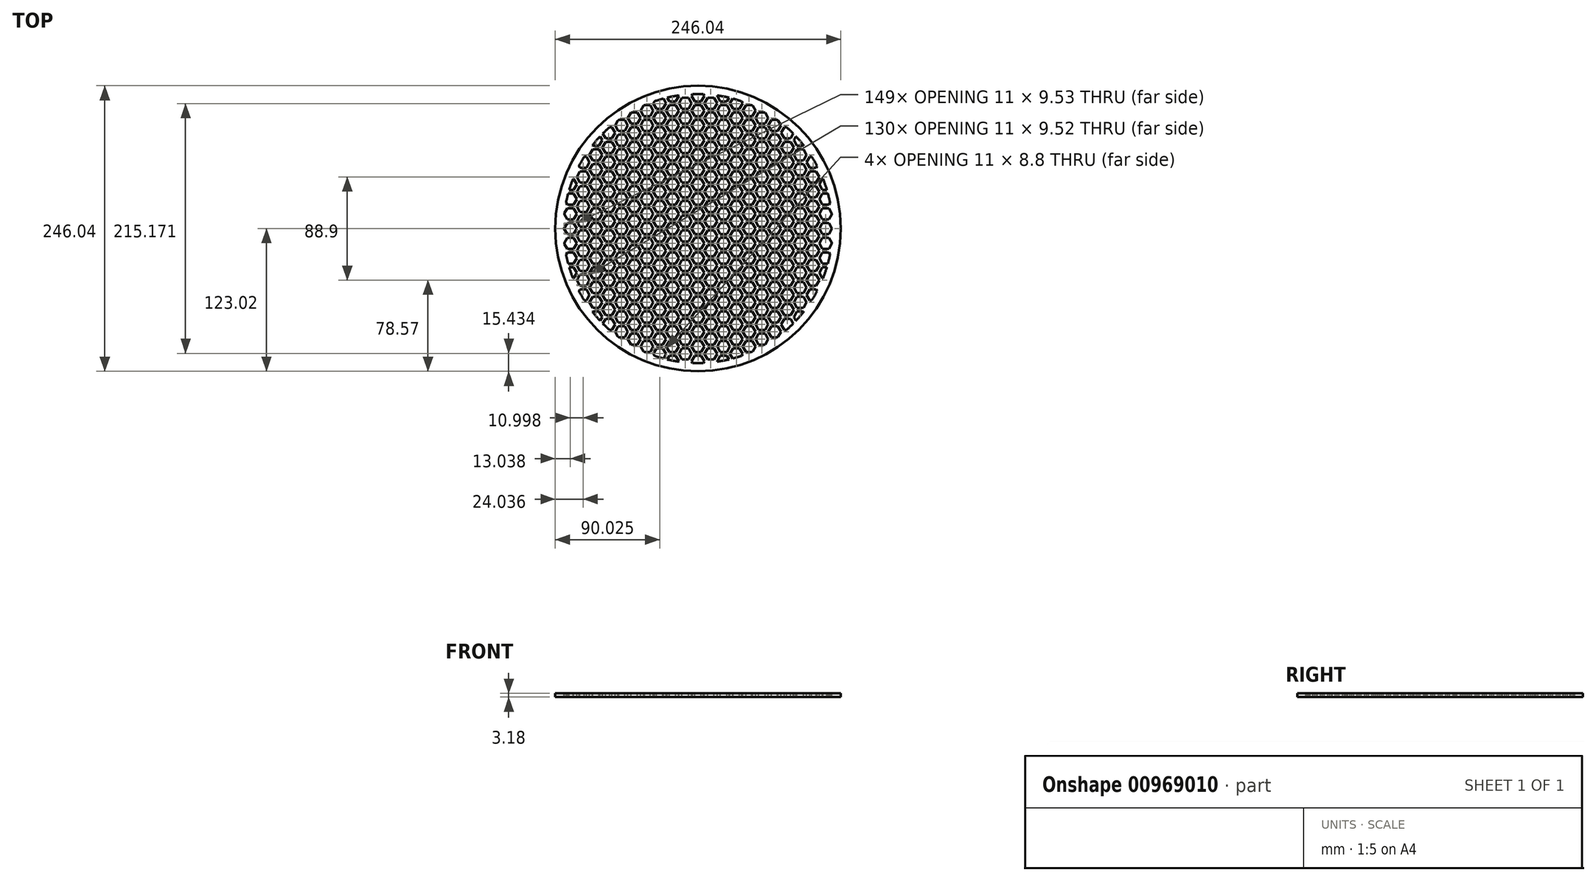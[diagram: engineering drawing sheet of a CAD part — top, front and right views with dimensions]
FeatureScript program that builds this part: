
annotation { "Feature Type Name" : "Feature", "Feature Type Description" : "" }
export const myFeature = defineFeature(function(context is Context, id is Id, definition is map)
    precondition{}
    {
        {
            var Q0;
            Q0=qCreatedBy(makeId("Top.planeOp"),FACE);
            var sketch = newSketch(context, id + "F0", { "sketchPlane" : qUnion([Q0])});
            skCircle(sketch, "E0", {"center": v(0, 0) * mm, "radius": 123.02 * mm});
            skSolve(sketch);
        }
        {
            var Q0;
            Q0=qSketchRegion(id+"F0",true);
            extrude(context, id + "F1", {"entities" : qUnion([Q0]), "depth" : 3.17 * mm, "offsetDistance" : 25.4 * mm});
        }
        {
            var Q0;
            Q0=makeQuery(id+"F1.opExtrude","CAP_FACE",FACE,{"disambiguationData":[OSD([sQuery(id+"F0.wireOp",EDGE,"E0")])],"isStart":false});
            var sketch = newSketch(context, id + "F2", { "sketchPlane" : qUnion([Q0])});
            skCircle(sketch, "E1.cCircle", {"center": v(-120.98, -120.65) * mm, "radius": 4.76 * mm, "construction": true});
            skLineSegment(sketch, "E1.0", {"start": v(-123.73, -115.89) * mm, "end": v(-118.23, -115.89) * mm});
            skLineSegment(sketch, "E1.1", {"start": v(-118.23, -115.89) * mm, "end": v(-115.48, -120.65) * mm});
            skLineSegment(sketch, "E1.2", {"start": v(-115.48, -120.65) * mm, "end": v(-118.23, -125.41) * mm});
            skLineSegment(sketch, "E1.3", {"start": v(-118.23, -125.41) * mm, "end": v(-123.73, -125.41) * mm});
            skLineSegment(sketch, "E1.4", {"start": v(-123.73, -125.41) * mm, "end": v(-126.48, -120.65) * mm});
            skLineSegment(sketch, "E1.5", {"start": v(-126.48, -120.65) * mm, "end": v(-123.73, -115.89) * mm});
            skPoint(sketch, "E1.0.midPoint", {"position": v(-120.98, -115.89) * mm});
            skCircle(sketch, "E2.cCircle", {"center": v(-109.98, -114.3) * mm, "radius": 4.76 * mm, "construction": true});
            skLineSegment(sketch, "E2.0", {"start": v(-112.73, -109.54) * mm, "end": v(-107.23, -109.54) * mm});
            skLineSegment(sketch, "E2.1", {"start": v(-107.23, -109.54) * mm, "end": v(-104.48, -114.3) * mm});
            skLineSegment(sketch, "E2.2", {"start": v(-104.48, -114.3) * mm, "end": v(-107.23, -119.06) * mm});
            skLineSegment(sketch, "E2.3", {"start": v(-107.23, -119.06) * mm, "end": v(-112.73, -119.06) * mm});
            skLineSegment(sketch, "E2.4", {"start": v(-112.73, -119.06) * mm, "end": v(-115.48, -114.3) * mm});
            skLineSegment(sketch, "E2.5", {"start": v(-115.48, -114.3) * mm, "end": v(-112.73, -109.54) * mm});
            skPoint(sketch, "E2.0.midPoint", {"position": v(-109.98, -109.54) * mm});
            skLineSegment(sketch, "E3.0.1.0", {"start": v(-123.73, -103.19) * mm, "end": v(-118.23, -103.19) * mm});
            skLineSegment(sketch, "E3.0.1.1", {"start": v(-118.23, -103.19) * mm, "end": v(-115.48, -107.95) * mm});
            skLineSegment(sketch, "E3.0.1.2", {"start": v(-115.48, -107.95) * mm, "end": v(-118.23, -112.71) * mm});
            skCircle(sketch, "E3.0.1.3", {"center": v(-120.98, -107.95) * mm, "radius": 4.76 * mm, "construction": true});
            skLineSegment(sketch, "E3.0.1.4", {"start": v(-118.23, -112.71) * mm, "end": v(-123.73, -112.71) * mm});
            skLineSegment(sketch, "E3.0.1.5", {"start": v(-123.73, -112.71) * mm, "end": v(-126.48, -107.95) * mm});
            skLineSegment(sketch, "E3.0.1.6", {"start": v(-126.48, -107.95) * mm, "end": v(-123.73, -103.19) * mm});
            skLineSegment(sketch, "E3.0.2.0", {"start": v(-123.73, -90.49) * mm, "end": v(-118.23, -90.49) * mm});
            skLineSegment(sketch, "E3.0.2.1", {"start": v(-118.23, -90.49) * mm, "end": v(-115.48, -95.25) * mm});
            skLineSegment(sketch, "E3.0.2.2", {"start": v(-115.48, -95.25) * mm, "end": v(-118.23, -100.01) * mm});
            skCircle(sketch, "E3.0.2.3", {"center": v(-120.98, -95.25) * mm, "radius": 4.76 * mm, "construction": true});
            skLineSegment(sketch, "E3.0.2.4", {"start": v(-118.23, -100.01) * mm, "end": v(-123.73, -100.01) * mm});
            skLineSegment(sketch, "E3.0.2.5", {"start": v(-123.73, -100.01) * mm, "end": v(-126.48, -95.25) * mm});
            skLineSegment(sketch, "E3.0.2.6", {"start": v(-126.48, -95.25) * mm, "end": v(-123.73, -90.49) * mm});
            skLineSegment(sketch, "E3.1.0.0", {"start": v(-101.73, -115.89) * mm, "end": v(-96.23, -115.89) * mm});
            skLineSegment(sketch, "E3.1.0.1", {"start": v(-96.23, -115.89) * mm, "end": v(-93.48, -120.65) * mm});
            skLineSegment(sketch, "E3.1.0.2", {"start": v(-93.48, -120.65) * mm, "end": v(-96.23, -125.41) * mm});
            skCircle(sketch, "E3.1.0.3", {"center": v(-98.98, -120.65) * mm, "radius": 4.76 * mm, "construction": true});
            skLineSegment(sketch, "E3.1.0.4", {"start": v(-96.23, -125.41) * mm, "end": v(-101.73, -125.41) * mm});
            skLineSegment(sketch, "E3.1.0.5", {"start": v(-101.73, -125.41) * mm, "end": v(-104.48, -120.65) * mm});
            skLineSegment(sketch, "E3.1.0.6", {"start": v(-104.48, -120.65) * mm, "end": v(-101.73, -115.89) * mm});
            skLineSegment(sketch, "E3.1.1.0", {"start": v(-101.73, -103.19) * mm, "end": v(-96.23, -103.19) * mm});
            skLineSegment(sketch, "E3.1.1.1", {"start": v(-96.23, -103.19) * mm, "end": v(-93.48, -107.95) * mm});
            skLineSegment(sketch, "E3.1.1.2", {"start": v(-93.48, -107.95) * mm, "end": v(-96.23, -112.71) * mm});
            skCircle(sketch, "E3.1.1.3", {"center": v(-98.98, -107.95) * mm, "radius": 4.76 * mm, "construction": true});
            skLineSegment(sketch, "E3.1.1.4", {"start": v(-96.23, -112.71) * mm, "end": v(-101.73, -112.71) * mm});
            skLineSegment(sketch, "E3.1.1.5", {"start": v(-101.73, -112.71) * mm, "end": v(-104.48, -107.95) * mm});
            skLineSegment(sketch, "E3.1.1.6", {"start": v(-104.48, -107.95) * mm, "end": v(-101.73, -103.19) * mm});
            skLineSegment(sketch, "E3.1.2.0", {"start": v(-101.73, -90.49) * mm, "end": v(-96.23, -90.49) * mm});
            skLineSegment(sketch, "E3.1.2.1", {"start": v(-96.23, -90.49) * mm, "end": v(-93.48, -95.25) * mm});
            skLineSegment(sketch, "E3.1.2.2", {"start": v(-93.48, -95.25) * mm, "end": v(-96.23, -100.01) * mm});
            skCircle(sketch, "E3.1.2.3", {"center": v(-98.98, -95.25) * mm, "radius": 4.76 * mm, "construction": true});
            skLineSegment(sketch, "E3.1.2.4", {"start": v(-96.23, -100.01) * mm, "end": v(-101.73, -100.01) * mm});
            skLineSegment(sketch, "E3.1.2.5", {"start": v(-101.73, -100.01) * mm, "end": v(-104.48, -95.25) * mm});
            skLineSegment(sketch, "E3.1.2.6", {"start": v(-104.48, -95.25) * mm, "end": v(-101.73, -90.49) * mm});
            skLineSegment(sketch, "E3.2.0.0", {"start": v(-79.74, -115.89) * mm, "end": v(-74.24, -115.89) * mm});
            skLineSegment(sketch, "E3.2.0.1", {"start": v(-74.24, -115.89) * mm, "end": v(-71.49, -120.65) * mm});
            skLineSegment(sketch, "E3.2.0.2", {"start": v(-71.49, -120.65) * mm, "end": v(-74.24, -125.41) * mm});
            skCircle(sketch, "E3.2.0.3", {"center": v(-76.99, -120.65) * mm, "radius": 4.76 * mm, "construction": true});
            skLineSegment(sketch, "E3.2.0.4", {"start": v(-74.24, -125.41) * mm, "end": v(-79.74, -125.41) * mm});
            skLineSegment(sketch, "E3.2.0.5", {"start": v(-79.74, -125.41) * mm, "end": v(-82.49, -120.65) * mm});
            skLineSegment(sketch, "E3.2.0.6", {"start": v(-82.49, -120.65) * mm, "end": v(-79.74, -115.89) * mm});
            skLineSegment(sketch, "E3.2.1.0", {"start": v(-79.74, -103.19) * mm, "end": v(-74.24, -103.19) * mm});
            skLineSegment(sketch, "E3.2.1.1", {"start": v(-74.24, -103.19) * mm, "end": v(-71.49, -107.95) * mm});
            skLineSegment(sketch, "E3.2.1.2", {"start": v(-71.49, -107.95) * mm, "end": v(-74.24, -112.71) * mm});
            skCircle(sketch, "E3.2.1.3", {"center": v(-76.99, -107.95) * mm, "radius": 4.76 * mm, "construction": true});
            skLineSegment(sketch, "E3.2.1.4", {"start": v(-74.24, -112.71) * mm, "end": v(-79.74, -112.71) * mm});
            skLineSegment(sketch, "E3.2.1.5", {"start": v(-79.74, -112.71) * mm, "end": v(-82.49, -107.95) * mm});
            skLineSegment(sketch, "E3.2.1.6", {"start": v(-82.49, -107.95) * mm, "end": v(-79.74, -103.19) * mm});
            skLineSegment(sketch, "E3.2.2.0", {"start": v(-79.74, -90.49) * mm, "end": v(-74.24, -90.49) * mm});
            skLineSegment(sketch, "E3.2.2.1", {"start": v(-74.24, -90.49) * mm, "end": v(-71.49, -95.25) * mm});
            skLineSegment(sketch, "E3.2.2.2", {"start": v(-71.49, -95.25) * mm, "end": v(-74.24, -100.01) * mm});
            skCircle(sketch, "E3.2.2.3", {"center": v(-76.99, -95.25) * mm, "radius": 4.76 * mm, "construction": true});
            skLineSegment(sketch, "E3.2.2.4", {"start": v(-74.24, -100.01) * mm, "end": v(-79.74, -100.01) * mm});
            skLineSegment(sketch, "E3.2.2.5", {"start": v(-79.74, -100.01) * mm, "end": v(-82.49, -95.25) * mm});
            skLineSegment(sketch, "E3.2.2.6", {"start": v(-82.49, -95.25) * mm, "end": v(-79.74, -90.49) * mm});
            skLineSegment(sketch, "E3.direction1", {"start": v(-123.73, -125.41) * mm, "end": v(-101.73, -125.41) * mm, "construction": true});
            skLineSegment(sketch, "E3.direction2", {"start": v(-123.73, -125.41) * mm, "end": v(-123.73, -112.71) * mm, "construction": true});
            skLineSegment(sketch, "E4.0.0.3", {"start": v(-123.73, -77.79) * mm, "end": v(-118.23, -77.79) * mm});
            skLineSegment(sketch, "E4.3.0.3", {"start": v(-118.23, -77.79) * mm, "end": v(-115.48, -82.55) * mm});
            skLineSegment(sketch, "E4.6.0.3", {"start": v(-115.48, -82.55) * mm, "end": v(-118.23, -87.31) * mm});
            skCircle(sketch, "E4.9.0.3", {"center": v(-120.98, -82.55) * mm, "radius": 4.76 * mm, "construction": true});
            skLineSegment(sketch, "E4.11.0.3", {"start": v(-118.23, -87.31) * mm, "end": v(-123.73, -87.31) * mm});
            skLineSegment(sketch, "E4.14.0.3", {"start": v(-123.73, -87.31) * mm, "end": v(-126.48, -82.55) * mm});
            skLineSegment(sketch, "E4.17.0.3", {"start": v(-126.48, -82.55) * mm, "end": v(-123.73, -77.79) * mm});
            skLineSegment(sketch, "E4.0.1.3", {"start": v(-101.73, -77.79) * mm, "end": v(-96.23, -77.79) * mm});
            skLineSegment(sketch, "E4.3.1.3", {"start": v(-96.23, -77.79) * mm, "end": v(-93.48, -82.55) * mm});
            skLineSegment(sketch, "E4.6.1.3", {"start": v(-93.48, -82.55) * mm, "end": v(-96.23, -87.31) * mm});
            skCircle(sketch, "E4.9.1.3", {"center": v(-98.98, -82.55) * mm, "radius": 4.76 * mm, "construction": true});
            skLineSegment(sketch, "E4.11.1.3", {"start": v(-96.23, -87.31) * mm, "end": v(-101.73, -87.31) * mm});
            skLineSegment(sketch, "E4.14.1.3", {"start": v(-101.73, -87.31) * mm, "end": v(-104.48, -82.55) * mm});
            skLineSegment(sketch, "E4.17.1.3", {"start": v(-104.48, -82.55) * mm, "end": v(-101.73, -77.79) * mm});
            skLineSegment(sketch, "E4.0.2.3", {"start": v(-79.74, -77.79) * mm, "end": v(-74.24, -77.79) * mm});
            skLineSegment(sketch, "E4.3.2.3", {"start": v(-74.24, -77.79) * mm, "end": v(-71.49, -82.55) * mm});
            skLineSegment(sketch, "E4.6.2.3", {"start": v(-71.49, -82.55) * mm, "end": v(-74.24, -87.31) * mm});
            skCircle(sketch, "E4.9.2.3", {"center": v(-76.99, -82.55) * mm, "radius": 4.76 * mm, "construction": true});
            skLineSegment(sketch, "E4.11.2.3", {"start": v(-74.24, -87.31) * mm, "end": v(-79.74, -87.31) * mm});
            skLineSegment(sketch, "E4.14.2.3", {"start": v(-79.74, -87.31) * mm, "end": v(-82.49, -82.55) * mm});
            skLineSegment(sketch, "E4.17.2.3", {"start": v(-82.49, -82.55) * mm, "end": v(-79.74, -77.79) * mm});
            skCircle(sketch, "E5.0.1.0", {"center": v(-109.98, -101.6) * mm, "radius": 4.76 * mm, "construction": true});
            skLineSegment(sketch, "E5.0.1.1", {"start": v(-115.48, -101.6) * mm, "end": v(-112.73, -96.84) * mm});
            skLineSegment(sketch, "E5.0.1.2", {"start": v(-112.73, -96.84) * mm, "end": v(-107.23, -96.84) * mm});
            skLineSegment(sketch, "E5.0.1.3", {"start": v(-107.23, -96.84) * mm, "end": v(-104.48, -101.6) * mm});
            skLineSegment(sketch, "E5.0.1.4", {"start": v(-104.48, -101.6) * mm, "end": v(-107.23, -106.36) * mm});
            skLineSegment(sketch, "E5.0.1.5", {"start": v(-107.23, -106.36) * mm, "end": v(-112.73, -106.36) * mm});
            skLineSegment(sketch, "E5.0.1.6", {"start": v(-112.73, -106.36) * mm, "end": v(-115.48, -101.6) * mm});
            skCircle(sketch, "E5.0.2.0", {"center": v(-109.98, -88.9) * mm, "radius": 4.76 * mm, "construction": true});
            skLineSegment(sketch, "E5.0.2.1", {"start": v(-115.48, -88.9) * mm, "end": v(-112.73, -84.14) * mm});
            skLineSegment(sketch, "E5.0.2.2", {"start": v(-112.73, -84.14) * mm, "end": v(-107.23, -84.14) * mm});
            skLineSegment(sketch, "E5.0.2.3", {"start": v(-107.23, -84.14) * mm, "end": v(-104.48, -88.9) * mm});
            skLineSegment(sketch, "E5.0.2.4", {"start": v(-104.48, -88.9) * mm, "end": v(-107.23, -93.66) * mm});
            skLineSegment(sketch, "E5.0.2.5", {"start": v(-107.23, -93.66) * mm, "end": v(-112.73, -93.66) * mm});
            skLineSegment(sketch, "E5.0.2.6", {"start": v(-112.73, -93.66) * mm, "end": v(-115.48, -88.9) * mm});
            skCircle(sketch, "E5.0.3.0", {"center": v(-109.98, -76.2) * mm, "radius": 4.76 * mm, "construction": true});
            skLineSegment(sketch, "E5.0.3.1", {"start": v(-115.48, -76.2) * mm, "end": v(-112.73, -71.44) * mm});
            skLineSegment(sketch, "E5.0.3.2", {"start": v(-112.73, -71.44) * mm, "end": v(-107.23, -71.44) * mm});
            skLineSegment(sketch, "E5.0.3.3", {"start": v(-107.23, -71.44) * mm, "end": v(-104.48, -76.2) * mm});
            skLineSegment(sketch, "E5.0.3.4", {"start": v(-104.48, -76.2) * mm, "end": v(-107.23, -80.96) * mm});
            skLineSegment(sketch, "E5.0.3.5", {"start": v(-107.23, -80.96) * mm, "end": v(-112.73, -80.96) * mm});
            skLineSegment(sketch, "E5.0.3.6", {"start": v(-112.73, -80.96) * mm, "end": v(-115.48, -76.2) * mm});
            skCircle(sketch, "E5.1.0.0", {"center": v(-87.99, -114.3) * mm, "radius": 4.76 * mm, "construction": true});
            skLineSegment(sketch, "E5.1.0.1", {"start": v(-93.48, -114.3) * mm, "end": v(-90.74, -109.54) * mm});
            skLineSegment(sketch, "E5.1.0.2", {"start": v(-90.74, -109.54) * mm, "end": v(-85.24, -109.54) * mm});
            skLineSegment(sketch, "E5.1.0.3", {"start": v(-85.24, -109.54) * mm, "end": v(-82.49, -114.3) * mm});
            skLineSegment(sketch, "E5.1.0.4", {"start": v(-82.49, -114.3) * mm, "end": v(-85.24, -119.06) * mm});
            skLineSegment(sketch, "E5.1.0.5", {"start": v(-85.24, -119.06) * mm, "end": v(-90.74, -119.06) * mm});
            skLineSegment(sketch, "E5.1.0.6", {"start": v(-90.74, -119.06) * mm, "end": v(-93.48, -114.3) * mm});
            skCircle(sketch, "E5.1.1.0", {"center": v(-87.99, -101.6) * mm, "radius": 4.76 * mm, "construction": true});
            skLineSegment(sketch, "E5.1.1.1", {"start": v(-93.48, -101.6) * mm, "end": v(-90.74, -96.84) * mm});
            skLineSegment(sketch, "E5.1.1.2", {"start": v(-90.74, -96.84) * mm, "end": v(-85.24, -96.84) * mm});
            skLineSegment(sketch, "E5.1.1.3", {"start": v(-85.24, -96.84) * mm, "end": v(-82.49, -101.6) * mm});
            skLineSegment(sketch, "E5.1.1.4", {"start": v(-82.49, -101.6) * mm, "end": v(-85.24, -106.36) * mm});
            skLineSegment(sketch, "E5.1.1.5", {"start": v(-85.24, -106.36) * mm, "end": v(-90.74, -106.36) * mm});
            skLineSegment(sketch, "E5.1.1.6", {"start": v(-90.74, -106.36) * mm, "end": v(-93.48, -101.6) * mm});
            skCircle(sketch, "E5.1.2.0", {"center": v(-87.99, -88.9) * mm, "radius": 4.76 * mm, "construction": true});
            skLineSegment(sketch, "E5.1.2.1", {"start": v(-93.48, -88.9) * mm, "end": v(-90.74, -84.14) * mm});
            skLineSegment(sketch, "E5.1.2.2", {"start": v(-90.74, -84.14) * mm, "end": v(-85.24, -84.14) * mm});
            skLineSegment(sketch, "E5.1.2.3", {"start": v(-85.24, -84.14) * mm, "end": v(-82.49, -88.9) * mm});
            skLineSegment(sketch, "E5.1.2.4", {"start": v(-82.49, -88.9) * mm, "end": v(-85.24, -93.66) * mm});
            skLineSegment(sketch, "E5.1.2.5", {"start": v(-85.24, -93.66) * mm, "end": v(-90.74, -93.66) * mm});
            skLineSegment(sketch, "E5.1.2.6", {"start": v(-90.74, -93.66) * mm, "end": v(-93.48, -88.9) * mm});
            skCircle(sketch, "E5.1.3.0", {"center": v(-87.99, -76.2) * mm, "radius": 4.76 * mm, "construction": true});
            skLineSegment(sketch, "E5.1.3.1", {"start": v(-93.48, -76.2) * mm, "end": v(-90.74, -71.44) * mm});
            skLineSegment(sketch, "E5.1.3.2", {"start": v(-90.74, -71.44) * mm, "end": v(-85.24, -71.44) * mm});
            skLineSegment(sketch, "E5.1.3.3", {"start": v(-85.24, -71.44) * mm, "end": v(-82.49, -76.2) * mm});
            skLineSegment(sketch, "E5.1.3.4", {"start": v(-82.49, -76.2) * mm, "end": v(-85.24, -80.96) * mm});
            skLineSegment(sketch, "E5.1.3.5", {"start": v(-85.24, -80.96) * mm, "end": v(-90.74, -80.96) * mm});
            skLineSegment(sketch, "E5.1.3.6", {"start": v(-90.74, -80.96) * mm, "end": v(-93.48, -76.2) * mm});
            skLineSegment(sketch, "E5.direction1", {"start": v(-112.73, -119.06) * mm, "end": v(-90.74, -119.06) * mm, "construction": true});
            skLineSegment(sketch, "E5.direction2", {"start": v(-112.73, -119.06) * mm, "end": v(-112.73, -106.36) * mm, "construction": true});
            skLineSegment(sketch, "E6.0.3.0", {"start": v(-57.74, -115.89) * mm, "end": v(-52.24, -115.89) * mm});
            skLineSegment(sketch, "E6.3.3.0", {"start": v(-52.24, -115.89) * mm, "end": v(-49.5, -120.65) * mm});
            skLineSegment(sketch, "E6.6.3.0", {"start": v(-49.5, -120.65) * mm, "end": v(-52.24, -125.41) * mm});
            skCircle(sketch, "E6.9.3.0", {"center": v(-55, -120.65) * mm, "radius": 4.76 * mm, "construction": true});
            skLineSegment(sketch, "E6.11.3.0", {"start": v(-52.24, -125.41) * mm, "end": v(-57.74, -125.41) * mm});
            skLineSegment(sketch, "E6.14.3.0", {"start": v(-57.74, -125.41) * mm, "end": v(-60.5, -120.65) * mm});
            skLineSegment(sketch, "E6.17.3.0", {"start": v(-60.5, -120.65) * mm, "end": v(-57.74, -115.89) * mm});
            skLineSegment(sketch, "E6.0.3.1", {"start": v(-57.74, -103.19) * mm, "end": v(-52.24, -103.19) * mm});
            skLineSegment(sketch, "E6.3.3.1", {"start": v(-52.24, -103.19) * mm, "end": v(-49.5, -107.95) * mm});
            skLineSegment(sketch, "E6.6.3.1", {"start": v(-49.5, -107.95) * mm, "end": v(-52.24, -112.71) * mm});
            skCircle(sketch, "E6.9.3.1", {"center": v(-55, -107.95) * mm, "radius": 4.76 * mm, "construction": true});
            skLineSegment(sketch, "E6.11.3.1", {"start": v(-52.24, -112.71) * mm, "end": v(-57.74, -112.71) * mm});
            skLineSegment(sketch, "E6.14.3.1", {"start": v(-57.74, -112.71) * mm, "end": v(-60.5, -107.95) * mm});
            skLineSegment(sketch, "E6.17.3.1", {"start": v(-60.5, -107.95) * mm, "end": v(-57.74, -103.19) * mm});
            skLineSegment(sketch, "E6.0.3.2", {"start": v(-57.74, -90.49) * mm, "end": v(-52.24, -90.49) * mm});
            skLineSegment(sketch, "E6.3.3.2", {"start": v(-52.24, -90.49) * mm, "end": v(-49.5, -95.25) * mm});
            skLineSegment(sketch, "E6.6.3.2", {"start": v(-49.5, -95.25) * mm, "end": v(-52.24, -100.01) * mm});
            skCircle(sketch, "E6.9.3.2", {"center": v(-55, -95.25) * mm, "radius": 4.76 * mm, "construction": true});
            skLineSegment(sketch, "E6.11.3.2", {"start": v(-52.24, -100.01) * mm, "end": v(-57.74, -100.01) * mm});
            skLineSegment(sketch, "E6.14.3.2", {"start": v(-57.74, -100.01) * mm, "end": v(-60.5, -95.25) * mm});
            skLineSegment(sketch, "E6.17.3.2", {"start": v(-60.5, -95.25) * mm, "end": v(-57.74, -90.49) * mm});
            skLineSegment(sketch, "E6.0.3.3", {"start": v(-57.74, -77.79) * mm, "end": v(-52.24, -77.79) * mm});
            skLineSegment(sketch, "E6.3.3.3", {"start": v(-52.24, -77.79) * mm, "end": v(-49.5, -82.55) * mm});
            skLineSegment(sketch, "E6.6.3.3", {"start": v(-49.5, -82.55) * mm, "end": v(-52.24, -87.31) * mm});
            skCircle(sketch, "E6.9.3.3", {"center": v(-55, -82.55) * mm, "radius": 4.76 * mm, "construction": true});
            skLineSegment(sketch, "E6.11.3.3", {"start": v(-52.24, -87.31) * mm, "end": v(-57.74, -87.31) * mm});
            skLineSegment(sketch, "E6.14.3.3", {"start": v(-57.74, -87.31) * mm, "end": v(-60.5, -82.55) * mm});
            skLineSegment(sketch, "E6.17.3.3", {"start": v(-60.5, -82.55) * mm, "end": v(-57.74, -77.79) * mm});
            skLineSegment(sketch, "E6.0.4.0", {"start": v(-35.74, -115.89) * mm, "end": v(-30.25, -115.89) * mm});
            skLineSegment(sketch, "E6.3.4.0", {"start": v(-30.25, -115.89) * mm, "end": v(-27.5, -120.65) * mm});
            skLineSegment(sketch, "E6.6.4.0", {"start": v(-27.5, -120.65) * mm, "end": v(-30.25, -125.41) * mm});
            skCircle(sketch, "E6.9.4.0", {"center": v(-33, -120.65) * mm, "radius": 4.76 * mm, "construction": true});
            skLineSegment(sketch, "E6.11.4.0", {"start": v(-30.25, -125.41) * mm, "end": v(-35.74, -125.41) * mm});
            skLineSegment(sketch, "E6.14.4.0", {"start": v(-35.74, -125.41) * mm, "end": v(-38.5, -120.65) * mm});
            skLineSegment(sketch, "E6.17.4.0", {"start": v(-38.5, -120.65) * mm, "end": v(-35.74, -115.89) * mm});
            skLineSegment(sketch, "E6.0.4.1", {"start": v(-35.74, -103.19) * mm, "end": v(-30.25, -103.19) * mm});
            skLineSegment(sketch, "E6.3.4.1", {"start": v(-30.25, -103.19) * mm, "end": v(-27.5, -107.95) * mm});
            skLineSegment(sketch, "E6.6.4.1", {"start": v(-27.5, -107.95) * mm, "end": v(-30.25, -112.71) * mm});
            skCircle(sketch, "E6.9.4.1", {"center": v(-33, -107.95) * mm, "radius": 4.76 * mm, "construction": true});
            skLineSegment(sketch, "E6.11.4.1", {"start": v(-30.25, -112.71) * mm, "end": v(-35.74, -112.71) * mm});
            skLineSegment(sketch, "E6.14.4.1", {"start": v(-35.74, -112.71) * mm, "end": v(-38.5, -107.95) * mm});
            skLineSegment(sketch, "E6.17.4.1", {"start": v(-38.5, -107.95) * mm, "end": v(-35.74, -103.19) * mm});
            skLineSegment(sketch, "E6.0.4.2", {"start": v(-35.74, -90.49) * mm, "end": v(-30.25, -90.49) * mm});
            skLineSegment(sketch, "E6.3.4.2", {"start": v(-30.25, -90.49) * mm, "end": v(-27.5, -95.25) * mm});
            skLineSegment(sketch, "E6.6.4.2", {"start": v(-27.5, -95.25) * mm, "end": v(-30.25, -100.01) * mm});
            skCircle(sketch, "E6.9.4.2", {"center": v(-33, -95.25) * mm, "radius": 4.76 * mm, "construction": true});
            skLineSegment(sketch, "E6.11.4.2", {"start": v(-30.25, -100.01) * mm, "end": v(-35.74, -100.01) * mm});
            skLineSegment(sketch, "E6.14.4.2", {"start": v(-35.74, -100.01) * mm, "end": v(-38.5, -95.25) * mm});
            skLineSegment(sketch, "E6.17.4.2", {"start": v(-38.5, -95.25) * mm, "end": v(-35.74, -90.49) * mm});
            skLineSegment(sketch, "E6.0.4.3", {"start": v(-35.74, -77.79) * mm, "end": v(-30.25, -77.79) * mm});
            skLineSegment(sketch, "E6.3.4.3", {"start": v(-30.25, -77.79) * mm, "end": v(-27.5, -82.55) * mm});
            skLineSegment(sketch, "E6.6.4.3", {"start": v(-27.5, -82.55) * mm, "end": v(-30.25, -87.31) * mm});
            skCircle(sketch, "E6.9.4.3", {"center": v(-33, -82.55) * mm, "radius": 4.76 * mm, "construction": true});
            skLineSegment(sketch, "E6.11.4.3", {"start": v(-30.25, -87.31) * mm, "end": v(-35.74, -87.31) * mm});
            skLineSegment(sketch, "E6.14.4.3", {"start": v(-35.74, -87.31) * mm, "end": v(-38.5, -82.55) * mm});
            skLineSegment(sketch, "E6.17.4.3", {"start": v(-38.5, -82.55) * mm, "end": v(-35.74, -77.79) * mm});
            skLineSegment(sketch, "E6.0.5.0", {"start": v(-13.75, -115.89) * mm, "end": v(-8.25, -115.89) * mm});
            skLineSegment(sketch, "E6.3.5.0", {"start": v(-8.25, -115.89) * mm, "end": v(-5.5, -120.65) * mm});
            skLineSegment(sketch, "E6.6.5.0", {"start": v(-5.5, -120.65) * mm, "end": v(-8.25, -125.41) * mm});
            skCircle(sketch, "E6.9.5.0", {"center": v(-11, -120.65) * mm, "radius": 4.76 * mm, "construction": true});
            skLineSegment(sketch, "E6.11.5.0", {"start": v(-8.25, -125.41) * mm, "end": v(-13.75, -125.41) * mm});
            skLineSegment(sketch, "E6.14.5.0", {"start": v(-13.75, -125.41) * mm, "end": v(-16.5, -120.65) * mm});
            skLineSegment(sketch, "E6.17.5.0", {"start": v(-16.5, -120.65) * mm, "end": v(-13.75, -115.89) * mm});
            skLineSegment(sketch, "E6.0.5.1", {"start": v(-13.75, -103.19) * mm, "end": v(-8.25, -103.19) * mm});
            skLineSegment(sketch, "E6.3.5.1", {"start": v(-8.25, -103.19) * mm, "end": v(-5.5, -107.95) * mm});
            skLineSegment(sketch, "E6.6.5.1", {"start": v(-5.5, -107.95) * mm, "end": v(-8.25, -112.71) * mm});
            skCircle(sketch, "E6.9.5.1", {"center": v(-11, -107.95) * mm, "radius": 4.76 * mm, "construction": true});
            skLineSegment(sketch, "E6.11.5.1", {"start": v(-8.25, -112.71) * mm, "end": v(-13.75, -112.71) * mm});
            skLineSegment(sketch, "E6.14.5.1", {"start": v(-13.75, -112.71) * mm, "end": v(-16.5, -107.95) * mm});
            skLineSegment(sketch, "E6.17.5.1", {"start": v(-16.5, -107.95) * mm, "end": v(-13.75, -103.19) * mm});
            skLineSegment(sketch, "E6.0.5.2", {"start": v(-13.75, -90.49) * mm, "end": v(-8.25, -90.49) * mm});
            skLineSegment(sketch, "E6.3.5.2", {"start": v(-8.25, -90.49) * mm, "end": v(-5.5, -95.25) * mm});
            skLineSegment(sketch, "E6.6.5.2", {"start": v(-5.5, -95.25) * mm, "end": v(-8.25, -100.01) * mm});
            skCircle(sketch, "E6.9.5.2", {"center": v(-11, -95.25) * mm, "radius": 4.76 * mm, "construction": true});
            skLineSegment(sketch, "E6.11.5.2", {"start": v(-8.25, -100.01) * mm, "end": v(-13.75, -100.01) * mm});
            skLineSegment(sketch, "E6.14.5.2", {"start": v(-13.75, -100.01) * mm, "end": v(-16.5, -95.25) * mm});
            skLineSegment(sketch, "E6.17.5.2", {"start": v(-16.5, -95.25) * mm, "end": v(-13.75, -90.49) * mm});
            skLineSegment(sketch, "E6.0.5.3", {"start": v(-13.75, -77.79) * mm, "end": v(-8.25, -77.79) * mm});
            skLineSegment(sketch, "E6.3.5.3", {"start": v(-8.25, -77.79) * mm, "end": v(-5.5, -82.55) * mm});
            skLineSegment(sketch, "E6.6.5.3", {"start": v(-5.5, -82.55) * mm, "end": v(-8.25, -87.31) * mm});
            skCircle(sketch, "E6.9.5.3", {"center": v(-11, -82.55) * mm, "radius": 4.76 * mm, "construction": true});
            skLineSegment(sketch, "E6.11.5.3", {"start": v(-8.25, -87.31) * mm, "end": v(-13.75, -87.31) * mm});
            skLineSegment(sketch, "E6.14.5.3", {"start": v(-13.75, -87.31) * mm, "end": v(-16.5, -82.55) * mm});
            skLineSegment(sketch, "E6.17.5.3", {"start": v(-16.5, -82.55) * mm, "end": v(-13.75, -77.79) * mm});
            skCircle(sketch, "E7.0.2.0", {"center": v(-65.99, -114.3) * mm, "radius": 4.76 * mm, "construction": true});
            skLineSegment(sketch, "E7.2.2.0", {"start": v(-71.49, -114.3) * mm, "end": v(-68.74, -109.54) * mm});
            skLineSegment(sketch, "E7.5.2.0", {"start": v(-68.74, -109.54) * mm, "end": v(-63.24, -109.54) * mm});
            skLineSegment(sketch, "E7.8.2.0", {"start": v(-63.24, -109.54) * mm, "end": v(-60.49, -114.3) * mm});
            skLineSegment(sketch, "E7.11.2.0", {"start": v(-60.49, -114.3) * mm, "end": v(-63.24, -119.06) * mm});
            skLineSegment(sketch, "E7.14.2.0", {"start": v(-63.24, -119.06) * mm, "end": v(-68.74, -119.06) * mm});
            skLineSegment(sketch, "E7.17.2.0", {"start": v(-68.74, -119.06) * mm, "end": v(-71.49, -114.3) * mm});
            skCircle(sketch, "E7.0.2.1", {"center": v(-65.99, -101.6) * mm, "radius": 4.76 * mm, "construction": true});
            skLineSegment(sketch, "E7.2.2.1", {"start": v(-71.49, -101.6) * mm, "end": v(-68.74, -96.84) * mm});
            skLineSegment(sketch, "E7.5.2.1", {"start": v(-68.74, -96.84) * mm, "end": v(-63.24, -96.84) * mm});
            skLineSegment(sketch, "E7.8.2.1", {"start": v(-63.24, -96.84) * mm, "end": v(-60.49, -101.6) * mm});
            skLineSegment(sketch, "E7.11.2.1", {"start": v(-60.49, -101.6) * mm, "end": v(-63.24, -106.36) * mm});
            skLineSegment(sketch, "E7.14.2.1", {"start": v(-63.24, -106.36) * mm, "end": v(-68.74, -106.36) * mm});
            skLineSegment(sketch, "E7.17.2.1", {"start": v(-68.74, -106.36) * mm, "end": v(-71.49, -101.6) * mm});
            skCircle(sketch, "E7.0.2.2", {"center": v(-65.99, -88.9) * mm, "radius": 4.76 * mm, "construction": true});
            skLineSegment(sketch, "E7.2.2.2", {"start": v(-71.49, -88.9) * mm, "end": v(-68.74, -84.14) * mm});
            skLineSegment(sketch, "E7.5.2.2", {"start": v(-68.74, -84.14) * mm, "end": v(-63.24, -84.14) * mm});
            skLineSegment(sketch, "E7.8.2.2", {"start": v(-63.24, -84.14) * mm, "end": v(-60.49, -88.9) * mm});
            skLineSegment(sketch, "E7.11.2.2", {"start": v(-60.49, -88.9) * mm, "end": v(-63.24, -93.66) * mm});
            skLineSegment(sketch, "E7.14.2.2", {"start": v(-63.24, -93.66) * mm, "end": v(-68.74, -93.66) * mm});
            skLineSegment(sketch, "E7.17.2.2", {"start": v(-68.74, -93.66) * mm, "end": v(-71.49, -88.9) * mm});
            skCircle(sketch, "E7.0.2.3", {"center": v(-65.99, -76.2) * mm, "radius": 4.76 * mm, "construction": true});
            skLineSegment(sketch, "E7.2.2.3", {"start": v(-71.49, -76.2) * mm, "end": v(-68.74, -71.44) * mm});
            skLineSegment(sketch, "E7.5.2.3", {"start": v(-68.74, -71.44) * mm, "end": v(-63.24, -71.44) * mm});
            skLineSegment(sketch, "E7.8.2.3", {"start": v(-63.24, -71.44) * mm, "end": v(-60.49, -76.2) * mm});
            skLineSegment(sketch, "E7.11.2.3", {"start": v(-60.49, -76.2) * mm, "end": v(-63.24, -80.96) * mm});
            skLineSegment(sketch, "E7.14.2.3", {"start": v(-63.24, -80.96) * mm, "end": v(-68.74, -80.96) * mm});
            skLineSegment(sketch, "E7.17.2.3", {"start": v(-68.74, -80.96) * mm, "end": v(-71.49, -76.2) * mm});
            skCircle(sketch, "E7.0.3.0", {"center": v(-44, -114.3) * mm, "radius": 4.76 * mm, "construction": true});
            skLineSegment(sketch, "E7.2.3.0", {"start": v(-49.5, -114.3) * mm, "end": v(-46.74, -109.54) * mm});
            skLineSegment(sketch, "E7.5.3.0", {"start": v(-46.74, -109.54) * mm, "end": v(-41.24, -109.54) * mm});
            skLineSegment(sketch, "E7.8.3.0", {"start": v(-41.24, -109.54) * mm, "end": v(-38.5, -114.3) * mm});
            skLineSegment(sketch, "E7.11.3.0", {"start": v(-38.5, -114.3) * mm, "end": v(-41.24, -119.06) * mm});
            skLineSegment(sketch, "E7.14.3.0", {"start": v(-41.24, -119.06) * mm, "end": v(-46.74, -119.06) * mm});
            skLineSegment(sketch, "E7.17.3.0", {"start": v(-46.74, -119.06) * mm, "end": v(-49.5, -114.3) * mm});
            skCircle(sketch, "E7.0.3.1", {"center": v(-44, -101.6) * mm, "radius": 4.76 * mm, "construction": true});
            skLineSegment(sketch, "E7.2.3.1", {"start": v(-49.5, -101.6) * mm, "end": v(-46.74, -96.84) * mm});
            skLineSegment(sketch, "E7.5.3.1", {"start": v(-46.74, -96.84) * mm, "end": v(-41.24, -96.84) * mm});
            skLineSegment(sketch, "E7.8.3.1", {"start": v(-41.24, -96.84) * mm, "end": v(-38.5, -101.6) * mm});
            skLineSegment(sketch, "E7.11.3.1", {"start": v(-38.5, -101.6) * mm, "end": v(-41.24, -106.36) * mm});
            skLineSegment(sketch, "E7.14.3.1", {"start": v(-41.24, -106.36) * mm, "end": v(-46.74, -106.36) * mm});
            skLineSegment(sketch, "E7.17.3.1", {"start": v(-46.74, -106.36) * mm, "end": v(-49.5, -101.6) * mm});
            skCircle(sketch, "E7.0.3.2", {"center": v(-44, -88.9) * mm, "radius": 4.76 * mm, "construction": true});
            skLineSegment(sketch, "E7.2.3.2", {"start": v(-49.5, -88.9) * mm, "end": v(-46.74, -84.14) * mm});
            skLineSegment(sketch, "E7.5.3.2", {"start": v(-46.74, -84.14) * mm, "end": v(-41.24, -84.14) * mm});
            skLineSegment(sketch, "E7.8.3.2", {"start": v(-41.24, -84.14) * mm, "end": v(-38.5, -88.9) * mm});
            skLineSegment(sketch, "E7.11.3.2", {"start": v(-38.5, -88.9) * mm, "end": v(-41.24, -93.66) * mm});
            skLineSegment(sketch, "E7.14.3.2", {"start": v(-41.24, -93.66) * mm, "end": v(-46.74, -93.66) * mm});
            skLineSegment(sketch, "E7.17.3.2", {"start": v(-46.74, -93.66) * mm, "end": v(-49.5, -88.9) * mm});
            skCircle(sketch, "E7.0.3.3", {"center": v(-44, -76.2) * mm, "radius": 4.76 * mm, "construction": true});
            skLineSegment(sketch, "E7.2.3.3", {"start": v(-49.5, -76.2) * mm, "end": v(-46.74, -71.44) * mm});
            skLineSegment(sketch, "E7.5.3.3", {"start": v(-46.74, -71.44) * mm, "end": v(-41.24, -71.44) * mm});
            skLineSegment(sketch, "E7.8.3.3", {"start": v(-41.24, -71.44) * mm, "end": v(-38.5, -76.2) * mm});
            skLineSegment(sketch, "E7.11.3.3", {"start": v(-38.5, -76.2) * mm, "end": v(-41.24, -80.96) * mm});
            skLineSegment(sketch, "E7.14.3.3", {"start": v(-41.24, -80.96) * mm, "end": v(-46.74, -80.96) * mm});
            skLineSegment(sketch, "E7.17.3.3", {"start": v(-46.74, -80.96) * mm, "end": v(-49.5, -76.2) * mm});
            skCircle(sketch, "E7.0.4.0", {"center": v(-22, -114.3) * mm, "radius": 4.76 * mm, "construction": true});
            skLineSegment(sketch, "E7.2.4.0", {"start": v(-27.5, -114.3) * mm, "end": v(-24.75, -109.54) * mm});
            skLineSegment(sketch, "E7.5.4.0", {"start": v(-24.75, -109.54) * mm, "end": v(-19.25, -109.54) * mm});
            skLineSegment(sketch, "E7.8.4.0", {"start": v(-19.25, -109.54) * mm, "end": v(-16.5, -114.3) * mm});
            skLineSegment(sketch, "E7.11.4.0", {"start": v(-16.5, -114.3) * mm, "end": v(-19.25, -119.06) * mm});
            skLineSegment(sketch, "E7.14.4.0", {"start": v(-19.25, -119.06) * mm, "end": v(-24.75, -119.06) * mm});
            skLineSegment(sketch, "E7.17.4.0", {"start": v(-24.75, -119.06) * mm, "end": v(-27.5, -114.3) * mm});
            skCircle(sketch, "E7.0.4.1", {"center": v(-22, -101.6) * mm, "radius": 4.76 * mm, "construction": true});
            skLineSegment(sketch, "E7.2.4.1", {"start": v(-27.5, -101.6) * mm, "end": v(-24.75, -96.84) * mm});
            skLineSegment(sketch, "E7.5.4.1", {"start": v(-24.75, -96.84) * mm, "end": v(-19.25, -96.84) * mm});
            skLineSegment(sketch, "E7.8.4.1", {"start": v(-19.25, -96.84) * mm, "end": v(-16.5, -101.6) * mm});
            skLineSegment(sketch, "E7.11.4.1", {"start": v(-16.5, -101.6) * mm, "end": v(-19.25, -106.36) * mm});
            skLineSegment(sketch, "E7.14.4.1", {"start": v(-19.25, -106.36) * mm, "end": v(-24.75, -106.36) * mm});
            skLineSegment(sketch, "E7.17.4.1", {"start": v(-24.75, -106.36) * mm, "end": v(-27.5, -101.6) * mm});
            skCircle(sketch, "E7.0.4.2", {"center": v(-22, -88.9) * mm, "radius": 4.76 * mm, "construction": true});
            skLineSegment(sketch, "E7.2.4.2", {"start": v(-27.5, -88.9) * mm, "end": v(-24.75, -84.14) * mm});
            skLineSegment(sketch, "E7.5.4.2", {"start": v(-24.75, -84.14) * mm, "end": v(-19.25, -84.14) * mm});
            skLineSegment(sketch, "E7.8.4.2", {"start": v(-19.25, -84.14) * mm, "end": v(-16.5, -88.9) * mm});
            skLineSegment(sketch, "E7.11.4.2", {"start": v(-16.5, -88.9) * mm, "end": v(-19.25, -93.66) * mm});
            skLineSegment(sketch, "E7.14.4.2", {"start": v(-19.25, -93.66) * mm, "end": v(-24.75, -93.66) * mm});
            skLineSegment(sketch, "E7.17.4.2", {"start": v(-24.75, -93.66) * mm, "end": v(-27.5, -88.9) * mm});
            skCircle(sketch, "E7.0.4.3", {"center": v(-22, -76.2) * mm, "radius": 4.76 * mm, "construction": true});
            skLineSegment(sketch, "E7.2.4.3", {"start": v(-27.5, -76.2) * mm, "end": v(-24.75, -71.44) * mm});
            skLineSegment(sketch, "E7.5.4.3", {"start": v(-24.75, -71.44) * mm, "end": v(-19.25, -71.44) * mm});
            skLineSegment(sketch, "E7.8.4.3", {"start": v(-19.25, -71.44) * mm, "end": v(-16.5, -76.2) * mm});
            skLineSegment(sketch, "E7.11.4.3", {"start": v(-16.5, -76.2) * mm, "end": v(-19.25, -80.96) * mm});
            skLineSegment(sketch, "E7.14.4.3", {"start": v(-19.25, -80.96) * mm, "end": v(-24.75, -80.96) * mm});
            skLineSegment(sketch, "E7.17.4.3", {"start": v(-24.75, -80.96) * mm, "end": v(-27.5, -76.2) * mm});
            skLineSegment(sketch, "E8.0.0.4", {"start": v(-123.73, -65.09) * mm, "end": v(-118.23, -65.09) * mm});
            skLineSegment(sketch, "E8.3.0.4", {"start": v(-118.23, -65.09) * mm, "end": v(-115.48, -69.85) * mm});
            skLineSegment(sketch, "E8.6.0.4", {"start": v(-115.48, -69.85) * mm, "end": v(-118.23, -74.61) * mm});
            skCircle(sketch, "E8.9.0.4", {"center": v(-120.98, -69.85) * mm, "radius": 4.76 * mm, "construction": true});
            skLineSegment(sketch, "E8.11.0.4", {"start": v(-118.23, -74.61) * mm, "end": v(-123.73, -74.61) * mm});
            skLineSegment(sketch, "E8.14.0.4", {"start": v(-123.73, -74.61) * mm, "end": v(-126.48, -69.85) * mm});
            skLineSegment(sketch, "E8.17.0.4", {"start": v(-126.48, -69.85) * mm, "end": v(-123.73, -65.09) * mm});
            skLineSegment(sketch, "E8.0.0.5", {"start": v(-123.73, -52.39) * mm, "end": v(-118.23, -52.39) * mm});
            skLineSegment(sketch, "E8.3.0.5", {"start": v(-118.23, -52.39) * mm, "end": v(-115.48, -57.15) * mm});
            skLineSegment(sketch, "E8.6.0.5", {"start": v(-115.48, -57.15) * mm, "end": v(-118.23, -61.91) * mm});
            skCircle(sketch, "E8.9.0.5", {"center": v(-120.98, -57.15) * mm, "radius": 4.76 * mm, "construction": true});
            skLineSegment(sketch, "E8.11.0.5", {"start": v(-118.23, -61.91) * mm, "end": v(-123.73, -61.91) * mm});
            skLineSegment(sketch, "E8.14.0.5", {"start": v(-123.73, -61.91) * mm, "end": v(-126.48, -57.15) * mm});
            skLineSegment(sketch, "E8.17.0.5", {"start": v(-126.48, -57.15) * mm, "end": v(-123.73, -52.39) * mm});
            skLineSegment(sketch, "E8.0.0.6", {"start": v(-123.73, -39.69) * mm, "end": v(-118.23, -39.69) * mm});
            skLineSegment(sketch, "E8.3.0.6", {"start": v(-118.23, -39.69) * mm, "end": v(-115.48, -44.45) * mm});
            skLineSegment(sketch, "E8.6.0.6", {"start": v(-115.48, -44.45) * mm, "end": v(-118.23, -49.21) * mm});
            skCircle(sketch, "E8.9.0.6", {"center": v(-120.98, -44.45) * mm, "radius": 4.76 * mm, "construction": true});
            skLineSegment(sketch, "E8.11.0.6", {"start": v(-118.23, -49.21) * mm, "end": v(-123.73, -49.21) * mm});
            skLineSegment(sketch, "E8.14.0.6", {"start": v(-123.73, -49.21) * mm, "end": v(-126.48, -44.45) * mm});
            skLineSegment(sketch, "E8.17.0.6", {"start": v(-126.48, -44.45) * mm, "end": v(-123.73, -39.69) * mm});
            skLineSegment(sketch, "E8.0.0.7", {"start": v(-123.73, -26.99) * mm, "end": v(-118.23, -26.99) * mm});
            skLineSegment(sketch, "E8.3.0.7", {"start": v(-118.23, -26.99) * mm, "end": v(-115.48, -31.75) * mm});
            skLineSegment(sketch, "E8.6.0.7", {"start": v(-115.48, -31.75) * mm, "end": v(-118.23, -36.51) * mm});
            skCircle(sketch, "E8.9.0.7", {"center": v(-120.98, -31.75) * mm, "radius": 4.76 * mm, "construction": true});
            skLineSegment(sketch, "E8.11.0.7", {"start": v(-118.23, -36.51) * mm, "end": v(-123.73, -36.51) * mm});
            skLineSegment(sketch, "E8.14.0.7", {"start": v(-123.73, -36.51) * mm, "end": v(-126.48, -31.75) * mm});
            skLineSegment(sketch, "E8.17.0.7", {"start": v(-126.48, -31.75) * mm, "end": v(-123.73, -26.99) * mm});
            skLineSegment(sketch, "E8.0.1.4", {"start": v(-101.73, -65.09) * mm, "end": v(-96.23, -65.09) * mm});
            skLineSegment(sketch, "E8.3.1.4", {"start": v(-96.23, -65.09) * mm, "end": v(-93.48, -69.85) * mm});
            skLineSegment(sketch, "E8.6.1.4", {"start": v(-93.48, -69.85) * mm, "end": v(-96.23, -74.61) * mm});
            skCircle(sketch, "E8.9.1.4", {"center": v(-98.98, -69.85) * mm, "radius": 4.76 * mm, "construction": true});
            skLineSegment(sketch, "E8.11.1.4", {"start": v(-96.23, -74.61) * mm, "end": v(-101.73, -74.61) * mm});
            skLineSegment(sketch, "E8.14.1.4", {"start": v(-101.73, -74.61) * mm, "end": v(-104.48, -69.85) * mm});
            skLineSegment(sketch, "E8.17.1.4", {"start": v(-104.48, -69.85) * mm, "end": v(-101.73, -65.09) * mm});
            skLineSegment(sketch, "E8.0.1.5", {"start": v(-101.73, -52.39) * mm, "end": v(-96.23, -52.39) * mm});
            skLineSegment(sketch, "E8.3.1.5", {"start": v(-96.23, -52.39) * mm, "end": v(-93.48, -57.15) * mm});
            skLineSegment(sketch, "E8.6.1.5", {"start": v(-93.48, -57.15) * mm, "end": v(-96.23, -61.91) * mm});
            skCircle(sketch, "E8.9.1.5", {"center": v(-98.98, -57.15) * mm, "radius": 4.76 * mm, "construction": true});
            skLineSegment(sketch, "E8.11.1.5", {"start": v(-96.23, -61.91) * mm, "end": v(-101.73, -61.91) * mm});
            skLineSegment(sketch, "E8.14.1.5", {"start": v(-101.73, -61.91) * mm, "end": v(-104.48, -57.15) * mm});
            skLineSegment(sketch, "E8.17.1.5", {"start": v(-104.48, -57.15) * mm, "end": v(-101.73, -52.39) * mm});
            skLineSegment(sketch, "E8.0.1.6", {"start": v(-101.73, -39.69) * mm, "end": v(-96.23, -39.69) * mm});
            skLineSegment(sketch, "E8.3.1.6", {"start": v(-96.23, -39.69) * mm, "end": v(-93.48, -44.45) * mm});
            skLineSegment(sketch, "E8.6.1.6", {"start": v(-93.48, -44.45) * mm, "end": v(-96.23, -49.21) * mm});
            skCircle(sketch, "E8.9.1.6", {"center": v(-98.98, -44.45) * mm, "radius": 4.76 * mm, "construction": true});
            skLineSegment(sketch, "E8.11.1.6", {"start": v(-96.23, -49.21) * mm, "end": v(-101.73, -49.21) * mm});
            skLineSegment(sketch, "E8.14.1.6", {"start": v(-101.73, -49.21) * mm, "end": v(-104.48, -44.45) * mm});
            skLineSegment(sketch, "E8.17.1.6", {"start": v(-104.48, -44.45) * mm, "end": v(-101.73, -39.69) * mm});
            skLineSegment(sketch, "E8.0.1.7", {"start": v(-101.73, -26.99) * mm, "end": v(-96.23, -26.99) * mm});
            skLineSegment(sketch, "E8.3.1.7", {"start": v(-96.23, -26.99) * mm, "end": v(-93.48, -31.75) * mm});
            skLineSegment(sketch, "E8.6.1.7", {"start": v(-93.48, -31.75) * mm, "end": v(-96.23, -36.51) * mm});
            skCircle(sketch, "E8.9.1.7", {"center": v(-98.98, -31.75) * mm, "radius": 4.76 * mm, "construction": true});
            skLineSegment(sketch, "E8.11.1.7", {"start": v(-96.23, -36.51) * mm, "end": v(-101.73, -36.51) * mm});
            skLineSegment(sketch, "E8.14.1.7", {"start": v(-101.73, -36.51) * mm, "end": v(-104.48, -31.75) * mm});
            skLineSegment(sketch, "E8.17.1.7", {"start": v(-104.48, -31.75) * mm, "end": v(-101.73, -26.99) * mm});
            skLineSegment(sketch, "E8.0.2.4", {"start": v(-79.74, -65.09) * mm, "end": v(-74.24, -65.09) * mm});
            skLineSegment(sketch, "E8.3.2.4", {"start": v(-74.24, -65.09) * mm, "end": v(-71.49, -69.85) * mm});
            skLineSegment(sketch, "E8.6.2.4", {"start": v(-71.49, -69.85) * mm, "end": v(-74.24, -74.61) * mm});
            skCircle(sketch, "E8.9.2.4", {"center": v(-76.99, -69.85) * mm, "radius": 4.76 * mm, "construction": true});
            skLineSegment(sketch, "E8.11.2.4", {"start": v(-74.24, -74.61) * mm, "end": v(-79.74, -74.61) * mm});
            skLineSegment(sketch, "E8.14.2.4", {"start": v(-79.74, -74.61) * mm, "end": v(-82.49, -69.85) * mm});
            skLineSegment(sketch, "E8.17.2.4", {"start": v(-82.49, -69.85) * mm, "end": v(-79.74, -65.09) * mm});
            skLineSegment(sketch, "E8.0.2.5", {"start": v(-79.74, -52.39) * mm, "end": v(-74.24, -52.39) * mm});
            skLineSegment(sketch, "E8.3.2.5", {"start": v(-74.24, -52.39) * mm, "end": v(-71.49, -57.15) * mm});
            skLineSegment(sketch, "E8.6.2.5", {"start": v(-71.49, -57.15) * mm, "end": v(-74.24, -61.91) * mm});
            skCircle(sketch, "E8.9.2.5", {"center": v(-76.99, -57.15) * mm, "radius": 4.76 * mm, "construction": true});
            skLineSegment(sketch, "E8.11.2.5", {"start": v(-74.24, -61.91) * mm, "end": v(-79.74, -61.91) * mm});
            skLineSegment(sketch, "E8.14.2.5", {"start": v(-79.74, -61.91) * mm, "end": v(-82.49, -57.15) * mm});
            skLineSegment(sketch, "E8.17.2.5", {"start": v(-82.49, -57.15) * mm, "end": v(-79.74, -52.39) * mm});
            skLineSegment(sketch, "E8.0.2.6", {"start": v(-79.74, -39.69) * mm, "end": v(-74.24, -39.69) * mm});
            skLineSegment(sketch, "E8.3.2.6", {"start": v(-74.24, -39.69) * mm, "end": v(-71.49, -44.45) * mm});
            skLineSegment(sketch, "E8.6.2.6", {"start": v(-71.49, -44.45) * mm, "end": v(-74.24, -49.21) * mm});
            skCircle(sketch, "E8.9.2.6", {"center": v(-76.99, -44.45) * mm, "radius": 4.76 * mm, "construction": true});
            skLineSegment(sketch, "E8.11.2.6", {"start": v(-74.24, -49.21) * mm, "end": v(-79.74, -49.21) * mm});
            skLineSegment(sketch, "E8.14.2.6", {"start": v(-79.74, -49.21) * mm, "end": v(-82.49, -44.45) * mm});
            skLineSegment(sketch, "E8.17.2.6", {"start": v(-82.49, -44.45) * mm, "end": v(-79.74, -39.69) * mm});
            skLineSegment(sketch, "E8.0.2.7", {"start": v(-79.74, -26.99) * mm, "end": v(-74.24, -26.99) * mm});
            skLineSegment(sketch, "E8.3.2.7", {"start": v(-74.24, -26.99) * mm, "end": v(-71.49, -31.75) * mm});
            skLineSegment(sketch, "E8.6.2.7", {"start": v(-71.49, -31.75) * mm, "end": v(-74.24, -36.51) * mm});
            skCircle(sketch, "E8.9.2.7", {"center": v(-76.99, -31.75) * mm, "radius": 4.76 * mm, "construction": true});
            skLineSegment(sketch, "E8.11.2.7", {"start": v(-74.24, -36.51) * mm, "end": v(-79.74, -36.51) * mm});
            skLineSegment(sketch, "E8.14.2.7", {"start": v(-79.74, -36.51) * mm, "end": v(-82.49, -31.75) * mm});
            skLineSegment(sketch, "E8.17.2.7", {"start": v(-82.49, -31.75) * mm, "end": v(-79.74, -26.99) * mm});
            skLineSegment(sketch, "E8.0.3.4", {"start": v(-57.74, -65.09) * mm, "end": v(-52.24, -65.09) * mm});
            skLineSegment(sketch, "E8.3.3.4", {"start": v(-52.24, -65.09) * mm, "end": v(-49.5, -69.85) * mm});
            skLineSegment(sketch, "E8.6.3.4", {"start": v(-49.5, -69.85) * mm, "end": v(-52.24, -74.61) * mm});
            skCircle(sketch, "E8.9.3.4", {"center": v(-55, -69.85) * mm, "radius": 4.76 * mm, "construction": true});
            skLineSegment(sketch, "E8.11.3.4", {"start": v(-52.24, -74.61) * mm, "end": v(-57.74, -74.61) * mm});
            skLineSegment(sketch, "E8.14.3.4", {"start": v(-57.74, -74.61) * mm, "end": v(-60.5, -69.85) * mm});
            skLineSegment(sketch, "E8.17.3.4", {"start": v(-60.5, -69.85) * mm, "end": v(-57.74, -65.09) * mm});
            skLineSegment(sketch, "E8.0.3.5", {"start": v(-57.74, -52.39) * mm, "end": v(-52.24, -52.39) * mm});
            skLineSegment(sketch, "E8.3.3.5", {"start": v(-52.24, -52.39) * mm, "end": v(-49.5, -57.15) * mm});
            skLineSegment(sketch, "E8.6.3.5", {"start": v(-49.5, -57.15) * mm, "end": v(-52.24, -61.91) * mm});
            skCircle(sketch, "E8.9.3.5", {"center": v(-55, -57.15) * mm, "radius": 4.76 * mm, "construction": true});
            skLineSegment(sketch, "E8.11.3.5", {"start": v(-52.24, -61.91) * mm, "end": v(-57.74, -61.91) * mm});
            skLineSegment(sketch, "E8.14.3.5", {"start": v(-57.74, -61.91) * mm, "end": v(-60.5, -57.15) * mm});
            skLineSegment(sketch, "E8.17.3.5", {"start": v(-60.5, -57.15) * mm, "end": v(-57.74, -52.39) * mm});
            skLineSegment(sketch, "E8.0.3.6", {"start": v(-57.74, -39.69) * mm, "end": v(-52.24, -39.69) * mm});
            skLineSegment(sketch, "E8.3.3.6", {"start": v(-52.24, -39.69) * mm, "end": v(-49.5, -44.45) * mm});
            skLineSegment(sketch, "E8.6.3.6", {"start": v(-49.5, -44.45) * mm, "end": v(-52.24, -49.21) * mm});
            skCircle(sketch, "E8.9.3.6", {"center": v(-55, -44.45) * mm, "radius": 4.76 * mm, "construction": true});
            skLineSegment(sketch, "E8.11.3.6", {"start": v(-52.24, -49.21) * mm, "end": v(-57.74, -49.21) * mm});
            skLineSegment(sketch, "E8.14.3.6", {"start": v(-57.74, -49.21) * mm, "end": v(-60.5, -44.45) * mm});
            skLineSegment(sketch, "E8.17.3.6", {"start": v(-60.5, -44.45) * mm, "end": v(-57.74, -39.69) * mm});
            skLineSegment(sketch, "E8.0.3.7", {"start": v(-57.74, -26.99) * mm, "end": v(-52.24, -26.99) * mm});
            skLineSegment(sketch, "E8.3.3.7", {"start": v(-52.24, -26.99) * mm, "end": v(-49.5, -31.75) * mm});
            skLineSegment(sketch, "E8.6.3.7", {"start": v(-49.5, -31.75) * mm, "end": v(-52.24, -36.51) * mm});
            skCircle(sketch, "E8.9.3.7", {"center": v(-55, -31.75) * mm, "radius": 4.76 * mm, "construction": true});
            skLineSegment(sketch, "E8.11.3.7", {"start": v(-52.24, -36.51) * mm, "end": v(-57.74, -36.51) * mm});
            skLineSegment(sketch, "E8.14.3.7", {"start": v(-57.74, -36.51) * mm, "end": v(-60.5, -31.75) * mm});
            skLineSegment(sketch, "E8.17.3.7", {"start": v(-60.5, -31.75) * mm, "end": v(-57.74, -26.99) * mm});
            skLineSegment(sketch, "E8.0.4.4", {"start": v(-35.74, -65.09) * mm, "end": v(-30.25, -65.09) * mm});
            skLineSegment(sketch, "E8.3.4.4", {"start": v(-30.25, -65.09) * mm, "end": v(-27.5, -69.85) * mm});
            skLineSegment(sketch, "E8.6.4.4", {"start": v(-27.5, -69.85) * mm, "end": v(-30.25, -74.61) * mm});
            skCircle(sketch, "E8.9.4.4", {"center": v(-33, -69.85) * mm, "radius": 4.76 * mm, "construction": true});
            skLineSegment(sketch, "E8.11.4.4", {"start": v(-30.25, -74.61) * mm, "end": v(-35.74, -74.61) * mm});
            skLineSegment(sketch, "E8.14.4.4", {"start": v(-35.74, -74.61) * mm, "end": v(-38.5, -69.85) * mm});
            skLineSegment(sketch, "E8.17.4.4", {"start": v(-38.5, -69.85) * mm, "end": v(-35.74, -65.09) * mm});
            skLineSegment(sketch, "E8.0.4.5", {"start": v(-35.74, -52.39) * mm, "end": v(-30.25, -52.39) * mm});
            skLineSegment(sketch, "E8.3.4.5", {"start": v(-30.25, -52.39) * mm, "end": v(-27.5, -57.15) * mm});
            skLineSegment(sketch, "E8.6.4.5", {"start": v(-27.5, -57.15) * mm, "end": v(-30.25, -61.91) * mm});
            skCircle(sketch, "E8.9.4.5", {"center": v(-33, -57.15) * mm, "radius": 4.76 * mm, "construction": true});
            skLineSegment(sketch, "E8.11.4.5", {"start": v(-30.25, -61.91) * mm, "end": v(-35.74, -61.91) * mm});
            skLineSegment(sketch, "E8.14.4.5", {"start": v(-35.74, -61.91) * mm, "end": v(-38.5, -57.15) * mm});
            skLineSegment(sketch, "E8.17.4.5", {"start": v(-38.5, -57.15) * mm, "end": v(-35.74, -52.39) * mm});
            skLineSegment(sketch, "E8.0.4.6", {"start": v(-35.74, -39.69) * mm, "end": v(-30.25, -39.69) * mm});
            skLineSegment(sketch, "E8.3.4.6", {"start": v(-30.25, -39.69) * mm, "end": v(-27.5, -44.45) * mm});
            skLineSegment(sketch, "E8.6.4.6", {"start": v(-27.5, -44.45) * mm, "end": v(-30.25, -49.21) * mm});
            skCircle(sketch, "E8.9.4.6", {"center": v(-33, -44.45) * mm, "radius": 4.76 * mm, "construction": true});
            skLineSegment(sketch, "E8.11.4.6", {"start": v(-30.25, -49.21) * mm, "end": v(-35.74, -49.21) * mm});
            skLineSegment(sketch, "E8.14.4.6", {"start": v(-35.74, -49.21) * mm, "end": v(-38.5, -44.45) * mm});
            skLineSegment(sketch, "E8.17.4.6", {"start": v(-38.5, -44.45) * mm, "end": v(-35.74, -39.69) * mm});
            skLineSegment(sketch, "E8.0.4.7", {"start": v(-35.74, -26.99) * mm, "end": v(-30.25, -26.99) * mm});
            skLineSegment(sketch, "E8.3.4.7", {"start": v(-30.25, -26.99) * mm, "end": v(-27.5, -31.75) * mm});
            skLineSegment(sketch, "E8.6.4.7", {"start": v(-27.5, -31.75) * mm, "end": v(-30.25, -36.51) * mm});
            skCircle(sketch, "E8.9.4.7", {"center": v(-33, -31.75) * mm, "radius": 4.76 * mm, "construction": true});
            skLineSegment(sketch, "E8.11.4.7", {"start": v(-30.25, -36.51) * mm, "end": v(-35.74, -36.51) * mm});
            skLineSegment(sketch, "E8.14.4.7", {"start": v(-35.74, -36.51) * mm, "end": v(-38.5, -31.75) * mm});
            skLineSegment(sketch, "E8.17.4.7", {"start": v(-38.5, -31.75) * mm, "end": v(-35.74, -26.99) * mm});
            skLineSegment(sketch, "E8.0.5.4", {"start": v(-13.75, -65.09) * mm, "end": v(-8.25, -65.09) * mm});
            skLineSegment(sketch, "E8.3.5.4", {"start": v(-8.25, -65.09) * mm, "end": v(-5.5, -69.85) * mm});
            skLineSegment(sketch, "E8.6.5.4", {"start": v(-5.5, -69.85) * mm, "end": v(-8.25, -74.61) * mm});
            skCircle(sketch, "E8.9.5.4", {"center": v(-11, -69.85) * mm, "radius": 4.76 * mm, "construction": true});
            skLineSegment(sketch, "E8.11.5.4", {"start": v(-8.25, -74.61) * mm, "end": v(-13.75, -74.61) * mm});
            skLineSegment(sketch, "E8.14.5.4", {"start": v(-13.75, -74.61) * mm, "end": v(-16.5, -69.85) * mm});
            skLineSegment(sketch, "E8.17.5.4", {"start": v(-16.5, -69.85) * mm, "end": v(-13.75, -65.09) * mm});
            skLineSegment(sketch, "E8.0.5.5", {"start": v(-13.75, -52.39) * mm, "end": v(-8.25, -52.39) * mm});
            skLineSegment(sketch, "E8.3.5.5", {"start": v(-8.25, -52.39) * mm, "end": v(-5.5, -57.15) * mm});
            skLineSegment(sketch, "E8.6.5.5", {"start": v(-5.5, -57.15) * mm, "end": v(-8.25, -61.91) * mm});
            skCircle(sketch, "E8.9.5.5", {"center": v(-11, -57.15) * mm, "radius": 4.76 * mm, "construction": true});
            skLineSegment(sketch, "E8.11.5.5", {"start": v(-8.25, -61.91) * mm, "end": v(-13.75, -61.91) * mm});
            skLineSegment(sketch, "E8.14.5.5", {"start": v(-13.75, -61.91) * mm, "end": v(-16.5, -57.15) * mm});
            skLineSegment(sketch, "E8.17.5.5", {"start": v(-16.5, -57.15) * mm, "end": v(-13.75, -52.39) * mm});
            skLineSegment(sketch, "E8.0.5.6", {"start": v(-13.75, -39.69) * mm, "end": v(-8.25, -39.69) * mm});
            skLineSegment(sketch, "E8.3.5.6", {"start": v(-8.25, -39.69) * mm, "end": v(-5.5, -44.45) * mm});
            skLineSegment(sketch, "E8.6.5.6", {"start": v(-5.5, -44.45) * mm, "end": v(-8.25, -49.21) * mm});
            skCircle(sketch, "E8.9.5.6", {"center": v(-11, -44.45) * mm, "radius": 4.76 * mm, "construction": true});
            skLineSegment(sketch, "E8.11.5.6", {"start": v(-8.25, -49.21) * mm, "end": v(-13.75, -49.21) * mm});
            skLineSegment(sketch, "E8.14.5.6", {"start": v(-13.75, -49.21) * mm, "end": v(-16.5, -44.45) * mm});
            skLineSegment(sketch, "E8.17.5.6", {"start": v(-16.5, -44.45) * mm, "end": v(-13.75, -39.69) * mm});
            skLineSegment(sketch, "E8.0.5.7", {"start": v(-13.75, -26.99) * mm, "end": v(-8.25, -26.99) * mm});
            skLineSegment(sketch, "E8.3.5.7", {"start": v(-8.25, -26.99) * mm, "end": v(-5.5, -31.75) * mm});
            skLineSegment(sketch, "E8.6.5.7", {"start": v(-5.5, -31.75) * mm, "end": v(-8.25, -36.51) * mm});
            skCircle(sketch, "E8.9.5.7", {"center": v(-11, -31.75) * mm, "radius": 4.76 * mm, "construction": true});
            skLineSegment(sketch, "E8.11.5.7", {"start": v(-8.25, -36.51) * mm, "end": v(-13.75, -36.51) * mm});
            skLineSegment(sketch, "E8.14.5.7", {"start": v(-13.75, -36.51) * mm, "end": v(-16.5, -31.75) * mm});
            skLineSegment(sketch, "E8.17.5.7", {"start": v(-16.5, -31.75) * mm, "end": v(-13.75, -26.99) * mm});
            skCircle(sketch, "E9.0.0.4", {"center": v(-109.98, -63.5) * mm, "radius": 4.76 * mm, "construction": true});
            skLineSegment(sketch, "E9.2.0.4", {"start": v(-115.48, -63.5) * mm, "end": v(-112.73, -58.74) * mm});
            skLineSegment(sketch, "E9.5.0.4", {"start": v(-112.73, -58.74) * mm, "end": v(-107.23, -58.74) * mm});
            skLineSegment(sketch, "E9.8.0.4", {"start": v(-107.23, -58.74) * mm, "end": v(-104.48, -63.5) * mm});
            skLineSegment(sketch, "E9.11.0.4", {"start": v(-104.48, -63.5) * mm, "end": v(-107.23, -68.26) * mm});
            skLineSegment(sketch, "E9.14.0.4", {"start": v(-107.23, -68.26) * mm, "end": v(-112.73, -68.26) * mm});
            skLineSegment(sketch, "E9.17.0.4", {"start": v(-112.73, -68.26) * mm, "end": v(-115.48, -63.5) * mm});
            skCircle(sketch, "E9.0.0.5", {"center": v(-109.98, -50.8) * mm, "radius": 4.76 * mm, "construction": true});
            skLineSegment(sketch, "E9.2.0.5", {"start": v(-115.48, -50.8) * mm, "end": v(-112.73, -46.04) * mm});
            skLineSegment(sketch, "E9.5.0.5", {"start": v(-112.73, -46.04) * mm, "end": v(-107.23, -46.04) * mm});
            skLineSegment(sketch, "E9.8.0.5", {"start": v(-107.23, -46.04) * mm, "end": v(-104.48, -50.8) * mm});
            skLineSegment(sketch, "E9.11.0.5", {"start": v(-104.48, -50.8) * mm, "end": v(-107.23, -55.56) * mm});
            skLineSegment(sketch, "E9.14.0.5", {"start": v(-107.23, -55.56) * mm, "end": v(-112.73, -55.56) * mm});
            skLineSegment(sketch, "E9.17.0.5", {"start": v(-112.73, -55.56) * mm, "end": v(-115.48, -50.8) * mm});
            skCircle(sketch, "E9.0.0.6", {"center": v(-109.98, -38.1) * mm, "radius": 4.76 * mm, "construction": true});
            skLineSegment(sketch, "E9.2.0.6", {"start": v(-115.48, -38.1) * mm, "end": v(-112.73, -33.34) * mm});
            skLineSegment(sketch, "E9.5.0.6", {"start": v(-112.73, -33.34) * mm, "end": v(-107.23, -33.34) * mm});
            skLineSegment(sketch, "E9.8.0.6", {"start": v(-107.23, -33.34) * mm, "end": v(-104.48, -38.1) * mm});
            skLineSegment(sketch, "E9.11.0.6", {"start": v(-104.48, -38.1) * mm, "end": v(-107.23, -42.86) * mm});
            skLineSegment(sketch, "E9.14.0.6", {"start": v(-107.23, -42.86) * mm, "end": v(-112.73, -42.86) * mm});
            skLineSegment(sketch, "E9.17.0.6", {"start": v(-112.73, -42.86) * mm, "end": v(-115.48, -38.1) * mm});
            skCircle(sketch, "E9.0.1.4", {"center": v(-87.99, -63.5) * mm, "radius": 4.76 * mm, "construction": true});
            skLineSegment(sketch, "E9.2.1.4", {"start": v(-93.48, -63.5) * mm, "end": v(-90.74, -58.74) * mm});
            skLineSegment(sketch, "E9.5.1.4", {"start": v(-90.74, -58.74) * mm, "end": v(-85.24, -58.74) * mm});
            skLineSegment(sketch, "E9.8.1.4", {"start": v(-85.24, -58.74) * mm, "end": v(-82.49, -63.5) * mm});
            skLineSegment(sketch, "E9.11.1.4", {"start": v(-82.49, -63.5) * mm, "end": v(-85.24, -68.26) * mm});
            skLineSegment(sketch, "E9.14.1.4", {"start": v(-85.24, -68.26) * mm, "end": v(-90.74, -68.26) * mm});
            skLineSegment(sketch, "E9.17.1.4", {"start": v(-90.74, -68.26) * mm, "end": v(-93.48, -63.5) * mm});
            skCircle(sketch, "E9.0.1.5", {"center": v(-87.99, -50.8) * mm, "radius": 4.76 * mm, "construction": true});
            skLineSegment(sketch, "E9.2.1.5", {"start": v(-93.48, -50.8) * mm, "end": v(-90.74, -46.04) * mm});
            skLineSegment(sketch, "E9.5.1.5", {"start": v(-90.74, -46.04) * mm, "end": v(-85.24, -46.04) * mm});
            skLineSegment(sketch, "E9.8.1.5", {"start": v(-85.24, -46.04) * mm, "end": v(-82.49, -50.8) * mm});
            skLineSegment(sketch, "E9.11.1.5", {"start": v(-82.49, -50.8) * mm, "end": v(-85.24, -55.56) * mm});
            skLineSegment(sketch, "E9.14.1.5", {"start": v(-85.24, -55.56) * mm, "end": v(-90.74, -55.56) * mm});
            skLineSegment(sketch, "E9.17.1.5", {"start": v(-90.74, -55.56) * mm, "end": v(-93.48, -50.8) * mm});
            skCircle(sketch, "E9.0.1.6", {"center": v(-87.99, -38.1) * mm, "radius": 4.76 * mm, "construction": true});
            skLineSegment(sketch, "E9.2.1.6", {"start": v(-93.48, -38.1) * mm, "end": v(-90.74, -33.34) * mm});
            skLineSegment(sketch, "E9.5.1.6", {"start": v(-90.74, -33.34) * mm, "end": v(-85.24, -33.34) * mm});
            skLineSegment(sketch, "E9.8.1.6", {"start": v(-85.24, -33.34) * mm, "end": v(-82.49, -38.1) * mm});
            skLineSegment(sketch, "E9.11.1.6", {"start": v(-82.49, -38.1) * mm, "end": v(-85.24, -42.86) * mm});
            skLineSegment(sketch, "E9.14.1.6", {"start": v(-85.24, -42.86) * mm, "end": v(-90.74, -42.86) * mm});
            skLineSegment(sketch, "E9.17.1.6", {"start": v(-90.74, -42.86) * mm, "end": v(-93.48, -38.1) * mm});
            skCircle(sketch, "E9.0.2.4", {"center": v(-65.99, -63.5) * mm, "radius": 4.76 * mm, "construction": true});
            skLineSegment(sketch, "E9.2.2.4", {"start": v(-71.49, -63.5) * mm, "end": v(-68.74, -58.74) * mm});
            skLineSegment(sketch, "E9.5.2.4", {"start": v(-68.74, -58.74) * mm, "end": v(-63.24, -58.74) * mm});
            skLineSegment(sketch, "E9.8.2.4", {"start": v(-63.24, -58.74) * mm, "end": v(-60.49, -63.5) * mm});
            skLineSegment(sketch, "E9.11.2.4", {"start": v(-60.49, -63.5) * mm, "end": v(-63.24, -68.26) * mm});
            skLineSegment(sketch, "E9.14.2.4", {"start": v(-63.24, -68.26) * mm, "end": v(-68.74, -68.26) * mm});
            skLineSegment(sketch, "E9.17.2.4", {"start": v(-68.74, -68.26) * mm, "end": v(-71.49, -63.5) * mm});
            skCircle(sketch, "E9.0.2.5", {"center": v(-65.99, -50.8) * mm, "radius": 4.76 * mm, "construction": true});
            skLineSegment(sketch, "E9.2.2.5", {"start": v(-71.49, -50.8) * mm, "end": v(-68.74, -46.04) * mm});
            skLineSegment(sketch, "E9.5.2.5", {"start": v(-68.74, -46.04) * mm, "end": v(-63.24, -46.04) * mm});
            skLineSegment(sketch, "E9.8.2.5", {"start": v(-63.24, -46.04) * mm, "end": v(-60.49, -50.8) * mm});
            skLineSegment(sketch, "E9.11.2.5", {"start": v(-60.49, -50.8) * mm, "end": v(-63.24, -55.56) * mm});
            skLineSegment(sketch, "E9.14.2.5", {"start": v(-63.24, -55.56) * mm, "end": v(-68.74, -55.56) * mm});
            skLineSegment(sketch, "E9.17.2.5", {"start": v(-68.74, -55.56) * mm, "end": v(-71.49, -50.8) * mm});
            skCircle(sketch, "E9.0.2.6", {"center": v(-65.99, -38.1) * mm, "radius": 4.76 * mm, "construction": true});
            skLineSegment(sketch, "E9.2.2.6", {"start": v(-71.49, -38.1) * mm, "end": v(-68.74, -33.34) * mm});
            skLineSegment(sketch, "E9.5.2.6", {"start": v(-68.74, -33.34) * mm, "end": v(-63.24, -33.34) * mm});
            skLineSegment(sketch, "E9.8.2.6", {"start": v(-63.24, -33.34) * mm, "end": v(-60.49, -38.1) * mm});
            skLineSegment(sketch, "E9.11.2.6", {"start": v(-60.49, -38.1) * mm, "end": v(-63.24, -42.86) * mm});
            skLineSegment(sketch, "E9.14.2.6", {"start": v(-63.24, -42.86) * mm, "end": v(-68.74, -42.86) * mm});
            skLineSegment(sketch, "E9.17.2.6", {"start": v(-68.74, -42.86) * mm, "end": v(-71.49, -38.1) * mm});
            skCircle(sketch, "E9.0.3.4", {"center": v(-44, -63.5) * mm, "radius": 4.76 * mm, "construction": true});
            skLineSegment(sketch, "E9.2.3.4", {"start": v(-49.5, -63.5) * mm, "end": v(-46.74, -58.74) * mm});
            skLineSegment(sketch, "E9.5.3.4", {"start": v(-46.74, -58.74) * mm, "end": v(-41.24, -58.74) * mm});
            skLineSegment(sketch, "E9.8.3.4", {"start": v(-41.24, -58.74) * mm, "end": v(-38.5, -63.5) * mm});
            skLineSegment(sketch, "E9.11.3.4", {"start": v(-38.5, -63.5) * mm, "end": v(-41.24, -68.26) * mm});
            skLineSegment(sketch, "E9.14.3.4", {"start": v(-41.24, -68.26) * mm, "end": v(-46.74, -68.26) * mm});
            skLineSegment(sketch, "E9.17.3.4", {"start": v(-46.74, -68.26) * mm, "end": v(-49.5, -63.5) * mm});
            skCircle(sketch, "E9.0.3.5", {"center": v(-44, -50.8) * mm, "radius": 4.76 * mm, "construction": true});
            skLineSegment(sketch, "E9.2.3.5", {"start": v(-49.5, -50.8) * mm, "end": v(-46.74, -46.04) * mm});
            skLineSegment(sketch, "E9.5.3.5", {"start": v(-46.74, -46.04) * mm, "end": v(-41.24, -46.04) * mm});
            skLineSegment(sketch, "E9.8.3.5", {"start": v(-41.24, -46.04) * mm, "end": v(-38.5, -50.8) * mm});
            skLineSegment(sketch, "E9.11.3.5", {"start": v(-38.5, -50.8) * mm, "end": v(-41.24, -55.56) * mm});
            skLineSegment(sketch, "E9.14.3.5", {"start": v(-41.24, -55.56) * mm, "end": v(-46.74, -55.56) * mm});
            skLineSegment(sketch, "E9.17.3.5", {"start": v(-46.74, -55.56) * mm, "end": v(-49.5, -50.8) * mm});
            skCircle(sketch, "E9.0.3.6", {"center": v(-44, -38.1) * mm, "radius": 4.76 * mm, "construction": true});
            skLineSegment(sketch, "E9.2.3.6", {"start": v(-49.5, -38.1) * mm, "end": v(-46.74, -33.34) * mm});
            skLineSegment(sketch, "E9.5.3.6", {"start": v(-46.74, -33.34) * mm, "end": v(-41.24, -33.34) * mm});
            skLineSegment(sketch, "E9.8.3.6", {"start": v(-41.24, -33.34) * mm, "end": v(-38.5, -38.1) * mm});
            skLineSegment(sketch, "E9.11.3.6", {"start": v(-38.5, -38.1) * mm, "end": v(-41.24, -42.86) * mm});
            skLineSegment(sketch, "E9.14.3.6", {"start": v(-41.24, -42.86) * mm, "end": v(-46.74, -42.86) * mm});
            skLineSegment(sketch, "E9.17.3.6", {"start": v(-46.74, -42.86) * mm, "end": v(-49.5, -38.1) * mm});
            skCircle(sketch, "E9.0.4.4", {"center": v(-22, -63.5) * mm, "radius": 4.76 * mm, "construction": true});
            skLineSegment(sketch, "E9.2.4.4", {"start": v(-27.5, -63.5) * mm, "end": v(-24.75, -58.74) * mm});
            skLineSegment(sketch, "E9.5.4.4", {"start": v(-24.75, -58.74) * mm, "end": v(-19.25, -58.74) * mm});
            skLineSegment(sketch, "E9.8.4.4", {"start": v(-19.25, -58.74) * mm, "end": v(-16.5, -63.5) * mm});
            skLineSegment(sketch, "E9.11.4.4", {"start": v(-16.5, -63.5) * mm, "end": v(-19.25, -68.26) * mm});
            skLineSegment(sketch, "E9.14.4.4", {"start": v(-19.25, -68.26) * mm, "end": v(-24.75, -68.26) * mm});
            skLineSegment(sketch, "E9.17.4.4", {"start": v(-24.75, -68.26) * mm, "end": v(-27.5, -63.5) * mm});
            skCircle(sketch, "E9.0.4.5", {"center": v(-22, -50.8) * mm, "radius": 4.76 * mm, "construction": true});
            skLineSegment(sketch, "E9.2.4.5", {"start": v(-27.5, -50.8) * mm, "end": v(-24.75, -46.04) * mm});
            skLineSegment(sketch, "E9.5.4.5", {"start": v(-24.75, -46.04) * mm, "end": v(-19.25, -46.04) * mm});
            skLineSegment(sketch, "E9.8.4.5", {"start": v(-19.25, -46.04) * mm, "end": v(-16.5, -50.8) * mm});
            skLineSegment(sketch, "E9.11.4.5", {"start": v(-16.5, -50.8) * mm, "end": v(-19.25, -55.56) * mm});
            skLineSegment(sketch, "E9.14.4.5", {"start": v(-19.25, -55.56) * mm, "end": v(-24.75, -55.56) * mm});
            skLineSegment(sketch, "E9.17.4.5", {"start": v(-24.75, -55.56) * mm, "end": v(-27.5, -50.8) * mm});
            skCircle(sketch, "E9.0.4.6", {"center": v(-22, -38.1) * mm, "radius": 4.76 * mm, "construction": true});
            skLineSegment(sketch, "E9.2.4.6", {"start": v(-27.5, -38.1) * mm, "end": v(-24.75, -33.34) * mm});
            skLineSegment(sketch, "E9.5.4.6", {"start": v(-24.75, -33.34) * mm, "end": v(-19.25, -33.34) * mm});
            skLineSegment(sketch, "E9.8.4.6", {"start": v(-19.25, -33.34) * mm, "end": v(-16.5, -38.1) * mm});
            skLineSegment(sketch, "E9.11.4.6", {"start": v(-16.5, -38.1) * mm, "end": v(-19.25, -42.86) * mm});
            skLineSegment(sketch, "E9.14.4.6", {"start": v(-19.25, -42.86) * mm, "end": v(-24.75, -42.86) * mm});
            skLineSegment(sketch, "E9.17.4.6", {"start": v(-24.75, -42.86) * mm, "end": v(-27.5, -38.1) * mm});
            skCircle(sketch, "E10.0.0.7", {"center": v(-109.98, -25.4) * mm, "radius": 4.76 * mm, "construction": true});
            skLineSegment(sketch, "E10.2.0.7", {"start": v(-115.48, -25.4) * mm, "end": v(-112.73, -20.64) * mm});
            skLineSegment(sketch, "E10.5.0.7", {"start": v(-112.73, -20.64) * mm, "end": v(-107.23, -20.64) * mm});
            skLineSegment(sketch, "E10.8.0.7", {"start": v(-107.23, -20.64) * mm, "end": v(-104.48, -25.4) * mm});
            skLineSegment(sketch, "E10.11.0.7", {"start": v(-104.48, -25.4) * mm, "end": v(-107.23, -30.16) * mm});
            skLineSegment(sketch, "E10.14.0.7", {"start": v(-107.23, -30.16) * mm, "end": v(-112.73, -30.16) * mm});
            skLineSegment(sketch, "E10.17.0.7", {"start": v(-112.73, -30.16) * mm, "end": v(-115.48, -25.4) * mm});
            skCircle(sketch, "E10.0.1.7", {"center": v(-87.99, -25.4) * mm, "radius": 4.76 * mm, "construction": true});
            skLineSegment(sketch, "E10.2.1.7", {"start": v(-93.48, -25.4) * mm, "end": v(-90.74, -20.64) * mm});
            skLineSegment(sketch, "E10.5.1.7", {"start": v(-90.74, -20.64) * mm, "end": v(-85.24, -20.64) * mm});
            skLineSegment(sketch, "E10.8.1.7", {"start": v(-85.24, -20.64) * mm, "end": v(-82.49, -25.4) * mm});
            skLineSegment(sketch, "E10.11.1.7", {"start": v(-82.49, -25.4) * mm, "end": v(-85.24, -30.16) * mm});
            skLineSegment(sketch, "E10.14.1.7", {"start": v(-85.24, -30.16) * mm, "end": v(-90.74, -30.16) * mm});
            skLineSegment(sketch, "E10.17.1.7", {"start": v(-90.74, -30.16) * mm, "end": v(-93.48, -25.4) * mm});
            skCircle(sketch, "E10.0.2.7", {"center": v(-65.99, -25.4) * mm, "radius": 4.76 * mm, "construction": true});
            skLineSegment(sketch, "E10.2.2.7", {"start": v(-71.49, -25.4) * mm, "end": v(-68.74, -20.64) * mm});
            skLineSegment(sketch, "E10.5.2.7", {"start": v(-68.74, -20.64) * mm, "end": v(-63.24, -20.64) * mm});
            skLineSegment(sketch, "E10.8.2.7", {"start": v(-63.24, -20.64) * mm, "end": v(-60.49, -25.4) * mm});
            skLineSegment(sketch, "E10.11.2.7", {"start": v(-60.49, -25.4) * mm, "end": v(-63.24, -30.16) * mm});
            skLineSegment(sketch, "E10.14.2.7", {"start": v(-63.24, -30.16) * mm, "end": v(-68.74, -30.16) * mm});
            skLineSegment(sketch, "E10.17.2.7", {"start": v(-68.74, -30.16) * mm, "end": v(-71.49, -25.4) * mm});
            skCircle(sketch, "E10.0.3.7", {"center": v(-44, -25.4) * mm, "radius": 4.76 * mm, "construction": true});
            skLineSegment(sketch, "E10.2.3.7", {"start": v(-49.5, -25.4) * mm, "end": v(-46.74, -20.64) * mm});
            skLineSegment(sketch, "E10.5.3.7", {"start": v(-46.74, -20.64) * mm, "end": v(-41.24, -20.64) * mm});
            skLineSegment(sketch, "E10.8.3.7", {"start": v(-41.24, -20.64) * mm, "end": v(-38.5, -25.4) * mm});
            skLineSegment(sketch, "E10.11.3.7", {"start": v(-38.5, -25.4) * mm, "end": v(-41.24, -30.16) * mm});
            skLineSegment(sketch, "E10.14.3.7", {"start": v(-41.24, -30.16) * mm, "end": v(-46.74, -30.16) * mm});
            skLineSegment(sketch, "E10.17.3.7", {"start": v(-46.74, -30.16) * mm, "end": v(-49.5, -25.4) * mm});
            skCircle(sketch, "E10.0.4.7", {"center": v(-22, -25.4) * mm, "radius": 4.76 * mm, "construction": true});
            skLineSegment(sketch, "E10.2.4.7", {"start": v(-27.5, -25.4) * mm, "end": v(-24.75, -20.64) * mm});
            skLineSegment(sketch, "E10.5.4.7", {"start": v(-24.75, -20.64) * mm, "end": v(-19.25, -20.64) * mm});
            skLineSegment(sketch, "E10.8.4.7", {"start": v(-19.25, -20.64) * mm, "end": v(-16.5, -25.4) * mm});
            skLineSegment(sketch, "E10.11.4.7", {"start": v(-16.5, -25.4) * mm, "end": v(-19.25, -30.16) * mm});
            skLineSegment(sketch, "E10.14.4.7", {"start": v(-19.25, -30.16) * mm, "end": v(-24.75, -30.16) * mm});
            skLineSegment(sketch, "E10.17.4.7", {"start": v(-24.75, -30.16) * mm, "end": v(-27.5, -25.4) * mm});
            skLineSegment(sketch, "E11.0.0.8", {"start": v(-123.73, -14.29) * mm, "end": v(-118.23, -14.29) * mm});
            skLineSegment(sketch, "E11.3.0.8", {"start": v(-118.23, -14.29) * mm, "end": v(-115.48, -19.05) * mm});
            skLineSegment(sketch, "E11.6.0.8", {"start": v(-115.48, -19.05) * mm, "end": v(-118.23, -23.81) * mm});
            skCircle(sketch, "E11.9.0.8", {"center": v(-120.98, -19.05) * mm, "radius": 4.76 * mm, "construction": true});
            skLineSegment(sketch, "E11.11.0.8", {"start": v(-118.23, -23.81) * mm, "end": v(-123.73, -23.81) * mm});
            skLineSegment(sketch, "E11.14.0.8", {"start": v(-123.73, -23.81) * mm, "end": v(-126.48, -19.05) * mm});
            skLineSegment(sketch, "E11.17.0.8", {"start": v(-126.48, -19.05) * mm, "end": v(-123.73, -14.29) * mm});
            skLineSegment(sketch, "E11.0.1.8", {"start": v(-101.73, -14.29) * mm, "end": v(-96.23, -14.29) * mm});
            skLineSegment(sketch, "E11.3.1.8", {"start": v(-96.23, -14.29) * mm, "end": v(-93.48, -19.05) * mm});
            skLineSegment(sketch, "E11.6.1.8", {"start": v(-93.48, -19.05) * mm, "end": v(-96.23, -23.81) * mm});
            skCircle(sketch, "E11.9.1.8", {"center": v(-98.98, -19.05) * mm, "radius": 4.76 * mm, "construction": true});
            skLineSegment(sketch, "E11.11.1.8", {"start": v(-96.23, -23.81) * mm, "end": v(-101.73, -23.81) * mm});
            skLineSegment(sketch, "E11.14.1.8", {"start": v(-101.73, -23.81) * mm, "end": v(-104.48, -19.05) * mm});
            skLineSegment(sketch, "E11.17.1.8", {"start": v(-104.48, -19.05) * mm, "end": v(-101.73, -14.29) * mm});
            skLineSegment(sketch, "E11.0.2.8", {"start": v(-79.74, -14.29) * mm, "end": v(-74.24, -14.29) * mm});
            skLineSegment(sketch, "E11.3.2.8", {"start": v(-74.24, -14.29) * mm, "end": v(-71.49, -19.05) * mm});
            skLineSegment(sketch, "E11.6.2.8", {"start": v(-71.49, -19.05) * mm, "end": v(-74.24, -23.81) * mm});
            skCircle(sketch, "E11.9.2.8", {"center": v(-76.99, -19.05) * mm, "radius": 4.76 * mm, "construction": true});
            skLineSegment(sketch, "E11.11.2.8", {"start": v(-74.24, -23.81) * mm, "end": v(-79.74, -23.81) * mm});
            skLineSegment(sketch, "E11.14.2.8", {"start": v(-79.74, -23.81) * mm, "end": v(-82.49, -19.05) * mm});
            skLineSegment(sketch, "E11.17.2.8", {"start": v(-82.49, -19.05) * mm, "end": v(-79.74, -14.29) * mm});
            skLineSegment(sketch, "E11.0.3.8", {"start": v(-57.74, -14.29) * mm, "end": v(-52.24, -14.29) * mm});
            skLineSegment(sketch, "E11.3.3.8", {"start": v(-52.24, -14.29) * mm, "end": v(-49.5, -19.05) * mm});
            skLineSegment(sketch, "E11.6.3.8", {"start": v(-49.5, -19.05) * mm, "end": v(-52.24, -23.81) * mm});
            skCircle(sketch, "E11.9.3.8", {"center": v(-55, -19.05) * mm, "radius": 4.76 * mm, "construction": true});
            skLineSegment(sketch, "E11.11.3.8", {"start": v(-52.24, -23.81) * mm, "end": v(-57.74, -23.81) * mm});
            skLineSegment(sketch, "E11.14.3.8", {"start": v(-57.74, -23.81) * mm, "end": v(-60.5, -19.05) * mm});
            skLineSegment(sketch, "E11.17.3.8", {"start": v(-60.5, -19.05) * mm, "end": v(-57.74, -14.29) * mm});
            skLineSegment(sketch, "E11.0.4.8", {"start": v(-35.74, -14.29) * mm, "end": v(-30.25, -14.29) * mm});
            skLineSegment(sketch, "E11.3.4.8", {"start": v(-30.25, -14.29) * mm, "end": v(-27.5, -19.05) * mm});
            skLineSegment(sketch, "E11.6.4.8", {"start": v(-27.5, -19.05) * mm, "end": v(-30.25, -23.81) * mm});
            skCircle(sketch, "E11.9.4.8", {"center": v(-33, -19.05) * mm, "radius": 4.76 * mm, "construction": true});
            skLineSegment(sketch, "E11.11.4.8", {"start": v(-30.25, -23.81) * mm, "end": v(-35.74, -23.81) * mm});
            skLineSegment(sketch, "E11.14.4.8", {"start": v(-35.74, -23.81) * mm, "end": v(-38.5, -19.05) * mm});
            skLineSegment(sketch, "E11.17.4.8", {"start": v(-38.5, -19.05) * mm, "end": v(-35.74, -14.29) * mm});
            skLineSegment(sketch, "E11.0.5.8", {"start": v(-13.75, -14.29) * mm, "end": v(-8.25, -14.29) * mm});
            skLineSegment(sketch, "E11.3.5.8", {"start": v(-8.25, -14.29) * mm, "end": v(-5.5, -19.05) * mm});
            skLineSegment(sketch, "E11.6.5.8", {"start": v(-5.5, -19.05) * mm, "end": v(-8.25, -23.81) * mm});
            skCircle(sketch, "E11.9.5.8", {"center": v(-11, -19.05) * mm, "radius": 4.76 * mm, "construction": true});
            skLineSegment(sketch, "E11.11.5.8", {"start": v(-8.25, -23.81) * mm, "end": v(-13.75, -23.81) * mm});
            skLineSegment(sketch, "E11.14.5.8", {"start": v(-13.75, -23.81) * mm, "end": v(-16.5, -19.05) * mm});
            skLineSegment(sketch, "E11.17.5.8", {"start": v(-16.5, -19.05) * mm, "end": v(-13.75, -14.29) * mm});
            skLineSegment(sketch, "E12.0.0.9", {"start": v(-123.73, -1.59) * mm, "end": v(-118.23, -1.59) * mm});
            skLineSegment(sketch, "E12.3.0.9", {"start": v(-118.23, -1.59) * mm, "end": v(-115.48, -6.35) * mm});
            skLineSegment(sketch, "E12.6.0.9", {"start": v(-115.48, -6.35) * mm, "end": v(-118.23, -11.11) * mm});
            skCircle(sketch, "E12.9.0.9", {"center": v(-120.98, -6.35) * mm, "radius": 4.76 * mm, "construction": true});
            skLineSegment(sketch, "E12.11.0.9", {"start": v(-118.23, -11.11) * mm, "end": v(-123.73, -11.11) * mm});
            skLineSegment(sketch, "E12.14.0.9", {"start": v(-123.73, -11.11) * mm, "end": v(-126.48, -6.35) * mm});
            skLineSegment(sketch, "E12.17.0.9", {"start": v(-126.48, -6.35) * mm, "end": v(-123.73, -1.59) * mm});
            skLineSegment(sketch, "E12.0.0.10", {"start": v(-123.73, 11.11) * mm, "end": v(-118.23, 11.11) * mm});
            skLineSegment(sketch, "E12.3.0.10", {"start": v(-118.23, 11.11) * mm, "end": v(-115.48, 6.35) * mm});
            skLineSegment(sketch, "E12.6.0.10", {"start": v(-115.48, 6.35) * mm, "end": v(-118.23, 1.59) * mm});
            skCircle(sketch, "E12.9.0.10", {"center": v(-120.98, 6.35) * mm, "radius": 4.76 * mm, "construction": true});
            skLineSegment(sketch, "E12.11.0.10", {"start": v(-118.23, 1.59) * mm, "end": v(-123.73, 1.59) * mm});
            skLineSegment(sketch, "E12.14.0.10", {"start": v(-123.73, 1.59) * mm, "end": v(-126.48, 6.35) * mm});
            skLineSegment(sketch, "E12.17.0.10", {"start": v(-126.48, 6.35) * mm, "end": v(-123.73, 11.11) * mm});
            skLineSegment(sketch, "E12.0.0.11", {"start": v(-123.73, 23.81) * mm, "end": v(-118.23, 23.81) * mm});
            skLineSegment(sketch, "E12.3.0.11", {"start": v(-118.23, 23.81) * mm, "end": v(-115.48, 19.05) * mm});
            skLineSegment(sketch, "E12.6.0.11", {"start": v(-115.48, 19.05) * mm, "end": v(-118.23, 14.29) * mm});
            skCircle(sketch, "E12.9.0.11", {"center": v(-120.98, 19.05) * mm, "radius": 4.76 * mm, "construction": true});
            skLineSegment(sketch, "E12.11.0.11", {"start": v(-118.23, 14.29) * mm, "end": v(-123.73, 14.29) * mm});
            skLineSegment(sketch, "E12.14.0.11", {"start": v(-123.73, 14.29) * mm, "end": v(-126.48, 19.05) * mm});
            skLineSegment(sketch, "E12.17.0.11", {"start": v(-126.48, 19.05) * mm, "end": v(-123.73, 23.81) * mm});
            skLineSegment(sketch, "E12.0.0.12", {"start": v(-123.73, 36.51) * mm, "end": v(-118.23, 36.51) * mm});
            skLineSegment(sketch, "E12.3.0.12", {"start": v(-118.23, 36.51) * mm, "end": v(-115.48, 31.75) * mm});
            skLineSegment(sketch, "E12.6.0.12", {"start": v(-115.48, 31.75) * mm, "end": v(-118.23, 26.99) * mm});
            skCircle(sketch, "E12.9.0.12", {"center": v(-120.98, 31.75) * mm, "radius": 4.76 * mm, "construction": true});
            skLineSegment(sketch, "E12.11.0.12", {"start": v(-118.23, 26.99) * mm, "end": v(-123.73, 26.99) * mm});
            skLineSegment(sketch, "E12.14.0.12", {"start": v(-123.73, 26.99) * mm, "end": v(-126.48, 31.75) * mm});
            skLineSegment(sketch, "E12.17.0.12", {"start": v(-126.48, 31.75) * mm, "end": v(-123.73, 36.51) * mm});
            skLineSegment(sketch, "E12.0.0.13", {"start": v(-123.73, 49.21) * mm, "end": v(-118.23, 49.21) * mm});
            skLineSegment(sketch, "E12.3.0.13", {"start": v(-118.23, 49.21) * mm, "end": v(-115.48, 44.45) * mm});
            skLineSegment(sketch, "E12.6.0.13", {"start": v(-115.48, 44.45) * mm, "end": v(-118.23, 39.69) * mm});
            skCircle(sketch, "E12.9.0.13", {"center": v(-120.98, 44.45) * mm, "radius": 4.76 * mm, "construction": true});
            skLineSegment(sketch, "E12.11.0.13", {"start": v(-118.23, 39.69) * mm, "end": v(-123.73, 39.69) * mm});
            skLineSegment(sketch, "E12.14.0.13", {"start": v(-123.73, 39.69) * mm, "end": v(-126.48, 44.45) * mm});
            skLineSegment(sketch, "E12.17.0.13", {"start": v(-126.48, 44.45) * mm, "end": v(-123.73, 49.21) * mm});
            skLineSegment(sketch, "E12.0.0.14", {"start": v(-123.73, 61.91) * mm, "end": v(-118.23, 61.91) * mm});
            skLineSegment(sketch, "E12.3.0.14", {"start": v(-118.23, 61.91) * mm, "end": v(-115.48, 57.15) * mm});
            skLineSegment(sketch, "E12.6.0.14", {"start": v(-115.48, 57.15) * mm, "end": v(-118.23, 52.39) * mm});
            skCircle(sketch, "E12.9.0.14", {"center": v(-120.98, 57.15) * mm, "radius": 4.76 * mm, "construction": true});
            skLineSegment(sketch, "E12.11.0.14", {"start": v(-118.23, 52.39) * mm, "end": v(-123.73, 52.39) * mm});
            skLineSegment(sketch, "E12.14.0.14", {"start": v(-123.73, 52.39) * mm, "end": v(-126.48, 57.15) * mm});
            skLineSegment(sketch, "E12.17.0.14", {"start": v(-126.48, 57.15) * mm, "end": v(-123.73, 61.91) * mm});
            skLineSegment(sketch, "E12.0.0.15", {"start": v(-123.73, 74.61) * mm, "end": v(-118.23, 74.61) * mm});
            skLineSegment(sketch, "E12.3.0.15", {"start": v(-118.23, 74.61) * mm, "end": v(-115.48, 69.85) * mm});
            skLineSegment(sketch, "E12.6.0.15", {"start": v(-115.48, 69.85) * mm, "end": v(-118.23, 65.09) * mm});
            skCircle(sketch, "E12.9.0.15", {"center": v(-120.98, 69.85) * mm, "radius": 4.76 * mm, "construction": true});
            skLineSegment(sketch, "E12.11.0.15", {"start": v(-118.23, 65.09) * mm, "end": v(-123.73, 65.09) * mm});
            skLineSegment(sketch, "E12.14.0.15", {"start": v(-123.73, 65.09) * mm, "end": v(-126.48, 69.85) * mm});
            skLineSegment(sketch, "E12.17.0.15", {"start": v(-126.48, 69.85) * mm, "end": v(-123.73, 74.61) * mm});
            skLineSegment(sketch, "E12.0.0.16", {"start": v(-123.73, 87.31) * mm, "end": v(-118.23, 87.31) * mm});
            skLineSegment(sketch, "E12.3.0.16", {"start": v(-118.23, 87.31) * mm, "end": v(-115.48, 82.55) * mm});
            skLineSegment(sketch, "E12.6.0.16", {"start": v(-115.48, 82.55) * mm, "end": v(-118.23, 77.79) * mm});
            skCircle(sketch, "E12.9.0.16", {"center": v(-120.98, 82.55) * mm, "radius": 4.76 * mm, "construction": true});
            skLineSegment(sketch, "E12.11.0.16", {"start": v(-118.23, 77.79) * mm, "end": v(-123.73, 77.79) * mm});
            skLineSegment(sketch, "E12.14.0.16", {"start": v(-123.73, 77.79) * mm, "end": v(-126.48, 82.55) * mm});
            skLineSegment(sketch, "E12.17.0.16", {"start": v(-126.48, 82.55) * mm, "end": v(-123.73, 87.31) * mm});
            skLineSegment(sketch, "E12.0.0.17", {"start": v(-123.73, 100.01) * mm, "end": v(-118.23, 100.01) * mm});
            skLineSegment(sketch, "E12.3.0.17", {"start": v(-118.23, 100.01) * mm, "end": v(-115.48, 95.25) * mm});
            skLineSegment(sketch, "E12.6.0.17", {"start": v(-115.48, 95.25) * mm, "end": v(-118.23, 90.49) * mm});
            skCircle(sketch, "E12.9.0.17", {"center": v(-120.98, 95.25) * mm, "radius": 4.76 * mm, "construction": true});
            skLineSegment(sketch, "E12.11.0.17", {"start": v(-118.23, 90.49) * mm, "end": v(-123.73, 90.49) * mm});
            skLineSegment(sketch, "E12.14.0.17", {"start": v(-123.73, 90.49) * mm, "end": v(-126.48, 95.25) * mm});
            skLineSegment(sketch, "E12.17.0.17", {"start": v(-126.48, 95.25) * mm, "end": v(-123.73, 100.01) * mm});
            skLineSegment(sketch, "E12.0.0.18", {"start": v(-123.73, 112.71) * mm, "end": v(-118.23, 112.71) * mm});
            skLineSegment(sketch, "E12.3.0.18", {"start": v(-118.23, 112.71) * mm, "end": v(-115.48, 107.95) * mm});
            skLineSegment(sketch, "E12.6.0.18", {"start": v(-115.48, 107.95) * mm, "end": v(-118.23, 103.19) * mm});
            skCircle(sketch, "E12.9.0.18", {"center": v(-120.98, 107.95) * mm, "radius": 4.76 * mm, "construction": true});
            skLineSegment(sketch, "E12.11.0.18", {"start": v(-118.23, 103.19) * mm, "end": v(-123.73, 103.19) * mm});
            skLineSegment(sketch, "E12.14.0.18", {"start": v(-123.73, 103.19) * mm, "end": v(-126.48, 107.95) * mm});
            skLineSegment(sketch, "E12.17.0.18", {"start": v(-126.48, 107.95) * mm, "end": v(-123.73, 112.71) * mm});
            skLineSegment(sketch, "E12.0.0.19", {"start": v(-123.73, 125.41) * mm, "end": v(-118.23, 125.41) * mm});
            skLineSegment(sketch, "E12.3.0.19", {"start": v(-118.23, 125.41) * mm, "end": v(-115.48, 120.65) * mm});
            skLineSegment(sketch, "E12.6.0.19", {"start": v(-115.48, 120.65) * mm, "end": v(-118.23, 115.89) * mm});
            skCircle(sketch, "E12.9.0.19", {"center": v(-120.98, 120.65) * mm, "radius": 4.76 * mm, "construction": true});
            skLineSegment(sketch, "E12.11.0.19", {"start": v(-118.23, 115.89) * mm, "end": v(-123.73, 115.89) * mm});
            skLineSegment(sketch, "E12.14.0.19", {"start": v(-123.73, 115.89) * mm, "end": v(-126.48, 120.65) * mm});
            skLineSegment(sketch, "E12.17.0.19", {"start": v(-126.48, 120.65) * mm, "end": v(-123.73, 125.41) * mm});
            skLineSegment(sketch, "E12.0.1.9", {"start": v(-101.73, -1.59) * mm, "end": v(-96.23, -1.59) * mm});
            skLineSegment(sketch, "E12.3.1.9", {"start": v(-96.23, -1.59) * mm, "end": v(-93.48, -6.35) * mm});
            skLineSegment(sketch, "E12.6.1.9", {"start": v(-93.48, -6.35) * mm, "end": v(-96.23, -11.11) * mm});
            skCircle(sketch, "E12.9.1.9", {"center": v(-98.98, -6.35) * mm, "radius": 4.76 * mm, "construction": true});
            skLineSegment(sketch, "E12.11.1.9", {"start": v(-96.23, -11.11) * mm, "end": v(-101.73, -11.11) * mm});
            skLineSegment(sketch, "E12.14.1.9", {"start": v(-101.73, -11.11) * mm, "end": v(-104.48, -6.35) * mm});
            skLineSegment(sketch, "E12.17.1.9", {"start": v(-104.48, -6.35) * mm, "end": v(-101.73, -1.59) * mm});
            skLineSegment(sketch, "E12.0.1.10", {"start": v(-101.73, 11.11) * mm, "end": v(-96.23, 11.11) * mm});
            skLineSegment(sketch, "E12.3.1.10", {"start": v(-96.23, 11.11) * mm, "end": v(-93.48, 6.35) * mm});
            skLineSegment(sketch, "E12.6.1.10", {"start": v(-93.48, 6.35) * mm, "end": v(-96.23, 1.59) * mm});
            skCircle(sketch, "E12.9.1.10", {"center": v(-98.98, 6.35) * mm, "radius": 4.76 * mm, "construction": true});
            skLineSegment(sketch, "E12.11.1.10", {"start": v(-96.23, 1.59) * mm, "end": v(-101.73, 1.59) * mm});
            skLineSegment(sketch, "E12.14.1.10", {"start": v(-101.73, 1.59) * mm, "end": v(-104.48, 6.35) * mm});
            skLineSegment(sketch, "E12.17.1.10", {"start": v(-104.48, 6.35) * mm, "end": v(-101.73, 11.11) * mm});
            skLineSegment(sketch, "E12.0.1.11", {"start": v(-101.73, 23.81) * mm, "end": v(-96.23, 23.81) * mm});
            skLineSegment(sketch, "E12.3.1.11", {"start": v(-96.23, 23.81) * mm, "end": v(-93.48, 19.05) * mm});
            skLineSegment(sketch, "E12.6.1.11", {"start": v(-93.48, 19.05) * mm, "end": v(-96.23, 14.29) * mm});
            skCircle(sketch, "E12.9.1.11", {"center": v(-98.98, 19.05) * mm, "radius": 4.76 * mm, "construction": true});
            skLineSegment(sketch, "E12.11.1.11", {"start": v(-96.23, 14.29) * mm, "end": v(-101.73, 14.29) * mm});
            skLineSegment(sketch, "E12.14.1.11", {"start": v(-101.73, 14.29) * mm, "end": v(-104.48, 19.05) * mm});
            skLineSegment(sketch, "E12.17.1.11", {"start": v(-104.48, 19.05) * mm, "end": v(-101.73, 23.81) * mm});
            skLineSegment(sketch, "E12.0.1.12", {"start": v(-101.73, 36.51) * mm, "end": v(-96.23, 36.51) * mm});
            skLineSegment(sketch, "E12.3.1.12", {"start": v(-96.23, 36.51) * mm, "end": v(-93.48, 31.75) * mm});
            skLineSegment(sketch, "E12.6.1.12", {"start": v(-93.48, 31.75) * mm, "end": v(-96.23, 26.99) * mm});
            skCircle(sketch, "E12.9.1.12", {"center": v(-98.98, 31.75) * mm, "radius": 4.76 * mm, "construction": true});
            skLineSegment(sketch, "E12.11.1.12", {"start": v(-96.23, 26.99) * mm, "end": v(-101.73, 26.99) * mm});
            skLineSegment(sketch, "E12.14.1.12", {"start": v(-101.73, 26.99) * mm, "end": v(-104.48, 31.75) * mm});
            skLineSegment(sketch, "E12.17.1.12", {"start": v(-104.48, 31.75) * mm, "end": v(-101.73, 36.51) * mm});
            skLineSegment(sketch, "E12.0.1.13", {"start": v(-101.73, 49.21) * mm, "end": v(-96.23, 49.21) * mm});
            skLineSegment(sketch, "E12.3.1.13", {"start": v(-96.23, 49.21) * mm, "end": v(-93.48, 44.45) * mm});
            skLineSegment(sketch, "E12.6.1.13", {"start": v(-93.48, 44.45) * mm, "end": v(-96.23, 39.69) * mm});
            skCircle(sketch, "E12.9.1.13", {"center": v(-98.98, 44.45) * mm, "radius": 4.76 * mm, "construction": true});
            skLineSegment(sketch, "E12.11.1.13", {"start": v(-96.23, 39.69) * mm, "end": v(-101.73, 39.69) * mm});
            skLineSegment(sketch, "E12.14.1.13", {"start": v(-101.73, 39.69) * mm, "end": v(-104.48, 44.45) * mm});
            skLineSegment(sketch, "E12.17.1.13", {"start": v(-104.48, 44.45) * mm, "end": v(-101.73, 49.21) * mm});
            skLineSegment(sketch, "E12.0.1.14", {"start": v(-101.73, 61.91) * mm, "end": v(-96.23, 61.91) * mm});
            skLineSegment(sketch, "E12.3.1.14", {"start": v(-96.23, 61.91) * mm, "end": v(-93.48, 57.15) * mm});
            skLineSegment(sketch, "E12.6.1.14", {"start": v(-93.48, 57.15) * mm, "end": v(-96.23, 52.39) * mm});
            skCircle(sketch, "E12.9.1.14", {"center": v(-98.98, 57.15) * mm, "radius": 4.76 * mm, "construction": true});
            skLineSegment(sketch, "E12.11.1.14", {"start": v(-96.23, 52.39) * mm, "end": v(-101.73, 52.39) * mm});
            skLineSegment(sketch, "E12.14.1.14", {"start": v(-101.73, 52.39) * mm, "end": v(-104.48, 57.15) * mm});
            skLineSegment(sketch, "E12.17.1.14", {"start": v(-104.48, 57.15) * mm, "end": v(-101.73, 61.91) * mm});
            skLineSegment(sketch, "E12.0.1.15", {"start": v(-101.73, 74.61) * mm, "end": v(-96.23, 74.61) * mm});
            skLineSegment(sketch, "E12.3.1.15", {"start": v(-96.23, 74.61) * mm, "end": v(-93.48, 69.85) * mm});
            skLineSegment(sketch, "E12.6.1.15", {"start": v(-93.48, 69.85) * mm, "end": v(-96.23, 65.09) * mm});
            skCircle(sketch, "E12.9.1.15", {"center": v(-98.98, 69.85) * mm, "radius": 4.76 * mm, "construction": true});
            skLineSegment(sketch, "E12.11.1.15", {"start": v(-96.23, 65.09) * mm, "end": v(-101.73, 65.09) * mm});
            skLineSegment(sketch, "E12.14.1.15", {"start": v(-101.73, 65.09) * mm, "end": v(-104.48, 69.85) * mm});
            skLineSegment(sketch, "E12.17.1.15", {"start": v(-104.48, 69.85) * mm, "end": v(-101.73, 74.61) * mm});
            skLineSegment(sketch, "E12.0.1.16", {"start": v(-101.73, 87.31) * mm, "end": v(-96.23, 87.31) * mm});
            skLineSegment(sketch, "E12.3.1.16", {"start": v(-96.23, 87.31) * mm, "end": v(-93.48, 82.55) * mm});
            skLineSegment(sketch, "E12.6.1.16", {"start": v(-93.48, 82.55) * mm, "end": v(-96.23, 77.79) * mm});
            skCircle(sketch, "E12.9.1.16", {"center": v(-98.98, 82.55) * mm, "radius": 4.76 * mm, "construction": true});
            skLineSegment(sketch, "E12.11.1.16", {"start": v(-96.23, 77.79) * mm, "end": v(-101.73, 77.79) * mm});
            skLineSegment(sketch, "E12.14.1.16", {"start": v(-101.73, 77.79) * mm, "end": v(-104.48, 82.55) * mm});
            skLineSegment(sketch, "E12.17.1.16", {"start": v(-104.48, 82.55) * mm, "end": v(-101.73, 87.31) * mm});
            skLineSegment(sketch, "E12.0.1.17", {"start": v(-101.73, 100.01) * mm, "end": v(-96.23, 100.01) * mm});
            skLineSegment(sketch, "E12.3.1.17", {"start": v(-96.23, 100.01) * mm, "end": v(-93.48, 95.25) * mm});
            skLineSegment(sketch, "E12.6.1.17", {"start": v(-93.48, 95.25) * mm, "end": v(-96.23, 90.49) * mm});
            skCircle(sketch, "E12.9.1.17", {"center": v(-98.98, 95.25) * mm, "radius": 4.76 * mm, "construction": true});
            skLineSegment(sketch, "E12.11.1.17", {"start": v(-96.23, 90.49) * mm, "end": v(-101.73, 90.49) * mm});
            skLineSegment(sketch, "E12.14.1.17", {"start": v(-101.73, 90.49) * mm, "end": v(-104.48, 95.25) * mm});
            skLineSegment(sketch, "E12.17.1.17", {"start": v(-104.48, 95.25) * mm, "end": v(-101.73, 100.01) * mm});
            skLineSegment(sketch, "E12.0.1.18", {"start": v(-101.73, 112.71) * mm, "end": v(-96.23, 112.71) * mm});
            skLineSegment(sketch, "E12.3.1.18", {"start": v(-96.23, 112.71) * mm, "end": v(-93.48, 107.95) * mm});
            skLineSegment(sketch, "E12.6.1.18", {"start": v(-93.48, 107.95) * mm, "end": v(-96.23, 103.19) * mm});
            skCircle(sketch, "E12.9.1.18", {"center": v(-98.98, 107.95) * mm, "radius": 4.76 * mm, "construction": true});
            skLineSegment(sketch, "E12.11.1.18", {"start": v(-96.23, 103.19) * mm, "end": v(-101.73, 103.19) * mm});
            skLineSegment(sketch, "E12.14.1.18", {"start": v(-101.73, 103.19) * mm, "end": v(-104.48, 107.95) * mm});
            skLineSegment(sketch, "E12.17.1.18", {"start": v(-104.48, 107.95) * mm, "end": v(-101.73, 112.71) * mm});
            skLineSegment(sketch, "E12.0.1.19", {"start": v(-101.73, 125.41) * mm, "end": v(-96.23, 125.41) * mm});
            skLineSegment(sketch, "E12.3.1.19", {"start": v(-96.23, 125.41) * mm, "end": v(-93.48, 120.65) * mm});
            skLineSegment(sketch, "E12.6.1.19", {"start": v(-93.48, 120.65) * mm, "end": v(-96.23, 115.89) * mm});
            skCircle(sketch, "E12.9.1.19", {"center": v(-98.98, 120.65) * mm, "radius": 4.76 * mm, "construction": true});
            skLineSegment(sketch, "E12.11.1.19", {"start": v(-96.23, 115.89) * mm, "end": v(-101.73, 115.89) * mm});
            skLineSegment(sketch, "E12.14.1.19", {"start": v(-101.73, 115.89) * mm, "end": v(-104.48, 120.65) * mm});
            skLineSegment(sketch, "E12.17.1.19", {"start": v(-104.48, 120.65) * mm, "end": v(-101.73, 125.41) * mm});
            skLineSegment(sketch, "E12.0.2.9", {"start": v(-79.74, -1.59) * mm, "end": v(-74.24, -1.59) * mm});
            skLineSegment(sketch, "E12.3.2.9", {"start": v(-74.24, -1.59) * mm, "end": v(-71.49, -6.35) * mm});
            skLineSegment(sketch, "E12.6.2.9", {"start": v(-71.49, -6.35) * mm, "end": v(-74.24, -11.11) * mm});
            skCircle(sketch, "E12.9.2.9", {"center": v(-76.99, -6.35) * mm, "radius": 4.76 * mm, "construction": true});
            skLineSegment(sketch, "E12.11.2.9", {"start": v(-74.24, -11.11) * mm, "end": v(-79.74, -11.11) * mm});
            skLineSegment(sketch, "E12.14.2.9", {"start": v(-79.74, -11.11) * mm, "end": v(-82.49, -6.35) * mm});
            skLineSegment(sketch, "E12.17.2.9", {"start": v(-82.49, -6.35) * mm, "end": v(-79.74, -1.59) * mm});
            skLineSegment(sketch, "E12.0.2.10", {"start": v(-79.74, 11.11) * mm, "end": v(-74.24, 11.11) * mm});
            skLineSegment(sketch, "E12.3.2.10", {"start": v(-74.24, 11.11) * mm, "end": v(-71.49, 6.35) * mm});
            skLineSegment(sketch, "E12.6.2.10", {"start": v(-71.49, 6.35) * mm, "end": v(-74.24, 1.59) * mm});
            skCircle(sketch, "E12.9.2.10", {"center": v(-76.99, 6.35) * mm, "radius": 4.76 * mm, "construction": true});
            skLineSegment(sketch, "E12.11.2.10", {"start": v(-74.24, 1.59) * mm, "end": v(-79.74, 1.59) * mm});
            skLineSegment(sketch, "E12.14.2.10", {"start": v(-79.74, 1.59) * mm, "end": v(-82.49, 6.35) * mm});
            skLineSegment(sketch, "E12.17.2.10", {"start": v(-82.49, 6.35) * mm, "end": v(-79.74, 11.11) * mm});
            skLineSegment(sketch, "E12.0.2.11", {"start": v(-79.74, 23.81) * mm, "end": v(-74.24, 23.81) * mm});
            skLineSegment(sketch, "E12.3.2.11", {"start": v(-74.24, 23.81) * mm, "end": v(-71.49, 19.05) * mm});
            skLineSegment(sketch, "E12.6.2.11", {"start": v(-71.49, 19.05) * mm, "end": v(-74.24, 14.29) * mm});
            skCircle(sketch, "E12.9.2.11", {"center": v(-76.99, 19.05) * mm, "radius": 4.76 * mm, "construction": true});
            skLineSegment(sketch, "E12.11.2.11", {"start": v(-74.24, 14.29) * mm, "end": v(-79.74, 14.29) * mm});
            skLineSegment(sketch, "E12.14.2.11", {"start": v(-79.74, 14.29) * mm, "end": v(-82.49, 19.05) * mm});
            skLineSegment(sketch, "E12.17.2.11", {"start": v(-82.49, 19.05) * mm, "end": v(-79.74, 23.81) * mm});
            skLineSegment(sketch, "E12.0.2.12", {"start": v(-79.74, 36.51) * mm, "end": v(-74.24, 36.51) * mm});
            skLineSegment(sketch, "E12.3.2.12", {"start": v(-74.24, 36.51) * mm, "end": v(-71.49, 31.75) * mm});
            skLineSegment(sketch, "E12.6.2.12", {"start": v(-71.49, 31.75) * mm, "end": v(-74.24, 26.99) * mm});
            skCircle(sketch, "E12.9.2.12", {"center": v(-76.99, 31.75) * mm, "radius": 4.76 * mm, "construction": true});
            skLineSegment(sketch, "E12.11.2.12", {"start": v(-74.24, 26.99) * mm, "end": v(-79.74, 26.99) * mm});
            skLineSegment(sketch, "E12.14.2.12", {"start": v(-79.74, 26.99) * mm, "end": v(-82.49, 31.75) * mm});
            skLineSegment(sketch, "E12.17.2.12", {"start": v(-82.49, 31.75) * mm, "end": v(-79.74, 36.51) * mm});
            skLineSegment(sketch, "E12.0.2.13", {"start": v(-79.74, 49.21) * mm, "end": v(-74.24, 49.21) * mm});
            skLineSegment(sketch, "E12.3.2.13", {"start": v(-74.24, 49.21) * mm, "end": v(-71.49, 44.45) * mm});
            skLineSegment(sketch, "E12.6.2.13", {"start": v(-71.49, 44.45) * mm, "end": v(-74.24, 39.69) * mm});
            skCircle(sketch, "E12.9.2.13", {"center": v(-76.99, 44.45) * mm, "radius": 4.76 * mm, "construction": true});
            skLineSegment(sketch, "E12.11.2.13", {"start": v(-74.24, 39.69) * mm, "end": v(-79.74, 39.69) * mm});
            skLineSegment(sketch, "E12.14.2.13", {"start": v(-79.74, 39.69) * mm, "end": v(-82.49, 44.45) * mm});
            skLineSegment(sketch, "E12.17.2.13", {"start": v(-82.49, 44.45) * mm, "end": v(-79.74, 49.21) * mm});
            skLineSegment(sketch, "E12.0.2.14", {"start": v(-79.74, 61.91) * mm, "end": v(-74.24, 61.91) * mm});
            skLineSegment(sketch, "E12.3.2.14", {"start": v(-74.24, 61.91) * mm, "end": v(-71.49, 57.15) * mm});
            skLineSegment(sketch, "E12.6.2.14", {"start": v(-71.49, 57.15) * mm, "end": v(-74.24, 52.39) * mm});
            skCircle(sketch, "E12.9.2.14", {"center": v(-76.99, 57.15) * mm, "radius": 4.76 * mm, "construction": true});
            skLineSegment(sketch, "E12.11.2.14", {"start": v(-74.24, 52.39) * mm, "end": v(-79.74, 52.39) * mm});
            skLineSegment(sketch, "E12.14.2.14", {"start": v(-79.74, 52.39) * mm, "end": v(-82.49, 57.15) * mm});
            skLineSegment(sketch, "E12.17.2.14", {"start": v(-82.49, 57.15) * mm, "end": v(-79.74, 61.91) * mm});
            skLineSegment(sketch, "E12.0.2.15", {"start": v(-79.74, 74.61) * mm, "end": v(-74.24, 74.61) * mm});
            skLineSegment(sketch, "E12.3.2.15", {"start": v(-74.24, 74.61) * mm, "end": v(-71.49, 69.85) * mm});
            skLineSegment(sketch, "E12.6.2.15", {"start": v(-71.49, 69.85) * mm, "end": v(-74.24, 65.09) * mm});
            skCircle(sketch, "E12.9.2.15", {"center": v(-76.99, 69.85) * mm, "radius": 4.76 * mm, "construction": true});
            skLineSegment(sketch, "E12.11.2.15", {"start": v(-74.24, 65.09) * mm, "end": v(-79.74, 65.09) * mm});
            skLineSegment(sketch, "E12.14.2.15", {"start": v(-79.74, 65.09) * mm, "end": v(-82.49, 69.85) * mm});
            skLineSegment(sketch, "E12.17.2.15", {"start": v(-82.49, 69.85) * mm, "end": v(-79.74, 74.61) * mm});
            skLineSegment(sketch, "E12.0.2.16", {"start": v(-79.74, 87.31) * mm, "end": v(-74.24, 87.31) * mm});
            skLineSegment(sketch, "E12.3.2.16", {"start": v(-74.24, 87.31) * mm, "end": v(-71.49, 82.55) * mm});
            skLineSegment(sketch, "E12.6.2.16", {"start": v(-71.49, 82.55) * mm, "end": v(-74.24, 77.79) * mm});
            skCircle(sketch, "E12.9.2.16", {"center": v(-76.99, 82.55) * mm, "radius": 4.76 * mm, "construction": true});
            skLineSegment(sketch, "E12.11.2.16", {"start": v(-74.24, 77.79) * mm, "end": v(-79.74, 77.79) * mm});
            skLineSegment(sketch, "E12.14.2.16", {"start": v(-79.74, 77.79) * mm, "end": v(-82.49, 82.55) * mm});
            skLineSegment(sketch, "E12.17.2.16", {"start": v(-82.49, 82.55) * mm, "end": v(-79.74, 87.31) * mm});
            skLineSegment(sketch, "E12.0.2.17", {"start": v(-79.74, 100.01) * mm, "end": v(-74.24, 100.01) * mm});
            skLineSegment(sketch, "E12.3.2.17", {"start": v(-74.24, 100.01) * mm, "end": v(-71.49, 95.25) * mm});
            skLineSegment(sketch, "E12.6.2.17", {"start": v(-71.49, 95.25) * mm, "end": v(-74.24, 90.49) * mm});
            skCircle(sketch, "E12.9.2.17", {"center": v(-76.99, 95.25) * mm, "radius": 4.76 * mm, "construction": true});
            skLineSegment(sketch, "E12.11.2.17", {"start": v(-74.24, 90.49) * mm, "end": v(-79.74, 90.49) * mm});
            skLineSegment(sketch, "E12.14.2.17", {"start": v(-79.74, 90.49) * mm, "end": v(-82.49, 95.25) * mm});
            skLineSegment(sketch, "E12.17.2.17", {"start": v(-82.49, 95.25) * mm, "end": v(-79.74, 100.01) * mm});
            skLineSegment(sketch, "E12.0.2.18", {"start": v(-79.74, 112.71) * mm, "end": v(-74.24, 112.71) * mm});
            skLineSegment(sketch, "E12.3.2.18", {"start": v(-74.24, 112.71) * mm, "end": v(-71.49, 107.95) * mm});
            skLineSegment(sketch, "E12.6.2.18", {"start": v(-71.49, 107.95) * mm, "end": v(-74.24, 103.19) * mm});
            skCircle(sketch, "E12.9.2.18", {"center": v(-76.99, 107.95) * mm, "radius": 4.76 * mm, "construction": true});
            skLineSegment(sketch, "E12.11.2.18", {"start": v(-74.24, 103.19) * mm, "end": v(-79.74, 103.19) * mm});
            skLineSegment(sketch, "E12.14.2.18", {"start": v(-79.74, 103.19) * mm, "end": v(-82.49, 107.95) * mm});
            skLineSegment(sketch, "E12.17.2.18", {"start": v(-82.49, 107.95) * mm, "end": v(-79.74, 112.71) * mm});
            skLineSegment(sketch, "E12.0.2.19", {"start": v(-79.74, 125.41) * mm, "end": v(-74.24, 125.41) * mm});
            skLineSegment(sketch, "E12.3.2.19", {"start": v(-74.24, 125.41) * mm, "end": v(-71.49, 120.65) * mm});
            skLineSegment(sketch, "E12.6.2.19", {"start": v(-71.49, 120.65) * mm, "end": v(-74.24, 115.89) * mm});
            skCircle(sketch, "E12.9.2.19", {"center": v(-76.99, 120.65) * mm, "radius": 4.76 * mm, "construction": true});
            skLineSegment(sketch, "E12.11.2.19", {"start": v(-74.24, 115.89) * mm, "end": v(-79.74, 115.89) * mm});
            skLineSegment(sketch, "E12.14.2.19", {"start": v(-79.74, 115.89) * mm, "end": v(-82.49, 120.65) * mm});
            skLineSegment(sketch, "E12.17.2.19", {"start": v(-82.49, 120.65) * mm, "end": v(-79.74, 125.41) * mm});
            skLineSegment(sketch, "E12.0.3.9", {"start": v(-57.74, -1.59) * mm, "end": v(-52.24, -1.59) * mm});
            skLineSegment(sketch, "E12.3.3.9", {"start": v(-52.24, -1.59) * mm, "end": v(-49.5, -6.35) * mm});
            skLineSegment(sketch, "E12.6.3.9", {"start": v(-49.5, -6.35) * mm, "end": v(-52.24, -11.11) * mm});
            skCircle(sketch, "E12.9.3.9", {"center": v(-55, -6.35) * mm, "radius": 4.76 * mm, "construction": true});
            skLineSegment(sketch, "E12.11.3.9", {"start": v(-52.24, -11.11) * mm, "end": v(-57.74, -11.11) * mm});
            skLineSegment(sketch, "E12.14.3.9", {"start": v(-57.74, -11.11) * mm, "end": v(-60.5, -6.35) * mm});
            skLineSegment(sketch, "E12.17.3.9", {"start": v(-60.5, -6.35) * mm, "end": v(-57.74, -1.59) * mm});
            skLineSegment(sketch, "E12.0.3.10", {"start": v(-57.74, 11.11) * mm, "end": v(-52.24, 11.11) * mm});
            skLineSegment(sketch, "E12.3.3.10", {"start": v(-52.24, 11.11) * mm, "end": v(-49.5, 6.35) * mm});
            skLineSegment(sketch, "E12.6.3.10", {"start": v(-49.5, 6.35) * mm, "end": v(-52.24, 1.59) * mm});
            skCircle(sketch, "E12.9.3.10", {"center": v(-55, 6.35) * mm, "radius": 4.76 * mm, "construction": true});
            skLineSegment(sketch, "E12.11.3.10", {"start": v(-52.24, 1.59) * mm, "end": v(-57.74, 1.59) * mm});
            skLineSegment(sketch, "E12.14.3.10", {"start": v(-57.74, 1.59) * mm, "end": v(-60.5, 6.35) * mm});
            skLineSegment(sketch, "E12.17.3.10", {"start": v(-60.5, 6.35) * mm, "end": v(-57.74, 11.11) * mm});
            skLineSegment(sketch, "E12.0.3.11", {"start": v(-57.74, 23.81) * mm, "end": v(-52.24, 23.81) * mm});
            skLineSegment(sketch, "E12.3.3.11", {"start": v(-52.24, 23.81) * mm, "end": v(-49.5, 19.05) * mm});
            skLineSegment(sketch, "E12.6.3.11", {"start": v(-49.5, 19.05) * mm, "end": v(-52.24, 14.29) * mm});
            skCircle(sketch, "E12.9.3.11", {"center": v(-55, 19.05) * mm, "radius": 4.76 * mm, "construction": true});
            skLineSegment(sketch, "E12.11.3.11", {"start": v(-52.24, 14.29) * mm, "end": v(-57.74, 14.29) * mm});
            skLineSegment(sketch, "E12.14.3.11", {"start": v(-57.74, 14.29) * mm, "end": v(-60.5, 19.05) * mm});
            skLineSegment(sketch, "E12.17.3.11", {"start": v(-60.5, 19.05) * mm, "end": v(-57.74, 23.81) * mm});
            skLineSegment(sketch, "E12.0.3.12", {"start": v(-57.74, 36.51) * mm, "end": v(-52.24, 36.51) * mm});
            skLineSegment(sketch, "E12.3.3.12", {"start": v(-52.24, 36.51) * mm, "end": v(-49.5, 31.75) * mm});
            skLineSegment(sketch, "E12.6.3.12", {"start": v(-49.5, 31.75) * mm, "end": v(-52.24, 26.99) * mm});
            skCircle(sketch, "E12.9.3.12", {"center": v(-55, 31.75) * mm, "radius": 4.76 * mm, "construction": true});
            skLineSegment(sketch, "E12.11.3.12", {"start": v(-52.24, 26.99) * mm, "end": v(-57.74, 26.99) * mm});
            skLineSegment(sketch, "E12.14.3.12", {"start": v(-57.74, 26.99) * mm, "end": v(-60.5, 31.75) * mm});
            skLineSegment(sketch, "E12.17.3.12", {"start": v(-60.5, 31.75) * mm, "end": v(-57.74, 36.51) * mm});
            skLineSegment(sketch, "E12.0.3.13", {"start": v(-57.74, 49.21) * mm, "end": v(-52.24, 49.21) * mm});
            skLineSegment(sketch, "E12.3.3.13", {"start": v(-52.24, 49.21) * mm, "end": v(-49.5, 44.45) * mm});
            skLineSegment(sketch, "E12.6.3.13", {"start": v(-49.5, 44.45) * mm, "end": v(-52.24, 39.69) * mm});
            skCircle(sketch, "E12.9.3.13", {"center": v(-55, 44.45) * mm, "radius": 4.76 * mm, "construction": true});
            skLineSegment(sketch, "E12.11.3.13", {"start": v(-52.24, 39.69) * mm, "end": v(-57.74, 39.69) * mm});
            skLineSegment(sketch, "E12.14.3.13", {"start": v(-57.74, 39.69) * mm, "end": v(-60.5, 44.45) * mm});
            skLineSegment(sketch, "E12.17.3.13", {"start": v(-60.5, 44.45) * mm, "end": v(-57.74, 49.21) * mm});
            skLineSegment(sketch, "E12.0.3.14", {"start": v(-57.74, 61.91) * mm, "end": v(-52.24, 61.91) * mm});
            skLineSegment(sketch, "E12.3.3.14", {"start": v(-52.24, 61.91) * mm, "end": v(-49.5, 57.15) * mm});
            skLineSegment(sketch, "E12.6.3.14", {"start": v(-49.5, 57.15) * mm, "end": v(-52.24, 52.39) * mm});
            skCircle(sketch, "E12.9.3.14", {"center": v(-55, 57.15) * mm, "radius": 4.76 * mm, "construction": true});
            skLineSegment(sketch, "E12.11.3.14", {"start": v(-52.24, 52.39) * mm, "end": v(-57.74, 52.39) * mm});
            skLineSegment(sketch, "E12.14.3.14", {"start": v(-57.74, 52.39) * mm, "end": v(-60.5, 57.15) * mm});
            skLineSegment(sketch, "E12.17.3.14", {"start": v(-60.5, 57.15) * mm, "end": v(-57.74, 61.91) * mm});
            skLineSegment(sketch, "E12.0.3.15", {"start": v(-57.74, 74.61) * mm, "end": v(-52.24, 74.61) * mm});
            skLineSegment(sketch, "E12.3.3.15", {"start": v(-52.24, 74.61) * mm, "end": v(-49.5, 69.85) * mm});
            skLineSegment(sketch, "E12.6.3.15", {"start": v(-49.5, 69.85) * mm, "end": v(-52.24, 65.09) * mm});
            skCircle(sketch, "E12.9.3.15", {"center": v(-55, 69.85) * mm, "radius": 4.76 * mm, "construction": true});
            skLineSegment(sketch, "E12.11.3.15", {"start": v(-52.24, 65.09) * mm, "end": v(-57.74, 65.09) * mm});
            skLineSegment(sketch, "E12.14.3.15", {"start": v(-57.74, 65.09) * mm, "end": v(-60.5, 69.85) * mm});
            skLineSegment(sketch, "E12.17.3.15", {"start": v(-60.5, 69.85) * mm, "end": v(-57.74, 74.61) * mm});
            skLineSegment(sketch, "E12.0.3.16", {"start": v(-57.74, 87.31) * mm, "end": v(-52.24, 87.31) * mm});
            skLineSegment(sketch, "E12.3.3.16", {"start": v(-52.24, 87.31) * mm, "end": v(-49.5, 82.55) * mm});
            skLineSegment(sketch, "E12.6.3.16", {"start": v(-49.5, 82.55) * mm, "end": v(-52.24, 77.79) * mm});
            skCircle(sketch, "E12.9.3.16", {"center": v(-55, 82.55) * mm, "radius": 4.76 * mm, "construction": true});
            skLineSegment(sketch, "E12.11.3.16", {"start": v(-52.24, 77.79) * mm, "end": v(-57.74, 77.79) * mm});
            skLineSegment(sketch, "E12.14.3.16", {"start": v(-57.74, 77.79) * mm, "end": v(-60.5, 82.55) * mm});
            skLineSegment(sketch, "E12.17.3.16", {"start": v(-60.5, 82.55) * mm, "end": v(-57.74, 87.31) * mm});
            skLineSegment(sketch, "E12.0.3.17", {"start": v(-57.74, 100.01) * mm, "end": v(-52.24, 100.01) * mm});
            skLineSegment(sketch, "E12.3.3.17", {"start": v(-52.24, 100.01) * mm, "end": v(-49.5, 95.25) * mm});
            skLineSegment(sketch, "E12.6.3.17", {"start": v(-49.5, 95.25) * mm, "end": v(-52.24, 90.49) * mm});
            skCircle(sketch, "E12.9.3.17", {"center": v(-55, 95.25) * mm, "radius": 4.76 * mm, "construction": true});
            skLineSegment(sketch, "E12.11.3.17", {"start": v(-52.24, 90.49) * mm, "end": v(-57.74, 90.49) * mm});
            skLineSegment(sketch, "E12.14.3.17", {"start": v(-57.74, 90.49) * mm, "end": v(-60.5, 95.25) * mm});
            skLineSegment(sketch, "E12.17.3.17", {"start": v(-60.5, 95.25) * mm, "end": v(-57.74, 100.01) * mm});
            skLineSegment(sketch, "E12.0.3.18", {"start": v(-57.74, 112.71) * mm, "end": v(-52.24, 112.71) * mm});
            skLineSegment(sketch, "E12.3.3.18", {"start": v(-52.24, 112.71) * mm, "end": v(-49.5, 107.95) * mm});
            skLineSegment(sketch, "E12.6.3.18", {"start": v(-49.5, 107.95) * mm, "end": v(-52.24, 103.19) * mm});
            skCircle(sketch, "E12.9.3.18", {"center": v(-55, 107.95) * mm, "radius": 4.76 * mm, "construction": true});
            skLineSegment(sketch, "E12.11.3.18", {"start": v(-52.24, 103.19) * mm, "end": v(-57.74, 103.19) * mm});
            skLineSegment(sketch, "E12.14.3.18", {"start": v(-57.74, 103.19) * mm, "end": v(-60.5, 107.95) * mm});
            skLineSegment(sketch, "E12.17.3.18", {"start": v(-60.5, 107.95) * mm, "end": v(-57.74, 112.71) * mm});
            skLineSegment(sketch, "E12.0.3.19", {"start": v(-57.74, 125.41) * mm, "end": v(-52.24, 125.41) * mm});
            skLineSegment(sketch, "E12.3.3.19", {"start": v(-52.24, 125.41) * mm, "end": v(-49.5, 120.65) * mm});
            skLineSegment(sketch, "E12.6.3.19", {"start": v(-49.5, 120.65) * mm, "end": v(-52.24, 115.89) * mm});
            skCircle(sketch, "E12.9.3.19", {"center": v(-55, 120.65) * mm, "radius": 4.76 * mm, "construction": true});
            skLineSegment(sketch, "E12.11.3.19", {"start": v(-52.24, 115.89) * mm, "end": v(-57.74, 115.89) * mm});
            skLineSegment(sketch, "E12.14.3.19", {"start": v(-57.74, 115.89) * mm, "end": v(-60.5, 120.65) * mm});
            skLineSegment(sketch, "E12.17.3.19", {"start": v(-60.5, 120.65) * mm, "end": v(-57.74, 125.41) * mm});
            skLineSegment(sketch, "E12.0.4.9", {"start": v(-35.74, -1.59) * mm, "end": v(-30.25, -1.59) * mm});
            skLineSegment(sketch, "E12.3.4.9", {"start": v(-30.25, -1.59) * mm, "end": v(-27.5, -6.35) * mm});
            skLineSegment(sketch, "E12.6.4.9", {"start": v(-27.5, -6.35) * mm, "end": v(-30.25, -11.11) * mm});
            skCircle(sketch, "E12.9.4.9", {"center": v(-33, -6.35) * mm, "radius": 4.76 * mm, "construction": true});
            skLineSegment(sketch, "E12.11.4.9", {"start": v(-30.25, -11.11) * mm, "end": v(-35.74, -11.11) * mm});
            skLineSegment(sketch, "E12.14.4.9", {"start": v(-35.74, -11.11) * mm, "end": v(-38.5, -6.35) * mm});
            skLineSegment(sketch, "E12.17.4.9", {"start": v(-38.5, -6.35) * mm, "end": v(-35.74, -1.59) * mm});
            skLineSegment(sketch, "E12.0.4.10", {"start": v(-35.74, 11.11) * mm, "end": v(-30.25, 11.11) * mm});
            skLineSegment(sketch, "E12.3.4.10", {"start": v(-30.25, 11.11) * mm, "end": v(-27.5, 6.35) * mm});
            skLineSegment(sketch, "E12.6.4.10", {"start": v(-27.5, 6.35) * mm, "end": v(-30.25, 1.59) * mm});
            skCircle(sketch, "E12.9.4.10", {"center": v(-33, 6.35) * mm, "radius": 4.76 * mm, "construction": true});
            skLineSegment(sketch, "E12.11.4.10", {"start": v(-30.25, 1.59) * mm, "end": v(-35.74, 1.59) * mm});
            skLineSegment(sketch, "E12.14.4.10", {"start": v(-35.74, 1.59) * mm, "end": v(-38.5, 6.35) * mm});
            skLineSegment(sketch, "E12.17.4.10", {"start": v(-38.5, 6.35) * mm, "end": v(-35.74, 11.11) * mm});
            skLineSegment(sketch, "E12.0.4.11", {"start": v(-35.74, 23.81) * mm, "end": v(-30.25, 23.81) * mm});
            skLineSegment(sketch, "E12.3.4.11", {"start": v(-30.25, 23.81) * mm, "end": v(-27.5, 19.05) * mm});
            skLineSegment(sketch, "E12.6.4.11", {"start": v(-27.5, 19.05) * mm, "end": v(-30.25, 14.29) * mm});
            skCircle(sketch, "E12.9.4.11", {"center": v(-33, 19.05) * mm, "radius": 4.76 * mm, "construction": true});
            skLineSegment(sketch, "E12.11.4.11", {"start": v(-30.25, 14.29) * mm, "end": v(-35.74, 14.29) * mm});
            skLineSegment(sketch, "E12.14.4.11", {"start": v(-35.74, 14.29) * mm, "end": v(-38.5, 19.05) * mm});
            skLineSegment(sketch, "E12.17.4.11", {"start": v(-38.5, 19.05) * mm, "end": v(-35.74, 23.81) * mm});
            skLineSegment(sketch, "E12.0.4.12", {"start": v(-35.74, 36.51) * mm, "end": v(-30.25, 36.51) * mm});
            skLineSegment(sketch, "E12.3.4.12", {"start": v(-30.25, 36.51) * mm, "end": v(-27.5, 31.75) * mm});
            skLineSegment(sketch, "E12.6.4.12", {"start": v(-27.5, 31.75) * mm, "end": v(-30.25, 26.99) * mm});
            skCircle(sketch, "E12.9.4.12", {"center": v(-33, 31.75) * mm, "radius": 4.76 * mm, "construction": true});
            skLineSegment(sketch, "E12.11.4.12", {"start": v(-30.25, 26.99) * mm, "end": v(-35.74, 26.99) * mm});
            skLineSegment(sketch, "E12.14.4.12", {"start": v(-35.74, 26.99) * mm, "end": v(-38.5, 31.75) * mm});
            skLineSegment(sketch, "E12.17.4.12", {"start": v(-38.5, 31.75) * mm, "end": v(-35.74, 36.51) * mm});
            skLineSegment(sketch, "E12.0.4.13", {"start": v(-35.74, 49.21) * mm, "end": v(-30.25, 49.21) * mm});
            skLineSegment(sketch, "E12.3.4.13", {"start": v(-30.25, 49.21) * mm, "end": v(-27.5, 44.45) * mm});
            skLineSegment(sketch, "E12.6.4.13", {"start": v(-27.5, 44.45) * mm, "end": v(-30.25, 39.69) * mm});
            skCircle(sketch, "E12.9.4.13", {"center": v(-33, 44.45) * mm, "radius": 4.76 * mm, "construction": true});
            skLineSegment(sketch, "E12.11.4.13", {"start": v(-30.25, 39.69) * mm, "end": v(-35.74, 39.69) * mm});
            skLineSegment(sketch, "E12.14.4.13", {"start": v(-35.74, 39.69) * mm, "end": v(-38.5, 44.45) * mm});
            skLineSegment(sketch, "E12.17.4.13", {"start": v(-38.5, 44.45) * mm, "end": v(-35.74, 49.21) * mm});
            skLineSegment(sketch, "E12.0.4.14", {"start": v(-35.74, 61.91) * mm, "end": v(-30.25, 61.91) * mm});
            skLineSegment(sketch, "E12.3.4.14", {"start": v(-30.25, 61.91) * mm, "end": v(-27.5, 57.15) * mm});
            skLineSegment(sketch, "E12.6.4.14", {"start": v(-27.5, 57.15) * mm, "end": v(-30.25, 52.39) * mm});
            skCircle(sketch, "E12.9.4.14", {"center": v(-33, 57.15) * mm, "radius": 4.76 * mm, "construction": true});
            skLineSegment(sketch, "E12.11.4.14", {"start": v(-30.25, 52.39) * mm, "end": v(-35.74, 52.39) * mm});
            skLineSegment(sketch, "E12.14.4.14", {"start": v(-35.74, 52.39) * mm, "end": v(-38.5, 57.15) * mm});
            skLineSegment(sketch, "E12.17.4.14", {"start": v(-38.5, 57.15) * mm, "end": v(-35.74, 61.91) * mm});
            skLineSegment(sketch, "E12.0.4.15", {"start": v(-35.74, 74.61) * mm, "end": v(-30.25, 74.61) * mm});
            skLineSegment(sketch, "E12.3.4.15", {"start": v(-30.25, 74.61) * mm, "end": v(-27.5, 69.85) * mm});
            skLineSegment(sketch, "E12.6.4.15", {"start": v(-27.5, 69.85) * mm, "end": v(-30.25, 65.09) * mm});
            skCircle(sketch, "E12.9.4.15", {"center": v(-33, 69.85) * mm, "radius": 4.76 * mm, "construction": true});
            skLineSegment(sketch, "E12.11.4.15", {"start": v(-30.25, 65.09) * mm, "end": v(-35.74, 65.09) * mm});
            skLineSegment(sketch, "E12.14.4.15", {"start": v(-35.74, 65.09) * mm, "end": v(-38.5, 69.85) * mm});
            skLineSegment(sketch, "E12.17.4.15", {"start": v(-38.5, 69.85) * mm, "end": v(-35.74, 74.61) * mm});
            skLineSegment(sketch, "E12.0.4.16", {"start": v(-35.74, 87.31) * mm, "end": v(-30.25, 87.31) * mm});
            skLineSegment(sketch, "E12.3.4.16", {"start": v(-30.25, 87.31) * mm, "end": v(-27.5, 82.55) * mm});
            skLineSegment(sketch, "E12.6.4.16", {"start": v(-27.5, 82.55) * mm, "end": v(-30.25, 77.79) * mm});
            skCircle(sketch, "E12.9.4.16", {"center": v(-33, 82.55) * mm, "radius": 4.76 * mm, "construction": true});
            skLineSegment(sketch, "E12.11.4.16", {"start": v(-30.25, 77.79) * mm, "end": v(-35.74, 77.79) * mm});
            skLineSegment(sketch, "E12.14.4.16", {"start": v(-35.74, 77.79) * mm, "end": v(-38.5, 82.55) * mm});
            skLineSegment(sketch, "E12.17.4.16", {"start": v(-38.5, 82.55) * mm, "end": v(-35.74, 87.31) * mm});
            skLineSegment(sketch, "E12.0.4.17", {"start": v(-35.74, 100.01) * mm, "end": v(-30.25, 100.01) * mm});
            skLineSegment(sketch, "E12.3.4.17", {"start": v(-30.25, 100.01) * mm, "end": v(-27.5, 95.25) * mm});
            skLineSegment(sketch, "E12.6.4.17", {"start": v(-27.5, 95.25) * mm, "end": v(-30.25, 90.49) * mm});
            skCircle(sketch, "E12.9.4.17", {"center": v(-33, 95.25) * mm, "radius": 4.76 * mm, "construction": true});
            skLineSegment(sketch, "E12.11.4.17", {"start": v(-30.25, 90.49) * mm, "end": v(-35.74, 90.49) * mm});
            skLineSegment(sketch, "E12.14.4.17", {"start": v(-35.74, 90.49) * mm, "end": v(-38.5, 95.25) * mm});
            skLineSegment(sketch, "E12.17.4.17", {"start": v(-38.5, 95.25) * mm, "end": v(-35.74, 100.01) * mm});
            skLineSegment(sketch, "E12.0.4.18", {"start": v(-35.74, 112.71) * mm, "end": v(-30.25, 112.71) * mm});
            skLineSegment(sketch, "E12.3.4.18", {"start": v(-30.25, 112.71) * mm, "end": v(-27.5, 107.95) * mm});
            skLineSegment(sketch, "E12.6.4.18", {"start": v(-27.5, 107.95) * mm, "end": v(-30.25, 103.19) * mm});
            skCircle(sketch, "E12.9.4.18", {"center": v(-33, 107.95) * mm, "radius": 4.76 * mm, "construction": true});
            skLineSegment(sketch, "E12.11.4.18", {"start": v(-30.25, 103.19) * mm, "end": v(-35.74, 103.19) * mm});
            skLineSegment(sketch, "E12.14.4.18", {"start": v(-35.74, 103.19) * mm, "end": v(-38.5, 107.95) * mm});
            skLineSegment(sketch, "E12.17.4.18", {"start": v(-38.5, 107.95) * mm, "end": v(-35.74, 112.71) * mm});
            skLineSegment(sketch, "E12.0.4.19", {"start": v(-35.74, 125.41) * mm, "end": v(-30.25, 125.41) * mm});
            skLineSegment(sketch, "E12.3.4.19", {"start": v(-30.25, 125.41) * mm, "end": v(-27.5, 120.65) * mm});
            skLineSegment(sketch, "E12.6.4.19", {"start": v(-27.5, 120.65) * mm, "end": v(-30.25, 115.89) * mm});
            skCircle(sketch, "E12.9.4.19", {"center": v(-33, 120.65) * mm, "radius": 4.76 * mm, "construction": true});
            skLineSegment(sketch, "E12.11.4.19", {"start": v(-30.25, 115.89) * mm, "end": v(-35.74, 115.89) * mm});
            skLineSegment(sketch, "E12.14.4.19", {"start": v(-35.74, 115.89) * mm, "end": v(-38.5, 120.65) * mm});
            skLineSegment(sketch, "E12.17.4.19", {"start": v(-38.5, 120.65) * mm, "end": v(-35.74, 125.41) * mm});
            skLineSegment(sketch, "E12.0.5.9", {"start": v(-13.75, -1.59) * mm, "end": v(-8.25, -1.59) * mm});
            skLineSegment(sketch, "E12.3.5.9", {"start": v(-8.25, -1.59) * mm, "end": v(-5.5, -6.35) * mm});
            skLineSegment(sketch, "E12.6.5.9", {"start": v(-5.5, -6.35) * mm, "end": v(-8.25, -11.11) * mm});
            skCircle(sketch, "E12.9.5.9", {"center": v(-11, -6.35) * mm, "radius": 4.76 * mm, "construction": true});
            skLineSegment(sketch, "E12.11.5.9", {"start": v(-8.25, -11.11) * mm, "end": v(-13.75, -11.11) * mm});
            skLineSegment(sketch, "E12.14.5.9", {"start": v(-13.75, -11.11) * mm, "end": v(-16.5, -6.35) * mm});
            skLineSegment(sketch, "E12.17.5.9", {"start": v(-16.5, -6.35) * mm, "end": v(-13.75, -1.59) * mm});
            skLineSegment(sketch, "E12.0.5.10", {"start": v(-13.75, 11.11) * mm, "end": v(-8.25, 11.11) * mm});
            skLineSegment(sketch, "E12.3.5.10", {"start": v(-8.25, 11.11) * mm, "end": v(-5.5, 6.35) * mm});
            skLineSegment(sketch, "E12.6.5.10", {"start": v(-5.5, 6.35) * mm, "end": v(-8.25, 1.59) * mm});
            skCircle(sketch, "E12.9.5.10", {"center": v(-11, 6.35) * mm, "radius": 4.76 * mm, "construction": true});
            skLineSegment(sketch, "E12.11.5.10", {"start": v(-8.25, 1.59) * mm, "end": v(-13.75, 1.59) * mm});
            skLineSegment(sketch, "E12.14.5.10", {"start": v(-13.75, 1.59) * mm, "end": v(-16.5, 6.35) * mm});
            skLineSegment(sketch, "E12.17.5.10", {"start": v(-16.5, 6.35) * mm, "end": v(-13.75, 11.11) * mm});
            skLineSegment(sketch, "E12.0.5.11", {"start": v(-13.75, 23.81) * mm, "end": v(-8.25, 23.81) * mm});
            skLineSegment(sketch, "E12.3.5.11", {"start": v(-8.25, 23.81) * mm, "end": v(-5.5, 19.05) * mm});
            skLineSegment(sketch, "E12.6.5.11", {"start": v(-5.5, 19.05) * mm, "end": v(-8.25, 14.29) * mm});
            skCircle(sketch, "E12.9.5.11", {"center": v(-11, 19.05) * mm, "radius": 4.76 * mm, "construction": true});
            skLineSegment(sketch, "E12.11.5.11", {"start": v(-8.25, 14.29) * mm, "end": v(-13.75, 14.29) * mm});
            skLineSegment(sketch, "E12.14.5.11", {"start": v(-13.75, 14.29) * mm, "end": v(-16.5, 19.05) * mm});
            skLineSegment(sketch, "E12.17.5.11", {"start": v(-16.5, 19.05) * mm, "end": v(-13.75, 23.81) * mm});
            skLineSegment(sketch, "E12.0.5.12", {"start": v(-13.75, 36.51) * mm, "end": v(-8.25, 36.51) * mm});
            skLineSegment(sketch, "E12.3.5.12", {"start": v(-8.25, 36.51) * mm, "end": v(-5.5, 31.75) * mm});
            skLineSegment(sketch, "E12.6.5.12", {"start": v(-5.5, 31.75) * mm, "end": v(-8.25, 26.99) * mm});
            skCircle(sketch, "E12.9.5.12", {"center": v(-11, 31.75) * mm, "radius": 4.76 * mm, "construction": true});
            skLineSegment(sketch, "E12.11.5.12", {"start": v(-8.25, 26.99) * mm, "end": v(-13.75, 26.99) * mm});
            skLineSegment(sketch, "E12.14.5.12", {"start": v(-13.75, 26.99) * mm, "end": v(-16.5, 31.75) * mm});
            skLineSegment(sketch, "E12.17.5.12", {"start": v(-16.5, 31.75) * mm, "end": v(-13.75, 36.51) * mm});
            skLineSegment(sketch, "E12.0.5.13", {"start": v(-13.75, 49.21) * mm, "end": v(-8.25, 49.21) * mm});
            skLineSegment(sketch, "E12.3.5.13", {"start": v(-8.25, 49.21) * mm, "end": v(-5.5, 44.45) * mm});
            skLineSegment(sketch, "E12.6.5.13", {"start": v(-5.5, 44.45) * mm, "end": v(-8.25, 39.69) * mm});
            skCircle(sketch, "E12.9.5.13", {"center": v(-11, 44.45) * mm, "radius": 4.76 * mm, "construction": true});
            skLineSegment(sketch, "E12.11.5.13", {"start": v(-8.25, 39.69) * mm, "end": v(-13.75, 39.69) * mm});
            skLineSegment(sketch, "E12.14.5.13", {"start": v(-13.75, 39.69) * mm, "end": v(-16.5, 44.45) * mm});
            skLineSegment(sketch, "E12.17.5.13", {"start": v(-16.5, 44.45) * mm, "end": v(-13.75, 49.21) * mm});
            skLineSegment(sketch, "E12.0.5.14", {"start": v(-13.75, 61.91) * mm, "end": v(-8.25, 61.91) * mm});
            skLineSegment(sketch, "E12.3.5.14", {"start": v(-8.25, 61.91) * mm, "end": v(-5.5, 57.15) * mm});
            skLineSegment(sketch, "E12.6.5.14", {"start": v(-5.5, 57.15) * mm, "end": v(-8.25, 52.39) * mm});
            skCircle(sketch, "E12.9.5.14", {"center": v(-11, 57.15) * mm, "radius": 4.76 * mm, "construction": true});
            skLineSegment(sketch, "E12.11.5.14", {"start": v(-8.25, 52.39) * mm, "end": v(-13.75, 52.39) * mm});
            skLineSegment(sketch, "E12.14.5.14", {"start": v(-13.75, 52.39) * mm, "end": v(-16.5, 57.15) * mm});
            skLineSegment(sketch, "E12.17.5.14", {"start": v(-16.5, 57.15) * mm, "end": v(-13.75, 61.91) * mm});
            skLineSegment(sketch, "E12.0.5.15", {"start": v(-13.75, 74.61) * mm, "end": v(-8.25, 74.61) * mm});
            skLineSegment(sketch, "E12.3.5.15", {"start": v(-8.25, 74.61) * mm, "end": v(-5.5, 69.85) * mm});
            skLineSegment(sketch, "E12.6.5.15", {"start": v(-5.5, 69.85) * mm, "end": v(-8.25, 65.09) * mm});
            skCircle(sketch, "E12.9.5.15", {"center": v(-11, 69.85) * mm, "radius": 4.76 * mm, "construction": true});
            skLineSegment(sketch, "E12.11.5.15", {"start": v(-8.25, 65.09) * mm, "end": v(-13.75, 65.09) * mm});
            skLineSegment(sketch, "E12.14.5.15", {"start": v(-13.75, 65.09) * mm, "end": v(-16.5, 69.85) * mm});
            skLineSegment(sketch, "E12.17.5.15", {"start": v(-16.5, 69.85) * mm, "end": v(-13.75, 74.61) * mm});
            skLineSegment(sketch, "E12.0.5.16", {"start": v(-13.75, 87.31) * mm, "end": v(-8.25, 87.31) * mm});
            skLineSegment(sketch, "E12.3.5.16", {"start": v(-8.25, 87.31) * mm, "end": v(-5.5, 82.55) * mm});
            skLineSegment(sketch, "E12.6.5.16", {"start": v(-5.5, 82.55) * mm, "end": v(-8.25, 77.79) * mm});
            skCircle(sketch, "E12.9.5.16", {"center": v(-11, 82.55) * mm, "radius": 4.76 * mm, "construction": true});
            skLineSegment(sketch, "E12.11.5.16", {"start": v(-8.25, 77.79) * mm, "end": v(-13.75, 77.79) * mm});
            skLineSegment(sketch, "E12.14.5.16", {"start": v(-13.75, 77.79) * mm, "end": v(-16.5, 82.55) * mm});
            skLineSegment(sketch, "E12.17.5.16", {"start": v(-16.5, 82.55) * mm, "end": v(-13.75, 87.31) * mm});
            skLineSegment(sketch, "E12.0.5.17", {"start": v(-13.75, 100.01) * mm, "end": v(-8.25, 100.01) * mm});
            skLineSegment(sketch, "E12.3.5.17", {"start": v(-8.25, 100.01) * mm, "end": v(-5.5, 95.25) * mm});
            skLineSegment(sketch, "E12.6.5.17", {"start": v(-5.5, 95.25) * mm, "end": v(-8.25, 90.49) * mm});
            skCircle(sketch, "E12.9.5.17", {"center": v(-11, 95.25) * mm, "radius": 4.76 * mm, "construction": true});
            skLineSegment(sketch, "E12.11.5.17", {"start": v(-8.25, 90.49) * mm, "end": v(-13.75, 90.49) * mm});
            skLineSegment(sketch, "E12.14.5.17", {"start": v(-13.75, 90.49) * mm, "end": v(-16.5, 95.25) * mm});
            skLineSegment(sketch, "E12.17.5.17", {"start": v(-16.5, 95.25) * mm, "end": v(-13.75, 100.01) * mm});
            skLineSegment(sketch, "E12.0.5.18", {"start": v(-13.75, 112.71) * mm, "end": v(-8.25, 112.71) * mm});
            skLineSegment(sketch, "E12.3.5.18", {"start": v(-8.25, 112.71) * mm, "end": v(-5.5, 107.95) * mm});
            skLineSegment(sketch, "E12.6.5.18", {"start": v(-5.5, 107.95) * mm, "end": v(-8.25, 103.19) * mm});
            skCircle(sketch, "E12.9.5.18", {"center": v(-11, 107.95) * mm, "radius": 4.76 * mm, "construction": true});
            skLineSegment(sketch, "E12.11.5.18", {"start": v(-8.25, 103.19) * mm, "end": v(-13.75, 103.19) * mm});
            skLineSegment(sketch, "E12.14.5.18", {"start": v(-13.75, 103.19) * mm, "end": v(-16.5, 107.95) * mm});
            skLineSegment(sketch, "E12.17.5.18", {"start": v(-16.5, 107.95) * mm, "end": v(-13.75, 112.71) * mm});
            skLineSegment(sketch, "E12.0.5.19", {"start": v(-13.75, 125.41) * mm, "end": v(-8.25, 125.41) * mm});
            skLineSegment(sketch, "E12.3.5.19", {"start": v(-8.25, 125.41) * mm, "end": v(-5.5, 120.65) * mm});
            skLineSegment(sketch, "E12.6.5.19", {"start": v(-5.5, 120.65) * mm, "end": v(-8.25, 115.89) * mm});
            skCircle(sketch, "E12.9.5.19", {"center": v(-11, 120.65) * mm, "radius": 4.76 * mm, "construction": true});
            skLineSegment(sketch, "E12.11.5.19", {"start": v(-8.25, 115.89) * mm, "end": v(-13.75, 115.89) * mm});
            skLineSegment(sketch, "E12.14.5.19", {"start": v(-13.75, 115.89) * mm, "end": v(-16.5, 120.65) * mm});
            skLineSegment(sketch, "E12.17.5.19", {"start": v(-16.5, 120.65) * mm, "end": v(-13.75, 125.41) * mm});
            skCircle(sketch, "E13.0.0.8", {"center": v(-109.98, -12.7) * mm, "radius": 4.76 * mm, "construction": true});
            skLineSegment(sketch, "E13.2.0.8", {"start": v(-115.48, -12.7) * mm, "end": v(-112.73, -7.94) * mm});
            skLineSegment(sketch, "E13.5.0.8", {"start": v(-112.73, -7.94) * mm, "end": v(-107.23, -7.94) * mm});
            skLineSegment(sketch, "E13.8.0.8", {"start": v(-107.23, -7.94) * mm, "end": v(-104.48, -12.7) * mm});
            skLineSegment(sketch, "E13.11.0.8", {"start": v(-104.48, -12.7) * mm, "end": v(-107.23, -17.46) * mm});
            skLineSegment(sketch, "E13.14.0.8", {"start": v(-107.23, -17.46) * mm, "end": v(-112.73, -17.46) * mm});
            skLineSegment(sketch, "E13.17.0.8", {"start": v(-112.73, -17.46) * mm, "end": v(-115.48, -12.7) * mm});
            skCircle(sketch, "E13.0.0.9", {"center": v(-109.98, 0) * mm, "radius": 4.76 * mm, "construction": true});
            skLineSegment(sketch, "E13.2.0.9", {"start": v(-115.48, 0) * mm, "end": v(-112.73, 4.76) * mm});
            skLineSegment(sketch, "E13.5.0.9", {"start": v(-112.73, 4.76) * mm, "end": v(-107.23, 4.76) * mm});
            skLineSegment(sketch, "E13.8.0.9", {"start": v(-107.23, 4.76) * mm, "end": v(-104.48, 0) * mm});
            skLineSegment(sketch, "E13.11.0.9", {"start": v(-104.48, 0) * mm, "end": v(-107.23, -4.76) * mm});
            skLineSegment(sketch, "E13.14.0.9", {"start": v(-107.23, -4.76) * mm, "end": v(-112.73, -4.76) * mm});
            skLineSegment(sketch, "E13.17.0.9", {"start": v(-112.73, -4.76) * mm, "end": v(-115.48, 0) * mm});
            skCircle(sketch, "E13.0.0.10", {"center": v(-109.98, 12.7) * mm, "radius": 4.76 * mm, "construction": true});
            skLineSegment(sketch, "E13.2.0.10", {"start": v(-115.48, 12.7) * mm, "end": v(-112.73, 17.46) * mm});
            skLineSegment(sketch, "E13.5.0.10", {"start": v(-112.73, 17.46) * mm, "end": v(-107.23, 17.46) * mm});
            skLineSegment(sketch, "E13.8.0.10", {"start": v(-107.23, 17.46) * mm, "end": v(-104.48, 12.7) * mm});
            skLineSegment(sketch, "E13.11.0.10", {"start": v(-104.48, 12.7) * mm, "end": v(-107.23, 7.94) * mm});
            skLineSegment(sketch, "E13.14.0.10", {"start": v(-107.23, 7.94) * mm, "end": v(-112.73, 7.94) * mm});
            skLineSegment(sketch, "E13.17.0.10", {"start": v(-112.73, 7.94) * mm, "end": v(-115.48, 12.7) * mm});
            skCircle(sketch, "E13.0.0.11", {"center": v(-109.98, 25.4) * mm, "radius": 4.76 * mm, "construction": true});
            skLineSegment(sketch, "E13.2.0.11", {"start": v(-115.48, 25.4) * mm, "end": v(-112.73, 30.16) * mm});
            skLineSegment(sketch, "E13.5.0.11", {"start": v(-112.73, 30.16) * mm, "end": v(-107.23, 30.16) * mm});
            skLineSegment(sketch, "E13.8.0.11", {"start": v(-107.23, 30.16) * mm, "end": v(-104.48, 25.4) * mm});
            skLineSegment(sketch, "E13.11.0.11", {"start": v(-104.48, 25.4) * mm, "end": v(-107.23, 20.64) * mm});
            skLineSegment(sketch, "E13.14.0.11", {"start": v(-107.23, 20.64) * mm, "end": v(-112.73, 20.64) * mm});
            skLineSegment(sketch, "E13.17.0.11", {"start": v(-112.73, 20.64) * mm, "end": v(-115.48, 25.4) * mm});
            skCircle(sketch, "E13.0.0.12", {"center": v(-109.98, 38.1) * mm, "radius": 4.76 * mm, "construction": true});
            skLineSegment(sketch, "E13.2.0.12", {"start": v(-115.48, 38.1) * mm, "end": v(-112.73, 42.86) * mm});
            skLineSegment(sketch, "E13.5.0.12", {"start": v(-112.73, 42.86) * mm, "end": v(-107.23, 42.86) * mm});
            skLineSegment(sketch, "E13.8.0.12", {"start": v(-107.23, 42.86) * mm, "end": v(-104.48, 38.1) * mm});
            skLineSegment(sketch, "E13.11.0.12", {"start": v(-104.48, 38.1) * mm, "end": v(-107.23, 33.34) * mm});
            skLineSegment(sketch, "E13.14.0.12", {"start": v(-107.23, 33.34) * mm, "end": v(-112.73, 33.34) * mm});
            skLineSegment(sketch, "E13.17.0.12", {"start": v(-112.73, 33.34) * mm, "end": v(-115.48, 38.1) * mm});
            skCircle(sketch, "E13.0.0.13", {"center": v(-109.98, 50.8) * mm, "radius": 4.76 * mm, "construction": true});
            skLineSegment(sketch, "E13.2.0.13", {"start": v(-115.48, 50.8) * mm, "end": v(-112.73, 55.56) * mm});
            skLineSegment(sketch, "E13.5.0.13", {"start": v(-112.73, 55.56) * mm, "end": v(-107.23, 55.56) * mm});
            skLineSegment(sketch, "E13.8.0.13", {"start": v(-107.23, 55.56) * mm, "end": v(-104.48, 50.8) * mm});
            skLineSegment(sketch, "E13.11.0.13", {"start": v(-104.48, 50.8) * mm, "end": v(-107.23, 46.04) * mm});
            skLineSegment(sketch, "E13.14.0.13", {"start": v(-107.23, 46.04) * mm, "end": v(-112.73, 46.04) * mm});
            skLineSegment(sketch, "E13.17.0.13", {"start": v(-112.73, 46.04) * mm, "end": v(-115.48, 50.8) * mm});
            skCircle(sketch, "E13.0.0.14", {"center": v(-109.98, 63.5) * mm, "radius": 4.76 * mm, "construction": true});
            skLineSegment(sketch, "E13.2.0.14", {"start": v(-115.48, 63.5) * mm, "end": v(-112.73, 68.26) * mm});
            skLineSegment(sketch, "E13.5.0.14", {"start": v(-112.73, 68.26) * mm, "end": v(-107.23, 68.26) * mm});
            skLineSegment(sketch, "E13.8.0.14", {"start": v(-107.23, 68.26) * mm, "end": v(-104.48, 63.5) * mm});
            skLineSegment(sketch, "E13.11.0.14", {"start": v(-104.48, 63.5) * mm, "end": v(-107.23, 58.74) * mm});
            skLineSegment(sketch, "E13.14.0.14", {"start": v(-107.23, 58.74) * mm, "end": v(-112.73, 58.74) * mm});
            skLineSegment(sketch, "E13.17.0.14", {"start": v(-112.73, 58.74) * mm, "end": v(-115.48, 63.5) * mm});
            skCircle(sketch, "E13.0.0.15", {"center": v(-109.98, 76.2) * mm, "radius": 4.76 * mm, "construction": true});
            skLineSegment(sketch, "E13.2.0.15", {"start": v(-115.48, 76.2) * mm, "end": v(-112.73, 80.96) * mm});
            skLineSegment(sketch, "E13.5.0.15", {"start": v(-112.73, 80.96) * mm, "end": v(-107.23, 80.96) * mm});
            skLineSegment(sketch, "E13.8.0.15", {"start": v(-107.23, 80.96) * mm, "end": v(-104.48, 76.2) * mm});
            skLineSegment(sketch, "E13.11.0.15", {"start": v(-104.48, 76.2) * mm, "end": v(-107.23, 71.44) * mm});
            skLineSegment(sketch, "E13.14.0.15", {"start": v(-107.23, 71.44) * mm, "end": v(-112.73, 71.44) * mm});
            skLineSegment(sketch, "E13.17.0.15", {"start": v(-112.73, 71.44) * mm, "end": v(-115.48, 76.2) * mm});
            skCircle(sketch, "E13.0.0.16", {"center": v(-109.98, 88.9) * mm, "radius": 4.76 * mm, "construction": true});
            skLineSegment(sketch, "E13.2.0.16", {"start": v(-115.48, 88.9) * mm, "end": v(-112.73, 93.66) * mm});
            skLineSegment(sketch, "E13.5.0.16", {"start": v(-112.73, 93.66) * mm, "end": v(-107.23, 93.66) * mm});
            skLineSegment(sketch, "E13.8.0.16", {"start": v(-107.23, 93.66) * mm, "end": v(-104.48, 88.9) * mm});
            skLineSegment(sketch, "E13.11.0.16", {"start": v(-104.48, 88.9) * mm, "end": v(-107.23, 84.14) * mm});
            skLineSegment(sketch, "E13.14.0.16", {"start": v(-107.23, 84.14) * mm, "end": v(-112.73, 84.14) * mm});
            skLineSegment(sketch, "E13.17.0.16", {"start": v(-112.73, 84.14) * mm, "end": v(-115.48, 88.9) * mm});
            skCircle(sketch, "E13.0.0.17", {"center": v(-109.98, 101.6) * mm, "radius": 4.76 * mm, "construction": true});
            skLineSegment(sketch, "E13.2.0.17", {"start": v(-115.48, 101.6) * mm, "end": v(-112.73, 106.36) * mm});
            skLineSegment(sketch, "E13.5.0.17", {"start": v(-112.73, 106.36) * mm, "end": v(-107.23, 106.36) * mm});
            skLineSegment(sketch, "E13.8.0.17", {"start": v(-107.23, 106.36) * mm, "end": v(-104.48, 101.6) * mm});
            skLineSegment(sketch, "E13.11.0.17", {"start": v(-104.48, 101.6) * mm, "end": v(-107.23, 96.84) * mm});
            skLineSegment(sketch, "E13.14.0.17", {"start": v(-107.23, 96.84) * mm, "end": v(-112.73, 96.84) * mm});
            skLineSegment(sketch, "E13.17.0.17", {"start": v(-112.73, 96.84) * mm, "end": v(-115.48, 101.6) * mm});
            skCircle(sketch, "E13.0.0.18", {"center": v(-109.98, 114.3) * mm, "radius": 4.76 * mm, "construction": true});
            skLineSegment(sketch, "E13.2.0.18", {"start": v(-115.48, 114.3) * mm, "end": v(-112.73, 119.06) * mm});
            skLineSegment(sketch, "E13.5.0.18", {"start": v(-112.73, 119.06) * mm, "end": v(-107.23, 119.06) * mm});
            skLineSegment(sketch, "E13.8.0.18", {"start": v(-107.23, 119.06) * mm, "end": v(-104.48, 114.3) * mm});
            skLineSegment(sketch, "E13.11.0.18", {"start": v(-104.48, 114.3) * mm, "end": v(-107.23, 109.54) * mm});
            skLineSegment(sketch, "E13.14.0.18", {"start": v(-107.23, 109.54) * mm, "end": v(-112.73, 109.54) * mm});
            skLineSegment(sketch, "E13.17.0.18", {"start": v(-112.73, 109.54) * mm, "end": v(-115.48, 114.3) * mm});
            skCircle(sketch, "E13.0.0.19", {"center": v(-109.98, 127) * mm, "radius": 4.76 * mm, "construction": true});
            skLineSegment(sketch, "E13.2.0.19", {"start": v(-115.48, 127) * mm, "end": v(-112.73, 131.76) * mm});
            skLineSegment(sketch, "E13.5.0.19", {"start": v(-112.73, 131.76) * mm, "end": v(-107.23, 131.76) * mm});
            skLineSegment(sketch, "E13.8.0.19", {"start": v(-107.23, 131.76) * mm, "end": v(-104.48, 127) * mm});
            skLineSegment(sketch, "E13.11.0.19", {"start": v(-104.48, 127) * mm, "end": v(-107.23, 122.24) * mm});
            skLineSegment(sketch, "E13.14.0.19", {"start": v(-107.23, 122.24) * mm, "end": v(-112.73, 122.24) * mm});
            skLineSegment(sketch, "E13.17.0.19", {"start": v(-112.73, 122.24) * mm, "end": v(-115.48, 127) * mm});
            skCircle(sketch, "E13.0.1.8", {"center": v(-87.99, -12.7) * mm, "radius": 4.76 * mm, "construction": true});
            skLineSegment(sketch, "E13.2.1.8", {"start": v(-93.48, -12.7) * mm, "end": v(-90.74, -7.94) * mm});
            skLineSegment(sketch, "E13.5.1.8", {"start": v(-90.74, -7.94) * mm, "end": v(-85.24, -7.94) * mm});
            skLineSegment(sketch, "E13.8.1.8", {"start": v(-85.24, -7.94) * mm, "end": v(-82.49, -12.7) * mm});
            skLineSegment(sketch, "E13.11.1.8", {"start": v(-82.49, -12.7) * mm, "end": v(-85.24, -17.46) * mm});
            skLineSegment(sketch, "E13.14.1.8", {"start": v(-85.24, -17.46) * mm, "end": v(-90.74, -17.46) * mm});
            skLineSegment(sketch, "E13.17.1.8", {"start": v(-90.74, -17.46) * mm, "end": v(-93.48, -12.7) * mm});
            skCircle(sketch, "E13.0.1.9", {"center": v(-87.99, 0) * mm, "radius": 4.76 * mm, "construction": true});
            skLineSegment(sketch, "E13.2.1.9", {"start": v(-93.48, 0) * mm, "end": v(-90.74, 4.76) * mm});
            skLineSegment(sketch, "E13.5.1.9", {"start": v(-90.74, 4.76) * mm, "end": v(-85.24, 4.76) * mm});
            skLineSegment(sketch, "E13.8.1.9", {"start": v(-85.24, 4.76) * mm, "end": v(-82.49, 0) * mm});
            skLineSegment(sketch, "E13.11.1.9", {"start": v(-82.49, 0) * mm, "end": v(-85.24, -4.76) * mm});
            skLineSegment(sketch, "E13.14.1.9", {"start": v(-85.24, -4.76) * mm, "end": v(-90.74, -4.76) * mm});
            skLineSegment(sketch, "E13.17.1.9", {"start": v(-90.74, -4.76) * mm, "end": v(-93.48, 0) * mm});
            skCircle(sketch, "E13.0.1.10", {"center": v(-87.99, 12.7) * mm, "radius": 4.76 * mm, "construction": true});
            skLineSegment(sketch, "E13.2.1.10", {"start": v(-93.48, 12.7) * mm, "end": v(-90.74, 17.46) * mm});
            skLineSegment(sketch, "E13.5.1.10", {"start": v(-90.74, 17.46) * mm, "end": v(-85.24, 17.46) * mm});
            skLineSegment(sketch, "E13.8.1.10", {"start": v(-85.24, 17.46) * mm, "end": v(-82.49, 12.7) * mm});
            skLineSegment(sketch, "E13.11.1.10", {"start": v(-82.49, 12.7) * mm, "end": v(-85.24, 7.94) * mm});
            skLineSegment(sketch, "E13.14.1.10", {"start": v(-85.24, 7.94) * mm, "end": v(-90.74, 7.94) * mm});
            skLineSegment(sketch, "E13.17.1.10", {"start": v(-90.74, 7.94) * mm, "end": v(-93.48, 12.7) * mm});
            skCircle(sketch, "E13.0.1.11", {"center": v(-87.99, 25.4) * mm, "radius": 4.76 * mm, "construction": true});
            skLineSegment(sketch, "E13.2.1.11", {"start": v(-93.48, 25.4) * mm, "end": v(-90.74, 30.16) * mm});
            skLineSegment(sketch, "E13.5.1.11", {"start": v(-90.74, 30.16) * mm, "end": v(-85.24, 30.16) * mm});
            skLineSegment(sketch, "E13.8.1.11", {"start": v(-85.24, 30.16) * mm, "end": v(-82.49, 25.4) * mm});
            skLineSegment(sketch, "E13.11.1.11", {"start": v(-82.49, 25.4) * mm, "end": v(-85.24, 20.64) * mm});
            skLineSegment(sketch, "E13.14.1.11", {"start": v(-85.24, 20.64) * mm, "end": v(-90.74, 20.64) * mm});
            skLineSegment(sketch, "E13.17.1.11", {"start": v(-90.74, 20.64) * mm, "end": v(-93.48, 25.4) * mm});
            skCircle(sketch, "E13.0.1.12", {"center": v(-87.99, 38.1) * mm, "radius": 4.76 * mm, "construction": true});
            skLineSegment(sketch, "E13.2.1.12", {"start": v(-93.48, 38.1) * mm, "end": v(-90.74, 42.86) * mm});
            skLineSegment(sketch, "E13.5.1.12", {"start": v(-90.74, 42.86) * mm, "end": v(-85.24, 42.86) * mm});
            skLineSegment(sketch, "E13.8.1.12", {"start": v(-85.24, 42.86) * mm, "end": v(-82.49, 38.1) * mm});
            skLineSegment(sketch, "E13.11.1.12", {"start": v(-82.49, 38.1) * mm, "end": v(-85.24, 33.34) * mm});
            skLineSegment(sketch, "E13.14.1.12", {"start": v(-85.24, 33.34) * mm, "end": v(-90.74, 33.34) * mm});
            skLineSegment(sketch, "E13.17.1.12", {"start": v(-90.74, 33.34) * mm, "end": v(-93.48, 38.1) * mm});
            skCircle(sketch, "E13.0.1.13", {"center": v(-87.99, 50.8) * mm, "radius": 4.76 * mm, "construction": true});
            skLineSegment(sketch, "E13.2.1.13", {"start": v(-93.48, 50.8) * mm, "end": v(-90.74, 55.56) * mm});
            skLineSegment(sketch, "E13.5.1.13", {"start": v(-90.74, 55.56) * mm, "end": v(-85.24, 55.56) * mm});
            skLineSegment(sketch, "E13.8.1.13", {"start": v(-85.24, 55.56) * mm, "end": v(-82.49, 50.8) * mm});
            skLineSegment(sketch, "E13.11.1.13", {"start": v(-82.49, 50.8) * mm, "end": v(-85.24, 46.04) * mm});
            skLineSegment(sketch, "E13.14.1.13", {"start": v(-85.24, 46.04) * mm, "end": v(-90.74, 46.04) * mm});
            skLineSegment(sketch, "E13.17.1.13", {"start": v(-90.74, 46.04) * mm, "end": v(-93.48, 50.8) * mm});
            skCircle(sketch, "E13.0.1.14", {"center": v(-87.99, 63.5) * mm, "radius": 4.76 * mm, "construction": true});
            skLineSegment(sketch, "E13.2.1.14", {"start": v(-93.48, 63.5) * mm, "end": v(-90.74, 68.26) * mm});
            skLineSegment(sketch, "E13.5.1.14", {"start": v(-90.74, 68.26) * mm, "end": v(-85.24, 68.26) * mm});
            skLineSegment(sketch, "E13.8.1.14", {"start": v(-85.24, 68.26) * mm, "end": v(-82.49, 63.5) * mm});
            skLineSegment(sketch, "E13.11.1.14", {"start": v(-82.49, 63.5) * mm, "end": v(-85.24, 58.74) * mm});
            skLineSegment(sketch, "E13.14.1.14", {"start": v(-85.24, 58.74) * mm, "end": v(-90.74, 58.74) * mm});
            skLineSegment(sketch, "E13.17.1.14", {"start": v(-90.74, 58.74) * mm, "end": v(-93.48, 63.5) * mm});
            skCircle(sketch, "E13.0.1.15", {"center": v(-87.99, 76.2) * mm, "radius": 4.76 * mm, "construction": true});
            skLineSegment(sketch, "E13.2.1.15", {"start": v(-93.48, 76.2) * mm, "end": v(-90.74, 80.96) * mm});
            skLineSegment(sketch, "E13.5.1.15", {"start": v(-90.74, 80.96) * mm, "end": v(-85.24, 80.96) * mm});
            skLineSegment(sketch, "E13.8.1.15", {"start": v(-85.24, 80.96) * mm, "end": v(-82.49, 76.2) * mm});
            skLineSegment(sketch, "E13.11.1.15", {"start": v(-82.49, 76.2) * mm, "end": v(-85.24, 71.44) * mm});
            skLineSegment(sketch, "E13.14.1.15", {"start": v(-85.24, 71.44) * mm, "end": v(-90.74, 71.44) * mm});
            skLineSegment(sketch, "E13.17.1.15", {"start": v(-90.74, 71.44) * mm, "end": v(-93.48, 76.2) * mm});
            skCircle(sketch, "E13.0.1.16", {"center": v(-87.99, 88.9) * mm, "radius": 4.76 * mm, "construction": true});
            skLineSegment(sketch, "E13.2.1.16", {"start": v(-93.48, 88.9) * mm, "end": v(-90.74, 93.66) * mm});
            skLineSegment(sketch, "E13.5.1.16", {"start": v(-90.74, 93.66) * mm, "end": v(-85.24, 93.66) * mm});
            skLineSegment(sketch, "E13.8.1.16", {"start": v(-85.24, 93.66) * mm, "end": v(-82.49, 88.9) * mm});
            skLineSegment(sketch, "E13.11.1.16", {"start": v(-82.49, 88.9) * mm, "end": v(-85.24, 84.14) * mm});
            skLineSegment(sketch, "E13.14.1.16", {"start": v(-85.24, 84.14) * mm, "end": v(-90.74, 84.14) * mm});
            skLineSegment(sketch, "E13.17.1.16", {"start": v(-90.74, 84.14) * mm, "end": v(-93.48, 88.9) * mm});
            skCircle(sketch, "E13.0.1.17", {"center": v(-87.99, 101.6) * mm, "radius": 4.76 * mm, "construction": true});
            skLineSegment(sketch, "E13.2.1.17", {"start": v(-93.48, 101.6) * mm, "end": v(-90.74, 106.36) * mm});
            skLineSegment(sketch, "E13.5.1.17", {"start": v(-90.74, 106.36) * mm, "end": v(-85.24, 106.36) * mm});
            skLineSegment(sketch, "E13.8.1.17", {"start": v(-85.24, 106.36) * mm, "end": v(-82.49, 101.6) * mm});
            skLineSegment(sketch, "E13.11.1.17", {"start": v(-82.49, 101.6) * mm, "end": v(-85.24, 96.84) * mm});
            skLineSegment(sketch, "E13.14.1.17", {"start": v(-85.24, 96.84) * mm, "end": v(-90.74, 96.84) * mm});
            skLineSegment(sketch, "E13.17.1.17", {"start": v(-90.74, 96.84) * mm, "end": v(-93.48, 101.6) * mm});
            skCircle(sketch, "E13.0.1.18", {"center": v(-87.99, 114.3) * mm, "radius": 4.76 * mm, "construction": true});
            skLineSegment(sketch, "E13.2.1.18", {"start": v(-93.48, 114.3) * mm, "end": v(-90.74, 119.06) * mm});
            skLineSegment(sketch, "E13.5.1.18", {"start": v(-90.74, 119.06) * mm, "end": v(-85.24, 119.06) * mm});
            skLineSegment(sketch, "E13.8.1.18", {"start": v(-85.24, 119.06) * mm, "end": v(-82.49, 114.3) * mm});
            skLineSegment(sketch, "E13.11.1.18", {"start": v(-82.49, 114.3) * mm, "end": v(-85.24, 109.54) * mm});
            skLineSegment(sketch, "E13.14.1.18", {"start": v(-85.24, 109.54) * mm, "end": v(-90.74, 109.54) * mm});
            skLineSegment(sketch, "E13.17.1.18", {"start": v(-90.74, 109.54) * mm, "end": v(-93.48, 114.3) * mm});
            skCircle(sketch, "E13.0.1.19", {"center": v(-87.99, 127) * mm, "radius": 4.76 * mm, "construction": true});
            skLineSegment(sketch, "E13.2.1.19", {"start": v(-93.48, 127) * mm, "end": v(-90.74, 131.76) * mm});
            skLineSegment(sketch, "E13.5.1.19", {"start": v(-90.74, 131.76) * mm, "end": v(-85.24, 131.76) * mm});
            skLineSegment(sketch, "E13.8.1.19", {"start": v(-85.24, 131.76) * mm, "end": v(-82.49, 127) * mm});
            skLineSegment(sketch, "E13.11.1.19", {"start": v(-82.49, 127) * mm, "end": v(-85.24, 122.24) * mm});
            skLineSegment(sketch, "E13.14.1.19", {"start": v(-85.24, 122.24) * mm, "end": v(-90.74, 122.24) * mm});
            skLineSegment(sketch, "E13.17.1.19", {"start": v(-90.74, 122.24) * mm, "end": v(-93.48, 127) * mm});
            skCircle(sketch, "E13.0.2.8", {"center": v(-65.99, -12.7) * mm, "radius": 4.76 * mm, "construction": true});
            skLineSegment(sketch, "E13.2.2.8", {"start": v(-71.49, -12.7) * mm, "end": v(-68.74, -7.94) * mm});
            skLineSegment(sketch, "E13.5.2.8", {"start": v(-68.74, -7.94) * mm, "end": v(-63.24, -7.94) * mm});
            skLineSegment(sketch, "E13.8.2.8", {"start": v(-63.24, -7.94) * mm, "end": v(-60.49, -12.7) * mm});
            skLineSegment(sketch, "E13.11.2.8", {"start": v(-60.49, -12.7) * mm, "end": v(-63.24, -17.46) * mm});
            skLineSegment(sketch, "E13.14.2.8", {"start": v(-63.24, -17.46) * mm, "end": v(-68.74, -17.46) * mm});
            skLineSegment(sketch, "E13.17.2.8", {"start": v(-68.74, -17.46) * mm, "end": v(-71.49, -12.7) * mm});
            skCircle(sketch, "E13.0.2.9", {"center": v(-65.99, 0) * mm, "radius": 4.76 * mm, "construction": true});
            skLineSegment(sketch, "E13.2.2.9", {"start": v(-71.49, 0) * mm, "end": v(-68.74, 4.76) * mm});
            skLineSegment(sketch, "E13.5.2.9", {"start": v(-68.74, 4.76) * mm, "end": v(-63.24, 4.76) * mm});
            skLineSegment(sketch, "E13.8.2.9", {"start": v(-63.24, 4.76) * mm, "end": v(-60.49, 0) * mm});
            skLineSegment(sketch, "E13.11.2.9", {"start": v(-60.49, 0) * mm, "end": v(-63.24, -4.76) * mm});
            skLineSegment(sketch, "E13.14.2.9", {"start": v(-63.24, -4.76) * mm, "end": v(-68.74, -4.76) * mm});
            skLineSegment(sketch, "E13.17.2.9", {"start": v(-68.74, -4.76) * mm, "end": v(-71.49, 0) * mm});
            skCircle(sketch, "E13.0.2.10", {"center": v(-65.99, 12.7) * mm, "radius": 4.76 * mm, "construction": true});
            skLineSegment(sketch, "E13.2.2.10", {"start": v(-71.49, 12.7) * mm, "end": v(-68.74, 17.46) * mm});
            skLineSegment(sketch, "E13.5.2.10", {"start": v(-68.74, 17.46) * mm, "end": v(-63.24, 17.46) * mm});
            skLineSegment(sketch, "E13.8.2.10", {"start": v(-63.24, 17.46) * mm, "end": v(-60.49, 12.7) * mm});
            skLineSegment(sketch, "E13.11.2.10", {"start": v(-60.49, 12.7) * mm, "end": v(-63.24, 7.94) * mm});
            skLineSegment(sketch, "E13.14.2.10", {"start": v(-63.24, 7.94) * mm, "end": v(-68.74, 7.94) * mm});
            skLineSegment(sketch, "E13.17.2.10", {"start": v(-68.74, 7.94) * mm, "end": v(-71.49, 12.7) * mm});
            skCircle(sketch, "E13.0.2.11", {"center": v(-65.99, 25.4) * mm, "radius": 4.76 * mm, "construction": true});
            skLineSegment(sketch, "E13.2.2.11", {"start": v(-71.49, 25.4) * mm, "end": v(-68.74, 30.16) * mm});
            skLineSegment(sketch, "E13.5.2.11", {"start": v(-68.74, 30.16) * mm, "end": v(-63.24, 30.16) * mm});
            skLineSegment(sketch, "E13.8.2.11", {"start": v(-63.24, 30.16) * mm, "end": v(-60.49, 25.4) * mm});
            skLineSegment(sketch, "E13.11.2.11", {"start": v(-60.49, 25.4) * mm, "end": v(-63.24, 20.64) * mm});
            skLineSegment(sketch, "E13.14.2.11", {"start": v(-63.24, 20.64) * mm, "end": v(-68.74, 20.64) * mm});
            skLineSegment(sketch, "E13.17.2.11", {"start": v(-68.74, 20.64) * mm, "end": v(-71.49, 25.4) * mm});
            skCircle(sketch, "E13.0.2.12", {"center": v(-65.99, 38.1) * mm, "radius": 4.76 * mm, "construction": true});
            skLineSegment(sketch, "E13.2.2.12", {"start": v(-71.49, 38.1) * mm, "end": v(-68.74, 42.86) * mm});
            skLineSegment(sketch, "E13.5.2.12", {"start": v(-68.74, 42.86) * mm, "end": v(-63.24, 42.86) * mm});
            skLineSegment(sketch, "E13.8.2.12", {"start": v(-63.24, 42.86) * mm, "end": v(-60.49, 38.1) * mm});
            skLineSegment(sketch, "E13.11.2.12", {"start": v(-60.49, 38.1) * mm, "end": v(-63.24, 33.34) * mm});
            skLineSegment(sketch, "E13.14.2.12", {"start": v(-63.24, 33.34) * mm, "end": v(-68.74, 33.34) * mm});
            skLineSegment(sketch, "E13.17.2.12", {"start": v(-68.74, 33.34) * mm, "end": v(-71.49, 38.1) * mm});
            skCircle(sketch, "E13.0.2.13", {"center": v(-65.99, 50.8) * mm, "radius": 4.76 * mm, "construction": true});
            skLineSegment(sketch, "E13.2.2.13", {"start": v(-71.49, 50.8) * mm, "end": v(-68.74, 55.56) * mm});
            skLineSegment(sketch, "E13.5.2.13", {"start": v(-68.74, 55.56) * mm, "end": v(-63.24, 55.56) * mm});
            skLineSegment(sketch, "E13.8.2.13", {"start": v(-63.24, 55.56) * mm, "end": v(-60.49, 50.8) * mm});
            skLineSegment(sketch, "E13.11.2.13", {"start": v(-60.49, 50.8) * mm, "end": v(-63.24, 46.04) * mm});
            skLineSegment(sketch, "E13.14.2.13", {"start": v(-63.24, 46.04) * mm, "end": v(-68.74, 46.04) * mm});
            skLineSegment(sketch, "E13.17.2.13", {"start": v(-68.74, 46.04) * mm, "end": v(-71.49, 50.8) * mm});
            skCircle(sketch, "E13.0.2.14", {"center": v(-65.99, 63.5) * mm, "radius": 4.76 * mm, "construction": true});
            skLineSegment(sketch, "E13.2.2.14", {"start": v(-71.49, 63.5) * mm, "end": v(-68.74, 68.26) * mm});
            skLineSegment(sketch, "E13.5.2.14", {"start": v(-68.74, 68.26) * mm, "end": v(-63.24, 68.26) * mm});
            skLineSegment(sketch, "E13.8.2.14", {"start": v(-63.24, 68.26) * mm, "end": v(-60.49, 63.5) * mm});
            skLineSegment(sketch, "E13.11.2.14", {"start": v(-60.49, 63.5) * mm, "end": v(-63.24, 58.74) * mm});
            skLineSegment(sketch, "E13.14.2.14", {"start": v(-63.24, 58.74) * mm, "end": v(-68.74, 58.74) * mm});
            skLineSegment(sketch, "E13.17.2.14", {"start": v(-68.74, 58.74) * mm, "end": v(-71.49, 63.5) * mm});
            skCircle(sketch, "E13.0.2.15", {"center": v(-65.99, 76.2) * mm, "radius": 4.76 * mm, "construction": true});
            skLineSegment(sketch, "E13.2.2.15", {"start": v(-71.49, 76.2) * mm, "end": v(-68.74, 80.96) * mm});
            skLineSegment(sketch, "E13.5.2.15", {"start": v(-68.74, 80.96) * mm, "end": v(-63.24, 80.96) * mm});
            skLineSegment(sketch, "E13.8.2.15", {"start": v(-63.24, 80.96) * mm, "end": v(-60.49, 76.2) * mm});
            skLineSegment(sketch, "E13.11.2.15", {"start": v(-60.49, 76.2) * mm, "end": v(-63.24, 71.44) * mm});
            skLineSegment(sketch, "E13.14.2.15", {"start": v(-63.24, 71.44) * mm, "end": v(-68.74, 71.44) * mm});
            skLineSegment(sketch, "E13.17.2.15", {"start": v(-68.74, 71.44) * mm, "end": v(-71.49, 76.2) * mm});
            skCircle(sketch, "E13.0.2.16", {"center": v(-65.99, 88.9) * mm, "radius": 4.76 * mm, "construction": true});
            skLineSegment(sketch, "E13.2.2.16", {"start": v(-71.49, 88.9) * mm, "end": v(-68.74, 93.66) * mm});
            skLineSegment(sketch, "E13.5.2.16", {"start": v(-68.74, 93.66) * mm, "end": v(-63.24, 93.66) * mm});
            skLineSegment(sketch, "E13.8.2.16", {"start": v(-63.24, 93.66) * mm, "end": v(-60.49, 88.9) * mm});
            skLineSegment(sketch, "E13.11.2.16", {"start": v(-60.49, 88.9) * mm, "end": v(-63.24, 84.14) * mm});
            skLineSegment(sketch, "E13.14.2.16", {"start": v(-63.24, 84.14) * mm, "end": v(-68.74, 84.14) * mm});
            skLineSegment(sketch, "E13.17.2.16", {"start": v(-68.74, 84.14) * mm, "end": v(-71.49, 88.9) * mm});
            skCircle(sketch, "E13.0.2.17", {"center": v(-65.99, 101.6) * mm, "radius": 4.76 * mm, "construction": true});
            skLineSegment(sketch, "E13.2.2.17", {"start": v(-71.49, 101.6) * mm, "end": v(-68.74, 106.36) * mm});
            skLineSegment(sketch, "E13.5.2.17", {"start": v(-68.74, 106.36) * mm, "end": v(-63.24, 106.36) * mm});
            skLineSegment(sketch, "E13.8.2.17", {"start": v(-63.24, 106.36) * mm, "end": v(-60.49, 101.6) * mm});
            skLineSegment(sketch, "E13.11.2.17", {"start": v(-60.49, 101.6) * mm, "end": v(-63.24, 96.84) * mm});
            skLineSegment(sketch, "E13.14.2.17", {"start": v(-63.24, 96.84) * mm, "end": v(-68.74, 96.84) * mm});
            skLineSegment(sketch, "E13.17.2.17", {"start": v(-68.74, 96.84) * mm, "end": v(-71.49, 101.6) * mm});
            skCircle(sketch, "E13.0.2.18", {"center": v(-65.99, 114.3) * mm, "radius": 4.76 * mm, "construction": true});
            skLineSegment(sketch, "E13.2.2.18", {"start": v(-71.49, 114.3) * mm, "end": v(-68.74, 119.06) * mm});
            skLineSegment(sketch, "E13.5.2.18", {"start": v(-68.74, 119.06) * mm, "end": v(-63.24, 119.06) * mm});
            skLineSegment(sketch, "E13.8.2.18", {"start": v(-63.24, 119.06) * mm, "end": v(-60.49, 114.3) * mm});
            skLineSegment(sketch, "E13.11.2.18", {"start": v(-60.49, 114.3) * mm, "end": v(-63.24, 109.54) * mm});
            skLineSegment(sketch, "E13.14.2.18", {"start": v(-63.24, 109.54) * mm, "end": v(-68.74, 109.54) * mm});
            skLineSegment(sketch, "E13.17.2.18", {"start": v(-68.74, 109.54) * mm, "end": v(-71.49, 114.3) * mm});
            skCircle(sketch, "E13.0.2.19", {"center": v(-65.99, 127) * mm, "radius": 4.76 * mm, "construction": true});
            skLineSegment(sketch, "E13.2.2.19", {"start": v(-71.49, 127) * mm, "end": v(-68.74, 131.76) * mm});
            skLineSegment(sketch, "E13.5.2.19", {"start": v(-68.74, 131.76) * mm, "end": v(-63.24, 131.76) * mm});
            skLineSegment(sketch, "E13.8.2.19", {"start": v(-63.24, 131.76) * mm, "end": v(-60.49, 127) * mm});
            skLineSegment(sketch, "E13.11.2.19", {"start": v(-60.49, 127) * mm, "end": v(-63.24, 122.24) * mm});
            skLineSegment(sketch, "E13.14.2.19", {"start": v(-63.24, 122.24) * mm, "end": v(-68.74, 122.24) * mm});
            skLineSegment(sketch, "E13.17.2.19", {"start": v(-68.74, 122.24) * mm, "end": v(-71.49, 127) * mm});
            skCircle(sketch, "E13.0.3.8", {"center": v(-44, -12.7) * mm, "radius": 4.76 * mm, "construction": true});
            skLineSegment(sketch, "E13.2.3.8", {"start": v(-49.5, -12.7) * mm, "end": v(-46.74, -7.94) * mm});
            skLineSegment(sketch, "E13.5.3.8", {"start": v(-46.74, -7.94) * mm, "end": v(-41.24, -7.94) * mm});
            skLineSegment(sketch, "E13.8.3.8", {"start": v(-41.24, -7.94) * mm, "end": v(-38.5, -12.7) * mm});
            skLineSegment(sketch, "E13.11.3.8", {"start": v(-38.5, -12.7) * mm, "end": v(-41.24, -17.46) * mm});
            skLineSegment(sketch, "E13.14.3.8", {"start": v(-41.24, -17.46) * mm, "end": v(-46.74, -17.46) * mm});
            skLineSegment(sketch, "E13.17.3.8", {"start": v(-46.74, -17.46) * mm, "end": v(-49.5, -12.7) * mm});
            skCircle(sketch, "E13.0.3.9", {"center": v(-44, 0) * mm, "radius": 4.76 * mm, "construction": true});
            skLineSegment(sketch, "E13.2.3.9", {"start": v(-49.5, 0) * mm, "end": v(-46.74, 4.76) * mm});
            skLineSegment(sketch, "E13.5.3.9", {"start": v(-46.74, 4.76) * mm, "end": v(-41.24, 4.76) * mm});
            skLineSegment(sketch, "E13.8.3.9", {"start": v(-41.24, 4.76) * mm, "end": v(-38.5, 0) * mm});
            skLineSegment(sketch, "E13.11.3.9", {"start": v(-38.5, 0) * mm, "end": v(-41.24, -4.76) * mm});
            skLineSegment(sketch, "E13.14.3.9", {"start": v(-41.24, -4.76) * mm, "end": v(-46.74, -4.76) * mm});
            skLineSegment(sketch, "E13.17.3.9", {"start": v(-46.74, -4.76) * mm, "end": v(-49.5, 0) * mm});
            skCircle(sketch, "E13.0.3.10", {"center": v(-44, 12.7) * mm, "radius": 4.76 * mm, "construction": true});
            skLineSegment(sketch, "E13.2.3.10", {"start": v(-49.5, 12.7) * mm, "end": v(-46.74, 17.46) * mm});
            skLineSegment(sketch, "E13.5.3.10", {"start": v(-46.74, 17.46) * mm, "end": v(-41.24, 17.46) * mm});
            skLineSegment(sketch, "E13.8.3.10", {"start": v(-41.24, 17.46) * mm, "end": v(-38.5, 12.7) * mm});
            skLineSegment(sketch, "E13.11.3.10", {"start": v(-38.5, 12.7) * mm, "end": v(-41.24, 7.94) * mm});
            skLineSegment(sketch, "E13.14.3.10", {"start": v(-41.24, 7.94) * mm, "end": v(-46.74, 7.94) * mm});
            skLineSegment(sketch, "E13.17.3.10", {"start": v(-46.74, 7.94) * mm, "end": v(-49.5, 12.7) * mm});
            skCircle(sketch, "E13.0.3.11", {"center": v(-44, 25.4) * mm, "radius": 4.76 * mm, "construction": true});
            skLineSegment(sketch, "E13.2.3.11", {"start": v(-49.5, 25.4) * mm, "end": v(-46.74, 30.16) * mm});
            skLineSegment(sketch, "E13.5.3.11", {"start": v(-46.74, 30.16) * mm, "end": v(-41.24, 30.16) * mm});
            skLineSegment(sketch, "E13.8.3.11", {"start": v(-41.24, 30.16) * mm, "end": v(-38.5, 25.4) * mm});
            skLineSegment(sketch, "E13.11.3.11", {"start": v(-38.5, 25.4) * mm, "end": v(-41.24, 20.64) * mm});
            skLineSegment(sketch, "E13.14.3.11", {"start": v(-41.24, 20.64) * mm, "end": v(-46.74, 20.64) * mm});
            skLineSegment(sketch, "E13.17.3.11", {"start": v(-46.74, 20.64) * mm, "end": v(-49.5, 25.4) * mm});
            skCircle(sketch, "E13.0.3.12", {"center": v(-44, 38.1) * mm, "radius": 4.76 * mm, "construction": true});
            skLineSegment(sketch, "E13.2.3.12", {"start": v(-49.5, 38.1) * mm, "end": v(-46.74, 42.86) * mm});
            skLineSegment(sketch, "E13.5.3.12", {"start": v(-46.74, 42.86) * mm, "end": v(-41.24, 42.86) * mm});
            skLineSegment(sketch, "E13.8.3.12", {"start": v(-41.24, 42.86) * mm, "end": v(-38.5, 38.1) * mm});
            skLineSegment(sketch, "E13.11.3.12", {"start": v(-38.5, 38.1) * mm, "end": v(-41.24, 33.34) * mm});
            skLineSegment(sketch, "E13.14.3.12", {"start": v(-41.24, 33.34) * mm, "end": v(-46.74, 33.34) * mm});
            skLineSegment(sketch, "E13.17.3.12", {"start": v(-46.74, 33.34) * mm, "end": v(-49.5, 38.1) * mm});
            skCircle(sketch, "E13.0.3.13", {"center": v(-44, 50.8) * mm, "radius": 4.76 * mm, "construction": true});
            skLineSegment(sketch, "E13.2.3.13", {"start": v(-49.5, 50.8) * mm, "end": v(-46.74, 55.56) * mm});
            skLineSegment(sketch, "E13.5.3.13", {"start": v(-46.74, 55.56) * mm, "end": v(-41.24, 55.56) * mm});
            skLineSegment(sketch, "E13.8.3.13", {"start": v(-41.24, 55.56) * mm, "end": v(-38.5, 50.8) * mm});
            skLineSegment(sketch, "E13.11.3.13", {"start": v(-38.5, 50.8) * mm, "end": v(-41.24, 46.04) * mm});
            skLineSegment(sketch, "E13.14.3.13", {"start": v(-41.24, 46.04) * mm, "end": v(-46.74, 46.04) * mm});
            skLineSegment(sketch, "E13.17.3.13", {"start": v(-46.74, 46.04) * mm, "end": v(-49.5, 50.8) * mm});
            skCircle(sketch, "E13.0.3.14", {"center": v(-44, 63.5) * mm, "radius": 4.76 * mm, "construction": true});
            skLineSegment(sketch, "E13.2.3.14", {"start": v(-49.5, 63.5) * mm, "end": v(-46.74, 68.26) * mm});
            skLineSegment(sketch, "E13.5.3.14", {"start": v(-46.74, 68.26) * mm, "end": v(-41.24, 68.26) * mm});
            skLineSegment(sketch, "E13.8.3.14", {"start": v(-41.24, 68.26) * mm, "end": v(-38.5, 63.5) * mm});
            skLineSegment(sketch, "E13.11.3.14", {"start": v(-38.5, 63.5) * mm, "end": v(-41.24, 58.74) * mm});
            skLineSegment(sketch, "E13.14.3.14", {"start": v(-41.24, 58.74) * mm, "end": v(-46.74, 58.74) * mm});
            skLineSegment(sketch, "E13.17.3.14", {"start": v(-46.74, 58.74) * mm, "end": v(-49.5, 63.5) * mm});
            skCircle(sketch, "E13.0.3.15", {"center": v(-44, 76.2) * mm, "radius": 4.76 * mm, "construction": true});
            skLineSegment(sketch, "E13.2.3.15", {"start": v(-49.5, 76.2) * mm, "end": v(-46.74, 80.96) * mm});
            skLineSegment(sketch, "E13.5.3.15", {"start": v(-46.74, 80.96) * mm, "end": v(-41.24, 80.96) * mm});
            skLineSegment(sketch, "E13.8.3.15", {"start": v(-41.24, 80.96) * mm, "end": v(-38.5, 76.2) * mm});
            skLineSegment(sketch, "E13.11.3.15", {"start": v(-38.5, 76.2) * mm, "end": v(-41.24, 71.44) * mm});
            skLineSegment(sketch, "E13.14.3.15", {"start": v(-41.24, 71.44) * mm, "end": v(-46.74, 71.44) * mm});
            skLineSegment(sketch, "E13.17.3.15", {"start": v(-46.74, 71.44) * mm, "end": v(-49.5, 76.2) * mm});
            skCircle(sketch, "E13.0.3.16", {"center": v(-44, 88.9) * mm, "radius": 4.76 * mm, "construction": true});
            skLineSegment(sketch, "E13.2.3.16", {"start": v(-49.5, 88.9) * mm, "end": v(-46.74, 93.66) * mm});
            skLineSegment(sketch, "E13.5.3.16", {"start": v(-46.74, 93.66) * mm, "end": v(-41.24, 93.66) * mm});
            skLineSegment(sketch, "E13.8.3.16", {"start": v(-41.24, 93.66) * mm, "end": v(-38.5, 88.9) * mm});
            skLineSegment(sketch, "E13.11.3.16", {"start": v(-38.5, 88.9) * mm, "end": v(-41.24, 84.14) * mm});
            skLineSegment(sketch, "E13.14.3.16", {"start": v(-41.24, 84.14) * mm, "end": v(-46.74, 84.14) * mm});
            skLineSegment(sketch, "E13.17.3.16", {"start": v(-46.74, 84.14) * mm, "end": v(-49.5, 88.9) * mm});
            skCircle(sketch, "E13.0.3.17", {"center": v(-44, 101.6) * mm, "radius": 4.76 * mm, "construction": true});
            skLineSegment(sketch, "E13.2.3.17", {"start": v(-49.5, 101.6) * mm, "end": v(-46.74, 106.36) * mm});
            skLineSegment(sketch, "E13.5.3.17", {"start": v(-46.74, 106.36) * mm, "end": v(-41.24, 106.36) * mm});
            skLineSegment(sketch, "E13.8.3.17", {"start": v(-41.24, 106.36) * mm, "end": v(-38.5, 101.6) * mm});
            skLineSegment(sketch, "E13.11.3.17", {"start": v(-38.5, 101.6) * mm, "end": v(-41.24, 96.84) * mm});
            skLineSegment(sketch, "E13.14.3.17", {"start": v(-41.24, 96.84) * mm, "end": v(-46.74, 96.84) * mm});
            skLineSegment(sketch, "E13.17.3.17", {"start": v(-46.74, 96.84) * mm, "end": v(-49.5, 101.6) * mm});
            skCircle(sketch, "E13.0.3.18", {"center": v(-44, 114.3) * mm, "radius": 4.76 * mm, "construction": true});
            skLineSegment(sketch, "E13.2.3.18", {"start": v(-49.5, 114.3) * mm, "end": v(-46.74, 119.06) * mm});
            skLineSegment(sketch, "E13.5.3.18", {"start": v(-46.74, 119.06) * mm, "end": v(-41.24, 119.06) * mm});
            skLineSegment(sketch, "E13.8.3.18", {"start": v(-41.24, 119.06) * mm, "end": v(-38.5, 114.3) * mm});
            skLineSegment(sketch, "E13.11.3.18", {"start": v(-38.5, 114.3) * mm, "end": v(-41.24, 109.54) * mm});
            skLineSegment(sketch, "E13.14.3.18", {"start": v(-41.24, 109.54) * mm, "end": v(-46.74, 109.54) * mm});
            skLineSegment(sketch, "E13.17.3.18", {"start": v(-46.74, 109.54) * mm, "end": v(-49.5, 114.3) * mm});
            skCircle(sketch, "E13.0.3.19", {"center": v(-44, 127) * mm, "radius": 4.76 * mm, "construction": true});
            skLineSegment(sketch, "E13.2.3.19", {"start": v(-49.5, 127) * mm, "end": v(-46.74, 131.76) * mm});
            skLineSegment(sketch, "E13.5.3.19", {"start": v(-46.74, 131.76) * mm, "end": v(-41.24, 131.76) * mm});
            skLineSegment(sketch, "E13.8.3.19", {"start": v(-41.24, 131.76) * mm, "end": v(-38.5, 127) * mm});
            skLineSegment(sketch, "E13.11.3.19", {"start": v(-38.5, 127) * mm, "end": v(-41.24, 122.24) * mm});
            skLineSegment(sketch, "E13.14.3.19", {"start": v(-41.24, 122.24) * mm, "end": v(-46.74, 122.24) * mm});
            skLineSegment(sketch, "E13.17.3.19", {"start": v(-46.74, 122.24) * mm, "end": v(-49.5, 127) * mm});
            skCircle(sketch, "E13.0.4.8", {"center": v(-22, -12.7) * mm, "radius": 4.76 * mm, "construction": true});
            skLineSegment(sketch, "E13.2.4.8", {"start": v(-27.5, -12.7) * mm, "end": v(-24.75, -7.94) * mm});
            skLineSegment(sketch, "E13.5.4.8", {"start": v(-24.75, -7.94) * mm, "end": v(-19.25, -7.94) * mm});
            skLineSegment(sketch, "E13.8.4.8", {"start": v(-19.25, -7.94) * mm, "end": v(-16.5, -12.7) * mm});
            skLineSegment(sketch, "E13.11.4.8", {"start": v(-16.5, -12.7) * mm, "end": v(-19.25, -17.46) * mm});
            skLineSegment(sketch, "E13.14.4.8", {"start": v(-19.25, -17.46) * mm, "end": v(-24.75, -17.46) * mm});
            skLineSegment(sketch, "E13.17.4.8", {"start": v(-24.75, -17.46) * mm, "end": v(-27.5, -12.7) * mm});
            skCircle(sketch, "E13.0.4.9", {"center": v(-22, 0) * mm, "radius": 4.76 * mm, "construction": true});
            skLineSegment(sketch, "E13.2.4.9", {"start": v(-27.5, 0) * mm, "end": v(-24.75, 4.76) * mm});
            skLineSegment(sketch, "E13.5.4.9", {"start": v(-24.75, 4.76) * mm, "end": v(-19.25, 4.76) * mm});
            skLineSegment(sketch, "E13.8.4.9", {"start": v(-19.25, 4.76) * mm, "end": v(-16.5, 0) * mm});
            skLineSegment(sketch, "E13.11.4.9", {"start": v(-16.5, 0) * mm, "end": v(-19.25, -4.76) * mm});
            skLineSegment(sketch, "E13.14.4.9", {"start": v(-19.25, -4.76) * mm, "end": v(-24.75, -4.76) * mm});
            skLineSegment(sketch, "E13.17.4.9", {"start": v(-24.75, -4.76) * mm, "end": v(-27.5, 0) * mm});
            skCircle(sketch, "E13.0.4.10", {"center": v(-22, 12.7) * mm, "radius": 4.76 * mm, "construction": true});
            skLineSegment(sketch, "E13.2.4.10", {"start": v(-27.5, 12.7) * mm, "end": v(-24.75, 17.46) * mm});
            skLineSegment(sketch, "E13.5.4.10", {"start": v(-24.75, 17.46) * mm, "end": v(-19.25, 17.46) * mm});
            skLineSegment(sketch, "E13.8.4.10", {"start": v(-19.25, 17.46) * mm, "end": v(-16.5, 12.7) * mm});
            skLineSegment(sketch, "E13.11.4.10", {"start": v(-16.5, 12.7) * mm, "end": v(-19.25, 7.94) * mm});
            skLineSegment(sketch, "E13.14.4.10", {"start": v(-19.25, 7.94) * mm, "end": v(-24.75, 7.94) * mm});
            skLineSegment(sketch, "E13.17.4.10", {"start": v(-24.75, 7.94) * mm, "end": v(-27.5, 12.7) * mm});
            skCircle(sketch, "E13.0.4.11", {"center": v(-22, 25.4) * mm, "radius": 4.76 * mm, "construction": true});
            skLineSegment(sketch, "E13.2.4.11", {"start": v(-27.5, 25.4) * mm, "end": v(-24.75, 30.16) * mm});
            skLineSegment(sketch, "E13.5.4.11", {"start": v(-24.75, 30.16) * mm, "end": v(-19.25, 30.16) * mm});
            skLineSegment(sketch, "E13.8.4.11", {"start": v(-19.25, 30.16) * mm, "end": v(-16.5, 25.4) * mm});
            skLineSegment(sketch, "E13.11.4.11", {"start": v(-16.5, 25.4) * mm, "end": v(-19.25, 20.64) * mm});
            skLineSegment(sketch, "E13.14.4.11", {"start": v(-19.25, 20.64) * mm, "end": v(-24.75, 20.64) * mm});
            skLineSegment(sketch, "E13.17.4.11", {"start": v(-24.75, 20.64) * mm, "end": v(-27.5, 25.4) * mm});
            skCircle(sketch, "E13.0.4.12", {"center": v(-22, 38.1) * mm, "radius": 4.76 * mm, "construction": true});
            skLineSegment(sketch, "E13.2.4.12", {"start": v(-27.5, 38.1) * mm, "end": v(-24.75, 42.86) * mm});
            skLineSegment(sketch, "E13.5.4.12", {"start": v(-24.75, 42.86) * mm, "end": v(-19.25, 42.86) * mm});
            skLineSegment(sketch, "E13.8.4.12", {"start": v(-19.25, 42.86) * mm, "end": v(-16.5, 38.1) * mm});
            skLineSegment(sketch, "E13.11.4.12", {"start": v(-16.5, 38.1) * mm, "end": v(-19.25, 33.34) * mm});
            skLineSegment(sketch, "E13.14.4.12", {"start": v(-19.25, 33.34) * mm, "end": v(-24.75, 33.34) * mm});
            skLineSegment(sketch, "E13.17.4.12", {"start": v(-24.75, 33.34) * mm, "end": v(-27.5, 38.1) * mm});
            skCircle(sketch, "E13.0.4.13", {"center": v(-22, 50.8) * mm, "radius": 4.76 * mm, "construction": true});
            skLineSegment(sketch, "E13.2.4.13", {"start": v(-27.5, 50.8) * mm, "end": v(-24.75, 55.56) * mm});
            skLineSegment(sketch, "E13.5.4.13", {"start": v(-24.75, 55.56) * mm, "end": v(-19.25, 55.56) * mm});
            skLineSegment(sketch, "E13.8.4.13", {"start": v(-19.25, 55.56) * mm, "end": v(-16.5, 50.8) * mm});
            skLineSegment(sketch, "E13.11.4.13", {"start": v(-16.5, 50.8) * mm, "end": v(-19.25, 46.04) * mm});
            skLineSegment(sketch, "E13.14.4.13", {"start": v(-19.25, 46.04) * mm, "end": v(-24.75, 46.04) * mm});
            skLineSegment(sketch, "E13.17.4.13", {"start": v(-24.75, 46.04) * mm, "end": v(-27.5, 50.8) * mm});
            skCircle(sketch, "E13.0.4.14", {"center": v(-22, 63.5) * mm, "radius": 4.76 * mm, "construction": true});
            skLineSegment(sketch, "E13.2.4.14", {"start": v(-27.5, 63.5) * mm, "end": v(-24.75, 68.26) * mm});
            skLineSegment(sketch, "E13.5.4.14", {"start": v(-24.75, 68.26) * mm, "end": v(-19.25, 68.26) * mm});
            skLineSegment(sketch, "E13.8.4.14", {"start": v(-19.25, 68.26) * mm, "end": v(-16.5, 63.5) * mm});
            skLineSegment(sketch, "E13.11.4.14", {"start": v(-16.5, 63.5) * mm, "end": v(-19.25, 58.74) * mm});
            skLineSegment(sketch, "E13.14.4.14", {"start": v(-19.25, 58.74) * mm, "end": v(-24.75, 58.74) * mm});
            skLineSegment(sketch, "E13.17.4.14", {"start": v(-24.75, 58.74) * mm, "end": v(-27.5, 63.5) * mm});
            skCircle(sketch, "E13.0.4.15", {"center": v(-22, 76.2) * mm, "radius": 4.76 * mm, "construction": true});
            skLineSegment(sketch, "E13.2.4.15", {"start": v(-27.5, 76.2) * mm, "end": v(-24.75, 80.96) * mm});
            skLineSegment(sketch, "E13.5.4.15", {"start": v(-24.75, 80.96) * mm, "end": v(-19.25, 80.96) * mm});
            skLineSegment(sketch, "E13.8.4.15", {"start": v(-19.25, 80.96) * mm, "end": v(-16.5, 76.2) * mm});
            skLineSegment(sketch, "E13.11.4.15", {"start": v(-16.5, 76.2) * mm, "end": v(-19.25, 71.44) * mm});
            skLineSegment(sketch, "E13.14.4.15", {"start": v(-19.25, 71.44) * mm, "end": v(-24.75, 71.44) * mm});
            skLineSegment(sketch, "E13.17.4.15", {"start": v(-24.75, 71.44) * mm, "end": v(-27.5, 76.2) * mm});
            skCircle(sketch, "E13.0.4.16", {"center": v(-22, 88.9) * mm, "radius": 4.76 * mm, "construction": true});
            skLineSegment(sketch, "E13.2.4.16", {"start": v(-27.5, 88.9) * mm, "end": v(-24.75, 93.66) * mm});
            skLineSegment(sketch, "E13.5.4.16", {"start": v(-24.75, 93.66) * mm, "end": v(-19.25, 93.66) * mm});
            skLineSegment(sketch, "E13.8.4.16", {"start": v(-19.25, 93.66) * mm, "end": v(-16.5, 88.9) * mm});
            skLineSegment(sketch, "E13.11.4.16", {"start": v(-16.5, 88.9) * mm, "end": v(-19.25, 84.14) * mm});
            skLineSegment(sketch, "E13.14.4.16", {"start": v(-19.25, 84.14) * mm, "end": v(-24.75, 84.14) * mm});
            skLineSegment(sketch, "E13.17.4.16", {"start": v(-24.75, 84.14) * mm, "end": v(-27.5, 88.9) * mm});
            skCircle(sketch, "E13.0.4.17", {"center": v(-22, 101.6) * mm, "radius": 4.76 * mm, "construction": true});
            skLineSegment(sketch, "E13.2.4.17", {"start": v(-27.5, 101.6) * mm, "end": v(-24.75, 106.36) * mm});
            skLineSegment(sketch, "E13.5.4.17", {"start": v(-24.75, 106.36) * mm, "end": v(-19.25, 106.36) * mm});
            skLineSegment(sketch, "E13.8.4.17", {"start": v(-19.25, 106.36) * mm, "end": v(-16.5, 101.6) * mm});
            skLineSegment(sketch, "E13.11.4.17", {"start": v(-16.5, 101.6) * mm, "end": v(-19.25, 96.84) * mm});
            skLineSegment(sketch, "E13.14.4.17", {"start": v(-19.25, 96.84) * mm, "end": v(-24.75, 96.84) * mm});
            skLineSegment(sketch, "E13.17.4.17", {"start": v(-24.75, 96.84) * mm, "end": v(-27.5, 101.6) * mm});
            skCircle(sketch, "E13.0.4.18", {"center": v(-22, 114.3) * mm, "radius": 4.76 * mm, "construction": true});
            skLineSegment(sketch, "E13.2.4.18", {"start": v(-27.5, 114.3) * mm, "end": v(-24.75, 119.06) * mm});
            skLineSegment(sketch, "E13.5.4.18", {"start": v(-24.75, 119.06) * mm, "end": v(-19.25, 119.06) * mm});
            skLineSegment(sketch, "E13.8.4.18", {"start": v(-19.25, 119.06) * mm, "end": v(-16.5, 114.3) * mm});
            skLineSegment(sketch, "E13.11.4.18", {"start": v(-16.5, 114.3) * mm, "end": v(-19.25, 109.54) * mm});
            skLineSegment(sketch, "E13.14.4.18", {"start": v(-19.25, 109.54) * mm, "end": v(-24.75, 109.54) * mm});
            skLineSegment(sketch, "E13.17.4.18", {"start": v(-24.75, 109.54) * mm, "end": v(-27.5, 114.3) * mm});
            skCircle(sketch, "E13.0.4.19", {"center": v(-22, 127) * mm, "radius": 4.76 * mm, "construction": true});
            skLineSegment(sketch, "E13.2.4.19", {"start": v(-27.5, 127) * mm, "end": v(-24.75, 131.76) * mm});
            skLineSegment(sketch, "E13.5.4.19", {"start": v(-24.75, 131.76) * mm, "end": v(-19.25, 131.76) * mm});
            skLineSegment(sketch, "E13.8.4.19", {"start": v(-19.25, 131.76) * mm, "end": v(-16.5, 127) * mm});
            skLineSegment(sketch, "E13.11.4.19", {"start": v(-16.5, 127) * mm, "end": v(-19.25, 122.24) * mm});
            skLineSegment(sketch, "E13.14.4.19", {"start": v(-19.25, 122.24) * mm, "end": v(-24.75, 122.24) * mm});
            skLineSegment(sketch, "E13.17.4.19", {"start": v(-24.75, 122.24) * mm, "end": v(-27.5, 127) * mm});
            skLineSegment(sketch, "E14.0.6.0", {"start": v(8.25, -115.89) * mm, "end": v(13.75, -115.89) * mm});
            skLineSegment(sketch, "E14.3.6.0", {"start": v(13.75, -115.89) * mm, "end": v(16.5, -120.65) * mm});
            skLineSegment(sketch, "E14.6.6.0", {"start": v(16.5, -120.65) * mm, "end": v(13.75, -125.41) * mm});
            skCircle(sketch, "E14.9.6.0", {"center": v(11, -120.65) * mm, "radius": 4.76 * mm, "construction": true});
            skLineSegment(sketch, "E14.11.6.0", {"start": v(13.75, -125.41) * mm, "end": v(8.25, -125.41) * mm});
            skLineSegment(sketch, "E14.14.6.0", {"start": v(8.25, -125.41) * mm, "end": v(5.5, -120.65) * mm});
            skLineSegment(sketch, "E14.17.6.0", {"start": v(5.5, -120.65) * mm, "end": v(8.25, -115.89) * mm});
            skLineSegment(sketch, "E14.0.6.1", {"start": v(8.25, -103.19) * mm, "end": v(13.75, -103.19) * mm});
            skLineSegment(sketch, "E14.3.6.1", {"start": v(13.75, -103.19) * mm, "end": v(16.5, -107.95) * mm});
            skLineSegment(sketch, "E14.6.6.1", {"start": v(16.5, -107.95) * mm, "end": v(13.75, -112.71) * mm});
            skCircle(sketch, "E14.9.6.1", {"center": v(11, -107.95) * mm, "radius": 4.76 * mm, "construction": true});
            skLineSegment(sketch, "E14.11.6.1", {"start": v(13.75, -112.71) * mm, "end": v(8.25, -112.71) * mm});
            skLineSegment(sketch, "E14.14.6.1", {"start": v(8.25, -112.71) * mm, "end": v(5.5, -107.95) * mm});
            skLineSegment(sketch, "E14.17.6.1", {"start": v(5.5, -107.95) * mm, "end": v(8.25, -103.19) * mm});
            skLineSegment(sketch, "E14.0.6.2", {"start": v(8.25, -90.49) * mm, "end": v(13.75, -90.49) * mm});
            skLineSegment(sketch, "E14.3.6.2", {"start": v(13.75, -90.49) * mm, "end": v(16.5, -95.25) * mm});
            skLineSegment(sketch, "E14.6.6.2", {"start": v(16.5, -95.25) * mm, "end": v(13.75, -100.01) * mm});
            skCircle(sketch, "E14.9.6.2", {"center": v(11, -95.25) * mm, "radius": 4.76 * mm, "construction": true});
            skLineSegment(sketch, "E14.11.6.2", {"start": v(13.75, -100.01) * mm, "end": v(8.25, -100.01) * mm});
            skLineSegment(sketch, "E14.14.6.2", {"start": v(8.25, -100.01) * mm, "end": v(5.5, -95.25) * mm});
            skLineSegment(sketch, "E14.17.6.2", {"start": v(5.5, -95.25) * mm, "end": v(8.25, -90.49) * mm});
            skLineSegment(sketch, "E14.0.6.3", {"start": v(8.25, -77.79) * mm, "end": v(13.75, -77.79) * mm});
            skLineSegment(sketch, "E14.3.6.3", {"start": v(13.75, -77.79) * mm, "end": v(16.5, -82.55) * mm});
            skLineSegment(sketch, "E14.6.6.3", {"start": v(16.5, -82.55) * mm, "end": v(13.75, -87.31) * mm});
            skCircle(sketch, "E14.9.6.3", {"center": v(11, -82.55) * mm, "radius": 4.76 * mm, "construction": true});
            skLineSegment(sketch, "E14.11.6.3", {"start": v(13.75, -87.31) * mm, "end": v(8.25, -87.31) * mm});
            skLineSegment(sketch, "E14.14.6.3", {"start": v(8.25, -87.31) * mm, "end": v(5.5, -82.55) * mm});
            skLineSegment(sketch, "E14.17.6.3", {"start": v(5.5, -82.55) * mm, "end": v(8.25, -77.79) * mm});
            skLineSegment(sketch, "E14.0.6.4", {"start": v(8.25, -65.09) * mm, "end": v(13.75, -65.09) * mm});
            skLineSegment(sketch, "E14.3.6.4", {"start": v(13.75, -65.09) * mm, "end": v(16.5, -69.85) * mm});
            skLineSegment(sketch, "E14.6.6.4", {"start": v(16.5, -69.85) * mm, "end": v(13.75, -74.61) * mm});
            skCircle(sketch, "E14.9.6.4", {"center": v(11, -69.85) * mm, "radius": 4.76 * mm, "construction": true});
            skLineSegment(sketch, "E14.11.6.4", {"start": v(13.75, -74.61) * mm, "end": v(8.25, -74.61) * mm});
            skLineSegment(sketch, "E14.14.6.4", {"start": v(8.25, -74.61) * mm, "end": v(5.5, -69.85) * mm});
            skLineSegment(sketch, "E14.17.6.4", {"start": v(5.5, -69.85) * mm, "end": v(8.25, -65.09) * mm});
            skLineSegment(sketch, "E14.0.6.5", {"start": v(8.25, -52.39) * mm, "end": v(13.75, -52.39) * mm});
            skLineSegment(sketch, "E14.3.6.5", {"start": v(13.75, -52.39) * mm, "end": v(16.5, -57.15) * mm});
            skLineSegment(sketch, "E14.6.6.5", {"start": v(16.5, -57.15) * mm, "end": v(13.75, -61.91) * mm});
            skCircle(sketch, "E14.9.6.5", {"center": v(11, -57.15) * mm, "radius": 4.76 * mm, "construction": true});
            skLineSegment(sketch, "E14.11.6.5", {"start": v(13.75, -61.91) * mm, "end": v(8.25, -61.91) * mm});
            skLineSegment(sketch, "E14.14.6.5", {"start": v(8.25, -61.91) * mm, "end": v(5.5, -57.15) * mm});
            skLineSegment(sketch, "E14.17.6.5", {"start": v(5.5, -57.15) * mm, "end": v(8.25, -52.39) * mm});
            skLineSegment(sketch, "E14.0.6.6", {"start": v(8.25, -39.69) * mm, "end": v(13.75, -39.69) * mm});
            skLineSegment(sketch, "E14.3.6.6", {"start": v(13.75, -39.69) * mm, "end": v(16.5, -44.45) * mm});
            skLineSegment(sketch, "E14.6.6.6", {"start": v(16.5, -44.45) * mm, "end": v(13.75, -49.21) * mm});
            skCircle(sketch, "E14.9.6.6", {"center": v(11, -44.45) * mm, "radius": 4.76 * mm, "construction": true});
            skLineSegment(sketch, "E14.11.6.6", {"start": v(13.75, -49.21) * mm, "end": v(8.25, -49.21) * mm});
            skLineSegment(sketch, "E14.14.6.6", {"start": v(8.25, -49.21) * mm, "end": v(5.5, -44.45) * mm});
            skLineSegment(sketch, "E14.17.6.6", {"start": v(5.5, -44.45) * mm, "end": v(8.25, -39.69) * mm});
            skLineSegment(sketch, "E14.0.6.7", {"start": v(8.25, -26.99) * mm, "end": v(13.75, -26.99) * mm});
            skLineSegment(sketch, "E14.3.6.7", {"start": v(13.75, -26.99) * mm, "end": v(16.5, -31.75) * mm});
            skLineSegment(sketch, "E14.6.6.7", {"start": v(16.5, -31.75) * mm, "end": v(13.75, -36.51) * mm});
            skCircle(sketch, "E14.9.6.7", {"center": v(11, -31.75) * mm, "radius": 4.76 * mm, "construction": true});
            skLineSegment(sketch, "E14.11.6.7", {"start": v(13.75, -36.51) * mm, "end": v(8.25, -36.51) * mm});
            skLineSegment(sketch, "E14.14.6.7", {"start": v(8.25, -36.51) * mm, "end": v(5.5, -31.75) * mm});
            skLineSegment(sketch, "E14.17.6.7", {"start": v(5.5, -31.75) * mm, "end": v(8.25, -26.99) * mm});
            skLineSegment(sketch, "E14.0.6.8", {"start": v(8.25, -14.29) * mm, "end": v(13.75, -14.29) * mm});
            skLineSegment(sketch, "E14.3.6.8", {"start": v(13.75, -14.29) * mm, "end": v(16.5, -19.05) * mm});
            skLineSegment(sketch, "E14.6.6.8", {"start": v(16.5, -19.05) * mm, "end": v(13.75, -23.81) * mm});
            skCircle(sketch, "E14.9.6.8", {"center": v(11, -19.05) * mm, "radius": 4.76 * mm, "construction": true});
            skLineSegment(sketch, "E14.11.6.8", {"start": v(13.75, -23.81) * mm, "end": v(8.25, -23.81) * mm});
            skLineSegment(sketch, "E14.14.6.8", {"start": v(8.25, -23.81) * mm, "end": v(5.5, -19.05) * mm});
            skLineSegment(sketch, "E14.17.6.8", {"start": v(5.5, -19.05) * mm, "end": v(8.25, -14.29) * mm});
            skLineSegment(sketch, "E14.0.6.9", {"start": v(8.25, -1.59) * mm, "end": v(13.75, -1.59) * mm});
            skLineSegment(sketch, "E14.3.6.9", {"start": v(13.75, -1.59) * mm, "end": v(16.5, -6.35) * mm});
            skLineSegment(sketch, "E14.6.6.9", {"start": v(16.5, -6.35) * mm, "end": v(13.75, -11.11) * mm});
            skCircle(sketch, "E14.9.6.9", {"center": v(11, -6.35) * mm, "radius": 4.76 * mm, "construction": true});
            skLineSegment(sketch, "E14.11.6.9", {"start": v(13.75, -11.11) * mm, "end": v(8.25, -11.11) * mm});
            skLineSegment(sketch, "E14.14.6.9", {"start": v(8.25, -11.11) * mm, "end": v(5.5, -6.35) * mm});
            skLineSegment(sketch, "E14.17.6.9", {"start": v(5.5, -6.35) * mm, "end": v(8.25, -1.59) * mm});
            skLineSegment(sketch, "E14.0.6.10", {"start": v(8.25, 11.11) * mm, "end": v(13.75, 11.11) * mm});
            skLineSegment(sketch, "E14.3.6.10", {"start": v(13.75, 11.11) * mm, "end": v(16.5, 6.35) * mm});
            skLineSegment(sketch, "E14.6.6.10", {"start": v(16.5, 6.35) * mm, "end": v(13.75, 1.59) * mm});
            skCircle(sketch, "E14.9.6.10", {"center": v(11, 6.35) * mm, "radius": 4.76 * mm, "construction": true});
            skLineSegment(sketch, "E14.11.6.10", {"start": v(13.75, 1.59) * mm, "end": v(8.25, 1.59) * mm});
            skLineSegment(sketch, "E14.14.6.10", {"start": v(8.25, 1.59) * mm, "end": v(5.5, 6.35) * mm});
            skLineSegment(sketch, "E14.17.6.10", {"start": v(5.5, 6.35) * mm, "end": v(8.25, 11.11) * mm});
            skLineSegment(sketch, "E14.0.6.11", {"start": v(8.25, 23.81) * mm, "end": v(13.75, 23.81) * mm});
            skLineSegment(sketch, "E14.3.6.11", {"start": v(13.75, 23.81) * mm, "end": v(16.5, 19.05) * mm});
            skLineSegment(sketch, "E14.6.6.11", {"start": v(16.5, 19.05) * mm, "end": v(13.75, 14.29) * mm});
            skCircle(sketch, "E14.9.6.11", {"center": v(11, 19.05) * mm, "radius": 4.76 * mm, "construction": true});
            skLineSegment(sketch, "E14.11.6.11", {"start": v(13.75, 14.29) * mm, "end": v(8.25, 14.29) * mm});
            skLineSegment(sketch, "E14.14.6.11", {"start": v(8.25, 14.29) * mm, "end": v(5.5, 19.05) * mm});
            skLineSegment(sketch, "E14.17.6.11", {"start": v(5.5, 19.05) * mm, "end": v(8.25, 23.81) * mm});
            skLineSegment(sketch, "E14.0.6.12", {"start": v(8.25, 36.51) * mm, "end": v(13.75, 36.51) * mm});
            skLineSegment(sketch, "E14.3.6.12", {"start": v(13.75, 36.51) * mm, "end": v(16.5, 31.75) * mm});
            skLineSegment(sketch, "E14.6.6.12", {"start": v(16.5, 31.75) * mm, "end": v(13.75, 26.99) * mm});
            skCircle(sketch, "E14.9.6.12", {"center": v(11, 31.75) * mm, "radius": 4.76 * mm, "construction": true});
            skLineSegment(sketch, "E14.11.6.12", {"start": v(13.75, 26.99) * mm, "end": v(8.25, 26.99) * mm});
            skLineSegment(sketch, "E14.14.6.12", {"start": v(8.25, 26.99) * mm, "end": v(5.5, 31.75) * mm});
            skLineSegment(sketch, "E14.17.6.12", {"start": v(5.5, 31.75) * mm, "end": v(8.25, 36.51) * mm});
            skLineSegment(sketch, "E14.0.6.13", {"start": v(8.25, 49.21) * mm, "end": v(13.75, 49.21) * mm});
            skLineSegment(sketch, "E14.3.6.13", {"start": v(13.75, 49.21) * mm, "end": v(16.5, 44.45) * mm});
            skLineSegment(sketch, "E14.6.6.13", {"start": v(16.5, 44.45) * mm, "end": v(13.75, 39.69) * mm});
            skCircle(sketch, "E14.9.6.13", {"center": v(11, 44.45) * mm, "radius": 4.76 * mm, "construction": true});
            skLineSegment(sketch, "E14.11.6.13", {"start": v(13.75, 39.69) * mm, "end": v(8.25, 39.69) * mm});
            skLineSegment(sketch, "E14.14.6.13", {"start": v(8.25, 39.69) * mm, "end": v(5.5, 44.45) * mm});
            skLineSegment(sketch, "E14.17.6.13", {"start": v(5.5, 44.45) * mm, "end": v(8.25, 49.21) * mm});
            skLineSegment(sketch, "E14.0.6.14", {"start": v(8.25, 61.91) * mm, "end": v(13.75, 61.91) * mm});
            skLineSegment(sketch, "E14.3.6.14", {"start": v(13.75, 61.91) * mm, "end": v(16.5, 57.15) * mm});
            skLineSegment(sketch, "E14.6.6.14", {"start": v(16.5, 57.15) * mm, "end": v(13.75, 52.39) * mm});
            skCircle(sketch, "E14.9.6.14", {"center": v(11, 57.15) * mm, "radius": 4.76 * mm, "construction": true});
            skLineSegment(sketch, "E14.11.6.14", {"start": v(13.75, 52.39) * mm, "end": v(8.25, 52.39) * mm});
            skLineSegment(sketch, "E14.14.6.14", {"start": v(8.25, 52.39) * mm, "end": v(5.5, 57.15) * mm});
            skLineSegment(sketch, "E14.17.6.14", {"start": v(5.5, 57.15) * mm, "end": v(8.25, 61.91) * mm});
            skLineSegment(sketch, "E14.0.6.15", {"start": v(8.25, 74.61) * mm, "end": v(13.75, 74.61) * mm});
            skLineSegment(sketch, "E14.3.6.15", {"start": v(13.75, 74.61) * mm, "end": v(16.5, 69.85) * mm});
            skLineSegment(sketch, "E14.6.6.15", {"start": v(16.5, 69.85) * mm, "end": v(13.75, 65.09) * mm});
            skCircle(sketch, "E14.9.6.15", {"center": v(11, 69.85) * mm, "radius": 4.76 * mm, "construction": true});
            skLineSegment(sketch, "E14.11.6.15", {"start": v(13.75, 65.09) * mm, "end": v(8.25, 65.09) * mm});
            skLineSegment(sketch, "E14.14.6.15", {"start": v(8.25, 65.09) * mm, "end": v(5.5, 69.85) * mm});
            skLineSegment(sketch, "E14.17.6.15", {"start": v(5.5, 69.85) * mm, "end": v(8.25, 74.61) * mm});
            skLineSegment(sketch, "E14.0.6.16", {"start": v(8.25, 87.31) * mm, "end": v(13.75, 87.31) * mm});
            skLineSegment(sketch, "E14.3.6.16", {"start": v(13.75, 87.31) * mm, "end": v(16.5, 82.55) * mm});
            skLineSegment(sketch, "E14.6.6.16", {"start": v(16.5, 82.55) * mm, "end": v(13.75, 77.79) * mm});
            skCircle(sketch, "E14.9.6.16", {"center": v(11, 82.55) * mm, "radius": 4.76 * mm, "construction": true});
            skLineSegment(sketch, "E14.11.6.16", {"start": v(13.75, 77.79) * mm, "end": v(8.25, 77.79) * mm});
            skLineSegment(sketch, "E14.14.6.16", {"start": v(8.25, 77.79) * mm, "end": v(5.5, 82.55) * mm});
            skLineSegment(sketch, "E14.17.6.16", {"start": v(5.5, 82.55) * mm, "end": v(8.25, 87.31) * mm});
            skLineSegment(sketch, "E14.0.6.17", {"start": v(8.25, 100.01) * mm, "end": v(13.75, 100.01) * mm});
            skLineSegment(sketch, "E14.3.6.17", {"start": v(13.75, 100.01) * mm, "end": v(16.5, 95.25) * mm});
            skLineSegment(sketch, "E14.6.6.17", {"start": v(16.5, 95.25) * mm, "end": v(13.75, 90.49) * mm});
            skCircle(sketch, "E14.9.6.17", {"center": v(11, 95.25) * mm, "radius": 4.76 * mm, "construction": true});
            skLineSegment(sketch, "E14.11.6.17", {"start": v(13.75, 90.49) * mm, "end": v(8.25, 90.49) * mm});
            skLineSegment(sketch, "E14.14.6.17", {"start": v(8.25, 90.49) * mm, "end": v(5.5, 95.25) * mm});
            skLineSegment(sketch, "E14.17.6.17", {"start": v(5.5, 95.25) * mm, "end": v(8.25, 100.01) * mm});
            skLineSegment(sketch, "E14.0.6.18", {"start": v(8.25, 112.71) * mm, "end": v(13.75, 112.71) * mm});
            skLineSegment(sketch, "E14.3.6.18", {"start": v(13.75, 112.71) * mm, "end": v(16.5, 107.95) * mm});
            skLineSegment(sketch, "E14.6.6.18", {"start": v(16.5, 107.95) * mm, "end": v(13.75, 103.19) * mm});
            skCircle(sketch, "E14.9.6.18", {"center": v(11, 107.95) * mm, "radius": 4.76 * mm, "construction": true});
            skLineSegment(sketch, "E14.11.6.18", {"start": v(13.75, 103.19) * mm, "end": v(8.25, 103.19) * mm});
            skLineSegment(sketch, "E14.14.6.18", {"start": v(8.25, 103.19) * mm, "end": v(5.5, 107.95) * mm});
            skLineSegment(sketch, "E14.17.6.18", {"start": v(5.5, 107.95) * mm, "end": v(8.25, 112.71) * mm});
            skLineSegment(sketch, "E14.0.6.19", {"start": v(8.25, 125.41) * mm, "end": v(13.75, 125.41) * mm});
            skLineSegment(sketch, "E14.3.6.19", {"start": v(13.75, 125.41) * mm, "end": v(16.5, 120.65) * mm});
            skLineSegment(sketch, "E14.6.6.19", {"start": v(16.5, 120.65) * mm, "end": v(13.75, 115.89) * mm});
            skCircle(sketch, "E14.9.6.19", {"center": v(11, 120.65) * mm, "radius": 4.76 * mm, "construction": true});
            skLineSegment(sketch, "E14.11.6.19", {"start": v(13.75, 115.89) * mm, "end": v(8.25, 115.89) * mm});
            skLineSegment(sketch, "E14.14.6.19", {"start": v(8.25, 115.89) * mm, "end": v(5.5, 120.65) * mm});
            skLineSegment(sketch, "E14.17.6.19", {"start": v(5.5, 120.65) * mm, "end": v(8.25, 125.41) * mm});
            skLineSegment(sketch, "E14.0.7.0", {"start": v(30.24, -115.89) * mm, "end": v(35.74, -115.89) * mm});
            skLineSegment(sketch, "E14.3.7.0", {"start": v(35.74, -115.89) * mm, "end": v(38.5, -120.65) * mm});
            skLineSegment(sketch, "E14.6.7.0", {"start": v(38.5, -120.65) * mm, "end": v(35.74, -125.41) * mm});
            skCircle(sketch, "E14.9.7.0", {"center": v(33, -120.65) * mm, "radius": 4.76 * mm, "construction": true});
            skLineSegment(sketch, "E14.11.7.0", {"start": v(35.74, -125.41) * mm, "end": v(30.24, -125.41) * mm});
            skLineSegment(sketch, "E14.14.7.0", {"start": v(30.24, -125.41) * mm, "end": v(27.5, -120.65) * mm});
            skLineSegment(sketch, "E14.17.7.0", {"start": v(27.5, -120.65) * mm, "end": v(30.24, -115.89) * mm});
            skLineSegment(sketch, "E14.0.7.1", {"start": v(30.24, -103.19) * mm, "end": v(35.74, -103.19) * mm});
            skLineSegment(sketch, "E14.3.7.1", {"start": v(35.74, -103.19) * mm, "end": v(38.5, -107.95) * mm});
            skLineSegment(sketch, "E14.6.7.1", {"start": v(38.5, -107.95) * mm, "end": v(35.74, -112.71) * mm});
            skCircle(sketch, "E14.9.7.1", {"center": v(33, -107.95) * mm, "radius": 4.76 * mm, "construction": true});
            skLineSegment(sketch, "E14.11.7.1", {"start": v(35.74, -112.71) * mm, "end": v(30.24, -112.71) * mm});
            skLineSegment(sketch, "E14.14.7.1", {"start": v(30.24, -112.71) * mm, "end": v(27.5, -107.95) * mm});
            skLineSegment(sketch, "E14.17.7.1", {"start": v(27.5, -107.95) * mm, "end": v(30.24, -103.19) * mm});
            skLineSegment(sketch, "E14.0.7.2", {"start": v(30.24, -90.49) * mm, "end": v(35.74, -90.49) * mm});
            skLineSegment(sketch, "E14.3.7.2", {"start": v(35.74, -90.49) * mm, "end": v(38.5, -95.25) * mm});
            skLineSegment(sketch, "E14.6.7.2", {"start": v(38.5, -95.25) * mm, "end": v(35.74, -100.01) * mm});
            skCircle(sketch, "E14.9.7.2", {"center": v(33, -95.25) * mm, "radius": 4.76 * mm, "construction": true});
            skLineSegment(sketch, "E14.11.7.2", {"start": v(35.74, -100.01) * mm, "end": v(30.24, -100.01) * mm});
            skLineSegment(sketch, "E14.14.7.2", {"start": v(30.24, -100.01) * mm, "end": v(27.5, -95.25) * mm});
            skLineSegment(sketch, "E14.17.7.2", {"start": v(27.5, -95.25) * mm, "end": v(30.24, -90.49) * mm});
            skLineSegment(sketch, "E14.0.7.3", {"start": v(30.24, -77.79) * mm, "end": v(35.74, -77.79) * mm});
            skLineSegment(sketch, "E14.3.7.3", {"start": v(35.74, -77.79) * mm, "end": v(38.5, -82.55) * mm});
            skLineSegment(sketch, "E14.6.7.3", {"start": v(38.5, -82.55) * mm, "end": v(35.74, -87.31) * mm});
            skCircle(sketch, "E14.9.7.3", {"center": v(33, -82.55) * mm, "radius": 4.76 * mm, "construction": true});
            skLineSegment(sketch, "E14.11.7.3", {"start": v(35.74, -87.31) * mm, "end": v(30.24, -87.31) * mm});
            skLineSegment(sketch, "E14.14.7.3", {"start": v(30.24, -87.31) * mm, "end": v(27.5, -82.55) * mm});
            skLineSegment(sketch, "E14.17.7.3", {"start": v(27.5, -82.55) * mm, "end": v(30.24, -77.79) * mm});
            skLineSegment(sketch, "E14.0.7.4", {"start": v(30.24, -65.09) * mm, "end": v(35.74, -65.09) * mm});
            skLineSegment(sketch, "E14.3.7.4", {"start": v(35.74, -65.09) * mm, "end": v(38.5, -69.85) * mm});
            skLineSegment(sketch, "E14.6.7.4", {"start": v(38.5, -69.85) * mm, "end": v(35.74, -74.61) * mm});
            skCircle(sketch, "E14.9.7.4", {"center": v(33, -69.85) * mm, "radius": 4.76 * mm, "construction": true});
            skLineSegment(sketch, "E14.11.7.4", {"start": v(35.74, -74.61) * mm, "end": v(30.24, -74.61) * mm});
            skLineSegment(sketch, "E14.14.7.4", {"start": v(30.24, -74.61) * mm, "end": v(27.5, -69.85) * mm});
            skLineSegment(sketch, "E14.17.7.4", {"start": v(27.5, -69.85) * mm, "end": v(30.24, -65.09) * mm});
            skLineSegment(sketch, "E14.0.7.5", {"start": v(30.24, -52.39) * mm, "end": v(35.74, -52.39) * mm});
            skLineSegment(sketch, "E14.3.7.5", {"start": v(35.74, -52.39) * mm, "end": v(38.5, -57.15) * mm});
            skLineSegment(sketch, "E14.6.7.5", {"start": v(38.5, -57.15) * mm, "end": v(35.74, -61.91) * mm});
            skCircle(sketch, "E14.9.7.5", {"center": v(33, -57.15) * mm, "radius": 4.76 * mm, "construction": true});
            skLineSegment(sketch, "E14.11.7.5", {"start": v(35.74, -61.91) * mm, "end": v(30.24, -61.91) * mm});
            skLineSegment(sketch, "E14.14.7.5", {"start": v(30.24, -61.91) * mm, "end": v(27.5, -57.15) * mm});
            skLineSegment(sketch, "E14.17.7.5", {"start": v(27.5, -57.15) * mm, "end": v(30.24, -52.39) * mm});
            skLineSegment(sketch, "E14.0.7.6", {"start": v(30.24, -39.69) * mm, "end": v(35.74, -39.69) * mm});
            skLineSegment(sketch, "E14.3.7.6", {"start": v(35.74, -39.69) * mm, "end": v(38.5, -44.45) * mm});
            skLineSegment(sketch, "E14.6.7.6", {"start": v(38.5, -44.45) * mm, "end": v(35.74, -49.21) * mm});
            skCircle(sketch, "E14.9.7.6", {"center": v(33, -44.45) * mm, "radius": 4.76 * mm, "construction": true});
            skLineSegment(sketch, "E14.11.7.6", {"start": v(35.74, -49.21) * mm, "end": v(30.24, -49.21) * mm});
            skLineSegment(sketch, "E14.14.7.6", {"start": v(30.24, -49.21) * mm, "end": v(27.5, -44.45) * mm});
            skLineSegment(sketch, "E14.17.7.6", {"start": v(27.5, -44.45) * mm, "end": v(30.24, -39.69) * mm});
            skLineSegment(sketch, "E14.0.7.7", {"start": v(30.24, -26.99) * mm, "end": v(35.74, -26.99) * mm});
            skLineSegment(sketch, "E14.3.7.7", {"start": v(35.74, -26.99) * mm, "end": v(38.5, -31.75) * mm});
            skLineSegment(sketch, "E14.6.7.7", {"start": v(38.5, -31.75) * mm, "end": v(35.74, -36.51) * mm});
            skCircle(sketch, "E14.9.7.7", {"center": v(33, -31.75) * mm, "radius": 4.76 * mm, "construction": true});
            skLineSegment(sketch, "E14.11.7.7", {"start": v(35.74, -36.51) * mm, "end": v(30.24, -36.51) * mm});
            skLineSegment(sketch, "E14.14.7.7", {"start": v(30.24, -36.51) * mm, "end": v(27.5, -31.75) * mm});
            skLineSegment(sketch, "E14.17.7.7", {"start": v(27.5, -31.75) * mm, "end": v(30.24, -26.99) * mm});
            skLineSegment(sketch, "E14.0.7.8", {"start": v(30.24, -14.29) * mm, "end": v(35.74, -14.29) * mm});
            skLineSegment(sketch, "E14.3.7.8", {"start": v(35.74, -14.29) * mm, "end": v(38.5, -19.05) * mm});
            skLineSegment(sketch, "E14.6.7.8", {"start": v(38.5, -19.05) * mm, "end": v(35.74, -23.81) * mm});
            skCircle(sketch, "E14.9.7.8", {"center": v(33, -19.05) * mm, "radius": 4.76 * mm, "construction": true});
            skLineSegment(sketch, "E14.11.7.8", {"start": v(35.74, -23.81) * mm, "end": v(30.24, -23.81) * mm});
            skLineSegment(sketch, "E14.14.7.8", {"start": v(30.24, -23.81) * mm, "end": v(27.5, -19.05) * mm});
            skLineSegment(sketch, "E14.17.7.8", {"start": v(27.5, -19.05) * mm, "end": v(30.24, -14.29) * mm});
            skLineSegment(sketch, "E14.0.7.9", {"start": v(30.24, -1.59) * mm, "end": v(35.74, -1.59) * mm});
            skLineSegment(sketch, "E14.3.7.9", {"start": v(35.74, -1.59) * mm, "end": v(38.5, -6.35) * mm});
            skLineSegment(sketch, "E14.6.7.9", {"start": v(38.5, -6.35) * mm, "end": v(35.74, -11.11) * mm});
            skCircle(sketch, "E14.9.7.9", {"center": v(33, -6.35) * mm, "radius": 4.76 * mm, "construction": true});
            skLineSegment(sketch, "E14.11.7.9", {"start": v(35.74, -11.11) * mm, "end": v(30.24, -11.11) * mm});
            skLineSegment(sketch, "E14.14.7.9", {"start": v(30.24, -11.11) * mm, "end": v(27.5, -6.35) * mm});
            skLineSegment(sketch, "E14.17.7.9", {"start": v(27.5, -6.35) * mm, "end": v(30.24, -1.59) * mm});
            skLineSegment(sketch, "E14.0.7.10", {"start": v(30.24, 11.11) * mm, "end": v(35.74, 11.11) * mm});
            skLineSegment(sketch, "E14.3.7.10", {"start": v(35.74, 11.11) * mm, "end": v(38.5, 6.35) * mm});
            skLineSegment(sketch, "E14.6.7.10", {"start": v(38.5, 6.35) * mm, "end": v(35.74, 1.59) * mm});
            skCircle(sketch, "E14.9.7.10", {"center": v(33, 6.35) * mm, "radius": 4.76 * mm, "construction": true});
            skLineSegment(sketch, "E14.11.7.10", {"start": v(35.74, 1.59) * mm, "end": v(30.24, 1.59) * mm});
            skLineSegment(sketch, "E14.14.7.10", {"start": v(30.24, 1.59) * mm, "end": v(27.5, 6.35) * mm});
            skLineSegment(sketch, "E14.17.7.10", {"start": v(27.5, 6.35) * mm, "end": v(30.24, 11.11) * mm});
            skLineSegment(sketch, "E14.0.7.11", {"start": v(30.24, 23.81) * mm, "end": v(35.74, 23.81) * mm});
            skLineSegment(sketch, "E14.3.7.11", {"start": v(35.74, 23.81) * mm, "end": v(38.5, 19.05) * mm});
            skLineSegment(sketch, "E14.6.7.11", {"start": v(38.5, 19.05) * mm, "end": v(35.74, 14.29) * mm});
            skCircle(sketch, "E14.9.7.11", {"center": v(33, 19.05) * mm, "radius": 4.76 * mm, "construction": true});
            skLineSegment(sketch, "E14.11.7.11", {"start": v(35.74, 14.29) * mm, "end": v(30.24, 14.29) * mm});
            skLineSegment(sketch, "E14.14.7.11", {"start": v(30.24, 14.29) * mm, "end": v(27.5, 19.05) * mm});
            skLineSegment(sketch, "E14.17.7.11", {"start": v(27.5, 19.05) * mm, "end": v(30.24, 23.81) * mm});
            skLineSegment(sketch, "E14.0.7.12", {"start": v(30.24, 36.51) * mm, "end": v(35.74, 36.51) * mm});
            skLineSegment(sketch, "E14.3.7.12", {"start": v(35.74, 36.51) * mm, "end": v(38.5, 31.75) * mm});
            skLineSegment(sketch, "E14.6.7.12", {"start": v(38.5, 31.75) * mm, "end": v(35.74, 26.99) * mm});
            skCircle(sketch, "E14.9.7.12", {"center": v(33, 31.75) * mm, "radius": 4.76 * mm, "construction": true});
            skLineSegment(sketch, "E14.11.7.12", {"start": v(35.74, 26.99) * mm, "end": v(30.24, 26.99) * mm});
            skLineSegment(sketch, "E14.14.7.12", {"start": v(30.24, 26.99) * mm, "end": v(27.5, 31.75) * mm});
            skLineSegment(sketch, "E14.17.7.12", {"start": v(27.5, 31.75) * mm, "end": v(30.24, 36.51) * mm});
            skLineSegment(sketch, "E14.0.7.13", {"start": v(30.24, 49.21) * mm, "end": v(35.74, 49.21) * mm});
            skLineSegment(sketch, "E14.3.7.13", {"start": v(35.74, 49.21) * mm, "end": v(38.5, 44.45) * mm});
            skLineSegment(sketch, "E14.6.7.13", {"start": v(38.5, 44.45) * mm, "end": v(35.74, 39.69) * mm});
            skCircle(sketch, "E14.9.7.13", {"center": v(33, 44.45) * mm, "radius": 4.76 * mm, "construction": true});
            skLineSegment(sketch, "E14.11.7.13", {"start": v(35.74, 39.69) * mm, "end": v(30.24, 39.69) * mm});
            skLineSegment(sketch, "E14.14.7.13", {"start": v(30.24, 39.69) * mm, "end": v(27.5, 44.45) * mm});
            skLineSegment(sketch, "E14.17.7.13", {"start": v(27.5, 44.45) * mm, "end": v(30.24, 49.21) * mm});
            skLineSegment(sketch, "E14.0.7.14", {"start": v(30.24, 61.91) * mm, "end": v(35.74, 61.91) * mm});
            skLineSegment(sketch, "E14.3.7.14", {"start": v(35.74, 61.91) * mm, "end": v(38.5, 57.15) * mm});
            skLineSegment(sketch, "E14.6.7.14", {"start": v(38.5, 57.15) * mm, "end": v(35.74, 52.39) * mm});
            skCircle(sketch, "E14.9.7.14", {"center": v(33, 57.15) * mm, "radius": 4.76 * mm, "construction": true});
            skLineSegment(sketch, "E14.11.7.14", {"start": v(35.74, 52.39) * mm, "end": v(30.24, 52.39) * mm});
            skLineSegment(sketch, "E14.14.7.14", {"start": v(30.24, 52.39) * mm, "end": v(27.5, 57.15) * mm});
            skLineSegment(sketch, "E14.17.7.14", {"start": v(27.5, 57.15) * mm, "end": v(30.24, 61.91) * mm});
            skLineSegment(sketch, "E14.0.7.15", {"start": v(30.24, 74.61) * mm, "end": v(35.74, 74.61) * mm});
            skLineSegment(sketch, "E14.3.7.15", {"start": v(35.74, 74.61) * mm, "end": v(38.5, 69.85) * mm});
            skLineSegment(sketch, "E14.6.7.15", {"start": v(38.5, 69.85) * mm, "end": v(35.74, 65.09) * mm});
            skCircle(sketch, "E14.9.7.15", {"center": v(33, 69.85) * mm, "radius": 4.76 * mm, "construction": true});
            skLineSegment(sketch, "E14.11.7.15", {"start": v(35.74, 65.09) * mm, "end": v(30.24, 65.09) * mm});
            skLineSegment(sketch, "E14.14.7.15", {"start": v(30.24, 65.09) * mm, "end": v(27.5, 69.85) * mm});
            skLineSegment(sketch, "E14.17.7.15", {"start": v(27.5, 69.85) * mm, "end": v(30.24, 74.61) * mm});
            skLineSegment(sketch, "E14.0.7.16", {"start": v(30.24, 87.31) * mm, "end": v(35.74, 87.31) * mm});
            skLineSegment(sketch, "E14.3.7.16", {"start": v(35.74, 87.31) * mm, "end": v(38.5, 82.55) * mm});
            skLineSegment(sketch, "E14.6.7.16", {"start": v(38.5, 82.55) * mm, "end": v(35.74, 77.79) * mm});
            skCircle(sketch, "E14.9.7.16", {"center": v(33, 82.55) * mm, "radius": 4.76 * mm, "construction": true});
            skLineSegment(sketch, "E14.11.7.16", {"start": v(35.74, 77.79) * mm, "end": v(30.24, 77.79) * mm});
            skLineSegment(sketch, "E14.14.7.16", {"start": v(30.24, 77.79) * mm, "end": v(27.5, 82.55) * mm});
            skLineSegment(sketch, "E14.17.7.16", {"start": v(27.5, 82.55) * mm, "end": v(30.24, 87.31) * mm});
            skLineSegment(sketch, "E14.0.7.17", {"start": v(30.24, 100.01) * mm, "end": v(35.74, 100.01) * mm});
            skLineSegment(sketch, "E14.3.7.17", {"start": v(35.74, 100.01) * mm, "end": v(38.5, 95.25) * mm});
            skLineSegment(sketch, "E14.6.7.17", {"start": v(38.5, 95.25) * mm, "end": v(35.74, 90.49) * mm});
            skCircle(sketch, "E14.9.7.17", {"center": v(33, 95.25) * mm, "radius": 4.76 * mm, "construction": true});
            skLineSegment(sketch, "E14.11.7.17", {"start": v(35.74, 90.49) * mm, "end": v(30.24, 90.49) * mm});
            skLineSegment(sketch, "E14.14.7.17", {"start": v(30.24, 90.49) * mm, "end": v(27.5, 95.25) * mm});
            skLineSegment(sketch, "E14.17.7.17", {"start": v(27.5, 95.25) * mm, "end": v(30.24, 100.01) * mm});
            skLineSegment(sketch, "E14.0.7.18", {"start": v(30.24, 112.71) * mm, "end": v(35.74, 112.71) * mm});
            skLineSegment(sketch, "E14.3.7.18", {"start": v(35.74, 112.71) * mm, "end": v(38.5, 107.95) * mm});
            skLineSegment(sketch, "E14.6.7.18", {"start": v(38.5, 107.95) * mm, "end": v(35.74, 103.19) * mm});
            skCircle(sketch, "E14.9.7.18", {"center": v(33, 107.95) * mm, "radius": 4.76 * mm, "construction": true});
            skLineSegment(sketch, "E14.11.7.18", {"start": v(35.74, 103.19) * mm, "end": v(30.24, 103.19) * mm});
            skLineSegment(sketch, "E14.14.7.18", {"start": v(30.24, 103.19) * mm, "end": v(27.5, 107.95) * mm});
            skLineSegment(sketch, "E14.17.7.18", {"start": v(27.5, 107.95) * mm, "end": v(30.24, 112.71) * mm});
            skLineSegment(sketch, "E14.0.7.19", {"start": v(30.24, 125.41) * mm, "end": v(35.74, 125.41) * mm});
            skLineSegment(sketch, "E14.3.7.19", {"start": v(35.74, 125.41) * mm, "end": v(38.5, 120.65) * mm});
            skLineSegment(sketch, "E14.6.7.19", {"start": v(38.5, 120.65) * mm, "end": v(35.74, 115.89) * mm});
            skCircle(sketch, "E14.9.7.19", {"center": v(33, 120.65) * mm, "radius": 4.76 * mm, "construction": true});
            skLineSegment(sketch, "E14.11.7.19", {"start": v(35.74, 115.89) * mm, "end": v(30.24, 115.89) * mm});
            skLineSegment(sketch, "E14.14.7.19", {"start": v(30.24, 115.89) * mm, "end": v(27.5, 120.65) * mm});
            skLineSegment(sketch, "E14.17.7.19", {"start": v(27.5, 120.65) * mm, "end": v(30.24, 125.41) * mm});
            skLineSegment(sketch, "E14.0.8.0", {"start": v(52.24, -115.89) * mm, "end": v(57.74, -115.89) * mm});
            skLineSegment(sketch, "E14.3.8.0", {"start": v(57.74, -115.89) * mm, "end": v(60.49, -120.65) * mm});
            skLineSegment(sketch, "E14.6.8.0", {"start": v(60.49, -120.65) * mm, "end": v(57.74, -125.41) * mm});
            skCircle(sketch, "E14.9.8.0", {"center": v(55, -120.65) * mm, "radius": 4.76 * mm, "construction": true});
            skLineSegment(sketch, "E14.11.8.0", {"start": v(57.74, -125.41) * mm, "end": v(52.24, -125.41) * mm});
            skLineSegment(sketch, "E14.14.8.0", {"start": v(52.24, -125.41) * mm, "end": v(49.5, -120.65) * mm});
            skLineSegment(sketch, "E14.17.8.0", {"start": v(49.5, -120.65) * mm, "end": v(52.24, -115.89) * mm});
            skLineSegment(sketch, "E14.0.8.1", {"start": v(52.24, -103.19) * mm, "end": v(57.74, -103.19) * mm});
            skLineSegment(sketch, "E14.3.8.1", {"start": v(57.74, -103.19) * mm, "end": v(60.49, -107.95) * mm});
            skLineSegment(sketch, "E14.6.8.1", {"start": v(60.49, -107.95) * mm, "end": v(57.74, -112.71) * mm});
            skCircle(sketch, "E14.9.8.1", {"center": v(55, -107.95) * mm, "radius": 4.76 * mm, "construction": true});
            skLineSegment(sketch, "E14.11.8.1", {"start": v(57.74, -112.71) * mm, "end": v(52.24, -112.71) * mm});
            skLineSegment(sketch, "E14.14.8.1", {"start": v(52.24, -112.71) * mm, "end": v(49.5, -107.95) * mm});
            skLineSegment(sketch, "E14.17.8.1", {"start": v(49.5, -107.95) * mm, "end": v(52.24, -103.19) * mm});
            skLineSegment(sketch, "E14.0.8.2", {"start": v(52.24, -90.49) * mm, "end": v(57.74, -90.49) * mm});
            skLineSegment(sketch, "E14.3.8.2", {"start": v(57.74, -90.49) * mm, "end": v(60.49, -95.25) * mm});
            skLineSegment(sketch, "E14.6.8.2", {"start": v(60.49, -95.25) * mm, "end": v(57.74, -100.01) * mm});
            skCircle(sketch, "E14.9.8.2", {"center": v(55, -95.25) * mm, "radius": 4.76 * mm, "construction": true});
            skLineSegment(sketch, "E14.11.8.2", {"start": v(57.74, -100.01) * mm, "end": v(52.24, -100.01) * mm});
            skLineSegment(sketch, "E14.14.8.2", {"start": v(52.24, -100.01) * mm, "end": v(49.5, -95.25) * mm});
            skLineSegment(sketch, "E14.17.8.2", {"start": v(49.5, -95.25) * mm, "end": v(52.24, -90.49) * mm});
            skLineSegment(sketch, "E14.0.8.3", {"start": v(52.24, -77.79) * mm, "end": v(57.74, -77.79) * mm});
            skLineSegment(sketch, "E14.3.8.3", {"start": v(57.74, -77.79) * mm, "end": v(60.49, -82.55) * mm});
            skLineSegment(sketch, "E14.6.8.3", {"start": v(60.49, -82.55) * mm, "end": v(57.74, -87.31) * mm});
            skCircle(sketch, "E14.9.8.3", {"center": v(55, -82.55) * mm, "radius": 4.76 * mm, "construction": true});
            skLineSegment(sketch, "E14.11.8.3", {"start": v(57.74, -87.31) * mm, "end": v(52.24, -87.31) * mm});
            skLineSegment(sketch, "E14.14.8.3", {"start": v(52.24, -87.31) * mm, "end": v(49.5, -82.55) * mm});
            skLineSegment(sketch, "E14.17.8.3", {"start": v(49.5, -82.55) * mm, "end": v(52.24, -77.79) * mm});
            skLineSegment(sketch, "E14.0.8.4", {"start": v(52.24, -65.09) * mm, "end": v(57.74, -65.09) * mm});
            skLineSegment(sketch, "E14.3.8.4", {"start": v(57.74, -65.09) * mm, "end": v(60.49, -69.85) * mm});
            skLineSegment(sketch, "E14.6.8.4", {"start": v(60.49, -69.85) * mm, "end": v(57.74, -74.61) * mm});
            skCircle(sketch, "E14.9.8.4", {"center": v(55, -69.85) * mm, "radius": 4.76 * mm, "construction": true});
            skLineSegment(sketch, "E14.11.8.4", {"start": v(57.74, -74.61) * mm, "end": v(52.24, -74.61) * mm});
            skLineSegment(sketch, "E14.14.8.4", {"start": v(52.24, -74.61) * mm, "end": v(49.5, -69.85) * mm});
            skLineSegment(sketch, "E14.17.8.4", {"start": v(49.5, -69.85) * mm, "end": v(52.24, -65.09) * mm});
            skLineSegment(sketch, "E14.0.8.5", {"start": v(52.24, -52.39) * mm, "end": v(57.74, -52.39) * mm});
            skLineSegment(sketch, "E14.3.8.5", {"start": v(57.74, -52.39) * mm, "end": v(60.49, -57.15) * mm});
            skLineSegment(sketch, "E14.6.8.5", {"start": v(60.49, -57.15) * mm, "end": v(57.74, -61.91) * mm});
            skCircle(sketch, "E14.9.8.5", {"center": v(55, -57.15) * mm, "radius": 4.76 * mm, "construction": true});
            skLineSegment(sketch, "E14.11.8.5", {"start": v(57.74, -61.91) * mm, "end": v(52.24, -61.91) * mm});
            skLineSegment(sketch, "E14.14.8.5", {"start": v(52.24, -61.91) * mm, "end": v(49.5, -57.15) * mm});
            skLineSegment(sketch, "E14.17.8.5", {"start": v(49.5, -57.15) * mm, "end": v(52.24, -52.39) * mm});
            skLineSegment(sketch, "E14.0.8.6", {"start": v(52.24, -39.69) * mm, "end": v(57.74, -39.69) * mm});
            skLineSegment(sketch, "E14.3.8.6", {"start": v(57.74, -39.69) * mm, "end": v(60.49, -44.45) * mm});
            skLineSegment(sketch, "E14.6.8.6", {"start": v(60.49, -44.45) * mm, "end": v(57.74, -49.21) * mm});
            skCircle(sketch, "E14.9.8.6", {"center": v(55, -44.45) * mm, "radius": 4.76 * mm, "construction": true});
            skLineSegment(sketch, "E14.11.8.6", {"start": v(57.74, -49.21) * mm, "end": v(52.24, -49.21) * mm});
            skLineSegment(sketch, "E14.14.8.6", {"start": v(52.24, -49.21) * mm, "end": v(49.5, -44.45) * mm});
            skLineSegment(sketch, "E14.17.8.6", {"start": v(49.5, -44.45) * mm, "end": v(52.24, -39.69) * mm});
            skLineSegment(sketch, "E14.0.8.7", {"start": v(52.24, -26.99) * mm, "end": v(57.74, -26.99) * mm});
            skLineSegment(sketch, "E14.3.8.7", {"start": v(57.74, -26.99) * mm, "end": v(60.49, -31.75) * mm});
            skLineSegment(sketch, "E14.6.8.7", {"start": v(60.49, -31.75) * mm, "end": v(57.74, -36.51) * mm});
            skCircle(sketch, "E14.9.8.7", {"center": v(55, -31.75) * mm, "radius": 4.76 * mm, "construction": true});
            skLineSegment(sketch, "E14.11.8.7", {"start": v(57.74, -36.51) * mm, "end": v(52.24, -36.51) * mm});
            skLineSegment(sketch, "E14.14.8.7", {"start": v(52.24, -36.51) * mm, "end": v(49.5, -31.75) * mm});
            skLineSegment(sketch, "E14.17.8.7", {"start": v(49.5, -31.75) * mm, "end": v(52.24, -26.99) * mm});
            skLineSegment(sketch, "E14.0.8.8", {"start": v(52.24, -14.29) * mm, "end": v(57.74, -14.29) * mm});
            skLineSegment(sketch, "E14.3.8.8", {"start": v(57.74, -14.29) * mm, "end": v(60.49, -19.05) * mm});
            skLineSegment(sketch, "E14.6.8.8", {"start": v(60.49, -19.05) * mm, "end": v(57.74, -23.81) * mm});
            skCircle(sketch, "E14.9.8.8", {"center": v(55, -19.05) * mm, "radius": 4.76 * mm, "construction": true});
            skLineSegment(sketch, "E14.11.8.8", {"start": v(57.74, -23.81) * mm, "end": v(52.24, -23.81) * mm});
            skLineSegment(sketch, "E14.14.8.8", {"start": v(52.24, -23.81) * mm, "end": v(49.5, -19.05) * mm});
            skLineSegment(sketch, "E14.17.8.8", {"start": v(49.5, -19.05) * mm, "end": v(52.24, -14.29) * mm});
            skLineSegment(sketch, "E14.0.8.9", {"start": v(52.24, -1.59) * mm, "end": v(57.74, -1.59) * mm});
            skLineSegment(sketch, "E14.3.8.9", {"start": v(57.74, -1.59) * mm, "end": v(60.49, -6.35) * mm});
            skLineSegment(sketch, "E14.6.8.9", {"start": v(60.49, -6.35) * mm, "end": v(57.74, -11.11) * mm});
            skCircle(sketch, "E14.9.8.9", {"center": v(55, -6.35) * mm, "radius": 4.76 * mm, "construction": true});
            skLineSegment(sketch, "E14.11.8.9", {"start": v(57.74, -11.11) * mm, "end": v(52.24, -11.11) * mm});
            skLineSegment(sketch, "E14.14.8.9", {"start": v(52.24, -11.11) * mm, "end": v(49.5, -6.35) * mm});
            skLineSegment(sketch, "E14.17.8.9", {"start": v(49.5, -6.35) * mm, "end": v(52.24, -1.59) * mm});
            skLineSegment(sketch, "E14.0.8.10", {"start": v(52.24, 11.11) * mm, "end": v(57.74, 11.11) * mm});
            skLineSegment(sketch, "E14.3.8.10", {"start": v(57.74, 11.11) * mm, "end": v(60.49, 6.35) * mm});
            skLineSegment(sketch, "E14.6.8.10", {"start": v(60.49, 6.35) * mm, "end": v(57.74, 1.59) * mm});
            skCircle(sketch, "E14.9.8.10", {"center": v(55, 6.35) * mm, "radius": 4.76 * mm, "construction": true});
            skLineSegment(sketch, "E14.11.8.10", {"start": v(57.74, 1.59) * mm, "end": v(52.24, 1.59) * mm});
            skLineSegment(sketch, "E14.14.8.10", {"start": v(52.24, 1.59) * mm, "end": v(49.5, 6.35) * mm});
            skLineSegment(sketch, "E14.17.8.10", {"start": v(49.5, 6.35) * mm, "end": v(52.24, 11.11) * mm});
            skLineSegment(sketch, "E14.0.8.11", {"start": v(52.24, 23.81) * mm, "end": v(57.74, 23.81) * mm});
            skLineSegment(sketch, "E14.3.8.11", {"start": v(57.74, 23.81) * mm, "end": v(60.49, 19.05) * mm});
            skLineSegment(sketch, "E14.6.8.11", {"start": v(60.49, 19.05) * mm, "end": v(57.74, 14.29) * mm});
            skCircle(sketch, "E14.9.8.11", {"center": v(55, 19.05) * mm, "radius": 4.76 * mm, "construction": true});
            skLineSegment(sketch, "E14.11.8.11", {"start": v(57.74, 14.29) * mm, "end": v(52.24, 14.29) * mm});
            skLineSegment(sketch, "E14.14.8.11", {"start": v(52.24, 14.29) * mm, "end": v(49.5, 19.05) * mm});
            skLineSegment(sketch, "E14.17.8.11", {"start": v(49.5, 19.05) * mm, "end": v(52.24, 23.81) * mm});
            skLineSegment(sketch, "E14.0.8.12", {"start": v(52.24, 36.51) * mm, "end": v(57.74, 36.51) * mm});
            skLineSegment(sketch, "E14.3.8.12", {"start": v(57.74, 36.51) * mm, "end": v(60.49, 31.75) * mm});
            skLineSegment(sketch, "E14.6.8.12", {"start": v(60.49, 31.75) * mm, "end": v(57.74, 26.99) * mm});
            skCircle(sketch, "E14.9.8.12", {"center": v(55, 31.75) * mm, "radius": 4.76 * mm, "construction": true});
            skLineSegment(sketch, "E14.11.8.12", {"start": v(57.74, 26.99) * mm, "end": v(52.24, 26.99) * mm});
            skLineSegment(sketch, "E14.14.8.12", {"start": v(52.24, 26.99) * mm, "end": v(49.5, 31.75) * mm});
            skLineSegment(sketch, "E14.17.8.12", {"start": v(49.5, 31.75) * mm, "end": v(52.24, 36.51) * mm});
            skLineSegment(sketch, "E14.0.8.13", {"start": v(52.24, 49.21) * mm, "end": v(57.74, 49.21) * mm});
            skLineSegment(sketch, "E14.3.8.13", {"start": v(57.74, 49.21) * mm, "end": v(60.49, 44.45) * mm});
            skLineSegment(sketch, "E14.6.8.13", {"start": v(60.49, 44.45) * mm, "end": v(57.74, 39.69) * mm});
            skCircle(sketch, "E14.9.8.13", {"center": v(55, 44.45) * mm, "radius": 4.76 * mm, "construction": true});
            skLineSegment(sketch, "E14.11.8.13", {"start": v(57.74, 39.69) * mm, "end": v(52.24, 39.69) * mm});
            skLineSegment(sketch, "E14.14.8.13", {"start": v(52.24, 39.69) * mm, "end": v(49.5, 44.45) * mm});
            skLineSegment(sketch, "E14.17.8.13", {"start": v(49.5, 44.45) * mm, "end": v(52.24, 49.21) * mm});
            skLineSegment(sketch, "E14.0.8.14", {"start": v(52.24, 61.91) * mm, "end": v(57.74, 61.91) * mm});
            skLineSegment(sketch, "E14.3.8.14", {"start": v(57.74, 61.91) * mm, "end": v(60.49, 57.15) * mm});
            skLineSegment(sketch, "E14.6.8.14", {"start": v(60.49, 57.15) * mm, "end": v(57.74, 52.39) * mm});
            skCircle(sketch, "E14.9.8.14", {"center": v(55, 57.15) * mm, "radius": 4.76 * mm, "construction": true});
            skLineSegment(sketch, "E14.11.8.14", {"start": v(57.74, 52.39) * mm, "end": v(52.24, 52.39) * mm});
            skLineSegment(sketch, "E14.14.8.14", {"start": v(52.24, 52.39) * mm, "end": v(49.5, 57.15) * mm});
            skLineSegment(sketch, "E14.17.8.14", {"start": v(49.5, 57.15) * mm, "end": v(52.24, 61.91) * mm});
            skLineSegment(sketch, "E14.0.8.15", {"start": v(52.24, 74.61) * mm, "end": v(57.74, 74.61) * mm});
            skLineSegment(sketch, "E14.3.8.15", {"start": v(57.74, 74.61) * mm, "end": v(60.49, 69.85) * mm});
            skLineSegment(sketch, "E14.6.8.15", {"start": v(60.49, 69.85) * mm, "end": v(57.74, 65.09) * mm});
            skCircle(sketch, "E14.9.8.15", {"center": v(55, 69.85) * mm, "radius": 4.76 * mm, "construction": true});
            skLineSegment(sketch, "E14.11.8.15", {"start": v(57.74, 65.09) * mm, "end": v(52.24, 65.09) * mm});
            skLineSegment(sketch, "E14.14.8.15", {"start": v(52.24, 65.09) * mm, "end": v(49.5, 69.85) * mm});
            skLineSegment(sketch, "E14.17.8.15", {"start": v(49.5, 69.85) * mm, "end": v(52.24, 74.61) * mm});
            skLineSegment(sketch, "E14.0.8.16", {"start": v(52.24, 87.31) * mm, "end": v(57.74, 87.31) * mm});
            skLineSegment(sketch, "E14.3.8.16", {"start": v(57.74, 87.31) * mm, "end": v(60.49, 82.55) * mm});
            skLineSegment(sketch, "E14.6.8.16", {"start": v(60.49, 82.55) * mm, "end": v(57.74, 77.79) * mm});
            skCircle(sketch, "E14.9.8.16", {"center": v(55, 82.55) * mm, "radius": 4.76 * mm, "construction": true});
            skLineSegment(sketch, "E14.11.8.16", {"start": v(57.74, 77.79) * mm, "end": v(52.24, 77.79) * mm});
            skLineSegment(sketch, "E14.14.8.16", {"start": v(52.24, 77.79) * mm, "end": v(49.5, 82.55) * mm});
            skLineSegment(sketch, "E14.17.8.16", {"start": v(49.5, 82.55) * mm, "end": v(52.24, 87.31) * mm});
            skLineSegment(sketch, "E14.0.8.17", {"start": v(52.24, 100.01) * mm, "end": v(57.74, 100.01) * mm});
            skLineSegment(sketch, "E14.3.8.17", {"start": v(57.74, 100.01) * mm, "end": v(60.49, 95.25) * mm});
            skLineSegment(sketch, "E14.6.8.17", {"start": v(60.49, 95.25) * mm, "end": v(57.74, 90.49) * mm});
            skCircle(sketch, "E14.9.8.17", {"center": v(55, 95.25) * mm, "radius": 4.76 * mm, "construction": true});
            skLineSegment(sketch, "E14.11.8.17", {"start": v(57.74, 90.49) * mm, "end": v(52.24, 90.49) * mm});
            skLineSegment(sketch, "E14.14.8.17", {"start": v(52.24, 90.49) * mm, "end": v(49.5, 95.25) * mm});
            skLineSegment(sketch, "E14.17.8.17", {"start": v(49.5, 95.25) * mm, "end": v(52.24, 100.01) * mm});
            skLineSegment(sketch, "E14.0.8.18", {"start": v(52.24, 112.71) * mm, "end": v(57.74, 112.71) * mm});
            skLineSegment(sketch, "E14.3.8.18", {"start": v(57.74, 112.71) * mm, "end": v(60.49, 107.95) * mm});
            skLineSegment(sketch, "E14.6.8.18", {"start": v(60.49, 107.95) * mm, "end": v(57.74, 103.19) * mm});
            skCircle(sketch, "E14.9.8.18", {"center": v(55, 107.95) * mm, "radius": 4.76 * mm, "construction": true});
            skLineSegment(sketch, "E14.11.8.18", {"start": v(57.74, 103.19) * mm, "end": v(52.24, 103.19) * mm});
            skLineSegment(sketch, "E14.14.8.18", {"start": v(52.24, 103.19) * mm, "end": v(49.5, 107.95) * mm});
            skLineSegment(sketch, "E14.17.8.18", {"start": v(49.5, 107.95) * mm, "end": v(52.24, 112.71) * mm});
            skLineSegment(sketch, "E14.0.8.19", {"start": v(52.24, 125.41) * mm, "end": v(57.74, 125.41) * mm});
            skLineSegment(sketch, "E14.3.8.19", {"start": v(57.74, 125.41) * mm, "end": v(60.49, 120.65) * mm});
            skLineSegment(sketch, "E14.6.8.19", {"start": v(60.49, 120.65) * mm, "end": v(57.74, 115.89) * mm});
            skCircle(sketch, "E14.9.8.19", {"center": v(55, 120.65) * mm, "radius": 4.76 * mm, "construction": true});
            skLineSegment(sketch, "E14.11.8.19", {"start": v(57.74, 115.89) * mm, "end": v(52.24, 115.89) * mm});
            skLineSegment(sketch, "E14.14.8.19", {"start": v(52.24, 115.89) * mm, "end": v(49.5, 120.65) * mm});
            skLineSegment(sketch, "E14.17.8.19", {"start": v(49.5, 120.65) * mm, "end": v(52.24, 125.41) * mm});
            skLineSegment(sketch, "E14.0.9.0", {"start": v(74.24, -115.89) * mm, "end": v(79.74, -115.89) * mm});
            skLineSegment(sketch, "E14.3.9.0", {"start": v(79.74, -115.89) * mm, "end": v(82.49, -120.65) * mm});
            skLineSegment(sketch, "E14.6.9.0", {"start": v(82.49, -120.65) * mm, "end": v(79.74, -125.41) * mm});
            skCircle(sketch, "E14.9.9.0", {"center": v(76.99, -120.65) * mm, "radius": 4.76 * mm, "construction": true});
            skLineSegment(sketch, "E14.11.9.0", {"start": v(79.74, -125.41) * mm, "end": v(74.24, -125.41) * mm});
            skLineSegment(sketch, "E14.14.9.0", {"start": v(74.24, -125.41) * mm, "end": v(71.49, -120.65) * mm});
            skLineSegment(sketch, "E14.17.9.0", {"start": v(71.49, -120.65) * mm, "end": v(74.24, -115.89) * mm});
            skLineSegment(sketch, "E14.0.9.1", {"start": v(74.24, -103.19) * mm, "end": v(79.74, -103.19) * mm});
            skLineSegment(sketch, "E14.3.9.1", {"start": v(79.74, -103.19) * mm, "end": v(82.49, -107.95) * mm});
            skLineSegment(sketch, "E14.6.9.1", {"start": v(82.49, -107.95) * mm, "end": v(79.74, -112.71) * mm});
            skCircle(sketch, "E14.9.9.1", {"center": v(76.99, -107.95) * mm, "radius": 4.76 * mm, "construction": true});
            skLineSegment(sketch, "E14.11.9.1", {"start": v(79.74, -112.71) * mm, "end": v(74.24, -112.71) * mm});
            skLineSegment(sketch, "E14.14.9.1", {"start": v(74.24, -112.71) * mm, "end": v(71.49, -107.95) * mm});
            skLineSegment(sketch, "E14.17.9.1", {"start": v(71.49, -107.95) * mm, "end": v(74.24, -103.19) * mm});
            skLineSegment(sketch, "E14.0.9.2", {"start": v(74.24, -90.49) * mm, "end": v(79.74, -90.49) * mm});
            skLineSegment(sketch, "E14.3.9.2", {"start": v(79.74, -90.49) * mm, "end": v(82.49, -95.25) * mm});
            skLineSegment(sketch, "E14.6.9.2", {"start": v(82.49, -95.25) * mm, "end": v(79.74, -100.01) * mm});
            skCircle(sketch, "E14.9.9.2", {"center": v(76.99, -95.25) * mm, "radius": 4.76 * mm, "construction": true});
            skLineSegment(sketch, "E14.11.9.2", {"start": v(79.74, -100.01) * mm, "end": v(74.24, -100.01) * mm});
            skLineSegment(sketch, "E14.14.9.2", {"start": v(74.24, -100.01) * mm, "end": v(71.49, -95.25) * mm});
            skLineSegment(sketch, "E14.17.9.2", {"start": v(71.49, -95.25) * mm, "end": v(74.24, -90.49) * mm});
            skLineSegment(sketch, "E14.0.9.3", {"start": v(74.24, -77.79) * mm, "end": v(79.74, -77.79) * mm});
            skLineSegment(sketch, "E14.3.9.3", {"start": v(79.74, -77.79) * mm, "end": v(82.49, -82.55) * mm});
            skLineSegment(sketch, "E14.6.9.3", {"start": v(82.49, -82.55) * mm, "end": v(79.74, -87.31) * mm});
            skCircle(sketch, "E14.9.9.3", {"center": v(76.99, -82.55) * mm, "radius": 4.76 * mm, "construction": true});
            skLineSegment(sketch, "E14.11.9.3", {"start": v(79.74, -87.31) * mm, "end": v(74.24, -87.31) * mm});
            skLineSegment(sketch, "E14.14.9.3", {"start": v(74.24, -87.31) * mm, "end": v(71.49, -82.55) * mm});
            skLineSegment(sketch, "E14.17.9.3", {"start": v(71.49, -82.55) * mm, "end": v(74.24, -77.79) * mm});
            skLineSegment(sketch, "E14.0.9.4", {"start": v(74.24, -65.09) * mm, "end": v(79.74, -65.09) * mm});
            skLineSegment(sketch, "E14.3.9.4", {"start": v(79.74, -65.09) * mm, "end": v(82.49, -69.85) * mm});
            skLineSegment(sketch, "E14.6.9.4", {"start": v(82.49, -69.85) * mm, "end": v(79.74, -74.61) * mm});
            skCircle(sketch, "E14.9.9.4", {"center": v(76.99, -69.85) * mm, "radius": 4.76 * mm, "construction": true});
            skLineSegment(sketch, "E14.11.9.4", {"start": v(79.74, -74.61) * mm, "end": v(74.24, -74.61) * mm});
            skLineSegment(sketch, "E14.14.9.4", {"start": v(74.24, -74.61) * mm, "end": v(71.49, -69.85) * mm});
            skLineSegment(sketch, "E14.17.9.4", {"start": v(71.49, -69.85) * mm, "end": v(74.24, -65.09) * mm});
            skLineSegment(sketch, "E14.0.9.5", {"start": v(74.24, -52.39) * mm, "end": v(79.74, -52.39) * mm});
            skLineSegment(sketch, "E14.3.9.5", {"start": v(79.74, -52.39) * mm, "end": v(82.49, -57.15) * mm});
            skLineSegment(sketch, "E14.6.9.5", {"start": v(82.49, -57.15) * mm, "end": v(79.74, -61.91) * mm});
            skCircle(sketch, "E14.9.9.5", {"center": v(76.99, -57.15) * mm, "radius": 4.76 * mm, "construction": true});
            skLineSegment(sketch, "E14.11.9.5", {"start": v(79.74, -61.91) * mm, "end": v(74.24, -61.91) * mm});
            skLineSegment(sketch, "E14.14.9.5", {"start": v(74.24, -61.91) * mm, "end": v(71.49, -57.15) * mm});
            skLineSegment(sketch, "E14.17.9.5", {"start": v(71.49, -57.15) * mm, "end": v(74.24, -52.39) * mm});
            skLineSegment(sketch, "E14.0.9.6", {"start": v(74.24, -39.69) * mm, "end": v(79.74, -39.69) * mm});
            skLineSegment(sketch, "E14.3.9.6", {"start": v(79.74, -39.69) * mm, "end": v(82.49, -44.45) * mm});
            skLineSegment(sketch, "E14.6.9.6", {"start": v(82.49, -44.45) * mm, "end": v(79.74, -49.21) * mm});
            skCircle(sketch, "E14.9.9.6", {"center": v(76.99, -44.45) * mm, "radius": 4.76 * mm, "construction": true});
            skLineSegment(sketch, "E14.11.9.6", {"start": v(79.74, -49.21) * mm, "end": v(74.24, -49.21) * mm});
            skLineSegment(sketch, "E14.14.9.6", {"start": v(74.24, -49.21) * mm, "end": v(71.49, -44.45) * mm});
            skLineSegment(sketch, "E14.17.9.6", {"start": v(71.49, -44.45) * mm, "end": v(74.24, -39.69) * mm});
            skLineSegment(sketch, "E14.0.9.7", {"start": v(74.24, -26.99) * mm, "end": v(79.74, -26.99) * mm});
            skLineSegment(sketch, "E14.3.9.7", {"start": v(79.74, -26.99) * mm, "end": v(82.49, -31.75) * mm});
            skLineSegment(sketch, "E14.6.9.7", {"start": v(82.49, -31.75) * mm, "end": v(79.74, -36.51) * mm});
            skCircle(sketch, "E14.9.9.7", {"center": v(76.99, -31.75) * mm, "radius": 4.76 * mm, "construction": true});
            skLineSegment(sketch, "E14.11.9.7", {"start": v(79.74, -36.51) * mm, "end": v(74.24, -36.51) * mm});
            skLineSegment(sketch, "E14.14.9.7", {"start": v(74.24, -36.51) * mm, "end": v(71.49, -31.75) * mm});
            skLineSegment(sketch, "E14.17.9.7", {"start": v(71.49, -31.75) * mm, "end": v(74.24, -26.99) * mm});
            skLineSegment(sketch, "E14.0.9.8", {"start": v(74.24, -14.29) * mm, "end": v(79.74, -14.29) * mm});
            skLineSegment(sketch, "E14.3.9.8", {"start": v(79.74, -14.29) * mm, "end": v(82.49, -19.05) * mm});
            skLineSegment(sketch, "E14.6.9.8", {"start": v(82.49, -19.05) * mm, "end": v(79.74, -23.81) * mm});
            skCircle(sketch, "E14.9.9.8", {"center": v(76.99, -19.05) * mm, "radius": 4.76 * mm, "construction": true});
            skLineSegment(sketch, "E14.11.9.8", {"start": v(79.74, -23.81) * mm, "end": v(74.24, -23.81) * mm});
            skLineSegment(sketch, "E14.14.9.8", {"start": v(74.24, -23.81) * mm, "end": v(71.49, -19.05) * mm});
            skLineSegment(sketch, "E14.17.9.8", {"start": v(71.49, -19.05) * mm, "end": v(74.24, -14.29) * mm});
            skLineSegment(sketch, "E14.0.9.9", {"start": v(74.24, -1.59) * mm, "end": v(79.74, -1.59) * mm});
            skLineSegment(sketch, "E14.3.9.9", {"start": v(79.74, -1.59) * mm, "end": v(82.49, -6.35) * mm});
            skLineSegment(sketch, "E14.6.9.9", {"start": v(82.49, -6.35) * mm, "end": v(79.74, -11.11) * mm});
            skCircle(sketch, "E14.9.9.9", {"center": v(76.99, -6.35) * mm, "radius": 4.76 * mm, "construction": true});
            skLineSegment(sketch, "E14.11.9.9", {"start": v(79.74, -11.11) * mm, "end": v(74.24, -11.11) * mm});
            skLineSegment(sketch, "E14.14.9.9", {"start": v(74.24, -11.11) * mm, "end": v(71.49, -6.35) * mm});
            skLineSegment(sketch, "E14.17.9.9", {"start": v(71.49, -6.35) * mm, "end": v(74.24, -1.59) * mm});
            skLineSegment(sketch, "E14.0.9.10", {"start": v(74.24, 11.11) * mm, "end": v(79.74, 11.11) * mm});
            skLineSegment(sketch, "E14.3.9.10", {"start": v(79.74, 11.11) * mm, "end": v(82.49, 6.35) * mm});
            skLineSegment(sketch, "E14.6.9.10", {"start": v(82.49, 6.35) * mm, "end": v(79.74, 1.59) * mm});
            skCircle(sketch, "E14.9.9.10", {"center": v(76.99, 6.35) * mm, "radius": 4.76 * mm, "construction": true});
            skLineSegment(sketch, "E14.11.9.10", {"start": v(79.74, 1.59) * mm, "end": v(74.24, 1.59) * mm});
            skLineSegment(sketch, "E14.14.9.10", {"start": v(74.24, 1.59) * mm, "end": v(71.49, 6.35) * mm});
            skLineSegment(sketch, "E14.17.9.10", {"start": v(71.49, 6.35) * mm, "end": v(74.24, 11.11) * mm});
            skLineSegment(sketch, "E14.0.9.11", {"start": v(74.24, 23.81) * mm, "end": v(79.74, 23.81) * mm});
            skLineSegment(sketch, "E14.3.9.11", {"start": v(79.74, 23.81) * mm, "end": v(82.49, 19.05) * mm});
            skLineSegment(sketch, "E14.6.9.11", {"start": v(82.49, 19.05) * mm, "end": v(79.74, 14.29) * mm});
            skCircle(sketch, "E14.9.9.11", {"center": v(76.99, 19.05) * mm, "radius": 4.76 * mm, "construction": true});
            skLineSegment(sketch, "E14.11.9.11", {"start": v(79.74, 14.29) * mm, "end": v(74.24, 14.29) * mm});
            skLineSegment(sketch, "E14.14.9.11", {"start": v(74.24, 14.29) * mm, "end": v(71.49, 19.05) * mm});
            skLineSegment(sketch, "E14.17.9.11", {"start": v(71.49, 19.05) * mm, "end": v(74.24, 23.81) * mm});
            skLineSegment(sketch, "E14.0.9.12", {"start": v(74.24, 36.51) * mm, "end": v(79.74, 36.51) * mm});
            skLineSegment(sketch, "E14.3.9.12", {"start": v(79.74, 36.51) * mm, "end": v(82.49, 31.75) * mm});
            skLineSegment(sketch, "E14.6.9.12", {"start": v(82.49, 31.75) * mm, "end": v(79.74, 26.99) * mm});
            skCircle(sketch, "E14.9.9.12", {"center": v(76.99, 31.75) * mm, "radius": 4.76 * mm, "construction": true});
            skLineSegment(sketch, "E14.11.9.12", {"start": v(79.74, 26.99) * mm, "end": v(74.24, 26.99) * mm});
            skLineSegment(sketch, "E14.14.9.12", {"start": v(74.24, 26.99) * mm, "end": v(71.49, 31.75) * mm});
            skLineSegment(sketch, "E14.17.9.12", {"start": v(71.49, 31.75) * mm, "end": v(74.24, 36.51) * mm});
            skLineSegment(sketch, "E14.0.9.13", {"start": v(74.24, 49.21) * mm, "end": v(79.74, 49.21) * mm});
            skLineSegment(sketch, "E14.3.9.13", {"start": v(79.74, 49.21) * mm, "end": v(82.49, 44.45) * mm});
            skLineSegment(sketch, "E14.6.9.13", {"start": v(82.49, 44.45) * mm, "end": v(79.74, 39.69) * mm});
            skCircle(sketch, "E14.9.9.13", {"center": v(76.99, 44.45) * mm, "radius": 4.76 * mm, "construction": true});
            skLineSegment(sketch, "E14.11.9.13", {"start": v(79.74, 39.69) * mm, "end": v(74.24, 39.69) * mm});
            skLineSegment(sketch, "E14.14.9.13", {"start": v(74.24, 39.69) * mm, "end": v(71.49, 44.45) * mm});
            skLineSegment(sketch, "E14.17.9.13", {"start": v(71.49, 44.45) * mm, "end": v(74.24, 49.21) * mm});
            skLineSegment(sketch, "E14.0.9.14", {"start": v(74.24, 61.91) * mm, "end": v(79.74, 61.91) * mm});
            skLineSegment(sketch, "E14.3.9.14", {"start": v(79.74, 61.91) * mm, "end": v(82.49, 57.15) * mm});
            skLineSegment(sketch, "E14.6.9.14", {"start": v(82.49, 57.15) * mm, "end": v(79.74, 52.39) * mm});
            skCircle(sketch, "E14.9.9.14", {"center": v(76.99, 57.15) * mm, "radius": 4.76 * mm, "construction": true});
            skLineSegment(sketch, "E14.11.9.14", {"start": v(79.74, 52.39) * mm, "end": v(74.24, 52.39) * mm});
            skLineSegment(sketch, "E14.14.9.14", {"start": v(74.24, 52.39) * mm, "end": v(71.49, 57.15) * mm});
            skLineSegment(sketch, "E14.17.9.14", {"start": v(71.49, 57.15) * mm, "end": v(74.24, 61.91) * mm});
            skLineSegment(sketch, "E14.0.9.15", {"start": v(74.24, 74.61) * mm, "end": v(79.74, 74.61) * mm});
            skLineSegment(sketch, "E14.3.9.15", {"start": v(79.74, 74.61) * mm, "end": v(82.49, 69.85) * mm});
            skLineSegment(sketch, "E14.6.9.15", {"start": v(82.49, 69.85) * mm, "end": v(79.74, 65.09) * mm});
            skCircle(sketch, "E14.9.9.15", {"center": v(76.99, 69.85) * mm, "radius": 4.76 * mm, "construction": true});
            skLineSegment(sketch, "E14.11.9.15", {"start": v(79.74, 65.09) * mm, "end": v(74.24, 65.09) * mm});
            skLineSegment(sketch, "E14.14.9.15", {"start": v(74.24, 65.09) * mm, "end": v(71.49, 69.85) * mm});
            skLineSegment(sketch, "E14.17.9.15", {"start": v(71.49, 69.85) * mm, "end": v(74.24, 74.61) * mm});
            skLineSegment(sketch, "E14.0.9.16", {"start": v(74.24, 87.31) * mm, "end": v(79.74, 87.31) * mm});
            skLineSegment(sketch, "E14.3.9.16", {"start": v(79.74, 87.31) * mm, "end": v(82.49, 82.55) * mm});
            skLineSegment(sketch, "E14.6.9.16", {"start": v(82.49, 82.55) * mm, "end": v(79.74, 77.79) * mm});
            skCircle(sketch, "E14.9.9.16", {"center": v(76.99, 82.55) * mm, "radius": 4.76 * mm, "construction": true});
            skLineSegment(sketch, "E14.11.9.16", {"start": v(79.74, 77.79) * mm, "end": v(74.24, 77.79) * mm});
            skLineSegment(sketch, "E14.14.9.16", {"start": v(74.24, 77.79) * mm, "end": v(71.49, 82.55) * mm});
            skLineSegment(sketch, "E14.17.9.16", {"start": v(71.49, 82.55) * mm, "end": v(74.24, 87.31) * mm});
            skLineSegment(sketch, "E14.0.9.17", {"start": v(74.24, 100.01) * mm, "end": v(79.74, 100.01) * mm});
            skLineSegment(sketch, "E14.3.9.17", {"start": v(79.74, 100.01) * mm, "end": v(82.49, 95.25) * mm});
            skLineSegment(sketch, "E14.6.9.17", {"start": v(82.49, 95.25) * mm, "end": v(79.74, 90.49) * mm});
            skCircle(sketch, "E14.9.9.17", {"center": v(76.99, 95.25) * mm, "radius": 4.76 * mm, "construction": true});
            skLineSegment(sketch, "E14.11.9.17", {"start": v(79.74, 90.49) * mm, "end": v(74.24, 90.49) * mm});
            skLineSegment(sketch, "E14.14.9.17", {"start": v(74.24, 90.49) * mm, "end": v(71.49, 95.25) * mm});
            skLineSegment(sketch, "E14.17.9.17", {"start": v(71.49, 95.25) * mm, "end": v(74.24, 100.01) * mm});
            skLineSegment(sketch, "E14.0.9.18", {"start": v(74.24, 112.71) * mm, "end": v(79.74, 112.71) * mm});
            skLineSegment(sketch, "E14.3.9.18", {"start": v(79.74, 112.71) * mm, "end": v(82.49, 107.95) * mm});
            skLineSegment(sketch, "E14.6.9.18", {"start": v(82.49, 107.95) * mm, "end": v(79.74, 103.19) * mm});
            skCircle(sketch, "E14.9.9.18", {"center": v(76.99, 107.95) * mm, "radius": 4.76 * mm, "construction": true});
            skLineSegment(sketch, "E14.11.9.18", {"start": v(79.74, 103.19) * mm, "end": v(74.24, 103.19) * mm});
            skLineSegment(sketch, "E14.14.9.18", {"start": v(74.24, 103.19) * mm, "end": v(71.49, 107.95) * mm});
            skLineSegment(sketch, "E14.17.9.18", {"start": v(71.49, 107.95) * mm, "end": v(74.24, 112.71) * mm});
            skLineSegment(sketch, "E14.0.9.19", {"start": v(74.24, 125.41) * mm, "end": v(79.74, 125.41) * mm});
            skLineSegment(sketch, "E14.3.9.19", {"start": v(79.74, 125.41) * mm, "end": v(82.49, 120.65) * mm});
            skLineSegment(sketch, "E14.6.9.19", {"start": v(82.49, 120.65) * mm, "end": v(79.74, 115.89) * mm});
            skCircle(sketch, "E14.9.9.19", {"center": v(76.99, 120.65) * mm, "radius": 4.76 * mm, "construction": true});
            skLineSegment(sketch, "E14.11.9.19", {"start": v(79.74, 115.89) * mm, "end": v(74.24, 115.89) * mm});
            skLineSegment(sketch, "E14.14.9.19", {"start": v(74.24, 115.89) * mm, "end": v(71.49, 120.65) * mm});
            skLineSegment(sketch, "E14.17.9.19", {"start": v(71.49, 120.65) * mm, "end": v(74.24, 125.41) * mm});
            skLineSegment(sketch, "E14.0.10.0", {"start": v(96.23, -115.89) * mm, "end": v(101.73, -115.89) * mm});
            skLineSegment(sketch, "E14.3.10.0", {"start": v(101.73, -115.89) * mm, "end": v(104.48, -120.65) * mm});
            skLineSegment(sketch, "E14.6.10.0", {"start": v(104.48, -120.65) * mm, "end": v(101.73, -125.41) * mm});
            skCircle(sketch, "E14.9.10.0", {"center": v(98.98, -120.65) * mm, "radius": 4.76 * mm, "construction": true});
            skLineSegment(sketch, "E14.11.10.0", {"start": v(101.73, -125.41) * mm, "end": v(96.23, -125.41) * mm});
            skLineSegment(sketch, "E14.14.10.0", {"start": v(96.23, -125.41) * mm, "end": v(93.48, -120.65) * mm});
            skLineSegment(sketch, "E14.17.10.0", {"start": v(93.48, -120.65) * mm, "end": v(96.23, -115.89) * mm});
            skLineSegment(sketch, "E14.0.10.1", {"start": v(96.23, -103.19) * mm, "end": v(101.73, -103.19) * mm});
            skLineSegment(sketch, "E14.3.10.1", {"start": v(101.73, -103.19) * mm, "end": v(104.48, -107.95) * mm});
            skLineSegment(sketch, "E14.6.10.1", {"start": v(104.48, -107.95) * mm, "end": v(101.73, -112.71) * mm});
            skCircle(sketch, "E14.9.10.1", {"center": v(98.98, -107.95) * mm, "radius": 4.76 * mm, "construction": true});
            skLineSegment(sketch, "E14.11.10.1", {"start": v(101.73, -112.71) * mm, "end": v(96.23, -112.71) * mm});
            skLineSegment(sketch, "E14.14.10.1", {"start": v(96.23, -112.71) * mm, "end": v(93.48, -107.95) * mm});
            skLineSegment(sketch, "E14.17.10.1", {"start": v(93.48, -107.95) * mm, "end": v(96.23, -103.19) * mm});
            skLineSegment(sketch, "E14.0.10.2", {"start": v(96.23, -90.49) * mm, "end": v(101.73, -90.49) * mm});
            skLineSegment(sketch, "E14.3.10.2", {"start": v(101.73, -90.49) * mm, "end": v(104.48, -95.25) * mm});
            skLineSegment(sketch, "E14.6.10.2", {"start": v(104.48, -95.25) * mm, "end": v(101.73, -100.01) * mm});
            skCircle(sketch, "E14.9.10.2", {"center": v(98.98, -95.25) * mm, "radius": 4.76 * mm, "construction": true});
            skLineSegment(sketch, "E14.11.10.2", {"start": v(101.73, -100.01) * mm, "end": v(96.23, -100.01) * mm});
            skLineSegment(sketch, "E14.14.10.2", {"start": v(96.23, -100.01) * mm, "end": v(93.48, -95.25) * mm});
            skLineSegment(sketch, "E14.17.10.2", {"start": v(93.48, -95.25) * mm, "end": v(96.23, -90.49) * mm});
            skLineSegment(sketch, "E14.0.10.3", {"start": v(96.23, -77.79) * mm, "end": v(101.73, -77.79) * mm});
            skLineSegment(sketch, "E14.3.10.3", {"start": v(101.73, -77.79) * mm, "end": v(104.48, -82.55) * mm});
            skLineSegment(sketch, "E14.6.10.3", {"start": v(104.48, -82.55) * mm, "end": v(101.73, -87.31) * mm});
            skCircle(sketch, "E14.9.10.3", {"center": v(98.98, -82.55) * mm, "radius": 4.76 * mm, "construction": true});
            skLineSegment(sketch, "E14.11.10.3", {"start": v(101.73, -87.31) * mm, "end": v(96.23, -87.31) * mm});
            skLineSegment(sketch, "E14.14.10.3", {"start": v(96.23, -87.31) * mm, "end": v(93.48, -82.55) * mm});
            skLineSegment(sketch, "E14.17.10.3", {"start": v(93.48, -82.55) * mm, "end": v(96.23, -77.79) * mm});
            skLineSegment(sketch, "E14.0.10.4", {"start": v(96.23, -65.09) * mm, "end": v(101.73, -65.09) * mm});
            skLineSegment(sketch, "E14.3.10.4", {"start": v(101.73, -65.09) * mm, "end": v(104.48, -69.85) * mm});
            skLineSegment(sketch, "E14.6.10.4", {"start": v(104.48, -69.85) * mm, "end": v(101.73, -74.61) * mm});
            skCircle(sketch, "E14.9.10.4", {"center": v(98.98, -69.85) * mm, "radius": 4.76 * mm, "construction": true});
            skLineSegment(sketch, "E14.11.10.4", {"start": v(101.73, -74.61) * mm, "end": v(96.23, -74.61) * mm});
            skLineSegment(sketch, "E14.14.10.4", {"start": v(96.23, -74.61) * mm, "end": v(93.48, -69.85) * mm});
            skLineSegment(sketch, "E14.17.10.4", {"start": v(93.48, -69.85) * mm, "end": v(96.23, -65.09) * mm});
            skLineSegment(sketch, "E14.0.10.5", {"start": v(96.23, -52.39) * mm, "end": v(101.73, -52.39) * mm});
            skLineSegment(sketch, "E14.3.10.5", {"start": v(101.73, -52.39) * mm, "end": v(104.48, -57.15) * mm});
            skLineSegment(sketch, "E14.6.10.5", {"start": v(104.48, -57.15) * mm, "end": v(101.73, -61.91) * mm});
            skCircle(sketch, "E14.9.10.5", {"center": v(98.98, -57.15) * mm, "radius": 4.76 * mm, "construction": true});
            skLineSegment(sketch, "E14.11.10.5", {"start": v(101.73, -61.91) * mm, "end": v(96.23, -61.91) * mm});
            skLineSegment(sketch, "E14.14.10.5", {"start": v(96.23, -61.91) * mm, "end": v(93.48, -57.15) * mm});
            skLineSegment(sketch, "E14.17.10.5", {"start": v(93.48, -57.15) * mm, "end": v(96.23, -52.39) * mm});
            skLineSegment(sketch, "E14.0.10.6", {"start": v(96.23, -39.69) * mm, "end": v(101.73, -39.69) * mm});
            skLineSegment(sketch, "E14.3.10.6", {"start": v(101.73, -39.69) * mm, "end": v(104.48, -44.45) * mm});
            skLineSegment(sketch, "E14.6.10.6", {"start": v(104.48, -44.45) * mm, "end": v(101.73, -49.21) * mm});
            skCircle(sketch, "E14.9.10.6", {"center": v(98.98, -44.45) * mm, "radius": 4.76 * mm, "construction": true});
            skLineSegment(sketch, "E14.11.10.6", {"start": v(101.73, -49.21) * mm, "end": v(96.23, -49.21) * mm});
            skLineSegment(sketch, "E14.14.10.6", {"start": v(96.23, -49.21) * mm, "end": v(93.48, -44.45) * mm});
            skLineSegment(sketch, "E14.17.10.6", {"start": v(93.48, -44.45) * mm, "end": v(96.23, -39.69) * mm});
            skLineSegment(sketch, "E14.0.10.7", {"start": v(96.23, -26.99) * mm, "end": v(101.73, -26.99) * mm});
            skLineSegment(sketch, "E14.3.10.7", {"start": v(101.73, -26.99) * mm, "end": v(104.48, -31.75) * mm});
            skLineSegment(sketch, "E14.6.10.7", {"start": v(104.48, -31.75) * mm, "end": v(101.73, -36.51) * mm});
            skCircle(sketch, "E14.9.10.7", {"center": v(98.98, -31.75) * mm, "radius": 4.76 * mm, "construction": true});
            skLineSegment(sketch, "E14.11.10.7", {"start": v(101.73, -36.51) * mm, "end": v(96.23, -36.51) * mm});
            skLineSegment(sketch, "E14.14.10.7", {"start": v(96.23, -36.51) * mm, "end": v(93.48, -31.75) * mm});
            skLineSegment(sketch, "E14.17.10.7", {"start": v(93.48, -31.75) * mm, "end": v(96.23, -26.99) * mm});
            skLineSegment(sketch, "E14.0.10.8", {"start": v(96.23, -14.29) * mm, "end": v(101.73, -14.29) * mm});
            skLineSegment(sketch, "E14.3.10.8", {"start": v(101.73, -14.29) * mm, "end": v(104.48, -19.05) * mm});
            skLineSegment(sketch, "E14.6.10.8", {"start": v(104.48, -19.05) * mm, "end": v(101.73, -23.81) * mm});
            skCircle(sketch, "E14.9.10.8", {"center": v(98.98, -19.05) * mm, "radius": 4.76 * mm, "construction": true});
            skLineSegment(sketch, "E14.11.10.8", {"start": v(101.73, -23.81) * mm, "end": v(96.23, -23.81) * mm});
            skLineSegment(sketch, "E14.14.10.8", {"start": v(96.23, -23.81) * mm, "end": v(93.48, -19.05) * mm});
            skLineSegment(sketch, "E14.17.10.8", {"start": v(93.48, -19.05) * mm, "end": v(96.23, -14.29) * mm});
            skLineSegment(sketch, "E14.0.10.9", {"start": v(96.23, -1.59) * mm, "end": v(101.73, -1.59) * mm});
            skLineSegment(sketch, "E14.3.10.9", {"start": v(101.73, -1.59) * mm, "end": v(104.48, -6.35) * mm});
            skLineSegment(sketch, "E14.6.10.9", {"start": v(104.48, -6.35) * mm, "end": v(101.73, -11.11) * mm});
            skCircle(sketch, "E14.9.10.9", {"center": v(98.98, -6.35) * mm, "radius": 4.76 * mm, "construction": true});
            skLineSegment(sketch, "E14.11.10.9", {"start": v(101.73, -11.11) * mm, "end": v(96.23, -11.11) * mm});
            skLineSegment(sketch, "E14.14.10.9", {"start": v(96.23, -11.11) * mm, "end": v(93.48, -6.35) * mm});
            skLineSegment(sketch, "E14.17.10.9", {"start": v(93.48, -6.35) * mm, "end": v(96.23, -1.59) * mm});
            skLineSegment(sketch, "E14.0.10.10", {"start": v(96.23, 11.11) * mm, "end": v(101.73, 11.11) * mm});
            skLineSegment(sketch, "E14.3.10.10", {"start": v(101.73, 11.11) * mm, "end": v(104.48, 6.35) * mm});
            skLineSegment(sketch, "E14.6.10.10", {"start": v(104.48, 6.35) * mm, "end": v(101.73, 1.59) * mm});
            skCircle(sketch, "E14.9.10.10", {"center": v(98.98, 6.35) * mm, "radius": 4.76 * mm, "construction": true});
            skLineSegment(sketch, "E14.11.10.10", {"start": v(101.73, 1.59) * mm, "end": v(96.23, 1.59) * mm});
            skLineSegment(sketch, "E14.14.10.10", {"start": v(96.23, 1.59) * mm, "end": v(93.48, 6.35) * mm});
            skLineSegment(sketch, "E14.17.10.10", {"start": v(93.48, 6.35) * mm, "end": v(96.23, 11.11) * mm});
            skLineSegment(sketch, "E14.0.10.11", {"start": v(96.23, 23.81) * mm, "end": v(101.73, 23.81) * mm});
            skLineSegment(sketch, "E14.3.10.11", {"start": v(101.73, 23.81) * mm, "end": v(104.48, 19.05) * mm});
            skLineSegment(sketch, "E14.6.10.11", {"start": v(104.48, 19.05) * mm, "end": v(101.73, 14.29) * mm});
            skCircle(sketch, "E14.9.10.11", {"center": v(98.98, 19.05) * mm, "radius": 4.76 * mm, "construction": true});
            skLineSegment(sketch, "E14.11.10.11", {"start": v(101.73, 14.29) * mm, "end": v(96.23, 14.29) * mm});
            skLineSegment(sketch, "E14.14.10.11", {"start": v(96.23, 14.29) * mm, "end": v(93.48, 19.05) * mm});
            skLineSegment(sketch, "E14.17.10.11", {"start": v(93.48, 19.05) * mm, "end": v(96.23, 23.81) * mm});
            skLineSegment(sketch, "E14.0.10.12", {"start": v(96.23, 36.51) * mm, "end": v(101.73, 36.51) * mm});
            skLineSegment(sketch, "E14.3.10.12", {"start": v(101.73, 36.51) * mm, "end": v(104.48, 31.75) * mm});
            skLineSegment(sketch, "E14.6.10.12", {"start": v(104.48, 31.75) * mm, "end": v(101.73, 26.99) * mm});
            skCircle(sketch, "E14.9.10.12", {"center": v(98.98, 31.75) * mm, "radius": 4.76 * mm, "construction": true});
            skLineSegment(sketch, "E14.11.10.12", {"start": v(101.73, 26.99) * mm, "end": v(96.23, 26.99) * mm});
            skLineSegment(sketch, "E14.14.10.12", {"start": v(96.23, 26.99) * mm, "end": v(93.48, 31.75) * mm});
            skLineSegment(sketch, "E14.17.10.12", {"start": v(93.48, 31.75) * mm, "end": v(96.23, 36.51) * mm});
            skLineSegment(sketch, "E14.0.10.13", {"start": v(96.23, 49.21) * mm, "end": v(101.73, 49.21) * mm});
            skLineSegment(sketch, "E14.3.10.13", {"start": v(101.73, 49.21) * mm, "end": v(104.48, 44.45) * mm});
            skLineSegment(sketch, "E14.6.10.13", {"start": v(104.48, 44.45) * mm, "end": v(101.73, 39.69) * mm});
            skCircle(sketch, "E14.9.10.13", {"center": v(98.98, 44.45) * mm, "radius": 4.76 * mm, "construction": true});
            skLineSegment(sketch, "E14.11.10.13", {"start": v(101.73, 39.69) * mm, "end": v(96.23, 39.69) * mm});
            skLineSegment(sketch, "E14.14.10.13", {"start": v(96.23, 39.69) * mm, "end": v(93.48, 44.45) * mm});
            skLineSegment(sketch, "E14.17.10.13", {"start": v(93.48, 44.45) * mm, "end": v(96.23, 49.21) * mm});
            skLineSegment(sketch, "E14.0.10.14", {"start": v(96.23, 61.91) * mm, "end": v(101.73, 61.91) * mm});
            skLineSegment(sketch, "E14.3.10.14", {"start": v(101.73, 61.91) * mm, "end": v(104.48, 57.15) * mm});
            skLineSegment(sketch, "E14.6.10.14", {"start": v(104.48, 57.15) * mm, "end": v(101.73, 52.39) * mm});
            skCircle(sketch, "E14.9.10.14", {"center": v(98.98, 57.15) * mm, "radius": 4.76 * mm, "construction": true});
            skLineSegment(sketch, "E14.11.10.14", {"start": v(101.73, 52.39) * mm, "end": v(96.23, 52.39) * mm});
            skLineSegment(sketch, "E14.14.10.14", {"start": v(96.23, 52.39) * mm, "end": v(93.48, 57.15) * mm});
            skLineSegment(sketch, "E14.17.10.14", {"start": v(93.48, 57.15) * mm, "end": v(96.23, 61.91) * mm});
            skLineSegment(sketch, "E14.0.10.15", {"start": v(96.23, 74.61) * mm, "end": v(101.73, 74.61) * mm});
            skLineSegment(sketch, "E14.3.10.15", {"start": v(101.73, 74.61) * mm, "end": v(104.48, 69.85) * mm});
            skLineSegment(sketch, "E14.6.10.15", {"start": v(104.48, 69.85) * mm, "end": v(101.73, 65.09) * mm});
            skCircle(sketch, "E14.9.10.15", {"center": v(98.98, 69.85) * mm, "radius": 4.76 * mm, "construction": true});
            skLineSegment(sketch, "E14.11.10.15", {"start": v(101.73, 65.09) * mm, "end": v(96.23, 65.09) * mm});
            skLineSegment(sketch, "E14.14.10.15", {"start": v(96.23, 65.09) * mm, "end": v(93.48, 69.85) * mm});
            skLineSegment(sketch, "E14.17.10.15", {"start": v(93.48, 69.85) * mm, "end": v(96.23, 74.61) * mm});
            skLineSegment(sketch, "E14.0.10.16", {"start": v(96.23, 87.31) * mm, "end": v(101.73, 87.31) * mm});
            skLineSegment(sketch, "E14.3.10.16", {"start": v(101.73, 87.31) * mm, "end": v(104.48, 82.55) * mm});
            skLineSegment(sketch, "E14.6.10.16", {"start": v(104.48, 82.55) * mm, "end": v(101.73, 77.79) * mm});
            skCircle(sketch, "E14.9.10.16", {"center": v(98.98, 82.55) * mm, "radius": 4.76 * mm, "construction": true});
            skLineSegment(sketch, "E14.11.10.16", {"start": v(101.73, 77.79) * mm, "end": v(96.23, 77.79) * mm});
            skLineSegment(sketch, "E14.14.10.16", {"start": v(96.23, 77.79) * mm, "end": v(93.48, 82.55) * mm});
            skLineSegment(sketch, "E14.17.10.16", {"start": v(93.48, 82.55) * mm, "end": v(96.23, 87.31) * mm});
            skLineSegment(sketch, "E14.0.10.17", {"start": v(96.23, 100.01) * mm, "end": v(101.73, 100.01) * mm});
            skLineSegment(sketch, "E14.3.10.17", {"start": v(101.73, 100.01) * mm, "end": v(104.48, 95.25) * mm});
            skLineSegment(sketch, "E14.6.10.17", {"start": v(104.48, 95.25) * mm, "end": v(101.73, 90.49) * mm});
            skCircle(sketch, "E14.9.10.17", {"center": v(98.98, 95.25) * mm, "radius": 4.76 * mm, "construction": true});
            skLineSegment(sketch, "E14.11.10.17", {"start": v(101.73, 90.49) * mm, "end": v(96.23, 90.49) * mm});
            skLineSegment(sketch, "E14.14.10.17", {"start": v(96.23, 90.49) * mm, "end": v(93.48, 95.25) * mm});
            skLineSegment(sketch, "E14.17.10.17", {"start": v(93.48, 95.25) * mm, "end": v(96.23, 100.01) * mm});
            skLineSegment(sketch, "E14.0.10.18", {"start": v(96.23, 112.71) * mm, "end": v(101.73, 112.71) * mm});
            skLineSegment(sketch, "E14.3.10.18", {"start": v(101.73, 112.71) * mm, "end": v(104.48, 107.95) * mm});
            skLineSegment(sketch, "E14.6.10.18", {"start": v(104.48, 107.95) * mm, "end": v(101.73, 103.19) * mm});
            skCircle(sketch, "E14.9.10.18", {"center": v(98.98, 107.95) * mm, "radius": 4.76 * mm, "construction": true});
            skLineSegment(sketch, "E14.11.10.18", {"start": v(101.73, 103.19) * mm, "end": v(96.23, 103.19) * mm});
            skLineSegment(sketch, "E14.14.10.18", {"start": v(96.23, 103.19) * mm, "end": v(93.48, 107.95) * mm});
            skLineSegment(sketch, "E14.17.10.18", {"start": v(93.48, 107.95) * mm, "end": v(96.23, 112.71) * mm});
            skLineSegment(sketch, "E14.0.10.19", {"start": v(96.23, 125.41) * mm, "end": v(101.73, 125.41) * mm});
            skLineSegment(sketch, "E14.3.10.19", {"start": v(101.73, 125.41) * mm, "end": v(104.48, 120.65) * mm});
            skLineSegment(sketch, "E14.6.10.19", {"start": v(104.48, 120.65) * mm, "end": v(101.73, 115.89) * mm});
            skCircle(sketch, "E14.9.10.19", {"center": v(98.98, 120.65) * mm, "radius": 4.76 * mm, "construction": true});
            skLineSegment(sketch, "E14.11.10.19", {"start": v(101.73, 115.89) * mm, "end": v(96.23, 115.89) * mm});
            skLineSegment(sketch, "E14.14.10.19", {"start": v(96.23, 115.89) * mm, "end": v(93.48, 120.65) * mm});
            skLineSegment(sketch, "E14.17.10.19", {"start": v(93.48, 120.65) * mm, "end": v(96.23, 125.41) * mm});
            skLineSegment(sketch, "E14.0.11.0", {"start": v(118.23, -115.89) * mm, "end": v(123.73, -115.89) * mm});
            skLineSegment(sketch, "E14.3.11.0", {"start": v(123.73, -115.89) * mm, "end": v(126.48, -120.65) * mm});
            skLineSegment(sketch, "E14.6.11.0", {"start": v(126.48, -120.65) * mm, "end": v(123.73, -125.41) * mm});
            skCircle(sketch, "E14.9.11.0", {"center": v(120.98, -120.65) * mm, "radius": 4.76 * mm, "construction": true});
            skLineSegment(sketch, "E14.11.11.0", {"start": v(123.73, -125.41) * mm, "end": v(118.23, -125.41) * mm});
            skLineSegment(sketch, "E14.14.11.0", {"start": v(118.23, -125.41) * mm, "end": v(115.48, -120.65) * mm});
            skLineSegment(sketch, "E14.17.11.0", {"start": v(115.48, -120.65) * mm, "end": v(118.23, -115.89) * mm});
            skLineSegment(sketch, "E14.0.11.1", {"start": v(118.23, -103.19) * mm, "end": v(123.73, -103.19) * mm});
            skLineSegment(sketch, "E14.3.11.1", {"start": v(123.73, -103.19) * mm, "end": v(126.48, -107.95) * mm});
            skLineSegment(sketch, "E14.6.11.1", {"start": v(126.48, -107.95) * mm, "end": v(123.73, -112.71) * mm});
            skCircle(sketch, "E14.9.11.1", {"center": v(120.98, -107.95) * mm, "radius": 4.76 * mm, "construction": true});
            skLineSegment(sketch, "E14.11.11.1", {"start": v(123.73, -112.71) * mm, "end": v(118.23, -112.71) * mm});
            skLineSegment(sketch, "E14.14.11.1", {"start": v(118.23, -112.71) * mm, "end": v(115.48, -107.95) * mm});
            skLineSegment(sketch, "E14.17.11.1", {"start": v(115.48, -107.95) * mm, "end": v(118.23, -103.19) * mm});
            skLineSegment(sketch, "E14.0.11.2", {"start": v(118.23, -90.49) * mm, "end": v(123.73, -90.49) * mm});
            skLineSegment(sketch, "E14.3.11.2", {"start": v(123.73, -90.49) * mm, "end": v(126.48, -95.25) * mm});
            skLineSegment(sketch, "E14.6.11.2", {"start": v(126.48, -95.25) * mm, "end": v(123.73, -100.01) * mm});
            skCircle(sketch, "E14.9.11.2", {"center": v(120.98, -95.25) * mm, "radius": 4.76 * mm, "construction": true});
            skLineSegment(sketch, "E14.11.11.2", {"start": v(123.73, -100.01) * mm, "end": v(118.23, -100.01) * mm});
            skLineSegment(sketch, "E14.14.11.2", {"start": v(118.23, -100.01) * mm, "end": v(115.48, -95.25) * mm});
            skLineSegment(sketch, "E14.17.11.2", {"start": v(115.48, -95.25) * mm, "end": v(118.23, -90.49) * mm});
            skLineSegment(sketch, "E14.0.11.3", {"start": v(118.23, -77.79) * mm, "end": v(123.73, -77.79) * mm});
            skLineSegment(sketch, "E14.3.11.3", {"start": v(123.73, -77.79) * mm, "end": v(126.48, -82.55) * mm});
            skLineSegment(sketch, "E14.6.11.3", {"start": v(126.48, -82.55) * mm, "end": v(123.73, -87.31) * mm});
            skCircle(sketch, "E14.9.11.3", {"center": v(120.98, -82.55) * mm, "radius": 4.76 * mm, "construction": true});
            skLineSegment(sketch, "E14.11.11.3", {"start": v(123.73, -87.31) * mm, "end": v(118.23, -87.31) * mm});
            skLineSegment(sketch, "E14.14.11.3", {"start": v(118.23, -87.31) * mm, "end": v(115.48, -82.55) * mm});
            skLineSegment(sketch, "E14.17.11.3", {"start": v(115.48, -82.55) * mm, "end": v(118.23, -77.79) * mm});
            skLineSegment(sketch, "E14.0.11.4", {"start": v(118.23, -65.09) * mm, "end": v(123.73, -65.09) * mm});
            skLineSegment(sketch, "E14.3.11.4", {"start": v(123.73, -65.09) * mm, "end": v(126.48, -69.85) * mm});
            skLineSegment(sketch, "E14.6.11.4", {"start": v(126.48, -69.85) * mm, "end": v(123.73, -74.61) * mm});
            skCircle(sketch, "E14.9.11.4", {"center": v(120.98, -69.85) * mm, "radius": 4.76 * mm, "construction": true});
            skLineSegment(sketch, "E14.11.11.4", {"start": v(123.73, -74.61) * mm, "end": v(118.23, -74.61) * mm});
            skLineSegment(sketch, "E14.14.11.4", {"start": v(118.23, -74.61) * mm, "end": v(115.48, -69.85) * mm});
            skLineSegment(sketch, "E14.17.11.4", {"start": v(115.48, -69.85) * mm, "end": v(118.23, -65.09) * mm});
            skLineSegment(sketch, "E14.0.11.5", {"start": v(118.23, -52.39) * mm, "end": v(123.73, -52.39) * mm});
            skLineSegment(sketch, "E14.3.11.5", {"start": v(123.73, -52.39) * mm, "end": v(126.48, -57.15) * mm});
            skLineSegment(sketch, "E14.6.11.5", {"start": v(126.48, -57.15) * mm, "end": v(123.73, -61.91) * mm});
            skCircle(sketch, "E14.9.11.5", {"center": v(120.98, -57.15) * mm, "radius": 4.76 * mm, "construction": true});
            skLineSegment(sketch, "E14.11.11.5", {"start": v(123.73, -61.91) * mm, "end": v(118.23, -61.91) * mm});
            skLineSegment(sketch, "E14.14.11.5", {"start": v(118.23, -61.91) * mm, "end": v(115.48, -57.15) * mm});
            skLineSegment(sketch, "E14.17.11.5", {"start": v(115.48, -57.15) * mm, "end": v(118.23, -52.39) * mm});
            skLineSegment(sketch, "E14.0.11.6", {"start": v(118.23, -39.69) * mm, "end": v(123.73, -39.69) * mm});
            skLineSegment(sketch, "E14.3.11.6", {"start": v(123.73, -39.69) * mm, "end": v(126.48, -44.45) * mm});
            skLineSegment(sketch, "E14.6.11.6", {"start": v(126.48, -44.45) * mm, "end": v(123.73, -49.21) * mm});
            skCircle(sketch, "E14.9.11.6", {"center": v(120.98, -44.45) * mm, "radius": 4.76 * mm, "construction": true});
            skLineSegment(sketch, "E14.11.11.6", {"start": v(123.73, -49.21) * mm, "end": v(118.23, -49.21) * mm});
            skLineSegment(sketch, "E14.14.11.6", {"start": v(118.23, -49.21) * mm, "end": v(115.48, -44.45) * mm});
            skLineSegment(sketch, "E14.17.11.6", {"start": v(115.48, -44.45) * mm, "end": v(118.23, -39.69) * mm});
            skLineSegment(sketch, "E14.0.11.7", {"start": v(118.23, -26.99) * mm, "end": v(123.73, -26.99) * mm});
            skLineSegment(sketch, "E14.3.11.7", {"start": v(123.73, -26.99) * mm, "end": v(126.48, -31.75) * mm});
            skLineSegment(sketch, "E14.6.11.7", {"start": v(126.48, -31.75) * mm, "end": v(123.73, -36.51) * mm});
            skCircle(sketch, "E14.9.11.7", {"center": v(120.98, -31.75) * mm, "radius": 4.76 * mm, "construction": true});
            skLineSegment(sketch, "E14.11.11.7", {"start": v(123.73, -36.51) * mm, "end": v(118.23, -36.51) * mm});
            skLineSegment(sketch, "E14.14.11.7", {"start": v(118.23, -36.51) * mm, "end": v(115.48, -31.75) * mm});
            skLineSegment(sketch, "E14.17.11.7", {"start": v(115.48, -31.75) * mm, "end": v(118.23, -26.99) * mm});
            skLineSegment(sketch, "E14.0.11.8", {"start": v(118.23, -14.29) * mm, "end": v(123.73, -14.29) * mm});
            skLineSegment(sketch, "E14.3.11.8", {"start": v(123.73, -14.29) * mm, "end": v(126.48, -19.05) * mm});
            skLineSegment(sketch, "E14.6.11.8", {"start": v(126.48, -19.05) * mm, "end": v(123.73, -23.81) * mm});
            skCircle(sketch, "E14.9.11.8", {"center": v(120.98, -19.05) * mm, "radius": 4.76 * mm, "construction": true});
            skLineSegment(sketch, "E14.11.11.8", {"start": v(123.73, -23.81) * mm, "end": v(118.23, -23.81) * mm});
            skLineSegment(sketch, "E14.14.11.8", {"start": v(118.23, -23.81) * mm, "end": v(115.48, -19.05) * mm});
            skLineSegment(sketch, "E14.17.11.8", {"start": v(115.48, -19.05) * mm, "end": v(118.23, -14.29) * mm});
            skLineSegment(sketch, "E14.0.11.9", {"start": v(118.23, -1.59) * mm, "end": v(123.73, -1.59) * mm});
            skLineSegment(sketch, "E14.3.11.9", {"start": v(123.73, -1.59) * mm, "end": v(126.48, -6.35) * mm});
            skLineSegment(sketch, "E14.6.11.9", {"start": v(126.48, -6.35) * mm, "end": v(123.73, -11.11) * mm});
            skCircle(sketch, "E14.9.11.9", {"center": v(120.98, -6.35) * mm, "radius": 4.76 * mm, "construction": true});
            skLineSegment(sketch, "E14.11.11.9", {"start": v(123.73, -11.11) * mm, "end": v(118.23, -11.11) * mm});
            skLineSegment(sketch, "E14.14.11.9", {"start": v(118.23, -11.11) * mm, "end": v(115.48, -6.35) * mm});
            skLineSegment(sketch, "E14.17.11.9", {"start": v(115.48, -6.35) * mm, "end": v(118.23, -1.59) * mm});
            skLineSegment(sketch, "E14.0.11.10", {"start": v(118.23, 11.11) * mm, "end": v(123.73, 11.11) * mm});
            skLineSegment(sketch, "E14.3.11.10", {"start": v(123.73, 11.11) * mm, "end": v(126.48, 6.35) * mm});
            skLineSegment(sketch, "E14.6.11.10", {"start": v(126.48, 6.35) * mm, "end": v(123.73, 1.59) * mm});
            skCircle(sketch, "E14.9.11.10", {"center": v(120.98, 6.35) * mm, "radius": 4.76 * mm, "construction": true});
            skLineSegment(sketch, "E14.11.11.10", {"start": v(123.73, 1.59) * mm, "end": v(118.23, 1.59) * mm});
            skLineSegment(sketch, "E14.14.11.10", {"start": v(118.23, 1.59) * mm, "end": v(115.48, 6.35) * mm});
            skLineSegment(sketch, "E14.17.11.10", {"start": v(115.48, 6.35) * mm, "end": v(118.23, 11.11) * mm});
            skLineSegment(sketch, "E14.0.11.11", {"start": v(118.23, 23.81) * mm, "end": v(123.73, 23.81) * mm});
            skLineSegment(sketch, "E14.3.11.11", {"start": v(123.73, 23.81) * mm, "end": v(126.48, 19.05) * mm});
            skLineSegment(sketch, "E14.6.11.11", {"start": v(126.48, 19.05) * mm, "end": v(123.73, 14.29) * mm});
            skCircle(sketch, "E14.9.11.11", {"center": v(120.98, 19.05) * mm, "radius": 4.76 * mm, "construction": true});
            skLineSegment(sketch, "E14.11.11.11", {"start": v(123.73, 14.29) * mm, "end": v(118.23, 14.29) * mm});
            skLineSegment(sketch, "E14.14.11.11", {"start": v(118.23, 14.29) * mm, "end": v(115.48, 19.05) * mm});
            skLineSegment(sketch, "E14.17.11.11", {"start": v(115.48, 19.05) * mm, "end": v(118.23, 23.81) * mm});
            skLineSegment(sketch, "E14.0.11.12", {"start": v(118.23, 36.51) * mm, "end": v(123.73, 36.51) * mm});
            skLineSegment(sketch, "E14.3.11.12", {"start": v(123.73, 36.51) * mm, "end": v(126.48, 31.75) * mm});
            skLineSegment(sketch, "E14.6.11.12", {"start": v(126.48, 31.75) * mm, "end": v(123.73, 26.99) * mm});
            skCircle(sketch, "E14.9.11.12", {"center": v(120.98, 31.75) * mm, "radius": 4.76 * mm, "construction": true});
            skLineSegment(sketch, "E14.11.11.12", {"start": v(123.73, 26.99) * mm, "end": v(118.23, 26.99) * mm});
            skLineSegment(sketch, "E14.14.11.12", {"start": v(118.23, 26.99) * mm, "end": v(115.48, 31.75) * mm});
            skLineSegment(sketch, "E14.17.11.12", {"start": v(115.48, 31.75) * mm, "end": v(118.23, 36.51) * mm});
            skLineSegment(sketch, "E14.0.11.13", {"start": v(118.23, 49.21) * mm, "end": v(123.73, 49.21) * mm});
            skLineSegment(sketch, "E14.3.11.13", {"start": v(123.73, 49.21) * mm, "end": v(126.48, 44.45) * mm});
            skLineSegment(sketch, "E14.6.11.13", {"start": v(126.48, 44.45) * mm, "end": v(123.73, 39.69) * mm});
            skCircle(sketch, "E14.9.11.13", {"center": v(120.98, 44.45) * mm, "radius": 4.76 * mm, "construction": true});
            skLineSegment(sketch, "E14.11.11.13", {"start": v(123.73, 39.69) * mm, "end": v(118.23, 39.69) * mm});
            skLineSegment(sketch, "E14.14.11.13", {"start": v(118.23, 39.69) * mm, "end": v(115.48, 44.45) * mm});
            skLineSegment(sketch, "E14.17.11.13", {"start": v(115.48, 44.45) * mm, "end": v(118.23, 49.21) * mm});
            skLineSegment(sketch, "E14.0.11.14", {"start": v(118.23, 61.91) * mm, "end": v(123.73, 61.91) * mm});
            skLineSegment(sketch, "E14.3.11.14", {"start": v(123.73, 61.91) * mm, "end": v(126.48, 57.15) * mm});
            skLineSegment(sketch, "E14.6.11.14", {"start": v(126.48, 57.15) * mm, "end": v(123.73, 52.39) * mm});
            skCircle(sketch, "E14.9.11.14", {"center": v(120.98, 57.15) * mm, "radius": 4.76 * mm, "construction": true});
            skLineSegment(sketch, "E14.11.11.14", {"start": v(123.73, 52.39) * mm, "end": v(118.23, 52.39) * mm});
            skLineSegment(sketch, "E14.14.11.14", {"start": v(118.23, 52.39) * mm, "end": v(115.48, 57.15) * mm});
            skLineSegment(sketch, "E14.17.11.14", {"start": v(115.48, 57.15) * mm, "end": v(118.23, 61.91) * mm});
            skLineSegment(sketch, "E14.0.11.15", {"start": v(118.23, 74.61) * mm, "end": v(123.73, 74.61) * mm});
            skLineSegment(sketch, "E14.3.11.15", {"start": v(123.73, 74.61) * mm, "end": v(126.48, 69.85) * mm});
            skLineSegment(sketch, "E14.6.11.15", {"start": v(126.48, 69.85) * mm, "end": v(123.73, 65.09) * mm});
            skCircle(sketch, "E14.9.11.15", {"center": v(120.98, 69.85) * mm, "radius": 4.76 * mm, "construction": true});
            skLineSegment(sketch, "E14.11.11.15", {"start": v(123.73, 65.09) * mm, "end": v(118.23, 65.09) * mm});
            skLineSegment(sketch, "E14.14.11.15", {"start": v(118.23, 65.09) * mm, "end": v(115.48, 69.85) * mm});
            skLineSegment(sketch, "E14.17.11.15", {"start": v(115.48, 69.85) * mm, "end": v(118.23, 74.61) * mm});
            skLineSegment(sketch, "E14.0.11.16", {"start": v(118.23, 87.31) * mm, "end": v(123.73, 87.31) * mm});
            skLineSegment(sketch, "E14.3.11.16", {"start": v(123.73, 87.31) * mm, "end": v(126.48, 82.55) * mm});
            skLineSegment(sketch, "E14.6.11.16", {"start": v(126.48, 82.55) * mm, "end": v(123.73, 77.79) * mm});
            skCircle(sketch, "E14.9.11.16", {"center": v(120.98, 82.55) * mm, "radius": 4.76 * mm, "construction": true});
            skLineSegment(sketch, "E14.11.11.16", {"start": v(123.73, 77.79) * mm, "end": v(118.23, 77.79) * mm});
            skLineSegment(sketch, "E14.14.11.16", {"start": v(118.23, 77.79) * mm, "end": v(115.48, 82.55) * mm});
            skLineSegment(sketch, "E14.17.11.16", {"start": v(115.48, 82.55) * mm, "end": v(118.23, 87.31) * mm});
            skLineSegment(sketch, "E14.0.11.17", {"start": v(118.23, 100.01) * mm, "end": v(123.73, 100.01) * mm});
            skLineSegment(sketch, "E14.3.11.17", {"start": v(123.73, 100.01) * mm, "end": v(126.48, 95.25) * mm});
            skLineSegment(sketch, "E14.6.11.17", {"start": v(126.48, 95.25) * mm, "end": v(123.73, 90.49) * mm});
            skCircle(sketch, "E14.9.11.17", {"center": v(120.98, 95.25) * mm, "radius": 4.76 * mm, "construction": true});
            skLineSegment(sketch, "E14.11.11.17", {"start": v(123.73, 90.49) * mm, "end": v(118.23, 90.49) * mm});
            skLineSegment(sketch, "E14.14.11.17", {"start": v(118.23, 90.49) * mm, "end": v(115.48, 95.25) * mm});
            skLineSegment(sketch, "E14.17.11.17", {"start": v(115.48, 95.25) * mm, "end": v(118.23, 100.01) * mm});
            skLineSegment(sketch, "E14.0.11.18", {"start": v(118.23, 112.71) * mm, "end": v(123.73, 112.71) * mm});
            skLineSegment(sketch, "E14.3.11.18", {"start": v(123.73, 112.71) * mm, "end": v(126.48, 107.95) * mm});
            skLineSegment(sketch, "E14.6.11.18", {"start": v(126.48, 107.95) * mm, "end": v(123.73, 103.19) * mm});
            skCircle(sketch, "E14.9.11.18", {"center": v(120.98, 107.95) * mm, "radius": 4.76 * mm, "construction": true});
            skLineSegment(sketch, "E14.11.11.18", {"start": v(123.73, 103.19) * mm, "end": v(118.23, 103.19) * mm});
            skLineSegment(sketch, "E14.14.11.18", {"start": v(118.23, 103.19) * mm, "end": v(115.48, 107.95) * mm});
            skLineSegment(sketch, "E14.17.11.18", {"start": v(115.48, 107.95) * mm, "end": v(118.23, 112.71) * mm});
            skLineSegment(sketch, "E14.0.11.19", {"start": v(118.23, 125.41) * mm, "end": v(123.73, 125.41) * mm});
            skLineSegment(sketch, "E14.3.11.19", {"start": v(123.73, 125.41) * mm, "end": v(126.48, 120.65) * mm});
            skLineSegment(sketch, "E14.6.11.19", {"start": v(126.48, 120.65) * mm, "end": v(123.73, 115.89) * mm});
            skCircle(sketch, "E14.9.11.19", {"center": v(120.98, 120.65) * mm, "radius": 4.76 * mm, "construction": true});
            skLineSegment(sketch, "E14.11.11.19", {"start": v(123.73, 115.89) * mm, "end": v(118.23, 115.89) * mm});
            skLineSegment(sketch, "E14.14.11.19", {"start": v(118.23, 115.89) * mm, "end": v(115.48, 120.65) * mm});
            skLineSegment(sketch, "E14.17.11.19", {"start": v(115.48, 120.65) * mm, "end": v(118.23, 125.41) * mm});
            skLineSegment(sketch, "E14.0.12.0", {"start": v(140.23, -115.89) * mm, "end": v(145.73, -115.89) * mm});
            skLineSegment(sketch, "E14.3.12.0", {"start": v(145.73, -115.89) * mm, "end": v(148.48, -120.65) * mm});
            skLineSegment(sketch, "E14.6.12.0", {"start": v(148.48, -120.65) * mm, "end": v(145.73, -125.41) * mm});
            skCircle(sketch, "E14.9.12.0", {"center": v(142.98, -120.65) * mm, "radius": 4.76 * mm, "construction": true});
            skLineSegment(sketch, "E14.11.12.0", {"start": v(145.73, -125.41) * mm, "end": v(140.23, -125.41) * mm});
            skLineSegment(sketch, "E14.14.12.0", {"start": v(140.23, -125.41) * mm, "end": v(137.48, -120.65) * mm});
            skLineSegment(sketch, "E14.17.12.0", {"start": v(137.48, -120.65) * mm, "end": v(140.23, -115.89) * mm});
            skLineSegment(sketch, "E14.0.12.1", {"start": v(140.23, -103.19) * mm, "end": v(145.73, -103.19) * mm});
            skLineSegment(sketch, "E14.3.12.1", {"start": v(145.73, -103.19) * mm, "end": v(148.48, -107.95) * mm});
            skLineSegment(sketch, "E14.6.12.1", {"start": v(148.48, -107.95) * mm, "end": v(145.73, -112.71) * mm});
            skCircle(sketch, "E14.9.12.1", {"center": v(142.98, -107.95) * mm, "radius": 4.76 * mm, "construction": true});
            skLineSegment(sketch, "E14.11.12.1", {"start": v(145.73, -112.71) * mm, "end": v(140.23, -112.71) * mm});
            skLineSegment(sketch, "E14.14.12.1", {"start": v(140.23, -112.71) * mm, "end": v(137.48, -107.95) * mm});
            skLineSegment(sketch, "E14.17.12.1", {"start": v(137.48, -107.95) * mm, "end": v(140.23, -103.19) * mm});
            skLineSegment(sketch, "E14.0.12.2", {"start": v(140.23, -90.49) * mm, "end": v(145.73, -90.49) * mm});
            skLineSegment(sketch, "E14.3.12.2", {"start": v(145.73, -90.49) * mm, "end": v(148.48, -95.25) * mm});
            skLineSegment(sketch, "E14.6.12.2", {"start": v(148.48, -95.25) * mm, "end": v(145.73, -100.01) * mm});
            skCircle(sketch, "E14.9.12.2", {"center": v(142.98, -95.25) * mm, "radius": 4.76 * mm, "construction": true});
            skLineSegment(sketch, "E14.11.12.2", {"start": v(145.73, -100.01) * mm, "end": v(140.23, -100.01) * mm});
            skLineSegment(sketch, "E14.14.12.2", {"start": v(140.23, -100.01) * mm, "end": v(137.48, -95.25) * mm});
            skLineSegment(sketch, "E14.17.12.2", {"start": v(137.48, -95.25) * mm, "end": v(140.23, -90.49) * mm});
            skLineSegment(sketch, "E14.0.12.3", {"start": v(140.23, -77.79) * mm, "end": v(145.73, -77.79) * mm});
            skLineSegment(sketch, "E14.3.12.3", {"start": v(145.73, -77.79) * mm, "end": v(148.48, -82.55) * mm});
            skLineSegment(sketch, "E14.6.12.3", {"start": v(148.48, -82.55) * mm, "end": v(145.73, -87.31) * mm});
            skCircle(sketch, "E14.9.12.3", {"center": v(142.98, -82.55) * mm, "radius": 4.76 * mm, "construction": true});
            skLineSegment(sketch, "E14.11.12.3", {"start": v(145.73, -87.31) * mm, "end": v(140.23, -87.31) * mm});
            skLineSegment(sketch, "E14.14.12.3", {"start": v(140.23, -87.31) * mm, "end": v(137.48, -82.55) * mm});
            skLineSegment(sketch, "E14.17.12.3", {"start": v(137.48, -82.55) * mm, "end": v(140.23, -77.79) * mm});
            skLineSegment(sketch, "E14.0.12.4", {"start": v(140.23, -65.09) * mm, "end": v(145.73, -65.09) * mm});
            skLineSegment(sketch, "E14.3.12.4", {"start": v(145.73, -65.09) * mm, "end": v(148.48, -69.85) * mm});
            skLineSegment(sketch, "E14.6.12.4", {"start": v(148.48, -69.85) * mm, "end": v(145.73, -74.61) * mm});
            skCircle(sketch, "E14.9.12.4", {"center": v(142.98, -69.85) * mm, "radius": 4.76 * mm, "construction": true});
            skLineSegment(sketch, "E14.11.12.4", {"start": v(145.73, -74.61) * mm, "end": v(140.23, -74.61) * mm});
            skLineSegment(sketch, "E14.14.12.4", {"start": v(140.23, -74.61) * mm, "end": v(137.48, -69.85) * mm});
            skLineSegment(sketch, "E14.17.12.4", {"start": v(137.48, -69.85) * mm, "end": v(140.23, -65.09) * mm});
            skLineSegment(sketch, "E14.0.12.5", {"start": v(140.23, -52.39) * mm, "end": v(145.73, -52.39) * mm});
            skLineSegment(sketch, "E14.3.12.5", {"start": v(145.73, -52.39) * mm, "end": v(148.48, -57.15) * mm});
            skLineSegment(sketch, "E14.6.12.5", {"start": v(148.48, -57.15) * mm, "end": v(145.73, -61.91) * mm});
            skCircle(sketch, "E14.9.12.5", {"center": v(142.98, -57.15) * mm, "radius": 4.76 * mm, "construction": true});
            skLineSegment(sketch, "E14.11.12.5", {"start": v(145.73, -61.91) * mm, "end": v(140.23, -61.91) * mm});
            skLineSegment(sketch, "E14.14.12.5", {"start": v(140.23, -61.91) * mm, "end": v(137.48, -57.15) * mm});
            skLineSegment(sketch, "E14.17.12.5", {"start": v(137.48, -57.15) * mm, "end": v(140.23, -52.39) * mm});
            skLineSegment(sketch, "E14.0.12.6", {"start": v(140.23, -39.69) * mm, "end": v(145.73, -39.69) * mm});
            skLineSegment(sketch, "E14.3.12.6", {"start": v(145.73, -39.69) * mm, "end": v(148.48, -44.45) * mm});
            skLineSegment(sketch, "E14.6.12.6", {"start": v(148.48, -44.45) * mm, "end": v(145.73, -49.21) * mm});
            skCircle(sketch, "E14.9.12.6", {"center": v(142.98, -44.45) * mm, "radius": 4.76 * mm, "construction": true});
            skLineSegment(sketch, "E14.11.12.6", {"start": v(145.73, -49.21) * mm, "end": v(140.23, -49.21) * mm});
            skLineSegment(sketch, "E14.14.12.6", {"start": v(140.23, -49.21) * mm, "end": v(137.48, -44.45) * mm});
            skLineSegment(sketch, "E14.17.12.6", {"start": v(137.48, -44.45) * mm, "end": v(140.23, -39.69) * mm});
            skLineSegment(sketch, "E14.0.12.7", {"start": v(140.23, -26.99) * mm, "end": v(145.73, -26.99) * mm});
            skLineSegment(sketch, "E14.3.12.7", {"start": v(145.73, -26.99) * mm, "end": v(148.48, -31.75) * mm});
            skLineSegment(sketch, "E14.6.12.7", {"start": v(148.48, -31.75) * mm, "end": v(145.73, -36.51) * mm});
            skCircle(sketch, "E14.9.12.7", {"center": v(142.98, -31.75) * mm, "radius": 4.76 * mm, "construction": true});
            skLineSegment(sketch, "E14.11.12.7", {"start": v(145.73, -36.51) * mm, "end": v(140.23, -36.51) * mm});
            skLineSegment(sketch, "E14.14.12.7", {"start": v(140.23, -36.51) * mm, "end": v(137.48, -31.75) * mm});
            skLineSegment(sketch, "E14.17.12.7", {"start": v(137.48, -31.75) * mm, "end": v(140.23, -26.99) * mm});
            skLineSegment(sketch, "E14.0.12.8", {"start": v(140.23, -14.29) * mm, "end": v(145.73, -14.29) * mm});
            skLineSegment(sketch, "E14.3.12.8", {"start": v(145.73, -14.29) * mm, "end": v(148.48, -19.05) * mm});
            skLineSegment(sketch, "E14.6.12.8", {"start": v(148.48, -19.05) * mm, "end": v(145.73, -23.81) * mm});
            skCircle(sketch, "E14.9.12.8", {"center": v(142.98, -19.05) * mm, "radius": 4.76 * mm, "construction": true});
            skLineSegment(sketch, "E14.11.12.8", {"start": v(145.73, -23.81) * mm, "end": v(140.23, -23.81) * mm});
            skLineSegment(sketch, "E14.14.12.8", {"start": v(140.23, -23.81) * mm, "end": v(137.48, -19.05) * mm});
            skLineSegment(sketch, "E14.17.12.8", {"start": v(137.48, -19.05) * mm, "end": v(140.23, -14.29) * mm});
            skLineSegment(sketch, "E14.0.12.9", {"start": v(140.23, -1.59) * mm, "end": v(145.73, -1.59) * mm});
            skLineSegment(sketch, "E14.3.12.9", {"start": v(145.73, -1.59) * mm, "end": v(148.48, -6.35) * mm});
            skLineSegment(sketch, "E14.6.12.9", {"start": v(148.48, -6.35) * mm, "end": v(145.73, -11.11) * mm});
            skCircle(sketch, "E14.9.12.9", {"center": v(142.98, -6.35) * mm, "radius": 4.76 * mm, "construction": true});
            skLineSegment(sketch, "E14.11.12.9", {"start": v(145.73, -11.11) * mm, "end": v(140.23, -11.11) * mm});
            skLineSegment(sketch, "E14.14.12.9", {"start": v(140.23, -11.11) * mm, "end": v(137.48, -6.35) * mm});
            skLineSegment(sketch, "E14.17.12.9", {"start": v(137.48, -6.35) * mm, "end": v(140.23, -1.59) * mm});
            skLineSegment(sketch, "E14.0.12.10", {"start": v(140.23, 11.11) * mm, "end": v(145.73, 11.11) * mm});
            skLineSegment(sketch, "E14.3.12.10", {"start": v(145.73, 11.11) * mm, "end": v(148.48, 6.35) * mm});
            skLineSegment(sketch, "E14.6.12.10", {"start": v(148.48, 6.35) * mm, "end": v(145.73, 1.59) * mm});
            skCircle(sketch, "E14.9.12.10", {"center": v(142.98, 6.35) * mm, "radius": 4.76 * mm, "construction": true});
            skLineSegment(sketch, "E14.11.12.10", {"start": v(145.73, 1.59) * mm, "end": v(140.23, 1.59) * mm});
            skLineSegment(sketch, "E14.14.12.10", {"start": v(140.23, 1.59) * mm, "end": v(137.48, 6.35) * mm});
            skLineSegment(sketch, "E14.17.12.10", {"start": v(137.48, 6.35) * mm, "end": v(140.23, 11.11) * mm});
            skLineSegment(sketch, "E14.0.12.11", {"start": v(140.23, 23.81) * mm, "end": v(145.73, 23.81) * mm});
            skLineSegment(sketch, "E14.3.12.11", {"start": v(145.73, 23.81) * mm, "end": v(148.48, 19.05) * mm});
            skLineSegment(sketch, "E14.6.12.11", {"start": v(148.48, 19.05) * mm, "end": v(145.73, 14.29) * mm});
            skCircle(sketch, "E14.9.12.11", {"center": v(142.98, 19.05) * mm, "radius": 4.76 * mm, "construction": true});
            skLineSegment(sketch, "E14.11.12.11", {"start": v(145.73, 14.29) * mm, "end": v(140.23, 14.29) * mm});
            skLineSegment(sketch, "E14.14.12.11", {"start": v(140.23, 14.29) * mm, "end": v(137.48, 19.05) * mm});
            skLineSegment(sketch, "E14.17.12.11", {"start": v(137.48, 19.05) * mm, "end": v(140.23, 23.81) * mm});
            skLineSegment(sketch, "E14.0.12.12", {"start": v(140.23, 36.51) * mm, "end": v(145.73, 36.51) * mm});
            skLineSegment(sketch, "E14.3.12.12", {"start": v(145.73, 36.51) * mm, "end": v(148.48, 31.75) * mm});
            skLineSegment(sketch, "E14.6.12.12", {"start": v(148.48, 31.75) * mm, "end": v(145.73, 26.99) * mm});
            skCircle(sketch, "E14.9.12.12", {"center": v(142.98, 31.75) * mm, "radius": 4.76 * mm, "construction": true});
            skLineSegment(sketch, "E14.11.12.12", {"start": v(145.73, 26.99) * mm, "end": v(140.23, 26.99) * mm});
            skLineSegment(sketch, "E14.14.12.12", {"start": v(140.23, 26.99) * mm, "end": v(137.48, 31.75) * mm});
            skLineSegment(sketch, "E14.17.12.12", {"start": v(137.48, 31.75) * mm, "end": v(140.23, 36.51) * mm});
            skLineSegment(sketch, "E14.0.12.13", {"start": v(140.23, 49.21) * mm, "end": v(145.73, 49.21) * mm});
            skLineSegment(sketch, "E14.3.12.13", {"start": v(145.73, 49.21) * mm, "end": v(148.48, 44.45) * mm});
            skLineSegment(sketch, "E14.6.12.13", {"start": v(148.48, 44.45) * mm, "end": v(145.73, 39.69) * mm});
            skCircle(sketch, "E14.9.12.13", {"center": v(142.98, 44.45) * mm, "radius": 4.76 * mm, "construction": true});
            skLineSegment(sketch, "E14.11.12.13", {"start": v(145.73, 39.69) * mm, "end": v(140.23, 39.69) * mm});
            skLineSegment(sketch, "E14.14.12.13", {"start": v(140.23, 39.69) * mm, "end": v(137.48, 44.45) * mm});
            skLineSegment(sketch, "E14.17.12.13", {"start": v(137.48, 44.45) * mm, "end": v(140.23, 49.21) * mm});
            skLineSegment(sketch, "E14.0.12.14", {"start": v(140.23, 61.91) * mm, "end": v(145.73, 61.91) * mm});
            skLineSegment(sketch, "E14.3.12.14", {"start": v(145.73, 61.91) * mm, "end": v(148.48, 57.15) * mm});
            skLineSegment(sketch, "E14.6.12.14", {"start": v(148.48, 57.15) * mm, "end": v(145.73, 52.39) * mm});
            skCircle(sketch, "E14.9.12.14", {"center": v(142.98, 57.15) * mm, "radius": 4.76 * mm, "construction": true});
            skLineSegment(sketch, "E14.11.12.14", {"start": v(145.73, 52.39) * mm, "end": v(140.23, 52.39) * mm});
            skLineSegment(sketch, "E14.14.12.14", {"start": v(140.23, 52.39) * mm, "end": v(137.48, 57.15) * mm});
            skLineSegment(sketch, "E14.17.12.14", {"start": v(137.48, 57.15) * mm, "end": v(140.23, 61.91) * mm});
            skLineSegment(sketch, "E14.0.12.15", {"start": v(140.23, 74.61) * mm, "end": v(145.73, 74.61) * mm});
            skLineSegment(sketch, "E14.3.12.15", {"start": v(145.73, 74.61) * mm, "end": v(148.48, 69.85) * mm});
            skLineSegment(sketch, "E14.6.12.15", {"start": v(148.48, 69.85) * mm, "end": v(145.73, 65.09) * mm});
            skCircle(sketch, "E14.9.12.15", {"center": v(142.98, 69.85) * mm, "radius": 4.76 * mm, "construction": true});
            skLineSegment(sketch, "E14.11.12.15", {"start": v(145.73, 65.09) * mm, "end": v(140.23, 65.09) * mm});
            skLineSegment(sketch, "E14.14.12.15", {"start": v(140.23, 65.09) * mm, "end": v(137.48, 69.85) * mm});
            skLineSegment(sketch, "E14.17.12.15", {"start": v(137.48, 69.85) * mm, "end": v(140.23, 74.61) * mm});
            skLineSegment(sketch, "E14.0.12.16", {"start": v(140.23, 87.31) * mm, "end": v(145.73, 87.31) * mm});
            skLineSegment(sketch, "E14.3.12.16", {"start": v(145.73, 87.31) * mm, "end": v(148.48, 82.55) * mm});
            skLineSegment(sketch, "E14.6.12.16", {"start": v(148.48, 82.55) * mm, "end": v(145.73, 77.79) * mm});
            skCircle(sketch, "E14.9.12.16", {"center": v(142.98, 82.55) * mm, "radius": 4.76 * mm, "construction": true});
            skLineSegment(sketch, "E14.11.12.16", {"start": v(145.73, 77.79) * mm, "end": v(140.23, 77.79) * mm});
            skLineSegment(sketch, "E14.14.12.16", {"start": v(140.23, 77.79) * mm, "end": v(137.48, 82.55) * mm});
            skLineSegment(sketch, "E14.17.12.16", {"start": v(137.48, 82.55) * mm, "end": v(140.23, 87.31) * mm});
            skLineSegment(sketch, "E14.0.12.17", {"start": v(140.23, 100.01) * mm, "end": v(145.73, 100.01) * mm});
            skLineSegment(sketch, "E14.3.12.17", {"start": v(145.73, 100.01) * mm, "end": v(148.48, 95.25) * mm});
            skLineSegment(sketch, "E14.6.12.17", {"start": v(148.48, 95.25) * mm, "end": v(145.73, 90.49) * mm});
            skCircle(sketch, "E14.9.12.17", {"center": v(142.98, 95.25) * mm, "radius": 4.76 * mm, "construction": true});
            skLineSegment(sketch, "E14.11.12.17", {"start": v(145.73, 90.49) * mm, "end": v(140.23, 90.49) * mm});
            skLineSegment(sketch, "E14.14.12.17", {"start": v(140.23, 90.49) * mm, "end": v(137.48, 95.25) * mm});
            skLineSegment(sketch, "E14.17.12.17", {"start": v(137.48, 95.25) * mm, "end": v(140.23, 100.01) * mm});
            skLineSegment(sketch, "E14.0.12.18", {"start": v(140.23, 112.71) * mm, "end": v(145.73, 112.71) * mm});
            skLineSegment(sketch, "E14.3.12.18", {"start": v(145.73, 112.71) * mm, "end": v(148.48, 107.95) * mm});
            skLineSegment(sketch, "E14.6.12.18", {"start": v(148.48, 107.95) * mm, "end": v(145.73, 103.19) * mm});
            skCircle(sketch, "E14.9.12.18", {"center": v(142.98, 107.95) * mm, "radius": 4.76 * mm, "construction": true});
            skLineSegment(sketch, "E14.11.12.18", {"start": v(145.73, 103.19) * mm, "end": v(140.23, 103.19) * mm});
            skLineSegment(sketch, "E14.14.12.18", {"start": v(140.23, 103.19) * mm, "end": v(137.48, 107.95) * mm});
            skLineSegment(sketch, "E14.17.12.18", {"start": v(137.48, 107.95) * mm, "end": v(140.23, 112.71) * mm});
            skLineSegment(sketch, "E14.0.12.19", {"start": v(140.23, 125.41) * mm, "end": v(145.73, 125.41) * mm});
            skLineSegment(sketch, "E14.3.12.19", {"start": v(145.73, 125.41) * mm, "end": v(148.48, 120.65) * mm});
            skLineSegment(sketch, "E14.6.12.19", {"start": v(148.48, 120.65) * mm, "end": v(145.73, 115.89) * mm});
            skCircle(sketch, "E14.9.12.19", {"center": v(142.98, 120.65) * mm, "radius": 4.76 * mm, "construction": true});
            skLineSegment(sketch, "E14.11.12.19", {"start": v(145.73, 115.89) * mm, "end": v(140.23, 115.89) * mm});
            skLineSegment(sketch, "E14.14.12.19", {"start": v(140.23, 115.89) * mm, "end": v(137.48, 120.65) * mm});
            skLineSegment(sketch, "E14.17.12.19", {"start": v(137.48, 120.65) * mm, "end": v(140.23, 125.41) * mm});
            skLineSegment(sketch, "E14.0.13.0", {"start": v(162.22, -115.89) * mm, "end": v(167.72, -115.89) * mm});
            skLineSegment(sketch, "E14.3.13.0", {"start": v(167.72, -115.89) * mm, "end": v(170.47, -120.65) * mm});
            skLineSegment(sketch, "E14.6.13.0", {"start": v(170.47, -120.65) * mm, "end": v(167.72, -125.41) * mm});
            skCircle(sketch, "E14.9.13.0", {"center": v(164.97, -120.65) * mm, "radius": 4.76 * mm, "construction": true});
            skLineSegment(sketch, "E14.11.13.0", {"start": v(167.72, -125.41) * mm, "end": v(162.22, -125.41) * mm});
            skLineSegment(sketch, "E14.14.13.0", {"start": v(162.22, -125.41) * mm, "end": v(159.47, -120.65) * mm});
            skLineSegment(sketch, "E14.17.13.0", {"start": v(159.47, -120.65) * mm, "end": v(162.22, -115.89) * mm});
            skLineSegment(sketch, "E14.0.13.1", {"start": v(162.22, -103.19) * mm, "end": v(167.72, -103.19) * mm});
            skLineSegment(sketch, "E14.3.13.1", {"start": v(167.72, -103.19) * mm, "end": v(170.47, -107.95) * mm});
            skLineSegment(sketch, "E14.6.13.1", {"start": v(170.47, -107.95) * mm, "end": v(167.72, -112.71) * mm});
            skCircle(sketch, "E14.9.13.1", {"center": v(164.97, -107.95) * mm, "radius": 4.76 * mm, "construction": true});
            skLineSegment(sketch, "E14.11.13.1", {"start": v(167.72, -112.71) * mm, "end": v(162.22, -112.71) * mm});
            skLineSegment(sketch, "E14.14.13.1", {"start": v(162.22, -112.71) * mm, "end": v(159.47, -107.95) * mm});
            skLineSegment(sketch, "E14.17.13.1", {"start": v(159.47, -107.95) * mm, "end": v(162.22, -103.19) * mm});
            skLineSegment(sketch, "E14.0.13.2", {"start": v(162.22, -90.49) * mm, "end": v(167.72, -90.49) * mm});
            skLineSegment(sketch, "E14.3.13.2", {"start": v(167.72, -90.49) * mm, "end": v(170.47, -95.25) * mm});
            skLineSegment(sketch, "E14.6.13.2", {"start": v(170.47, -95.25) * mm, "end": v(167.72, -100.01) * mm});
            skCircle(sketch, "E14.9.13.2", {"center": v(164.97, -95.25) * mm, "radius": 4.76 * mm, "construction": true});
            skLineSegment(sketch, "E14.11.13.2", {"start": v(167.72, -100.01) * mm, "end": v(162.22, -100.01) * mm});
            skLineSegment(sketch, "E14.14.13.2", {"start": v(162.22, -100.01) * mm, "end": v(159.47, -95.25) * mm});
            skLineSegment(sketch, "E14.17.13.2", {"start": v(159.47, -95.25) * mm, "end": v(162.22, -90.49) * mm});
            skLineSegment(sketch, "E14.0.13.3", {"start": v(162.22, -77.79) * mm, "end": v(167.72, -77.79) * mm});
            skLineSegment(sketch, "E14.3.13.3", {"start": v(167.72, -77.79) * mm, "end": v(170.47, -82.55) * mm});
            skLineSegment(sketch, "E14.6.13.3", {"start": v(170.47, -82.55) * mm, "end": v(167.72, -87.31) * mm});
            skCircle(sketch, "E14.9.13.3", {"center": v(164.97, -82.55) * mm, "radius": 4.76 * mm, "construction": true});
            skLineSegment(sketch, "E14.11.13.3", {"start": v(167.72, -87.31) * mm, "end": v(162.22, -87.31) * mm});
            skLineSegment(sketch, "E14.14.13.3", {"start": v(162.22, -87.31) * mm, "end": v(159.47, -82.55) * mm});
            skLineSegment(sketch, "E14.17.13.3", {"start": v(159.47, -82.55) * mm, "end": v(162.22, -77.79) * mm});
            skLineSegment(sketch, "E14.0.13.4", {"start": v(162.22, -65.09) * mm, "end": v(167.72, -65.09) * mm});
            skLineSegment(sketch, "E14.3.13.4", {"start": v(167.72, -65.09) * mm, "end": v(170.47, -69.85) * mm});
            skLineSegment(sketch, "E14.6.13.4", {"start": v(170.47, -69.85) * mm, "end": v(167.72, -74.61) * mm});
            skCircle(sketch, "E14.9.13.4", {"center": v(164.97, -69.85) * mm, "radius": 4.76 * mm, "construction": true});
            skLineSegment(sketch, "E14.11.13.4", {"start": v(167.72, -74.61) * mm, "end": v(162.22, -74.61) * mm});
            skLineSegment(sketch, "E14.14.13.4", {"start": v(162.22, -74.61) * mm, "end": v(159.47, -69.85) * mm});
            skLineSegment(sketch, "E14.17.13.4", {"start": v(159.47, -69.85) * mm, "end": v(162.22, -65.09) * mm});
            skLineSegment(sketch, "E14.0.13.5", {"start": v(162.22, -52.39) * mm, "end": v(167.72, -52.39) * mm});
            skLineSegment(sketch, "E14.3.13.5", {"start": v(167.72, -52.39) * mm, "end": v(170.47, -57.15) * mm});
            skLineSegment(sketch, "E14.6.13.5", {"start": v(170.47, -57.15) * mm, "end": v(167.72, -61.91) * mm});
            skCircle(sketch, "E14.9.13.5", {"center": v(164.97, -57.15) * mm, "radius": 4.76 * mm, "construction": true});
            skLineSegment(sketch, "E14.11.13.5", {"start": v(167.72, -61.91) * mm, "end": v(162.22, -61.91) * mm});
            skLineSegment(sketch, "E14.14.13.5", {"start": v(162.22, -61.91) * mm, "end": v(159.47, -57.15) * mm});
            skLineSegment(sketch, "E14.17.13.5", {"start": v(159.47, -57.15) * mm, "end": v(162.22, -52.39) * mm});
            skLineSegment(sketch, "E14.0.13.6", {"start": v(162.22, -39.69) * mm, "end": v(167.72, -39.69) * mm});
            skLineSegment(sketch, "E14.3.13.6", {"start": v(167.72, -39.69) * mm, "end": v(170.47, -44.45) * mm});
            skLineSegment(sketch, "E14.6.13.6", {"start": v(170.47, -44.45) * mm, "end": v(167.72, -49.21) * mm});
            skCircle(sketch, "E14.9.13.6", {"center": v(164.97, -44.45) * mm, "radius": 4.76 * mm, "construction": true});
            skLineSegment(sketch, "E14.11.13.6", {"start": v(167.72, -49.21) * mm, "end": v(162.22, -49.21) * mm});
            skLineSegment(sketch, "E14.14.13.6", {"start": v(162.22, -49.21) * mm, "end": v(159.47, -44.45) * mm});
            skLineSegment(sketch, "E14.17.13.6", {"start": v(159.47, -44.45) * mm, "end": v(162.22, -39.69) * mm});
            skLineSegment(sketch, "E14.0.13.7", {"start": v(162.22, -26.99) * mm, "end": v(167.72, -26.99) * mm});
            skLineSegment(sketch, "E14.3.13.7", {"start": v(167.72, -26.99) * mm, "end": v(170.47, -31.75) * mm});
            skLineSegment(sketch, "E14.6.13.7", {"start": v(170.47, -31.75) * mm, "end": v(167.72, -36.51) * mm});
            skCircle(sketch, "E14.9.13.7", {"center": v(164.97, -31.75) * mm, "radius": 4.76 * mm, "construction": true});
            skLineSegment(sketch, "E14.11.13.7", {"start": v(167.72, -36.51) * mm, "end": v(162.22, -36.51) * mm});
            skLineSegment(sketch, "E14.14.13.7", {"start": v(162.22, -36.51) * mm, "end": v(159.47, -31.75) * mm});
            skLineSegment(sketch, "E14.17.13.7", {"start": v(159.47, -31.75) * mm, "end": v(162.22, -26.99) * mm});
            skLineSegment(sketch, "E14.0.13.8", {"start": v(162.22, -14.29) * mm, "end": v(167.72, -14.29) * mm});
            skLineSegment(sketch, "E14.3.13.8", {"start": v(167.72, -14.29) * mm, "end": v(170.47, -19.05) * mm});
            skLineSegment(sketch, "E14.6.13.8", {"start": v(170.47, -19.05) * mm, "end": v(167.72, -23.81) * mm});
            skCircle(sketch, "E14.9.13.8", {"center": v(164.97, -19.05) * mm, "radius": 4.76 * mm, "construction": true});
            skLineSegment(sketch, "E14.11.13.8", {"start": v(167.72, -23.81) * mm, "end": v(162.22, -23.81) * mm});
            skLineSegment(sketch, "E14.14.13.8", {"start": v(162.22, -23.81) * mm, "end": v(159.47, -19.05) * mm});
            skLineSegment(sketch, "E14.17.13.8", {"start": v(159.47, -19.05) * mm, "end": v(162.22, -14.29) * mm});
            skLineSegment(sketch, "E14.0.13.9", {"start": v(162.22, -1.59) * mm, "end": v(167.72, -1.59) * mm});
            skLineSegment(sketch, "E14.3.13.9", {"start": v(167.72, -1.59) * mm, "end": v(170.47, -6.35) * mm});
            skLineSegment(sketch, "E14.6.13.9", {"start": v(170.47, -6.35) * mm, "end": v(167.72, -11.11) * mm});
            skCircle(sketch, "E14.9.13.9", {"center": v(164.97, -6.35) * mm, "radius": 4.76 * mm, "construction": true});
            skLineSegment(sketch, "E14.11.13.9", {"start": v(167.72, -11.11) * mm, "end": v(162.22, -11.11) * mm});
            skLineSegment(sketch, "E14.14.13.9", {"start": v(162.22, -11.11) * mm, "end": v(159.47, -6.35) * mm});
            skLineSegment(sketch, "E14.17.13.9", {"start": v(159.47, -6.35) * mm, "end": v(162.22, -1.59) * mm});
            skLineSegment(sketch, "E14.0.13.10", {"start": v(162.22, 11.11) * mm, "end": v(167.72, 11.11) * mm});
            skLineSegment(sketch, "E14.3.13.10", {"start": v(167.72, 11.11) * mm, "end": v(170.47, 6.35) * mm});
            skLineSegment(sketch, "E14.6.13.10", {"start": v(170.47, 6.35) * mm, "end": v(167.72, 1.59) * mm});
            skCircle(sketch, "E14.9.13.10", {"center": v(164.97, 6.35) * mm, "radius": 4.76 * mm, "construction": true});
            skLineSegment(sketch, "E14.11.13.10", {"start": v(167.72, 1.59) * mm, "end": v(162.22, 1.59) * mm});
            skLineSegment(sketch, "E14.14.13.10", {"start": v(162.22, 1.59) * mm, "end": v(159.47, 6.35) * mm});
            skLineSegment(sketch, "E14.17.13.10", {"start": v(159.47, 6.35) * mm, "end": v(162.22, 11.11) * mm});
            skLineSegment(sketch, "E14.0.13.11", {"start": v(162.22, 23.81) * mm, "end": v(167.72, 23.81) * mm});
            skLineSegment(sketch, "E14.3.13.11", {"start": v(167.72, 23.81) * mm, "end": v(170.47, 19.05) * mm});
            skLineSegment(sketch, "E14.6.13.11", {"start": v(170.47, 19.05) * mm, "end": v(167.72, 14.29) * mm});
            skCircle(sketch, "E14.9.13.11", {"center": v(164.97, 19.05) * mm, "radius": 4.76 * mm, "construction": true});
            skLineSegment(sketch, "E14.11.13.11", {"start": v(167.72, 14.29) * mm, "end": v(162.22, 14.29) * mm});
            skLineSegment(sketch, "E14.14.13.11", {"start": v(162.22, 14.29) * mm, "end": v(159.47, 19.05) * mm});
            skLineSegment(sketch, "E14.17.13.11", {"start": v(159.47, 19.05) * mm, "end": v(162.22, 23.81) * mm});
            skLineSegment(sketch, "E14.0.13.12", {"start": v(162.22, 36.51) * mm, "end": v(167.72, 36.51) * mm});
            skLineSegment(sketch, "E14.3.13.12", {"start": v(167.72, 36.51) * mm, "end": v(170.47, 31.75) * mm});
            skLineSegment(sketch, "E14.6.13.12", {"start": v(170.47, 31.75) * mm, "end": v(167.72, 26.99) * mm});
            skCircle(sketch, "E14.9.13.12", {"center": v(164.97, 31.75) * mm, "radius": 4.76 * mm, "construction": true});
            skLineSegment(sketch, "E14.11.13.12", {"start": v(167.72, 26.99) * mm, "end": v(162.22, 26.99) * mm});
            skLineSegment(sketch, "E14.14.13.12", {"start": v(162.22, 26.99) * mm, "end": v(159.47, 31.75) * mm});
            skLineSegment(sketch, "E14.17.13.12", {"start": v(159.47, 31.75) * mm, "end": v(162.22, 36.51) * mm});
            skLineSegment(sketch, "E14.0.13.13", {"start": v(162.22, 49.21) * mm, "end": v(167.72, 49.21) * mm});
            skLineSegment(sketch, "E14.3.13.13", {"start": v(167.72, 49.21) * mm, "end": v(170.47, 44.45) * mm});
            skLineSegment(sketch, "E14.6.13.13", {"start": v(170.47, 44.45) * mm, "end": v(167.72, 39.69) * mm});
            skCircle(sketch, "E14.9.13.13", {"center": v(164.97, 44.45) * mm, "radius": 4.76 * mm, "construction": true});
            skLineSegment(sketch, "E14.11.13.13", {"start": v(167.72, 39.69) * mm, "end": v(162.22, 39.69) * mm});
            skLineSegment(sketch, "E14.14.13.13", {"start": v(162.22, 39.69) * mm, "end": v(159.47, 44.45) * mm});
            skLineSegment(sketch, "E14.17.13.13", {"start": v(159.47, 44.45) * mm, "end": v(162.22, 49.21) * mm});
            skLineSegment(sketch, "E14.0.13.14", {"start": v(162.22, 61.91) * mm, "end": v(167.72, 61.91) * mm});
            skLineSegment(sketch, "E14.3.13.14", {"start": v(167.72, 61.91) * mm, "end": v(170.47, 57.15) * mm});
            skLineSegment(sketch, "E14.6.13.14", {"start": v(170.47, 57.15) * mm, "end": v(167.72, 52.39) * mm});
            skCircle(sketch, "E14.9.13.14", {"center": v(164.97, 57.15) * mm, "radius": 4.76 * mm, "construction": true});
            skLineSegment(sketch, "E14.11.13.14", {"start": v(167.72, 52.39) * mm, "end": v(162.22, 52.39) * mm});
            skLineSegment(sketch, "E14.14.13.14", {"start": v(162.22, 52.39) * mm, "end": v(159.47, 57.15) * mm});
            skLineSegment(sketch, "E14.17.13.14", {"start": v(159.47, 57.15) * mm, "end": v(162.22, 61.91) * mm});
            skLineSegment(sketch, "E14.0.13.15", {"start": v(162.22, 74.61) * mm, "end": v(167.72, 74.61) * mm});
            skLineSegment(sketch, "E14.3.13.15", {"start": v(167.72, 74.61) * mm, "end": v(170.47, 69.85) * mm});
            skLineSegment(sketch, "E14.6.13.15", {"start": v(170.47, 69.85) * mm, "end": v(167.72, 65.09) * mm});
            skCircle(sketch, "E14.9.13.15", {"center": v(164.97, 69.85) * mm, "radius": 4.76 * mm, "construction": true});
            skLineSegment(sketch, "E14.11.13.15", {"start": v(167.72, 65.09) * mm, "end": v(162.22, 65.09) * mm});
            skLineSegment(sketch, "E14.14.13.15", {"start": v(162.22, 65.09) * mm, "end": v(159.47, 69.85) * mm});
            skLineSegment(sketch, "E14.17.13.15", {"start": v(159.47, 69.85) * mm, "end": v(162.22, 74.61) * mm});
            skLineSegment(sketch, "E14.0.13.16", {"start": v(162.22, 87.31) * mm, "end": v(167.72, 87.31) * mm});
            skLineSegment(sketch, "E14.3.13.16", {"start": v(167.72, 87.31) * mm, "end": v(170.47, 82.55) * mm});
            skLineSegment(sketch, "E14.6.13.16", {"start": v(170.47, 82.55) * mm, "end": v(167.72, 77.79) * mm});
            skCircle(sketch, "E14.9.13.16", {"center": v(164.97, 82.55) * mm, "radius": 4.76 * mm, "construction": true});
            skLineSegment(sketch, "E14.11.13.16", {"start": v(167.72, 77.79) * mm, "end": v(162.22, 77.79) * mm});
            skLineSegment(sketch, "E14.14.13.16", {"start": v(162.22, 77.79) * mm, "end": v(159.47, 82.55) * mm});
            skLineSegment(sketch, "E14.17.13.16", {"start": v(159.47, 82.55) * mm, "end": v(162.22, 87.31) * mm});
            skLineSegment(sketch, "E14.0.13.17", {"start": v(162.22, 100.01) * mm, "end": v(167.72, 100.01) * mm});
            skLineSegment(sketch, "E14.3.13.17", {"start": v(167.72, 100.01) * mm, "end": v(170.47, 95.25) * mm});
            skLineSegment(sketch, "E14.6.13.17", {"start": v(170.47, 95.25) * mm, "end": v(167.72, 90.49) * mm});
            skCircle(sketch, "E14.9.13.17", {"center": v(164.97, 95.25) * mm, "radius": 4.76 * mm, "construction": true});
            skLineSegment(sketch, "E14.11.13.17", {"start": v(167.72, 90.49) * mm, "end": v(162.22, 90.49) * mm});
            skLineSegment(sketch, "E14.14.13.17", {"start": v(162.22, 90.49) * mm, "end": v(159.47, 95.25) * mm});
            skLineSegment(sketch, "E14.17.13.17", {"start": v(159.47, 95.25) * mm, "end": v(162.22, 100.01) * mm});
            skLineSegment(sketch, "E14.0.13.18", {"start": v(162.22, 112.71) * mm, "end": v(167.72, 112.71) * mm});
            skLineSegment(sketch, "E14.3.13.18", {"start": v(167.72, 112.71) * mm, "end": v(170.47, 107.95) * mm});
            skLineSegment(sketch, "E14.6.13.18", {"start": v(170.47, 107.95) * mm, "end": v(167.72, 103.19) * mm});
            skCircle(sketch, "E14.9.13.18", {"center": v(164.97, 107.95) * mm, "radius": 4.76 * mm, "construction": true});
            skLineSegment(sketch, "E14.11.13.18", {"start": v(167.72, 103.19) * mm, "end": v(162.22, 103.19) * mm});
            skLineSegment(sketch, "E14.14.13.18", {"start": v(162.22, 103.19) * mm, "end": v(159.47, 107.95) * mm});
            skLineSegment(sketch, "E14.17.13.18", {"start": v(159.47, 107.95) * mm, "end": v(162.22, 112.71) * mm});
            skLineSegment(sketch, "E14.0.13.19", {"start": v(162.22, 125.41) * mm, "end": v(167.72, 125.41) * mm});
            skLineSegment(sketch, "E14.3.13.19", {"start": v(167.72, 125.41) * mm, "end": v(170.47, 120.65) * mm});
            skLineSegment(sketch, "E14.6.13.19", {"start": v(170.47, 120.65) * mm, "end": v(167.72, 115.89) * mm});
            skCircle(sketch, "E14.9.13.19", {"center": v(164.97, 120.65) * mm, "radius": 4.76 * mm, "construction": true});
            skLineSegment(sketch, "E14.11.13.19", {"start": v(167.72, 115.89) * mm, "end": v(162.22, 115.89) * mm});
            skLineSegment(sketch, "E14.14.13.19", {"start": v(162.22, 115.89) * mm, "end": v(159.47, 120.65) * mm});
            skLineSegment(sketch, "E14.17.13.19", {"start": v(159.47, 120.65) * mm, "end": v(162.22, 125.41) * mm});
            skLineSegment(sketch, "E14.0.14.0", {"start": v(184.22, -115.89) * mm, "end": v(189.72, -115.89) * mm});
            skLineSegment(sketch, "E14.3.14.0", {"start": v(189.72, -115.89) * mm, "end": v(192.47, -120.65) * mm});
            skLineSegment(sketch, "E14.6.14.0", {"start": v(192.47, -120.65) * mm, "end": v(189.72, -125.41) * mm});
            skCircle(sketch, "E14.9.14.0", {"center": v(186.97, -120.65) * mm, "radius": 4.76 * mm, "construction": true});
            skLineSegment(sketch, "E14.11.14.0", {"start": v(189.72, -125.41) * mm, "end": v(184.22, -125.41) * mm});
            skLineSegment(sketch, "E14.14.14.0", {"start": v(184.22, -125.41) * mm, "end": v(181.47, -120.65) * mm});
            skLineSegment(sketch, "E14.17.14.0", {"start": v(181.47, -120.65) * mm, "end": v(184.22, -115.89) * mm});
            skLineSegment(sketch, "E14.0.14.1", {"start": v(184.22, -103.19) * mm, "end": v(189.72, -103.19) * mm});
            skLineSegment(sketch, "E14.3.14.1", {"start": v(189.72, -103.19) * mm, "end": v(192.47, -107.95) * mm});
            skLineSegment(sketch, "E14.6.14.1", {"start": v(192.47, -107.95) * mm, "end": v(189.72, -112.71) * mm});
            skCircle(sketch, "E14.9.14.1", {"center": v(186.97, -107.95) * mm, "radius": 4.76 * mm, "construction": true});
            skLineSegment(sketch, "E14.11.14.1", {"start": v(189.72, -112.71) * mm, "end": v(184.22, -112.71) * mm});
            skLineSegment(sketch, "E14.14.14.1", {"start": v(184.22, -112.71) * mm, "end": v(181.47, -107.95) * mm});
            skLineSegment(sketch, "E14.17.14.1", {"start": v(181.47, -107.95) * mm, "end": v(184.22, -103.19) * mm});
            skLineSegment(sketch, "E14.0.14.2", {"start": v(184.22, -90.49) * mm, "end": v(189.72, -90.49) * mm});
            skLineSegment(sketch, "E14.3.14.2", {"start": v(189.72, -90.49) * mm, "end": v(192.47, -95.25) * mm});
            skLineSegment(sketch, "E14.6.14.2", {"start": v(192.47, -95.25) * mm, "end": v(189.72, -100.01) * mm});
            skCircle(sketch, "E14.9.14.2", {"center": v(186.97, -95.25) * mm, "radius": 4.76 * mm, "construction": true});
            skLineSegment(sketch, "E14.11.14.2", {"start": v(189.72, -100.01) * mm, "end": v(184.22, -100.01) * mm});
            skLineSegment(sketch, "E14.14.14.2", {"start": v(184.22, -100.01) * mm, "end": v(181.47, -95.25) * mm});
            skLineSegment(sketch, "E14.17.14.2", {"start": v(181.47, -95.25) * mm, "end": v(184.22, -90.49) * mm});
            skLineSegment(sketch, "E14.0.14.3", {"start": v(184.22, -77.79) * mm, "end": v(189.72, -77.79) * mm});
            skLineSegment(sketch, "E14.3.14.3", {"start": v(189.72, -77.79) * mm, "end": v(192.47, -82.55) * mm});
            skLineSegment(sketch, "E14.6.14.3", {"start": v(192.47, -82.55) * mm, "end": v(189.72, -87.31) * mm});
            skCircle(sketch, "E14.9.14.3", {"center": v(186.97, -82.55) * mm, "radius": 4.76 * mm, "construction": true});
            skLineSegment(sketch, "E14.11.14.3", {"start": v(189.72, -87.31) * mm, "end": v(184.22, -87.31) * mm});
            skLineSegment(sketch, "E14.14.14.3", {"start": v(184.22, -87.31) * mm, "end": v(181.47, -82.55) * mm});
            skLineSegment(sketch, "E14.17.14.3", {"start": v(181.47, -82.55) * mm, "end": v(184.22, -77.79) * mm});
            skLineSegment(sketch, "E14.0.14.4", {"start": v(184.22, -65.09) * mm, "end": v(189.72, -65.09) * mm});
            skLineSegment(sketch, "E14.3.14.4", {"start": v(189.72, -65.09) * mm, "end": v(192.47, -69.85) * mm});
            skLineSegment(sketch, "E14.6.14.4", {"start": v(192.47, -69.85) * mm, "end": v(189.72, -74.61) * mm});
            skCircle(sketch, "E14.9.14.4", {"center": v(186.97, -69.85) * mm, "radius": 4.76 * mm, "construction": true});
            skLineSegment(sketch, "E14.11.14.4", {"start": v(189.72, -74.61) * mm, "end": v(184.22, -74.61) * mm});
            skLineSegment(sketch, "E14.14.14.4", {"start": v(184.22, -74.61) * mm, "end": v(181.47, -69.85) * mm});
            skLineSegment(sketch, "E14.17.14.4", {"start": v(181.47, -69.85) * mm, "end": v(184.22, -65.09) * mm});
            skLineSegment(sketch, "E14.0.14.5", {"start": v(184.22, -52.39) * mm, "end": v(189.72, -52.39) * mm});
            skLineSegment(sketch, "E14.3.14.5", {"start": v(189.72, -52.39) * mm, "end": v(192.47, -57.15) * mm});
            skLineSegment(sketch, "E14.6.14.5", {"start": v(192.47, -57.15) * mm, "end": v(189.72, -61.91) * mm});
            skCircle(sketch, "E14.9.14.5", {"center": v(186.97, -57.15) * mm, "radius": 4.76 * mm, "construction": true});
            skLineSegment(sketch, "E14.11.14.5", {"start": v(189.72, -61.91) * mm, "end": v(184.22, -61.91) * mm});
            skLineSegment(sketch, "E14.14.14.5", {"start": v(184.22, -61.91) * mm, "end": v(181.47, -57.15) * mm});
            skLineSegment(sketch, "E14.17.14.5", {"start": v(181.47, -57.15) * mm, "end": v(184.22, -52.39) * mm});
            skLineSegment(sketch, "E14.0.14.6", {"start": v(184.22, -39.69) * mm, "end": v(189.72, -39.69) * mm});
            skLineSegment(sketch, "E14.3.14.6", {"start": v(189.72, -39.69) * mm, "end": v(192.47, -44.45) * mm});
            skLineSegment(sketch, "E14.6.14.6", {"start": v(192.47, -44.45) * mm, "end": v(189.72, -49.21) * mm});
            skCircle(sketch, "E14.9.14.6", {"center": v(186.97, -44.45) * mm, "radius": 4.76 * mm, "construction": true});
            skLineSegment(sketch, "E14.11.14.6", {"start": v(189.72, -49.21) * mm, "end": v(184.22, -49.21) * mm});
            skLineSegment(sketch, "E14.14.14.6", {"start": v(184.22, -49.21) * mm, "end": v(181.47, -44.45) * mm});
            skLineSegment(sketch, "E14.17.14.6", {"start": v(181.47, -44.45) * mm, "end": v(184.22, -39.69) * mm});
            skLineSegment(sketch, "E14.0.14.7", {"start": v(184.22, -26.99) * mm, "end": v(189.72, -26.99) * mm});
            skLineSegment(sketch, "E14.3.14.7", {"start": v(189.72, -26.99) * mm, "end": v(192.47, -31.75) * mm});
            skLineSegment(sketch, "E14.6.14.7", {"start": v(192.47, -31.75) * mm, "end": v(189.72, -36.51) * mm});
            skCircle(sketch, "E14.9.14.7", {"center": v(186.97, -31.75) * mm, "radius": 4.76 * mm, "construction": true});
            skLineSegment(sketch, "E14.11.14.7", {"start": v(189.72, -36.51) * mm, "end": v(184.22, -36.51) * mm});
            skLineSegment(sketch, "E14.14.14.7", {"start": v(184.22, -36.51) * mm, "end": v(181.47, -31.75) * mm});
            skLineSegment(sketch, "E14.17.14.7", {"start": v(181.47, -31.75) * mm, "end": v(184.22, -26.99) * mm});
            skLineSegment(sketch, "E14.0.14.8", {"start": v(184.22, -14.29) * mm, "end": v(189.72, -14.29) * mm});
            skLineSegment(sketch, "E14.3.14.8", {"start": v(189.72, -14.29) * mm, "end": v(192.47, -19.05) * mm});
            skLineSegment(sketch, "E14.6.14.8", {"start": v(192.47, -19.05) * mm, "end": v(189.72, -23.81) * mm});
            skCircle(sketch, "E14.9.14.8", {"center": v(186.97, -19.05) * mm, "radius": 4.76 * mm, "construction": true});
            skLineSegment(sketch, "E14.11.14.8", {"start": v(189.72, -23.81) * mm, "end": v(184.22, -23.81) * mm});
            skLineSegment(sketch, "E14.14.14.8", {"start": v(184.22, -23.81) * mm, "end": v(181.47, -19.05) * mm});
            skLineSegment(sketch, "E14.17.14.8", {"start": v(181.47, -19.05) * mm, "end": v(184.22, -14.29) * mm});
            skLineSegment(sketch, "E14.0.14.9", {"start": v(184.22, -1.59) * mm, "end": v(189.72, -1.59) * mm});
            skLineSegment(sketch, "E14.3.14.9", {"start": v(189.72, -1.59) * mm, "end": v(192.47, -6.35) * mm});
            skLineSegment(sketch, "E14.6.14.9", {"start": v(192.47, -6.35) * mm, "end": v(189.72, -11.11) * mm});
            skCircle(sketch, "E14.9.14.9", {"center": v(186.97, -6.35) * mm, "radius": 4.76 * mm, "construction": true});
            skLineSegment(sketch, "E14.11.14.9", {"start": v(189.72, -11.11) * mm, "end": v(184.22, -11.11) * mm});
            skLineSegment(sketch, "E14.14.14.9", {"start": v(184.22, -11.11) * mm, "end": v(181.47, -6.35) * mm});
            skLineSegment(sketch, "E14.17.14.9", {"start": v(181.47, -6.35) * mm, "end": v(184.22, -1.59) * mm});
            skLineSegment(sketch, "E14.0.14.10", {"start": v(184.22, 11.11) * mm, "end": v(189.72, 11.11) * mm});
            skLineSegment(sketch, "E14.3.14.10", {"start": v(189.72, 11.11) * mm, "end": v(192.47, 6.35) * mm});
            skLineSegment(sketch, "E14.6.14.10", {"start": v(192.47, 6.35) * mm, "end": v(189.72, 1.59) * mm});
            skCircle(sketch, "E14.9.14.10", {"center": v(186.97, 6.35) * mm, "radius": 4.76 * mm, "construction": true});
            skLineSegment(sketch, "E14.11.14.10", {"start": v(189.72, 1.59) * mm, "end": v(184.22, 1.59) * mm});
            skLineSegment(sketch, "E14.14.14.10", {"start": v(184.22, 1.59) * mm, "end": v(181.47, 6.35) * mm});
            skLineSegment(sketch, "E14.17.14.10", {"start": v(181.47, 6.35) * mm, "end": v(184.22, 11.11) * mm});
            skLineSegment(sketch, "E14.0.14.11", {"start": v(184.22, 23.81) * mm, "end": v(189.72, 23.81) * mm});
            skLineSegment(sketch, "E14.3.14.11", {"start": v(189.72, 23.81) * mm, "end": v(192.47, 19.05) * mm});
            skLineSegment(sketch, "E14.6.14.11", {"start": v(192.47, 19.05) * mm, "end": v(189.72, 14.29) * mm});
            skCircle(sketch, "E14.9.14.11", {"center": v(186.97, 19.05) * mm, "radius": 4.76 * mm, "construction": true});
            skLineSegment(sketch, "E14.11.14.11", {"start": v(189.72, 14.29) * mm, "end": v(184.22, 14.29) * mm});
            skLineSegment(sketch, "E14.14.14.11", {"start": v(184.22, 14.29) * mm, "end": v(181.47, 19.05) * mm});
            skLineSegment(sketch, "E14.17.14.11", {"start": v(181.47, 19.05) * mm, "end": v(184.22, 23.81) * mm});
            skLineSegment(sketch, "E14.0.14.12", {"start": v(184.22, 36.51) * mm, "end": v(189.72, 36.51) * mm});
            skLineSegment(sketch, "E14.3.14.12", {"start": v(189.72, 36.51) * mm, "end": v(192.47, 31.75) * mm});
            skLineSegment(sketch, "E14.6.14.12", {"start": v(192.47, 31.75) * mm, "end": v(189.72, 26.99) * mm});
            skCircle(sketch, "E14.9.14.12", {"center": v(186.97, 31.75) * mm, "radius": 4.76 * mm, "construction": true});
            skLineSegment(sketch, "E14.11.14.12", {"start": v(189.72, 26.99) * mm, "end": v(184.22, 26.99) * mm});
            skLineSegment(sketch, "E14.14.14.12", {"start": v(184.22, 26.99) * mm, "end": v(181.47, 31.75) * mm});
            skLineSegment(sketch, "E14.17.14.12", {"start": v(181.47, 31.75) * mm, "end": v(184.22, 36.51) * mm});
            skLineSegment(sketch, "E14.0.14.13", {"start": v(184.22, 49.21) * mm, "end": v(189.72, 49.21) * mm});
            skLineSegment(sketch, "E14.3.14.13", {"start": v(189.72, 49.21) * mm, "end": v(192.47, 44.45) * mm});
            skLineSegment(sketch, "E14.6.14.13", {"start": v(192.47, 44.45) * mm, "end": v(189.72, 39.69) * mm});
            skCircle(sketch, "E14.9.14.13", {"center": v(186.97, 44.45) * mm, "radius": 4.76 * mm, "construction": true});
            skLineSegment(sketch, "E14.11.14.13", {"start": v(189.72, 39.69) * mm, "end": v(184.22, 39.69) * mm});
            skLineSegment(sketch, "E14.14.14.13", {"start": v(184.22, 39.69) * mm, "end": v(181.47, 44.45) * mm});
            skLineSegment(sketch, "E14.17.14.13", {"start": v(181.47, 44.45) * mm, "end": v(184.22, 49.21) * mm});
            skLineSegment(sketch, "E14.0.14.14", {"start": v(184.22, 61.91) * mm, "end": v(189.72, 61.91) * mm});
            skLineSegment(sketch, "E14.3.14.14", {"start": v(189.72, 61.91) * mm, "end": v(192.47, 57.15) * mm});
            skLineSegment(sketch, "E14.6.14.14", {"start": v(192.47, 57.15) * mm, "end": v(189.72, 52.39) * mm});
            skCircle(sketch, "E14.9.14.14", {"center": v(186.97, 57.15) * mm, "radius": 4.76 * mm, "construction": true});
            skLineSegment(sketch, "E14.11.14.14", {"start": v(189.72, 52.39) * mm, "end": v(184.22, 52.39) * mm});
            skLineSegment(sketch, "E14.14.14.14", {"start": v(184.22, 52.39) * mm, "end": v(181.47, 57.15) * mm});
            skLineSegment(sketch, "E14.17.14.14", {"start": v(181.47, 57.15) * mm, "end": v(184.22, 61.91) * mm});
            skLineSegment(sketch, "E14.0.14.15", {"start": v(184.22, 74.61) * mm, "end": v(189.72, 74.61) * mm});
            skLineSegment(sketch, "E14.3.14.15", {"start": v(189.72, 74.61) * mm, "end": v(192.47, 69.85) * mm});
            skLineSegment(sketch, "E14.6.14.15", {"start": v(192.47, 69.85) * mm, "end": v(189.72, 65.09) * mm});
            skCircle(sketch, "E14.9.14.15", {"center": v(186.97, 69.85) * mm, "radius": 4.76 * mm, "construction": true});
            skLineSegment(sketch, "E14.11.14.15", {"start": v(189.72, 65.09) * mm, "end": v(184.22, 65.09) * mm});
            skLineSegment(sketch, "E14.14.14.15", {"start": v(184.22, 65.09) * mm, "end": v(181.47, 69.85) * mm});
            skLineSegment(sketch, "E14.17.14.15", {"start": v(181.47, 69.85) * mm, "end": v(184.22, 74.61) * mm});
            skLineSegment(sketch, "E14.0.14.16", {"start": v(184.22, 87.31) * mm, "end": v(189.72, 87.31) * mm});
            skLineSegment(sketch, "E14.3.14.16", {"start": v(189.72, 87.31) * mm, "end": v(192.47, 82.55) * mm});
            skLineSegment(sketch, "E14.6.14.16", {"start": v(192.47, 82.55) * mm, "end": v(189.72, 77.79) * mm});
            skCircle(sketch, "E14.9.14.16", {"center": v(186.97, 82.55) * mm, "radius": 4.76 * mm, "construction": true});
            skLineSegment(sketch, "E14.11.14.16", {"start": v(189.72, 77.79) * mm, "end": v(184.22, 77.79) * mm});
            skLineSegment(sketch, "E14.14.14.16", {"start": v(184.22, 77.79) * mm, "end": v(181.47, 82.55) * mm});
            skLineSegment(sketch, "E14.17.14.16", {"start": v(181.47, 82.55) * mm, "end": v(184.22, 87.31) * mm});
            skLineSegment(sketch, "E14.0.14.17", {"start": v(184.22, 100.01) * mm, "end": v(189.72, 100.01) * mm});
            skLineSegment(sketch, "E14.3.14.17", {"start": v(189.72, 100.01) * mm, "end": v(192.47, 95.25) * mm});
            skLineSegment(sketch, "E14.6.14.17", {"start": v(192.47, 95.25) * mm, "end": v(189.72, 90.49) * mm});
            skCircle(sketch, "E14.9.14.17", {"center": v(186.97, 95.25) * mm, "radius": 4.76 * mm, "construction": true});
            skLineSegment(sketch, "E14.11.14.17", {"start": v(189.72, 90.49) * mm, "end": v(184.22, 90.49) * mm});
            skLineSegment(sketch, "E14.14.14.17", {"start": v(184.22, 90.49) * mm, "end": v(181.47, 95.25) * mm});
            skLineSegment(sketch, "E14.17.14.17", {"start": v(181.47, 95.25) * mm, "end": v(184.22, 100.01) * mm});
            skLineSegment(sketch, "E14.0.14.18", {"start": v(184.22, 112.71) * mm, "end": v(189.72, 112.71) * mm});
            skLineSegment(sketch, "E14.3.14.18", {"start": v(189.72, 112.71) * mm, "end": v(192.47, 107.95) * mm});
            skLineSegment(sketch, "E14.6.14.18", {"start": v(192.47, 107.95) * mm, "end": v(189.72, 103.19) * mm});
            skCircle(sketch, "E14.9.14.18", {"center": v(186.97, 107.95) * mm, "radius": 4.76 * mm, "construction": true});
            skLineSegment(sketch, "E14.11.14.18", {"start": v(189.72, 103.19) * mm, "end": v(184.22, 103.19) * mm});
            skLineSegment(sketch, "E14.14.14.18", {"start": v(184.22, 103.19) * mm, "end": v(181.47, 107.95) * mm});
            skLineSegment(sketch, "E14.17.14.18", {"start": v(181.47, 107.95) * mm, "end": v(184.22, 112.71) * mm});
            skLineSegment(sketch, "E14.0.14.19", {"start": v(184.22, 125.41) * mm, "end": v(189.72, 125.41) * mm});
            skLineSegment(sketch, "E14.3.14.19", {"start": v(189.72, 125.41) * mm, "end": v(192.47, 120.65) * mm});
            skLineSegment(sketch, "E14.6.14.19", {"start": v(192.47, 120.65) * mm, "end": v(189.72, 115.89) * mm});
            skCircle(sketch, "E14.9.14.19", {"center": v(186.97, 120.65) * mm, "radius": 4.76 * mm, "construction": true});
            skLineSegment(sketch, "E14.11.14.19", {"start": v(189.72, 115.89) * mm, "end": v(184.22, 115.89) * mm});
            skLineSegment(sketch, "E14.14.14.19", {"start": v(184.22, 115.89) * mm, "end": v(181.47, 120.65) * mm});
            skLineSegment(sketch, "E14.17.14.19", {"start": v(181.47, 120.65) * mm, "end": v(184.22, 125.41) * mm});
            skLineSegment(sketch, "E14.0.15.0", {"start": v(206.22, -115.89) * mm, "end": v(211.72, -115.89) * mm});
            skLineSegment(sketch, "E14.3.15.0", {"start": v(211.72, -115.89) * mm, "end": v(214.46, -120.65) * mm});
            skLineSegment(sketch, "E14.6.15.0", {"start": v(214.46, -120.65) * mm, "end": v(211.72, -125.41) * mm});
            skCircle(sketch, "E14.9.15.0", {"center": v(208.97, -120.65) * mm, "radius": 4.76 * mm, "construction": true});
            skLineSegment(sketch, "E14.11.15.0", {"start": v(211.72, -125.41) * mm, "end": v(206.22, -125.41) * mm});
            skLineSegment(sketch, "E14.14.15.0", {"start": v(206.22, -125.41) * mm, "end": v(203.47, -120.65) * mm});
            skLineSegment(sketch, "E14.17.15.0", {"start": v(203.47, -120.65) * mm, "end": v(206.22, -115.89) * mm});
            skLineSegment(sketch, "E14.0.15.1", {"start": v(206.22, -103.19) * mm, "end": v(211.72, -103.19) * mm});
            skLineSegment(sketch, "E14.3.15.1", {"start": v(211.72, -103.19) * mm, "end": v(214.46, -107.95) * mm});
            skLineSegment(sketch, "E14.6.15.1", {"start": v(214.46, -107.95) * mm, "end": v(211.72, -112.71) * mm});
            skCircle(sketch, "E14.9.15.1", {"center": v(208.97, -107.95) * mm, "radius": 4.76 * mm, "construction": true});
            skLineSegment(sketch, "E14.11.15.1", {"start": v(211.72, -112.71) * mm, "end": v(206.22, -112.71) * mm});
            skLineSegment(sketch, "E14.14.15.1", {"start": v(206.22, -112.71) * mm, "end": v(203.47, -107.95) * mm});
            skLineSegment(sketch, "E14.17.15.1", {"start": v(203.47, -107.95) * mm, "end": v(206.22, -103.19) * mm});
            skLineSegment(sketch, "E14.0.15.2", {"start": v(206.22, -90.49) * mm, "end": v(211.72, -90.49) * mm});
            skLineSegment(sketch, "E14.3.15.2", {"start": v(211.72, -90.49) * mm, "end": v(214.46, -95.25) * mm});
            skLineSegment(sketch, "E14.6.15.2", {"start": v(214.46, -95.25) * mm, "end": v(211.72, -100.01) * mm});
            skCircle(sketch, "E14.9.15.2", {"center": v(208.97, -95.25) * mm, "radius": 4.76 * mm, "construction": true});
            skLineSegment(sketch, "E14.11.15.2", {"start": v(211.72, -100.01) * mm, "end": v(206.22, -100.01) * mm});
            skLineSegment(sketch, "E14.14.15.2", {"start": v(206.22, -100.01) * mm, "end": v(203.47, -95.25) * mm});
            skLineSegment(sketch, "E14.17.15.2", {"start": v(203.47, -95.25) * mm, "end": v(206.22, -90.49) * mm});
            skLineSegment(sketch, "E14.0.15.3", {"start": v(206.22, -77.79) * mm, "end": v(211.72, -77.79) * mm});
            skLineSegment(sketch, "E14.3.15.3", {"start": v(211.72, -77.79) * mm, "end": v(214.46, -82.55) * mm});
            skLineSegment(sketch, "E14.6.15.3", {"start": v(214.46, -82.55) * mm, "end": v(211.72, -87.31) * mm});
            skCircle(sketch, "E14.9.15.3", {"center": v(208.97, -82.55) * mm, "radius": 4.76 * mm, "construction": true});
            skLineSegment(sketch, "E14.11.15.3", {"start": v(211.72, -87.31) * mm, "end": v(206.22, -87.31) * mm});
            skLineSegment(sketch, "E14.14.15.3", {"start": v(206.22, -87.31) * mm, "end": v(203.47, -82.55) * mm});
            skLineSegment(sketch, "E14.17.15.3", {"start": v(203.47, -82.55) * mm, "end": v(206.22, -77.79) * mm});
            skLineSegment(sketch, "E14.0.15.4", {"start": v(206.22, -65.09) * mm, "end": v(211.72, -65.09) * mm});
            skLineSegment(sketch, "E14.3.15.4", {"start": v(211.72, -65.09) * mm, "end": v(214.46, -69.85) * mm});
            skLineSegment(sketch, "E14.6.15.4", {"start": v(214.46, -69.85) * mm, "end": v(211.72, -74.61) * mm});
            skCircle(sketch, "E14.9.15.4", {"center": v(208.97, -69.85) * mm, "radius": 4.76 * mm, "construction": true});
            skLineSegment(sketch, "E14.11.15.4", {"start": v(211.72, -74.61) * mm, "end": v(206.22, -74.61) * mm});
            skLineSegment(sketch, "E14.14.15.4", {"start": v(206.22, -74.61) * mm, "end": v(203.47, -69.85) * mm});
            skLineSegment(sketch, "E14.17.15.4", {"start": v(203.47, -69.85) * mm, "end": v(206.22, -65.09) * mm});
            skLineSegment(sketch, "E14.0.15.5", {"start": v(206.22, -52.39) * mm, "end": v(211.72, -52.39) * mm});
            skLineSegment(sketch, "E14.3.15.5", {"start": v(211.72, -52.39) * mm, "end": v(214.46, -57.15) * mm});
            skLineSegment(sketch, "E14.6.15.5", {"start": v(214.46, -57.15) * mm, "end": v(211.72, -61.91) * mm});
            skCircle(sketch, "E14.9.15.5", {"center": v(208.97, -57.15) * mm, "radius": 4.76 * mm, "construction": true});
            skLineSegment(sketch, "E14.11.15.5", {"start": v(211.72, -61.91) * mm, "end": v(206.22, -61.91) * mm});
            skLineSegment(sketch, "E14.14.15.5", {"start": v(206.22, -61.91) * mm, "end": v(203.47, -57.15) * mm});
            skLineSegment(sketch, "E14.17.15.5", {"start": v(203.47, -57.15) * mm, "end": v(206.22, -52.39) * mm});
            skLineSegment(sketch, "E14.0.15.6", {"start": v(206.22, -39.69) * mm, "end": v(211.72, -39.69) * mm});
            skLineSegment(sketch, "E14.3.15.6", {"start": v(211.72, -39.69) * mm, "end": v(214.46, -44.45) * mm});
            skLineSegment(sketch, "E14.6.15.6", {"start": v(214.46, -44.45) * mm, "end": v(211.72, -49.21) * mm});
            skCircle(sketch, "E14.9.15.6", {"center": v(208.97, -44.45) * mm, "radius": 4.76 * mm, "construction": true});
            skLineSegment(sketch, "E14.11.15.6", {"start": v(211.72, -49.21) * mm, "end": v(206.22, -49.21) * mm});
            skLineSegment(sketch, "E14.14.15.6", {"start": v(206.22, -49.21) * mm, "end": v(203.47, -44.45) * mm});
            skLineSegment(sketch, "E14.17.15.6", {"start": v(203.47, -44.45) * mm, "end": v(206.22, -39.69) * mm});
            skLineSegment(sketch, "E14.0.15.7", {"start": v(206.22, -26.99) * mm, "end": v(211.72, -26.99) * mm});
            skLineSegment(sketch, "E14.3.15.7", {"start": v(211.72, -26.99) * mm, "end": v(214.46, -31.75) * mm});
            skLineSegment(sketch, "E14.6.15.7", {"start": v(214.46, -31.75) * mm, "end": v(211.72, -36.51) * mm});
            skCircle(sketch, "E14.9.15.7", {"center": v(208.97, -31.75) * mm, "radius": 4.76 * mm, "construction": true});
            skLineSegment(sketch, "E14.11.15.7", {"start": v(211.72, -36.51) * mm, "end": v(206.22, -36.51) * mm});
            skLineSegment(sketch, "E14.14.15.7", {"start": v(206.22, -36.51) * mm, "end": v(203.47, -31.75) * mm});
            skLineSegment(sketch, "E14.17.15.7", {"start": v(203.47, -31.75) * mm, "end": v(206.22, -26.99) * mm});
            skLineSegment(sketch, "E14.0.15.8", {"start": v(206.22, -14.29) * mm, "end": v(211.72, -14.29) * mm});
            skLineSegment(sketch, "E14.3.15.8", {"start": v(211.72, -14.29) * mm, "end": v(214.46, -19.05) * mm});
            skLineSegment(sketch, "E14.6.15.8", {"start": v(214.46, -19.05) * mm, "end": v(211.72, -23.81) * mm});
            skCircle(sketch, "E14.9.15.8", {"center": v(208.97, -19.05) * mm, "radius": 4.76 * mm, "construction": true});
            skLineSegment(sketch, "E14.11.15.8", {"start": v(211.72, -23.81) * mm, "end": v(206.22, -23.81) * mm});
            skLineSegment(sketch, "E14.14.15.8", {"start": v(206.22, -23.81) * mm, "end": v(203.47, -19.05) * mm});
            skLineSegment(sketch, "E14.17.15.8", {"start": v(203.47, -19.05) * mm, "end": v(206.22, -14.29) * mm});
            skLineSegment(sketch, "E14.0.15.9", {"start": v(206.22, -1.59) * mm, "end": v(211.72, -1.59) * mm});
            skLineSegment(sketch, "E14.3.15.9", {"start": v(211.72, -1.59) * mm, "end": v(214.46, -6.35) * mm});
            skLineSegment(sketch, "E14.6.15.9", {"start": v(214.46, -6.35) * mm, "end": v(211.72, -11.11) * mm});
            skCircle(sketch, "E14.9.15.9", {"center": v(208.97, -6.35) * mm, "radius": 4.76 * mm, "construction": true});
            skLineSegment(sketch, "E14.11.15.9", {"start": v(211.72, -11.11) * mm, "end": v(206.22, -11.11) * mm});
            skLineSegment(sketch, "E14.14.15.9", {"start": v(206.22, -11.11) * mm, "end": v(203.47, -6.35) * mm});
            skLineSegment(sketch, "E14.17.15.9", {"start": v(203.47, -6.35) * mm, "end": v(206.22, -1.59) * mm});
            skLineSegment(sketch, "E14.0.15.10", {"start": v(206.22, 11.11) * mm, "end": v(211.72, 11.11) * mm});
            skLineSegment(sketch, "E14.3.15.10", {"start": v(211.72, 11.11) * mm, "end": v(214.46, 6.35) * mm});
            skLineSegment(sketch, "E14.6.15.10", {"start": v(214.46, 6.35) * mm, "end": v(211.72, 1.59) * mm});
            skCircle(sketch, "E14.9.15.10", {"center": v(208.97, 6.35) * mm, "radius": 4.76 * mm, "construction": true});
            skLineSegment(sketch, "E14.11.15.10", {"start": v(211.72, 1.59) * mm, "end": v(206.22, 1.59) * mm});
            skLineSegment(sketch, "E14.14.15.10", {"start": v(206.22, 1.59) * mm, "end": v(203.47, 6.35) * mm});
            skLineSegment(sketch, "E14.17.15.10", {"start": v(203.47, 6.35) * mm, "end": v(206.22, 11.11) * mm});
            skLineSegment(sketch, "E14.0.15.11", {"start": v(206.22, 23.81) * mm, "end": v(211.72, 23.81) * mm});
            skLineSegment(sketch, "E14.3.15.11", {"start": v(211.72, 23.81) * mm, "end": v(214.46, 19.05) * mm});
            skLineSegment(sketch, "E14.6.15.11", {"start": v(214.46, 19.05) * mm, "end": v(211.72, 14.29) * mm});
            skCircle(sketch, "E14.9.15.11", {"center": v(208.97, 19.05) * mm, "radius": 4.76 * mm, "construction": true});
            skLineSegment(sketch, "E14.11.15.11", {"start": v(211.72, 14.29) * mm, "end": v(206.22, 14.29) * mm});
            skLineSegment(sketch, "E14.14.15.11", {"start": v(206.22, 14.29) * mm, "end": v(203.47, 19.05) * mm});
            skLineSegment(sketch, "E14.17.15.11", {"start": v(203.47, 19.05) * mm, "end": v(206.22, 23.81) * mm});
            skLineSegment(sketch, "E14.0.15.12", {"start": v(206.22, 36.51) * mm, "end": v(211.72, 36.51) * mm});
            skLineSegment(sketch, "E14.3.15.12", {"start": v(211.72, 36.51) * mm, "end": v(214.46, 31.75) * mm});
            skLineSegment(sketch, "E14.6.15.12", {"start": v(214.46, 31.75) * mm, "end": v(211.72, 26.99) * mm});
            skCircle(sketch, "E14.9.15.12", {"center": v(208.97, 31.75) * mm, "radius": 4.76 * mm, "construction": true});
            skLineSegment(sketch, "E14.11.15.12", {"start": v(211.72, 26.99) * mm, "end": v(206.22, 26.99) * mm});
            skLineSegment(sketch, "E14.14.15.12", {"start": v(206.22, 26.99) * mm, "end": v(203.47, 31.75) * mm});
            skLineSegment(sketch, "E14.17.15.12", {"start": v(203.47, 31.75) * mm, "end": v(206.22, 36.51) * mm});
            skLineSegment(sketch, "E14.0.15.13", {"start": v(206.22, 49.21) * mm, "end": v(211.72, 49.21) * mm});
            skLineSegment(sketch, "E14.3.15.13", {"start": v(211.72, 49.21) * mm, "end": v(214.46, 44.45) * mm});
            skLineSegment(sketch, "E14.6.15.13", {"start": v(214.46, 44.45) * mm, "end": v(211.72, 39.69) * mm});
            skCircle(sketch, "E14.9.15.13", {"center": v(208.97, 44.45) * mm, "radius": 4.76 * mm, "construction": true});
            skLineSegment(sketch, "E14.11.15.13", {"start": v(211.72, 39.69) * mm, "end": v(206.22, 39.69) * mm});
            skLineSegment(sketch, "E14.14.15.13", {"start": v(206.22, 39.69) * mm, "end": v(203.47, 44.45) * mm});
            skLineSegment(sketch, "E14.17.15.13", {"start": v(203.47, 44.45) * mm, "end": v(206.22, 49.21) * mm});
            skLineSegment(sketch, "E14.0.15.14", {"start": v(206.22, 61.91) * mm, "end": v(211.72, 61.91) * mm});
            skLineSegment(sketch, "E14.3.15.14", {"start": v(211.72, 61.91) * mm, "end": v(214.46, 57.15) * mm});
            skLineSegment(sketch, "E14.6.15.14", {"start": v(214.46, 57.15) * mm, "end": v(211.72, 52.39) * mm});
            skCircle(sketch, "E14.9.15.14", {"center": v(208.97, 57.15) * mm, "radius": 4.76 * mm, "construction": true});
            skLineSegment(sketch, "E14.11.15.14", {"start": v(211.72, 52.39) * mm, "end": v(206.22, 52.39) * mm});
            skLineSegment(sketch, "E14.14.15.14", {"start": v(206.22, 52.39) * mm, "end": v(203.47, 57.15) * mm});
            skLineSegment(sketch, "E14.17.15.14", {"start": v(203.47, 57.15) * mm, "end": v(206.22, 61.91) * mm});
            skLineSegment(sketch, "E14.0.15.15", {"start": v(206.22, 74.61) * mm, "end": v(211.72, 74.61) * mm});
            skLineSegment(sketch, "E14.3.15.15", {"start": v(211.72, 74.61) * mm, "end": v(214.46, 69.85) * mm});
            skLineSegment(sketch, "E14.6.15.15", {"start": v(214.46, 69.85) * mm, "end": v(211.72, 65.09) * mm});
            skCircle(sketch, "E14.9.15.15", {"center": v(208.97, 69.85) * mm, "radius": 4.76 * mm, "construction": true});
            skLineSegment(sketch, "E14.11.15.15", {"start": v(211.72, 65.09) * mm, "end": v(206.22, 65.09) * mm});
            skLineSegment(sketch, "E14.14.15.15", {"start": v(206.22, 65.09) * mm, "end": v(203.47, 69.85) * mm});
            skLineSegment(sketch, "E14.17.15.15", {"start": v(203.47, 69.85) * mm, "end": v(206.22, 74.61) * mm});
            skLineSegment(sketch, "E14.0.15.16", {"start": v(206.22, 87.31) * mm, "end": v(211.72, 87.31) * mm});
            skLineSegment(sketch, "E14.3.15.16", {"start": v(211.72, 87.31) * mm, "end": v(214.46, 82.55) * mm});
            skLineSegment(sketch, "E14.6.15.16", {"start": v(214.46, 82.55) * mm, "end": v(211.72, 77.79) * mm});
            skCircle(sketch, "E14.9.15.16", {"center": v(208.97, 82.55) * mm, "radius": 4.76 * mm, "construction": true});
            skLineSegment(sketch, "E14.11.15.16", {"start": v(211.72, 77.79) * mm, "end": v(206.22, 77.79) * mm});
            skLineSegment(sketch, "E14.14.15.16", {"start": v(206.22, 77.79) * mm, "end": v(203.47, 82.55) * mm});
            skLineSegment(sketch, "E14.17.15.16", {"start": v(203.47, 82.55) * mm, "end": v(206.22, 87.31) * mm});
            skLineSegment(sketch, "E14.0.15.17", {"start": v(206.22, 100.01) * mm, "end": v(211.72, 100.01) * mm});
            skLineSegment(sketch, "E14.3.15.17", {"start": v(211.72, 100.01) * mm, "end": v(214.46, 95.25) * mm});
            skLineSegment(sketch, "E14.6.15.17", {"start": v(214.46, 95.25) * mm, "end": v(211.72, 90.49) * mm});
            skCircle(sketch, "E14.9.15.17", {"center": v(208.97, 95.25) * mm, "radius": 4.76 * mm, "construction": true});
            skLineSegment(sketch, "E14.11.15.17", {"start": v(211.72, 90.49) * mm, "end": v(206.22, 90.49) * mm});
            skLineSegment(sketch, "E14.14.15.17", {"start": v(206.22, 90.49) * mm, "end": v(203.47, 95.25) * mm});
            skLineSegment(sketch, "E14.17.15.17", {"start": v(203.47, 95.25) * mm, "end": v(206.22, 100.01) * mm});
            skLineSegment(sketch, "E14.0.15.18", {"start": v(206.22, 112.71) * mm, "end": v(211.72, 112.71) * mm});
            skLineSegment(sketch, "E14.3.15.18", {"start": v(211.72, 112.71) * mm, "end": v(214.46, 107.95) * mm});
            skLineSegment(sketch, "E14.6.15.18", {"start": v(214.46, 107.95) * mm, "end": v(211.72, 103.19) * mm});
            skCircle(sketch, "E14.9.15.18", {"center": v(208.97, 107.95) * mm, "radius": 4.76 * mm, "construction": true});
            skLineSegment(sketch, "E14.11.15.18", {"start": v(211.72, 103.19) * mm, "end": v(206.22, 103.19) * mm});
            skLineSegment(sketch, "E14.14.15.18", {"start": v(206.22, 103.19) * mm, "end": v(203.47, 107.95) * mm});
            skLineSegment(sketch, "E14.17.15.18", {"start": v(203.47, 107.95) * mm, "end": v(206.22, 112.71) * mm});
            skLineSegment(sketch, "E14.0.15.19", {"start": v(206.22, 125.41) * mm, "end": v(211.72, 125.41) * mm});
            skLineSegment(sketch, "E14.3.15.19", {"start": v(211.72, 125.41) * mm, "end": v(214.46, 120.65) * mm});
            skLineSegment(sketch, "E14.6.15.19", {"start": v(214.46, 120.65) * mm, "end": v(211.72, 115.89) * mm});
            skCircle(sketch, "E14.9.15.19", {"center": v(208.97, 120.65) * mm, "radius": 4.76 * mm, "construction": true});
            skLineSegment(sketch, "E14.11.15.19", {"start": v(211.72, 115.89) * mm, "end": v(206.22, 115.89) * mm});
            skLineSegment(sketch, "E14.14.15.19", {"start": v(206.22, 115.89) * mm, "end": v(203.47, 120.65) * mm});
            skLineSegment(sketch, "E14.17.15.19", {"start": v(203.47, 120.65) * mm, "end": v(206.22, 125.41) * mm});
            skLineSegment(sketch, "E14.0.16.0", {"start": v(228.21, -115.89) * mm, "end": v(233.71, -115.89) * mm});
            skLineSegment(sketch, "E14.3.16.0", {"start": v(233.71, -115.89) * mm, "end": v(236.46, -120.65) * mm});
            skLineSegment(sketch, "E14.6.16.0", {"start": v(236.46, -120.65) * mm, "end": v(233.71, -125.41) * mm});
            skCircle(sketch, "E14.9.16.0", {"center": v(230.96, -120.65) * mm, "radius": 4.76 * mm, "construction": true});
            skLineSegment(sketch, "E14.11.16.0", {"start": v(233.71, -125.41) * mm, "end": v(228.21, -125.41) * mm});
            skLineSegment(sketch, "E14.14.16.0", {"start": v(228.21, -125.41) * mm, "end": v(225.46, -120.65) * mm});
            skLineSegment(sketch, "E14.17.16.0", {"start": v(225.46, -120.65) * mm, "end": v(228.21, -115.89) * mm});
            skLineSegment(sketch, "E14.0.16.1", {"start": v(228.21, -103.19) * mm, "end": v(233.71, -103.19) * mm});
            skLineSegment(sketch, "E14.3.16.1", {"start": v(233.71, -103.19) * mm, "end": v(236.46, -107.95) * mm});
            skLineSegment(sketch, "E14.6.16.1", {"start": v(236.46, -107.95) * mm, "end": v(233.71, -112.71) * mm});
            skCircle(sketch, "E14.9.16.1", {"center": v(230.96, -107.95) * mm, "radius": 4.76 * mm, "construction": true});
            skLineSegment(sketch, "E14.11.16.1", {"start": v(233.71, -112.71) * mm, "end": v(228.21, -112.71) * mm});
            skLineSegment(sketch, "E14.14.16.1", {"start": v(228.21, -112.71) * mm, "end": v(225.46, -107.95) * mm});
            skLineSegment(sketch, "E14.17.16.1", {"start": v(225.46, -107.95) * mm, "end": v(228.21, -103.19) * mm});
            skLineSegment(sketch, "E14.0.16.2", {"start": v(228.21, -90.49) * mm, "end": v(233.71, -90.49) * mm});
            skLineSegment(sketch, "E14.3.16.2", {"start": v(233.71, -90.49) * mm, "end": v(236.46, -95.25) * mm});
            skLineSegment(sketch, "E14.6.16.2", {"start": v(236.46, -95.25) * mm, "end": v(233.71, -100.01) * mm});
            skCircle(sketch, "E14.9.16.2", {"center": v(230.96, -95.25) * mm, "radius": 4.76 * mm, "construction": true});
            skLineSegment(sketch, "E14.11.16.2", {"start": v(233.71, -100.01) * mm, "end": v(228.21, -100.01) * mm});
            skLineSegment(sketch, "E14.14.16.2", {"start": v(228.21, -100.01) * mm, "end": v(225.46, -95.25) * mm});
            skLineSegment(sketch, "E14.17.16.2", {"start": v(225.46, -95.25) * mm, "end": v(228.21, -90.49) * mm});
            skLineSegment(sketch, "E14.0.16.3", {"start": v(228.21, -77.79) * mm, "end": v(233.71, -77.79) * mm});
            skLineSegment(sketch, "E14.3.16.3", {"start": v(233.71, -77.79) * mm, "end": v(236.46, -82.55) * mm});
            skLineSegment(sketch, "E14.6.16.3", {"start": v(236.46, -82.55) * mm, "end": v(233.71, -87.31) * mm});
            skCircle(sketch, "E14.9.16.3", {"center": v(230.96, -82.55) * mm, "radius": 4.76 * mm, "construction": true});
            skLineSegment(sketch, "E14.11.16.3", {"start": v(233.71, -87.31) * mm, "end": v(228.21, -87.31) * mm});
            skLineSegment(sketch, "E14.14.16.3", {"start": v(228.21, -87.31) * mm, "end": v(225.46, -82.55) * mm});
            skLineSegment(sketch, "E14.17.16.3", {"start": v(225.46, -82.55) * mm, "end": v(228.21, -77.79) * mm});
            skLineSegment(sketch, "E14.0.16.4", {"start": v(228.21, -65.09) * mm, "end": v(233.71, -65.09) * mm});
            skLineSegment(sketch, "E14.3.16.4", {"start": v(233.71, -65.09) * mm, "end": v(236.46, -69.85) * mm});
            skLineSegment(sketch, "E14.6.16.4", {"start": v(236.46, -69.85) * mm, "end": v(233.71, -74.61) * mm});
            skCircle(sketch, "E14.9.16.4", {"center": v(230.96, -69.85) * mm, "radius": 4.76 * mm, "construction": true});
            skLineSegment(sketch, "E14.11.16.4", {"start": v(233.71, -74.61) * mm, "end": v(228.21, -74.61) * mm});
            skLineSegment(sketch, "E14.14.16.4", {"start": v(228.21, -74.61) * mm, "end": v(225.46, -69.85) * mm});
            skLineSegment(sketch, "E14.17.16.4", {"start": v(225.46, -69.85) * mm, "end": v(228.21, -65.09) * mm});
            skLineSegment(sketch, "E14.0.16.5", {"start": v(228.21, -52.39) * mm, "end": v(233.71, -52.39) * mm});
            skLineSegment(sketch, "E14.3.16.5", {"start": v(233.71, -52.39) * mm, "end": v(236.46, -57.15) * mm});
            skLineSegment(sketch, "E14.6.16.5", {"start": v(236.46, -57.15) * mm, "end": v(233.71, -61.91) * mm});
            skCircle(sketch, "E14.9.16.5", {"center": v(230.96, -57.15) * mm, "radius": 4.76 * mm, "construction": true});
            skLineSegment(sketch, "E14.11.16.5", {"start": v(233.71, -61.91) * mm, "end": v(228.21, -61.91) * mm});
            skLineSegment(sketch, "E14.14.16.5", {"start": v(228.21, -61.91) * mm, "end": v(225.46, -57.15) * mm});
            skLineSegment(sketch, "E14.17.16.5", {"start": v(225.46, -57.15) * mm, "end": v(228.21, -52.39) * mm});
            skLineSegment(sketch, "E14.0.16.6", {"start": v(228.21, -39.69) * mm, "end": v(233.71, -39.69) * mm});
            skLineSegment(sketch, "E14.3.16.6", {"start": v(233.71, -39.69) * mm, "end": v(236.46, -44.45) * mm});
            skLineSegment(sketch, "E14.6.16.6", {"start": v(236.46, -44.45) * mm, "end": v(233.71, -49.21) * mm});
            skCircle(sketch, "E14.9.16.6", {"center": v(230.96, -44.45) * mm, "radius": 4.76 * mm, "construction": true});
            skLineSegment(sketch, "E14.11.16.6", {"start": v(233.71, -49.21) * mm, "end": v(228.21, -49.21) * mm});
            skLineSegment(sketch, "E14.14.16.6", {"start": v(228.21, -49.21) * mm, "end": v(225.46, -44.45) * mm});
            skLineSegment(sketch, "E14.17.16.6", {"start": v(225.46, -44.45) * mm, "end": v(228.21, -39.69) * mm});
            skLineSegment(sketch, "E14.0.16.7", {"start": v(228.21, -26.99) * mm, "end": v(233.71, -26.99) * mm});
            skLineSegment(sketch, "E14.3.16.7", {"start": v(233.71, -26.99) * mm, "end": v(236.46, -31.75) * mm});
            skLineSegment(sketch, "E14.6.16.7", {"start": v(236.46, -31.75) * mm, "end": v(233.71, -36.51) * mm});
            skCircle(sketch, "E14.9.16.7", {"center": v(230.96, -31.75) * mm, "radius": 4.76 * mm, "construction": true});
            skLineSegment(sketch, "E14.11.16.7", {"start": v(233.71, -36.51) * mm, "end": v(228.21, -36.51) * mm});
            skLineSegment(sketch, "E14.14.16.7", {"start": v(228.21, -36.51) * mm, "end": v(225.46, -31.75) * mm});
            skLineSegment(sketch, "E14.17.16.7", {"start": v(225.46, -31.75) * mm, "end": v(228.21, -26.99) * mm});
            skLineSegment(sketch, "E14.0.16.8", {"start": v(228.21, -14.29) * mm, "end": v(233.71, -14.29) * mm});
            skLineSegment(sketch, "E14.3.16.8", {"start": v(233.71, -14.29) * mm, "end": v(236.46, -19.05) * mm});
            skLineSegment(sketch, "E14.6.16.8", {"start": v(236.46, -19.05) * mm, "end": v(233.71, -23.81) * mm});
            skCircle(sketch, "E14.9.16.8", {"center": v(230.96, -19.05) * mm, "radius": 4.76 * mm, "construction": true});
            skLineSegment(sketch, "E14.11.16.8", {"start": v(233.71, -23.81) * mm, "end": v(228.21, -23.81) * mm});
            skLineSegment(sketch, "E14.14.16.8", {"start": v(228.21, -23.81) * mm, "end": v(225.46, -19.05) * mm});
            skLineSegment(sketch, "E14.17.16.8", {"start": v(225.46, -19.05) * mm, "end": v(228.21, -14.29) * mm});
            skLineSegment(sketch, "E14.0.16.9", {"start": v(228.21, -1.59) * mm, "end": v(233.71, -1.59) * mm});
            skLineSegment(sketch, "E14.3.16.9", {"start": v(233.71, -1.59) * mm, "end": v(236.46, -6.35) * mm});
            skLineSegment(sketch, "E14.6.16.9", {"start": v(236.46, -6.35) * mm, "end": v(233.71, -11.11) * mm});
            skCircle(sketch, "E14.9.16.9", {"center": v(230.96, -6.35) * mm, "radius": 4.76 * mm, "construction": true});
            skLineSegment(sketch, "E14.11.16.9", {"start": v(233.71, -11.11) * mm, "end": v(228.21, -11.11) * mm});
            skLineSegment(sketch, "E14.14.16.9", {"start": v(228.21, -11.11) * mm, "end": v(225.46, -6.35) * mm});
            skLineSegment(sketch, "E14.17.16.9", {"start": v(225.46, -6.35) * mm, "end": v(228.21, -1.59) * mm});
            skLineSegment(sketch, "E14.0.16.10", {"start": v(228.21, 11.11) * mm, "end": v(233.71, 11.11) * mm});
            skLineSegment(sketch, "E14.3.16.10", {"start": v(233.71, 11.11) * mm, "end": v(236.46, 6.35) * mm});
            skLineSegment(sketch, "E14.6.16.10", {"start": v(236.46, 6.35) * mm, "end": v(233.71, 1.59) * mm});
            skCircle(sketch, "E14.9.16.10", {"center": v(230.96, 6.35) * mm, "radius": 4.76 * mm, "construction": true});
            skLineSegment(sketch, "E14.11.16.10", {"start": v(233.71, 1.59) * mm, "end": v(228.21, 1.59) * mm});
            skLineSegment(sketch, "E14.14.16.10", {"start": v(228.21, 1.59) * mm, "end": v(225.46, 6.35) * mm});
            skLineSegment(sketch, "E14.17.16.10", {"start": v(225.46, 6.35) * mm, "end": v(228.21, 11.11) * mm});
            skLineSegment(sketch, "E14.0.16.11", {"start": v(228.21, 23.81) * mm, "end": v(233.71, 23.81) * mm});
            skLineSegment(sketch, "E14.3.16.11", {"start": v(233.71, 23.81) * mm, "end": v(236.46, 19.05) * mm});
            skLineSegment(sketch, "E14.6.16.11", {"start": v(236.46, 19.05) * mm, "end": v(233.71, 14.29) * mm});
            skCircle(sketch, "E14.9.16.11", {"center": v(230.96, 19.05) * mm, "radius": 4.76 * mm, "construction": true});
            skLineSegment(sketch, "E14.11.16.11", {"start": v(233.71, 14.29) * mm, "end": v(228.21, 14.29) * mm});
            skLineSegment(sketch, "E14.14.16.11", {"start": v(228.21, 14.29) * mm, "end": v(225.46, 19.05) * mm});
            skLineSegment(sketch, "E14.17.16.11", {"start": v(225.46, 19.05) * mm, "end": v(228.21, 23.81) * mm});
            skLineSegment(sketch, "E14.0.16.12", {"start": v(228.21, 36.51) * mm, "end": v(233.71, 36.51) * mm});
            skLineSegment(sketch, "E14.3.16.12", {"start": v(233.71, 36.51) * mm, "end": v(236.46, 31.75) * mm});
            skLineSegment(sketch, "E14.6.16.12", {"start": v(236.46, 31.75) * mm, "end": v(233.71, 26.99) * mm});
            skCircle(sketch, "E14.9.16.12", {"center": v(230.96, 31.75) * mm, "radius": 4.76 * mm, "construction": true});
            skLineSegment(sketch, "E14.11.16.12", {"start": v(233.71, 26.99) * mm, "end": v(228.21, 26.99) * mm});
            skLineSegment(sketch, "E14.14.16.12", {"start": v(228.21, 26.99) * mm, "end": v(225.46, 31.75) * mm});
            skLineSegment(sketch, "E14.17.16.12", {"start": v(225.46, 31.75) * mm, "end": v(228.21, 36.51) * mm});
            skLineSegment(sketch, "E14.0.16.13", {"start": v(228.21, 49.21) * mm, "end": v(233.71, 49.21) * mm});
            skLineSegment(sketch, "E14.3.16.13", {"start": v(233.71, 49.21) * mm, "end": v(236.46, 44.45) * mm});
            skLineSegment(sketch, "E14.6.16.13", {"start": v(236.46, 44.45) * mm, "end": v(233.71, 39.69) * mm});
            skCircle(sketch, "E14.9.16.13", {"center": v(230.96, 44.45) * mm, "radius": 4.76 * mm, "construction": true});
            skLineSegment(sketch, "E14.11.16.13", {"start": v(233.71, 39.69) * mm, "end": v(228.21, 39.69) * mm});
            skLineSegment(sketch, "E14.14.16.13", {"start": v(228.21, 39.69) * mm, "end": v(225.46, 44.45) * mm});
            skLineSegment(sketch, "E14.17.16.13", {"start": v(225.46, 44.45) * mm, "end": v(228.21, 49.21) * mm});
            skLineSegment(sketch, "E14.0.16.14", {"start": v(228.21, 61.91) * mm, "end": v(233.71, 61.91) * mm});
            skLineSegment(sketch, "E14.3.16.14", {"start": v(233.71, 61.91) * mm, "end": v(236.46, 57.15) * mm});
            skLineSegment(sketch, "E14.6.16.14", {"start": v(236.46, 57.15) * mm, "end": v(233.71, 52.39) * mm});
            skCircle(sketch, "E14.9.16.14", {"center": v(230.96, 57.15) * mm, "radius": 4.76 * mm, "construction": true});
            skLineSegment(sketch, "E14.11.16.14", {"start": v(233.71, 52.39) * mm, "end": v(228.21, 52.39) * mm});
            skLineSegment(sketch, "E14.14.16.14", {"start": v(228.21, 52.39) * mm, "end": v(225.46, 57.15) * mm});
            skLineSegment(sketch, "E14.17.16.14", {"start": v(225.46, 57.15) * mm, "end": v(228.21, 61.91) * mm});
            skLineSegment(sketch, "E14.0.16.15", {"start": v(228.21, 74.61) * mm, "end": v(233.71, 74.61) * mm});
            skLineSegment(sketch, "E14.3.16.15", {"start": v(233.71, 74.61) * mm, "end": v(236.46, 69.85) * mm});
            skLineSegment(sketch, "E14.6.16.15", {"start": v(236.46, 69.85) * mm, "end": v(233.71, 65.09) * mm});
            skCircle(sketch, "E14.9.16.15", {"center": v(230.96, 69.85) * mm, "radius": 4.76 * mm, "construction": true});
            skLineSegment(sketch, "E14.11.16.15", {"start": v(233.71, 65.09) * mm, "end": v(228.21, 65.09) * mm});
            skLineSegment(sketch, "E14.14.16.15", {"start": v(228.21, 65.09) * mm, "end": v(225.46, 69.85) * mm});
            skLineSegment(sketch, "E14.17.16.15", {"start": v(225.46, 69.85) * mm, "end": v(228.21, 74.61) * mm});
            skLineSegment(sketch, "E14.0.16.16", {"start": v(228.21, 87.31) * mm, "end": v(233.71, 87.31) * mm});
            skLineSegment(sketch, "E14.3.16.16", {"start": v(233.71, 87.31) * mm, "end": v(236.46, 82.55) * mm});
            skLineSegment(sketch, "E14.6.16.16", {"start": v(236.46, 82.55) * mm, "end": v(233.71, 77.79) * mm});
            skCircle(sketch, "E14.9.16.16", {"center": v(230.96, 82.55) * mm, "radius": 4.76 * mm, "construction": true});
            skLineSegment(sketch, "E14.11.16.16", {"start": v(233.71, 77.79) * mm, "end": v(228.21, 77.79) * mm});
            skLineSegment(sketch, "E14.14.16.16", {"start": v(228.21, 77.79) * mm, "end": v(225.46, 82.55) * mm});
            skLineSegment(sketch, "E14.17.16.16", {"start": v(225.46, 82.55) * mm, "end": v(228.21, 87.31) * mm});
            skLineSegment(sketch, "E14.0.16.17", {"start": v(228.21, 100.01) * mm, "end": v(233.71, 100.01) * mm});
            skLineSegment(sketch, "E14.3.16.17", {"start": v(233.71, 100.01) * mm, "end": v(236.46, 95.25) * mm});
            skLineSegment(sketch, "E14.6.16.17", {"start": v(236.46, 95.25) * mm, "end": v(233.71, 90.49) * mm});
            skCircle(sketch, "E14.9.16.17", {"center": v(230.96, 95.25) * mm, "radius": 4.76 * mm, "construction": true});
            skLineSegment(sketch, "E14.11.16.17", {"start": v(233.71, 90.49) * mm, "end": v(228.21, 90.49) * mm});
            skLineSegment(sketch, "E14.14.16.17", {"start": v(228.21, 90.49) * mm, "end": v(225.46, 95.25) * mm});
            skLineSegment(sketch, "E14.17.16.17", {"start": v(225.46, 95.25) * mm, "end": v(228.21, 100.01) * mm});
            skLineSegment(sketch, "E14.0.16.18", {"start": v(228.21, 112.71) * mm, "end": v(233.71, 112.71) * mm});
            skLineSegment(sketch, "E14.3.16.18", {"start": v(233.71, 112.71) * mm, "end": v(236.46, 107.95) * mm});
            skLineSegment(sketch, "E14.6.16.18", {"start": v(236.46, 107.95) * mm, "end": v(233.71, 103.19) * mm});
            skCircle(sketch, "E14.9.16.18", {"center": v(230.96, 107.95) * mm, "radius": 4.76 * mm, "construction": true});
            skLineSegment(sketch, "E14.11.16.18", {"start": v(233.71, 103.19) * mm, "end": v(228.21, 103.19) * mm});
            skLineSegment(sketch, "E14.14.16.18", {"start": v(228.21, 103.19) * mm, "end": v(225.46, 107.95) * mm});
            skLineSegment(sketch, "E14.17.16.18", {"start": v(225.46, 107.95) * mm, "end": v(228.21, 112.71) * mm});
            skLineSegment(sketch, "E14.0.16.19", {"start": v(228.21, 125.41) * mm, "end": v(233.71, 125.41) * mm});
            skLineSegment(sketch, "E14.3.16.19", {"start": v(233.71, 125.41) * mm, "end": v(236.46, 120.65) * mm});
            skLineSegment(sketch, "E14.6.16.19", {"start": v(236.46, 120.65) * mm, "end": v(233.71, 115.89) * mm});
            skCircle(sketch, "E14.9.16.19", {"center": v(230.96, 120.65) * mm, "radius": 4.76 * mm, "construction": true});
            skLineSegment(sketch, "E14.11.16.19", {"start": v(233.71, 115.89) * mm, "end": v(228.21, 115.89) * mm});
            skLineSegment(sketch, "E14.14.16.19", {"start": v(228.21, 115.89) * mm, "end": v(225.46, 120.65) * mm});
            skLineSegment(sketch, "E14.17.16.19", {"start": v(225.46, 120.65) * mm, "end": v(228.21, 125.41) * mm});
            skLineSegment(sketch, "E14.0.17.0", {"start": v(250.2, -115.89) * mm, "end": v(255.7, -115.89) * mm});
            skLineSegment(sketch, "E14.3.17.0", {"start": v(255.7, -115.89) * mm, "end": v(258.46, -120.65) * mm});
            skLineSegment(sketch, "E14.6.17.0", {"start": v(258.46, -120.65) * mm, "end": v(255.7, -125.41) * mm});
            skCircle(sketch, "E14.9.17.0", {"center": v(252.96, -120.65) * mm, "radius": 4.76 * mm, "construction": true});
            skLineSegment(sketch, "E14.11.17.0", {"start": v(255.7, -125.41) * mm, "end": v(250.2, -125.41) * mm});
            skLineSegment(sketch, "E14.14.17.0", {"start": v(250.2, -125.41) * mm, "end": v(247.46, -120.65) * mm});
            skLineSegment(sketch, "E14.17.17.0", {"start": v(247.46, -120.65) * mm, "end": v(250.2, -115.89) * mm});
            skLineSegment(sketch, "E14.0.17.1", {"start": v(250.2, -103.19) * mm, "end": v(255.7, -103.19) * mm});
            skLineSegment(sketch, "E14.3.17.1", {"start": v(255.7, -103.19) * mm, "end": v(258.46, -107.95) * mm});
            skLineSegment(sketch, "E14.6.17.1", {"start": v(258.46, -107.95) * mm, "end": v(255.7, -112.71) * mm});
            skCircle(sketch, "E14.9.17.1", {"center": v(252.96, -107.95) * mm, "radius": 4.76 * mm, "construction": true});
            skLineSegment(sketch, "E14.11.17.1", {"start": v(255.7, -112.71) * mm, "end": v(250.2, -112.71) * mm});
            skLineSegment(sketch, "E14.14.17.1", {"start": v(250.2, -112.71) * mm, "end": v(247.46, -107.95) * mm});
            skLineSegment(sketch, "E14.17.17.1", {"start": v(247.46, -107.95) * mm, "end": v(250.2, -103.19) * mm});
            skLineSegment(sketch, "E14.0.17.2", {"start": v(250.2, -90.49) * mm, "end": v(255.7, -90.49) * mm});
            skLineSegment(sketch, "E14.3.17.2", {"start": v(255.7, -90.49) * mm, "end": v(258.46, -95.25) * mm});
            skLineSegment(sketch, "E14.6.17.2", {"start": v(258.46, -95.25) * mm, "end": v(255.7, -100.01) * mm});
            skCircle(sketch, "E14.9.17.2", {"center": v(252.96, -95.25) * mm, "radius": 4.76 * mm, "construction": true});
            skLineSegment(sketch, "E14.11.17.2", {"start": v(255.7, -100.01) * mm, "end": v(250.2, -100.01) * mm});
            skLineSegment(sketch, "E14.14.17.2", {"start": v(250.2, -100.01) * mm, "end": v(247.46, -95.25) * mm});
            skLineSegment(sketch, "E14.17.17.2", {"start": v(247.46, -95.25) * mm, "end": v(250.2, -90.49) * mm});
            skLineSegment(sketch, "E14.0.17.3", {"start": v(250.2, -77.79) * mm, "end": v(255.7, -77.79) * mm});
            skLineSegment(sketch, "E14.3.17.3", {"start": v(255.7, -77.79) * mm, "end": v(258.46, -82.55) * mm});
            skLineSegment(sketch, "E14.6.17.3", {"start": v(258.46, -82.55) * mm, "end": v(255.7, -87.31) * mm});
            skCircle(sketch, "E14.9.17.3", {"center": v(252.96, -82.55) * mm, "radius": 4.76 * mm, "construction": true});
            skLineSegment(sketch, "E14.11.17.3", {"start": v(255.7, -87.31) * mm, "end": v(250.2, -87.31) * mm});
            skLineSegment(sketch, "E14.14.17.3", {"start": v(250.2, -87.31) * mm, "end": v(247.46, -82.55) * mm});
            skLineSegment(sketch, "E14.17.17.3", {"start": v(247.46, -82.55) * mm, "end": v(250.2, -77.79) * mm});
            skLineSegment(sketch, "E14.0.17.4", {"start": v(250.2, -65.09) * mm, "end": v(255.7, -65.09) * mm});
            skLineSegment(sketch, "E14.3.17.4", {"start": v(255.7, -65.09) * mm, "end": v(258.46, -69.85) * mm});
            skLineSegment(sketch, "E14.6.17.4", {"start": v(258.46, -69.85) * mm, "end": v(255.7, -74.61) * mm});
            skCircle(sketch, "E14.9.17.4", {"center": v(252.96, -69.85) * mm, "radius": 4.76 * mm, "construction": true});
            skLineSegment(sketch, "E14.11.17.4", {"start": v(255.7, -74.61) * mm, "end": v(250.2, -74.61) * mm});
            skLineSegment(sketch, "E14.14.17.4", {"start": v(250.2, -74.61) * mm, "end": v(247.46, -69.85) * mm});
            skLineSegment(sketch, "E14.17.17.4", {"start": v(247.46, -69.85) * mm, "end": v(250.2, -65.09) * mm});
            skLineSegment(sketch, "E14.0.17.5", {"start": v(250.2, -52.39) * mm, "end": v(255.7, -52.39) * mm});
            skLineSegment(sketch, "E14.3.17.5", {"start": v(255.7, -52.39) * mm, "end": v(258.46, -57.15) * mm});
            skLineSegment(sketch, "E14.6.17.5", {"start": v(258.46, -57.15) * mm, "end": v(255.7, -61.91) * mm});
            skCircle(sketch, "E14.9.17.5", {"center": v(252.96, -57.15) * mm, "radius": 4.76 * mm, "construction": true});
            skLineSegment(sketch, "E14.11.17.5", {"start": v(255.7, -61.91) * mm, "end": v(250.2, -61.91) * mm});
            skLineSegment(sketch, "E14.14.17.5", {"start": v(250.2, -61.91) * mm, "end": v(247.46, -57.15) * mm});
            skLineSegment(sketch, "E14.17.17.5", {"start": v(247.46, -57.15) * mm, "end": v(250.2, -52.39) * mm});
            skLineSegment(sketch, "E14.0.17.6", {"start": v(250.2, -39.69) * mm, "end": v(255.7, -39.69) * mm});
            skLineSegment(sketch, "E14.3.17.6", {"start": v(255.7, -39.69) * mm, "end": v(258.46, -44.45) * mm});
            skLineSegment(sketch, "E14.6.17.6", {"start": v(258.46, -44.45) * mm, "end": v(255.7, -49.21) * mm});
            skCircle(sketch, "E14.9.17.6", {"center": v(252.96, -44.45) * mm, "radius": 4.76 * mm, "construction": true});
            skLineSegment(sketch, "E14.11.17.6", {"start": v(255.7, -49.21) * mm, "end": v(250.2, -49.21) * mm});
            skLineSegment(sketch, "E14.14.17.6", {"start": v(250.2, -49.21) * mm, "end": v(247.46, -44.45) * mm});
            skLineSegment(sketch, "E14.17.17.6", {"start": v(247.46, -44.45) * mm, "end": v(250.2, -39.69) * mm});
            skLineSegment(sketch, "E14.0.17.7", {"start": v(250.2, -26.99) * mm, "end": v(255.7, -26.99) * mm});
            skLineSegment(sketch, "E14.3.17.7", {"start": v(255.7, -26.99) * mm, "end": v(258.46, -31.75) * mm});
            skLineSegment(sketch, "E14.6.17.7", {"start": v(258.46, -31.75) * mm, "end": v(255.7, -36.51) * mm});
            skCircle(sketch, "E14.9.17.7", {"center": v(252.96, -31.75) * mm, "radius": 4.76 * mm, "construction": true});
            skLineSegment(sketch, "E14.11.17.7", {"start": v(255.7, -36.51) * mm, "end": v(250.2, -36.51) * mm});
            skLineSegment(sketch, "E14.14.17.7", {"start": v(250.2, -36.51) * mm, "end": v(247.46, -31.75) * mm});
            skLineSegment(sketch, "E14.17.17.7", {"start": v(247.46, -31.75) * mm, "end": v(250.2, -26.99) * mm});
            skLineSegment(sketch, "E14.0.17.8", {"start": v(250.2, -14.29) * mm, "end": v(255.7, -14.29) * mm});
            skLineSegment(sketch, "E14.3.17.8", {"start": v(255.7, -14.29) * mm, "end": v(258.46, -19.05) * mm});
            skLineSegment(sketch, "E14.6.17.8", {"start": v(258.46, -19.05) * mm, "end": v(255.7, -23.81) * mm});
            skCircle(sketch, "E14.9.17.8", {"center": v(252.96, -19.05) * mm, "radius": 4.76 * mm, "construction": true});
            skLineSegment(sketch, "E14.11.17.8", {"start": v(255.7, -23.81) * mm, "end": v(250.2, -23.81) * mm});
            skLineSegment(sketch, "E14.14.17.8", {"start": v(250.2, -23.81) * mm, "end": v(247.46, -19.05) * mm});
            skLineSegment(sketch, "E14.17.17.8", {"start": v(247.46, -19.05) * mm, "end": v(250.2, -14.29) * mm});
            skLineSegment(sketch, "E14.0.17.9", {"start": v(250.2, -1.59) * mm, "end": v(255.7, -1.59) * mm});
            skLineSegment(sketch, "E14.3.17.9", {"start": v(255.7, -1.59) * mm, "end": v(258.46, -6.35) * mm});
            skLineSegment(sketch, "E14.6.17.9", {"start": v(258.46, -6.35) * mm, "end": v(255.7, -11.11) * mm});
            skCircle(sketch, "E14.9.17.9", {"center": v(252.96, -6.35) * mm, "radius": 4.76 * mm, "construction": true});
            skLineSegment(sketch, "E14.11.17.9", {"start": v(255.7, -11.11) * mm, "end": v(250.2, -11.11) * mm});
            skLineSegment(sketch, "E14.14.17.9", {"start": v(250.2, -11.11) * mm, "end": v(247.46, -6.35) * mm});
            skLineSegment(sketch, "E14.17.17.9", {"start": v(247.46, -6.35) * mm, "end": v(250.2, -1.59) * mm});
            skLineSegment(sketch, "E14.0.17.10", {"start": v(250.2, 11.11) * mm, "end": v(255.7, 11.11) * mm});
            skLineSegment(sketch, "E14.3.17.10", {"start": v(255.7, 11.11) * mm, "end": v(258.46, 6.35) * mm});
            skLineSegment(sketch, "E14.6.17.10", {"start": v(258.46, 6.35) * mm, "end": v(255.7, 1.59) * mm});
            skCircle(sketch, "E14.9.17.10", {"center": v(252.96, 6.35) * mm, "radius": 4.76 * mm, "construction": true});
            skLineSegment(sketch, "E14.11.17.10", {"start": v(255.7, 1.59) * mm, "end": v(250.2, 1.59) * mm});
            skLineSegment(sketch, "E14.14.17.10", {"start": v(250.2, 1.59) * mm, "end": v(247.46, 6.35) * mm});
            skLineSegment(sketch, "E14.17.17.10", {"start": v(247.46, 6.35) * mm, "end": v(250.2, 11.11) * mm});
            skLineSegment(sketch, "E14.0.17.11", {"start": v(250.2, 23.81) * mm, "end": v(255.7, 23.81) * mm});
            skLineSegment(sketch, "E14.3.17.11", {"start": v(255.7, 23.81) * mm, "end": v(258.46, 19.05) * mm});
            skLineSegment(sketch, "E14.6.17.11", {"start": v(258.46, 19.05) * mm, "end": v(255.7, 14.29) * mm});
            skCircle(sketch, "E14.9.17.11", {"center": v(252.96, 19.05) * mm, "radius": 4.76 * mm, "construction": true});
            skLineSegment(sketch, "E14.11.17.11", {"start": v(255.7, 14.29) * mm, "end": v(250.2, 14.29) * mm});
            skLineSegment(sketch, "E14.14.17.11", {"start": v(250.2, 14.29) * mm, "end": v(247.46, 19.05) * mm});
            skLineSegment(sketch, "E14.17.17.11", {"start": v(247.46, 19.05) * mm, "end": v(250.2, 23.81) * mm});
            skLineSegment(sketch, "E14.0.17.12", {"start": v(250.2, 36.51) * mm, "end": v(255.7, 36.51) * mm});
            skLineSegment(sketch, "E14.3.17.12", {"start": v(255.7, 36.51) * mm, "end": v(258.46, 31.75) * mm});
            skLineSegment(sketch, "E14.6.17.12", {"start": v(258.46, 31.75) * mm, "end": v(255.7, 26.99) * mm});
            skCircle(sketch, "E14.9.17.12", {"center": v(252.96, 31.75) * mm, "radius": 4.76 * mm, "construction": true});
            skLineSegment(sketch, "E14.11.17.12", {"start": v(255.7, 26.99) * mm, "end": v(250.2, 26.99) * mm});
            skLineSegment(sketch, "E14.14.17.12", {"start": v(250.2, 26.99) * mm, "end": v(247.46, 31.75) * mm});
            skLineSegment(sketch, "E14.17.17.12", {"start": v(247.46, 31.75) * mm, "end": v(250.2, 36.51) * mm});
            skLineSegment(sketch, "E14.0.17.13", {"start": v(250.2, 49.21) * mm, "end": v(255.7, 49.21) * mm});
            skLineSegment(sketch, "E14.3.17.13", {"start": v(255.7, 49.21) * mm, "end": v(258.46, 44.45) * mm});
            skLineSegment(sketch, "E14.6.17.13", {"start": v(258.46, 44.45) * mm, "end": v(255.7, 39.69) * mm});
            skCircle(sketch, "E14.9.17.13", {"center": v(252.96, 44.45) * mm, "radius": 4.76 * mm, "construction": true});
            skLineSegment(sketch, "E14.11.17.13", {"start": v(255.7, 39.69) * mm, "end": v(250.2, 39.69) * mm});
            skLineSegment(sketch, "E14.14.17.13", {"start": v(250.2, 39.69) * mm, "end": v(247.46, 44.45) * mm});
            skLineSegment(sketch, "E14.17.17.13", {"start": v(247.46, 44.45) * mm, "end": v(250.2, 49.21) * mm});
            skLineSegment(sketch, "E14.0.17.14", {"start": v(250.2, 61.91) * mm, "end": v(255.7, 61.91) * mm});
            skLineSegment(sketch, "E14.3.17.14", {"start": v(255.7, 61.91) * mm, "end": v(258.46, 57.15) * mm});
            skLineSegment(sketch, "E14.6.17.14", {"start": v(258.46, 57.15) * mm, "end": v(255.7, 52.39) * mm});
            skCircle(sketch, "E14.9.17.14", {"center": v(252.96, 57.15) * mm, "radius": 4.76 * mm, "construction": true});
            skLineSegment(sketch, "E14.11.17.14", {"start": v(255.7, 52.39) * mm, "end": v(250.2, 52.39) * mm});
            skLineSegment(sketch, "E14.14.17.14", {"start": v(250.2, 52.39) * mm, "end": v(247.46, 57.15) * mm});
            skLineSegment(sketch, "E14.17.17.14", {"start": v(247.46, 57.15) * mm, "end": v(250.2, 61.91) * mm});
            skLineSegment(sketch, "E14.0.17.15", {"start": v(250.2, 74.61) * mm, "end": v(255.7, 74.61) * mm});
            skLineSegment(sketch, "E14.3.17.15", {"start": v(255.7, 74.61) * mm, "end": v(258.46, 69.85) * mm});
            skLineSegment(sketch, "E14.6.17.15", {"start": v(258.46, 69.85) * mm, "end": v(255.7, 65.09) * mm});
            skCircle(sketch, "E14.9.17.15", {"center": v(252.96, 69.85) * mm, "radius": 4.76 * mm, "construction": true});
            skLineSegment(sketch, "E14.11.17.15", {"start": v(255.7, 65.09) * mm, "end": v(250.2, 65.09) * mm});
            skLineSegment(sketch, "E14.14.17.15", {"start": v(250.2, 65.09) * mm, "end": v(247.46, 69.85) * mm});
            skLineSegment(sketch, "E14.17.17.15", {"start": v(247.46, 69.85) * mm, "end": v(250.2, 74.61) * mm});
            skLineSegment(sketch, "E14.0.17.16", {"start": v(250.2, 87.31) * mm, "end": v(255.7, 87.31) * mm});
            skLineSegment(sketch, "E14.3.17.16", {"start": v(255.7, 87.31) * mm, "end": v(258.46, 82.55) * mm});
            skLineSegment(sketch, "E14.6.17.16", {"start": v(258.46, 82.55) * mm, "end": v(255.7, 77.79) * mm});
            skCircle(sketch, "E14.9.17.16", {"center": v(252.96, 82.55) * mm, "radius": 4.76 * mm, "construction": true});
            skLineSegment(sketch, "E14.11.17.16", {"start": v(255.7, 77.79) * mm, "end": v(250.2, 77.79) * mm});
            skLineSegment(sketch, "E14.14.17.16", {"start": v(250.2, 77.79) * mm, "end": v(247.46, 82.55) * mm});
            skLineSegment(sketch, "E14.17.17.16", {"start": v(247.46, 82.55) * mm, "end": v(250.2, 87.31) * mm});
            skLineSegment(sketch, "E14.0.17.17", {"start": v(250.2, 100.01) * mm, "end": v(255.7, 100.01) * mm});
            skLineSegment(sketch, "E14.3.17.17", {"start": v(255.7, 100.01) * mm, "end": v(258.46, 95.25) * mm});
            skLineSegment(sketch, "E14.6.17.17", {"start": v(258.46, 95.25) * mm, "end": v(255.7, 90.49) * mm});
            skCircle(sketch, "E14.9.17.17", {"center": v(252.96, 95.25) * mm, "radius": 4.76 * mm, "construction": true});
            skLineSegment(sketch, "E14.11.17.17", {"start": v(255.7, 90.49) * mm, "end": v(250.2, 90.49) * mm});
            skLineSegment(sketch, "E14.14.17.17", {"start": v(250.2, 90.49) * mm, "end": v(247.46, 95.25) * mm});
            skLineSegment(sketch, "E14.17.17.17", {"start": v(247.46, 95.25) * mm, "end": v(250.2, 100.01) * mm});
            skLineSegment(sketch, "E14.0.17.18", {"start": v(250.2, 112.71) * mm, "end": v(255.7, 112.71) * mm});
            skLineSegment(sketch, "E14.3.17.18", {"start": v(255.7, 112.71) * mm, "end": v(258.46, 107.95) * mm});
            skLineSegment(sketch, "E14.6.17.18", {"start": v(258.46, 107.95) * mm, "end": v(255.7, 103.19) * mm});
            skCircle(sketch, "E14.9.17.18", {"center": v(252.96, 107.95) * mm, "radius": 4.76 * mm, "construction": true});
            skLineSegment(sketch, "E14.11.17.18", {"start": v(255.7, 103.19) * mm, "end": v(250.2, 103.19) * mm});
            skLineSegment(sketch, "E14.14.17.18", {"start": v(250.2, 103.19) * mm, "end": v(247.46, 107.95) * mm});
            skLineSegment(sketch, "E14.17.17.18", {"start": v(247.46, 107.95) * mm, "end": v(250.2, 112.71) * mm});
            skLineSegment(sketch, "E14.0.17.19", {"start": v(250.2, 125.41) * mm, "end": v(255.7, 125.41) * mm});
            skLineSegment(sketch, "E14.3.17.19", {"start": v(255.7, 125.41) * mm, "end": v(258.46, 120.65) * mm});
            skLineSegment(sketch, "E14.6.17.19", {"start": v(258.46, 120.65) * mm, "end": v(255.7, 115.89) * mm});
            skCircle(sketch, "E14.9.17.19", {"center": v(252.96, 120.65) * mm, "radius": 4.76 * mm, "construction": true});
            skLineSegment(sketch, "E14.11.17.19", {"start": v(255.7, 115.89) * mm, "end": v(250.2, 115.89) * mm});
            skLineSegment(sketch, "E14.14.17.19", {"start": v(250.2, 115.89) * mm, "end": v(247.46, 120.65) * mm});
            skLineSegment(sketch, "E14.17.17.19", {"start": v(247.46, 120.65) * mm, "end": v(250.2, 125.41) * mm});
            skLineSegment(sketch, "E14.0.18.0", {"start": v(272.2, -115.89) * mm, "end": v(277.7, -115.89) * mm});
            skLineSegment(sketch, "E14.3.18.0", {"start": v(277.7, -115.89) * mm, "end": v(280.45, -120.65) * mm});
            skLineSegment(sketch, "E14.6.18.0", {"start": v(280.45, -120.65) * mm, "end": v(277.7, -125.41) * mm});
            skCircle(sketch, "E14.9.18.0", {"center": v(274.95, -120.65) * mm, "radius": 4.76 * mm, "construction": true});
            skLineSegment(sketch, "E14.11.18.0", {"start": v(277.7, -125.41) * mm, "end": v(272.2, -125.41) * mm});
            skLineSegment(sketch, "E14.14.18.0", {"start": v(272.2, -125.41) * mm, "end": v(269.46, -120.65) * mm});
            skLineSegment(sketch, "E14.17.18.0", {"start": v(269.46, -120.65) * mm, "end": v(272.2, -115.89) * mm});
            skLineSegment(sketch, "E14.0.18.1", {"start": v(272.2, -103.19) * mm, "end": v(277.7, -103.19) * mm});
            skLineSegment(sketch, "E14.3.18.1", {"start": v(277.7, -103.19) * mm, "end": v(280.45, -107.95) * mm});
            skLineSegment(sketch, "E14.6.18.1", {"start": v(280.45, -107.95) * mm, "end": v(277.7, -112.71) * mm});
            skCircle(sketch, "E14.9.18.1", {"center": v(274.95, -107.95) * mm, "radius": 4.76 * mm, "construction": true});
            skLineSegment(sketch, "E14.11.18.1", {"start": v(277.7, -112.71) * mm, "end": v(272.2, -112.71) * mm});
            skLineSegment(sketch, "E14.14.18.1", {"start": v(272.2, -112.71) * mm, "end": v(269.46, -107.95) * mm});
            skLineSegment(sketch, "E14.17.18.1", {"start": v(269.46, -107.95) * mm, "end": v(272.2, -103.19) * mm});
            skLineSegment(sketch, "E14.0.18.2", {"start": v(272.2, -90.49) * mm, "end": v(277.7, -90.49) * mm});
            skLineSegment(sketch, "E14.3.18.2", {"start": v(277.7, -90.49) * mm, "end": v(280.45, -95.25) * mm});
            skLineSegment(sketch, "E14.6.18.2", {"start": v(280.45, -95.25) * mm, "end": v(277.7, -100.01) * mm});
            skCircle(sketch, "E14.9.18.2", {"center": v(274.95, -95.25) * mm, "radius": 4.76 * mm, "construction": true});
            skLineSegment(sketch, "E14.11.18.2", {"start": v(277.7, -100.01) * mm, "end": v(272.2, -100.01) * mm});
            skLineSegment(sketch, "E14.14.18.2", {"start": v(272.2, -100.01) * mm, "end": v(269.46, -95.25) * mm});
            skLineSegment(sketch, "E14.17.18.2", {"start": v(269.46, -95.25) * mm, "end": v(272.2, -90.49) * mm});
            skLineSegment(sketch, "E14.0.18.3", {"start": v(272.2, -77.79) * mm, "end": v(277.7, -77.79) * mm});
            skLineSegment(sketch, "E14.3.18.3", {"start": v(277.7, -77.79) * mm, "end": v(280.45, -82.55) * mm});
            skLineSegment(sketch, "E14.6.18.3", {"start": v(280.45, -82.55) * mm, "end": v(277.7, -87.31) * mm});
            skCircle(sketch, "E14.9.18.3", {"center": v(274.95, -82.55) * mm, "radius": 4.76 * mm, "construction": true});
            skLineSegment(sketch, "E14.11.18.3", {"start": v(277.7, -87.31) * mm, "end": v(272.2, -87.31) * mm});
            skLineSegment(sketch, "E14.14.18.3", {"start": v(272.2, -87.31) * mm, "end": v(269.46, -82.55) * mm});
            skLineSegment(sketch, "E14.17.18.3", {"start": v(269.46, -82.55) * mm, "end": v(272.2, -77.79) * mm});
            skLineSegment(sketch, "E14.0.18.4", {"start": v(272.2, -65.09) * mm, "end": v(277.7, -65.09) * mm});
            skLineSegment(sketch, "E14.3.18.4", {"start": v(277.7, -65.09) * mm, "end": v(280.45, -69.85) * mm});
            skLineSegment(sketch, "E14.6.18.4", {"start": v(280.45, -69.85) * mm, "end": v(277.7, -74.61) * mm});
            skCircle(sketch, "E14.9.18.4", {"center": v(274.95, -69.85) * mm, "radius": 4.76 * mm, "construction": true});
            skLineSegment(sketch, "E14.11.18.4", {"start": v(277.7, -74.61) * mm, "end": v(272.2, -74.61) * mm});
            skLineSegment(sketch, "E14.14.18.4", {"start": v(272.2, -74.61) * mm, "end": v(269.46, -69.85) * mm});
            skLineSegment(sketch, "E14.17.18.4", {"start": v(269.46, -69.85) * mm, "end": v(272.2, -65.09) * mm});
            skLineSegment(sketch, "E14.0.18.5", {"start": v(272.2, -52.39) * mm, "end": v(277.7, -52.39) * mm});
            skLineSegment(sketch, "E14.3.18.5", {"start": v(277.7, -52.39) * mm, "end": v(280.45, -57.15) * mm});
            skLineSegment(sketch, "E14.6.18.5", {"start": v(280.45, -57.15) * mm, "end": v(277.7, -61.91) * mm});
            skCircle(sketch, "E14.9.18.5", {"center": v(274.95, -57.15) * mm, "radius": 4.76 * mm, "construction": true});
            skLineSegment(sketch, "E14.11.18.5", {"start": v(277.7, -61.91) * mm, "end": v(272.2, -61.91) * mm});
            skLineSegment(sketch, "E14.14.18.5", {"start": v(272.2, -61.91) * mm, "end": v(269.46, -57.15) * mm});
            skLineSegment(sketch, "E14.17.18.5", {"start": v(269.46, -57.15) * mm, "end": v(272.2, -52.39) * mm});
            skLineSegment(sketch, "E14.0.18.6", {"start": v(272.2, -39.69) * mm, "end": v(277.7, -39.69) * mm});
            skLineSegment(sketch, "E14.3.18.6", {"start": v(277.7, -39.69) * mm, "end": v(280.45, -44.45) * mm});
            skLineSegment(sketch, "E14.6.18.6", {"start": v(280.45, -44.45) * mm, "end": v(277.7, -49.21) * mm});
            skCircle(sketch, "E14.9.18.6", {"center": v(274.95, -44.45) * mm, "radius": 4.76 * mm, "construction": true});
            skLineSegment(sketch, "E14.11.18.6", {"start": v(277.7, -49.21) * mm, "end": v(272.2, -49.21) * mm});
            skLineSegment(sketch, "E14.14.18.6", {"start": v(272.2, -49.21) * mm, "end": v(269.46, -44.45) * mm});
            skLineSegment(sketch, "E14.17.18.6", {"start": v(269.46, -44.45) * mm, "end": v(272.2, -39.69) * mm});
            skLineSegment(sketch, "E14.0.18.7", {"start": v(272.2, -26.99) * mm, "end": v(277.7, -26.99) * mm});
            skLineSegment(sketch, "E14.3.18.7", {"start": v(277.7, -26.99) * mm, "end": v(280.45, -31.75) * mm});
            skLineSegment(sketch, "E14.6.18.7", {"start": v(280.45, -31.75) * mm, "end": v(277.7, -36.51) * mm});
            skCircle(sketch, "E14.9.18.7", {"center": v(274.95, -31.75) * mm, "radius": 4.76 * mm, "construction": true});
            skLineSegment(sketch, "E14.11.18.7", {"start": v(277.7, -36.51) * mm, "end": v(272.2, -36.51) * mm});
            skLineSegment(sketch, "E14.14.18.7", {"start": v(272.2, -36.51) * mm, "end": v(269.46, -31.75) * mm});
            skLineSegment(sketch, "E14.17.18.7", {"start": v(269.46, -31.75) * mm, "end": v(272.2, -26.99) * mm});
            skLineSegment(sketch, "E14.0.18.8", {"start": v(272.2, -14.29) * mm, "end": v(277.7, -14.29) * mm});
            skLineSegment(sketch, "E14.3.18.8", {"start": v(277.7, -14.29) * mm, "end": v(280.45, -19.05) * mm});
            skLineSegment(sketch, "E14.6.18.8", {"start": v(280.45, -19.05) * mm, "end": v(277.7, -23.81) * mm});
            skCircle(sketch, "E14.9.18.8", {"center": v(274.95, -19.05) * mm, "radius": 4.76 * mm, "construction": true});
            skLineSegment(sketch, "E14.11.18.8", {"start": v(277.7, -23.81) * mm, "end": v(272.2, -23.81) * mm});
            skLineSegment(sketch, "E14.14.18.8", {"start": v(272.2, -23.81) * mm, "end": v(269.46, -19.05) * mm});
            skLineSegment(sketch, "E14.17.18.8", {"start": v(269.46, -19.05) * mm, "end": v(272.2, -14.29) * mm});
            skLineSegment(sketch, "E14.0.18.9", {"start": v(272.2, -1.59) * mm, "end": v(277.7, -1.59) * mm});
            skLineSegment(sketch, "E14.3.18.9", {"start": v(277.7, -1.59) * mm, "end": v(280.45, -6.35) * mm});
            skLineSegment(sketch, "E14.6.18.9", {"start": v(280.45, -6.35) * mm, "end": v(277.7, -11.11) * mm});
            skCircle(sketch, "E14.9.18.9", {"center": v(274.95, -6.35) * mm, "radius": 4.76 * mm, "construction": true});
            skLineSegment(sketch, "E14.11.18.9", {"start": v(277.7, -11.11) * mm, "end": v(272.2, -11.11) * mm});
            skLineSegment(sketch, "E14.14.18.9", {"start": v(272.2, -11.11) * mm, "end": v(269.46, -6.35) * mm});
            skLineSegment(sketch, "E14.17.18.9", {"start": v(269.46, -6.35) * mm, "end": v(272.2, -1.59) * mm});
            skLineSegment(sketch, "E14.0.18.10", {"start": v(272.2, 11.11) * mm, "end": v(277.7, 11.11) * mm});
            skLineSegment(sketch, "E14.3.18.10", {"start": v(277.7, 11.11) * mm, "end": v(280.45, 6.35) * mm});
            skLineSegment(sketch, "E14.6.18.10", {"start": v(280.45, 6.35) * mm, "end": v(277.7, 1.59) * mm});
            skCircle(sketch, "E14.9.18.10", {"center": v(274.95, 6.35) * mm, "radius": 4.76 * mm, "construction": true});
            skLineSegment(sketch, "E14.11.18.10", {"start": v(277.7, 1.59) * mm, "end": v(272.2, 1.59) * mm});
            skLineSegment(sketch, "E14.14.18.10", {"start": v(272.2, 1.59) * mm, "end": v(269.46, 6.35) * mm});
            skLineSegment(sketch, "E14.17.18.10", {"start": v(269.46, 6.35) * mm, "end": v(272.2, 11.11) * mm});
            skLineSegment(sketch, "E14.0.18.11", {"start": v(272.2, 23.81) * mm, "end": v(277.7, 23.81) * mm});
            skLineSegment(sketch, "E14.3.18.11", {"start": v(277.7, 23.81) * mm, "end": v(280.45, 19.05) * mm});
            skLineSegment(sketch, "E14.6.18.11", {"start": v(280.45, 19.05) * mm, "end": v(277.7, 14.29) * mm});
            skCircle(sketch, "E14.9.18.11", {"center": v(274.95, 19.05) * mm, "radius": 4.76 * mm, "construction": true});
            skLineSegment(sketch, "E14.11.18.11", {"start": v(277.7, 14.29) * mm, "end": v(272.2, 14.29) * mm});
            skLineSegment(sketch, "E14.14.18.11", {"start": v(272.2, 14.29) * mm, "end": v(269.46, 19.05) * mm});
            skLineSegment(sketch, "E14.17.18.11", {"start": v(269.46, 19.05) * mm, "end": v(272.2, 23.81) * mm});
            skLineSegment(sketch, "E14.0.18.12", {"start": v(272.2, 36.51) * mm, "end": v(277.7, 36.51) * mm});
            skLineSegment(sketch, "E14.3.18.12", {"start": v(277.7, 36.51) * mm, "end": v(280.45, 31.75) * mm});
            skLineSegment(sketch, "E14.6.18.12", {"start": v(280.45, 31.75) * mm, "end": v(277.7, 26.99) * mm});
            skCircle(sketch, "E14.9.18.12", {"center": v(274.95, 31.75) * mm, "radius": 4.76 * mm, "construction": true});
            skLineSegment(sketch, "E14.11.18.12", {"start": v(277.7, 26.99) * mm, "end": v(272.2, 26.99) * mm});
            skLineSegment(sketch, "E14.14.18.12", {"start": v(272.2, 26.99) * mm, "end": v(269.46, 31.75) * mm});
            skLineSegment(sketch, "E14.17.18.12", {"start": v(269.46, 31.75) * mm, "end": v(272.2, 36.51) * mm});
            skLineSegment(sketch, "E14.0.18.13", {"start": v(272.2, 49.21) * mm, "end": v(277.7, 49.21) * mm});
            skLineSegment(sketch, "E14.3.18.13", {"start": v(277.7, 49.21) * mm, "end": v(280.45, 44.45) * mm});
            skLineSegment(sketch, "E14.6.18.13", {"start": v(280.45, 44.45) * mm, "end": v(277.7, 39.69) * mm});
            skCircle(sketch, "E14.9.18.13", {"center": v(274.95, 44.45) * mm, "radius": 4.76 * mm, "construction": true});
            skLineSegment(sketch, "E14.11.18.13", {"start": v(277.7, 39.69) * mm, "end": v(272.2, 39.69) * mm});
            skLineSegment(sketch, "E14.14.18.13", {"start": v(272.2, 39.69) * mm, "end": v(269.46, 44.45) * mm});
            skLineSegment(sketch, "E14.17.18.13", {"start": v(269.46, 44.45) * mm, "end": v(272.2, 49.21) * mm});
            skLineSegment(sketch, "E14.0.18.14", {"start": v(272.2, 61.91) * mm, "end": v(277.7, 61.91) * mm});
            skLineSegment(sketch, "E14.3.18.14", {"start": v(277.7, 61.91) * mm, "end": v(280.45, 57.15) * mm});
            skLineSegment(sketch, "E14.6.18.14", {"start": v(280.45, 57.15) * mm, "end": v(277.7, 52.39) * mm});
            skCircle(sketch, "E14.9.18.14", {"center": v(274.95, 57.15) * mm, "radius": 4.76 * mm, "construction": true});
            skLineSegment(sketch, "E14.11.18.14", {"start": v(277.7, 52.39) * mm, "end": v(272.2, 52.39) * mm});
            skLineSegment(sketch, "E14.14.18.14", {"start": v(272.2, 52.39) * mm, "end": v(269.46, 57.15) * mm});
            skLineSegment(sketch, "E14.17.18.14", {"start": v(269.46, 57.15) * mm, "end": v(272.2, 61.91) * mm});
            skLineSegment(sketch, "E14.0.18.15", {"start": v(272.2, 74.61) * mm, "end": v(277.7, 74.61) * mm});
            skLineSegment(sketch, "E14.3.18.15", {"start": v(277.7, 74.61) * mm, "end": v(280.45, 69.85) * mm});
            skLineSegment(sketch, "E14.6.18.15", {"start": v(280.45, 69.85) * mm, "end": v(277.7, 65.09) * mm});
            skCircle(sketch, "E14.9.18.15", {"center": v(274.95, 69.85) * mm, "radius": 4.76 * mm, "construction": true});
            skLineSegment(sketch, "E14.11.18.15", {"start": v(277.7, 65.09) * mm, "end": v(272.2, 65.09) * mm});
            skLineSegment(sketch, "E14.14.18.15", {"start": v(272.2, 65.09) * mm, "end": v(269.46, 69.85) * mm});
            skLineSegment(sketch, "E14.17.18.15", {"start": v(269.46, 69.85) * mm, "end": v(272.2, 74.61) * mm});
            skLineSegment(sketch, "E14.0.18.16", {"start": v(272.2, 87.31) * mm, "end": v(277.7, 87.31) * mm});
            skLineSegment(sketch, "E14.3.18.16", {"start": v(277.7, 87.31) * mm, "end": v(280.45, 82.55) * mm});
            skLineSegment(sketch, "E14.6.18.16", {"start": v(280.45, 82.55) * mm, "end": v(277.7, 77.79) * mm});
            skCircle(sketch, "E14.9.18.16", {"center": v(274.95, 82.55) * mm, "radius": 4.76 * mm, "construction": true});
            skLineSegment(sketch, "E14.11.18.16", {"start": v(277.7, 77.79) * mm, "end": v(272.2, 77.79) * mm});
            skLineSegment(sketch, "E14.14.18.16", {"start": v(272.2, 77.79) * mm, "end": v(269.46, 82.55) * mm});
            skLineSegment(sketch, "E14.17.18.16", {"start": v(269.46, 82.55) * mm, "end": v(272.2, 87.31) * mm});
            skLineSegment(sketch, "E14.0.18.17", {"start": v(272.2, 100.01) * mm, "end": v(277.7, 100.01) * mm});
            skLineSegment(sketch, "E14.3.18.17", {"start": v(277.7, 100.01) * mm, "end": v(280.45, 95.25) * mm});
            skLineSegment(sketch, "E14.6.18.17", {"start": v(280.45, 95.25) * mm, "end": v(277.7, 90.49) * mm});
            skCircle(sketch, "E14.9.18.17", {"center": v(274.95, 95.25) * mm, "radius": 4.76 * mm, "construction": true});
            skLineSegment(sketch, "E14.11.18.17", {"start": v(277.7, 90.49) * mm, "end": v(272.2, 90.49) * mm});
            skLineSegment(sketch, "E14.14.18.17", {"start": v(272.2, 90.49) * mm, "end": v(269.46, 95.25) * mm});
            skLineSegment(sketch, "E14.17.18.17", {"start": v(269.46, 95.25) * mm, "end": v(272.2, 100.01) * mm});
            skLineSegment(sketch, "E14.0.18.18", {"start": v(272.2, 112.71) * mm, "end": v(277.7, 112.71) * mm});
            skLineSegment(sketch, "E14.3.18.18", {"start": v(277.7, 112.71) * mm, "end": v(280.45, 107.95) * mm});
            skLineSegment(sketch, "E14.6.18.18", {"start": v(280.45, 107.95) * mm, "end": v(277.7, 103.19) * mm});
            skCircle(sketch, "E14.9.18.18", {"center": v(274.95, 107.95) * mm, "radius": 4.76 * mm, "construction": true});
            skLineSegment(sketch, "E14.11.18.18", {"start": v(277.7, 103.19) * mm, "end": v(272.2, 103.19) * mm});
            skLineSegment(sketch, "E14.14.18.18", {"start": v(272.2, 103.19) * mm, "end": v(269.46, 107.95) * mm});
            skLineSegment(sketch, "E14.17.18.18", {"start": v(269.46, 107.95) * mm, "end": v(272.2, 112.71) * mm});
            skLineSegment(sketch, "E14.0.18.19", {"start": v(272.2, 125.41) * mm, "end": v(277.7, 125.41) * mm});
            skLineSegment(sketch, "E14.3.18.19", {"start": v(277.7, 125.41) * mm, "end": v(280.45, 120.65) * mm});
            skLineSegment(sketch, "E14.6.18.19", {"start": v(280.45, 120.65) * mm, "end": v(277.7, 115.89) * mm});
            skCircle(sketch, "E14.9.18.19", {"center": v(274.95, 120.65) * mm, "radius": 4.76 * mm, "construction": true});
            skLineSegment(sketch, "E14.11.18.19", {"start": v(277.7, 115.89) * mm, "end": v(272.2, 115.89) * mm});
            skLineSegment(sketch, "E14.14.18.19", {"start": v(272.2, 115.89) * mm, "end": v(269.46, 120.65) * mm});
            skLineSegment(sketch, "E14.17.18.19", {"start": v(269.46, 120.65) * mm, "end": v(272.2, 125.41) * mm});
            skLineSegment(sketch, "E14.0.19.0", {"start": v(294.2, -115.89) * mm, "end": v(299.7, -115.89) * mm});
            skLineSegment(sketch, "E14.3.19.0", {"start": v(299.7, -115.89) * mm, "end": v(302.45, -120.65) * mm});
            skLineSegment(sketch, "E14.6.19.0", {"start": v(302.45, -120.65) * mm, "end": v(299.7, -125.41) * mm});
            skCircle(sketch, "E14.9.19.0", {"center": v(296.95, -120.65) * mm, "radius": 4.76 * mm, "construction": true});
            skLineSegment(sketch, "E14.11.19.0", {"start": v(299.7, -125.41) * mm, "end": v(294.2, -125.41) * mm});
            skLineSegment(sketch, "E14.14.19.0", {"start": v(294.2, -125.41) * mm, "end": v(291.45, -120.65) * mm});
            skLineSegment(sketch, "E14.17.19.0", {"start": v(291.45, -120.65) * mm, "end": v(294.2, -115.89) * mm});
            skLineSegment(sketch, "E14.0.19.1", {"start": v(294.2, -103.19) * mm, "end": v(299.7, -103.19) * mm});
            skLineSegment(sketch, "E14.3.19.1", {"start": v(299.7, -103.19) * mm, "end": v(302.45, -107.95) * mm});
            skLineSegment(sketch, "E14.6.19.1", {"start": v(302.45, -107.95) * mm, "end": v(299.7, -112.71) * mm});
            skCircle(sketch, "E14.9.19.1", {"center": v(296.95, -107.95) * mm, "radius": 4.76 * mm, "construction": true});
            skLineSegment(sketch, "E14.11.19.1", {"start": v(299.7, -112.71) * mm, "end": v(294.2, -112.71) * mm});
            skLineSegment(sketch, "E14.14.19.1", {"start": v(294.2, -112.71) * mm, "end": v(291.45, -107.95) * mm});
            skLineSegment(sketch, "E14.17.19.1", {"start": v(291.45, -107.95) * mm, "end": v(294.2, -103.19) * mm});
            skLineSegment(sketch, "E14.0.19.2", {"start": v(294.2, -90.49) * mm, "end": v(299.7, -90.49) * mm});
            skLineSegment(sketch, "E14.3.19.2", {"start": v(299.7, -90.49) * mm, "end": v(302.45, -95.25) * mm});
            skLineSegment(sketch, "E14.6.19.2", {"start": v(302.45, -95.25) * mm, "end": v(299.7, -100.01) * mm});
            skCircle(sketch, "E14.9.19.2", {"center": v(296.95, -95.25) * mm, "radius": 4.76 * mm, "construction": true});
            skLineSegment(sketch, "E14.11.19.2", {"start": v(299.7, -100.01) * mm, "end": v(294.2, -100.01) * mm});
            skLineSegment(sketch, "E14.14.19.2", {"start": v(294.2, -100.01) * mm, "end": v(291.45, -95.25) * mm});
            skLineSegment(sketch, "E14.17.19.2", {"start": v(291.45, -95.25) * mm, "end": v(294.2, -90.49) * mm});
            skLineSegment(sketch, "E14.0.19.3", {"start": v(294.2, -77.79) * mm, "end": v(299.7, -77.79) * mm});
            skLineSegment(sketch, "E14.3.19.3", {"start": v(299.7, -77.79) * mm, "end": v(302.45, -82.55) * mm});
            skLineSegment(sketch, "E14.6.19.3", {"start": v(302.45, -82.55) * mm, "end": v(299.7, -87.31) * mm});
            skCircle(sketch, "E14.9.19.3", {"center": v(296.95, -82.55) * mm, "radius": 4.76 * mm, "construction": true});
            skLineSegment(sketch, "E14.11.19.3", {"start": v(299.7, -87.31) * mm, "end": v(294.2, -87.31) * mm});
            skLineSegment(sketch, "E14.14.19.3", {"start": v(294.2, -87.31) * mm, "end": v(291.45, -82.55) * mm});
            skLineSegment(sketch, "E14.17.19.3", {"start": v(291.45, -82.55) * mm, "end": v(294.2, -77.79) * mm});
            skLineSegment(sketch, "E14.0.19.4", {"start": v(294.2, -65.09) * mm, "end": v(299.7, -65.09) * mm});
            skLineSegment(sketch, "E14.3.19.4", {"start": v(299.7, -65.09) * mm, "end": v(302.45, -69.85) * mm});
            skLineSegment(sketch, "E14.6.19.4", {"start": v(302.45, -69.85) * mm, "end": v(299.7, -74.61) * mm});
            skCircle(sketch, "E14.9.19.4", {"center": v(296.95, -69.85) * mm, "radius": 4.76 * mm, "construction": true});
            skLineSegment(sketch, "E14.11.19.4", {"start": v(299.7, -74.61) * mm, "end": v(294.2, -74.61) * mm});
            skLineSegment(sketch, "E14.14.19.4", {"start": v(294.2, -74.61) * mm, "end": v(291.45, -69.85) * mm});
            skLineSegment(sketch, "E14.17.19.4", {"start": v(291.45, -69.85) * mm, "end": v(294.2, -65.09) * mm});
            skLineSegment(sketch, "E14.0.19.5", {"start": v(294.2, -52.39) * mm, "end": v(299.7, -52.39) * mm});
            skLineSegment(sketch, "E14.3.19.5", {"start": v(299.7, -52.39) * mm, "end": v(302.45, -57.15) * mm});
            skLineSegment(sketch, "E14.6.19.5", {"start": v(302.45, -57.15) * mm, "end": v(299.7, -61.91) * mm});
            skCircle(sketch, "E14.9.19.5", {"center": v(296.95, -57.15) * mm, "radius": 4.76 * mm, "construction": true});
            skLineSegment(sketch, "E14.11.19.5", {"start": v(299.7, -61.91) * mm, "end": v(294.2, -61.91) * mm});
            skLineSegment(sketch, "E14.14.19.5", {"start": v(294.2, -61.91) * mm, "end": v(291.45, -57.15) * mm});
            skLineSegment(sketch, "E14.17.19.5", {"start": v(291.45, -57.15) * mm, "end": v(294.2, -52.39) * mm});
            skLineSegment(sketch, "E14.0.19.6", {"start": v(294.2, -39.69) * mm, "end": v(299.7, -39.69) * mm});
            skLineSegment(sketch, "E14.3.19.6", {"start": v(299.7, -39.69) * mm, "end": v(302.45, -44.45) * mm});
            skLineSegment(sketch, "E14.6.19.6", {"start": v(302.45, -44.45) * mm, "end": v(299.7, -49.21) * mm});
            skCircle(sketch, "E14.9.19.6", {"center": v(296.95, -44.45) * mm, "radius": 4.76 * mm, "construction": true});
            skLineSegment(sketch, "E14.11.19.6", {"start": v(299.7, -49.21) * mm, "end": v(294.2, -49.21) * mm});
            skLineSegment(sketch, "E14.14.19.6", {"start": v(294.2, -49.21) * mm, "end": v(291.45, -44.45) * mm});
            skLineSegment(sketch, "E14.17.19.6", {"start": v(291.45, -44.45) * mm, "end": v(294.2, -39.69) * mm});
            skLineSegment(sketch, "E14.0.19.7", {"start": v(294.2, -26.99) * mm, "end": v(299.7, -26.99) * mm});
            skLineSegment(sketch, "E14.3.19.7", {"start": v(299.7, -26.99) * mm, "end": v(302.45, -31.75) * mm});
            skLineSegment(sketch, "E14.6.19.7", {"start": v(302.45, -31.75) * mm, "end": v(299.7, -36.51) * mm});
            skCircle(sketch, "E14.9.19.7", {"center": v(296.95, -31.75) * mm, "radius": 4.76 * mm, "construction": true});
            skLineSegment(sketch, "E14.11.19.7", {"start": v(299.7, -36.51) * mm, "end": v(294.2, -36.51) * mm});
            skLineSegment(sketch, "E14.14.19.7", {"start": v(294.2, -36.51) * mm, "end": v(291.45, -31.75) * mm});
            skLineSegment(sketch, "E14.17.19.7", {"start": v(291.45, -31.75) * mm, "end": v(294.2, -26.99) * mm});
            skLineSegment(sketch, "E14.0.19.8", {"start": v(294.2, -14.29) * mm, "end": v(299.7, -14.29) * mm});
            skLineSegment(sketch, "E14.3.19.8", {"start": v(299.7, -14.29) * mm, "end": v(302.45, -19.05) * mm});
            skLineSegment(sketch, "E14.6.19.8", {"start": v(302.45, -19.05) * mm, "end": v(299.7, -23.81) * mm});
            skCircle(sketch, "E14.9.19.8", {"center": v(296.95, -19.05) * mm, "radius": 4.76 * mm, "construction": true});
            skLineSegment(sketch, "E14.11.19.8", {"start": v(299.7, -23.81) * mm, "end": v(294.2, -23.81) * mm});
            skLineSegment(sketch, "E14.14.19.8", {"start": v(294.2, -23.81) * mm, "end": v(291.45, -19.05) * mm});
            skLineSegment(sketch, "E14.17.19.8", {"start": v(291.45, -19.05) * mm, "end": v(294.2, -14.29) * mm});
            skLineSegment(sketch, "E14.0.19.9", {"start": v(294.2, -1.59) * mm, "end": v(299.7, -1.59) * mm});
            skLineSegment(sketch, "E14.3.19.9", {"start": v(299.7, -1.59) * mm, "end": v(302.45, -6.35) * mm});
            skLineSegment(sketch, "E14.6.19.9", {"start": v(302.45, -6.35) * mm, "end": v(299.7, -11.11) * mm});
            skCircle(sketch, "E14.9.19.9", {"center": v(296.95, -6.35) * mm, "radius": 4.76 * mm, "construction": true});
            skLineSegment(sketch, "E14.11.19.9", {"start": v(299.7, -11.11) * mm, "end": v(294.2, -11.11) * mm});
            skLineSegment(sketch, "E14.14.19.9", {"start": v(294.2, -11.11) * mm, "end": v(291.45, -6.35) * mm});
            skLineSegment(sketch, "E14.17.19.9", {"start": v(291.45, -6.35) * mm, "end": v(294.2, -1.59) * mm});
            skLineSegment(sketch, "E14.0.19.10", {"start": v(294.2, 11.11) * mm, "end": v(299.7, 11.11) * mm});
            skLineSegment(sketch, "E14.3.19.10", {"start": v(299.7, 11.11) * mm, "end": v(302.45, 6.35) * mm});
            skLineSegment(sketch, "E14.6.19.10", {"start": v(302.45, 6.35) * mm, "end": v(299.7, 1.59) * mm});
            skCircle(sketch, "E14.9.19.10", {"center": v(296.95, 6.35) * mm, "radius": 4.76 * mm, "construction": true});
            skLineSegment(sketch, "E14.11.19.10", {"start": v(299.7, 1.59) * mm, "end": v(294.2, 1.59) * mm});
            skLineSegment(sketch, "E14.14.19.10", {"start": v(294.2, 1.59) * mm, "end": v(291.45, 6.35) * mm});
            skLineSegment(sketch, "E14.17.19.10", {"start": v(291.45, 6.35) * mm, "end": v(294.2, 11.11) * mm});
            skLineSegment(sketch, "E14.0.19.11", {"start": v(294.2, 23.81) * mm, "end": v(299.7, 23.81) * mm});
            skLineSegment(sketch, "E14.3.19.11", {"start": v(299.7, 23.81) * mm, "end": v(302.45, 19.05) * mm});
            skLineSegment(sketch, "E14.6.19.11", {"start": v(302.45, 19.05) * mm, "end": v(299.7, 14.29) * mm});
            skCircle(sketch, "E14.9.19.11", {"center": v(296.95, 19.05) * mm, "radius": 4.76 * mm, "construction": true});
            skLineSegment(sketch, "E14.11.19.11", {"start": v(299.7, 14.29) * mm, "end": v(294.2, 14.29) * mm});
            skLineSegment(sketch, "E14.14.19.11", {"start": v(294.2, 14.29) * mm, "end": v(291.45, 19.05) * mm});
            skLineSegment(sketch, "E14.17.19.11", {"start": v(291.45, 19.05) * mm, "end": v(294.2, 23.81) * mm});
            skLineSegment(sketch, "E14.0.19.12", {"start": v(294.2, 36.51) * mm, "end": v(299.7, 36.51) * mm});
            skLineSegment(sketch, "E14.3.19.12", {"start": v(299.7, 36.51) * mm, "end": v(302.45, 31.75) * mm});
            skLineSegment(sketch, "E14.6.19.12", {"start": v(302.45, 31.75) * mm, "end": v(299.7, 26.99) * mm});
            skCircle(sketch, "E14.9.19.12", {"center": v(296.95, 31.75) * mm, "radius": 4.76 * mm, "construction": true});
            skLineSegment(sketch, "E14.11.19.12", {"start": v(299.7, 26.99) * mm, "end": v(294.2, 26.99) * mm});
            skLineSegment(sketch, "E14.14.19.12", {"start": v(294.2, 26.99) * mm, "end": v(291.45, 31.75) * mm});
            skLineSegment(sketch, "E14.17.19.12", {"start": v(291.45, 31.75) * mm, "end": v(294.2, 36.51) * mm});
            skLineSegment(sketch, "E14.0.19.13", {"start": v(294.2, 49.21) * mm, "end": v(299.7, 49.21) * mm});
            skLineSegment(sketch, "E14.3.19.13", {"start": v(299.7, 49.21) * mm, "end": v(302.45, 44.45) * mm});
            skLineSegment(sketch, "E14.6.19.13", {"start": v(302.45, 44.45) * mm, "end": v(299.7, 39.69) * mm});
            skCircle(sketch, "E14.9.19.13", {"center": v(296.95, 44.45) * mm, "radius": 4.76 * mm, "construction": true});
            skLineSegment(sketch, "E14.11.19.13", {"start": v(299.7, 39.69) * mm, "end": v(294.2, 39.69) * mm});
            skLineSegment(sketch, "E14.14.19.13", {"start": v(294.2, 39.69) * mm, "end": v(291.45, 44.45) * mm});
            skLineSegment(sketch, "E14.17.19.13", {"start": v(291.45, 44.45) * mm, "end": v(294.2, 49.21) * mm});
            skLineSegment(sketch, "E14.0.19.14", {"start": v(294.2, 61.91) * mm, "end": v(299.7, 61.91) * mm});
            skLineSegment(sketch, "E14.3.19.14", {"start": v(299.7, 61.91) * mm, "end": v(302.45, 57.15) * mm});
            skLineSegment(sketch, "E14.6.19.14", {"start": v(302.45, 57.15) * mm, "end": v(299.7, 52.39) * mm});
            skCircle(sketch, "E14.9.19.14", {"center": v(296.95, 57.15) * mm, "radius": 4.76 * mm, "construction": true});
            skLineSegment(sketch, "E14.11.19.14", {"start": v(299.7, 52.39) * mm, "end": v(294.2, 52.39) * mm});
            skLineSegment(sketch, "E14.14.19.14", {"start": v(294.2, 52.39) * mm, "end": v(291.45, 57.15) * mm});
            skLineSegment(sketch, "E14.17.19.14", {"start": v(291.45, 57.15) * mm, "end": v(294.2, 61.91) * mm});
            skLineSegment(sketch, "E14.0.19.15", {"start": v(294.2, 74.61) * mm, "end": v(299.7, 74.61) * mm});
            skLineSegment(sketch, "E14.3.19.15", {"start": v(299.7, 74.61) * mm, "end": v(302.45, 69.85) * mm});
            skLineSegment(sketch, "E14.6.19.15", {"start": v(302.45, 69.85) * mm, "end": v(299.7, 65.09) * mm});
            skCircle(sketch, "E14.9.19.15", {"center": v(296.95, 69.85) * mm, "radius": 4.76 * mm, "construction": true});
            skLineSegment(sketch, "E14.11.19.15", {"start": v(299.7, 65.09) * mm, "end": v(294.2, 65.09) * mm});
            skLineSegment(sketch, "E14.14.19.15", {"start": v(294.2, 65.09) * mm, "end": v(291.45, 69.85) * mm});
            skLineSegment(sketch, "E14.17.19.15", {"start": v(291.45, 69.85) * mm, "end": v(294.2, 74.61) * mm});
            skLineSegment(sketch, "E14.0.19.16", {"start": v(294.2, 87.31) * mm, "end": v(299.7, 87.31) * mm});
            skLineSegment(sketch, "E14.3.19.16", {"start": v(299.7, 87.31) * mm, "end": v(302.45, 82.55) * mm});
            skLineSegment(sketch, "E14.6.19.16", {"start": v(302.45, 82.55) * mm, "end": v(299.7, 77.79) * mm});
            skCircle(sketch, "E14.9.19.16", {"center": v(296.95, 82.55) * mm, "radius": 4.76 * mm, "construction": true});
            skLineSegment(sketch, "E14.11.19.16", {"start": v(299.7, 77.79) * mm, "end": v(294.2, 77.79) * mm});
            skLineSegment(sketch, "E14.14.19.16", {"start": v(294.2, 77.79) * mm, "end": v(291.45, 82.55) * mm});
            skLineSegment(sketch, "E14.17.19.16", {"start": v(291.45, 82.55) * mm, "end": v(294.2, 87.31) * mm});
            skLineSegment(sketch, "E14.0.19.17", {"start": v(294.2, 100.01) * mm, "end": v(299.7, 100.01) * mm});
            skLineSegment(sketch, "E14.3.19.17", {"start": v(299.7, 100.01) * mm, "end": v(302.45, 95.25) * mm});
            skLineSegment(sketch, "E14.6.19.17", {"start": v(302.45, 95.25) * mm, "end": v(299.7, 90.49) * mm});
            skCircle(sketch, "E14.9.19.17", {"center": v(296.95, 95.25) * mm, "radius": 4.76 * mm, "construction": true});
            skLineSegment(sketch, "E14.11.19.17", {"start": v(299.7, 90.49) * mm, "end": v(294.2, 90.49) * mm});
            skLineSegment(sketch, "E14.14.19.17", {"start": v(294.2, 90.49) * mm, "end": v(291.45, 95.25) * mm});
            skLineSegment(sketch, "E14.17.19.17", {"start": v(291.45, 95.25) * mm, "end": v(294.2, 100.01) * mm});
            skLineSegment(sketch, "E14.0.19.18", {"start": v(294.2, 112.71) * mm, "end": v(299.7, 112.71) * mm});
            skLineSegment(sketch, "E14.3.19.18", {"start": v(299.7, 112.71) * mm, "end": v(302.45, 107.95) * mm});
            skLineSegment(sketch, "E14.6.19.18", {"start": v(302.45, 107.95) * mm, "end": v(299.7, 103.19) * mm});
            skCircle(sketch, "E14.9.19.18", {"center": v(296.95, 107.95) * mm, "radius": 4.76 * mm, "construction": true});
            skLineSegment(sketch, "E14.11.19.18", {"start": v(299.7, 103.19) * mm, "end": v(294.2, 103.19) * mm});
            skLineSegment(sketch, "E14.14.19.18", {"start": v(294.2, 103.19) * mm, "end": v(291.45, 107.95) * mm});
            skLineSegment(sketch, "E14.17.19.18", {"start": v(291.45, 107.95) * mm, "end": v(294.2, 112.71) * mm});
            skLineSegment(sketch, "E14.0.19.19", {"start": v(294.2, 125.41) * mm, "end": v(299.7, 125.41) * mm});
            skLineSegment(sketch, "E14.3.19.19", {"start": v(299.7, 125.41) * mm, "end": v(302.45, 120.65) * mm});
            skLineSegment(sketch, "E14.6.19.19", {"start": v(302.45, 120.65) * mm, "end": v(299.7, 115.89) * mm});
            skCircle(sketch, "E14.9.19.19", {"center": v(296.95, 120.65) * mm, "radius": 4.76 * mm, "construction": true});
            skLineSegment(sketch, "E14.11.19.19", {"start": v(299.7, 115.89) * mm, "end": v(294.2, 115.89) * mm});
            skLineSegment(sketch, "E14.14.19.19", {"start": v(294.2, 115.89) * mm, "end": v(291.45, 120.65) * mm});
            skLineSegment(sketch, "E14.17.19.19", {"start": v(291.45, 120.65) * mm, "end": v(294.2, 125.41) * mm});
            skCircle(sketch, "E15.0.5.0", {"center": v(0, -114.3) * mm, "radius": 4.76 * mm, "construction": true});
            skLineSegment(sketch, "E15.2.5.0", {"start": v(-5.5, -114.3) * mm, "end": v(-2.75, -109.54) * mm});
            skLineSegment(sketch, "E15.5.5.0", {"start": v(-2.75, -109.54) * mm, "end": v(2.75, -109.54) * mm});
            skLineSegment(sketch, "E15.8.5.0", {"start": v(2.75, -109.54) * mm, "end": v(5.5, -114.3) * mm});
            skLineSegment(sketch, "E15.11.5.0", {"start": v(5.5, -114.3) * mm, "end": v(2.75, -119.06) * mm});
            skLineSegment(sketch, "E15.14.5.0", {"start": v(2.75, -119.06) * mm, "end": v(-2.75, -119.06) * mm});
            skLineSegment(sketch, "E15.17.5.0", {"start": v(-2.75, -119.06) * mm, "end": v(-5.5, -114.3) * mm});
            skCircle(sketch, "E15.0.5.1", {"center": v(0, -101.6) * mm, "radius": 4.76 * mm, "construction": true});
            skLineSegment(sketch, "E15.2.5.1", {"start": v(-5.5, -101.6) * mm, "end": v(-2.75, -96.84) * mm});
            skLineSegment(sketch, "E15.5.5.1", {"start": v(-2.75, -96.84) * mm, "end": v(2.75, -96.84) * mm});
            skLineSegment(sketch, "E15.8.5.1", {"start": v(2.75, -96.84) * mm, "end": v(5.5, -101.6) * mm});
            skLineSegment(sketch, "E15.11.5.1", {"start": v(5.5, -101.6) * mm, "end": v(2.75, -106.36) * mm});
            skLineSegment(sketch, "E15.14.5.1", {"start": v(2.75, -106.36) * mm, "end": v(-2.75, -106.36) * mm});
            skLineSegment(sketch, "E15.17.5.1", {"start": v(-2.75, -106.36) * mm, "end": v(-5.5, -101.6) * mm});
            skCircle(sketch, "E15.0.5.2", {"center": v(0, -88.9) * mm, "radius": 4.76 * mm, "construction": true});
            skLineSegment(sketch, "E15.2.5.2", {"start": v(-5.5, -88.9) * mm, "end": v(-2.75, -84.14) * mm});
            skLineSegment(sketch, "E15.5.5.2", {"start": v(-2.75, -84.14) * mm, "end": v(2.75, -84.14) * mm});
            skLineSegment(sketch, "E15.8.5.2", {"start": v(2.75, -84.14) * mm, "end": v(5.5, -88.9) * mm});
            skLineSegment(sketch, "E15.11.5.2", {"start": v(5.5, -88.9) * mm, "end": v(2.75, -93.66) * mm});
            skLineSegment(sketch, "E15.14.5.2", {"start": v(2.75, -93.66) * mm, "end": v(-2.75, -93.66) * mm});
            skLineSegment(sketch, "E15.17.5.2", {"start": v(-2.75, -93.66) * mm, "end": v(-5.5, -88.9) * mm});
            skCircle(sketch, "E15.0.5.3", {"center": v(0, -76.2) * mm, "radius": 4.76 * mm, "construction": true});
            skLineSegment(sketch, "E15.2.5.3", {"start": v(-5.5, -76.2) * mm, "end": v(-2.75, -71.44) * mm});
            skLineSegment(sketch, "E15.5.5.3", {"start": v(-2.75, -71.44) * mm, "end": v(2.75, -71.44) * mm});
            skLineSegment(sketch, "E15.8.5.3", {"start": v(2.75, -71.44) * mm, "end": v(5.5, -76.2) * mm});
            skLineSegment(sketch, "E15.11.5.3", {"start": v(5.5, -76.2) * mm, "end": v(2.75, -80.96) * mm});
            skLineSegment(sketch, "E15.14.5.3", {"start": v(2.75, -80.96) * mm, "end": v(-2.75, -80.96) * mm});
            skLineSegment(sketch, "E15.17.5.3", {"start": v(-2.75, -80.96) * mm, "end": v(-5.5, -76.2) * mm});
            skCircle(sketch, "E15.0.5.4", {"center": v(0, -63.5) * mm, "radius": 4.76 * mm, "construction": true});
            skLineSegment(sketch, "E15.2.5.4", {"start": v(-5.5, -63.5) * mm, "end": v(-2.75, -58.74) * mm});
            skLineSegment(sketch, "E15.5.5.4", {"start": v(-2.75, -58.74) * mm, "end": v(2.75, -58.74) * mm});
            skLineSegment(sketch, "E15.8.5.4", {"start": v(2.75, -58.74) * mm, "end": v(5.5, -63.5) * mm});
            skLineSegment(sketch, "E15.11.5.4", {"start": v(5.5, -63.5) * mm, "end": v(2.75, -68.26) * mm});
            skLineSegment(sketch, "E15.14.5.4", {"start": v(2.75, -68.26) * mm, "end": v(-2.75, -68.26) * mm});
            skLineSegment(sketch, "E15.17.5.4", {"start": v(-2.75, -68.26) * mm, "end": v(-5.5, -63.5) * mm});
            skCircle(sketch, "E15.0.5.5", {"center": v(0, -50.8) * mm, "radius": 4.76 * mm, "construction": true});
            skLineSegment(sketch, "E15.2.5.5", {"start": v(-5.5, -50.8) * mm, "end": v(-2.75, -46.04) * mm});
            skLineSegment(sketch, "E15.5.5.5", {"start": v(-2.75, -46.04) * mm, "end": v(2.75, -46.04) * mm});
            skLineSegment(sketch, "E15.8.5.5", {"start": v(2.75, -46.04) * mm, "end": v(5.5, -50.8) * mm});
            skLineSegment(sketch, "E15.11.5.5", {"start": v(5.5, -50.8) * mm, "end": v(2.75, -55.56) * mm});
            skLineSegment(sketch, "E15.14.5.5", {"start": v(2.75, -55.56) * mm, "end": v(-2.75, -55.56) * mm});
            skLineSegment(sketch, "E15.17.5.5", {"start": v(-2.75, -55.56) * mm, "end": v(-5.5, -50.8) * mm});
            skCircle(sketch, "E15.0.5.6", {"center": v(0, -38.1) * mm, "radius": 4.76 * mm, "construction": true});
            skLineSegment(sketch, "E15.2.5.6", {"start": v(-5.5, -38.1) * mm, "end": v(-2.75, -33.34) * mm});
            skLineSegment(sketch, "E15.5.5.6", {"start": v(-2.75, -33.34) * mm, "end": v(2.75, -33.34) * mm});
            skLineSegment(sketch, "E15.8.5.6", {"start": v(2.75, -33.34) * mm, "end": v(5.5, -38.1) * mm});
            skLineSegment(sketch, "E15.11.5.6", {"start": v(5.5, -38.1) * mm, "end": v(2.75, -42.86) * mm});
            skLineSegment(sketch, "E15.14.5.6", {"start": v(2.75, -42.86) * mm, "end": v(-2.75, -42.86) * mm});
            skLineSegment(sketch, "E15.17.5.6", {"start": v(-2.75, -42.86) * mm, "end": v(-5.5, -38.1) * mm});
            skCircle(sketch, "E15.0.5.7", {"center": v(0, -25.4) * mm, "radius": 4.76 * mm, "construction": true});
            skLineSegment(sketch, "E15.2.5.7", {"start": v(-5.5, -25.4) * mm, "end": v(-2.75, -20.64) * mm});
            skLineSegment(sketch, "E15.5.5.7", {"start": v(-2.75, -20.64) * mm, "end": v(2.75, -20.64) * mm});
            skLineSegment(sketch, "E15.8.5.7", {"start": v(2.75, -20.64) * mm, "end": v(5.5, -25.4) * mm});
            skLineSegment(sketch, "E15.11.5.7", {"start": v(5.5, -25.4) * mm, "end": v(2.75, -30.16) * mm});
            skLineSegment(sketch, "E15.14.5.7", {"start": v(2.75, -30.16) * mm, "end": v(-2.75, -30.16) * mm});
            skLineSegment(sketch, "E15.17.5.7", {"start": v(-2.75, -30.16) * mm, "end": v(-5.5, -25.4) * mm});
            skCircle(sketch, "E15.0.5.8", {"center": v(0, -12.7) * mm, "radius": 4.76 * mm, "construction": true});
            skLineSegment(sketch, "E15.2.5.8", {"start": v(-5.5, -12.7) * mm, "end": v(-2.75, -7.94) * mm});
            skLineSegment(sketch, "E15.5.5.8", {"start": v(-2.75, -7.94) * mm, "end": v(2.75, -7.94) * mm});
            skLineSegment(sketch, "E15.8.5.8", {"start": v(2.75, -7.94) * mm, "end": v(5.5, -12.7) * mm});
            skLineSegment(sketch, "E15.11.5.8", {"start": v(5.5, -12.7) * mm, "end": v(2.75, -17.46) * mm});
            skLineSegment(sketch, "E15.14.5.8", {"start": v(2.75, -17.46) * mm, "end": v(-2.75, -17.46) * mm});
            skLineSegment(sketch, "E15.17.5.8", {"start": v(-2.75, -17.46) * mm, "end": v(-5.5, -12.7) * mm});
            skCircle(sketch, "E15.0.5.9", {"center": v(0, 0) * mm, "radius": 4.76 * mm, "construction": true});
            skLineSegment(sketch, "E15.2.5.9", {"start": v(-5.5, 0) * mm, "end": v(-2.75, 4.76) * mm});
            skLineSegment(sketch, "E15.5.5.9", {"start": v(-2.75, 4.76) * mm, "end": v(2.75, 4.76) * mm});
            skLineSegment(sketch, "E15.8.5.9", {"start": v(2.75, 4.76) * mm, "end": v(5.5, 0) * mm});
            skLineSegment(sketch, "E15.11.5.9", {"start": v(5.5, 0) * mm, "end": v(2.75, -4.76) * mm});
            skLineSegment(sketch, "E15.14.5.9", {"start": v(2.75, -4.76) * mm, "end": v(-2.75, -4.76) * mm});
            skLineSegment(sketch, "E15.17.5.9", {"start": v(-2.75, -4.76) * mm, "end": v(-5.5, 0) * mm});
            skCircle(sketch, "E15.0.5.10", {"center": v(0, 12.7) * mm, "radius": 4.76 * mm, "construction": true});
            skLineSegment(sketch, "E15.2.5.10", {"start": v(-5.5, 12.7) * mm, "end": v(-2.75, 17.46) * mm});
            skLineSegment(sketch, "E15.5.5.10", {"start": v(-2.75, 17.46) * mm, "end": v(2.75, 17.46) * mm});
            skLineSegment(sketch, "E15.8.5.10", {"start": v(2.75, 17.46) * mm, "end": v(5.5, 12.7) * mm});
            skLineSegment(sketch, "E15.11.5.10", {"start": v(5.5, 12.7) * mm, "end": v(2.75, 7.94) * mm});
            skLineSegment(sketch, "E15.14.5.10", {"start": v(2.75, 7.94) * mm, "end": v(-2.75, 7.94) * mm});
            skLineSegment(sketch, "E15.17.5.10", {"start": v(-2.75, 7.94) * mm, "end": v(-5.5, 12.7) * mm});
            skCircle(sketch, "E15.0.5.11", {"center": v(0, 25.4) * mm, "radius": 4.76 * mm, "construction": true});
            skLineSegment(sketch, "E15.2.5.11", {"start": v(-5.5, 25.4) * mm, "end": v(-2.75, 30.16) * mm});
            skLineSegment(sketch, "E15.5.5.11", {"start": v(-2.75, 30.16) * mm, "end": v(2.75, 30.16) * mm});
            skLineSegment(sketch, "E15.8.5.11", {"start": v(2.75, 30.16) * mm, "end": v(5.5, 25.4) * mm});
            skLineSegment(sketch, "E15.11.5.11", {"start": v(5.5, 25.4) * mm, "end": v(2.75, 20.64) * mm});
            skLineSegment(sketch, "E15.14.5.11", {"start": v(2.75, 20.64) * mm, "end": v(-2.75, 20.64) * mm});
            skLineSegment(sketch, "E15.17.5.11", {"start": v(-2.75, 20.64) * mm, "end": v(-5.5, 25.4) * mm});
            skCircle(sketch, "E15.0.5.12", {"center": v(0, 38.1) * mm, "radius": 4.76 * mm, "construction": true});
            skLineSegment(sketch, "E15.2.5.12", {"start": v(-5.5, 38.1) * mm, "end": v(-2.75, 42.86) * mm});
            skLineSegment(sketch, "E15.5.5.12", {"start": v(-2.75, 42.86) * mm, "end": v(2.75, 42.86) * mm});
            skLineSegment(sketch, "E15.8.5.12", {"start": v(2.75, 42.86) * mm, "end": v(5.5, 38.1) * mm});
            skLineSegment(sketch, "E15.11.5.12", {"start": v(5.5, 38.1) * mm, "end": v(2.75, 33.34) * mm});
            skLineSegment(sketch, "E15.14.5.12", {"start": v(2.75, 33.34) * mm, "end": v(-2.75, 33.34) * mm});
            skLineSegment(sketch, "E15.17.5.12", {"start": v(-2.75, 33.34) * mm, "end": v(-5.5, 38.1) * mm});
            skCircle(sketch, "E15.0.5.13", {"center": v(0, 50.8) * mm, "radius": 4.76 * mm, "construction": true});
            skLineSegment(sketch, "E15.2.5.13", {"start": v(-5.5, 50.8) * mm, "end": v(-2.75, 55.56) * mm});
            skLineSegment(sketch, "E15.5.5.13", {"start": v(-2.75, 55.56) * mm, "end": v(2.75, 55.56) * mm});
            skLineSegment(sketch, "E15.8.5.13", {"start": v(2.75, 55.56) * mm, "end": v(5.5, 50.8) * mm});
            skLineSegment(sketch, "E15.11.5.13", {"start": v(5.5, 50.8) * mm, "end": v(2.75, 46.04) * mm});
            skLineSegment(sketch, "E15.14.5.13", {"start": v(2.75, 46.04) * mm, "end": v(-2.75, 46.04) * mm});
            skLineSegment(sketch, "E15.17.5.13", {"start": v(-2.75, 46.04) * mm, "end": v(-5.5, 50.8) * mm});
            skCircle(sketch, "E15.0.5.14", {"center": v(0, 63.5) * mm, "radius": 4.76 * mm, "construction": true});
            skLineSegment(sketch, "E15.2.5.14", {"start": v(-5.5, 63.5) * mm, "end": v(-2.75, 68.26) * mm});
            skLineSegment(sketch, "E15.5.5.14", {"start": v(-2.75, 68.26) * mm, "end": v(2.75, 68.26) * mm});
            skLineSegment(sketch, "E15.8.5.14", {"start": v(2.75, 68.26) * mm, "end": v(5.5, 63.5) * mm});
            skLineSegment(sketch, "E15.11.5.14", {"start": v(5.5, 63.5) * mm, "end": v(2.75, 58.74) * mm});
            skLineSegment(sketch, "E15.14.5.14", {"start": v(2.75, 58.74) * mm, "end": v(-2.75, 58.74) * mm});
            skLineSegment(sketch, "E15.17.5.14", {"start": v(-2.75, 58.74) * mm, "end": v(-5.5, 63.5) * mm});
            skCircle(sketch, "E15.0.5.15", {"center": v(0, 76.2) * mm, "radius": 4.76 * mm, "construction": true});
            skLineSegment(sketch, "E15.2.5.15", {"start": v(-5.5, 76.2) * mm, "end": v(-2.75, 80.96) * mm});
            skLineSegment(sketch, "E15.5.5.15", {"start": v(-2.75, 80.96) * mm, "end": v(2.75, 80.96) * mm});
            skLineSegment(sketch, "E15.8.5.15", {"start": v(2.75, 80.96) * mm, "end": v(5.5, 76.2) * mm});
            skLineSegment(sketch, "E15.11.5.15", {"start": v(5.5, 76.2) * mm, "end": v(2.75, 71.44) * mm});
            skLineSegment(sketch, "E15.14.5.15", {"start": v(2.75, 71.44) * mm, "end": v(-2.75, 71.44) * mm});
            skLineSegment(sketch, "E15.17.5.15", {"start": v(-2.75, 71.44) * mm, "end": v(-5.5, 76.2) * mm});
            skCircle(sketch, "E15.0.5.16", {"center": v(0, 88.9) * mm, "radius": 4.76 * mm, "construction": true});
            skLineSegment(sketch, "E15.2.5.16", {"start": v(-5.5, 88.9) * mm, "end": v(-2.75, 93.66) * mm});
            skLineSegment(sketch, "E15.5.5.16", {"start": v(-2.75, 93.66) * mm, "end": v(2.75, 93.66) * mm});
            skLineSegment(sketch, "E15.8.5.16", {"start": v(2.75, 93.66) * mm, "end": v(5.5, 88.9) * mm});
            skLineSegment(sketch, "E15.11.5.16", {"start": v(5.5, 88.9) * mm, "end": v(2.75, 84.14) * mm});
            skLineSegment(sketch, "E15.14.5.16", {"start": v(2.75, 84.14) * mm, "end": v(-2.75, 84.14) * mm});
            skLineSegment(sketch, "E15.17.5.16", {"start": v(-2.75, 84.14) * mm, "end": v(-5.5, 88.9) * mm});
            skCircle(sketch, "E15.0.5.17", {"center": v(0, 101.6) * mm, "radius": 4.76 * mm, "construction": true});
            skLineSegment(sketch, "E15.2.5.17", {"start": v(-5.5, 101.6) * mm, "end": v(-2.75, 106.36) * mm});
            skLineSegment(sketch, "E15.5.5.17", {"start": v(-2.75, 106.36) * mm, "end": v(2.75, 106.36) * mm});
            skLineSegment(sketch, "E15.8.5.17", {"start": v(2.75, 106.36) * mm, "end": v(5.5, 101.6) * mm});
            skLineSegment(sketch, "E15.11.5.17", {"start": v(5.5, 101.6) * mm, "end": v(2.75, 96.84) * mm});
            skLineSegment(sketch, "E15.14.5.17", {"start": v(2.75, 96.84) * mm, "end": v(-2.75, 96.84) * mm});
            skLineSegment(sketch, "E15.17.5.17", {"start": v(-2.75, 96.84) * mm, "end": v(-5.5, 101.6) * mm});
            skCircle(sketch, "E15.0.5.18", {"center": v(0, 114.3) * mm, "radius": 4.76 * mm, "construction": true});
            skLineSegment(sketch, "E15.2.5.18", {"start": v(-5.5, 114.3) * mm, "end": v(-2.75, 119.06) * mm});
            skLineSegment(sketch, "E15.5.5.18", {"start": v(-2.75, 119.06) * mm, "end": v(2.75, 119.06) * mm});
            skLineSegment(sketch, "E15.8.5.18", {"start": v(2.75, 119.06) * mm, "end": v(5.5, 114.3) * mm});
            skLineSegment(sketch, "E15.11.5.18", {"start": v(5.5, 114.3) * mm, "end": v(2.75, 109.54) * mm});
            skLineSegment(sketch, "E15.14.5.18", {"start": v(2.75, 109.54) * mm, "end": v(-2.75, 109.54) * mm});
            skLineSegment(sketch, "E15.17.5.18", {"start": v(-2.75, 109.54) * mm, "end": v(-5.5, 114.3) * mm});
            skCircle(sketch, "E15.0.5.19", {"center": v(0, 127) * mm, "radius": 4.76 * mm, "construction": true});
            skLineSegment(sketch, "E15.2.5.19", {"start": v(-5.5, 127) * mm, "end": v(-2.75, 131.76) * mm});
            skLineSegment(sketch, "E15.5.5.19", {"start": v(-2.75, 131.76) * mm, "end": v(2.75, 131.76) * mm});
            skLineSegment(sketch, "E15.8.5.19", {"start": v(2.75, 131.76) * mm, "end": v(5.5, 127) * mm});
            skLineSegment(sketch, "E15.11.5.19", {"start": v(5.5, 127) * mm, "end": v(2.75, 122.24) * mm});
            skLineSegment(sketch, "E15.14.5.19", {"start": v(2.75, 122.24) * mm, "end": v(-2.75, 122.24) * mm});
            skLineSegment(sketch, "E15.17.5.19", {"start": v(-2.75, 122.24) * mm, "end": v(-5.5, 127) * mm});
            skCircle(sketch, "E15.0.6.0", {"center": v(22, -114.3) * mm, "radius": 4.76 * mm, "construction": true});
            skLineSegment(sketch, "E15.2.6.0", {"start": v(16.5, -114.3) * mm, "end": v(19.25, -109.54) * mm});
            skLineSegment(sketch, "E15.5.6.0", {"start": v(19.25, -109.54) * mm, "end": v(24.75, -109.54) * mm});
            skLineSegment(sketch, "E15.8.6.0", {"start": v(24.75, -109.54) * mm, "end": v(27.5, -114.3) * mm});
            skLineSegment(sketch, "E15.11.6.0", {"start": v(27.5, -114.3) * mm, "end": v(24.75, -119.06) * mm});
            skLineSegment(sketch, "E15.14.6.0", {"start": v(24.75, -119.06) * mm, "end": v(19.25, -119.06) * mm});
            skLineSegment(sketch, "E15.17.6.0", {"start": v(19.25, -119.06) * mm, "end": v(16.5, -114.3) * mm});
            skCircle(sketch, "E15.0.6.1", {"center": v(22, -101.6) * mm, "radius": 4.76 * mm, "construction": true});
            skLineSegment(sketch, "E15.2.6.1", {"start": v(16.5, -101.6) * mm, "end": v(19.25, -96.84) * mm});
            skLineSegment(sketch, "E15.5.6.1", {"start": v(19.25, -96.84) * mm, "end": v(24.75, -96.84) * mm});
            skLineSegment(sketch, "E15.8.6.1", {"start": v(24.75, -96.84) * mm, "end": v(27.5, -101.6) * mm});
            skLineSegment(sketch, "E15.11.6.1", {"start": v(27.5, -101.6) * mm, "end": v(24.75, -106.36) * mm});
            skLineSegment(sketch, "E15.14.6.1", {"start": v(24.75, -106.36) * mm, "end": v(19.25, -106.36) * mm});
            skLineSegment(sketch, "E15.17.6.1", {"start": v(19.25, -106.36) * mm, "end": v(16.5, -101.6) * mm});
            skCircle(sketch, "E15.0.6.2", {"center": v(22, -88.9) * mm, "radius": 4.76 * mm, "construction": true});
            skLineSegment(sketch, "E15.2.6.2", {"start": v(16.5, -88.9) * mm, "end": v(19.25, -84.14) * mm});
            skLineSegment(sketch, "E15.5.6.2", {"start": v(19.25, -84.14) * mm, "end": v(24.75, -84.14) * mm});
            skLineSegment(sketch, "E15.8.6.2", {"start": v(24.75, -84.14) * mm, "end": v(27.5, -88.9) * mm});
            skLineSegment(sketch, "E15.11.6.2", {"start": v(27.5, -88.9) * mm, "end": v(24.75, -93.66) * mm});
            skLineSegment(sketch, "E15.14.6.2", {"start": v(24.75, -93.66) * mm, "end": v(19.25, -93.66) * mm});
            skLineSegment(sketch, "E15.17.6.2", {"start": v(19.25, -93.66) * mm, "end": v(16.5, -88.9) * mm});
            skCircle(sketch, "E15.0.6.3", {"center": v(22, -76.2) * mm, "radius": 4.76 * mm, "construction": true});
            skLineSegment(sketch, "E15.2.6.3", {"start": v(16.5, -76.2) * mm, "end": v(19.25, -71.44) * mm});
            skLineSegment(sketch, "E15.5.6.3", {"start": v(19.25, -71.44) * mm, "end": v(24.75, -71.44) * mm});
            skLineSegment(sketch, "E15.8.6.3", {"start": v(24.75, -71.44) * mm, "end": v(27.5, -76.2) * mm});
            skLineSegment(sketch, "E15.11.6.3", {"start": v(27.5, -76.2) * mm, "end": v(24.75, -80.96) * mm});
            skLineSegment(sketch, "E15.14.6.3", {"start": v(24.75, -80.96) * mm, "end": v(19.25, -80.96) * mm});
            skLineSegment(sketch, "E15.17.6.3", {"start": v(19.25, -80.96) * mm, "end": v(16.5, -76.2) * mm});
            skCircle(sketch, "E15.0.6.4", {"center": v(22, -63.5) * mm, "radius": 4.76 * mm, "construction": true});
            skLineSegment(sketch, "E15.2.6.4", {"start": v(16.5, -63.5) * mm, "end": v(19.25, -58.74) * mm});
            skLineSegment(sketch, "E15.5.6.4", {"start": v(19.25, -58.74) * mm, "end": v(24.75, -58.74) * mm});
            skLineSegment(sketch, "E15.8.6.4", {"start": v(24.75, -58.74) * mm, "end": v(27.5, -63.5) * mm});
            skLineSegment(sketch, "E15.11.6.4", {"start": v(27.5, -63.5) * mm, "end": v(24.75, -68.26) * mm});
            skLineSegment(sketch, "E15.14.6.4", {"start": v(24.75, -68.26) * mm, "end": v(19.25, -68.26) * mm});
            skLineSegment(sketch, "E15.17.6.4", {"start": v(19.25, -68.26) * mm, "end": v(16.5, -63.5) * mm});
            skCircle(sketch, "E15.0.6.5", {"center": v(22, -50.8) * mm, "radius": 4.76 * mm, "construction": true});
            skLineSegment(sketch, "E15.2.6.5", {"start": v(16.5, -50.8) * mm, "end": v(19.25, -46.04) * mm});
            skLineSegment(sketch, "E15.5.6.5", {"start": v(19.25, -46.04) * mm, "end": v(24.75, -46.04) * mm});
            skLineSegment(sketch, "E15.8.6.5", {"start": v(24.75, -46.04) * mm, "end": v(27.5, -50.8) * mm});
            skLineSegment(sketch, "E15.11.6.5", {"start": v(27.5, -50.8) * mm, "end": v(24.75, -55.56) * mm});
            skLineSegment(sketch, "E15.14.6.5", {"start": v(24.75, -55.56) * mm, "end": v(19.25, -55.56) * mm});
            skLineSegment(sketch, "E15.17.6.5", {"start": v(19.25, -55.56) * mm, "end": v(16.5, -50.8) * mm});
            skCircle(sketch, "E15.0.6.6", {"center": v(22, -38.1) * mm, "radius": 4.76 * mm, "construction": true});
            skLineSegment(sketch, "E15.2.6.6", {"start": v(16.5, -38.1) * mm, "end": v(19.25, -33.34) * mm});
            skLineSegment(sketch, "E15.5.6.6", {"start": v(19.25, -33.34) * mm, "end": v(24.75, -33.34) * mm});
            skLineSegment(sketch, "E15.8.6.6", {"start": v(24.75, -33.34) * mm, "end": v(27.5, -38.1) * mm});
            skLineSegment(sketch, "E15.11.6.6", {"start": v(27.5, -38.1) * mm, "end": v(24.75, -42.86) * mm});
            skLineSegment(sketch, "E15.14.6.6", {"start": v(24.75, -42.86) * mm, "end": v(19.25, -42.86) * mm});
            skLineSegment(sketch, "E15.17.6.6", {"start": v(19.25, -42.86) * mm, "end": v(16.5, -38.1) * mm});
            skCircle(sketch, "E15.0.6.7", {"center": v(22, -25.4) * mm, "radius": 4.76 * mm, "construction": true});
            skLineSegment(sketch, "E15.2.6.7", {"start": v(16.5, -25.4) * mm, "end": v(19.25, -20.64) * mm});
            skLineSegment(sketch, "E15.5.6.7", {"start": v(19.25, -20.64) * mm, "end": v(24.75, -20.64) * mm});
            skLineSegment(sketch, "E15.8.6.7", {"start": v(24.75, -20.64) * mm, "end": v(27.5, -25.4) * mm});
            skLineSegment(sketch, "E15.11.6.7", {"start": v(27.5, -25.4) * mm, "end": v(24.75, -30.16) * mm});
            skLineSegment(sketch, "E15.14.6.7", {"start": v(24.75, -30.16) * mm, "end": v(19.25, -30.16) * mm});
            skLineSegment(sketch, "E15.17.6.7", {"start": v(19.25, -30.16) * mm, "end": v(16.5, -25.4) * mm});
            skCircle(sketch, "E15.0.6.8", {"center": v(22, -12.7) * mm, "radius": 4.76 * mm, "construction": true});
            skLineSegment(sketch, "E15.2.6.8", {"start": v(16.5, -12.7) * mm, "end": v(19.25, -7.94) * mm});
            skLineSegment(sketch, "E15.5.6.8", {"start": v(19.25, -7.94) * mm, "end": v(24.75, -7.94) * mm});
            skLineSegment(sketch, "E15.8.6.8", {"start": v(24.75, -7.94) * mm, "end": v(27.5, -12.7) * mm});
            skLineSegment(sketch, "E15.11.6.8", {"start": v(27.5, -12.7) * mm, "end": v(24.75, -17.46) * mm});
            skLineSegment(sketch, "E15.14.6.8", {"start": v(24.75, -17.46) * mm, "end": v(19.25, -17.46) * mm});
            skLineSegment(sketch, "E15.17.6.8", {"start": v(19.25, -17.46) * mm, "end": v(16.5, -12.7) * mm});
            skCircle(sketch, "E15.0.6.9", {"center": v(22, 0) * mm, "radius": 4.76 * mm, "construction": true});
            skLineSegment(sketch, "E15.2.6.9", {"start": v(16.5, 0) * mm, "end": v(19.25, 4.76) * mm});
            skLineSegment(sketch, "E15.5.6.9", {"start": v(19.25, 4.76) * mm, "end": v(24.75, 4.76) * mm});
            skLineSegment(sketch, "E15.8.6.9", {"start": v(24.75, 4.76) * mm, "end": v(27.5, 0) * mm});
            skLineSegment(sketch, "E15.11.6.9", {"start": v(27.5, 0) * mm, "end": v(24.75, -4.76) * mm});
            skLineSegment(sketch, "E15.14.6.9", {"start": v(24.75, -4.76) * mm, "end": v(19.25, -4.76) * mm});
            skLineSegment(sketch, "E15.17.6.9", {"start": v(19.25, -4.76) * mm, "end": v(16.5, 0) * mm});
            skCircle(sketch, "E15.0.6.10", {"center": v(22, 12.7) * mm, "radius": 4.76 * mm, "construction": true});
            skLineSegment(sketch, "E15.2.6.10", {"start": v(16.5, 12.7) * mm, "end": v(19.25, 17.46) * mm});
            skLineSegment(sketch, "E15.5.6.10", {"start": v(19.25, 17.46) * mm, "end": v(24.75, 17.46) * mm});
            skLineSegment(sketch, "E15.8.6.10", {"start": v(24.75, 17.46) * mm, "end": v(27.5, 12.7) * mm});
            skLineSegment(sketch, "E15.11.6.10", {"start": v(27.5, 12.7) * mm, "end": v(24.75, 7.94) * mm});
            skLineSegment(sketch, "E15.14.6.10", {"start": v(24.75, 7.94) * mm, "end": v(19.25, 7.94) * mm});
            skLineSegment(sketch, "E15.17.6.10", {"start": v(19.25, 7.94) * mm, "end": v(16.5, 12.7) * mm});
            skCircle(sketch, "E15.0.6.11", {"center": v(22, 25.4) * mm, "radius": 4.76 * mm, "construction": true});
            skLineSegment(sketch, "E15.2.6.11", {"start": v(16.5, 25.4) * mm, "end": v(19.25, 30.16) * mm});
            skLineSegment(sketch, "E15.5.6.11", {"start": v(19.25, 30.16) * mm, "end": v(24.75, 30.16) * mm});
            skLineSegment(sketch, "E15.8.6.11", {"start": v(24.75, 30.16) * mm, "end": v(27.5, 25.4) * mm});
            skLineSegment(sketch, "E15.11.6.11", {"start": v(27.5, 25.4) * mm, "end": v(24.75, 20.64) * mm});
            skLineSegment(sketch, "E15.14.6.11", {"start": v(24.75, 20.64) * mm, "end": v(19.25, 20.64) * mm});
            skLineSegment(sketch, "E15.17.6.11", {"start": v(19.25, 20.64) * mm, "end": v(16.5, 25.4) * mm});
            skCircle(sketch, "E15.0.6.12", {"center": v(22, 38.1) * mm, "radius": 4.76 * mm, "construction": true});
            skLineSegment(sketch, "E15.2.6.12", {"start": v(16.5, 38.1) * mm, "end": v(19.25, 42.86) * mm});
            skLineSegment(sketch, "E15.5.6.12", {"start": v(19.25, 42.86) * mm, "end": v(24.75, 42.86) * mm});
            skLineSegment(sketch, "E15.8.6.12", {"start": v(24.75, 42.86) * mm, "end": v(27.5, 38.1) * mm});
            skLineSegment(sketch, "E15.11.6.12", {"start": v(27.5, 38.1) * mm, "end": v(24.75, 33.34) * mm});
            skLineSegment(sketch, "E15.14.6.12", {"start": v(24.75, 33.34) * mm, "end": v(19.25, 33.34) * mm});
            skLineSegment(sketch, "E15.17.6.12", {"start": v(19.25, 33.34) * mm, "end": v(16.5, 38.1) * mm});
            skCircle(sketch, "E15.0.6.13", {"center": v(22, 50.8) * mm, "radius": 4.76 * mm, "construction": true});
            skLineSegment(sketch, "E15.2.6.13", {"start": v(16.5, 50.8) * mm, "end": v(19.25, 55.56) * mm});
            skLineSegment(sketch, "E15.5.6.13", {"start": v(19.25, 55.56) * mm, "end": v(24.75, 55.56) * mm});
            skLineSegment(sketch, "E15.8.6.13", {"start": v(24.75, 55.56) * mm, "end": v(27.5, 50.8) * mm});
            skLineSegment(sketch, "E15.11.6.13", {"start": v(27.5, 50.8) * mm, "end": v(24.75, 46.04) * mm});
            skLineSegment(sketch, "E15.14.6.13", {"start": v(24.75, 46.04) * mm, "end": v(19.25, 46.04) * mm});
            skLineSegment(sketch, "E15.17.6.13", {"start": v(19.25, 46.04) * mm, "end": v(16.5, 50.8) * mm});
            skCircle(sketch, "E15.0.6.14", {"center": v(22, 63.5) * mm, "radius": 4.76 * mm, "construction": true});
            skLineSegment(sketch, "E15.2.6.14", {"start": v(16.5, 63.5) * mm, "end": v(19.25, 68.26) * mm});
            skLineSegment(sketch, "E15.5.6.14", {"start": v(19.25, 68.26) * mm, "end": v(24.75, 68.26) * mm});
            skLineSegment(sketch, "E15.8.6.14", {"start": v(24.75, 68.26) * mm, "end": v(27.5, 63.5) * mm});
            skLineSegment(sketch, "E15.11.6.14", {"start": v(27.5, 63.5) * mm, "end": v(24.75, 58.74) * mm});
            skLineSegment(sketch, "E15.14.6.14", {"start": v(24.75, 58.74) * mm, "end": v(19.25, 58.74) * mm});
            skLineSegment(sketch, "E15.17.6.14", {"start": v(19.25, 58.74) * mm, "end": v(16.5, 63.5) * mm});
            skCircle(sketch, "E15.0.6.15", {"center": v(22, 76.2) * mm, "radius": 4.76 * mm, "construction": true});
            skLineSegment(sketch, "E15.2.6.15", {"start": v(16.5, 76.2) * mm, "end": v(19.25, 80.96) * mm});
            skLineSegment(sketch, "E15.5.6.15", {"start": v(19.25, 80.96) * mm, "end": v(24.75, 80.96) * mm});
            skLineSegment(sketch, "E15.8.6.15", {"start": v(24.75, 80.96) * mm, "end": v(27.5, 76.2) * mm});
            skLineSegment(sketch, "E15.11.6.15", {"start": v(27.5, 76.2) * mm, "end": v(24.75, 71.44) * mm});
            skLineSegment(sketch, "E15.14.6.15", {"start": v(24.75, 71.44) * mm, "end": v(19.25, 71.44) * mm});
            skLineSegment(sketch, "E15.17.6.15", {"start": v(19.25, 71.44) * mm, "end": v(16.5, 76.2) * mm});
            skCircle(sketch, "E15.0.6.16", {"center": v(22, 88.9) * mm, "radius": 4.76 * mm, "construction": true});
            skLineSegment(sketch, "E15.2.6.16", {"start": v(16.5, 88.9) * mm, "end": v(19.25, 93.66) * mm});
            skLineSegment(sketch, "E15.5.6.16", {"start": v(19.25, 93.66) * mm, "end": v(24.75, 93.66) * mm});
            skLineSegment(sketch, "E15.8.6.16", {"start": v(24.75, 93.66) * mm, "end": v(27.5, 88.9) * mm});
            skLineSegment(sketch, "E15.11.6.16", {"start": v(27.5, 88.9) * mm, "end": v(24.75, 84.14) * mm});
            skLineSegment(sketch, "E15.14.6.16", {"start": v(24.75, 84.14) * mm, "end": v(19.25, 84.14) * mm});
            skLineSegment(sketch, "E15.17.6.16", {"start": v(19.25, 84.14) * mm, "end": v(16.5, 88.9) * mm});
            skCircle(sketch, "E15.0.6.17", {"center": v(22, 101.6) * mm, "radius": 4.76 * mm, "construction": true});
            skLineSegment(sketch, "E15.2.6.17", {"start": v(16.5, 101.6) * mm, "end": v(19.25, 106.36) * mm});
            skLineSegment(sketch, "E15.5.6.17", {"start": v(19.25, 106.36) * mm, "end": v(24.75, 106.36) * mm});
            skLineSegment(sketch, "E15.8.6.17", {"start": v(24.75, 106.36) * mm, "end": v(27.5, 101.6) * mm});
            skLineSegment(sketch, "E15.11.6.17", {"start": v(27.5, 101.6) * mm, "end": v(24.75, 96.84) * mm});
            skLineSegment(sketch, "E15.14.6.17", {"start": v(24.75, 96.84) * mm, "end": v(19.25, 96.84) * mm});
            skLineSegment(sketch, "E15.17.6.17", {"start": v(19.25, 96.84) * mm, "end": v(16.5, 101.6) * mm});
            skCircle(sketch, "E15.0.6.18", {"center": v(22, 114.3) * mm, "radius": 4.76 * mm, "construction": true});
            skLineSegment(sketch, "E15.2.6.18", {"start": v(16.5, 114.3) * mm, "end": v(19.25, 119.06) * mm});
            skLineSegment(sketch, "E15.5.6.18", {"start": v(19.25, 119.06) * mm, "end": v(24.75, 119.06) * mm});
            skLineSegment(sketch, "E15.8.6.18", {"start": v(24.75, 119.06) * mm, "end": v(27.5, 114.3) * mm});
            skLineSegment(sketch, "E15.11.6.18", {"start": v(27.5, 114.3) * mm, "end": v(24.75, 109.54) * mm});
            skLineSegment(sketch, "E15.14.6.18", {"start": v(24.75, 109.54) * mm, "end": v(19.25, 109.54) * mm});
            skLineSegment(sketch, "E15.17.6.18", {"start": v(19.25, 109.54) * mm, "end": v(16.5, 114.3) * mm});
            skCircle(sketch, "E15.0.6.19", {"center": v(22, 127) * mm, "radius": 4.76 * mm, "construction": true});
            skLineSegment(sketch, "E15.2.6.19", {"start": v(16.5, 127) * mm, "end": v(19.25, 131.76) * mm});
            skLineSegment(sketch, "E15.5.6.19", {"start": v(19.25, 131.76) * mm, "end": v(24.75, 131.76) * mm});
            skLineSegment(sketch, "E15.8.6.19", {"start": v(24.75, 131.76) * mm, "end": v(27.5, 127) * mm});
            skLineSegment(sketch, "E15.11.6.19", {"start": v(27.5, 127) * mm, "end": v(24.75, 122.24) * mm});
            skLineSegment(sketch, "E15.14.6.19", {"start": v(24.75, 122.24) * mm, "end": v(19.25, 122.24) * mm});
            skLineSegment(sketch, "E15.17.6.19", {"start": v(19.25, 122.24) * mm, "end": v(16.5, 127) * mm});
            skCircle(sketch, "E15.0.7.0", {"center": v(44, -114.3) * mm, "radius": 4.76 * mm, "construction": true});
            skLineSegment(sketch, "E15.2.7.0", {"start": v(38.5, -114.3) * mm, "end": v(41.24, -109.54) * mm});
            skLineSegment(sketch, "E15.5.7.0", {"start": v(41.24, -109.54) * mm, "end": v(46.74, -109.54) * mm});
            skLineSegment(sketch, "E15.8.7.0", {"start": v(46.74, -109.54) * mm, "end": v(49.5, -114.3) * mm});
            skLineSegment(sketch, "E15.11.7.0", {"start": v(49.5, -114.3) * mm, "end": v(46.74, -119.06) * mm});
            skLineSegment(sketch, "E15.14.7.0", {"start": v(46.74, -119.06) * mm, "end": v(41.24, -119.06) * mm});
            skLineSegment(sketch, "E15.17.7.0", {"start": v(41.24, -119.06) * mm, "end": v(38.5, -114.3) * mm});
            skCircle(sketch, "E15.0.7.1", {"center": v(44, -101.6) * mm, "radius": 4.76 * mm, "construction": true});
            skLineSegment(sketch, "E15.2.7.1", {"start": v(38.5, -101.6) * mm, "end": v(41.24, -96.84) * mm});
            skLineSegment(sketch, "E15.5.7.1", {"start": v(41.24, -96.84) * mm, "end": v(46.74, -96.84) * mm});
            skLineSegment(sketch, "E15.8.7.1", {"start": v(46.74, -96.84) * mm, "end": v(49.5, -101.6) * mm});
            skLineSegment(sketch, "E15.11.7.1", {"start": v(49.5, -101.6) * mm, "end": v(46.74, -106.36) * mm});
            skLineSegment(sketch, "E15.14.7.1", {"start": v(46.74, -106.36) * mm, "end": v(41.24, -106.36) * mm});
            skLineSegment(sketch, "E15.17.7.1", {"start": v(41.24, -106.36) * mm, "end": v(38.5, -101.6) * mm});
            skCircle(sketch, "E15.0.7.2", {"center": v(44, -88.9) * mm, "radius": 4.76 * mm, "construction": true});
            skLineSegment(sketch, "E15.2.7.2", {"start": v(38.5, -88.9) * mm, "end": v(41.24, -84.14) * mm});
            skLineSegment(sketch, "E15.5.7.2", {"start": v(41.24, -84.14) * mm, "end": v(46.74, -84.14) * mm});
            skLineSegment(sketch, "E15.8.7.2", {"start": v(46.74, -84.14) * mm, "end": v(49.5, -88.9) * mm});
            skLineSegment(sketch, "E15.11.7.2", {"start": v(49.5, -88.9) * mm, "end": v(46.74, -93.66) * mm});
            skLineSegment(sketch, "E15.14.7.2", {"start": v(46.74, -93.66) * mm, "end": v(41.24, -93.66) * mm});
            skLineSegment(sketch, "E15.17.7.2", {"start": v(41.24, -93.66) * mm, "end": v(38.5, -88.9) * mm});
            skCircle(sketch, "E15.0.7.3", {"center": v(44, -76.2) * mm, "radius": 4.76 * mm, "construction": true});
            skLineSegment(sketch, "E15.2.7.3", {"start": v(38.5, -76.2) * mm, "end": v(41.24, -71.44) * mm});
            skLineSegment(sketch, "E15.5.7.3", {"start": v(41.24, -71.44) * mm, "end": v(46.74, -71.44) * mm});
            skLineSegment(sketch, "E15.8.7.3", {"start": v(46.74, -71.44) * mm, "end": v(49.5, -76.2) * mm});
            skLineSegment(sketch, "E15.11.7.3", {"start": v(49.5, -76.2) * mm, "end": v(46.74, -80.96) * mm});
            skLineSegment(sketch, "E15.14.7.3", {"start": v(46.74, -80.96) * mm, "end": v(41.24, -80.96) * mm});
            skLineSegment(sketch, "E15.17.7.3", {"start": v(41.24, -80.96) * mm, "end": v(38.5, -76.2) * mm});
            skCircle(sketch, "E15.0.7.4", {"center": v(44, -63.5) * mm, "radius": 4.76 * mm, "construction": true});
            skLineSegment(sketch, "E15.2.7.4", {"start": v(38.5, -63.5) * mm, "end": v(41.24, -58.74) * mm});
            skLineSegment(sketch, "E15.5.7.4", {"start": v(41.24, -58.74) * mm, "end": v(46.74, -58.74) * mm});
            skLineSegment(sketch, "E15.8.7.4", {"start": v(46.74, -58.74) * mm, "end": v(49.5, -63.5) * mm});
            skLineSegment(sketch, "E15.11.7.4", {"start": v(49.5, -63.5) * mm, "end": v(46.74, -68.26) * mm});
            skLineSegment(sketch, "E15.14.7.4", {"start": v(46.74, -68.26) * mm, "end": v(41.24, -68.26) * mm});
            skLineSegment(sketch, "E15.17.7.4", {"start": v(41.24, -68.26) * mm, "end": v(38.5, -63.5) * mm});
            skCircle(sketch, "E15.0.7.5", {"center": v(44, -50.8) * mm, "radius": 4.76 * mm, "construction": true});
            skLineSegment(sketch, "E15.2.7.5", {"start": v(38.5, -50.8) * mm, "end": v(41.24, -46.04) * mm});
            skLineSegment(sketch, "E15.5.7.5", {"start": v(41.24, -46.04) * mm, "end": v(46.74, -46.04) * mm});
            skLineSegment(sketch, "E15.8.7.5", {"start": v(46.74, -46.04) * mm, "end": v(49.5, -50.8) * mm});
            skLineSegment(sketch, "E15.11.7.5", {"start": v(49.5, -50.8) * mm, "end": v(46.74, -55.56) * mm});
            skLineSegment(sketch, "E15.14.7.5", {"start": v(46.74, -55.56) * mm, "end": v(41.24, -55.56) * mm});
            skLineSegment(sketch, "E15.17.7.5", {"start": v(41.24, -55.56) * mm, "end": v(38.5, -50.8) * mm});
            skCircle(sketch, "E15.0.7.6", {"center": v(44, -38.1) * mm, "radius": 4.76 * mm, "construction": true});
            skLineSegment(sketch, "E15.2.7.6", {"start": v(38.5, -38.1) * mm, "end": v(41.24, -33.34) * mm});
            skLineSegment(sketch, "E15.5.7.6", {"start": v(41.24, -33.34) * mm, "end": v(46.74, -33.34) * mm});
            skLineSegment(sketch, "E15.8.7.6", {"start": v(46.74, -33.34) * mm, "end": v(49.5, -38.1) * mm});
            skLineSegment(sketch, "E15.11.7.6", {"start": v(49.5, -38.1) * mm, "end": v(46.74, -42.86) * mm});
            skLineSegment(sketch, "E15.14.7.6", {"start": v(46.74, -42.86) * mm, "end": v(41.24, -42.86) * mm});
            skLineSegment(sketch, "E15.17.7.6", {"start": v(41.24, -42.86) * mm, "end": v(38.5, -38.1) * mm});
            skCircle(sketch, "E15.0.7.7", {"center": v(44, -25.4) * mm, "radius": 4.76 * mm, "construction": true});
            skLineSegment(sketch, "E15.2.7.7", {"start": v(38.5, -25.4) * mm, "end": v(41.24, -20.64) * mm});
            skLineSegment(sketch, "E15.5.7.7", {"start": v(41.24, -20.64) * mm, "end": v(46.74, -20.64) * mm});
            skLineSegment(sketch, "E15.8.7.7", {"start": v(46.74, -20.64) * mm, "end": v(49.5, -25.4) * mm});
            skLineSegment(sketch, "E15.11.7.7", {"start": v(49.5, -25.4) * mm, "end": v(46.74, -30.16) * mm});
            skLineSegment(sketch, "E15.14.7.7", {"start": v(46.74, -30.16) * mm, "end": v(41.24, -30.16) * mm});
            skLineSegment(sketch, "E15.17.7.7", {"start": v(41.24, -30.16) * mm, "end": v(38.5, -25.4) * mm});
            skCircle(sketch, "E15.0.7.8", {"center": v(44, -12.7) * mm, "radius": 4.76 * mm, "construction": true});
            skLineSegment(sketch, "E15.2.7.8", {"start": v(38.5, -12.7) * mm, "end": v(41.24, -7.94) * mm});
            skLineSegment(sketch, "E15.5.7.8", {"start": v(41.24, -7.94) * mm, "end": v(46.74, -7.94) * mm});
            skLineSegment(sketch, "E15.8.7.8", {"start": v(46.74, -7.94) * mm, "end": v(49.5, -12.7) * mm});
            skLineSegment(sketch, "E15.11.7.8", {"start": v(49.5, -12.7) * mm, "end": v(46.74, -17.46) * mm});
            skLineSegment(sketch, "E15.14.7.8", {"start": v(46.74, -17.46) * mm, "end": v(41.24, -17.46) * mm});
            skLineSegment(sketch, "E15.17.7.8", {"start": v(41.24, -17.46) * mm, "end": v(38.5, -12.7) * mm});
            skCircle(sketch, "E15.0.7.9", {"center": v(44, 0) * mm, "radius": 4.76 * mm, "construction": true});
            skLineSegment(sketch, "E15.2.7.9", {"start": v(38.5, 0) * mm, "end": v(41.24, 4.76) * mm});
            skLineSegment(sketch, "E15.5.7.9", {"start": v(41.24, 4.76) * mm, "end": v(46.74, 4.76) * mm});
            skLineSegment(sketch, "E15.8.7.9", {"start": v(46.74, 4.76) * mm, "end": v(49.5, 0) * mm});
            skLineSegment(sketch, "E15.11.7.9", {"start": v(49.5, 0) * mm, "end": v(46.74, -4.76) * mm});
            skLineSegment(sketch, "E15.14.7.9", {"start": v(46.74, -4.76) * mm, "end": v(41.24, -4.76) * mm});
            skLineSegment(sketch, "E15.17.7.9", {"start": v(41.24, -4.76) * mm, "end": v(38.5, 0) * mm});
            skCircle(sketch, "E15.0.7.10", {"center": v(44, 12.7) * mm, "radius": 4.76 * mm, "construction": true});
            skLineSegment(sketch, "E15.2.7.10", {"start": v(38.5, 12.7) * mm, "end": v(41.24, 17.46) * mm});
            skLineSegment(sketch, "E15.5.7.10", {"start": v(41.24, 17.46) * mm, "end": v(46.74, 17.46) * mm});
            skLineSegment(sketch, "E15.8.7.10", {"start": v(46.74, 17.46) * mm, "end": v(49.5, 12.7) * mm});
            skLineSegment(sketch, "E15.11.7.10", {"start": v(49.5, 12.7) * mm, "end": v(46.74, 7.94) * mm});
            skLineSegment(sketch, "E15.14.7.10", {"start": v(46.74, 7.94) * mm, "end": v(41.24, 7.94) * mm});
            skLineSegment(sketch, "E15.17.7.10", {"start": v(41.24, 7.94) * mm, "end": v(38.5, 12.7) * mm});
            skCircle(sketch, "E15.0.7.11", {"center": v(44, 25.4) * mm, "radius": 4.76 * mm, "construction": true});
            skLineSegment(sketch, "E15.2.7.11", {"start": v(38.5, 25.4) * mm, "end": v(41.24, 30.16) * mm});
            skLineSegment(sketch, "E15.5.7.11", {"start": v(41.24, 30.16) * mm, "end": v(46.74, 30.16) * mm});
            skLineSegment(sketch, "E15.8.7.11", {"start": v(46.74, 30.16) * mm, "end": v(49.5, 25.4) * mm});
            skLineSegment(sketch, "E15.11.7.11", {"start": v(49.5, 25.4) * mm, "end": v(46.74, 20.64) * mm});
            skLineSegment(sketch, "E15.14.7.11", {"start": v(46.74, 20.64) * mm, "end": v(41.24, 20.64) * mm});
            skLineSegment(sketch, "E15.17.7.11", {"start": v(41.24, 20.64) * mm, "end": v(38.5, 25.4) * mm});
            skCircle(sketch, "E15.0.7.12", {"center": v(44, 38.1) * mm, "radius": 4.76 * mm, "construction": true});
            skLineSegment(sketch, "E15.2.7.12", {"start": v(38.5, 38.1) * mm, "end": v(41.24, 42.86) * mm});
            skLineSegment(sketch, "E15.5.7.12", {"start": v(41.24, 42.86) * mm, "end": v(46.74, 42.86) * mm});
            skLineSegment(sketch, "E15.8.7.12", {"start": v(46.74, 42.86) * mm, "end": v(49.5, 38.1) * mm});
            skLineSegment(sketch, "E15.11.7.12", {"start": v(49.5, 38.1) * mm, "end": v(46.74, 33.34) * mm});
            skLineSegment(sketch, "E15.14.7.12", {"start": v(46.74, 33.34) * mm, "end": v(41.24, 33.34) * mm});
            skLineSegment(sketch, "E15.17.7.12", {"start": v(41.24, 33.34) * mm, "end": v(38.5, 38.1) * mm});
            skCircle(sketch, "E15.0.7.13", {"center": v(44, 50.8) * mm, "radius": 4.76 * mm, "construction": true});
            skLineSegment(sketch, "E15.2.7.13", {"start": v(38.5, 50.8) * mm, "end": v(41.24, 55.56) * mm});
            skLineSegment(sketch, "E15.5.7.13", {"start": v(41.24, 55.56) * mm, "end": v(46.74, 55.56) * mm});
            skLineSegment(sketch, "E15.8.7.13", {"start": v(46.74, 55.56) * mm, "end": v(49.5, 50.8) * mm});
            skLineSegment(sketch, "E15.11.7.13", {"start": v(49.5, 50.8) * mm, "end": v(46.74, 46.04) * mm});
            skLineSegment(sketch, "E15.14.7.13", {"start": v(46.74, 46.04) * mm, "end": v(41.24, 46.04) * mm});
            skLineSegment(sketch, "E15.17.7.13", {"start": v(41.24, 46.04) * mm, "end": v(38.5, 50.8) * mm});
            skCircle(sketch, "E15.0.7.14", {"center": v(44, 63.5) * mm, "radius": 4.76 * mm, "construction": true});
            skLineSegment(sketch, "E15.2.7.14", {"start": v(38.5, 63.5) * mm, "end": v(41.24, 68.26) * mm});
            skLineSegment(sketch, "E15.5.7.14", {"start": v(41.24, 68.26) * mm, "end": v(46.74, 68.26) * mm});
            skLineSegment(sketch, "E15.8.7.14", {"start": v(46.74, 68.26) * mm, "end": v(49.5, 63.5) * mm});
            skLineSegment(sketch, "E15.11.7.14", {"start": v(49.5, 63.5) * mm, "end": v(46.74, 58.74) * mm});
            skLineSegment(sketch, "E15.14.7.14", {"start": v(46.74, 58.74) * mm, "end": v(41.24, 58.74) * mm});
            skLineSegment(sketch, "E15.17.7.14", {"start": v(41.24, 58.74) * mm, "end": v(38.5, 63.5) * mm});
            skCircle(sketch, "E15.0.7.15", {"center": v(44, 76.2) * mm, "radius": 4.76 * mm, "construction": true});
            skLineSegment(sketch, "E15.2.7.15", {"start": v(38.5, 76.2) * mm, "end": v(41.24, 80.96) * mm});
            skLineSegment(sketch, "E15.5.7.15", {"start": v(41.24, 80.96) * mm, "end": v(46.74, 80.96) * mm});
            skLineSegment(sketch, "E15.8.7.15", {"start": v(46.74, 80.96) * mm, "end": v(49.5, 76.2) * mm});
            skLineSegment(sketch, "E15.11.7.15", {"start": v(49.5, 76.2) * mm, "end": v(46.74, 71.44) * mm});
            skLineSegment(sketch, "E15.14.7.15", {"start": v(46.74, 71.44) * mm, "end": v(41.24, 71.44) * mm});
            skLineSegment(sketch, "E15.17.7.15", {"start": v(41.24, 71.44) * mm, "end": v(38.5, 76.2) * mm});
            skCircle(sketch, "E15.0.7.16", {"center": v(44, 88.9) * mm, "radius": 4.76 * mm, "construction": true});
            skLineSegment(sketch, "E15.2.7.16", {"start": v(38.5, 88.9) * mm, "end": v(41.24, 93.66) * mm});
            skLineSegment(sketch, "E15.5.7.16", {"start": v(41.24, 93.66) * mm, "end": v(46.74, 93.66) * mm});
            skLineSegment(sketch, "E15.8.7.16", {"start": v(46.74, 93.66) * mm, "end": v(49.5, 88.9) * mm});
            skLineSegment(sketch, "E15.11.7.16", {"start": v(49.5, 88.9) * mm, "end": v(46.74, 84.14) * mm});
            skLineSegment(sketch, "E15.14.7.16", {"start": v(46.74, 84.14) * mm, "end": v(41.24, 84.14) * mm});
            skLineSegment(sketch, "E15.17.7.16", {"start": v(41.24, 84.14) * mm, "end": v(38.5, 88.9) * mm});
            skCircle(sketch, "E15.0.7.17", {"center": v(44, 101.6) * mm, "radius": 4.76 * mm, "construction": true});
            skLineSegment(sketch, "E15.2.7.17", {"start": v(38.5, 101.6) * mm, "end": v(41.24, 106.36) * mm});
            skLineSegment(sketch, "E15.5.7.17", {"start": v(41.24, 106.36) * mm, "end": v(46.74, 106.36) * mm});
            skLineSegment(sketch, "E15.8.7.17", {"start": v(46.74, 106.36) * mm, "end": v(49.5, 101.6) * mm});
            skLineSegment(sketch, "E15.11.7.17", {"start": v(49.5, 101.6) * mm, "end": v(46.74, 96.84) * mm});
            skLineSegment(sketch, "E15.14.7.17", {"start": v(46.74, 96.84) * mm, "end": v(41.24, 96.84) * mm});
            skLineSegment(sketch, "E15.17.7.17", {"start": v(41.24, 96.84) * mm, "end": v(38.5, 101.6) * mm});
            skCircle(sketch, "E15.0.7.18", {"center": v(44, 114.3) * mm, "radius": 4.76 * mm, "construction": true});
            skLineSegment(sketch, "E15.2.7.18", {"start": v(38.5, 114.3) * mm, "end": v(41.24, 119.06) * mm});
            skLineSegment(sketch, "E15.5.7.18", {"start": v(41.24, 119.06) * mm, "end": v(46.74, 119.06) * mm});
            skLineSegment(sketch, "E15.8.7.18", {"start": v(46.74, 119.06) * mm, "end": v(49.5, 114.3) * mm});
            skLineSegment(sketch, "E15.11.7.18", {"start": v(49.5, 114.3) * mm, "end": v(46.74, 109.54) * mm});
            skLineSegment(sketch, "E15.14.7.18", {"start": v(46.74, 109.54) * mm, "end": v(41.24, 109.54) * mm});
            skLineSegment(sketch, "E15.17.7.18", {"start": v(41.24, 109.54) * mm, "end": v(38.5, 114.3) * mm});
            skCircle(sketch, "E15.0.7.19", {"center": v(44, 127) * mm, "radius": 4.76 * mm, "construction": true});
            skLineSegment(sketch, "E15.2.7.19", {"start": v(38.5, 127) * mm, "end": v(41.24, 131.76) * mm});
            skLineSegment(sketch, "E15.5.7.19", {"start": v(41.24, 131.76) * mm, "end": v(46.74, 131.76) * mm});
            skLineSegment(sketch, "E15.8.7.19", {"start": v(46.74, 131.76) * mm, "end": v(49.5, 127) * mm});
            skLineSegment(sketch, "E15.11.7.19", {"start": v(49.5, 127) * mm, "end": v(46.74, 122.24) * mm});
            skLineSegment(sketch, "E15.14.7.19", {"start": v(46.74, 122.24) * mm, "end": v(41.24, 122.24) * mm});
            skLineSegment(sketch, "E15.17.7.19", {"start": v(41.24, 122.24) * mm, "end": v(38.5, 127) * mm});
            skCircle(sketch, "E15.0.8.0", {"center": v(65.99, -114.3) * mm, "radius": 4.76 * mm, "construction": true});
            skLineSegment(sketch, "E15.2.8.0", {"start": v(60.49, -114.3) * mm, "end": v(63.24, -109.54) * mm});
            skLineSegment(sketch, "E15.5.8.0", {"start": v(63.24, -109.54) * mm, "end": v(68.74, -109.54) * mm});
            skLineSegment(sketch, "E15.8.8.0", {"start": v(68.74, -109.54) * mm, "end": v(71.49, -114.3) * mm});
            skLineSegment(sketch, "E15.11.8.0", {"start": v(71.49, -114.3) * mm, "end": v(68.74, -119.06) * mm});
            skLineSegment(sketch, "E15.14.8.0", {"start": v(68.74, -119.06) * mm, "end": v(63.24, -119.06) * mm});
            skLineSegment(sketch, "E15.17.8.0", {"start": v(63.24, -119.06) * mm, "end": v(60.49, -114.3) * mm});
            skCircle(sketch, "E15.0.8.1", {"center": v(65.99, -101.6) * mm, "radius": 4.76 * mm, "construction": true});
            skLineSegment(sketch, "E15.2.8.1", {"start": v(60.49, -101.6) * mm, "end": v(63.24, -96.84) * mm});
            skLineSegment(sketch, "E15.5.8.1", {"start": v(63.24, -96.84) * mm, "end": v(68.74, -96.84) * mm});
            skLineSegment(sketch, "E15.8.8.1", {"start": v(68.74, -96.84) * mm, "end": v(71.49, -101.6) * mm});
            skLineSegment(sketch, "E15.11.8.1", {"start": v(71.49, -101.6) * mm, "end": v(68.74, -106.36) * mm});
            skLineSegment(sketch, "E15.14.8.1", {"start": v(68.74, -106.36) * mm, "end": v(63.24, -106.36) * mm});
            skLineSegment(sketch, "E15.17.8.1", {"start": v(63.24, -106.36) * mm, "end": v(60.49, -101.6) * mm});
            skCircle(sketch, "E15.0.8.2", {"center": v(65.99, -88.9) * mm, "radius": 4.76 * mm, "construction": true});
            skLineSegment(sketch, "E15.2.8.2", {"start": v(60.49, -88.9) * mm, "end": v(63.24, -84.14) * mm});
            skLineSegment(sketch, "E15.5.8.2", {"start": v(63.24, -84.14) * mm, "end": v(68.74, -84.14) * mm});
            skLineSegment(sketch, "E15.8.8.2", {"start": v(68.74, -84.14) * mm, "end": v(71.49, -88.9) * mm});
            skLineSegment(sketch, "E15.11.8.2", {"start": v(71.49, -88.9) * mm, "end": v(68.74, -93.66) * mm});
            skLineSegment(sketch, "E15.14.8.2", {"start": v(68.74, -93.66) * mm, "end": v(63.24, -93.66) * mm});
            skLineSegment(sketch, "E15.17.8.2", {"start": v(63.24, -93.66) * mm, "end": v(60.49, -88.9) * mm});
            skCircle(sketch, "E15.0.8.3", {"center": v(65.99, -76.2) * mm, "radius": 4.76 * mm, "construction": true});
            skLineSegment(sketch, "E15.2.8.3", {"start": v(60.49, -76.2) * mm, "end": v(63.24, -71.44) * mm});
            skLineSegment(sketch, "E15.5.8.3", {"start": v(63.24, -71.44) * mm, "end": v(68.74, -71.44) * mm});
            skLineSegment(sketch, "E15.8.8.3", {"start": v(68.74, -71.44) * mm, "end": v(71.49, -76.2) * mm});
            skLineSegment(sketch, "E15.11.8.3", {"start": v(71.49, -76.2) * mm, "end": v(68.74, -80.96) * mm});
            skLineSegment(sketch, "E15.14.8.3", {"start": v(68.74, -80.96) * mm, "end": v(63.24, -80.96) * mm});
            skLineSegment(sketch, "E15.17.8.3", {"start": v(63.24, -80.96) * mm, "end": v(60.49, -76.2) * mm});
            skCircle(sketch, "E15.0.8.4", {"center": v(65.99, -63.5) * mm, "radius": 4.76 * mm, "construction": true});
            skLineSegment(sketch, "E15.2.8.4", {"start": v(60.49, -63.5) * mm, "end": v(63.24, -58.74) * mm});
            skLineSegment(sketch, "E15.5.8.4", {"start": v(63.24, -58.74) * mm, "end": v(68.74, -58.74) * mm});
            skLineSegment(sketch, "E15.8.8.4", {"start": v(68.74, -58.74) * mm, "end": v(71.49, -63.5) * mm});
            skLineSegment(sketch, "E15.11.8.4", {"start": v(71.49, -63.5) * mm, "end": v(68.74, -68.26) * mm});
            skLineSegment(sketch, "E15.14.8.4", {"start": v(68.74, -68.26) * mm, "end": v(63.24, -68.26) * mm});
            skLineSegment(sketch, "E15.17.8.4", {"start": v(63.24, -68.26) * mm, "end": v(60.49, -63.5) * mm});
            skCircle(sketch, "E15.0.8.5", {"center": v(65.99, -50.8) * mm, "radius": 4.76 * mm, "construction": true});
            skLineSegment(sketch, "E15.2.8.5", {"start": v(60.49, -50.8) * mm, "end": v(63.24, -46.04) * mm});
            skLineSegment(sketch, "E15.5.8.5", {"start": v(63.24, -46.04) * mm, "end": v(68.74, -46.04) * mm});
            skLineSegment(sketch, "E15.8.8.5", {"start": v(68.74, -46.04) * mm, "end": v(71.49, -50.8) * mm});
            skLineSegment(sketch, "E15.11.8.5", {"start": v(71.49, -50.8) * mm, "end": v(68.74, -55.56) * mm});
            skLineSegment(sketch, "E15.14.8.5", {"start": v(68.74, -55.56) * mm, "end": v(63.24, -55.56) * mm});
            skLineSegment(sketch, "E15.17.8.5", {"start": v(63.24, -55.56) * mm, "end": v(60.49, -50.8) * mm});
            skCircle(sketch, "E15.0.8.6", {"center": v(65.99, -38.1) * mm, "radius": 4.76 * mm, "construction": true});
            skLineSegment(sketch, "E15.2.8.6", {"start": v(60.49, -38.1) * mm, "end": v(63.24, -33.34) * mm});
            skLineSegment(sketch, "E15.5.8.6", {"start": v(63.24, -33.34) * mm, "end": v(68.74, -33.34) * mm});
            skLineSegment(sketch, "E15.8.8.6", {"start": v(68.74, -33.34) * mm, "end": v(71.49, -38.1) * mm});
            skLineSegment(sketch, "E15.11.8.6", {"start": v(71.49, -38.1) * mm, "end": v(68.74, -42.86) * mm});
            skLineSegment(sketch, "E15.14.8.6", {"start": v(68.74, -42.86) * mm, "end": v(63.24, -42.86) * mm});
            skLineSegment(sketch, "E15.17.8.6", {"start": v(63.24, -42.86) * mm, "end": v(60.49, -38.1) * mm});
            skCircle(sketch, "E15.0.8.7", {"center": v(65.99, -25.4) * mm, "radius": 4.76 * mm, "construction": true});
            skLineSegment(sketch, "E15.2.8.7", {"start": v(60.49, -25.4) * mm, "end": v(63.24, -20.64) * mm});
            skLineSegment(sketch, "E15.5.8.7", {"start": v(63.24, -20.64) * mm, "end": v(68.74, -20.64) * mm});
            skLineSegment(sketch, "E15.8.8.7", {"start": v(68.74, -20.64) * mm, "end": v(71.49, -25.4) * mm});
            skLineSegment(sketch, "E15.11.8.7", {"start": v(71.49, -25.4) * mm, "end": v(68.74, -30.16) * mm});
            skLineSegment(sketch, "E15.14.8.7", {"start": v(68.74, -30.16) * mm, "end": v(63.24, -30.16) * mm});
            skLineSegment(sketch, "E15.17.8.7", {"start": v(63.24, -30.16) * mm, "end": v(60.49, -25.4) * mm});
            skCircle(sketch, "E15.0.8.8", {"center": v(65.99, -12.7) * mm, "radius": 4.76 * mm, "construction": true});
            skLineSegment(sketch, "E15.2.8.8", {"start": v(60.49, -12.7) * mm, "end": v(63.24, -7.94) * mm});
            skLineSegment(sketch, "E15.5.8.8", {"start": v(63.24, -7.94) * mm, "end": v(68.74, -7.94) * mm});
            skLineSegment(sketch, "E15.8.8.8", {"start": v(68.74, -7.94) * mm, "end": v(71.49, -12.7) * mm});
            skLineSegment(sketch, "E15.11.8.8", {"start": v(71.49, -12.7) * mm, "end": v(68.74, -17.46) * mm});
            skLineSegment(sketch, "E15.14.8.8", {"start": v(68.74, -17.46) * mm, "end": v(63.24, -17.46) * mm});
            skLineSegment(sketch, "E15.17.8.8", {"start": v(63.24, -17.46) * mm, "end": v(60.49, -12.7) * mm});
            skCircle(sketch, "E15.0.8.9", {"center": v(65.99, 0) * mm, "radius": 4.76 * mm, "construction": true});
            skLineSegment(sketch, "E15.2.8.9", {"start": v(60.49, 0) * mm, "end": v(63.24, 4.76) * mm});
            skLineSegment(sketch, "E15.5.8.9", {"start": v(63.24, 4.76) * mm, "end": v(68.74, 4.76) * mm});
            skLineSegment(sketch, "E15.8.8.9", {"start": v(68.74, 4.76) * mm, "end": v(71.49, 0) * mm});
            skLineSegment(sketch, "E15.11.8.9", {"start": v(71.49, 0) * mm, "end": v(68.74, -4.76) * mm});
            skLineSegment(sketch, "E15.14.8.9", {"start": v(68.74, -4.76) * mm, "end": v(63.24, -4.76) * mm});
            skLineSegment(sketch, "E15.17.8.9", {"start": v(63.24, -4.76) * mm, "end": v(60.49, 0) * mm});
            skCircle(sketch, "E15.0.8.10", {"center": v(65.99, 12.7) * mm, "radius": 4.76 * mm, "construction": true});
            skLineSegment(sketch, "E15.2.8.10", {"start": v(60.49, 12.7) * mm, "end": v(63.24, 17.46) * mm});
            skLineSegment(sketch, "E15.5.8.10", {"start": v(63.24, 17.46) * mm, "end": v(68.74, 17.46) * mm});
            skLineSegment(sketch, "E15.8.8.10", {"start": v(68.74, 17.46) * mm, "end": v(71.49, 12.7) * mm});
            skLineSegment(sketch, "E15.11.8.10", {"start": v(71.49, 12.7) * mm, "end": v(68.74, 7.94) * mm});
            skLineSegment(sketch, "E15.14.8.10", {"start": v(68.74, 7.94) * mm, "end": v(63.24, 7.94) * mm});
            skLineSegment(sketch, "E15.17.8.10", {"start": v(63.24, 7.94) * mm, "end": v(60.49, 12.7) * mm});
            skCircle(sketch, "E15.0.8.11", {"center": v(65.99, 25.4) * mm, "radius": 4.76 * mm, "construction": true});
            skLineSegment(sketch, "E15.2.8.11", {"start": v(60.49, 25.4) * mm, "end": v(63.24, 30.16) * mm});
            skLineSegment(sketch, "E15.5.8.11", {"start": v(63.24, 30.16) * mm, "end": v(68.74, 30.16) * mm});
            skLineSegment(sketch, "E15.8.8.11", {"start": v(68.74, 30.16) * mm, "end": v(71.49, 25.4) * mm});
            skLineSegment(sketch, "E15.11.8.11", {"start": v(71.49, 25.4) * mm, "end": v(68.74, 20.64) * mm});
            skLineSegment(sketch, "E15.14.8.11", {"start": v(68.74, 20.64) * mm, "end": v(63.24, 20.64) * mm});
            skLineSegment(sketch, "E15.17.8.11", {"start": v(63.24, 20.64) * mm, "end": v(60.49, 25.4) * mm});
            skCircle(sketch, "E15.0.8.12", {"center": v(65.99, 38.1) * mm, "radius": 4.76 * mm, "construction": true});
            skLineSegment(sketch, "E15.2.8.12", {"start": v(60.49, 38.1) * mm, "end": v(63.24, 42.86) * mm});
            skLineSegment(sketch, "E15.5.8.12", {"start": v(63.24, 42.86) * mm, "end": v(68.74, 42.86) * mm});
            skLineSegment(sketch, "E15.8.8.12", {"start": v(68.74, 42.86) * mm, "end": v(71.49, 38.1) * mm});
            skLineSegment(sketch, "E15.11.8.12", {"start": v(71.49, 38.1) * mm, "end": v(68.74, 33.34) * mm});
            skLineSegment(sketch, "E15.14.8.12", {"start": v(68.74, 33.34) * mm, "end": v(63.24, 33.34) * mm});
            skLineSegment(sketch, "E15.17.8.12", {"start": v(63.24, 33.34) * mm, "end": v(60.49, 38.1) * mm});
            skCircle(sketch, "E15.0.8.13", {"center": v(65.99, 50.8) * mm, "radius": 4.76 * mm, "construction": true});
            skLineSegment(sketch, "E15.2.8.13", {"start": v(60.49, 50.8) * mm, "end": v(63.24, 55.56) * mm});
            skLineSegment(sketch, "E15.5.8.13", {"start": v(63.24, 55.56) * mm, "end": v(68.74, 55.56) * mm});
            skLineSegment(sketch, "E15.8.8.13", {"start": v(68.74, 55.56) * mm, "end": v(71.49, 50.8) * mm});
            skLineSegment(sketch, "E15.11.8.13", {"start": v(71.49, 50.8) * mm, "end": v(68.74, 46.04) * mm});
            skLineSegment(sketch, "E15.14.8.13", {"start": v(68.74, 46.04) * mm, "end": v(63.24, 46.04) * mm});
            skLineSegment(sketch, "E15.17.8.13", {"start": v(63.24, 46.04) * mm, "end": v(60.49, 50.8) * mm});
            skCircle(sketch, "E15.0.8.14", {"center": v(65.99, 63.5) * mm, "radius": 4.76 * mm, "construction": true});
            skLineSegment(sketch, "E15.2.8.14", {"start": v(60.49, 63.5) * mm, "end": v(63.24, 68.26) * mm});
            skLineSegment(sketch, "E15.5.8.14", {"start": v(63.24, 68.26) * mm, "end": v(68.74, 68.26) * mm});
            skLineSegment(sketch, "E15.8.8.14", {"start": v(68.74, 68.26) * mm, "end": v(71.49, 63.5) * mm});
            skLineSegment(sketch, "E15.11.8.14", {"start": v(71.49, 63.5) * mm, "end": v(68.74, 58.74) * mm});
            skLineSegment(sketch, "E15.14.8.14", {"start": v(68.74, 58.74) * mm, "end": v(63.24, 58.74) * mm});
            skLineSegment(sketch, "E15.17.8.14", {"start": v(63.24, 58.74) * mm, "end": v(60.49, 63.5) * mm});
            skCircle(sketch, "E15.0.8.15", {"center": v(65.99, 76.2) * mm, "radius": 4.76 * mm, "construction": true});
            skLineSegment(sketch, "E15.2.8.15", {"start": v(60.49, 76.2) * mm, "end": v(63.24, 80.96) * mm});
            skLineSegment(sketch, "E15.5.8.15", {"start": v(63.24, 80.96) * mm, "end": v(68.74, 80.96) * mm});
            skLineSegment(sketch, "E15.8.8.15", {"start": v(68.74, 80.96) * mm, "end": v(71.49, 76.2) * mm});
            skLineSegment(sketch, "E15.11.8.15", {"start": v(71.49, 76.2) * mm, "end": v(68.74, 71.44) * mm});
            skLineSegment(sketch, "E15.14.8.15", {"start": v(68.74, 71.44) * mm, "end": v(63.24, 71.44) * mm});
            skLineSegment(sketch, "E15.17.8.15", {"start": v(63.24, 71.44) * mm, "end": v(60.49, 76.2) * mm});
            skCircle(sketch, "E15.0.8.16", {"center": v(65.99, 88.9) * mm, "radius": 4.76 * mm, "construction": true});
            skLineSegment(sketch, "E15.2.8.16", {"start": v(60.49, 88.9) * mm, "end": v(63.24, 93.66) * mm});
            skLineSegment(sketch, "E15.5.8.16", {"start": v(63.24, 93.66) * mm, "end": v(68.74, 93.66) * mm});
            skLineSegment(sketch, "E15.8.8.16", {"start": v(68.74, 93.66) * mm, "end": v(71.49, 88.9) * mm});
            skLineSegment(sketch, "E15.11.8.16", {"start": v(71.49, 88.9) * mm, "end": v(68.74, 84.14) * mm});
            skLineSegment(sketch, "E15.14.8.16", {"start": v(68.74, 84.14) * mm, "end": v(63.24, 84.14) * mm});
            skLineSegment(sketch, "E15.17.8.16", {"start": v(63.24, 84.14) * mm, "end": v(60.49, 88.9) * mm});
            skCircle(sketch, "E15.0.8.17", {"center": v(65.99, 101.6) * mm, "radius": 4.76 * mm, "construction": true});
            skLineSegment(sketch, "E15.2.8.17", {"start": v(60.49, 101.6) * mm, "end": v(63.24, 106.36) * mm});
            skLineSegment(sketch, "E15.5.8.17", {"start": v(63.24, 106.36) * mm, "end": v(68.74, 106.36) * mm});
            skLineSegment(sketch, "E15.8.8.17", {"start": v(68.74, 106.36) * mm, "end": v(71.49, 101.6) * mm});
            skLineSegment(sketch, "E15.11.8.17", {"start": v(71.49, 101.6) * mm, "end": v(68.74, 96.84) * mm});
            skLineSegment(sketch, "E15.14.8.17", {"start": v(68.74, 96.84) * mm, "end": v(63.24, 96.84) * mm});
            skLineSegment(sketch, "E15.17.8.17", {"start": v(63.24, 96.84) * mm, "end": v(60.49, 101.6) * mm});
            skCircle(sketch, "E15.0.8.18", {"center": v(65.99, 114.3) * mm, "radius": 4.76 * mm, "construction": true});
            skLineSegment(sketch, "E15.2.8.18", {"start": v(60.49, 114.3) * mm, "end": v(63.24, 119.06) * mm});
            skLineSegment(sketch, "E15.5.8.18", {"start": v(63.24, 119.06) * mm, "end": v(68.74, 119.06) * mm});
            skLineSegment(sketch, "E15.8.8.18", {"start": v(68.74, 119.06) * mm, "end": v(71.49, 114.3) * mm});
            skLineSegment(sketch, "E15.11.8.18", {"start": v(71.49, 114.3) * mm, "end": v(68.74, 109.54) * mm});
            skLineSegment(sketch, "E15.14.8.18", {"start": v(68.74, 109.54) * mm, "end": v(63.24, 109.54) * mm});
            skLineSegment(sketch, "E15.17.8.18", {"start": v(63.24, 109.54) * mm, "end": v(60.49, 114.3) * mm});
            skCircle(sketch, "E15.0.8.19", {"center": v(65.99, 127) * mm, "radius": 4.76 * mm, "construction": true});
            skLineSegment(sketch, "E15.2.8.19", {"start": v(60.49, 127) * mm, "end": v(63.24, 131.76) * mm});
            skLineSegment(sketch, "E15.5.8.19", {"start": v(63.24, 131.76) * mm, "end": v(68.74, 131.76) * mm});
            skLineSegment(sketch, "E15.8.8.19", {"start": v(68.74, 131.76) * mm, "end": v(71.49, 127) * mm});
            skLineSegment(sketch, "E15.11.8.19", {"start": v(71.49, 127) * mm, "end": v(68.74, 122.24) * mm});
            skLineSegment(sketch, "E15.14.8.19", {"start": v(68.74, 122.24) * mm, "end": v(63.24, 122.24) * mm});
            skLineSegment(sketch, "E15.17.8.19", {"start": v(63.24, 122.24) * mm, "end": v(60.49, 127) * mm});
            skCircle(sketch, "E15.0.9.0", {"center": v(87.99, -114.3) * mm, "radius": 4.76 * mm, "construction": true});
            skLineSegment(sketch, "E15.2.9.0", {"start": v(82.49, -114.3) * mm, "end": v(85.24, -109.54) * mm});
            skLineSegment(sketch, "E15.5.9.0", {"start": v(85.24, -109.54) * mm, "end": v(90.74, -109.54) * mm});
            skLineSegment(sketch, "E15.8.9.0", {"start": v(90.74, -109.54) * mm, "end": v(93.48, -114.3) * mm});
            skLineSegment(sketch, "E15.11.9.0", {"start": v(93.48, -114.3) * mm, "end": v(90.74, -119.06) * mm});
            skLineSegment(sketch, "E15.14.9.0", {"start": v(90.74, -119.06) * mm, "end": v(85.24, -119.06) * mm});
            skLineSegment(sketch, "E15.17.9.0", {"start": v(85.24, -119.06) * mm, "end": v(82.49, -114.3) * mm});
            skCircle(sketch, "E15.0.9.1", {"center": v(87.99, -101.6) * mm, "radius": 4.76 * mm, "construction": true});
            skLineSegment(sketch, "E15.2.9.1", {"start": v(82.49, -101.6) * mm, "end": v(85.24, -96.84) * mm});
            skLineSegment(sketch, "E15.5.9.1", {"start": v(85.24, -96.84) * mm, "end": v(90.74, -96.84) * mm});
            skLineSegment(sketch, "E15.8.9.1", {"start": v(90.74, -96.84) * mm, "end": v(93.48, -101.6) * mm});
            skLineSegment(sketch, "E15.11.9.1", {"start": v(93.48, -101.6) * mm, "end": v(90.74, -106.36) * mm});
            skLineSegment(sketch, "E15.14.9.1", {"start": v(90.74, -106.36) * mm, "end": v(85.24, -106.36) * mm});
            skLineSegment(sketch, "E15.17.9.1", {"start": v(85.24, -106.36) * mm, "end": v(82.49, -101.6) * mm});
            skCircle(sketch, "E15.0.9.2", {"center": v(87.99, -88.9) * mm, "radius": 4.76 * mm, "construction": true});
            skLineSegment(sketch, "E15.2.9.2", {"start": v(82.49, -88.9) * mm, "end": v(85.24, -84.14) * mm});
            skLineSegment(sketch, "E15.5.9.2", {"start": v(85.24, -84.14) * mm, "end": v(90.74, -84.14) * mm});
            skLineSegment(sketch, "E15.8.9.2", {"start": v(90.74, -84.14) * mm, "end": v(93.48, -88.9) * mm});
            skLineSegment(sketch, "E15.11.9.2", {"start": v(93.48, -88.9) * mm, "end": v(90.74, -93.66) * mm});
            skLineSegment(sketch, "E15.14.9.2", {"start": v(90.74, -93.66) * mm, "end": v(85.24, -93.66) * mm});
            skLineSegment(sketch, "E15.17.9.2", {"start": v(85.24, -93.66) * mm, "end": v(82.49, -88.9) * mm});
            skCircle(sketch, "E15.0.9.3", {"center": v(87.99, -76.2) * mm, "radius": 4.76 * mm, "construction": true});
            skLineSegment(sketch, "E15.2.9.3", {"start": v(82.49, -76.2) * mm, "end": v(85.24, -71.44) * mm});
            skLineSegment(sketch, "E15.5.9.3", {"start": v(85.24, -71.44) * mm, "end": v(90.74, -71.44) * mm});
            skLineSegment(sketch, "E15.8.9.3", {"start": v(90.74, -71.44) * mm, "end": v(93.48, -76.2) * mm});
            skLineSegment(sketch, "E15.11.9.3", {"start": v(93.48, -76.2) * mm, "end": v(90.74, -80.96) * mm});
            skLineSegment(sketch, "E15.14.9.3", {"start": v(90.74, -80.96) * mm, "end": v(85.24, -80.96) * mm});
            skLineSegment(sketch, "E15.17.9.3", {"start": v(85.24, -80.96) * mm, "end": v(82.49, -76.2) * mm});
            skCircle(sketch, "E15.0.9.4", {"center": v(87.99, -63.5) * mm, "radius": 4.76 * mm, "construction": true});
            skLineSegment(sketch, "E15.2.9.4", {"start": v(82.49, -63.5) * mm, "end": v(85.24, -58.74) * mm});
            skLineSegment(sketch, "E15.5.9.4", {"start": v(85.24, -58.74) * mm, "end": v(90.74, -58.74) * mm});
            skLineSegment(sketch, "E15.8.9.4", {"start": v(90.74, -58.74) * mm, "end": v(93.48, -63.5) * mm});
            skLineSegment(sketch, "E15.11.9.4", {"start": v(93.48, -63.5) * mm, "end": v(90.74, -68.26) * mm});
            skLineSegment(sketch, "E15.14.9.4", {"start": v(90.74, -68.26) * mm, "end": v(85.24, -68.26) * mm});
            skLineSegment(sketch, "E15.17.9.4", {"start": v(85.24, -68.26) * mm, "end": v(82.49, -63.5) * mm});
            skCircle(sketch, "E15.0.9.5", {"center": v(87.99, -50.8) * mm, "radius": 4.76 * mm, "construction": true});
            skLineSegment(sketch, "E15.2.9.5", {"start": v(82.49, -50.8) * mm, "end": v(85.24, -46.04) * mm});
            skLineSegment(sketch, "E15.5.9.5", {"start": v(85.24, -46.04) * mm, "end": v(90.74, -46.04) * mm});
            skLineSegment(sketch, "E15.8.9.5", {"start": v(90.74, -46.04) * mm, "end": v(93.48, -50.8) * mm});
            skLineSegment(sketch, "E15.11.9.5", {"start": v(93.48, -50.8) * mm, "end": v(90.74, -55.56) * mm});
            skLineSegment(sketch, "E15.14.9.5", {"start": v(90.74, -55.56) * mm, "end": v(85.24, -55.56) * mm});
            skLineSegment(sketch, "E15.17.9.5", {"start": v(85.24, -55.56) * mm, "end": v(82.49, -50.8) * mm});
            skCircle(sketch, "E15.0.9.6", {"center": v(87.99, -38.1) * mm, "radius": 4.76 * mm, "construction": true});
            skLineSegment(sketch, "E15.2.9.6", {"start": v(82.49, -38.1) * mm, "end": v(85.24, -33.34) * mm});
            skLineSegment(sketch, "E15.5.9.6", {"start": v(85.24, -33.34) * mm, "end": v(90.74, -33.34) * mm});
            skLineSegment(sketch, "E15.8.9.6", {"start": v(90.74, -33.34) * mm, "end": v(93.48, -38.1) * mm});
            skLineSegment(sketch, "E15.11.9.6", {"start": v(93.48, -38.1) * mm, "end": v(90.74, -42.86) * mm});
            skLineSegment(sketch, "E15.14.9.6", {"start": v(90.74, -42.86) * mm, "end": v(85.24, -42.86) * mm});
            skLineSegment(sketch, "E15.17.9.6", {"start": v(85.24, -42.86) * mm, "end": v(82.49, -38.1) * mm});
            skCircle(sketch, "E15.0.9.7", {"center": v(87.99, -25.4) * mm, "radius": 4.76 * mm, "construction": true});
            skLineSegment(sketch, "E15.2.9.7", {"start": v(82.49, -25.4) * mm, "end": v(85.24, -20.64) * mm});
            skLineSegment(sketch, "E15.5.9.7", {"start": v(85.24, -20.64) * mm, "end": v(90.74, -20.64) * mm});
            skLineSegment(sketch, "E15.8.9.7", {"start": v(90.74, -20.64) * mm, "end": v(93.48, -25.4) * mm});
            skLineSegment(sketch, "E15.11.9.7", {"start": v(93.48, -25.4) * mm, "end": v(90.74, -30.16) * mm});
            skLineSegment(sketch, "E15.14.9.7", {"start": v(90.74, -30.16) * mm, "end": v(85.24, -30.16) * mm});
            skLineSegment(sketch, "E15.17.9.7", {"start": v(85.24, -30.16) * mm, "end": v(82.49, -25.4) * mm});
            skCircle(sketch, "E15.0.9.8", {"center": v(87.99, -12.7) * mm, "radius": 4.76 * mm, "construction": true});
            skLineSegment(sketch, "E15.2.9.8", {"start": v(82.49, -12.7) * mm, "end": v(85.24, -7.94) * mm});
            skLineSegment(sketch, "E15.5.9.8", {"start": v(85.24, -7.94) * mm, "end": v(90.74, -7.94) * mm});
            skLineSegment(sketch, "E15.8.9.8", {"start": v(90.74, -7.94) * mm, "end": v(93.48, -12.7) * mm});
            skLineSegment(sketch, "E15.11.9.8", {"start": v(93.48, -12.7) * mm, "end": v(90.74, -17.46) * mm});
            skLineSegment(sketch, "E15.14.9.8", {"start": v(90.74, -17.46) * mm, "end": v(85.24, -17.46) * mm});
            skLineSegment(sketch, "E15.17.9.8", {"start": v(85.24, -17.46) * mm, "end": v(82.49, -12.7) * mm});
            skCircle(sketch, "E15.0.9.9", {"center": v(87.99, 0) * mm, "radius": 4.76 * mm, "construction": true});
            skLineSegment(sketch, "E15.2.9.9", {"start": v(82.49, 0) * mm, "end": v(85.24, 4.76) * mm});
            skLineSegment(sketch, "E15.5.9.9", {"start": v(85.24, 4.76) * mm, "end": v(90.74, 4.76) * mm});
            skLineSegment(sketch, "E15.8.9.9", {"start": v(90.74, 4.76) * mm, "end": v(93.48, 0) * mm});
            skLineSegment(sketch, "E15.11.9.9", {"start": v(93.48, 0) * mm, "end": v(90.74, -4.76) * mm});
            skLineSegment(sketch, "E15.14.9.9", {"start": v(90.74, -4.76) * mm, "end": v(85.24, -4.76) * mm});
            skLineSegment(sketch, "E15.17.9.9", {"start": v(85.24, -4.76) * mm, "end": v(82.49, 0) * mm});
            skCircle(sketch, "E15.0.9.10", {"center": v(87.99, 12.7) * mm, "radius": 4.76 * mm, "construction": true});
            skLineSegment(sketch, "E15.2.9.10", {"start": v(82.49, 12.7) * mm, "end": v(85.24, 17.46) * mm});
            skLineSegment(sketch, "E15.5.9.10", {"start": v(85.24, 17.46) * mm, "end": v(90.74, 17.46) * mm});
            skLineSegment(sketch, "E15.8.9.10", {"start": v(90.74, 17.46) * mm, "end": v(93.48, 12.7) * mm});
            skLineSegment(sketch, "E15.11.9.10", {"start": v(93.48, 12.7) * mm, "end": v(90.74, 7.94) * mm});
            skLineSegment(sketch, "E15.14.9.10", {"start": v(90.74, 7.94) * mm, "end": v(85.24, 7.94) * mm});
            skLineSegment(sketch, "E15.17.9.10", {"start": v(85.24, 7.94) * mm, "end": v(82.49, 12.7) * mm});
            skCircle(sketch, "E15.0.9.11", {"center": v(87.99, 25.4) * mm, "radius": 4.76 * mm, "construction": true});
            skLineSegment(sketch, "E15.2.9.11", {"start": v(82.49, 25.4) * mm, "end": v(85.24, 30.16) * mm});
            skLineSegment(sketch, "E15.5.9.11", {"start": v(85.24, 30.16) * mm, "end": v(90.74, 30.16) * mm});
            skLineSegment(sketch, "E15.8.9.11", {"start": v(90.74, 30.16) * mm, "end": v(93.48, 25.4) * mm});
            skLineSegment(sketch, "E15.11.9.11", {"start": v(93.48, 25.4) * mm, "end": v(90.74, 20.64) * mm});
            skLineSegment(sketch, "E15.14.9.11", {"start": v(90.74, 20.64) * mm, "end": v(85.24, 20.64) * mm});
            skLineSegment(sketch, "E15.17.9.11", {"start": v(85.24, 20.64) * mm, "end": v(82.49, 25.4) * mm});
            skCircle(sketch, "E15.0.9.12", {"center": v(87.99, 38.1) * mm, "radius": 4.76 * mm, "construction": true});
            skLineSegment(sketch, "E15.2.9.12", {"start": v(82.49, 38.1) * mm, "end": v(85.24, 42.86) * mm});
            skLineSegment(sketch, "E15.5.9.12", {"start": v(85.24, 42.86) * mm, "end": v(90.74, 42.86) * mm});
            skLineSegment(sketch, "E15.8.9.12", {"start": v(90.74, 42.86) * mm, "end": v(93.48, 38.1) * mm});
            skLineSegment(sketch, "E15.11.9.12", {"start": v(93.48, 38.1) * mm, "end": v(90.74, 33.34) * mm});
            skLineSegment(sketch, "E15.14.9.12", {"start": v(90.74, 33.34) * mm, "end": v(85.24, 33.34) * mm});
            skLineSegment(sketch, "E15.17.9.12", {"start": v(85.24, 33.34) * mm, "end": v(82.49, 38.1) * mm});
            skCircle(sketch, "E15.0.9.13", {"center": v(87.99, 50.8) * mm, "radius": 4.76 * mm, "construction": true});
            skLineSegment(sketch, "E15.2.9.13", {"start": v(82.49, 50.8) * mm, "end": v(85.24, 55.56) * mm});
            skLineSegment(sketch, "E15.5.9.13", {"start": v(85.24, 55.56) * mm, "end": v(90.74, 55.56) * mm});
            skLineSegment(sketch, "E15.8.9.13", {"start": v(90.74, 55.56) * mm, "end": v(93.48, 50.8) * mm});
            skLineSegment(sketch, "E15.11.9.13", {"start": v(93.48, 50.8) * mm, "end": v(90.74, 46.04) * mm});
            skLineSegment(sketch, "E15.14.9.13", {"start": v(90.74, 46.04) * mm, "end": v(85.24, 46.04) * mm});
            skLineSegment(sketch, "E15.17.9.13", {"start": v(85.24, 46.04) * mm, "end": v(82.49, 50.8) * mm});
            skCircle(sketch, "E15.0.9.14", {"center": v(87.99, 63.5) * mm, "radius": 4.76 * mm, "construction": true});
            skLineSegment(sketch, "E15.2.9.14", {"start": v(82.49, 63.5) * mm, "end": v(85.24, 68.26) * mm});
            skLineSegment(sketch, "E15.5.9.14", {"start": v(85.24, 68.26) * mm, "end": v(90.74, 68.26) * mm});
            skLineSegment(sketch, "E15.8.9.14", {"start": v(90.74, 68.26) * mm, "end": v(93.48, 63.5) * mm});
            skLineSegment(sketch, "E15.11.9.14", {"start": v(93.48, 63.5) * mm, "end": v(90.74, 58.74) * mm});
            skLineSegment(sketch, "E15.14.9.14", {"start": v(90.74, 58.74) * mm, "end": v(85.24, 58.74) * mm});
            skLineSegment(sketch, "E15.17.9.14", {"start": v(85.24, 58.74) * mm, "end": v(82.49, 63.5) * mm});
            skCircle(sketch, "E15.0.9.15", {"center": v(87.99, 76.2) * mm, "radius": 4.76 * mm, "construction": true});
            skLineSegment(sketch, "E15.2.9.15", {"start": v(82.49, 76.2) * mm, "end": v(85.24, 80.96) * mm});
            skLineSegment(sketch, "E15.5.9.15", {"start": v(85.24, 80.96) * mm, "end": v(90.74, 80.96) * mm});
            skLineSegment(sketch, "E15.8.9.15", {"start": v(90.74, 80.96) * mm, "end": v(93.48, 76.2) * mm});
            skLineSegment(sketch, "E15.11.9.15", {"start": v(93.48, 76.2) * mm, "end": v(90.74, 71.44) * mm});
            skLineSegment(sketch, "E15.14.9.15", {"start": v(90.74, 71.44) * mm, "end": v(85.24, 71.44) * mm});
            skLineSegment(sketch, "E15.17.9.15", {"start": v(85.24, 71.44) * mm, "end": v(82.49, 76.2) * mm});
            skCircle(sketch, "E15.0.9.16", {"center": v(87.99, 88.9) * mm, "radius": 4.76 * mm, "construction": true});
            skLineSegment(sketch, "E15.2.9.16", {"start": v(82.49, 88.9) * mm, "end": v(85.24, 93.66) * mm});
            skLineSegment(sketch, "E15.5.9.16", {"start": v(85.24, 93.66) * mm, "end": v(90.74, 93.66) * mm});
            skLineSegment(sketch, "E15.8.9.16", {"start": v(90.74, 93.66) * mm, "end": v(93.48, 88.9) * mm});
            skLineSegment(sketch, "E15.11.9.16", {"start": v(93.48, 88.9) * mm, "end": v(90.74, 84.14) * mm});
            skLineSegment(sketch, "E15.14.9.16", {"start": v(90.74, 84.14) * mm, "end": v(85.24, 84.14) * mm});
            skLineSegment(sketch, "E15.17.9.16", {"start": v(85.24, 84.14) * mm, "end": v(82.49, 88.9) * mm});
            skCircle(sketch, "E15.0.9.17", {"center": v(87.99, 101.6) * mm, "radius": 4.76 * mm, "construction": true});
            skLineSegment(sketch, "E15.2.9.17", {"start": v(82.49, 101.6) * mm, "end": v(85.24, 106.36) * mm});
            skLineSegment(sketch, "E15.5.9.17", {"start": v(85.24, 106.36) * mm, "end": v(90.74, 106.36) * mm});
            skLineSegment(sketch, "E15.8.9.17", {"start": v(90.74, 106.36) * mm, "end": v(93.48, 101.6) * mm});
            skLineSegment(sketch, "E15.11.9.17", {"start": v(93.48, 101.6) * mm, "end": v(90.74, 96.84) * mm});
            skLineSegment(sketch, "E15.14.9.17", {"start": v(90.74, 96.84) * mm, "end": v(85.24, 96.84) * mm});
            skLineSegment(sketch, "E15.17.9.17", {"start": v(85.24, 96.84) * mm, "end": v(82.49, 101.6) * mm});
            skCircle(sketch, "E15.0.9.18", {"center": v(87.99, 114.3) * mm, "radius": 4.76 * mm, "construction": true});
            skLineSegment(sketch, "E15.2.9.18", {"start": v(82.49, 114.3) * mm, "end": v(85.24, 119.06) * mm});
            skLineSegment(sketch, "E15.5.9.18", {"start": v(85.24, 119.06) * mm, "end": v(90.74, 119.06) * mm});
            skLineSegment(sketch, "E15.8.9.18", {"start": v(90.74, 119.06) * mm, "end": v(93.48, 114.3) * mm});
            skLineSegment(sketch, "E15.11.9.18", {"start": v(93.48, 114.3) * mm, "end": v(90.74, 109.54) * mm});
            skLineSegment(sketch, "E15.14.9.18", {"start": v(90.74, 109.54) * mm, "end": v(85.24, 109.54) * mm});
            skLineSegment(sketch, "E15.17.9.18", {"start": v(85.24, 109.54) * mm, "end": v(82.49, 114.3) * mm});
            skCircle(sketch, "E15.0.9.19", {"center": v(87.99, 127) * mm, "radius": 4.76 * mm, "construction": true});
            skLineSegment(sketch, "E15.2.9.19", {"start": v(82.49, 127) * mm, "end": v(85.24, 131.76) * mm});
            skLineSegment(sketch, "E15.5.9.19", {"start": v(85.24, 131.76) * mm, "end": v(90.74, 131.76) * mm});
            skLineSegment(sketch, "E15.8.9.19", {"start": v(90.74, 131.76) * mm, "end": v(93.48, 127) * mm});
            skLineSegment(sketch, "E15.11.9.19", {"start": v(93.48, 127) * mm, "end": v(90.74, 122.24) * mm});
            skLineSegment(sketch, "E15.14.9.19", {"start": v(90.74, 122.24) * mm, "end": v(85.24, 122.24) * mm});
            skLineSegment(sketch, "E15.17.9.19", {"start": v(85.24, 122.24) * mm, "end": v(82.49, 127) * mm});
            skCircle(sketch, "E15.0.10.0", {"center": v(109.98, -114.3) * mm, "radius": 4.76 * mm, "construction": true});
            skLineSegment(sketch, "E15.2.10.0", {"start": v(104.48, -114.3) * mm, "end": v(107.23, -109.54) * mm});
            skLineSegment(sketch, "E15.5.10.0", {"start": v(107.23, -109.54) * mm, "end": v(112.73, -109.54) * mm});
            skLineSegment(sketch, "E15.8.10.0", {"start": v(112.73, -109.54) * mm, "end": v(115.48, -114.3) * mm});
            skLineSegment(sketch, "E15.11.10.0", {"start": v(115.48, -114.3) * mm, "end": v(112.73, -119.06) * mm});
            skLineSegment(sketch, "E15.14.10.0", {"start": v(112.73, -119.06) * mm, "end": v(107.23, -119.06) * mm});
            skLineSegment(sketch, "E15.17.10.0", {"start": v(107.23, -119.06) * mm, "end": v(104.48, -114.3) * mm});
            skCircle(sketch, "E15.0.10.1", {"center": v(109.98, -101.6) * mm, "radius": 4.76 * mm, "construction": true});
            skLineSegment(sketch, "E15.2.10.1", {"start": v(104.48, -101.6) * mm, "end": v(107.23, -96.84) * mm});
            skLineSegment(sketch, "E15.5.10.1", {"start": v(107.23, -96.84) * mm, "end": v(112.73, -96.84) * mm});
            skLineSegment(sketch, "E15.8.10.1", {"start": v(112.73, -96.84) * mm, "end": v(115.48, -101.6) * mm});
            skLineSegment(sketch, "E15.11.10.1", {"start": v(115.48, -101.6) * mm, "end": v(112.73, -106.36) * mm});
            skLineSegment(sketch, "E15.14.10.1", {"start": v(112.73, -106.36) * mm, "end": v(107.23, -106.36) * mm});
            skLineSegment(sketch, "E15.17.10.1", {"start": v(107.23, -106.36) * mm, "end": v(104.48, -101.6) * mm});
            skCircle(sketch, "E15.0.10.2", {"center": v(109.98, -88.9) * mm, "radius": 4.76 * mm, "construction": true});
            skLineSegment(sketch, "E15.2.10.2", {"start": v(104.48, -88.9) * mm, "end": v(107.23, -84.14) * mm});
            skLineSegment(sketch, "E15.5.10.2", {"start": v(107.23, -84.14) * mm, "end": v(112.73, -84.14) * mm});
            skLineSegment(sketch, "E15.8.10.2", {"start": v(112.73, -84.14) * mm, "end": v(115.48, -88.9) * mm});
            skLineSegment(sketch, "E15.11.10.2", {"start": v(115.48, -88.9) * mm, "end": v(112.73, -93.66) * mm});
            skLineSegment(sketch, "E15.14.10.2", {"start": v(112.73, -93.66) * mm, "end": v(107.23, -93.66) * mm});
            skLineSegment(sketch, "E15.17.10.2", {"start": v(107.23, -93.66) * mm, "end": v(104.48, -88.9) * mm});
            skCircle(sketch, "E15.0.10.3", {"center": v(109.98, -76.2) * mm, "radius": 4.76 * mm, "construction": true});
            skLineSegment(sketch, "E15.2.10.3", {"start": v(104.48, -76.2) * mm, "end": v(107.23, -71.44) * mm});
            skLineSegment(sketch, "E15.5.10.3", {"start": v(107.23, -71.44) * mm, "end": v(112.73, -71.44) * mm});
            skLineSegment(sketch, "E15.8.10.3", {"start": v(112.73, -71.44) * mm, "end": v(115.48, -76.2) * mm});
            skLineSegment(sketch, "E15.11.10.3", {"start": v(115.48, -76.2) * mm, "end": v(112.73, -80.96) * mm});
            skLineSegment(sketch, "E15.14.10.3", {"start": v(112.73, -80.96) * mm, "end": v(107.23, -80.96) * mm});
            skLineSegment(sketch, "E15.17.10.3", {"start": v(107.23, -80.96) * mm, "end": v(104.48, -76.2) * mm});
            skCircle(sketch, "E15.0.10.4", {"center": v(109.98, -63.5) * mm, "radius": 4.76 * mm, "construction": true});
            skLineSegment(sketch, "E15.2.10.4", {"start": v(104.48, -63.5) * mm, "end": v(107.23, -58.74) * mm});
            skLineSegment(sketch, "E15.5.10.4", {"start": v(107.23, -58.74) * mm, "end": v(112.73, -58.74) * mm});
            skLineSegment(sketch, "E15.8.10.4", {"start": v(112.73, -58.74) * mm, "end": v(115.48, -63.5) * mm});
            skLineSegment(sketch, "E15.11.10.4", {"start": v(115.48, -63.5) * mm, "end": v(112.73, -68.26) * mm});
            skLineSegment(sketch, "E15.14.10.4", {"start": v(112.73, -68.26) * mm, "end": v(107.23, -68.26) * mm});
            skLineSegment(sketch, "E15.17.10.4", {"start": v(107.23, -68.26) * mm, "end": v(104.48, -63.5) * mm});
            skCircle(sketch, "E15.0.10.5", {"center": v(109.98, -50.8) * mm, "radius": 4.76 * mm, "construction": true});
            skLineSegment(sketch, "E15.2.10.5", {"start": v(104.48, -50.8) * mm, "end": v(107.23, -46.04) * mm});
            skLineSegment(sketch, "E15.5.10.5", {"start": v(107.23, -46.04) * mm, "end": v(112.73, -46.04) * mm});
            skLineSegment(sketch, "E15.8.10.5", {"start": v(112.73, -46.04) * mm, "end": v(115.48, -50.8) * mm});
            skLineSegment(sketch, "E15.11.10.5", {"start": v(115.48, -50.8) * mm, "end": v(112.73, -55.56) * mm});
            skLineSegment(sketch, "E15.14.10.5", {"start": v(112.73, -55.56) * mm, "end": v(107.23, -55.56) * mm});
            skLineSegment(sketch, "E15.17.10.5", {"start": v(107.23, -55.56) * mm, "end": v(104.48, -50.8) * mm});
            skCircle(sketch, "E15.0.10.6", {"center": v(109.98, -38.1) * mm, "radius": 4.76 * mm, "construction": true});
            skLineSegment(sketch, "E15.2.10.6", {"start": v(104.48, -38.1) * mm, "end": v(107.23, -33.34) * mm});
            skLineSegment(sketch, "E15.5.10.6", {"start": v(107.23, -33.34) * mm, "end": v(112.73, -33.34) * mm});
            skLineSegment(sketch, "E15.8.10.6", {"start": v(112.73, -33.34) * mm, "end": v(115.48, -38.1) * mm});
            skLineSegment(sketch, "E15.11.10.6", {"start": v(115.48, -38.1) * mm, "end": v(112.73, -42.86) * mm});
            skLineSegment(sketch, "E15.14.10.6", {"start": v(112.73, -42.86) * mm, "end": v(107.23, -42.86) * mm});
            skLineSegment(sketch, "E15.17.10.6", {"start": v(107.23, -42.86) * mm, "end": v(104.48, -38.1) * mm});
            skCircle(sketch, "E15.0.10.7", {"center": v(109.98, -25.4) * mm, "radius": 4.76 * mm, "construction": true});
            skLineSegment(sketch, "E15.2.10.7", {"start": v(104.48, -25.4) * mm, "end": v(107.23, -20.64) * mm});
            skLineSegment(sketch, "E15.5.10.7", {"start": v(107.23, -20.64) * mm, "end": v(112.73, -20.64) * mm});
            skLineSegment(sketch, "E15.8.10.7", {"start": v(112.73, -20.64) * mm, "end": v(115.48, -25.4) * mm});
            skLineSegment(sketch, "E15.11.10.7", {"start": v(115.48, -25.4) * mm, "end": v(112.73, -30.16) * mm});
            skLineSegment(sketch, "E15.14.10.7", {"start": v(112.73, -30.16) * mm, "end": v(107.23, -30.16) * mm});
            skLineSegment(sketch, "E15.17.10.7", {"start": v(107.23, -30.16) * mm, "end": v(104.48, -25.4) * mm});
            skCircle(sketch, "E15.0.10.8", {"center": v(109.98, -12.7) * mm, "radius": 4.76 * mm, "construction": true});
            skLineSegment(sketch, "E15.2.10.8", {"start": v(104.48, -12.7) * mm, "end": v(107.23, -7.94) * mm});
            skLineSegment(sketch, "E15.5.10.8", {"start": v(107.23, -7.94) * mm, "end": v(112.73, -7.94) * mm});
            skLineSegment(sketch, "E15.8.10.8", {"start": v(112.73, -7.94) * mm, "end": v(115.48, -12.7) * mm});
            skLineSegment(sketch, "E15.11.10.8", {"start": v(115.48, -12.7) * mm, "end": v(112.73, -17.46) * mm});
            skLineSegment(sketch, "E15.14.10.8", {"start": v(112.73, -17.46) * mm, "end": v(107.23, -17.46) * mm});
            skLineSegment(sketch, "E15.17.10.8", {"start": v(107.23, -17.46) * mm, "end": v(104.48, -12.7) * mm});
            skCircle(sketch, "E15.0.10.9", {"center": v(109.98, 0) * mm, "radius": 4.76 * mm, "construction": true});
            skLineSegment(sketch, "E15.2.10.9", {"start": v(104.48, 0) * mm, "end": v(107.23, 4.76) * mm});
            skLineSegment(sketch, "E15.5.10.9", {"start": v(107.23, 4.76) * mm, "end": v(112.73, 4.76) * mm});
            skLineSegment(sketch, "E15.8.10.9", {"start": v(112.73, 4.76) * mm, "end": v(115.48, 0) * mm});
            skLineSegment(sketch, "E15.11.10.9", {"start": v(115.48, 0) * mm, "end": v(112.73, -4.76) * mm});
            skLineSegment(sketch, "E15.14.10.9", {"start": v(112.73, -4.76) * mm, "end": v(107.23, -4.76) * mm});
            skLineSegment(sketch, "E15.17.10.9", {"start": v(107.23, -4.76) * mm, "end": v(104.48, 0) * mm});
            skCircle(sketch, "E15.0.10.10", {"center": v(109.98, 12.7) * mm, "radius": 4.76 * mm, "construction": true});
            skLineSegment(sketch, "E15.2.10.10", {"start": v(104.48, 12.7) * mm, "end": v(107.23, 17.46) * mm});
            skLineSegment(sketch, "E15.5.10.10", {"start": v(107.23, 17.46) * mm, "end": v(112.73, 17.46) * mm});
            skLineSegment(sketch, "E15.8.10.10", {"start": v(112.73, 17.46) * mm, "end": v(115.48, 12.7) * mm});
            skLineSegment(sketch, "E15.11.10.10", {"start": v(115.48, 12.7) * mm, "end": v(112.73, 7.94) * mm});
            skLineSegment(sketch, "E15.14.10.10", {"start": v(112.73, 7.94) * mm, "end": v(107.23, 7.94) * mm});
            skLineSegment(sketch, "E15.17.10.10", {"start": v(107.23, 7.94) * mm, "end": v(104.48, 12.7) * mm});
            skCircle(sketch, "E15.0.10.11", {"center": v(109.98, 25.4) * mm, "radius": 4.76 * mm, "construction": true});
            skLineSegment(sketch, "E15.2.10.11", {"start": v(104.48, 25.4) * mm, "end": v(107.23, 30.16) * mm});
            skLineSegment(sketch, "E15.5.10.11", {"start": v(107.23, 30.16) * mm, "end": v(112.73, 30.16) * mm});
            skLineSegment(sketch, "E15.8.10.11", {"start": v(112.73, 30.16) * mm, "end": v(115.48, 25.4) * mm});
            skLineSegment(sketch, "E15.11.10.11", {"start": v(115.48, 25.4) * mm, "end": v(112.73, 20.64) * mm});
            skLineSegment(sketch, "E15.14.10.11", {"start": v(112.73, 20.64) * mm, "end": v(107.23, 20.64) * mm});
            skLineSegment(sketch, "E15.17.10.11", {"start": v(107.23, 20.64) * mm, "end": v(104.48, 25.4) * mm});
            skCircle(sketch, "E15.0.10.12", {"center": v(109.98, 38.1) * mm, "radius": 4.76 * mm, "construction": true});
            skLineSegment(sketch, "E15.2.10.12", {"start": v(104.48, 38.1) * mm, "end": v(107.23, 42.86) * mm});
            skLineSegment(sketch, "E15.5.10.12", {"start": v(107.23, 42.86) * mm, "end": v(112.73, 42.86) * mm});
            skLineSegment(sketch, "E15.8.10.12", {"start": v(112.73, 42.86) * mm, "end": v(115.48, 38.1) * mm});
            skLineSegment(sketch, "E15.11.10.12", {"start": v(115.48, 38.1) * mm, "end": v(112.73, 33.34) * mm});
            skLineSegment(sketch, "E15.14.10.12", {"start": v(112.73, 33.34) * mm, "end": v(107.23, 33.34) * mm});
            skLineSegment(sketch, "E15.17.10.12", {"start": v(107.23, 33.34) * mm, "end": v(104.48, 38.1) * mm});
            skCircle(sketch, "E15.0.10.13", {"center": v(109.98, 50.8) * mm, "radius": 4.76 * mm, "construction": true});
            skLineSegment(sketch, "E15.2.10.13", {"start": v(104.48, 50.8) * mm, "end": v(107.23, 55.56) * mm});
            skLineSegment(sketch, "E15.5.10.13", {"start": v(107.23, 55.56) * mm, "end": v(112.73, 55.56) * mm});
            skLineSegment(sketch, "E15.8.10.13", {"start": v(112.73, 55.56) * mm, "end": v(115.48, 50.8) * mm});
            skLineSegment(sketch, "E15.11.10.13", {"start": v(115.48, 50.8) * mm, "end": v(112.73, 46.04) * mm});
            skLineSegment(sketch, "E15.14.10.13", {"start": v(112.73, 46.04) * mm, "end": v(107.23, 46.04) * mm});
            skLineSegment(sketch, "E15.17.10.13", {"start": v(107.23, 46.04) * mm, "end": v(104.48, 50.8) * mm});
            skCircle(sketch, "E15.0.10.14", {"center": v(109.98, 63.5) * mm, "radius": 4.76 * mm, "construction": true});
            skLineSegment(sketch, "E15.2.10.14", {"start": v(104.48, 63.5) * mm, "end": v(107.23, 68.26) * mm});
            skLineSegment(sketch, "E15.5.10.14", {"start": v(107.23, 68.26) * mm, "end": v(112.73, 68.26) * mm});
            skLineSegment(sketch, "E15.8.10.14", {"start": v(112.73, 68.26) * mm, "end": v(115.48, 63.5) * mm});
            skLineSegment(sketch, "E15.11.10.14", {"start": v(115.48, 63.5) * mm, "end": v(112.73, 58.74) * mm});
            skLineSegment(sketch, "E15.14.10.14", {"start": v(112.73, 58.74) * mm, "end": v(107.23, 58.74) * mm});
            skLineSegment(sketch, "E15.17.10.14", {"start": v(107.23, 58.74) * mm, "end": v(104.48, 63.5) * mm});
            skCircle(sketch, "E15.0.10.15", {"center": v(109.98, 76.2) * mm, "radius": 4.76 * mm, "construction": true});
            skLineSegment(sketch, "E15.2.10.15", {"start": v(104.48, 76.2) * mm, "end": v(107.23, 80.96) * mm});
            skLineSegment(sketch, "E15.5.10.15", {"start": v(107.23, 80.96) * mm, "end": v(112.73, 80.96) * mm});
            skLineSegment(sketch, "E15.8.10.15", {"start": v(112.73, 80.96) * mm, "end": v(115.48, 76.2) * mm});
            skLineSegment(sketch, "E15.11.10.15", {"start": v(115.48, 76.2) * mm, "end": v(112.73, 71.44) * mm});
            skLineSegment(sketch, "E15.14.10.15", {"start": v(112.73, 71.44) * mm, "end": v(107.23, 71.44) * mm});
            skLineSegment(sketch, "E15.17.10.15", {"start": v(107.23, 71.44) * mm, "end": v(104.48, 76.2) * mm});
            skCircle(sketch, "E15.0.10.16", {"center": v(109.98, 88.9) * mm, "radius": 4.76 * mm, "construction": true});
            skLineSegment(sketch, "E15.2.10.16", {"start": v(104.48, 88.9) * mm, "end": v(107.23, 93.66) * mm});
            skLineSegment(sketch, "E15.5.10.16", {"start": v(107.23, 93.66) * mm, "end": v(112.73, 93.66) * mm});
            skLineSegment(sketch, "E15.8.10.16", {"start": v(112.73, 93.66) * mm, "end": v(115.48, 88.9) * mm});
            skLineSegment(sketch, "E15.11.10.16", {"start": v(115.48, 88.9) * mm, "end": v(112.73, 84.14) * mm});
            skLineSegment(sketch, "E15.14.10.16", {"start": v(112.73, 84.14) * mm, "end": v(107.23, 84.14) * mm});
            skLineSegment(sketch, "E15.17.10.16", {"start": v(107.23, 84.14) * mm, "end": v(104.48, 88.9) * mm});
            skCircle(sketch, "E15.0.10.17", {"center": v(109.98, 101.6) * mm, "radius": 4.76 * mm, "construction": true});
            skLineSegment(sketch, "E15.2.10.17", {"start": v(104.48, 101.6) * mm, "end": v(107.23, 106.36) * mm});
            skLineSegment(sketch, "E15.5.10.17", {"start": v(107.23, 106.36) * mm, "end": v(112.73, 106.36) * mm});
            skLineSegment(sketch, "E15.8.10.17", {"start": v(112.73, 106.36) * mm, "end": v(115.48, 101.6) * mm});
            skLineSegment(sketch, "E15.11.10.17", {"start": v(115.48, 101.6) * mm, "end": v(112.73, 96.84) * mm});
            skLineSegment(sketch, "E15.14.10.17", {"start": v(112.73, 96.84) * mm, "end": v(107.23, 96.84) * mm});
            skLineSegment(sketch, "E15.17.10.17", {"start": v(107.23, 96.84) * mm, "end": v(104.48, 101.6) * mm});
            skCircle(sketch, "E15.0.10.18", {"center": v(109.98, 114.3) * mm, "radius": 4.76 * mm, "construction": true});
            skLineSegment(sketch, "E15.2.10.18", {"start": v(104.48, 114.3) * mm, "end": v(107.23, 119.06) * mm});
            skLineSegment(sketch, "E15.5.10.18", {"start": v(107.23, 119.06) * mm, "end": v(112.73, 119.06) * mm});
            skLineSegment(sketch, "E15.8.10.18", {"start": v(112.73, 119.06) * mm, "end": v(115.48, 114.3) * mm});
            skLineSegment(sketch, "E15.11.10.18", {"start": v(115.48, 114.3) * mm, "end": v(112.73, 109.54) * mm});
            skLineSegment(sketch, "E15.14.10.18", {"start": v(112.73, 109.54) * mm, "end": v(107.23, 109.54) * mm});
            skLineSegment(sketch, "E15.17.10.18", {"start": v(107.23, 109.54) * mm, "end": v(104.48, 114.3) * mm});
            skCircle(sketch, "E15.0.10.19", {"center": v(109.98, 127) * mm, "radius": 4.76 * mm, "construction": true});
            skLineSegment(sketch, "E15.2.10.19", {"start": v(104.48, 127) * mm, "end": v(107.23, 131.76) * mm});
            skLineSegment(sketch, "E15.5.10.19", {"start": v(107.23, 131.76) * mm, "end": v(112.73, 131.76) * mm});
            skLineSegment(sketch, "E15.8.10.19", {"start": v(112.73, 131.76) * mm, "end": v(115.48, 127) * mm});
            skLineSegment(sketch, "E15.11.10.19", {"start": v(115.48, 127) * mm, "end": v(112.73, 122.24) * mm});
            skLineSegment(sketch, "E15.14.10.19", {"start": v(112.73, 122.24) * mm, "end": v(107.23, 122.24) * mm});
            skLineSegment(sketch, "E15.17.10.19", {"start": v(107.23, 122.24) * mm, "end": v(104.48, 127) * mm});
            skCircle(sketch, "E15.0.11.0", {"center": v(131.98, -114.3) * mm, "radius": 4.76 * mm, "construction": true});
            skLineSegment(sketch, "E15.2.11.0", {"start": v(126.48, -114.3) * mm, "end": v(129.23, -109.54) * mm});
            skLineSegment(sketch, "E15.5.11.0", {"start": v(129.23, -109.54) * mm, "end": v(134.73, -109.54) * mm});
            skLineSegment(sketch, "E15.8.11.0", {"start": v(134.73, -109.54) * mm, "end": v(137.48, -114.3) * mm});
            skLineSegment(sketch, "E15.11.11.0", {"start": v(137.48, -114.3) * mm, "end": v(134.73, -119.06) * mm});
            skLineSegment(sketch, "E15.14.11.0", {"start": v(134.73, -119.06) * mm, "end": v(129.23, -119.06) * mm});
            skLineSegment(sketch, "E15.17.11.0", {"start": v(129.23, -119.06) * mm, "end": v(126.48, -114.3) * mm});
            skCircle(sketch, "E15.0.11.1", {"center": v(131.98, -101.6) * mm, "radius": 4.76 * mm, "construction": true});
            skLineSegment(sketch, "E15.2.11.1", {"start": v(126.48, -101.6) * mm, "end": v(129.23, -96.84) * mm});
            skLineSegment(sketch, "E15.5.11.1", {"start": v(129.23, -96.84) * mm, "end": v(134.73, -96.84) * mm});
            skLineSegment(sketch, "E15.8.11.1", {"start": v(134.73, -96.84) * mm, "end": v(137.48, -101.6) * mm});
            skLineSegment(sketch, "E15.11.11.1", {"start": v(137.48, -101.6) * mm, "end": v(134.73, -106.36) * mm});
            skLineSegment(sketch, "E15.14.11.1", {"start": v(134.73, -106.36) * mm, "end": v(129.23, -106.36) * mm});
            skLineSegment(sketch, "E15.17.11.1", {"start": v(129.23, -106.36) * mm, "end": v(126.48, -101.6) * mm});
            skCircle(sketch, "E15.0.11.2", {"center": v(131.98, -88.9) * mm, "radius": 4.76 * mm, "construction": true});
            skLineSegment(sketch, "E15.2.11.2", {"start": v(126.48, -88.9) * mm, "end": v(129.23, -84.14) * mm});
            skLineSegment(sketch, "E15.5.11.2", {"start": v(129.23, -84.14) * mm, "end": v(134.73, -84.14) * mm});
            skLineSegment(sketch, "E15.8.11.2", {"start": v(134.73, -84.14) * mm, "end": v(137.48, -88.9) * mm});
            skLineSegment(sketch, "E15.11.11.2", {"start": v(137.48, -88.9) * mm, "end": v(134.73, -93.66) * mm});
            skLineSegment(sketch, "E15.14.11.2", {"start": v(134.73, -93.66) * mm, "end": v(129.23, -93.66) * mm});
            skLineSegment(sketch, "E15.17.11.2", {"start": v(129.23, -93.66) * mm, "end": v(126.48, -88.9) * mm});
            skCircle(sketch, "E15.0.11.3", {"center": v(131.98, -76.2) * mm, "radius": 4.76 * mm, "construction": true});
            skLineSegment(sketch, "E15.2.11.3", {"start": v(126.48, -76.2) * mm, "end": v(129.23, -71.44) * mm});
            skLineSegment(sketch, "E15.5.11.3", {"start": v(129.23, -71.44) * mm, "end": v(134.73, -71.44) * mm});
            skLineSegment(sketch, "E15.8.11.3", {"start": v(134.73, -71.44) * mm, "end": v(137.48, -76.2) * mm});
            skLineSegment(sketch, "E15.11.11.3", {"start": v(137.48, -76.2) * mm, "end": v(134.73, -80.96) * mm});
            skLineSegment(sketch, "E15.14.11.3", {"start": v(134.73, -80.96) * mm, "end": v(129.23, -80.96) * mm});
            skLineSegment(sketch, "E15.17.11.3", {"start": v(129.23, -80.96) * mm, "end": v(126.48, -76.2) * mm});
            skCircle(sketch, "E15.0.11.4", {"center": v(131.98, -63.5) * mm, "radius": 4.76 * mm, "construction": true});
            skLineSegment(sketch, "E15.2.11.4", {"start": v(126.48, -63.5) * mm, "end": v(129.23, -58.74) * mm});
            skLineSegment(sketch, "E15.5.11.4", {"start": v(129.23, -58.74) * mm, "end": v(134.73, -58.74) * mm});
            skLineSegment(sketch, "E15.8.11.4", {"start": v(134.73, -58.74) * mm, "end": v(137.48, -63.5) * mm});
            skLineSegment(sketch, "E15.11.11.4", {"start": v(137.48, -63.5) * mm, "end": v(134.73, -68.26) * mm});
            skLineSegment(sketch, "E15.14.11.4", {"start": v(134.73, -68.26) * mm, "end": v(129.23, -68.26) * mm});
            skLineSegment(sketch, "E15.17.11.4", {"start": v(129.23, -68.26) * mm, "end": v(126.48, -63.5) * mm});
            skCircle(sketch, "E15.0.11.5", {"center": v(131.98, -50.8) * mm, "radius": 4.76 * mm, "construction": true});
            skLineSegment(sketch, "E15.2.11.5", {"start": v(126.48, -50.8) * mm, "end": v(129.23, -46.04) * mm});
            skLineSegment(sketch, "E15.5.11.5", {"start": v(129.23, -46.04) * mm, "end": v(134.73, -46.04) * mm});
            skLineSegment(sketch, "E15.8.11.5", {"start": v(134.73, -46.04) * mm, "end": v(137.48, -50.8) * mm});
            skLineSegment(sketch, "E15.11.11.5", {"start": v(137.48, -50.8) * mm, "end": v(134.73, -55.56) * mm});
            skLineSegment(sketch, "E15.14.11.5", {"start": v(134.73, -55.56) * mm, "end": v(129.23, -55.56) * mm});
            skLineSegment(sketch, "E15.17.11.5", {"start": v(129.23, -55.56) * mm, "end": v(126.48, -50.8) * mm});
            skCircle(sketch, "E15.0.11.6", {"center": v(131.98, -38.1) * mm, "radius": 4.76 * mm, "construction": true});
            skLineSegment(sketch, "E15.2.11.6", {"start": v(126.48, -38.1) * mm, "end": v(129.23, -33.34) * mm});
            skLineSegment(sketch, "E15.5.11.6", {"start": v(129.23, -33.34) * mm, "end": v(134.73, -33.34) * mm});
            skLineSegment(sketch, "E15.8.11.6", {"start": v(134.73, -33.34) * mm, "end": v(137.48, -38.1) * mm});
            skLineSegment(sketch, "E15.11.11.6", {"start": v(137.48, -38.1) * mm, "end": v(134.73, -42.86) * mm});
            skLineSegment(sketch, "E15.14.11.6", {"start": v(134.73, -42.86) * mm, "end": v(129.23, -42.86) * mm});
            skLineSegment(sketch, "E15.17.11.6", {"start": v(129.23, -42.86) * mm, "end": v(126.48, -38.1) * mm});
            skCircle(sketch, "E15.0.11.7", {"center": v(131.98, -25.4) * mm, "radius": 4.76 * mm, "construction": true});
            skLineSegment(sketch, "E15.2.11.7", {"start": v(126.48, -25.4) * mm, "end": v(129.23, -20.64) * mm});
            skLineSegment(sketch, "E15.5.11.7", {"start": v(129.23, -20.64) * mm, "end": v(134.73, -20.64) * mm});
            skLineSegment(sketch, "E15.8.11.7", {"start": v(134.73, -20.64) * mm, "end": v(137.48, -25.4) * mm});
            skLineSegment(sketch, "E15.11.11.7", {"start": v(137.48, -25.4) * mm, "end": v(134.73, -30.16) * mm});
            skLineSegment(sketch, "E15.14.11.7", {"start": v(134.73, -30.16) * mm, "end": v(129.23, -30.16) * mm});
            skLineSegment(sketch, "E15.17.11.7", {"start": v(129.23, -30.16) * mm, "end": v(126.48, -25.4) * mm});
            skCircle(sketch, "E15.0.11.8", {"center": v(131.98, -12.7) * mm, "radius": 4.76 * mm, "construction": true});
            skLineSegment(sketch, "E15.2.11.8", {"start": v(126.48, -12.7) * mm, "end": v(129.23, -7.94) * mm});
            skLineSegment(sketch, "E15.5.11.8", {"start": v(129.23, -7.94) * mm, "end": v(134.73, -7.94) * mm});
            skLineSegment(sketch, "E15.8.11.8", {"start": v(134.73, -7.94) * mm, "end": v(137.48, -12.7) * mm});
            skLineSegment(sketch, "E15.11.11.8", {"start": v(137.48, -12.7) * mm, "end": v(134.73, -17.46) * mm});
            skLineSegment(sketch, "E15.14.11.8", {"start": v(134.73, -17.46) * mm, "end": v(129.23, -17.46) * mm});
            skLineSegment(sketch, "E15.17.11.8", {"start": v(129.23, -17.46) * mm, "end": v(126.48, -12.7) * mm});
            skCircle(sketch, "E15.0.11.9", {"center": v(131.98, 0) * mm, "radius": 4.76 * mm, "construction": true});
            skLineSegment(sketch, "E15.2.11.9", {"start": v(126.48, 0) * mm, "end": v(129.23, 4.76) * mm});
            skLineSegment(sketch, "E15.5.11.9", {"start": v(129.23, 4.76) * mm, "end": v(134.73, 4.76) * mm});
            skLineSegment(sketch, "E15.8.11.9", {"start": v(134.73, 4.76) * mm, "end": v(137.48, 0) * mm});
            skLineSegment(sketch, "E15.11.11.9", {"start": v(137.48, 0) * mm, "end": v(134.73, -4.76) * mm});
            skLineSegment(sketch, "E15.14.11.9", {"start": v(134.73, -4.76) * mm, "end": v(129.23, -4.76) * mm});
            skLineSegment(sketch, "E15.17.11.9", {"start": v(129.23, -4.76) * mm, "end": v(126.48, 0) * mm});
            skCircle(sketch, "E15.0.11.10", {"center": v(131.98, 12.7) * mm, "radius": 4.76 * mm, "construction": true});
            skLineSegment(sketch, "E15.2.11.10", {"start": v(126.48, 12.7) * mm, "end": v(129.23, 17.46) * mm});
            skLineSegment(sketch, "E15.5.11.10", {"start": v(129.23, 17.46) * mm, "end": v(134.73, 17.46) * mm});
            skLineSegment(sketch, "E15.8.11.10", {"start": v(134.73, 17.46) * mm, "end": v(137.48, 12.7) * mm});
            skLineSegment(sketch, "E15.11.11.10", {"start": v(137.48, 12.7) * mm, "end": v(134.73, 7.94) * mm});
            skLineSegment(sketch, "E15.14.11.10", {"start": v(134.73, 7.94) * mm, "end": v(129.23, 7.94) * mm});
            skLineSegment(sketch, "E15.17.11.10", {"start": v(129.23, 7.94) * mm, "end": v(126.48, 12.7) * mm});
            skCircle(sketch, "E15.0.11.11", {"center": v(131.98, 25.4) * mm, "radius": 4.76 * mm, "construction": true});
            skLineSegment(sketch, "E15.2.11.11", {"start": v(126.48, 25.4) * mm, "end": v(129.23, 30.16) * mm});
            skLineSegment(sketch, "E15.5.11.11", {"start": v(129.23, 30.16) * mm, "end": v(134.73, 30.16) * mm});
            skLineSegment(sketch, "E15.8.11.11", {"start": v(134.73, 30.16) * mm, "end": v(137.48, 25.4) * mm});
            skLineSegment(sketch, "E15.11.11.11", {"start": v(137.48, 25.4) * mm, "end": v(134.73, 20.64) * mm});
            skLineSegment(sketch, "E15.14.11.11", {"start": v(134.73, 20.64) * mm, "end": v(129.23, 20.64) * mm});
            skLineSegment(sketch, "E15.17.11.11", {"start": v(129.23, 20.64) * mm, "end": v(126.48, 25.4) * mm});
            skCircle(sketch, "E15.0.11.12", {"center": v(131.98, 38.1) * mm, "radius": 4.76 * mm, "construction": true});
            skLineSegment(sketch, "E15.2.11.12", {"start": v(126.48, 38.1) * mm, "end": v(129.23, 42.86) * mm});
            skLineSegment(sketch, "E15.5.11.12", {"start": v(129.23, 42.86) * mm, "end": v(134.73, 42.86) * mm});
            skLineSegment(sketch, "E15.8.11.12", {"start": v(134.73, 42.86) * mm, "end": v(137.48, 38.1) * mm});
            skLineSegment(sketch, "E15.11.11.12", {"start": v(137.48, 38.1) * mm, "end": v(134.73, 33.34) * mm});
            skLineSegment(sketch, "E15.14.11.12", {"start": v(134.73, 33.34) * mm, "end": v(129.23, 33.34) * mm});
            skLineSegment(sketch, "E15.17.11.12", {"start": v(129.23, 33.34) * mm, "end": v(126.48, 38.1) * mm});
            skCircle(sketch, "E15.0.11.13", {"center": v(131.98, 50.8) * mm, "radius": 4.76 * mm, "construction": true});
            skLineSegment(sketch, "E15.2.11.13", {"start": v(126.48, 50.8) * mm, "end": v(129.23, 55.56) * mm});
            skLineSegment(sketch, "E15.5.11.13", {"start": v(129.23, 55.56) * mm, "end": v(134.73, 55.56) * mm});
            skLineSegment(sketch, "E15.8.11.13", {"start": v(134.73, 55.56) * mm, "end": v(137.48, 50.8) * mm});
            skLineSegment(sketch, "E15.11.11.13", {"start": v(137.48, 50.8) * mm, "end": v(134.73, 46.04) * mm});
            skLineSegment(sketch, "E15.14.11.13", {"start": v(134.73, 46.04) * mm, "end": v(129.23, 46.04) * mm});
            skLineSegment(sketch, "E15.17.11.13", {"start": v(129.23, 46.04) * mm, "end": v(126.48, 50.8) * mm});
            skCircle(sketch, "E15.0.11.14", {"center": v(131.98, 63.5) * mm, "radius": 4.76 * mm, "construction": true});
            skLineSegment(sketch, "E15.2.11.14", {"start": v(126.48, 63.5) * mm, "end": v(129.23, 68.26) * mm});
            skLineSegment(sketch, "E15.5.11.14", {"start": v(129.23, 68.26) * mm, "end": v(134.73, 68.26) * mm});
            skLineSegment(sketch, "E15.8.11.14", {"start": v(134.73, 68.26) * mm, "end": v(137.48, 63.5) * mm});
            skLineSegment(sketch, "E15.11.11.14", {"start": v(137.48, 63.5) * mm, "end": v(134.73, 58.74) * mm});
            skLineSegment(sketch, "E15.14.11.14", {"start": v(134.73, 58.74) * mm, "end": v(129.23, 58.74) * mm});
            skLineSegment(sketch, "E15.17.11.14", {"start": v(129.23, 58.74) * mm, "end": v(126.48, 63.5) * mm});
            skCircle(sketch, "E15.0.11.15", {"center": v(131.98, 76.2) * mm, "radius": 4.76 * mm, "construction": true});
            skLineSegment(sketch, "E15.2.11.15", {"start": v(126.48, 76.2) * mm, "end": v(129.23, 80.96) * mm});
            skLineSegment(sketch, "E15.5.11.15", {"start": v(129.23, 80.96) * mm, "end": v(134.73, 80.96) * mm});
            skLineSegment(sketch, "E15.8.11.15", {"start": v(134.73, 80.96) * mm, "end": v(137.48, 76.2) * mm});
            skLineSegment(sketch, "E15.11.11.15", {"start": v(137.48, 76.2) * mm, "end": v(134.73, 71.44) * mm});
            skLineSegment(sketch, "E15.14.11.15", {"start": v(134.73, 71.44) * mm, "end": v(129.23, 71.44) * mm});
            skLineSegment(sketch, "E15.17.11.15", {"start": v(129.23, 71.44) * mm, "end": v(126.48, 76.2) * mm});
            skCircle(sketch, "E15.0.11.16", {"center": v(131.98, 88.9) * mm, "radius": 4.76 * mm, "construction": true});
            skLineSegment(sketch, "E15.2.11.16", {"start": v(126.48, 88.9) * mm, "end": v(129.23, 93.66) * mm});
            skLineSegment(sketch, "E15.5.11.16", {"start": v(129.23, 93.66) * mm, "end": v(134.73, 93.66) * mm});
            skLineSegment(sketch, "E15.8.11.16", {"start": v(134.73, 93.66) * mm, "end": v(137.48, 88.9) * mm});
            skLineSegment(sketch, "E15.11.11.16", {"start": v(137.48, 88.9) * mm, "end": v(134.73, 84.14) * mm});
            skLineSegment(sketch, "E15.14.11.16", {"start": v(134.73, 84.14) * mm, "end": v(129.23, 84.14) * mm});
            skLineSegment(sketch, "E15.17.11.16", {"start": v(129.23, 84.14) * mm, "end": v(126.48, 88.9) * mm});
            skCircle(sketch, "E15.0.11.17", {"center": v(131.98, 101.6) * mm, "radius": 4.76 * mm, "construction": true});
            skLineSegment(sketch, "E15.2.11.17", {"start": v(126.48, 101.6) * mm, "end": v(129.23, 106.36) * mm});
            skLineSegment(sketch, "E15.5.11.17", {"start": v(129.23, 106.36) * mm, "end": v(134.73, 106.36) * mm});
            skLineSegment(sketch, "E15.8.11.17", {"start": v(134.73, 106.36) * mm, "end": v(137.48, 101.6) * mm});
            skLineSegment(sketch, "E15.11.11.17", {"start": v(137.48, 101.6) * mm, "end": v(134.73, 96.84) * mm});
            skLineSegment(sketch, "E15.14.11.17", {"start": v(134.73, 96.84) * mm, "end": v(129.23, 96.84) * mm});
            skLineSegment(sketch, "E15.17.11.17", {"start": v(129.23, 96.84) * mm, "end": v(126.48, 101.6) * mm});
            skCircle(sketch, "E15.0.11.18", {"center": v(131.98, 114.3) * mm, "radius": 4.76 * mm, "construction": true});
            skLineSegment(sketch, "E15.2.11.18", {"start": v(126.48, 114.3) * mm, "end": v(129.23, 119.06) * mm});
            skLineSegment(sketch, "E15.5.11.18", {"start": v(129.23, 119.06) * mm, "end": v(134.73, 119.06) * mm});
            skLineSegment(sketch, "E15.8.11.18", {"start": v(134.73, 119.06) * mm, "end": v(137.48, 114.3) * mm});
            skLineSegment(sketch, "E15.11.11.18", {"start": v(137.48, 114.3) * mm, "end": v(134.73, 109.54) * mm});
            skLineSegment(sketch, "E15.14.11.18", {"start": v(134.73, 109.54) * mm, "end": v(129.23, 109.54) * mm});
            skLineSegment(sketch, "E15.17.11.18", {"start": v(129.23, 109.54) * mm, "end": v(126.48, 114.3) * mm});
            skCircle(sketch, "E15.0.11.19", {"center": v(131.98, 127) * mm, "radius": 4.76 * mm, "construction": true});
            skLineSegment(sketch, "E15.2.11.19", {"start": v(126.48, 127) * mm, "end": v(129.23, 131.76) * mm});
            skLineSegment(sketch, "E15.5.11.19", {"start": v(129.23, 131.76) * mm, "end": v(134.73, 131.76) * mm});
            skLineSegment(sketch, "E15.8.11.19", {"start": v(134.73, 131.76) * mm, "end": v(137.48, 127) * mm});
            skLineSegment(sketch, "E15.11.11.19", {"start": v(137.48, 127) * mm, "end": v(134.73, 122.24) * mm});
            skLineSegment(sketch, "E15.14.11.19", {"start": v(134.73, 122.24) * mm, "end": v(129.23, 122.24) * mm});
            skLineSegment(sketch, "E15.17.11.19", {"start": v(129.23, 122.24) * mm, "end": v(126.48, 127) * mm});
            skCircle(sketch, "E15.0.12.0", {"center": v(153.97, -114.3) * mm, "radius": 4.76 * mm, "construction": true});
            skLineSegment(sketch, "E15.2.12.0", {"start": v(148.48, -114.3) * mm, "end": v(151.23, -109.54) * mm});
            skLineSegment(sketch, "E15.5.12.0", {"start": v(151.23, -109.54) * mm, "end": v(156.72, -109.54) * mm});
            skLineSegment(sketch, "E15.8.12.0", {"start": v(156.72, -109.54) * mm, "end": v(159.47, -114.3) * mm});
            skLineSegment(sketch, "E15.11.12.0", {"start": v(159.47, -114.3) * mm, "end": v(156.72, -119.06) * mm});
            skLineSegment(sketch, "E15.14.12.0", {"start": v(156.72, -119.06) * mm, "end": v(151.23, -119.06) * mm});
            skLineSegment(sketch, "E15.17.12.0", {"start": v(151.23, -119.06) * mm, "end": v(148.48, -114.3) * mm});
            skCircle(sketch, "E15.0.12.1", {"center": v(153.97, -101.6) * mm, "radius": 4.76 * mm, "construction": true});
            skLineSegment(sketch, "E15.2.12.1", {"start": v(148.48, -101.6) * mm, "end": v(151.23, -96.84) * mm});
            skLineSegment(sketch, "E15.5.12.1", {"start": v(151.23, -96.84) * mm, "end": v(156.72, -96.84) * mm});
            skLineSegment(sketch, "E15.8.12.1", {"start": v(156.72, -96.84) * mm, "end": v(159.47, -101.6) * mm});
            skLineSegment(sketch, "E15.11.12.1", {"start": v(159.47, -101.6) * mm, "end": v(156.72, -106.36) * mm});
            skLineSegment(sketch, "E15.14.12.1", {"start": v(156.72, -106.36) * mm, "end": v(151.23, -106.36) * mm});
            skLineSegment(sketch, "E15.17.12.1", {"start": v(151.23, -106.36) * mm, "end": v(148.48, -101.6) * mm});
            skCircle(sketch, "E15.0.12.2", {"center": v(153.97, -88.9) * mm, "radius": 4.76 * mm, "construction": true});
            skLineSegment(sketch, "E15.2.12.2", {"start": v(148.48, -88.9) * mm, "end": v(151.23, -84.14) * mm});
            skLineSegment(sketch, "E15.5.12.2", {"start": v(151.23, -84.14) * mm, "end": v(156.72, -84.14) * mm});
            skLineSegment(sketch, "E15.8.12.2", {"start": v(156.72, -84.14) * mm, "end": v(159.47, -88.9) * mm});
            skLineSegment(sketch, "E15.11.12.2", {"start": v(159.47, -88.9) * mm, "end": v(156.72, -93.66) * mm});
            skLineSegment(sketch, "E15.14.12.2", {"start": v(156.72, -93.66) * mm, "end": v(151.23, -93.66) * mm});
            skLineSegment(sketch, "E15.17.12.2", {"start": v(151.23, -93.66) * mm, "end": v(148.48, -88.9) * mm});
            skCircle(sketch, "E15.0.12.3", {"center": v(153.97, -76.2) * mm, "radius": 4.76 * mm, "construction": true});
            skLineSegment(sketch, "E15.2.12.3", {"start": v(148.48, -76.2) * mm, "end": v(151.23, -71.44) * mm});
            skLineSegment(sketch, "E15.5.12.3", {"start": v(151.23, -71.44) * mm, "end": v(156.72, -71.44) * mm});
            skLineSegment(sketch, "E15.8.12.3", {"start": v(156.72, -71.44) * mm, "end": v(159.47, -76.2) * mm});
            skLineSegment(sketch, "E15.11.12.3", {"start": v(159.47, -76.2) * mm, "end": v(156.72, -80.96) * mm});
            skLineSegment(sketch, "E15.14.12.3", {"start": v(156.72, -80.96) * mm, "end": v(151.23, -80.96) * mm});
            skLineSegment(sketch, "E15.17.12.3", {"start": v(151.23, -80.96) * mm, "end": v(148.48, -76.2) * mm});
            skCircle(sketch, "E15.0.12.4", {"center": v(153.97, -63.5) * mm, "radius": 4.76 * mm, "construction": true});
            skLineSegment(sketch, "E15.2.12.4", {"start": v(148.48, -63.5) * mm, "end": v(151.23, -58.74) * mm});
            skLineSegment(sketch, "E15.5.12.4", {"start": v(151.23, -58.74) * mm, "end": v(156.72, -58.74) * mm});
            skLineSegment(sketch, "E15.8.12.4", {"start": v(156.72, -58.74) * mm, "end": v(159.47, -63.5) * mm});
            skLineSegment(sketch, "E15.11.12.4", {"start": v(159.47, -63.5) * mm, "end": v(156.72, -68.26) * mm});
            skLineSegment(sketch, "E15.14.12.4", {"start": v(156.72, -68.26) * mm, "end": v(151.23, -68.26) * mm});
            skLineSegment(sketch, "E15.17.12.4", {"start": v(151.23, -68.26) * mm, "end": v(148.48, -63.5) * mm});
            skCircle(sketch, "E15.0.12.5", {"center": v(153.97, -50.8) * mm, "radius": 4.76 * mm, "construction": true});
            skLineSegment(sketch, "E15.2.12.5", {"start": v(148.48, -50.8) * mm, "end": v(151.23, -46.04) * mm});
            skLineSegment(sketch, "E15.5.12.5", {"start": v(151.23, -46.04) * mm, "end": v(156.72, -46.04) * mm});
            skLineSegment(sketch, "E15.8.12.5", {"start": v(156.72, -46.04) * mm, "end": v(159.47, -50.8) * mm});
            skLineSegment(sketch, "E15.11.12.5", {"start": v(159.47, -50.8) * mm, "end": v(156.72, -55.56) * mm});
            skLineSegment(sketch, "E15.14.12.5", {"start": v(156.72, -55.56) * mm, "end": v(151.23, -55.56) * mm});
            skLineSegment(sketch, "E15.17.12.5", {"start": v(151.23, -55.56) * mm, "end": v(148.48, -50.8) * mm});
            skCircle(sketch, "E15.0.12.6", {"center": v(153.97, -38.1) * mm, "radius": 4.76 * mm, "construction": true});
            skLineSegment(sketch, "E15.2.12.6", {"start": v(148.48, -38.1) * mm, "end": v(151.23, -33.34) * mm});
            skLineSegment(sketch, "E15.5.12.6", {"start": v(151.23, -33.34) * mm, "end": v(156.72, -33.34) * mm});
            skLineSegment(sketch, "E15.8.12.6", {"start": v(156.72, -33.34) * mm, "end": v(159.47, -38.1) * mm});
            skLineSegment(sketch, "E15.11.12.6", {"start": v(159.47, -38.1) * mm, "end": v(156.72, -42.86) * mm});
            skLineSegment(sketch, "E15.14.12.6", {"start": v(156.72, -42.86) * mm, "end": v(151.23, -42.86) * mm});
            skLineSegment(sketch, "E15.17.12.6", {"start": v(151.23, -42.86) * mm, "end": v(148.48, -38.1) * mm});
            skCircle(sketch, "E15.0.12.7", {"center": v(153.97, -25.4) * mm, "radius": 4.76 * mm, "construction": true});
            skLineSegment(sketch, "E15.2.12.7", {"start": v(148.48, -25.4) * mm, "end": v(151.23, -20.64) * mm});
            skLineSegment(sketch, "E15.5.12.7", {"start": v(151.23, -20.64) * mm, "end": v(156.72, -20.64) * mm});
            skLineSegment(sketch, "E15.8.12.7", {"start": v(156.72, -20.64) * mm, "end": v(159.47, -25.4) * mm});
            skLineSegment(sketch, "E15.11.12.7", {"start": v(159.47, -25.4) * mm, "end": v(156.72, -30.16) * mm});
            skLineSegment(sketch, "E15.14.12.7", {"start": v(156.72, -30.16) * mm, "end": v(151.23, -30.16) * mm});
            skLineSegment(sketch, "E15.17.12.7", {"start": v(151.23, -30.16) * mm, "end": v(148.48, -25.4) * mm});
            skCircle(sketch, "E15.0.12.8", {"center": v(153.97, -12.7) * mm, "radius": 4.76 * mm, "construction": true});
            skLineSegment(sketch, "E15.2.12.8", {"start": v(148.48, -12.7) * mm, "end": v(151.23, -7.94) * mm});
            skLineSegment(sketch, "E15.5.12.8", {"start": v(151.23, -7.94) * mm, "end": v(156.72, -7.94) * mm});
            skLineSegment(sketch, "E15.8.12.8", {"start": v(156.72, -7.94) * mm, "end": v(159.47, -12.7) * mm});
            skLineSegment(sketch, "E15.11.12.8", {"start": v(159.47, -12.7) * mm, "end": v(156.72, -17.46) * mm});
            skLineSegment(sketch, "E15.14.12.8", {"start": v(156.72, -17.46) * mm, "end": v(151.23, -17.46) * mm});
            skLineSegment(sketch, "E15.17.12.8", {"start": v(151.23, -17.46) * mm, "end": v(148.48, -12.7) * mm});
            skCircle(sketch, "E15.0.12.9", {"center": v(153.97, 0) * mm, "radius": 4.76 * mm, "construction": true});
            skLineSegment(sketch, "E15.2.12.9", {"start": v(148.48, 0) * mm, "end": v(151.23, 4.76) * mm});
            skLineSegment(sketch, "E15.5.12.9", {"start": v(151.23, 4.76) * mm, "end": v(156.72, 4.76) * mm});
            skLineSegment(sketch, "E15.8.12.9", {"start": v(156.72, 4.76) * mm, "end": v(159.47, 0) * mm});
            skLineSegment(sketch, "E15.11.12.9", {"start": v(159.47, 0) * mm, "end": v(156.72, -4.76) * mm});
            skLineSegment(sketch, "E15.14.12.9", {"start": v(156.72, -4.76) * mm, "end": v(151.23, -4.76) * mm});
            skLineSegment(sketch, "E15.17.12.9", {"start": v(151.23, -4.76) * mm, "end": v(148.48, 0) * mm});
            skCircle(sketch, "E15.0.12.10", {"center": v(153.97, 12.7) * mm, "radius": 4.76 * mm, "construction": true});
            skLineSegment(sketch, "E15.2.12.10", {"start": v(148.48, 12.7) * mm, "end": v(151.23, 17.46) * mm});
            skLineSegment(sketch, "E15.5.12.10", {"start": v(151.23, 17.46) * mm, "end": v(156.72, 17.46) * mm});
            skLineSegment(sketch, "E15.8.12.10", {"start": v(156.72, 17.46) * mm, "end": v(159.47, 12.7) * mm});
            skLineSegment(sketch, "E15.11.12.10", {"start": v(159.47, 12.7) * mm, "end": v(156.72, 7.94) * mm});
            skLineSegment(sketch, "E15.14.12.10", {"start": v(156.72, 7.94) * mm, "end": v(151.23, 7.94) * mm});
            skLineSegment(sketch, "E15.17.12.10", {"start": v(151.23, 7.94) * mm, "end": v(148.48, 12.7) * mm});
            skCircle(sketch, "E15.0.12.11", {"center": v(153.97, 25.4) * mm, "radius": 4.76 * mm, "construction": true});
            skLineSegment(sketch, "E15.2.12.11", {"start": v(148.48, 25.4) * mm, "end": v(151.23, 30.16) * mm});
            skLineSegment(sketch, "E15.5.12.11", {"start": v(151.23, 30.16) * mm, "end": v(156.72, 30.16) * mm});
            skLineSegment(sketch, "E15.8.12.11", {"start": v(156.72, 30.16) * mm, "end": v(159.47, 25.4) * mm});
            skLineSegment(sketch, "E15.11.12.11", {"start": v(159.47, 25.4) * mm, "end": v(156.72, 20.64) * mm});
            skLineSegment(sketch, "E15.14.12.11", {"start": v(156.72, 20.64) * mm, "end": v(151.23, 20.64) * mm});
            skLineSegment(sketch, "E15.17.12.11", {"start": v(151.23, 20.64) * mm, "end": v(148.48, 25.4) * mm});
            skCircle(sketch, "E15.0.12.12", {"center": v(153.97, 38.1) * mm, "radius": 4.76 * mm, "construction": true});
            skLineSegment(sketch, "E15.2.12.12", {"start": v(148.48, 38.1) * mm, "end": v(151.23, 42.86) * mm});
            skLineSegment(sketch, "E15.5.12.12", {"start": v(151.23, 42.86) * mm, "end": v(156.72, 42.86) * mm});
            skLineSegment(sketch, "E15.8.12.12", {"start": v(156.72, 42.86) * mm, "end": v(159.47, 38.1) * mm});
            skLineSegment(sketch, "E15.11.12.12", {"start": v(159.47, 38.1) * mm, "end": v(156.72, 33.34) * mm});
            skLineSegment(sketch, "E15.14.12.12", {"start": v(156.72, 33.34) * mm, "end": v(151.23, 33.34) * mm});
            skLineSegment(sketch, "E15.17.12.12", {"start": v(151.23, 33.34) * mm, "end": v(148.48, 38.1) * mm});
            skCircle(sketch, "E15.0.12.13", {"center": v(153.97, 50.8) * mm, "radius": 4.76 * mm, "construction": true});
            skLineSegment(sketch, "E15.2.12.13", {"start": v(148.48, 50.8) * mm, "end": v(151.23, 55.56) * mm});
            skLineSegment(sketch, "E15.5.12.13", {"start": v(151.23, 55.56) * mm, "end": v(156.72, 55.56) * mm});
            skLineSegment(sketch, "E15.8.12.13", {"start": v(156.72, 55.56) * mm, "end": v(159.47, 50.8) * mm});
            skLineSegment(sketch, "E15.11.12.13", {"start": v(159.47, 50.8) * mm, "end": v(156.72, 46.04) * mm});
            skLineSegment(sketch, "E15.14.12.13", {"start": v(156.72, 46.04) * mm, "end": v(151.23, 46.04) * mm});
            skLineSegment(sketch, "E15.17.12.13", {"start": v(151.23, 46.04) * mm, "end": v(148.48, 50.8) * mm});
            skCircle(sketch, "E15.0.12.14", {"center": v(153.97, 63.5) * mm, "radius": 4.76 * mm, "construction": true});
            skLineSegment(sketch, "E15.2.12.14", {"start": v(148.48, 63.5) * mm, "end": v(151.23, 68.26) * mm});
            skLineSegment(sketch, "E15.5.12.14", {"start": v(151.23, 68.26) * mm, "end": v(156.72, 68.26) * mm});
            skLineSegment(sketch, "E15.8.12.14", {"start": v(156.72, 68.26) * mm, "end": v(159.47, 63.5) * mm});
            skLineSegment(sketch, "E15.11.12.14", {"start": v(159.47, 63.5) * mm, "end": v(156.72, 58.74) * mm});
            skLineSegment(sketch, "E15.14.12.14", {"start": v(156.72, 58.74) * mm, "end": v(151.23, 58.74) * mm});
            skLineSegment(sketch, "E15.17.12.14", {"start": v(151.23, 58.74) * mm, "end": v(148.48, 63.5) * mm});
            skCircle(sketch, "E15.0.12.15", {"center": v(153.97, 76.2) * mm, "radius": 4.76 * mm, "construction": true});
            skLineSegment(sketch, "E15.2.12.15", {"start": v(148.48, 76.2) * mm, "end": v(151.23, 80.96) * mm});
            skLineSegment(sketch, "E15.5.12.15", {"start": v(151.23, 80.96) * mm, "end": v(156.72, 80.96) * mm});
            skLineSegment(sketch, "E15.8.12.15", {"start": v(156.72, 80.96) * mm, "end": v(159.47, 76.2) * mm});
            skLineSegment(sketch, "E15.11.12.15", {"start": v(159.47, 76.2) * mm, "end": v(156.72, 71.44) * mm});
            skLineSegment(sketch, "E15.14.12.15", {"start": v(156.72, 71.44) * mm, "end": v(151.23, 71.44) * mm});
            skLineSegment(sketch, "E15.17.12.15", {"start": v(151.23, 71.44) * mm, "end": v(148.48, 76.2) * mm});
            skCircle(sketch, "E15.0.12.16", {"center": v(153.97, 88.9) * mm, "radius": 4.76 * mm, "construction": true});
            skLineSegment(sketch, "E15.2.12.16", {"start": v(148.48, 88.9) * mm, "end": v(151.23, 93.66) * mm});
            skLineSegment(sketch, "E15.5.12.16", {"start": v(151.23, 93.66) * mm, "end": v(156.72, 93.66) * mm});
            skLineSegment(sketch, "E15.8.12.16", {"start": v(156.72, 93.66) * mm, "end": v(159.47, 88.9) * mm});
            skLineSegment(sketch, "E15.11.12.16", {"start": v(159.47, 88.9) * mm, "end": v(156.72, 84.14) * mm});
            skLineSegment(sketch, "E15.14.12.16", {"start": v(156.72, 84.14) * mm, "end": v(151.23, 84.14) * mm});
            skLineSegment(sketch, "E15.17.12.16", {"start": v(151.23, 84.14) * mm, "end": v(148.48, 88.9) * mm});
            skCircle(sketch, "E15.0.12.17", {"center": v(153.97, 101.6) * mm, "radius": 4.76 * mm, "construction": true});
            skLineSegment(sketch, "E15.2.12.17", {"start": v(148.48, 101.6) * mm, "end": v(151.23, 106.36) * mm});
            skLineSegment(sketch, "E15.5.12.17", {"start": v(151.23, 106.36) * mm, "end": v(156.72, 106.36) * mm});
            skLineSegment(sketch, "E15.8.12.17", {"start": v(156.72, 106.36) * mm, "end": v(159.47, 101.6) * mm});
            skLineSegment(sketch, "E15.11.12.17", {"start": v(159.47, 101.6) * mm, "end": v(156.72, 96.84) * mm});
            skLineSegment(sketch, "E15.14.12.17", {"start": v(156.72, 96.84) * mm, "end": v(151.23, 96.84) * mm});
            skLineSegment(sketch, "E15.17.12.17", {"start": v(151.23, 96.84) * mm, "end": v(148.48, 101.6) * mm});
            skCircle(sketch, "E15.0.12.18", {"center": v(153.97, 114.3) * mm, "radius": 4.76 * mm, "construction": true});
            skLineSegment(sketch, "E15.2.12.18", {"start": v(148.48, 114.3) * mm, "end": v(151.23, 119.06) * mm});
            skLineSegment(sketch, "E15.5.12.18", {"start": v(151.23, 119.06) * mm, "end": v(156.72, 119.06) * mm});
            skLineSegment(sketch, "E15.8.12.18", {"start": v(156.72, 119.06) * mm, "end": v(159.47, 114.3) * mm});
            skLineSegment(sketch, "E15.11.12.18", {"start": v(159.47, 114.3) * mm, "end": v(156.72, 109.54) * mm});
            skLineSegment(sketch, "E15.14.12.18", {"start": v(156.72, 109.54) * mm, "end": v(151.23, 109.54) * mm});
            skLineSegment(sketch, "E15.17.12.18", {"start": v(151.23, 109.54) * mm, "end": v(148.48, 114.3) * mm});
            skCircle(sketch, "E15.0.12.19", {"center": v(153.97, 127) * mm, "radius": 4.76 * mm, "construction": true});
            skLineSegment(sketch, "E15.2.12.19", {"start": v(148.48, 127) * mm, "end": v(151.23, 131.76) * mm});
            skLineSegment(sketch, "E15.5.12.19", {"start": v(151.23, 131.76) * mm, "end": v(156.72, 131.76) * mm});
            skLineSegment(sketch, "E15.8.12.19", {"start": v(156.72, 131.76) * mm, "end": v(159.47, 127) * mm});
            skLineSegment(sketch, "E15.11.12.19", {"start": v(159.47, 127) * mm, "end": v(156.72, 122.24) * mm});
            skLineSegment(sketch, "E15.14.12.19", {"start": v(156.72, 122.24) * mm, "end": v(151.23, 122.24) * mm});
            skLineSegment(sketch, "E15.17.12.19", {"start": v(151.23, 122.24) * mm, "end": v(148.48, 127) * mm});
            skCircle(sketch, "E15.0.13.0", {"center": v(175.97, -114.3) * mm, "radius": 4.76 * mm, "construction": true});
            skLineSegment(sketch, "E15.2.13.0", {"start": v(170.47, -114.3) * mm, "end": v(173.22, -109.54) * mm});
            skLineSegment(sketch, "E15.5.13.0", {"start": v(173.22, -109.54) * mm, "end": v(178.72, -109.54) * mm});
            skLineSegment(sketch, "E15.8.13.0", {"start": v(178.72, -109.54) * mm, "end": v(181.47, -114.3) * mm});
            skLineSegment(sketch, "E15.11.13.0", {"start": v(181.47, -114.3) * mm, "end": v(178.72, -119.06) * mm});
            skLineSegment(sketch, "E15.14.13.0", {"start": v(178.72, -119.06) * mm, "end": v(173.22, -119.06) * mm});
            skLineSegment(sketch, "E15.17.13.0", {"start": v(173.22, -119.06) * mm, "end": v(170.47, -114.3) * mm});
            skCircle(sketch, "E15.0.13.1", {"center": v(175.97, -101.6) * mm, "radius": 4.76 * mm, "construction": true});
            skLineSegment(sketch, "E15.2.13.1", {"start": v(170.47, -101.6) * mm, "end": v(173.22, -96.84) * mm});
            skLineSegment(sketch, "E15.5.13.1", {"start": v(173.22, -96.84) * mm, "end": v(178.72, -96.84) * mm});
            skLineSegment(sketch, "E15.8.13.1", {"start": v(178.72, -96.84) * mm, "end": v(181.47, -101.6) * mm});
            skLineSegment(sketch, "E15.11.13.1", {"start": v(181.47, -101.6) * mm, "end": v(178.72, -106.36) * mm});
            skLineSegment(sketch, "E15.14.13.1", {"start": v(178.72, -106.36) * mm, "end": v(173.22, -106.36) * mm});
            skLineSegment(sketch, "E15.17.13.1", {"start": v(173.22, -106.36) * mm, "end": v(170.47, -101.6) * mm});
            skCircle(sketch, "E15.0.13.2", {"center": v(175.97, -88.9) * mm, "radius": 4.76 * mm, "construction": true});
            skLineSegment(sketch, "E15.2.13.2", {"start": v(170.47, -88.9) * mm, "end": v(173.22, -84.14) * mm});
            skLineSegment(sketch, "E15.5.13.2", {"start": v(173.22, -84.14) * mm, "end": v(178.72, -84.14) * mm});
            skLineSegment(sketch, "E15.8.13.2", {"start": v(178.72, -84.14) * mm, "end": v(181.47, -88.9) * mm});
            skLineSegment(sketch, "E15.11.13.2", {"start": v(181.47, -88.9) * mm, "end": v(178.72, -93.66) * mm});
            skLineSegment(sketch, "E15.14.13.2", {"start": v(178.72, -93.66) * mm, "end": v(173.22, -93.66) * mm});
            skLineSegment(sketch, "E15.17.13.2", {"start": v(173.22, -93.66) * mm, "end": v(170.47, -88.9) * mm});
            skCircle(sketch, "E15.0.13.3", {"center": v(175.97, -76.2) * mm, "radius": 4.76 * mm, "construction": true});
            skLineSegment(sketch, "E15.2.13.3", {"start": v(170.47, -76.2) * mm, "end": v(173.22, -71.44) * mm});
            skLineSegment(sketch, "E15.5.13.3", {"start": v(173.22, -71.44) * mm, "end": v(178.72, -71.44) * mm});
            skLineSegment(sketch, "E15.8.13.3", {"start": v(178.72, -71.44) * mm, "end": v(181.47, -76.2) * mm});
            skLineSegment(sketch, "E15.11.13.3", {"start": v(181.47, -76.2) * mm, "end": v(178.72, -80.96) * mm});
            skLineSegment(sketch, "E15.14.13.3", {"start": v(178.72, -80.96) * mm, "end": v(173.22, -80.96) * mm});
            skLineSegment(sketch, "E15.17.13.3", {"start": v(173.22, -80.96) * mm, "end": v(170.47, -76.2) * mm});
            skCircle(sketch, "E15.0.13.4", {"center": v(175.97, -63.5) * mm, "radius": 4.76 * mm, "construction": true});
            skLineSegment(sketch, "E15.2.13.4", {"start": v(170.47, -63.5) * mm, "end": v(173.22, -58.74) * mm});
            skLineSegment(sketch, "E15.5.13.4", {"start": v(173.22, -58.74) * mm, "end": v(178.72, -58.74) * mm});
            skLineSegment(sketch, "E15.8.13.4", {"start": v(178.72, -58.74) * mm, "end": v(181.47, -63.5) * mm});
            skLineSegment(sketch, "E15.11.13.4", {"start": v(181.47, -63.5) * mm, "end": v(178.72, -68.26) * mm});
            skLineSegment(sketch, "E15.14.13.4", {"start": v(178.72, -68.26) * mm, "end": v(173.22, -68.26) * mm});
            skLineSegment(sketch, "E15.17.13.4", {"start": v(173.22, -68.26) * mm, "end": v(170.47, -63.5) * mm});
            skCircle(sketch, "E15.0.13.5", {"center": v(175.97, -50.8) * mm, "radius": 4.76 * mm, "construction": true});
            skLineSegment(sketch, "E15.2.13.5", {"start": v(170.47, -50.8) * mm, "end": v(173.22, -46.04) * mm});
            skLineSegment(sketch, "E15.5.13.5", {"start": v(173.22, -46.04) * mm, "end": v(178.72, -46.04) * mm});
            skLineSegment(sketch, "E15.8.13.5", {"start": v(178.72, -46.04) * mm, "end": v(181.47, -50.8) * mm});
            skLineSegment(sketch, "E15.11.13.5", {"start": v(181.47, -50.8) * mm, "end": v(178.72, -55.56) * mm});
            skLineSegment(sketch, "E15.14.13.5", {"start": v(178.72, -55.56) * mm, "end": v(173.22, -55.56) * mm});
            skLineSegment(sketch, "E15.17.13.5", {"start": v(173.22, -55.56) * mm, "end": v(170.47, -50.8) * mm});
            skCircle(sketch, "E15.0.13.6", {"center": v(175.97, -38.1) * mm, "radius": 4.76 * mm, "construction": true});
            skLineSegment(sketch, "E15.2.13.6", {"start": v(170.47, -38.1) * mm, "end": v(173.22, -33.34) * mm});
            skLineSegment(sketch, "E15.5.13.6", {"start": v(173.22, -33.34) * mm, "end": v(178.72, -33.34) * mm});
            skLineSegment(sketch, "E15.8.13.6", {"start": v(178.72, -33.34) * mm, "end": v(181.47, -38.1) * mm});
            skLineSegment(sketch, "E15.11.13.6", {"start": v(181.47, -38.1) * mm, "end": v(178.72, -42.86) * mm});
            skLineSegment(sketch, "E15.14.13.6", {"start": v(178.72, -42.86) * mm, "end": v(173.22, -42.86) * mm});
            skLineSegment(sketch, "E15.17.13.6", {"start": v(173.22, -42.86) * mm, "end": v(170.47, -38.1) * mm});
            skCircle(sketch, "E15.0.13.7", {"center": v(175.97, -25.4) * mm, "radius": 4.76 * mm, "construction": true});
            skLineSegment(sketch, "E15.2.13.7", {"start": v(170.47, -25.4) * mm, "end": v(173.22, -20.64) * mm});
            skLineSegment(sketch, "E15.5.13.7", {"start": v(173.22, -20.64) * mm, "end": v(178.72, -20.64) * mm});
            skLineSegment(sketch, "E15.8.13.7", {"start": v(178.72, -20.64) * mm, "end": v(181.47, -25.4) * mm});
            skLineSegment(sketch, "E15.11.13.7", {"start": v(181.47, -25.4) * mm, "end": v(178.72, -30.16) * mm});
            skLineSegment(sketch, "E15.14.13.7", {"start": v(178.72, -30.16) * mm, "end": v(173.22, -30.16) * mm});
            skLineSegment(sketch, "E15.17.13.7", {"start": v(173.22, -30.16) * mm, "end": v(170.47, -25.4) * mm});
            skCircle(sketch, "E15.0.13.8", {"center": v(175.97, -12.7) * mm, "radius": 4.76 * mm, "construction": true});
            skLineSegment(sketch, "E15.2.13.8", {"start": v(170.47, -12.7) * mm, "end": v(173.22, -7.94) * mm});
            skLineSegment(sketch, "E15.5.13.8", {"start": v(173.22, -7.94) * mm, "end": v(178.72, -7.94) * mm});
            skLineSegment(sketch, "E15.8.13.8", {"start": v(178.72, -7.94) * mm, "end": v(181.47, -12.7) * mm});
            skLineSegment(sketch, "E15.11.13.8", {"start": v(181.47, -12.7) * mm, "end": v(178.72, -17.46) * mm});
            skLineSegment(sketch, "E15.14.13.8", {"start": v(178.72, -17.46) * mm, "end": v(173.22, -17.46) * mm});
            skLineSegment(sketch, "E15.17.13.8", {"start": v(173.22, -17.46) * mm, "end": v(170.47, -12.7) * mm});
            skCircle(sketch, "E15.0.13.9", {"center": v(175.97, 0) * mm, "radius": 4.76 * mm, "construction": true});
            skLineSegment(sketch, "E15.2.13.9", {"start": v(170.47, 0) * mm, "end": v(173.22, 4.76) * mm});
            skLineSegment(sketch, "E15.5.13.9", {"start": v(173.22, 4.76) * mm, "end": v(178.72, 4.76) * mm});
            skLineSegment(sketch, "E15.8.13.9", {"start": v(178.72, 4.76) * mm, "end": v(181.47, 0) * mm});
            skLineSegment(sketch, "E15.11.13.9", {"start": v(181.47, 0) * mm, "end": v(178.72, -4.76) * mm});
            skLineSegment(sketch, "E15.14.13.9", {"start": v(178.72, -4.76) * mm, "end": v(173.22, -4.76) * mm});
            skLineSegment(sketch, "E15.17.13.9", {"start": v(173.22, -4.76) * mm, "end": v(170.47, 0) * mm});
            skCircle(sketch, "E15.0.13.10", {"center": v(175.97, 12.7) * mm, "radius": 4.76 * mm, "construction": true});
            skLineSegment(sketch, "E15.2.13.10", {"start": v(170.47, 12.7) * mm, "end": v(173.22, 17.46) * mm});
            skLineSegment(sketch, "E15.5.13.10", {"start": v(173.22, 17.46) * mm, "end": v(178.72, 17.46) * mm});
            skLineSegment(sketch, "E15.8.13.10", {"start": v(178.72, 17.46) * mm, "end": v(181.47, 12.7) * mm});
            skLineSegment(sketch, "E15.11.13.10", {"start": v(181.47, 12.7) * mm, "end": v(178.72, 7.94) * mm});
            skLineSegment(sketch, "E15.14.13.10", {"start": v(178.72, 7.94) * mm, "end": v(173.22, 7.94) * mm});
            skLineSegment(sketch, "E15.17.13.10", {"start": v(173.22, 7.94) * mm, "end": v(170.47, 12.7) * mm});
            skCircle(sketch, "E15.0.13.11", {"center": v(175.97, 25.4) * mm, "radius": 4.76 * mm, "construction": true});
            skLineSegment(sketch, "E15.2.13.11", {"start": v(170.47, 25.4) * mm, "end": v(173.22, 30.16) * mm});
            skLineSegment(sketch, "E15.5.13.11", {"start": v(173.22, 30.16) * mm, "end": v(178.72, 30.16) * mm});
            skLineSegment(sketch, "E15.8.13.11", {"start": v(178.72, 30.16) * mm, "end": v(181.47, 25.4) * mm});
            skLineSegment(sketch, "E15.11.13.11", {"start": v(181.47, 25.4) * mm, "end": v(178.72, 20.64) * mm});
            skLineSegment(sketch, "E15.14.13.11", {"start": v(178.72, 20.64) * mm, "end": v(173.22, 20.64) * mm});
            skLineSegment(sketch, "E15.17.13.11", {"start": v(173.22, 20.64) * mm, "end": v(170.47, 25.4) * mm});
            skCircle(sketch, "E15.0.13.12", {"center": v(175.97, 38.1) * mm, "radius": 4.76 * mm, "construction": true});
            skLineSegment(sketch, "E15.2.13.12", {"start": v(170.47, 38.1) * mm, "end": v(173.22, 42.86) * mm});
            skLineSegment(sketch, "E15.5.13.12", {"start": v(173.22, 42.86) * mm, "end": v(178.72, 42.86) * mm});
            skLineSegment(sketch, "E15.8.13.12", {"start": v(178.72, 42.86) * mm, "end": v(181.47, 38.1) * mm});
            skLineSegment(sketch, "E15.11.13.12", {"start": v(181.47, 38.1) * mm, "end": v(178.72, 33.34) * mm});
            skLineSegment(sketch, "E15.14.13.12", {"start": v(178.72, 33.34) * mm, "end": v(173.22, 33.34) * mm});
            skLineSegment(sketch, "E15.17.13.12", {"start": v(173.22, 33.34) * mm, "end": v(170.47, 38.1) * mm});
            skCircle(sketch, "E15.0.13.13", {"center": v(175.97, 50.8) * mm, "radius": 4.76 * mm, "construction": true});
            skLineSegment(sketch, "E15.2.13.13", {"start": v(170.47, 50.8) * mm, "end": v(173.22, 55.56) * mm});
            skLineSegment(sketch, "E15.5.13.13", {"start": v(173.22, 55.56) * mm, "end": v(178.72, 55.56) * mm});
            skLineSegment(sketch, "E15.8.13.13", {"start": v(178.72, 55.56) * mm, "end": v(181.47, 50.8) * mm});
            skLineSegment(sketch, "E15.11.13.13", {"start": v(181.47, 50.8) * mm, "end": v(178.72, 46.04) * mm});
            skLineSegment(sketch, "E15.14.13.13", {"start": v(178.72, 46.04) * mm, "end": v(173.22, 46.04) * mm});
            skLineSegment(sketch, "E15.17.13.13", {"start": v(173.22, 46.04) * mm, "end": v(170.47, 50.8) * mm});
            skCircle(sketch, "E15.0.13.14", {"center": v(175.97, 63.5) * mm, "radius": 4.76 * mm, "construction": true});
            skLineSegment(sketch, "E15.2.13.14", {"start": v(170.47, 63.5) * mm, "end": v(173.22, 68.26) * mm});
            skLineSegment(sketch, "E15.5.13.14", {"start": v(173.22, 68.26) * mm, "end": v(178.72, 68.26) * mm});
            skLineSegment(sketch, "E15.8.13.14", {"start": v(178.72, 68.26) * mm, "end": v(181.47, 63.5) * mm});
            skLineSegment(sketch, "E15.11.13.14", {"start": v(181.47, 63.5) * mm, "end": v(178.72, 58.74) * mm});
            skLineSegment(sketch, "E15.14.13.14", {"start": v(178.72, 58.74) * mm, "end": v(173.22, 58.74) * mm});
            skLineSegment(sketch, "E15.17.13.14", {"start": v(173.22, 58.74) * mm, "end": v(170.47, 63.5) * mm});
            skCircle(sketch, "E15.0.13.15", {"center": v(175.97, 76.2) * mm, "radius": 4.76 * mm, "construction": true});
            skLineSegment(sketch, "E15.2.13.15", {"start": v(170.47, 76.2) * mm, "end": v(173.22, 80.96) * mm});
            skLineSegment(sketch, "E15.5.13.15", {"start": v(173.22, 80.96) * mm, "end": v(178.72, 80.96) * mm});
            skLineSegment(sketch, "E15.8.13.15", {"start": v(178.72, 80.96) * mm, "end": v(181.47, 76.2) * mm});
            skLineSegment(sketch, "E15.11.13.15", {"start": v(181.47, 76.2) * mm, "end": v(178.72, 71.44) * mm});
            skLineSegment(sketch, "E15.14.13.15", {"start": v(178.72, 71.44) * mm, "end": v(173.22, 71.44) * mm});
            skLineSegment(sketch, "E15.17.13.15", {"start": v(173.22, 71.44) * mm, "end": v(170.47, 76.2) * mm});
            skCircle(sketch, "E15.0.13.16", {"center": v(175.97, 88.9) * mm, "radius": 4.76 * mm, "construction": true});
            skLineSegment(sketch, "E15.2.13.16", {"start": v(170.47, 88.9) * mm, "end": v(173.22, 93.66) * mm});
            skLineSegment(sketch, "E15.5.13.16", {"start": v(173.22, 93.66) * mm, "end": v(178.72, 93.66) * mm});
            skLineSegment(sketch, "E15.8.13.16", {"start": v(178.72, 93.66) * mm, "end": v(181.47, 88.9) * mm});
            skLineSegment(sketch, "E15.11.13.16", {"start": v(181.47, 88.9) * mm, "end": v(178.72, 84.14) * mm});
            skLineSegment(sketch, "E15.14.13.16", {"start": v(178.72, 84.14) * mm, "end": v(173.22, 84.14) * mm});
            skLineSegment(sketch, "E15.17.13.16", {"start": v(173.22, 84.14) * mm, "end": v(170.47, 88.9) * mm});
            skCircle(sketch, "E15.0.13.17", {"center": v(175.97, 101.6) * mm, "radius": 4.76 * mm, "construction": true});
            skLineSegment(sketch, "E15.2.13.17", {"start": v(170.47, 101.6) * mm, "end": v(173.22, 106.36) * mm});
            skLineSegment(sketch, "E15.5.13.17", {"start": v(173.22, 106.36) * mm, "end": v(178.72, 106.36) * mm});
            skLineSegment(sketch, "E15.8.13.17", {"start": v(178.72, 106.36) * mm, "end": v(181.47, 101.6) * mm});
            skLineSegment(sketch, "E15.11.13.17", {"start": v(181.47, 101.6) * mm, "end": v(178.72, 96.84) * mm});
            skLineSegment(sketch, "E15.14.13.17", {"start": v(178.72, 96.84) * mm, "end": v(173.22, 96.84) * mm});
            skLineSegment(sketch, "E15.17.13.17", {"start": v(173.22, 96.84) * mm, "end": v(170.47, 101.6) * mm});
            skCircle(sketch, "E15.0.13.18", {"center": v(175.97, 114.3) * mm, "radius": 4.76 * mm, "construction": true});
            skLineSegment(sketch, "E15.2.13.18", {"start": v(170.47, 114.3) * mm, "end": v(173.22, 119.06) * mm});
            skLineSegment(sketch, "E15.5.13.18", {"start": v(173.22, 119.06) * mm, "end": v(178.72, 119.06) * mm});
            skLineSegment(sketch, "E15.8.13.18", {"start": v(178.72, 119.06) * mm, "end": v(181.47, 114.3) * mm});
            skLineSegment(sketch, "E15.11.13.18", {"start": v(181.47, 114.3) * mm, "end": v(178.72, 109.54) * mm});
            skLineSegment(sketch, "E15.14.13.18", {"start": v(178.72, 109.54) * mm, "end": v(173.22, 109.54) * mm});
            skLineSegment(sketch, "E15.17.13.18", {"start": v(173.22, 109.54) * mm, "end": v(170.47, 114.3) * mm});
            skCircle(sketch, "E15.0.13.19", {"center": v(175.97, 127) * mm, "radius": 4.76 * mm, "construction": true});
            skLineSegment(sketch, "E15.2.13.19", {"start": v(170.47, 127) * mm, "end": v(173.22, 131.76) * mm});
            skLineSegment(sketch, "E15.5.13.19", {"start": v(173.22, 131.76) * mm, "end": v(178.72, 131.76) * mm});
            skLineSegment(sketch, "E15.8.13.19", {"start": v(178.72, 131.76) * mm, "end": v(181.47, 127) * mm});
            skLineSegment(sketch, "E15.11.13.19", {"start": v(181.47, 127) * mm, "end": v(178.72, 122.24) * mm});
            skLineSegment(sketch, "E15.14.13.19", {"start": v(178.72, 122.24) * mm, "end": v(173.22, 122.24) * mm});
            skLineSegment(sketch, "E15.17.13.19", {"start": v(173.22, 122.24) * mm, "end": v(170.47, 127) * mm});
            skCircle(sketch, "E15.0.14.0", {"center": v(197.97, -114.3) * mm, "radius": 4.76 * mm, "construction": true});
            skLineSegment(sketch, "E15.2.14.0", {"start": v(192.47, -114.3) * mm, "end": v(195.22, -109.54) * mm});
            skLineSegment(sketch, "E15.5.14.0", {"start": v(195.22, -109.54) * mm, "end": v(200.72, -109.54) * mm});
            skLineSegment(sketch, "E15.8.14.0", {"start": v(200.72, -109.54) * mm, "end": v(203.47, -114.3) * mm});
            skLineSegment(sketch, "E15.11.14.0", {"start": v(203.47, -114.3) * mm, "end": v(200.72, -119.06) * mm});
            skLineSegment(sketch, "E15.14.14.0", {"start": v(200.72, -119.06) * mm, "end": v(195.22, -119.06) * mm});
            skLineSegment(sketch, "E15.17.14.0", {"start": v(195.22, -119.06) * mm, "end": v(192.47, -114.3) * mm});
            skCircle(sketch, "E15.0.14.1", {"center": v(197.97, -101.6) * mm, "radius": 4.76 * mm, "construction": true});
            skLineSegment(sketch, "E15.2.14.1", {"start": v(192.47, -101.6) * mm, "end": v(195.22, -96.84) * mm});
            skLineSegment(sketch, "E15.5.14.1", {"start": v(195.22, -96.84) * mm, "end": v(200.72, -96.84) * mm});
            skLineSegment(sketch, "E15.8.14.1", {"start": v(200.72, -96.84) * mm, "end": v(203.47, -101.6) * mm});
            skLineSegment(sketch, "E15.11.14.1", {"start": v(203.47, -101.6) * mm, "end": v(200.72, -106.36) * mm});
            skLineSegment(sketch, "E15.14.14.1", {"start": v(200.72, -106.36) * mm, "end": v(195.22, -106.36) * mm});
            skLineSegment(sketch, "E15.17.14.1", {"start": v(195.22, -106.36) * mm, "end": v(192.47, -101.6) * mm});
            skCircle(sketch, "E15.0.14.2", {"center": v(197.97, -88.9) * mm, "radius": 4.76 * mm, "construction": true});
            skLineSegment(sketch, "E15.2.14.2", {"start": v(192.47, -88.9) * mm, "end": v(195.22, -84.14) * mm});
            skLineSegment(sketch, "E15.5.14.2", {"start": v(195.22, -84.14) * mm, "end": v(200.72, -84.14) * mm});
            skLineSegment(sketch, "E15.8.14.2", {"start": v(200.72, -84.14) * mm, "end": v(203.47, -88.9) * mm});
            skLineSegment(sketch, "E15.11.14.2", {"start": v(203.47, -88.9) * mm, "end": v(200.72, -93.66) * mm});
            skLineSegment(sketch, "E15.14.14.2", {"start": v(200.72, -93.66) * mm, "end": v(195.22, -93.66) * mm});
            skLineSegment(sketch, "E15.17.14.2", {"start": v(195.22, -93.66) * mm, "end": v(192.47, -88.9) * mm});
            skCircle(sketch, "E15.0.14.3", {"center": v(197.97, -76.2) * mm, "radius": 4.76 * mm, "construction": true});
            skLineSegment(sketch, "E15.2.14.3", {"start": v(192.47, -76.2) * mm, "end": v(195.22, -71.44) * mm});
            skLineSegment(sketch, "E15.5.14.3", {"start": v(195.22, -71.44) * mm, "end": v(200.72, -71.44) * mm});
            skLineSegment(sketch, "E15.8.14.3", {"start": v(200.72, -71.44) * mm, "end": v(203.47, -76.2) * mm});
            skLineSegment(sketch, "E15.11.14.3", {"start": v(203.47, -76.2) * mm, "end": v(200.72, -80.96) * mm});
            skLineSegment(sketch, "E15.14.14.3", {"start": v(200.72, -80.96) * mm, "end": v(195.22, -80.96) * mm});
            skLineSegment(sketch, "E15.17.14.3", {"start": v(195.22, -80.96) * mm, "end": v(192.47, -76.2) * mm});
            skCircle(sketch, "E15.0.14.4", {"center": v(197.97, -63.5) * mm, "radius": 4.76 * mm, "construction": true});
            skLineSegment(sketch, "E15.2.14.4", {"start": v(192.47, -63.5) * mm, "end": v(195.22, -58.74) * mm});
            skLineSegment(sketch, "E15.5.14.4", {"start": v(195.22, -58.74) * mm, "end": v(200.72, -58.74) * mm});
            skLineSegment(sketch, "E15.8.14.4", {"start": v(200.72, -58.74) * mm, "end": v(203.47, -63.5) * mm});
            skLineSegment(sketch, "E15.11.14.4", {"start": v(203.47, -63.5) * mm, "end": v(200.72, -68.26) * mm});
            skLineSegment(sketch, "E15.14.14.4", {"start": v(200.72, -68.26) * mm, "end": v(195.22, -68.26) * mm});
            skLineSegment(sketch, "E15.17.14.4", {"start": v(195.22, -68.26) * mm, "end": v(192.47, -63.5) * mm});
            skCircle(sketch, "E15.0.14.5", {"center": v(197.97, -50.8) * mm, "radius": 4.76 * mm, "construction": true});
            skLineSegment(sketch, "E15.2.14.5", {"start": v(192.47, -50.8) * mm, "end": v(195.22, -46.04) * mm});
            skLineSegment(sketch, "E15.5.14.5", {"start": v(195.22, -46.04) * mm, "end": v(200.72, -46.04) * mm});
            skLineSegment(sketch, "E15.8.14.5", {"start": v(200.72, -46.04) * mm, "end": v(203.47, -50.8) * mm});
            skLineSegment(sketch, "E15.11.14.5", {"start": v(203.47, -50.8) * mm, "end": v(200.72, -55.56) * mm});
            skLineSegment(sketch, "E15.14.14.5", {"start": v(200.72, -55.56) * mm, "end": v(195.22, -55.56) * mm});
            skLineSegment(sketch, "E15.17.14.5", {"start": v(195.22, -55.56) * mm, "end": v(192.47, -50.8) * mm});
            skCircle(sketch, "E15.0.14.6", {"center": v(197.97, -38.1) * mm, "radius": 4.76 * mm, "construction": true});
            skLineSegment(sketch, "E15.2.14.6", {"start": v(192.47, -38.1) * mm, "end": v(195.22, -33.34) * mm});
            skLineSegment(sketch, "E15.5.14.6", {"start": v(195.22, -33.34) * mm, "end": v(200.72, -33.34) * mm});
            skLineSegment(sketch, "E15.8.14.6", {"start": v(200.72, -33.34) * mm, "end": v(203.47, -38.1) * mm});
            skLineSegment(sketch, "E15.11.14.6", {"start": v(203.47, -38.1) * mm, "end": v(200.72, -42.86) * mm});
            skLineSegment(sketch, "E15.14.14.6", {"start": v(200.72, -42.86) * mm, "end": v(195.22, -42.86) * mm});
            skLineSegment(sketch, "E15.17.14.6", {"start": v(195.22, -42.86) * mm, "end": v(192.47, -38.1) * mm});
            skCircle(sketch, "E15.0.14.7", {"center": v(197.97, -25.4) * mm, "radius": 4.76 * mm, "construction": true});
            skLineSegment(sketch, "E15.2.14.7", {"start": v(192.47, -25.4) * mm, "end": v(195.22, -20.64) * mm});
            skLineSegment(sketch, "E15.5.14.7", {"start": v(195.22, -20.64) * mm, "end": v(200.72, -20.64) * mm});
            skLineSegment(sketch, "E15.8.14.7", {"start": v(200.72, -20.64) * mm, "end": v(203.47, -25.4) * mm});
            skLineSegment(sketch, "E15.11.14.7", {"start": v(203.47, -25.4) * mm, "end": v(200.72, -30.16) * mm});
            skLineSegment(sketch, "E15.14.14.7", {"start": v(200.72, -30.16) * mm, "end": v(195.22, -30.16) * mm});
            skLineSegment(sketch, "E15.17.14.7", {"start": v(195.22, -30.16) * mm, "end": v(192.47, -25.4) * mm});
            skCircle(sketch, "E15.0.14.8", {"center": v(197.97, -12.7) * mm, "radius": 4.76 * mm, "construction": true});
            skLineSegment(sketch, "E15.2.14.8", {"start": v(192.47, -12.7) * mm, "end": v(195.22, -7.94) * mm});
            skLineSegment(sketch, "E15.5.14.8", {"start": v(195.22, -7.94) * mm, "end": v(200.72, -7.94) * mm});
            skLineSegment(sketch, "E15.8.14.8", {"start": v(200.72, -7.94) * mm, "end": v(203.47, -12.7) * mm});
            skLineSegment(sketch, "E15.11.14.8", {"start": v(203.47, -12.7) * mm, "end": v(200.72, -17.46) * mm});
            skLineSegment(sketch, "E15.14.14.8", {"start": v(200.72, -17.46) * mm, "end": v(195.22, -17.46) * mm});
            skLineSegment(sketch, "E15.17.14.8", {"start": v(195.22, -17.46) * mm, "end": v(192.47, -12.7) * mm});
            skCircle(sketch, "E15.0.14.9", {"center": v(197.97, 0) * mm, "radius": 4.76 * mm, "construction": true});
            skLineSegment(sketch, "E15.2.14.9", {"start": v(192.47, 0) * mm, "end": v(195.22, 4.76) * mm});
            skLineSegment(sketch, "E15.5.14.9", {"start": v(195.22, 4.76) * mm, "end": v(200.72, 4.76) * mm});
            skLineSegment(sketch, "E15.8.14.9", {"start": v(200.72, 4.76) * mm, "end": v(203.47, 0) * mm});
            skLineSegment(sketch, "E15.11.14.9", {"start": v(203.47, 0) * mm, "end": v(200.72, -4.76) * mm});
            skLineSegment(sketch, "E15.14.14.9", {"start": v(200.72, -4.76) * mm, "end": v(195.22, -4.76) * mm});
            skLineSegment(sketch, "E15.17.14.9", {"start": v(195.22, -4.76) * mm, "end": v(192.47, 0) * mm});
            skCircle(sketch, "E15.0.14.10", {"center": v(197.97, 12.7) * mm, "radius": 4.76 * mm, "construction": true});
            skLineSegment(sketch, "E15.2.14.10", {"start": v(192.47, 12.7) * mm, "end": v(195.22, 17.46) * mm});
            skLineSegment(sketch, "E15.5.14.10", {"start": v(195.22, 17.46) * mm, "end": v(200.72, 17.46) * mm});
            skLineSegment(sketch, "E15.8.14.10", {"start": v(200.72, 17.46) * mm, "end": v(203.47, 12.7) * mm});
            skLineSegment(sketch, "E15.11.14.10", {"start": v(203.47, 12.7) * mm, "end": v(200.72, 7.94) * mm});
            skLineSegment(sketch, "E15.14.14.10", {"start": v(200.72, 7.94) * mm, "end": v(195.22, 7.94) * mm});
            skLineSegment(sketch, "E15.17.14.10", {"start": v(195.22, 7.94) * mm, "end": v(192.47, 12.7) * mm});
            skCircle(sketch, "E15.0.14.11", {"center": v(197.97, 25.4) * mm, "radius": 4.76 * mm, "construction": true});
            skLineSegment(sketch, "E15.2.14.11", {"start": v(192.47, 25.4) * mm, "end": v(195.22, 30.16) * mm});
            skLineSegment(sketch, "E15.5.14.11", {"start": v(195.22, 30.16) * mm, "end": v(200.72, 30.16) * mm});
            skLineSegment(sketch, "E15.8.14.11", {"start": v(200.72, 30.16) * mm, "end": v(203.47, 25.4) * mm});
            skLineSegment(sketch, "E15.11.14.11", {"start": v(203.47, 25.4) * mm, "end": v(200.72, 20.64) * mm});
            skLineSegment(sketch, "E15.14.14.11", {"start": v(200.72, 20.64) * mm, "end": v(195.22, 20.64) * mm});
            skLineSegment(sketch, "E15.17.14.11", {"start": v(195.22, 20.64) * mm, "end": v(192.47, 25.4) * mm});
            skCircle(sketch, "E15.0.14.12", {"center": v(197.97, 38.1) * mm, "radius": 4.76 * mm, "construction": true});
            skLineSegment(sketch, "E15.2.14.12", {"start": v(192.47, 38.1) * mm, "end": v(195.22, 42.86) * mm});
            skLineSegment(sketch, "E15.5.14.12", {"start": v(195.22, 42.86) * mm, "end": v(200.72, 42.86) * mm});
            skLineSegment(sketch, "E15.8.14.12", {"start": v(200.72, 42.86) * mm, "end": v(203.47, 38.1) * mm});
            skLineSegment(sketch, "E15.11.14.12", {"start": v(203.47, 38.1) * mm, "end": v(200.72, 33.34) * mm});
            skLineSegment(sketch, "E15.14.14.12", {"start": v(200.72, 33.34) * mm, "end": v(195.22, 33.34) * mm});
            skLineSegment(sketch, "E15.17.14.12", {"start": v(195.22, 33.34) * mm, "end": v(192.47, 38.1) * mm});
            skCircle(sketch, "E15.0.14.13", {"center": v(197.97, 50.8) * mm, "radius": 4.76 * mm, "construction": true});
            skLineSegment(sketch, "E15.2.14.13", {"start": v(192.47, 50.8) * mm, "end": v(195.22, 55.56) * mm});
            skLineSegment(sketch, "E15.5.14.13", {"start": v(195.22, 55.56) * mm, "end": v(200.72, 55.56) * mm});
            skLineSegment(sketch, "E15.8.14.13", {"start": v(200.72, 55.56) * mm, "end": v(203.47, 50.8) * mm});
            skLineSegment(sketch, "E15.11.14.13", {"start": v(203.47, 50.8) * mm, "end": v(200.72, 46.04) * mm});
            skLineSegment(sketch, "E15.14.14.13", {"start": v(200.72, 46.04) * mm, "end": v(195.22, 46.04) * mm});
            skLineSegment(sketch, "E15.17.14.13", {"start": v(195.22, 46.04) * mm, "end": v(192.47, 50.8) * mm});
            skCircle(sketch, "E15.0.14.14", {"center": v(197.97, 63.5) * mm, "radius": 4.76 * mm, "construction": true});
            skLineSegment(sketch, "E15.2.14.14", {"start": v(192.47, 63.5) * mm, "end": v(195.22, 68.26) * mm});
            skLineSegment(sketch, "E15.5.14.14", {"start": v(195.22, 68.26) * mm, "end": v(200.72, 68.26) * mm});
            skLineSegment(sketch, "E15.8.14.14", {"start": v(200.72, 68.26) * mm, "end": v(203.47, 63.5) * mm});
            skLineSegment(sketch, "E15.11.14.14", {"start": v(203.47, 63.5) * mm, "end": v(200.72, 58.74) * mm});
            skLineSegment(sketch, "E15.14.14.14", {"start": v(200.72, 58.74) * mm, "end": v(195.22, 58.74) * mm});
            skLineSegment(sketch, "E15.17.14.14", {"start": v(195.22, 58.74) * mm, "end": v(192.47, 63.5) * mm});
            skCircle(sketch, "E15.0.14.15", {"center": v(197.97, 76.2) * mm, "radius": 4.76 * mm, "construction": true});
            skLineSegment(sketch, "E15.2.14.15", {"start": v(192.47, 76.2) * mm, "end": v(195.22, 80.96) * mm});
            skLineSegment(sketch, "E15.5.14.15", {"start": v(195.22, 80.96) * mm, "end": v(200.72, 80.96) * mm});
            skLineSegment(sketch, "E15.8.14.15", {"start": v(200.72, 80.96) * mm, "end": v(203.47, 76.2) * mm});
            skLineSegment(sketch, "E15.11.14.15", {"start": v(203.47, 76.2) * mm, "end": v(200.72, 71.44) * mm});
            skLineSegment(sketch, "E15.14.14.15", {"start": v(200.72, 71.44) * mm, "end": v(195.22, 71.44) * mm});
            skLineSegment(sketch, "E15.17.14.15", {"start": v(195.22, 71.44) * mm, "end": v(192.47, 76.2) * mm});
            skCircle(sketch, "E15.0.14.16", {"center": v(197.97, 88.9) * mm, "radius": 4.76 * mm, "construction": true});
            skLineSegment(sketch, "E15.2.14.16", {"start": v(192.47, 88.9) * mm, "end": v(195.22, 93.66) * mm});
            skLineSegment(sketch, "E15.5.14.16", {"start": v(195.22, 93.66) * mm, "end": v(200.72, 93.66) * mm});
            skLineSegment(sketch, "E15.8.14.16", {"start": v(200.72, 93.66) * mm, "end": v(203.47, 88.9) * mm});
            skLineSegment(sketch, "E15.11.14.16", {"start": v(203.47, 88.9) * mm, "end": v(200.72, 84.14) * mm});
            skLineSegment(sketch, "E15.14.14.16", {"start": v(200.72, 84.14) * mm, "end": v(195.22, 84.14) * mm});
            skLineSegment(sketch, "E15.17.14.16", {"start": v(195.22, 84.14) * mm, "end": v(192.47, 88.9) * mm});
            skCircle(sketch, "E15.0.14.17", {"center": v(197.97, 101.6) * mm, "radius": 4.76 * mm, "construction": true});
            skLineSegment(sketch, "E15.2.14.17", {"start": v(192.47, 101.6) * mm, "end": v(195.22, 106.36) * mm});
            skLineSegment(sketch, "E15.5.14.17", {"start": v(195.22, 106.36) * mm, "end": v(200.72, 106.36) * mm});
            skLineSegment(sketch, "E15.8.14.17", {"start": v(200.72, 106.36) * mm, "end": v(203.47, 101.6) * mm});
            skLineSegment(sketch, "E15.11.14.17", {"start": v(203.47, 101.6) * mm, "end": v(200.72, 96.84) * mm});
            skLineSegment(sketch, "E15.14.14.17", {"start": v(200.72, 96.84) * mm, "end": v(195.22, 96.84) * mm});
            skLineSegment(sketch, "E15.17.14.17", {"start": v(195.22, 96.84) * mm, "end": v(192.47, 101.6) * mm});
            skCircle(sketch, "E15.0.14.18", {"center": v(197.97, 114.3) * mm, "radius": 4.76 * mm, "construction": true});
            skLineSegment(sketch, "E15.2.14.18", {"start": v(192.47, 114.3) * mm, "end": v(195.22, 119.06) * mm});
            skLineSegment(sketch, "E15.5.14.18", {"start": v(195.22, 119.06) * mm, "end": v(200.72, 119.06) * mm});
            skLineSegment(sketch, "E15.8.14.18", {"start": v(200.72, 119.06) * mm, "end": v(203.47, 114.3) * mm});
            skLineSegment(sketch, "E15.11.14.18", {"start": v(203.47, 114.3) * mm, "end": v(200.72, 109.54) * mm});
            skLineSegment(sketch, "E15.14.14.18", {"start": v(200.72, 109.54) * mm, "end": v(195.22, 109.54) * mm});
            skLineSegment(sketch, "E15.17.14.18", {"start": v(195.22, 109.54) * mm, "end": v(192.47, 114.3) * mm});
            skCircle(sketch, "E15.0.14.19", {"center": v(197.97, 127) * mm, "radius": 4.76 * mm, "construction": true});
            skLineSegment(sketch, "E15.2.14.19", {"start": v(192.47, 127) * mm, "end": v(195.22, 131.76) * mm});
            skLineSegment(sketch, "E15.5.14.19", {"start": v(195.22, 131.76) * mm, "end": v(200.72, 131.76) * mm});
            skLineSegment(sketch, "E15.8.14.19", {"start": v(200.72, 131.76) * mm, "end": v(203.47, 127) * mm});
            skLineSegment(sketch, "E15.11.14.19", {"start": v(203.47, 127) * mm, "end": v(200.72, 122.24) * mm});
            skLineSegment(sketch, "E15.14.14.19", {"start": v(200.72, 122.24) * mm, "end": v(195.22, 122.24) * mm});
            skLineSegment(sketch, "E15.17.14.19", {"start": v(195.22, 122.24) * mm, "end": v(192.47, 127) * mm});
            skCircle(sketch, "E15.0.15.0", {"center": v(219.96, -114.3) * mm, "radius": 4.76 * mm, "construction": true});
            skLineSegment(sketch, "E15.2.15.0", {"start": v(214.46, -114.3) * mm, "end": v(217.21, -109.54) * mm});
            skLineSegment(sketch, "E15.5.15.0", {"start": v(217.21, -109.54) * mm, "end": v(222.71, -109.54) * mm});
            skLineSegment(sketch, "E15.8.15.0", {"start": v(222.71, -109.54) * mm, "end": v(225.46, -114.3) * mm});
            skLineSegment(sketch, "E15.11.15.0", {"start": v(225.46, -114.3) * mm, "end": v(222.71, -119.06) * mm});
            skLineSegment(sketch, "E15.14.15.0", {"start": v(222.71, -119.06) * mm, "end": v(217.21, -119.06) * mm});
            skLineSegment(sketch, "E15.17.15.0", {"start": v(217.21, -119.06) * mm, "end": v(214.46, -114.3) * mm});
            skCircle(sketch, "E15.0.15.1", {"center": v(219.96, -101.6) * mm, "radius": 4.76 * mm, "construction": true});
            skLineSegment(sketch, "E15.2.15.1", {"start": v(214.46, -101.6) * mm, "end": v(217.21, -96.84) * mm});
            skLineSegment(sketch, "E15.5.15.1", {"start": v(217.21, -96.84) * mm, "end": v(222.71, -96.84) * mm});
            skLineSegment(sketch, "E15.8.15.1", {"start": v(222.71, -96.84) * mm, "end": v(225.46, -101.6) * mm});
            skLineSegment(sketch, "E15.11.15.1", {"start": v(225.46, -101.6) * mm, "end": v(222.71, -106.36) * mm});
            skLineSegment(sketch, "E15.14.15.1", {"start": v(222.71, -106.36) * mm, "end": v(217.21, -106.36) * mm});
            skLineSegment(sketch, "E15.17.15.1", {"start": v(217.21, -106.36) * mm, "end": v(214.46, -101.6) * mm});
            skCircle(sketch, "E15.0.15.2", {"center": v(219.96, -88.9) * mm, "radius": 4.76 * mm, "construction": true});
            skLineSegment(sketch, "E15.2.15.2", {"start": v(214.46, -88.9) * mm, "end": v(217.21, -84.14) * mm});
            skLineSegment(sketch, "E15.5.15.2", {"start": v(217.21, -84.14) * mm, "end": v(222.71, -84.14) * mm});
            skLineSegment(sketch, "E15.8.15.2", {"start": v(222.71, -84.14) * mm, "end": v(225.46, -88.9) * mm});
            skLineSegment(sketch, "E15.11.15.2", {"start": v(225.46, -88.9) * mm, "end": v(222.71, -93.66) * mm});
            skLineSegment(sketch, "E15.14.15.2", {"start": v(222.71, -93.66) * mm, "end": v(217.21, -93.66) * mm});
            skLineSegment(sketch, "E15.17.15.2", {"start": v(217.21, -93.66) * mm, "end": v(214.46, -88.9) * mm});
            skCircle(sketch, "E15.0.15.3", {"center": v(219.96, -76.2) * mm, "radius": 4.76 * mm, "construction": true});
            skLineSegment(sketch, "E15.2.15.3", {"start": v(214.46, -76.2) * mm, "end": v(217.21, -71.44) * mm});
            skLineSegment(sketch, "E15.5.15.3", {"start": v(217.21, -71.44) * mm, "end": v(222.71, -71.44) * mm});
            skLineSegment(sketch, "E15.8.15.3", {"start": v(222.71, -71.44) * mm, "end": v(225.46, -76.2) * mm});
            skLineSegment(sketch, "E15.11.15.3", {"start": v(225.46, -76.2) * mm, "end": v(222.71, -80.96) * mm});
            skLineSegment(sketch, "E15.14.15.3", {"start": v(222.71, -80.96) * mm, "end": v(217.21, -80.96) * mm});
            skLineSegment(sketch, "E15.17.15.3", {"start": v(217.21, -80.96) * mm, "end": v(214.46, -76.2) * mm});
            skCircle(sketch, "E15.0.15.4", {"center": v(219.96, -63.5) * mm, "radius": 4.76 * mm, "construction": true});
            skLineSegment(sketch, "E15.2.15.4", {"start": v(214.46, -63.5) * mm, "end": v(217.21, -58.74) * mm});
            skLineSegment(sketch, "E15.5.15.4", {"start": v(217.21, -58.74) * mm, "end": v(222.71, -58.74) * mm});
            skLineSegment(sketch, "E15.8.15.4", {"start": v(222.71, -58.74) * mm, "end": v(225.46, -63.5) * mm});
            skLineSegment(sketch, "E15.11.15.4", {"start": v(225.46, -63.5) * mm, "end": v(222.71, -68.26) * mm});
            skLineSegment(sketch, "E15.14.15.4", {"start": v(222.71, -68.26) * mm, "end": v(217.21, -68.26) * mm});
            skLineSegment(sketch, "E15.17.15.4", {"start": v(217.21, -68.26) * mm, "end": v(214.46, -63.5) * mm});
            skCircle(sketch, "E15.0.15.5", {"center": v(219.96, -50.8) * mm, "radius": 4.76 * mm, "construction": true});
            skLineSegment(sketch, "E15.2.15.5", {"start": v(214.46, -50.8) * mm, "end": v(217.21, -46.04) * mm});
            skLineSegment(sketch, "E15.5.15.5", {"start": v(217.21, -46.04) * mm, "end": v(222.71, -46.04) * mm});
            skLineSegment(sketch, "E15.8.15.5", {"start": v(222.71, -46.04) * mm, "end": v(225.46, -50.8) * mm});
            skLineSegment(sketch, "E15.11.15.5", {"start": v(225.46, -50.8) * mm, "end": v(222.71, -55.56) * mm});
            skLineSegment(sketch, "E15.14.15.5", {"start": v(222.71, -55.56) * mm, "end": v(217.21, -55.56) * mm});
            skLineSegment(sketch, "E15.17.15.5", {"start": v(217.21, -55.56) * mm, "end": v(214.46, -50.8) * mm});
            skCircle(sketch, "E15.0.15.6", {"center": v(219.96, -38.1) * mm, "radius": 4.76 * mm, "construction": true});
            skLineSegment(sketch, "E15.2.15.6", {"start": v(214.46, -38.1) * mm, "end": v(217.21, -33.34) * mm});
            skLineSegment(sketch, "E15.5.15.6", {"start": v(217.21, -33.34) * mm, "end": v(222.71, -33.34) * mm});
            skLineSegment(sketch, "E15.8.15.6", {"start": v(222.71, -33.34) * mm, "end": v(225.46, -38.1) * mm});
            skLineSegment(sketch, "E15.11.15.6", {"start": v(225.46, -38.1) * mm, "end": v(222.71, -42.86) * mm});
            skLineSegment(sketch, "E15.14.15.6", {"start": v(222.71, -42.86) * mm, "end": v(217.21, -42.86) * mm});
            skLineSegment(sketch, "E15.17.15.6", {"start": v(217.21, -42.86) * mm, "end": v(214.46, -38.1) * mm});
            skCircle(sketch, "E15.0.15.7", {"center": v(219.96, -25.4) * mm, "radius": 4.76 * mm, "construction": true});
            skLineSegment(sketch, "E15.2.15.7", {"start": v(214.46, -25.4) * mm, "end": v(217.21, -20.64) * mm});
            skLineSegment(sketch, "E15.5.15.7", {"start": v(217.21, -20.64) * mm, "end": v(222.71, -20.64) * mm});
            skLineSegment(sketch, "E15.8.15.7", {"start": v(222.71, -20.64) * mm, "end": v(225.46, -25.4) * mm});
            skLineSegment(sketch, "E15.11.15.7", {"start": v(225.46, -25.4) * mm, "end": v(222.71, -30.16) * mm});
            skLineSegment(sketch, "E15.14.15.7", {"start": v(222.71, -30.16) * mm, "end": v(217.21, -30.16) * mm});
            skLineSegment(sketch, "E15.17.15.7", {"start": v(217.21, -30.16) * mm, "end": v(214.46, -25.4) * mm});
            skCircle(sketch, "E15.0.15.8", {"center": v(219.96, -12.7) * mm, "radius": 4.76 * mm, "construction": true});
            skLineSegment(sketch, "E15.2.15.8", {"start": v(214.46, -12.7) * mm, "end": v(217.21, -7.94) * mm});
            skLineSegment(sketch, "E15.5.15.8", {"start": v(217.21, -7.94) * mm, "end": v(222.71, -7.94) * mm});
            skLineSegment(sketch, "E15.8.15.8", {"start": v(222.71, -7.94) * mm, "end": v(225.46, -12.7) * mm});
            skLineSegment(sketch, "E15.11.15.8", {"start": v(225.46, -12.7) * mm, "end": v(222.71, -17.46) * mm});
            skLineSegment(sketch, "E15.14.15.8", {"start": v(222.71, -17.46) * mm, "end": v(217.21, -17.46) * mm});
            skLineSegment(sketch, "E15.17.15.8", {"start": v(217.21, -17.46) * mm, "end": v(214.46, -12.7) * mm});
            skCircle(sketch, "E15.0.15.9", {"center": v(219.96, 0) * mm, "radius": 4.76 * mm, "construction": true});
            skLineSegment(sketch, "E15.2.15.9", {"start": v(214.46, 0) * mm, "end": v(217.21, 4.76) * mm});
            skLineSegment(sketch, "E15.5.15.9", {"start": v(217.21, 4.76) * mm, "end": v(222.71, 4.76) * mm});
            skLineSegment(sketch, "E15.8.15.9", {"start": v(222.71, 4.76) * mm, "end": v(225.46, 0) * mm});
            skLineSegment(sketch, "E15.11.15.9", {"start": v(225.46, 0) * mm, "end": v(222.71, -4.76) * mm});
            skLineSegment(sketch, "E15.14.15.9", {"start": v(222.71, -4.76) * mm, "end": v(217.21, -4.76) * mm});
            skLineSegment(sketch, "E15.17.15.9", {"start": v(217.21, -4.76) * mm, "end": v(214.46, 0) * mm});
            skCircle(sketch, "E15.0.15.10", {"center": v(219.96, 12.7) * mm, "radius": 4.76 * mm, "construction": true});
            skLineSegment(sketch, "E15.2.15.10", {"start": v(214.46, 12.7) * mm, "end": v(217.21, 17.46) * mm});
            skLineSegment(sketch, "E15.5.15.10", {"start": v(217.21, 17.46) * mm, "end": v(222.71, 17.46) * mm});
            skLineSegment(sketch, "E15.8.15.10", {"start": v(222.71, 17.46) * mm, "end": v(225.46, 12.7) * mm});
            skLineSegment(sketch, "E15.11.15.10", {"start": v(225.46, 12.7) * mm, "end": v(222.71, 7.94) * mm});
            skLineSegment(sketch, "E15.14.15.10", {"start": v(222.71, 7.94) * mm, "end": v(217.21, 7.94) * mm});
            skLineSegment(sketch, "E15.17.15.10", {"start": v(217.21, 7.94) * mm, "end": v(214.46, 12.7) * mm});
            skCircle(sketch, "E15.0.15.11", {"center": v(219.96, 25.4) * mm, "radius": 4.76 * mm, "construction": true});
            skLineSegment(sketch, "E15.2.15.11", {"start": v(214.46, 25.4) * mm, "end": v(217.21, 30.16) * mm});
            skLineSegment(sketch, "E15.5.15.11", {"start": v(217.21, 30.16) * mm, "end": v(222.71, 30.16) * mm});
            skLineSegment(sketch, "E15.8.15.11", {"start": v(222.71, 30.16) * mm, "end": v(225.46, 25.4) * mm});
            skLineSegment(sketch, "E15.11.15.11", {"start": v(225.46, 25.4) * mm, "end": v(222.71, 20.64) * mm});
            skLineSegment(sketch, "E15.14.15.11", {"start": v(222.71, 20.64) * mm, "end": v(217.21, 20.64) * mm});
            skLineSegment(sketch, "E15.17.15.11", {"start": v(217.21, 20.64) * mm, "end": v(214.46, 25.4) * mm});
            skCircle(sketch, "E15.0.15.12", {"center": v(219.96, 38.1) * mm, "radius": 4.76 * mm, "construction": true});
            skLineSegment(sketch, "E15.2.15.12", {"start": v(214.46, 38.1) * mm, "end": v(217.21, 42.86) * mm});
            skLineSegment(sketch, "E15.5.15.12", {"start": v(217.21, 42.86) * mm, "end": v(222.71, 42.86) * mm});
            skLineSegment(sketch, "E15.8.15.12", {"start": v(222.71, 42.86) * mm, "end": v(225.46, 38.1) * mm});
            skLineSegment(sketch, "E15.11.15.12", {"start": v(225.46, 38.1) * mm, "end": v(222.71, 33.34) * mm});
            skLineSegment(sketch, "E15.14.15.12", {"start": v(222.71, 33.34) * mm, "end": v(217.21, 33.34) * mm});
            skLineSegment(sketch, "E15.17.15.12", {"start": v(217.21, 33.34) * mm, "end": v(214.46, 38.1) * mm});
            skCircle(sketch, "E15.0.15.13", {"center": v(219.96, 50.8) * mm, "radius": 4.76 * mm, "construction": true});
            skLineSegment(sketch, "E15.2.15.13", {"start": v(214.46, 50.8) * mm, "end": v(217.21, 55.56) * mm});
            skLineSegment(sketch, "E15.5.15.13", {"start": v(217.21, 55.56) * mm, "end": v(222.71, 55.56) * mm});
            skLineSegment(sketch, "E15.8.15.13", {"start": v(222.71, 55.56) * mm, "end": v(225.46, 50.8) * mm});
            skLineSegment(sketch, "E15.11.15.13", {"start": v(225.46, 50.8) * mm, "end": v(222.71, 46.04) * mm});
            skLineSegment(sketch, "E15.14.15.13", {"start": v(222.71, 46.04) * mm, "end": v(217.21, 46.04) * mm});
            skLineSegment(sketch, "E15.17.15.13", {"start": v(217.21, 46.04) * mm, "end": v(214.46, 50.8) * mm});
            skCircle(sketch, "E15.0.15.14", {"center": v(219.96, 63.5) * mm, "radius": 4.76 * mm, "construction": true});
            skLineSegment(sketch, "E15.2.15.14", {"start": v(214.46, 63.5) * mm, "end": v(217.21, 68.26) * mm});
            skLineSegment(sketch, "E15.5.15.14", {"start": v(217.21, 68.26) * mm, "end": v(222.71, 68.26) * mm});
            skLineSegment(sketch, "E15.8.15.14", {"start": v(222.71, 68.26) * mm, "end": v(225.46, 63.5) * mm});
            skLineSegment(sketch, "E15.11.15.14", {"start": v(225.46, 63.5) * mm, "end": v(222.71, 58.74) * mm});
            skLineSegment(sketch, "E15.14.15.14", {"start": v(222.71, 58.74) * mm, "end": v(217.21, 58.74) * mm});
            skLineSegment(sketch, "E15.17.15.14", {"start": v(217.21, 58.74) * mm, "end": v(214.46, 63.5) * mm});
            skCircle(sketch, "E15.0.15.15", {"center": v(219.96, 76.2) * mm, "radius": 4.76 * mm, "construction": true});
            skLineSegment(sketch, "E15.2.15.15", {"start": v(214.46, 76.2) * mm, "end": v(217.21, 80.96) * mm});
            skLineSegment(sketch, "E15.5.15.15", {"start": v(217.21, 80.96) * mm, "end": v(222.71, 80.96) * mm});
            skLineSegment(sketch, "E15.8.15.15", {"start": v(222.71, 80.96) * mm, "end": v(225.46, 76.2) * mm});
            skLineSegment(sketch, "E15.11.15.15", {"start": v(225.46, 76.2) * mm, "end": v(222.71, 71.44) * mm});
            skLineSegment(sketch, "E15.14.15.15", {"start": v(222.71, 71.44) * mm, "end": v(217.21, 71.44) * mm});
            skLineSegment(sketch, "E15.17.15.15", {"start": v(217.21, 71.44) * mm, "end": v(214.46, 76.2) * mm});
            skCircle(sketch, "E15.0.15.16", {"center": v(219.96, 88.9) * mm, "radius": 4.76 * mm, "construction": true});
            skLineSegment(sketch, "E15.2.15.16", {"start": v(214.46, 88.9) * mm, "end": v(217.21, 93.66) * mm});
            skLineSegment(sketch, "E15.5.15.16", {"start": v(217.21, 93.66) * mm, "end": v(222.71, 93.66) * mm});
            skLineSegment(sketch, "E15.8.15.16", {"start": v(222.71, 93.66) * mm, "end": v(225.46, 88.9) * mm});
            skLineSegment(sketch, "E15.11.15.16", {"start": v(225.46, 88.9) * mm, "end": v(222.71, 84.14) * mm});
            skLineSegment(sketch, "E15.14.15.16", {"start": v(222.71, 84.14) * mm, "end": v(217.21, 84.14) * mm});
            skLineSegment(sketch, "E15.17.15.16", {"start": v(217.21, 84.14) * mm, "end": v(214.46, 88.9) * mm});
            skCircle(sketch, "E15.0.15.17", {"center": v(219.96, 101.6) * mm, "radius": 4.76 * mm, "construction": true});
            skLineSegment(sketch, "E15.2.15.17", {"start": v(214.46, 101.6) * mm, "end": v(217.21, 106.36) * mm});
            skLineSegment(sketch, "E15.5.15.17", {"start": v(217.21, 106.36) * mm, "end": v(222.71, 106.36) * mm});
            skLineSegment(sketch, "E15.8.15.17", {"start": v(222.71, 106.36) * mm, "end": v(225.46, 101.6) * mm});
            skLineSegment(sketch, "E15.11.15.17", {"start": v(225.46, 101.6) * mm, "end": v(222.71, 96.84) * mm});
            skLineSegment(sketch, "E15.14.15.17", {"start": v(222.71, 96.84) * mm, "end": v(217.21, 96.84) * mm});
            skLineSegment(sketch, "E15.17.15.17", {"start": v(217.21, 96.84) * mm, "end": v(214.46, 101.6) * mm});
            skCircle(sketch, "E15.0.15.18", {"center": v(219.96, 114.3) * mm, "radius": 4.76 * mm, "construction": true});
            skLineSegment(sketch, "E15.2.15.18", {"start": v(214.46, 114.3) * mm, "end": v(217.21, 119.06) * mm});
            skLineSegment(sketch, "E15.5.15.18", {"start": v(217.21, 119.06) * mm, "end": v(222.71, 119.06) * mm});
            skLineSegment(sketch, "E15.8.15.18", {"start": v(222.71, 119.06) * mm, "end": v(225.46, 114.3) * mm});
            skLineSegment(sketch, "E15.11.15.18", {"start": v(225.46, 114.3) * mm, "end": v(222.71, 109.54) * mm});
            skLineSegment(sketch, "E15.14.15.18", {"start": v(222.71, 109.54) * mm, "end": v(217.21, 109.54) * mm});
            skLineSegment(sketch, "E15.17.15.18", {"start": v(217.21, 109.54) * mm, "end": v(214.46, 114.3) * mm});
            skCircle(sketch, "E15.0.15.19", {"center": v(219.96, 127) * mm, "radius": 4.76 * mm, "construction": true});
            skLineSegment(sketch, "E15.2.15.19", {"start": v(214.46, 127) * mm, "end": v(217.21, 131.76) * mm});
            skLineSegment(sketch, "E15.5.15.19", {"start": v(217.21, 131.76) * mm, "end": v(222.71, 131.76) * mm});
            skLineSegment(sketch, "E15.8.15.19", {"start": v(222.71, 131.76) * mm, "end": v(225.46, 127) * mm});
            skLineSegment(sketch, "E15.11.15.19", {"start": v(225.46, 127) * mm, "end": v(222.71, 122.24) * mm});
            skLineSegment(sketch, "E15.14.15.19", {"start": v(222.71, 122.24) * mm, "end": v(217.21, 122.24) * mm});
            skLineSegment(sketch, "E15.17.15.19", {"start": v(217.21, 122.24) * mm, "end": v(214.46, 127) * mm});
            skCircle(sketch, "E15.0.16.0", {"center": v(241.96, -114.3) * mm, "radius": 4.76 * mm, "construction": true});
            skLineSegment(sketch, "E15.2.16.0", {"start": v(236.46, -114.3) * mm, "end": v(239.21, -109.54) * mm});
            skLineSegment(sketch, "E15.5.16.0", {"start": v(239.21, -109.54) * mm, "end": v(244.71, -109.54) * mm});
            skLineSegment(sketch, "E15.8.16.0", {"start": v(244.71, -109.54) * mm, "end": v(247.46, -114.3) * mm});
            skLineSegment(sketch, "E15.11.16.0", {"start": v(247.46, -114.3) * mm, "end": v(244.71, -119.06) * mm});
            skLineSegment(sketch, "E15.14.16.0", {"start": v(244.71, -119.06) * mm, "end": v(239.21, -119.06) * mm});
            skLineSegment(sketch, "E15.17.16.0", {"start": v(239.21, -119.06) * mm, "end": v(236.46, -114.3) * mm});
            skCircle(sketch, "E15.0.16.1", {"center": v(241.96, -101.6) * mm, "radius": 4.76 * mm, "construction": true});
            skLineSegment(sketch, "E15.2.16.1", {"start": v(236.46, -101.6) * mm, "end": v(239.21, -96.84) * mm});
            skLineSegment(sketch, "E15.5.16.1", {"start": v(239.21, -96.84) * mm, "end": v(244.71, -96.84) * mm});
            skLineSegment(sketch, "E15.8.16.1", {"start": v(244.71, -96.84) * mm, "end": v(247.46, -101.6) * mm});
            skLineSegment(sketch, "E15.11.16.1", {"start": v(247.46, -101.6) * mm, "end": v(244.71, -106.36) * mm});
            skLineSegment(sketch, "E15.14.16.1", {"start": v(244.71, -106.36) * mm, "end": v(239.21, -106.36) * mm});
            skLineSegment(sketch, "E15.17.16.1", {"start": v(239.21, -106.36) * mm, "end": v(236.46, -101.6) * mm});
            skCircle(sketch, "E15.0.16.2", {"center": v(241.96, -88.9) * mm, "radius": 4.76 * mm, "construction": true});
            skLineSegment(sketch, "E15.2.16.2", {"start": v(236.46, -88.9) * mm, "end": v(239.21, -84.14) * mm});
            skLineSegment(sketch, "E15.5.16.2", {"start": v(239.21, -84.14) * mm, "end": v(244.71, -84.14) * mm});
            skLineSegment(sketch, "E15.8.16.2", {"start": v(244.71, -84.14) * mm, "end": v(247.46, -88.9) * mm});
            skLineSegment(sketch, "E15.11.16.2", {"start": v(247.46, -88.9) * mm, "end": v(244.71, -93.66) * mm});
            skLineSegment(sketch, "E15.14.16.2", {"start": v(244.71, -93.66) * mm, "end": v(239.21, -93.66) * mm});
            skLineSegment(sketch, "E15.17.16.2", {"start": v(239.21, -93.66) * mm, "end": v(236.46, -88.9) * mm});
            skCircle(sketch, "E15.0.16.3", {"center": v(241.96, -76.2) * mm, "radius": 4.76 * mm, "construction": true});
            skLineSegment(sketch, "E15.2.16.3", {"start": v(236.46, -76.2) * mm, "end": v(239.21, -71.44) * mm});
            skLineSegment(sketch, "E15.5.16.3", {"start": v(239.21, -71.44) * mm, "end": v(244.71, -71.44) * mm});
            skLineSegment(sketch, "E15.8.16.3", {"start": v(244.71, -71.44) * mm, "end": v(247.46, -76.2) * mm});
            skLineSegment(sketch, "E15.11.16.3", {"start": v(247.46, -76.2) * mm, "end": v(244.71, -80.96) * mm});
            skLineSegment(sketch, "E15.14.16.3", {"start": v(244.71, -80.96) * mm, "end": v(239.21, -80.96) * mm});
            skLineSegment(sketch, "E15.17.16.3", {"start": v(239.21, -80.96) * mm, "end": v(236.46, -76.2) * mm});
            skCircle(sketch, "E15.0.16.4", {"center": v(241.96, -63.5) * mm, "radius": 4.76 * mm, "construction": true});
            skLineSegment(sketch, "E15.2.16.4", {"start": v(236.46, -63.5) * mm, "end": v(239.21, -58.74) * mm});
            skLineSegment(sketch, "E15.5.16.4", {"start": v(239.21, -58.74) * mm, "end": v(244.71, -58.74) * mm});
            skLineSegment(sketch, "E15.8.16.4", {"start": v(244.71, -58.74) * mm, "end": v(247.46, -63.5) * mm});
            skLineSegment(sketch, "E15.11.16.4", {"start": v(247.46, -63.5) * mm, "end": v(244.71, -68.26) * mm});
            skLineSegment(sketch, "E15.14.16.4", {"start": v(244.71, -68.26) * mm, "end": v(239.21, -68.26) * mm});
            skLineSegment(sketch, "E15.17.16.4", {"start": v(239.21, -68.26) * mm, "end": v(236.46, -63.5) * mm});
            skCircle(sketch, "E15.0.16.5", {"center": v(241.96, -50.8) * mm, "radius": 4.76 * mm, "construction": true});
            skLineSegment(sketch, "E15.2.16.5", {"start": v(236.46, -50.8) * mm, "end": v(239.21, -46.04) * mm});
            skLineSegment(sketch, "E15.5.16.5", {"start": v(239.21, -46.04) * mm, "end": v(244.71, -46.04) * mm});
            skLineSegment(sketch, "E15.8.16.5", {"start": v(244.71, -46.04) * mm, "end": v(247.46, -50.8) * mm});
            skLineSegment(sketch, "E15.11.16.5", {"start": v(247.46, -50.8) * mm, "end": v(244.71, -55.56) * mm});
            skLineSegment(sketch, "E15.14.16.5", {"start": v(244.71, -55.56) * mm, "end": v(239.21, -55.56) * mm});
            skLineSegment(sketch, "E15.17.16.5", {"start": v(239.21, -55.56) * mm, "end": v(236.46, -50.8) * mm});
            skCircle(sketch, "E15.0.16.6", {"center": v(241.96, -38.1) * mm, "radius": 4.76 * mm, "construction": true});
            skLineSegment(sketch, "E15.2.16.6", {"start": v(236.46, -38.1) * mm, "end": v(239.21, -33.34) * mm});
            skLineSegment(sketch, "E15.5.16.6", {"start": v(239.21, -33.34) * mm, "end": v(244.71, -33.34) * mm});
            skLineSegment(sketch, "E15.8.16.6", {"start": v(244.71, -33.34) * mm, "end": v(247.46, -38.1) * mm});
            skLineSegment(sketch, "E15.11.16.6", {"start": v(247.46, -38.1) * mm, "end": v(244.71, -42.86) * mm});
            skLineSegment(sketch, "E15.14.16.6", {"start": v(244.71, -42.86) * mm, "end": v(239.21, -42.86) * mm});
            skLineSegment(sketch, "E15.17.16.6", {"start": v(239.21, -42.86) * mm, "end": v(236.46, -38.1) * mm});
            skCircle(sketch, "E15.0.16.7", {"center": v(241.96, -25.4) * mm, "radius": 4.76 * mm, "construction": true});
            skLineSegment(sketch, "E15.2.16.7", {"start": v(236.46, -25.4) * mm, "end": v(239.21, -20.64) * mm});
            skLineSegment(sketch, "E15.5.16.7", {"start": v(239.21, -20.64) * mm, "end": v(244.71, -20.64) * mm});
            skLineSegment(sketch, "E15.8.16.7", {"start": v(244.71, -20.64) * mm, "end": v(247.46, -25.4) * mm});
            skLineSegment(sketch, "E15.11.16.7", {"start": v(247.46, -25.4) * mm, "end": v(244.71, -30.16) * mm});
            skLineSegment(sketch, "E15.14.16.7", {"start": v(244.71, -30.16) * mm, "end": v(239.21, -30.16) * mm});
            skLineSegment(sketch, "E15.17.16.7", {"start": v(239.21, -30.16) * mm, "end": v(236.46, -25.4) * mm});
            skCircle(sketch, "E15.0.16.8", {"center": v(241.96, -12.7) * mm, "radius": 4.76 * mm, "construction": true});
            skLineSegment(sketch, "E15.2.16.8", {"start": v(236.46, -12.7) * mm, "end": v(239.21, -7.94) * mm});
            skLineSegment(sketch, "E15.5.16.8", {"start": v(239.21, -7.94) * mm, "end": v(244.71, -7.94) * mm});
            skLineSegment(sketch, "E15.8.16.8", {"start": v(244.71, -7.94) * mm, "end": v(247.46, -12.7) * mm});
            skLineSegment(sketch, "E15.11.16.8", {"start": v(247.46, -12.7) * mm, "end": v(244.71, -17.46) * mm});
            skLineSegment(sketch, "E15.14.16.8", {"start": v(244.71, -17.46) * mm, "end": v(239.21, -17.46) * mm});
            skLineSegment(sketch, "E15.17.16.8", {"start": v(239.21, -17.46) * mm, "end": v(236.46, -12.7) * mm});
            skCircle(sketch, "E15.0.16.9", {"center": v(241.96, 0) * mm, "radius": 4.76 * mm, "construction": true});
            skLineSegment(sketch, "E15.2.16.9", {"start": v(236.46, 0) * mm, "end": v(239.21, 4.76) * mm});
            skLineSegment(sketch, "E15.5.16.9", {"start": v(239.21, 4.76) * mm, "end": v(244.71, 4.76) * mm});
            skLineSegment(sketch, "E15.8.16.9", {"start": v(244.71, 4.76) * mm, "end": v(247.46, 0) * mm});
            skLineSegment(sketch, "E15.11.16.9", {"start": v(247.46, 0) * mm, "end": v(244.71, -4.76) * mm});
            skLineSegment(sketch, "E15.14.16.9", {"start": v(244.71, -4.76) * mm, "end": v(239.21, -4.76) * mm});
            skLineSegment(sketch, "E15.17.16.9", {"start": v(239.21, -4.76) * mm, "end": v(236.46, 0) * mm});
            skCircle(sketch, "E15.0.16.10", {"center": v(241.96, 12.7) * mm, "radius": 4.76 * mm, "construction": true});
            skLineSegment(sketch, "E15.2.16.10", {"start": v(236.46, 12.7) * mm, "end": v(239.21, 17.46) * mm});
            skLineSegment(sketch, "E15.5.16.10", {"start": v(239.21, 17.46) * mm, "end": v(244.71, 17.46) * mm});
            skLineSegment(sketch, "E15.8.16.10", {"start": v(244.71, 17.46) * mm, "end": v(247.46, 12.7) * mm});
            skLineSegment(sketch, "E15.11.16.10", {"start": v(247.46, 12.7) * mm, "end": v(244.71, 7.94) * mm});
            skLineSegment(sketch, "E15.14.16.10", {"start": v(244.71, 7.94) * mm, "end": v(239.21, 7.94) * mm});
            skLineSegment(sketch, "E15.17.16.10", {"start": v(239.21, 7.94) * mm, "end": v(236.46, 12.7) * mm});
            skCircle(sketch, "E15.0.16.11", {"center": v(241.96, 25.4) * mm, "radius": 4.76 * mm, "construction": true});
            skLineSegment(sketch, "E15.2.16.11", {"start": v(236.46, 25.4) * mm, "end": v(239.21, 30.16) * mm});
            skLineSegment(sketch, "E15.5.16.11", {"start": v(239.21, 30.16) * mm, "end": v(244.71, 30.16) * mm});
            skLineSegment(sketch, "E15.8.16.11", {"start": v(244.71, 30.16) * mm, "end": v(247.46, 25.4) * mm});
            skLineSegment(sketch, "E15.11.16.11", {"start": v(247.46, 25.4) * mm, "end": v(244.71, 20.64) * mm});
            skLineSegment(sketch, "E15.14.16.11", {"start": v(244.71, 20.64) * mm, "end": v(239.21, 20.64) * mm});
            skLineSegment(sketch, "E15.17.16.11", {"start": v(239.21, 20.64) * mm, "end": v(236.46, 25.4) * mm});
            skCircle(sketch, "E15.0.16.12", {"center": v(241.96, 38.1) * mm, "radius": 4.76 * mm, "construction": true});
            skLineSegment(sketch, "E15.2.16.12", {"start": v(236.46, 38.1) * mm, "end": v(239.21, 42.86) * mm});
            skLineSegment(sketch, "E15.5.16.12", {"start": v(239.21, 42.86) * mm, "end": v(244.71, 42.86) * mm});
            skLineSegment(sketch, "E15.8.16.12", {"start": v(244.71, 42.86) * mm, "end": v(247.46, 38.1) * mm});
            skLineSegment(sketch, "E15.11.16.12", {"start": v(247.46, 38.1) * mm, "end": v(244.71, 33.34) * mm});
            skLineSegment(sketch, "E15.14.16.12", {"start": v(244.71, 33.34) * mm, "end": v(239.21, 33.34) * mm});
            skLineSegment(sketch, "E15.17.16.12", {"start": v(239.21, 33.34) * mm, "end": v(236.46, 38.1) * mm});
            skCircle(sketch, "E15.0.16.13", {"center": v(241.96, 50.8) * mm, "radius": 4.76 * mm, "construction": true});
            skLineSegment(sketch, "E15.2.16.13", {"start": v(236.46, 50.8) * mm, "end": v(239.21, 55.56) * mm});
            skLineSegment(sketch, "E15.5.16.13", {"start": v(239.21, 55.56) * mm, "end": v(244.71, 55.56) * mm});
            skLineSegment(sketch, "E15.8.16.13", {"start": v(244.71, 55.56) * mm, "end": v(247.46, 50.8) * mm});
            skLineSegment(sketch, "E15.11.16.13", {"start": v(247.46, 50.8) * mm, "end": v(244.71, 46.04) * mm});
            skLineSegment(sketch, "E15.14.16.13", {"start": v(244.71, 46.04) * mm, "end": v(239.21, 46.04) * mm});
            skLineSegment(sketch, "E15.17.16.13", {"start": v(239.21, 46.04) * mm, "end": v(236.46, 50.8) * mm});
            skCircle(sketch, "E15.0.16.14", {"center": v(241.96, 63.5) * mm, "radius": 4.76 * mm, "construction": true});
            skLineSegment(sketch, "E15.2.16.14", {"start": v(236.46, 63.5) * mm, "end": v(239.21, 68.26) * mm});
            skLineSegment(sketch, "E15.5.16.14", {"start": v(239.21, 68.26) * mm, "end": v(244.71, 68.26) * mm});
            skLineSegment(sketch, "E15.8.16.14", {"start": v(244.71, 68.26) * mm, "end": v(247.46, 63.5) * mm});
            skLineSegment(sketch, "E15.11.16.14", {"start": v(247.46, 63.5) * mm, "end": v(244.71, 58.74) * mm});
            skLineSegment(sketch, "E15.14.16.14", {"start": v(244.71, 58.74) * mm, "end": v(239.21, 58.74) * mm});
            skLineSegment(sketch, "E15.17.16.14", {"start": v(239.21, 58.74) * mm, "end": v(236.46, 63.5) * mm});
            skCircle(sketch, "E15.0.16.15", {"center": v(241.96, 76.2) * mm, "radius": 4.76 * mm, "construction": true});
            skLineSegment(sketch, "E15.2.16.15", {"start": v(236.46, 76.2) * mm, "end": v(239.21, 80.96) * mm});
            skLineSegment(sketch, "E15.5.16.15", {"start": v(239.21, 80.96) * mm, "end": v(244.71, 80.96) * mm});
            skLineSegment(sketch, "E15.8.16.15", {"start": v(244.71, 80.96) * mm, "end": v(247.46, 76.2) * mm});
            skLineSegment(sketch, "E15.11.16.15", {"start": v(247.46, 76.2) * mm, "end": v(244.71, 71.44) * mm});
            skLineSegment(sketch, "E15.14.16.15", {"start": v(244.71, 71.44) * mm, "end": v(239.21, 71.44) * mm});
            skLineSegment(sketch, "E15.17.16.15", {"start": v(239.21, 71.44) * mm, "end": v(236.46, 76.2) * mm});
            skCircle(sketch, "E15.0.16.16", {"center": v(241.96, 88.9) * mm, "radius": 4.76 * mm, "construction": true});
            skLineSegment(sketch, "E15.2.16.16", {"start": v(236.46, 88.9) * mm, "end": v(239.21, 93.66) * mm});
            skLineSegment(sketch, "E15.5.16.16", {"start": v(239.21, 93.66) * mm, "end": v(244.71, 93.66) * mm});
            skLineSegment(sketch, "E15.8.16.16", {"start": v(244.71, 93.66) * mm, "end": v(247.46, 88.9) * mm});
            skLineSegment(sketch, "E15.11.16.16", {"start": v(247.46, 88.9) * mm, "end": v(244.71, 84.14) * mm});
            skLineSegment(sketch, "E15.14.16.16", {"start": v(244.71, 84.14) * mm, "end": v(239.21, 84.14) * mm});
            skLineSegment(sketch, "E15.17.16.16", {"start": v(239.21, 84.14) * mm, "end": v(236.46, 88.9) * mm});
            skCircle(sketch, "E15.0.16.17", {"center": v(241.96, 101.6) * mm, "radius": 4.76 * mm, "construction": true});
            skLineSegment(sketch, "E15.2.16.17", {"start": v(236.46, 101.6) * mm, "end": v(239.21, 106.36) * mm});
            skLineSegment(sketch, "E15.5.16.17", {"start": v(239.21, 106.36) * mm, "end": v(244.71, 106.36) * mm});
            skLineSegment(sketch, "E15.8.16.17", {"start": v(244.71, 106.36) * mm, "end": v(247.46, 101.6) * mm});
            skLineSegment(sketch, "E15.11.16.17", {"start": v(247.46, 101.6) * mm, "end": v(244.71, 96.84) * mm});
            skLineSegment(sketch, "E15.14.16.17", {"start": v(244.71, 96.84) * mm, "end": v(239.21, 96.84) * mm});
            skLineSegment(sketch, "E15.17.16.17", {"start": v(239.21, 96.84) * mm, "end": v(236.46, 101.6) * mm});
            skCircle(sketch, "E15.0.16.18", {"center": v(241.96, 114.3) * mm, "radius": 4.76 * mm, "construction": true});
            skLineSegment(sketch, "E15.2.16.18", {"start": v(236.46, 114.3) * mm, "end": v(239.21, 119.06) * mm});
            skLineSegment(sketch, "E15.5.16.18", {"start": v(239.21, 119.06) * mm, "end": v(244.71, 119.06) * mm});
            skLineSegment(sketch, "E15.8.16.18", {"start": v(244.71, 119.06) * mm, "end": v(247.46, 114.3) * mm});
            skLineSegment(sketch, "E15.11.16.18", {"start": v(247.46, 114.3) * mm, "end": v(244.71, 109.54) * mm});
            skLineSegment(sketch, "E15.14.16.18", {"start": v(244.71, 109.54) * mm, "end": v(239.21, 109.54) * mm});
            skLineSegment(sketch, "E15.17.16.18", {"start": v(239.21, 109.54) * mm, "end": v(236.46, 114.3) * mm});
            skCircle(sketch, "E15.0.16.19", {"center": v(241.96, 127) * mm, "radius": 4.76 * mm, "construction": true});
            skLineSegment(sketch, "E15.2.16.19", {"start": v(236.46, 127) * mm, "end": v(239.21, 131.76) * mm});
            skLineSegment(sketch, "E15.5.16.19", {"start": v(239.21, 131.76) * mm, "end": v(244.71, 131.76) * mm});
            skLineSegment(sketch, "E15.8.16.19", {"start": v(244.71, 131.76) * mm, "end": v(247.46, 127) * mm});
            skLineSegment(sketch, "E15.11.16.19", {"start": v(247.46, 127) * mm, "end": v(244.71, 122.24) * mm});
            skLineSegment(sketch, "E15.14.16.19", {"start": v(244.71, 122.24) * mm, "end": v(239.21, 122.24) * mm});
            skLineSegment(sketch, "E15.17.16.19", {"start": v(239.21, 122.24) * mm, "end": v(236.46, 127) * mm});
            skCircle(sketch, "E15.0.17.0", {"center": v(263.96, -114.3) * mm, "radius": 4.76 * mm, "construction": true});
            skLineSegment(sketch, "E15.2.17.0", {"start": v(258.46, -114.3) * mm, "end": v(261.2, -109.54) * mm});
            skLineSegment(sketch, "E15.5.17.0", {"start": v(261.2, -109.54) * mm, "end": v(266.7, -109.54) * mm});
            skLineSegment(sketch, "E15.8.17.0", {"start": v(266.7, -109.54) * mm, "end": v(269.46, -114.3) * mm});
            skLineSegment(sketch, "E15.11.17.0", {"start": v(269.46, -114.3) * mm, "end": v(266.7, -119.06) * mm});
            skLineSegment(sketch, "E15.14.17.0", {"start": v(266.7, -119.06) * mm, "end": v(261.2, -119.06) * mm});
            skLineSegment(sketch, "E15.17.17.0", {"start": v(261.2, -119.06) * mm, "end": v(258.46, -114.3) * mm});
            skCircle(sketch, "E15.0.17.1", {"center": v(263.96, -101.6) * mm, "radius": 4.76 * mm, "construction": true});
            skLineSegment(sketch, "E15.2.17.1", {"start": v(258.46, -101.6) * mm, "end": v(261.2, -96.84) * mm});
            skLineSegment(sketch, "E15.5.17.1", {"start": v(261.2, -96.84) * mm, "end": v(266.7, -96.84) * mm});
            skLineSegment(sketch, "E15.8.17.1", {"start": v(266.7, -96.84) * mm, "end": v(269.46, -101.6) * mm});
            skLineSegment(sketch, "E15.11.17.1", {"start": v(269.46, -101.6) * mm, "end": v(266.7, -106.36) * mm});
            skLineSegment(sketch, "E15.14.17.1", {"start": v(266.7, -106.36) * mm, "end": v(261.2, -106.36) * mm});
            skLineSegment(sketch, "E15.17.17.1", {"start": v(261.2, -106.36) * mm, "end": v(258.46, -101.6) * mm});
            skCircle(sketch, "E15.0.17.2", {"center": v(263.96, -88.9) * mm, "radius": 4.76 * mm, "construction": true});
            skLineSegment(sketch, "E15.2.17.2", {"start": v(258.46, -88.9) * mm, "end": v(261.2, -84.14) * mm});
            skLineSegment(sketch, "E15.5.17.2", {"start": v(261.2, -84.14) * mm, "end": v(266.7, -84.14) * mm});
            skLineSegment(sketch, "E15.8.17.2", {"start": v(266.7, -84.14) * mm, "end": v(269.46, -88.9) * mm});
            skLineSegment(sketch, "E15.11.17.2", {"start": v(269.46, -88.9) * mm, "end": v(266.7, -93.66) * mm});
            skLineSegment(sketch, "E15.14.17.2", {"start": v(266.7, -93.66) * mm, "end": v(261.2, -93.66) * mm});
            skLineSegment(sketch, "E15.17.17.2", {"start": v(261.2, -93.66) * mm, "end": v(258.46, -88.9) * mm});
            skCircle(sketch, "E15.0.17.3", {"center": v(263.96, -76.2) * mm, "radius": 4.76 * mm, "construction": true});
            skLineSegment(sketch, "E15.2.17.3", {"start": v(258.46, -76.2) * mm, "end": v(261.2, -71.44) * mm});
            skLineSegment(sketch, "E15.5.17.3", {"start": v(261.2, -71.44) * mm, "end": v(266.7, -71.44) * mm});
            skLineSegment(sketch, "E15.8.17.3", {"start": v(266.7, -71.44) * mm, "end": v(269.46, -76.2) * mm});
            skLineSegment(sketch, "E15.11.17.3", {"start": v(269.46, -76.2) * mm, "end": v(266.7, -80.96) * mm});
            skLineSegment(sketch, "E15.14.17.3", {"start": v(266.7, -80.96) * mm, "end": v(261.2, -80.96) * mm});
            skLineSegment(sketch, "E15.17.17.3", {"start": v(261.2, -80.96) * mm, "end": v(258.46, -76.2) * mm});
            skCircle(sketch, "E15.0.17.4", {"center": v(263.96, -63.5) * mm, "radius": 4.76 * mm, "construction": true});
            skLineSegment(sketch, "E15.2.17.4", {"start": v(258.46, -63.5) * mm, "end": v(261.2, -58.74) * mm});
            skLineSegment(sketch, "E15.5.17.4", {"start": v(261.2, -58.74) * mm, "end": v(266.7, -58.74) * mm});
            skLineSegment(sketch, "E15.8.17.4", {"start": v(266.7, -58.74) * mm, "end": v(269.46, -63.5) * mm});
            skLineSegment(sketch, "E15.11.17.4", {"start": v(269.46, -63.5) * mm, "end": v(266.7, -68.26) * mm});
            skLineSegment(sketch, "E15.14.17.4", {"start": v(266.7, -68.26) * mm, "end": v(261.2, -68.26) * mm});
            skLineSegment(sketch, "E15.17.17.4", {"start": v(261.2, -68.26) * mm, "end": v(258.46, -63.5) * mm});
            skCircle(sketch, "E15.0.17.5", {"center": v(263.96, -50.8) * mm, "radius": 4.76 * mm, "construction": true});
            skLineSegment(sketch, "E15.2.17.5", {"start": v(258.46, -50.8) * mm, "end": v(261.2, -46.04) * mm});
            skLineSegment(sketch, "E15.5.17.5", {"start": v(261.2, -46.04) * mm, "end": v(266.7, -46.04) * mm});
            skLineSegment(sketch, "E15.8.17.5", {"start": v(266.7, -46.04) * mm, "end": v(269.46, -50.8) * mm});
            skLineSegment(sketch, "E15.11.17.5", {"start": v(269.46, -50.8) * mm, "end": v(266.7, -55.56) * mm});
            skLineSegment(sketch, "E15.14.17.5", {"start": v(266.7, -55.56) * mm, "end": v(261.2, -55.56) * mm});
            skLineSegment(sketch, "E15.17.17.5", {"start": v(261.2, -55.56) * mm, "end": v(258.46, -50.8) * mm});
            skCircle(sketch, "E15.0.17.6", {"center": v(263.96, -38.1) * mm, "radius": 4.76 * mm, "construction": true});
            skLineSegment(sketch, "E15.2.17.6", {"start": v(258.46, -38.1) * mm, "end": v(261.2, -33.34) * mm});
            skLineSegment(sketch, "E15.5.17.6", {"start": v(261.2, -33.34) * mm, "end": v(266.7, -33.34) * mm});
            skLineSegment(sketch, "E15.8.17.6", {"start": v(266.7, -33.34) * mm, "end": v(269.46, -38.1) * mm});
            skLineSegment(sketch, "E15.11.17.6", {"start": v(269.46, -38.1) * mm, "end": v(266.7, -42.86) * mm});
            skLineSegment(sketch, "E15.14.17.6", {"start": v(266.7, -42.86) * mm, "end": v(261.2, -42.86) * mm});
            skLineSegment(sketch, "E15.17.17.6", {"start": v(261.2, -42.86) * mm, "end": v(258.46, -38.1) * mm});
            skCircle(sketch, "E15.0.17.7", {"center": v(263.96, -25.4) * mm, "radius": 4.76 * mm, "construction": true});
            skLineSegment(sketch, "E15.2.17.7", {"start": v(258.46, -25.4) * mm, "end": v(261.2, -20.64) * mm});
            skLineSegment(sketch, "E15.5.17.7", {"start": v(261.2, -20.64) * mm, "end": v(266.7, -20.64) * mm});
            skLineSegment(sketch, "E15.8.17.7", {"start": v(266.7, -20.64) * mm, "end": v(269.46, -25.4) * mm});
            skLineSegment(sketch, "E15.11.17.7", {"start": v(269.46, -25.4) * mm, "end": v(266.7, -30.16) * mm});
            skLineSegment(sketch, "E15.14.17.7", {"start": v(266.7, -30.16) * mm, "end": v(261.2, -30.16) * mm});
            skLineSegment(sketch, "E15.17.17.7", {"start": v(261.2, -30.16) * mm, "end": v(258.46, -25.4) * mm});
            skCircle(sketch, "E15.0.17.8", {"center": v(263.96, -12.7) * mm, "radius": 4.76 * mm, "construction": true});
            skLineSegment(sketch, "E15.2.17.8", {"start": v(258.46, -12.7) * mm, "end": v(261.2, -7.94) * mm});
            skLineSegment(sketch, "E15.5.17.8", {"start": v(261.2, -7.94) * mm, "end": v(266.7, -7.94) * mm});
            skLineSegment(sketch, "E15.8.17.8", {"start": v(266.7, -7.94) * mm, "end": v(269.46, -12.7) * mm});
            skLineSegment(sketch, "E15.11.17.8", {"start": v(269.46, -12.7) * mm, "end": v(266.7, -17.46) * mm});
            skLineSegment(sketch, "E15.14.17.8", {"start": v(266.7, -17.46) * mm, "end": v(261.2, -17.46) * mm});
            skLineSegment(sketch, "E15.17.17.8", {"start": v(261.2, -17.46) * mm, "end": v(258.46, -12.7) * mm});
            skCircle(sketch, "E15.0.17.9", {"center": v(263.96, 0) * mm, "radius": 4.76 * mm, "construction": true});
            skLineSegment(sketch, "E15.2.17.9", {"start": v(258.46, 0) * mm, "end": v(261.2, 4.76) * mm});
            skLineSegment(sketch, "E15.5.17.9", {"start": v(261.2, 4.76) * mm, "end": v(266.7, 4.76) * mm});
            skLineSegment(sketch, "E15.8.17.9", {"start": v(266.7, 4.76) * mm, "end": v(269.46, 0) * mm});
            skLineSegment(sketch, "E15.11.17.9", {"start": v(269.46, 0) * mm, "end": v(266.7, -4.76) * mm});
            skLineSegment(sketch, "E15.14.17.9", {"start": v(266.7, -4.76) * mm, "end": v(261.2, -4.76) * mm});
            skLineSegment(sketch, "E15.17.17.9", {"start": v(261.2, -4.76) * mm, "end": v(258.46, 0) * mm});
            skCircle(sketch, "E15.0.17.10", {"center": v(263.96, 12.7) * mm, "radius": 4.76 * mm, "construction": true});
            skLineSegment(sketch, "E15.2.17.10", {"start": v(258.46, 12.7) * mm, "end": v(261.2, 17.46) * mm});
            skLineSegment(sketch, "E15.5.17.10", {"start": v(261.2, 17.46) * mm, "end": v(266.7, 17.46) * mm});
            skLineSegment(sketch, "E15.8.17.10", {"start": v(266.7, 17.46) * mm, "end": v(269.46, 12.7) * mm});
            skLineSegment(sketch, "E15.11.17.10", {"start": v(269.46, 12.7) * mm, "end": v(266.7, 7.94) * mm});
            skLineSegment(sketch, "E15.14.17.10", {"start": v(266.7, 7.94) * mm, "end": v(261.2, 7.94) * mm});
            skLineSegment(sketch, "E15.17.17.10", {"start": v(261.2, 7.94) * mm, "end": v(258.46, 12.7) * mm});
            skCircle(sketch, "E15.0.17.11", {"center": v(263.96, 25.4) * mm, "radius": 4.76 * mm, "construction": true});
            skLineSegment(sketch, "E15.2.17.11", {"start": v(258.46, 25.4) * mm, "end": v(261.2, 30.16) * mm});
            skLineSegment(sketch, "E15.5.17.11", {"start": v(261.2, 30.16) * mm, "end": v(266.7, 30.16) * mm});
            skLineSegment(sketch, "E15.8.17.11", {"start": v(266.7, 30.16) * mm, "end": v(269.46, 25.4) * mm});
            skLineSegment(sketch, "E15.11.17.11", {"start": v(269.46, 25.4) * mm, "end": v(266.7, 20.64) * mm});
            skLineSegment(sketch, "E15.14.17.11", {"start": v(266.7, 20.64) * mm, "end": v(261.2, 20.64) * mm});
            skLineSegment(sketch, "E15.17.17.11", {"start": v(261.2, 20.64) * mm, "end": v(258.46, 25.4) * mm});
            skCircle(sketch, "E15.0.17.12", {"center": v(263.96, 38.1) * mm, "radius": 4.76 * mm, "construction": true});
            skLineSegment(sketch, "E15.2.17.12", {"start": v(258.46, 38.1) * mm, "end": v(261.2, 42.86) * mm});
            skLineSegment(sketch, "E15.5.17.12", {"start": v(261.2, 42.86) * mm, "end": v(266.7, 42.86) * mm});
            skLineSegment(sketch, "E15.8.17.12", {"start": v(266.7, 42.86) * mm, "end": v(269.46, 38.1) * mm});
            skLineSegment(sketch, "E15.11.17.12", {"start": v(269.46, 38.1) * mm, "end": v(266.7, 33.34) * mm});
            skLineSegment(sketch, "E15.14.17.12", {"start": v(266.7, 33.34) * mm, "end": v(261.2, 33.34) * mm});
            skLineSegment(sketch, "E15.17.17.12", {"start": v(261.2, 33.34) * mm, "end": v(258.46, 38.1) * mm});
            skCircle(sketch, "E15.0.17.13", {"center": v(263.96, 50.8) * mm, "radius": 4.76 * mm, "construction": true});
            skLineSegment(sketch, "E15.2.17.13", {"start": v(258.46, 50.8) * mm, "end": v(261.2, 55.56) * mm});
            skLineSegment(sketch, "E15.5.17.13", {"start": v(261.2, 55.56) * mm, "end": v(266.7, 55.56) * mm});
            skLineSegment(sketch, "E15.8.17.13", {"start": v(266.7, 55.56) * mm, "end": v(269.46, 50.8) * mm});
            skLineSegment(sketch, "E15.11.17.13", {"start": v(269.46, 50.8) * mm, "end": v(266.7, 46.04) * mm});
            skLineSegment(sketch, "E15.14.17.13", {"start": v(266.7, 46.04) * mm, "end": v(261.2, 46.04) * mm});
            skLineSegment(sketch, "E15.17.17.13", {"start": v(261.2, 46.04) * mm, "end": v(258.46, 50.8) * mm});
            skCircle(sketch, "E15.0.17.14", {"center": v(263.96, 63.5) * mm, "radius": 4.76 * mm, "construction": true});
            skLineSegment(sketch, "E15.2.17.14", {"start": v(258.46, 63.5) * mm, "end": v(261.2, 68.26) * mm});
            skLineSegment(sketch, "E15.5.17.14", {"start": v(261.2, 68.26) * mm, "end": v(266.7, 68.26) * mm});
            skLineSegment(sketch, "E15.8.17.14", {"start": v(266.7, 68.26) * mm, "end": v(269.46, 63.5) * mm});
            skLineSegment(sketch, "E15.11.17.14", {"start": v(269.46, 63.5) * mm, "end": v(266.7, 58.74) * mm});
            skLineSegment(sketch, "E15.14.17.14", {"start": v(266.7, 58.74) * mm, "end": v(261.2, 58.74) * mm});
            skLineSegment(sketch, "E15.17.17.14", {"start": v(261.2, 58.74) * mm, "end": v(258.46, 63.5) * mm});
            skCircle(sketch, "E15.0.17.15", {"center": v(263.96, 76.2) * mm, "radius": 4.76 * mm, "construction": true});
            skLineSegment(sketch, "E15.2.17.15", {"start": v(258.46, 76.2) * mm, "end": v(261.2, 80.96) * mm});
            skLineSegment(sketch, "E15.5.17.15", {"start": v(261.2, 80.96) * mm, "end": v(266.7, 80.96) * mm});
            skLineSegment(sketch, "E15.8.17.15", {"start": v(266.7, 80.96) * mm, "end": v(269.46, 76.2) * mm});
            skLineSegment(sketch, "E15.11.17.15", {"start": v(269.46, 76.2) * mm, "end": v(266.7, 71.44) * mm});
            skLineSegment(sketch, "E15.14.17.15", {"start": v(266.7, 71.44) * mm, "end": v(261.2, 71.44) * mm});
            skLineSegment(sketch, "E15.17.17.15", {"start": v(261.2, 71.44) * mm, "end": v(258.46, 76.2) * mm});
            skCircle(sketch, "E15.0.17.16", {"center": v(263.96, 88.9) * mm, "radius": 4.76 * mm, "construction": true});
            skLineSegment(sketch, "E15.2.17.16", {"start": v(258.46, 88.9) * mm, "end": v(261.2, 93.66) * mm});
            skLineSegment(sketch, "E15.5.17.16", {"start": v(261.2, 93.66) * mm, "end": v(266.7, 93.66) * mm});
            skLineSegment(sketch, "E15.8.17.16", {"start": v(266.7, 93.66) * mm, "end": v(269.46, 88.9) * mm});
            skLineSegment(sketch, "E15.11.17.16", {"start": v(269.46, 88.9) * mm, "end": v(266.7, 84.14) * mm});
            skLineSegment(sketch, "E15.14.17.16", {"start": v(266.7, 84.14) * mm, "end": v(261.2, 84.14) * mm});
            skLineSegment(sketch, "E15.17.17.16", {"start": v(261.2, 84.14) * mm, "end": v(258.46, 88.9) * mm});
            skCircle(sketch, "E15.0.17.17", {"center": v(263.96, 101.6) * mm, "radius": 4.76 * mm, "construction": true});
            skLineSegment(sketch, "E15.2.17.17", {"start": v(258.46, 101.6) * mm, "end": v(261.2, 106.36) * mm});
            skLineSegment(sketch, "E15.5.17.17", {"start": v(261.2, 106.36) * mm, "end": v(266.7, 106.36) * mm});
            skLineSegment(sketch, "E15.8.17.17", {"start": v(266.7, 106.36) * mm, "end": v(269.46, 101.6) * mm});
            skLineSegment(sketch, "E15.11.17.17", {"start": v(269.46, 101.6) * mm, "end": v(266.7, 96.84) * mm});
            skLineSegment(sketch, "E15.14.17.17", {"start": v(266.7, 96.84) * mm, "end": v(261.2, 96.84) * mm});
            skLineSegment(sketch, "E15.17.17.17", {"start": v(261.2, 96.84) * mm, "end": v(258.46, 101.6) * mm});
            skCircle(sketch, "E15.0.17.18", {"center": v(263.96, 114.3) * mm, "radius": 4.76 * mm, "construction": true});
            skLineSegment(sketch, "E15.2.17.18", {"start": v(258.46, 114.3) * mm, "end": v(261.2, 119.06) * mm});
            skLineSegment(sketch, "E15.5.17.18", {"start": v(261.2, 119.06) * mm, "end": v(266.7, 119.06) * mm});
            skLineSegment(sketch, "E15.8.17.18", {"start": v(266.7, 119.06) * mm, "end": v(269.46, 114.3) * mm});
            skLineSegment(sketch, "E15.11.17.18", {"start": v(269.46, 114.3) * mm, "end": v(266.7, 109.54) * mm});
            skLineSegment(sketch, "E15.14.17.18", {"start": v(266.7, 109.54) * mm, "end": v(261.2, 109.54) * mm});
            skLineSegment(sketch, "E15.17.17.18", {"start": v(261.2, 109.54) * mm, "end": v(258.46, 114.3) * mm});
            skCircle(sketch, "E15.0.17.19", {"center": v(263.96, 127) * mm, "radius": 4.76 * mm, "construction": true});
            skLineSegment(sketch, "E15.2.17.19", {"start": v(258.46, 127) * mm, "end": v(261.2, 131.76) * mm});
            skLineSegment(sketch, "E15.5.17.19", {"start": v(261.2, 131.76) * mm, "end": v(266.7, 131.76) * mm});
            skLineSegment(sketch, "E15.8.17.19", {"start": v(266.7, 131.76) * mm, "end": v(269.46, 127) * mm});
            skLineSegment(sketch, "E15.11.17.19", {"start": v(269.46, 127) * mm, "end": v(266.7, 122.24) * mm});
            skLineSegment(sketch, "E15.14.17.19", {"start": v(266.7, 122.24) * mm, "end": v(261.2, 122.24) * mm});
            skLineSegment(sketch, "E15.17.17.19", {"start": v(261.2, 122.24) * mm, "end": v(258.46, 127) * mm});
            skCircle(sketch, "E15.0.18.0", {"center": v(285.95, -114.3) * mm, "radius": 4.76 * mm, "construction": true});
            skLineSegment(sketch, "E15.2.18.0", {"start": v(280.45, -114.3) * mm, "end": v(283.2, -109.54) * mm});
            skLineSegment(sketch, "E15.5.18.0", {"start": v(283.2, -109.54) * mm, "end": v(288.7, -109.54) * mm});
            skLineSegment(sketch, "E15.8.18.0", {"start": v(288.7, -109.54) * mm, "end": v(291.45, -114.3) * mm});
            skLineSegment(sketch, "E15.11.18.0", {"start": v(291.45, -114.3) * mm, "end": v(288.7, -119.06) * mm});
            skLineSegment(sketch, "E15.14.18.0", {"start": v(288.7, -119.06) * mm, "end": v(283.2, -119.06) * mm});
            skLineSegment(sketch, "E15.17.18.0", {"start": v(283.2, -119.06) * mm, "end": v(280.45, -114.3) * mm});
            skCircle(sketch, "E15.0.18.1", {"center": v(285.95, -101.6) * mm, "radius": 4.76 * mm, "construction": true});
            skLineSegment(sketch, "E15.2.18.1", {"start": v(280.45, -101.6) * mm, "end": v(283.2, -96.84) * mm});
            skLineSegment(sketch, "E15.5.18.1", {"start": v(283.2, -96.84) * mm, "end": v(288.7, -96.84) * mm});
            skLineSegment(sketch, "E15.8.18.1", {"start": v(288.7, -96.84) * mm, "end": v(291.45, -101.6) * mm});
            skLineSegment(sketch, "E15.11.18.1", {"start": v(291.45, -101.6) * mm, "end": v(288.7, -106.36) * mm});
            skLineSegment(sketch, "E15.14.18.1", {"start": v(288.7, -106.36) * mm, "end": v(283.2, -106.36) * mm});
            skLineSegment(sketch, "E15.17.18.1", {"start": v(283.2, -106.36) * mm, "end": v(280.45, -101.6) * mm});
            skCircle(sketch, "E15.0.18.2", {"center": v(285.95, -88.9) * mm, "radius": 4.76 * mm, "construction": true});
            skLineSegment(sketch, "E15.2.18.2", {"start": v(280.45, -88.9) * mm, "end": v(283.2, -84.14) * mm});
            skLineSegment(sketch, "E15.5.18.2", {"start": v(283.2, -84.14) * mm, "end": v(288.7, -84.14) * mm});
            skLineSegment(sketch, "E15.8.18.2", {"start": v(288.7, -84.14) * mm, "end": v(291.45, -88.9) * mm});
            skLineSegment(sketch, "E15.11.18.2", {"start": v(291.45, -88.9) * mm, "end": v(288.7, -93.66) * mm});
            skLineSegment(sketch, "E15.14.18.2", {"start": v(288.7, -93.66) * mm, "end": v(283.2, -93.66) * mm});
            skLineSegment(sketch, "E15.17.18.2", {"start": v(283.2, -93.66) * mm, "end": v(280.45, -88.9) * mm});
            skCircle(sketch, "E15.0.18.3", {"center": v(285.95, -76.2) * mm, "radius": 4.76 * mm, "construction": true});
            skLineSegment(sketch, "E15.2.18.3", {"start": v(280.45, -76.2) * mm, "end": v(283.2, -71.44) * mm});
            skLineSegment(sketch, "E15.5.18.3", {"start": v(283.2, -71.44) * mm, "end": v(288.7, -71.44) * mm});
            skLineSegment(sketch, "E15.8.18.3", {"start": v(288.7, -71.44) * mm, "end": v(291.45, -76.2) * mm});
            skLineSegment(sketch, "E15.11.18.3", {"start": v(291.45, -76.2) * mm, "end": v(288.7, -80.96) * mm});
            skLineSegment(sketch, "E15.14.18.3", {"start": v(288.7, -80.96) * mm, "end": v(283.2, -80.96) * mm});
            skLineSegment(sketch, "E15.17.18.3", {"start": v(283.2, -80.96) * mm, "end": v(280.45, -76.2) * mm});
            skCircle(sketch, "E15.0.18.4", {"center": v(285.95, -63.5) * mm, "radius": 4.76 * mm, "construction": true});
            skLineSegment(sketch, "E15.2.18.4", {"start": v(280.45, -63.5) * mm, "end": v(283.2, -58.74) * mm});
            skLineSegment(sketch, "E15.5.18.4", {"start": v(283.2, -58.74) * mm, "end": v(288.7, -58.74) * mm});
            skLineSegment(sketch, "E15.8.18.4", {"start": v(288.7, -58.74) * mm, "end": v(291.45, -63.5) * mm});
            skLineSegment(sketch, "E15.11.18.4", {"start": v(291.45, -63.5) * mm, "end": v(288.7, -68.26) * mm});
            skLineSegment(sketch, "E15.14.18.4", {"start": v(288.7, -68.26) * mm, "end": v(283.2, -68.26) * mm});
            skLineSegment(sketch, "E15.17.18.4", {"start": v(283.2, -68.26) * mm, "end": v(280.45, -63.5) * mm});
            skCircle(sketch, "E15.0.18.5", {"center": v(285.95, -50.8) * mm, "radius": 4.76 * mm, "construction": true});
            skLineSegment(sketch, "E15.2.18.5", {"start": v(280.45, -50.8) * mm, "end": v(283.2, -46.04) * mm});
            skLineSegment(sketch, "E15.5.18.5", {"start": v(283.2, -46.04) * mm, "end": v(288.7, -46.04) * mm});
            skLineSegment(sketch, "E15.8.18.5", {"start": v(288.7, -46.04) * mm, "end": v(291.45, -50.8) * mm});
            skLineSegment(sketch, "E15.11.18.5", {"start": v(291.45, -50.8) * mm, "end": v(288.7, -55.56) * mm});
            skLineSegment(sketch, "E15.14.18.5", {"start": v(288.7, -55.56) * mm, "end": v(283.2, -55.56) * mm});
            skLineSegment(sketch, "E15.17.18.5", {"start": v(283.2, -55.56) * mm, "end": v(280.45, -50.8) * mm});
            skCircle(sketch, "E15.0.18.6", {"center": v(285.95, -38.1) * mm, "radius": 4.76 * mm, "construction": true});
            skLineSegment(sketch, "E15.2.18.6", {"start": v(280.45, -38.1) * mm, "end": v(283.2, -33.34) * mm});
            skLineSegment(sketch, "E15.5.18.6", {"start": v(283.2, -33.34) * mm, "end": v(288.7, -33.34) * mm});
            skLineSegment(sketch, "E15.8.18.6", {"start": v(288.7, -33.34) * mm, "end": v(291.45, -38.1) * mm});
            skLineSegment(sketch, "E15.11.18.6", {"start": v(291.45, -38.1) * mm, "end": v(288.7, -42.86) * mm});
            skLineSegment(sketch, "E15.14.18.6", {"start": v(288.7, -42.86) * mm, "end": v(283.2, -42.86) * mm});
            skLineSegment(sketch, "E15.17.18.6", {"start": v(283.2, -42.86) * mm, "end": v(280.45, -38.1) * mm});
            skCircle(sketch, "E15.0.18.7", {"center": v(285.95, -25.4) * mm, "radius": 4.76 * mm, "construction": true});
            skLineSegment(sketch, "E15.2.18.7", {"start": v(280.45, -25.4) * mm, "end": v(283.2, -20.64) * mm});
            skLineSegment(sketch, "E15.5.18.7", {"start": v(283.2, -20.64) * mm, "end": v(288.7, -20.64) * mm});
            skLineSegment(sketch, "E15.8.18.7", {"start": v(288.7, -20.64) * mm, "end": v(291.45, -25.4) * mm});
            skLineSegment(sketch, "E15.11.18.7", {"start": v(291.45, -25.4) * mm, "end": v(288.7, -30.16) * mm});
            skLineSegment(sketch, "E15.14.18.7", {"start": v(288.7, -30.16) * mm, "end": v(283.2, -30.16) * mm});
            skLineSegment(sketch, "E15.17.18.7", {"start": v(283.2, -30.16) * mm, "end": v(280.45, -25.4) * mm});
            skCircle(sketch, "E15.0.18.8", {"center": v(285.95, -12.7) * mm, "radius": 4.76 * mm, "construction": true});
            skLineSegment(sketch, "E15.2.18.8", {"start": v(280.45, -12.7) * mm, "end": v(283.2, -7.94) * mm});
            skLineSegment(sketch, "E15.5.18.8", {"start": v(283.2, -7.94) * mm, "end": v(288.7, -7.94) * mm});
            skLineSegment(sketch, "E15.8.18.8", {"start": v(288.7, -7.94) * mm, "end": v(291.45, -12.7) * mm});
            skLineSegment(sketch, "E15.11.18.8", {"start": v(291.45, -12.7) * mm, "end": v(288.7, -17.46) * mm});
            skLineSegment(sketch, "E15.14.18.8", {"start": v(288.7, -17.46) * mm, "end": v(283.2, -17.46) * mm});
            skLineSegment(sketch, "E15.17.18.8", {"start": v(283.2, -17.46) * mm, "end": v(280.45, -12.7) * mm});
            skCircle(sketch, "E15.0.18.9", {"center": v(285.95, 0) * mm, "radius": 4.76 * mm, "construction": true});
            skLineSegment(sketch, "E15.2.18.9", {"start": v(280.45, 0) * mm, "end": v(283.2, 4.76) * mm});
            skLineSegment(sketch, "E15.5.18.9", {"start": v(283.2, 4.76) * mm, "end": v(288.7, 4.76) * mm});
            skLineSegment(sketch, "E15.8.18.9", {"start": v(288.7, 4.76) * mm, "end": v(291.45, 0) * mm});
            skLineSegment(sketch, "E15.11.18.9", {"start": v(291.45, 0) * mm, "end": v(288.7, -4.76) * mm});
            skLineSegment(sketch, "E15.14.18.9", {"start": v(288.7, -4.76) * mm, "end": v(283.2, -4.76) * mm});
            skLineSegment(sketch, "E15.17.18.9", {"start": v(283.2, -4.76) * mm, "end": v(280.45, 0) * mm});
            skCircle(sketch, "E15.0.18.10", {"center": v(285.95, 12.7) * mm, "radius": 4.76 * mm, "construction": true});
            skLineSegment(sketch, "E15.2.18.10", {"start": v(280.45, 12.7) * mm, "end": v(283.2, 17.46) * mm});
            skLineSegment(sketch, "E15.5.18.10", {"start": v(283.2, 17.46) * mm, "end": v(288.7, 17.46) * mm});
            skLineSegment(sketch, "E15.8.18.10", {"start": v(288.7, 17.46) * mm, "end": v(291.45, 12.7) * mm});
            skLineSegment(sketch, "E15.11.18.10", {"start": v(291.45, 12.7) * mm, "end": v(288.7, 7.94) * mm});
            skLineSegment(sketch, "E15.14.18.10", {"start": v(288.7, 7.94) * mm, "end": v(283.2, 7.94) * mm});
            skLineSegment(sketch, "E15.17.18.10", {"start": v(283.2, 7.94) * mm, "end": v(280.45, 12.7) * mm});
            skCircle(sketch, "E15.0.18.11", {"center": v(285.95, 25.4) * mm, "radius": 4.76 * mm, "construction": true});
            skLineSegment(sketch, "E15.2.18.11", {"start": v(280.45, 25.4) * mm, "end": v(283.2, 30.16) * mm});
            skLineSegment(sketch, "E15.5.18.11", {"start": v(283.2, 30.16) * mm, "end": v(288.7, 30.16) * mm});
            skLineSegment(sketch, "E15.8.18.11", {"start": v(288.7, 30.16) * mm, "end": v(291.45, 25.4) * mm});
            skLineSegment(sketch, "E15.11.18.11", {"start": v(291.45, 25.4) * mm, "end": v(288.7, 20.64) * mm});
            skLineSegment(sketch, "E15.14.18.11", {"start": v(288.7, 20.64) * mm, "end": v(283.2, 20.64) * mm});
            skLineSegment(sketch, "E15.17.18.11", {"start": v(283.2, 20.64) * mm, "end": v(280.45, 25.4) * mm});
            skCircle(sketch, "E15.0.18.12", {"center": v(285.95, 38.1) * mm, "radius": 4.76 * mm, "construction": true});
            skLineSegment(sketch, "E15.2.18.12", {"start": v(280.45, 38.1) * mm, "end": v(283.2, 42.86) * mm});
            skLineSegment(sketch, "E15.5.18.12", {"start": v(283.2, 42.86) * mm, "end": v(288.7, 42.86) * mm});
            skLineSegment(sketch, "E15.8.18.12", {"start": v(288.7, 42.86) * mm, "end": v(291.45, 38.1) * mm});
            skLineSegment(sketch, "E15.11.18.12", {"start": v(291.45, 38.1) * mm, "end": v(288.7, 33.34) * mm});
            skLineSegment(sketch, "E15.14.18.12", {"start": v(288.7, 33.34) * mm, "end": v(283.2, 33.34) * mm});
            skLineSegment(sketch, "E15.17.18.12", {"start": v(283.2, 33.34) * mm, "end": v(280.45, 38.1) * mm});
            skCircle(sketch, "E15.0.18.13", {"center": v(285.95, 50.8) * mm, "radius": 4.76 * mm, "construction": true});
            skLineSegment(sketch, "E15.2.18.13", {"start": v(280.45, 50.8) * mm, "end": v(283.2, 55.56) * mm});
            skLineSegment(sketch, "E15.5.18.13", {"start": v(283.2, 55.56) * mm, "end": v(288.7, 55.56) * mm});
            skLineSegment(sketch, "E15.8.18.13", {"start": v(288.7, 55.56) * mm, "end": v(291.45, 50.8) * mm});
            skLineSegment(sketch, "E15.11.18.13", {"start": v(291.45, 50.8) * mm, "end": v(288.7, 46.04) * mm});
            skLineSegment(sketch, "E15.14.18.13", {"start": v(288.7, 46.04) * mm, "end": v(283.2, 46.04) * mm});
            skLineSegment(sketch, "E15.17.18.13", {"start": v(283.2, 46.04) * mm, "end": v(280.45, 50.8) * mm});
            skCircle(sketch, "E15.0.18.14", {"center": v(285.95, 63.5) * mm, "radius": 4.76 * mm, "construction": true});
            skLineSegment(sketch, "E15.2.18.14", {"start": v(280.45, 63.5) * mm, "end": v(283.2, 68.26) * mm});
            skLineSegment(sketch, "E15.5.18.14", {"start": v(283.2, 68.26) * mm, "end": v(288.7, 68.26) * mm});
            skLineSegment(sketch, "E15.8.18.14", {"start": v(288.7, 68.26) * mm, "end": v(291.45, 63.5) * mm});
            skLineSegment(sketch, "E15.11.18.14", {"start": v(291.45, 63.5) * mm, "end": v(288.7, 58.74) * mm});
            skLineSegment(sketch, "E15.14.18.14", {"start": v(288.7, 58.74) * mm, "end": v(283.2, 58.74) * mm});
            skLineSegment(sketch, "E15.17.18.14", {"start": v(283.2, 58.74) * mm, "end": v(280.45, 63.5) * mm});
            skCircle(sketch, "E15.0.18.15", {"center": v(285.95, 76.2) * mm, "radius": 4.76 * mm, "construction": true});
            skLineSegment(sketch, "E15.2.18.15", {"start": v(280.45, 76.2) * mm, "end": v(283.2, 80.96) * mm});
            skLineSegment(sketch, "E15.5.18.15", {"start": v(283.2, 80.96) * mm, "end": v(288.7, 80.96) * mm});
            skLineSegment(sketch, "E15.8.18.15", {"start": v(288.7, 80.96) * mm, "end": v(291.45, 76.2) * mm});
            skLineSegment(sketch, "E15.11.18.15", {"start": v(291.45, 76.2) * mm, "end": v(288.7, 71.44) * mm});
            skLineSegment(sketch, "E15.14.18.15", {"start": v(288.7, 71.44) * mm, "end": v(283.2, 71.44) * mm});
            skLineSegment(sketch, "E15.17.18.15", {"start": v(283.2, 71.44) * mm, "end": v(280.45, 76.2) * mm});
            skCircle(sketch, "E15.0.18.16", {"center": v(285.95, 88.9) * mm, "radius": 4.76 * mm, "construction": true});
            skLineSegment(sketch, "E15.2.18.16", {"start": v(280.45, 88.9) * mm, "end": v(283.2, 93.66) * mm});
            skLineSegment(sketch, "E15.5.18.16", {"start": v(283.2, 93.66) * mm, "end": v(288.7, 93.66) * mm});
            skLineSegment(sketch, "E15.8.18.16", {"start": v(288.7, 93.66) * mm, "end": v(291.45, 88.9) * mm});
            skLineSegment(sketch, "E15.11.18.16", {"start": v(291.45, 88.9) * mm, "end": v(288.7, 84.14) * mm});
            skLineSegment(sketch, "E15.14.18.16", {"start": v(288.7, 84.14) * mm, "end": v(283.2, 84.14) * mm});
            skLineSegment(sketch, "E15.17.18.16", {"start": v(283.2, 84.14) * mm, "end": v(280.45, 88.9) * mm});
            skCircle(sketch, "E15.0.18.17", {"center": v(285.95, 101.6) * mm, "radius": 4.76 * mm, "construction": true});
            skLineSegment(sketch, "E15.2.18.17", {"start": v(280.45, 101.6) * mm, "end": v(283.2, 106.36) * mm});
            skLineSegment(sketch, "E15.5.18.17", {"start": v(283.2, 106.36) * mm, "end": v(288.7, 106.36) * mm});
            skLineSegment(sketch, "E15.8.18.17", {"start": v(288.7, 106.36) * mm, "end": v(291.45, 101.6) * mm});
            skLineSegment(sketch, "E15.11.18.17", {"start": v(291.45, 101.6) * mm, "end": v(288.7, 96.84) * mm});
            skLineSegment(sketch, "E15.14.18.17", {"start": v(288.7, 96.84) * mm, "end": v(283.2, 96.84) * mm});
            skLineSegment(sketch, "E15.17.18.17", {"start": v(283.2, 96.84) * mm, "end": v(280.45, 101.6) * mm});
            skCircle(sketch, "E15.0.18.18", {"center": v(285.95, 114.3) * mm, "radius": 4.76 * mm, "construction": true});
            skLineSegment(sketch, "E15.2.18.18", {"start": v(280.45, 114.3) * mm, "end": v(283.2, 119.06) * mm});
            skLineSegment(sketch, "E15.5.18.18", {"start": v(283.2, 119.06) * mm, "end": v(288.7, 119.06) * mm});
            skLineSegment(sketch, "E15.8.18.18", {"start": v(288.7, 119.06) * mm, "end": v(291.45, 114.3) * mm});
            skLineSegment(sketch, "E15.11.18.18", {"start": v(291.45, 114.3) * mm, "end": v(288.7, 109.54) * mm});
            skLineSegment(sketch, "E15.14.18.18", {"start": v(288.7, 109.54) * mm, "end": v(283.2, 109.54) * mm});
            skLineSegment(sketch, "E15.17.18.18", {"start": v(283.2, 109.54) * mm, "end": v(280.45, 114.3) * mm});
            skCircle(sketch, "E15.0.18.19", {"center": v(285.95, 127) * mm, "radius": 4.76 * mm, "construction": true});
            skLineSegment(sketch, "E15.2.18.19", {"start": v(280.45, 127) * mm, "end": v(283.2, 131.76) * mm});
            skLineSegment(sketch, "E15.5.18.19", {"start": v(283.2, 131.76) * mm, "end": v(288.7, 131.76) * mm});
            skLineSegment(sketch, "E15.8.18.19", {"start": v(288.7, 131.76) * mm, "end": v(291.45, 127) * mm});
            skLineSegment(sketch, "E15.11.18.19", {"start": v(291.45, 127) * mm, "end": v(288.7, 122.24) * mm});
            skLineSegment(sketch, "E15.14.18.19", {"start": v(288.7, 122.24) * mm, "end": v(283.2, 122.24) * mm});
            skLineSegment(sketch, "E15.17.18.19", {"start": v(283.2, 122.24) * mm, "end": v(280.45, 127) * mm});
            skCircle(sketch, "E15.0.19.0", {"center": v(307.95, -114.3) * mm, "radius": 4.76 * mm, "construction": true});
            skLineSegment(sketch, "E15.2.19.0", {"start": v(302.45, -114.3) * mm, "end": v(305.2, -109.54) * mm});
            skLineSegment(sketch, "E15.5.19.0", {"start": v(305.2, -109.54) * mm, "end": v(310.7, -109.54) * mm});
            skLineSegment(sketch, "E15.8.19.0", {"start": v(310.7, -109.54) * mm, "end": v(313.45, -114.3) * mm});
            skLineSegment(sketch, "E15.11.19.0", {"start": v(313.45, -114.3) * mm, "end": v(310.7, -119.06) * mm});
            skLineSegment(sketch, "E15.14.19.0", {"start": v(310.7, -119.06) * mm, "end": v(305.2, -119.06) * mm});
            skLineSegment(sketch, "E15.17.19.0", {"start": v(305.2, -119.06) * mm, "end": v(302.45, -114.3) * mm});
            skCircle(sketch, "E15.0.19.1", {"center": v(307.95, -101.6) * mm, "radius": 4.76 * mm, "construction": true});
            skLineSegment(sketch, "E15.2.19.1", {"start": v(302.45, -101.6) * mm, "end": v(305.2, -96.84) * mm});
            skLineSegment(sketch, "E15.5.19.1", {"start": v(305.2, -96.84) * mm, "end": v(310.7, -96.84) * mm});
            skLineSegment(sketch, "E15.8.19.1", {"start": v(310.7, -96.84) * mm, "end": v(313.45, -101.6) * mm});
            skLineSegment(sketch, "E15.11.19.1", {"start": v(313.45, -101.6) * mm, "end": v(310.7, -106.36) * mm});
            skLineSegment(sketch, "E15.14.19.1", {"start": v(310.7, -106.36) * mm, "end": v(305.2, -106.36) * mm});
            skLineSegment(sketch, "E15.17.19.1", {"start": v(305.2, -106.36) * mm, "end": v(302.45, -101.6) * mm});
            skCircle(sketch, "E15.0.19.2", {"center": v(307.95, -88.9) * mm, "radius": 4.76 * mm, "construction": true});
            skLineSegment(sketch, "E15.2.19.2", {"start": v(302.45, -88.9) * mm, "end": v(305.2, -84.14) * mm});
            skLineSegment(sketch, "E15.5.19.2", {"start": v(305.2, -84.14) * mm, "end": v(310.7, -84.14) * mm});
            skLineSegment(sketch, "E15.8.19.2", {"start": v(310.7, -84.14) * mm, "end": v(313.45, -88.9) * mm});
            skLineSegment(sketch, "E15.11.19.2", {"start": v(313.45, -88.9) * mm, "end": v(310.7, -93.66) * mm});
            skLineSegment(sketch, "E15.14.19.2", {"start": v(310.7, -93.66) * mm, "end": v(305.2, -93.66) * mm});
            skLineSegment(sketch, "E15.17.19.2", {"start": v(305.2, -93.66) * mm, "end": v(302.45, -88.9) * mm});
            skCircle(sketch, "E15.0.19.3", {"center": v(307.95, -76.2) * mm, "radius": 4.76 * mm, "construction": true});
            skLineSegment(sketch, "E15.2.19.3", {"start": v(302.45, -76.2) * mm, "end": v(305.2, -71.44) * mm});
            skLineSegment(sketch, "E15.5.19.3", {"start": v(305.2, -71.44) * mm, "end": v(310.7, -71.44) * mm});
            skLineSegment(sketch, "E15.8.19.3", {"start": v(310.7, -71.44) * mm, "end": v(313.45, -76.2) * mm});
            skLineSegment(sketch, "E15.11.19.3", {"start": v(313.45, -76.2) * mm, "end": v(310.7, -80.96) * mm});
            skLineSegment(sketch, "E15.14.19.3", {"start": v(310.7, -80.96) * mm, "end": v(305.2, -80.96) * mm});
            skLineSegment(sketch, "E15.17.19.3", {"start": v(305.2, -80.96) * mm, "end": v(302.45, -76.2) * mm});
            skCircle(sketch, "E15.0.19.4", {"center": v(307.95, -63.5) * mm, "radius": 4.76 * mm, "construction": true});
            skLineSegment(sketch, "E15.2.19.4", {"start": v(302.45, -63.5) * mm, "end": v(305.2, -58.74) * mm});
            skLineSegment(sketch, "E15.5.19.4", {"start": v(305.2, -58.74) * mm, "end": v(310.7, -58.74) * mm});
            skLineSegment(sketch, "E15.8.19.4", {"start": v(310.7, -58.74) * mm, "end": v(313.45, -63.5) * mm});
            skLineSegment(sketch, "E15.11.19.4", {"start": v(313.45, -63.5) * mm, "end": v(310.7, -68.26) * mm});
            skLineSegment(sketch, "E15.14.19.4", {"start": v(310.7, -68.26) * mm, "end": v(305.2, -68.26) * mm});
            skLineSegment(sketch, "E15.17.19.4", {"start": v(305.2, -68.26) * mm, "end": v(302.45, -63.5) * mm});
            skCircle(sketch, "E15.0.19.5", {"center": v(307.95, -50.8) * mm, "radius": 4.76 * mm, "construction": true});
            skLineSegment(sketch, "E15.2.19.5", {"start": v(302.45, -50.8) * mm, "end": v(305.2, -46.04) * mm});
            skLineSegment(sketch, "E15.5.19.5", {"start": v(305.2, -46.04) * mm, "end": v(310.7, -46.04) * mm});
            skLineSegment(sketch, "E15.8.19.5", {"start": v(310.7, -46.04) * mm, "end": v(313.45, -50.8) * mm});
            skLineSegment(sketch, "E15.11.19.5", {"start": v(313.45, -50.8) * mm, "end": v(310.7, -55.56) * mm});
            skLineSegment(sketch, "E15.14.19.5", {"start": v(310.7, -55.56) * mm, "end": v(305.2, -55.56) * mm});
            skLineSegment(sketch, "E15.17.19.5", {"start": v(305.2, -55.56) * mm, "end": v(302.45, -50.8) * mm});
            skCircle(sketch, "E15.0.19.6", {"center": v(307.95, -38.1) * mm, "radius": 4.76 * mm, "construction": true});
            skLineSegment(sketch, "E15.2.19.6", {"start": v(302.45, -38.1) * mm, "end": v(305.2, -33.34) * mm});
            skLineSegment(sketch, "E15.5.19.6", {"start": v(305.2, -33.34) * mm, "end": v(310.7, -33.34) * mm});
            skLineSegment(sketch, "E15.8.19.6", {"start": v(310.7, -33.34) * mm, "end": v(313.45, -38.1) * mm});
            skLineSegment(sketch, "E15.11.19.6", {"start": v(313.45, -38.1) * mm, "end": v(310.7, -42.86) * mm});
            skLineSegment(sketch, "E15.14.19.6", {"start": v(310.7, -42.86) * mm, "end": v(305.2, -42.86) * mm});
            skLineSegment(sketch, "E15.17.19.6", {"start": v(305.2, -42.86) * mm, "end": v(302.45, -38.1) * mm});
            skCircle(sketch, "E15.0.19.7", {"center": v(307.95, -25.4) * mm, "radius": 4.76 * mm, "construction": true});
            skLineSegment(sketch, "E15.2.19.7", {"start": v(302.45, -25.4) * mm, "end": v(305.2, -20.64) * mm});
            skLineSegment(sketch, "E15.5.19.7", {"start": v(305.2, -20.64) * mm, "end": v(310.7, -20.64) * mm});
            skLineSegment(sketch, "E15.8.19.7", {"start": v(310.7, -20.64) * mm, "end": v(313.45, -25.4) * mm});
            skLineSegment(sketch, "E15.11.19.7", {"start": v(313.45, -25.4) * mm, "end": v(310.7, -30.16) * mm});
            skLineSegment(sketch, "E15.14.19.7", {"start": v(310.7, -30.16) * mm, "end": v(305.2, -30.16) * mm});
            skLineSegment(sketch, "E15.17.19.7", {"start": v(305.2, -30.16) * mm, "end": v(302.45, -25.4) * mm});
            skCircle(sketch, "E15.0.19.8", {"center": v(307.95, -12.7) * mm, "radius": 4.76 * mm, "construction": true});
            skLineSegment(sketch, "E15.2.19.8", {"start": v(302.45, -12.7) * mm, "end": v(305.2, -7.94) * mm});
            skLineSegment(sketch, "E15.5.19.8", {"start": v(305.2, -7.94) * mm, "end": v(310.7, -7.94) * mm});
            skLineSegment(sketch, "E15.8.19.8", {"start": v(310.7, -7.94) * mm, "end": v(313.45, -12.7) * mm});
            skLineSegment(sketch, "E15.11.19.8", {"start": v(313.45, -12.7) * mm, "end": v(310.7, -17.46) * mm});
            skLineSegment(sketch, "E15.14.19.8", {"start": v(310.7, -17.46) * mm, "end": v(305.2, -17.46) * mm});
            skLineSegment(sketch, "E15.17.19.8", {"start": v(305.2, -17.46) * mm, "end": v(302.45, -12.7) * mm});
            skCircle(sketch, "E15.0.19.9", {"center": v(307.95, 0) * mm, "radius": 4.76 * mm, "construction": true});
            skLineSegment(sketch, "E15.2.19.9", {"start": v(302.45, 0) * mm, "end": v(305.2, 4.76) * mm});
            skLineSegment(sketch, "E15.5.19.9", {"start": v(305.2, 4.76) * mm, "end": v(310.7, 4.76) * mm});
            skLineSegment(sketch, "E15.8.19.9", {"start": v(310.7, 4.76) * mm, "end": v(313.45, 0) * mm});
            skLineSegment(sketch, "E15.11.19.9", {"start": v(313.45, 0) * mm, "end": v(310.7, -4.76) * mm});
            skLineSegment(sketch, "E15.14.19.9", {"start": v(310.7, -4.76) * mm, "end": v(305.2, -4.76) * mm});
            skLineSegment(sketch, "E15.17.19.9", {"start": v(305.2, -4.76) * mm, "end": v(302.45, 0) * mm});
            skCircle(sketch, "E15.0.19.10", {"center": v(307.95, 12.7) * mm, "radius": 4.76 * mm, "construction": true});
            skLineSegment(sketch, "E15.2.19.10", {"start": v(302.45, 12.7) * mm, "end": v(305.2, 17.46) * mm});
            skLineSegment(sketch, "E15.5.19.10", {"start": v(305.2, 17.46) * mm, "end": v(310.7, 17.46) * mm});
            skLineSegment(sketch, "E15.8.19.10", {"start": v(310.7, 17.46) * mm, "end": v(313.45, 12.7) * mm});
            skLineSegment(sketch, "E15.11.19.10", {"start": v(313.45, 12.7) * mm, "end": v(310.7, 7.94) * mm});
            skLineSegment(sketch, "E15.14.19.10", {"start": v(310.7, 7.94) * mm, "end": v(305.2, 7.94) * mm});
            skLineSegment(sketch, "E15.17.19.10", {"start": v(305.2, 7.94) * mm, "end": v(302.45, 12.7) * mm});
            skCircle(sketch, "E15.0.19.11", {"center": v(307.95, 25.4) * mm, "radius": 4.76 * mm, "construction": true});
            skLineSegment(sketch, "E15.2.19.11", {"start": v(302.45, 25.4) * mm, "end": v(305.2, 30.16) * mm});
            skLineSegment(sketch, "E15.5.19.11", {"start": v(305.2, 30.16) * mm, "end": v(310.7, 30.16) * mm});
            skLineSegment(sketch, "E15.8.19.11", {"start": v(310.7, 30.16) * mm, "end": v(313.45, 25.4) * mm});
            skLineSegment(sketch, "E15.11.19.11", {"start": v(313.45, 25.4) * mm, "end": v(310.7, 20.64) * mm});
            skLineSegment(sketch, "E15.14.19.11", {"start": v(310.7, 20.64) * mm, "end": v(305.2, 20.64) * mm});
            skLineSegment(sketch, "E15.17.19.11", {"start": v(305.2, 20.64) * mm, "end": v(302.45, 25.4) * mm});
            skCircle(sketch, "E15.0.19.12", {"center": v(307.95, 38.1) * mm, "radius": 4.76 * mm, "construction": true});
            skLineSegment(sketch, "E15.2.19.12", {"start": v(302.45, 38.1) * mm, "end": v(305.2, 42.86) * mm});
            skLineSegment(sketch, "E15.5.19.12", {"start": v(305.2, 42.86) * mm, "end": v(310.7, 42.86) * mm});
            skLineSegment(sketch, "E15.8.19.12", {"start": v(310.7, 42.86) * mm, "end": v(313.45, 38.1) * mm});
            skLineSegment(sketch, "E15.11.19.12", {"start": v(313.45, 38.1) * mm, "end": v(310.7, 33.34) * mm});
            skLineSegment(sketch, "E15.14.19.12", {"start": v(310.7, 33.34) * mm, "end": v(305.2, 33.34) * mm});
            skLineSegment(sketch, "E15.17.19.12", {"start": v(305.2, 33.34) * mm, "end": v(302.45, 38.1) * mm});
            skCircle(sketch, "E15.0.19.13", {"center": v(307.95, 50.8) * mm, "radius": 4.76 * mm, "construction": true});
            skLineSegment(sketch, "E15.2.19.13", {"start": v(302.45, 50.8) * mm, "end": v(305.2, 55.56) * mm});
            skLineSegment(sketch, "E15.5.19.13", {"start": v(305.2, 55.56) * mm, "end": v(310.7, 55.56) * mm});
            skLineSegment(sketch, "E15.8.19.13", {"start": v(310.7, 55.56) * mm, "end": v(313.45, 50.8) * mm});
            skLineSegment(sketch, "E15.11.19.13", {"start": v(313.45, 50.8) * mm, "end": v(310.7, 46.04) * mm});
            skLineSegment(sketch, "E15.14.19.13", {"start": v(310.7, 46.04) * mm, "end": v(305.2, 46.04) * mm});
            skLineSegment(sketch, "E15.17.19.13", {"start": v(305.2, 46.04) * mm, "end": v(302.45, 50.8) * mm});
            skCircle(sketch, "E15.0.19.14", {"center": v(307.95, 63.5) * mm, "radius": 4.76 * mm, "construction": true});
            skLineSegment(sketch, "E15.2.19.14", {"start": v(302.45, 63.5) * mm, "end": v(305.2, 68.26) * mm});
            skLineSegment(sketch, "E15.5.19.14", {"start": v(305.2, 68.26) * mm, "end": v(310.7, 68.26) * mm});
            skLineSegment(sketch, "E15.8.19.14", {"start": v(310.7, 68.26) * mm, "end": v(313.45, 63.5) * mm});
            skLineSegment(sketch, "E15.11.19.14", {"start": v(313.45, 63.5) * mm, "end": v(310.7, 58.74) * mm});
            skLineSegment(sketch, "E15.14.19.14", {"start": v(310.7, 58.74) * mm, "end": v(305.2, 58.74) * mm});
            skLineSegment(sketch, "E15.17.19.14", {"start": v(305.2, 58.74) * mm, "end": v(302.45, 63.5) * mm});
            skCircle(sketch, "E15.0.19.15", {"center": v(307.95, 76.2) * mm, "radius": 4.76 * mm, "construction": true});
            skLineSegment(sketch, "E15.2.19.15", {"start": v(302.45, 76.2) * mm, "end": v(305.2, 80.96) * mm});
            skLineSegment(sketch, "E15.5.19.15", {"start": v(305.2, 80.96) * mm, "end": v(310.7, 80.96) * mm});
            skLineSegment(sketch, "E15.8.19.15", {"start": v(310.7, 80.96) * mm, "end": v(313.45, 76.2) * mm});
            skLineSegment(sketch, "E15.11.19.15", {"start": v(313.45, 76.2) * mm, "end": v(310.7, 71.44) * mm});
            skLineSegment(sketch, "E15.14.19.15", {"start": v(310.7, 71.44) * mm, "end": v(305.2, 71.44) * mm});
            skLineSegment(sketch, "E15.17.19.15", {"start": v(305.2, 71.44) * mm, "end": v(302.45, 76.2) * mm});
            skCircle(sketch, "E15.0.19.16", {"center": v(307.95, 88.9) * mm, "radius": 4.76 * mm, "construction": true});
            skLineSegment(sketch, "E15.2.19.16", {"start": v(302.45, 88.9) * mm, "end": v(305.2, 93.66) * mm});
            skLineSegment(sketch, "E15.5.19.16", {"start": v(305.2, 93.66) * mm, "end": v(310.7, 93.66) * mm});
            skLineSegment(sketch, "E15.8.19.16", {"start": v(310.7, 93.66) * mm, "end": v(313.45, 88.9) * mm});
            skLineSegment(sketch, "E15.11.19.16", {"start": v(313.45, 88.9) * mm, "end": v(310.7, 84.14) * mm});
            skLineSegment(sketch, "E15.14.19.16", {"start": v(310.7, 84.14) * mm, "end": v(305.2, 84.14) * mm});
            skLineSegment(sketch, "E15.17.19.16", {"start": v(305.2, 84.14) * mm, "end": v(302.45, 88.9) * mm});
            skCircle(sketch, "E15.0.19.17", {"center": v(307.95, 101.6) * mm, "radius": 4.76 * mm, "construction": true});
            skLineSegment(sketch, "E15.2.19.17", {"start": v(302.45, 101.6) * mm, "end": v(305.2, 106.36) * mm});
            skLineSegment(sketch, "E15.5.19.17", {"start": v(305.2, 106.36) * mm, "end": v(310.7, 106.36) * mm});
            skLineSegment(sketch, "E15.8.19.17", {"start": v(310.7, 106.36) * mm, "end": v(313.45, 101.6) * mm});
            skLineSegment(sketch, "E15.11.19.17", {"start": v(313.45, 101.6) * mm, "end": v(310.7, 96.84) * mm});
            skLineSegment(sketch, "E15.14.19.17", {"start": v(310.7, 96.84) * mm, "end": v(305.2, 96.84) * mm});
            skLineSegment(sketch, "E15.17.19.17", {"start": v(305.2, 96.84) * mm, "end": v(302.45, 101.6) * mm});
            skCircle(sketch, "E15.0.19.18", {"center": v(307.95, 114.3) * mm, "radius": 4.76 * mm, "construction": true});
            skLineSegment(sketch, "E15.2.19.18", {"start": v(302.45, 114.3) * mm, "end": v(305.2, 119.06) * mm});
            skLineSegment(sketch, "E15.5.19.18", {"start": v(305.2, 119.06) * mm, "end": v(310.7, 119.06) * mm});
            skLineSegment(sketch, "E15.8.19.18", {"start": v(310.7, 119.06) * mm, "end": v(313.45, 114.3) * mm});
            skLineSegment(sketch, "E15.11.19.18", {"start": v(313.45, 114.3) * mm, "end": v(310.7, 109.54) * mm});
            skLineSegment(sketch, "E15.14.19.18", {"start": v(310.7, 109.54) * mm, "end": v(305.2, 109.54) * mm});
            skLineSegment(sketch, "E15.17.19.18", {"start": v(305.2, 109.54) * mm, "end": v(302.45, 114.3) * mm});
            skCircle(sketch, "E15.0.19.19", {"center": v(307.95, 127) * mm, "radius": 4.76 * mm, "construction": true});
            skLineSegment(sketch, "E15.2.19.19", {"start": v(302.45, 127) * mm, "end": v(305.2, 131.76) * mm});
            skLineSegment(sketch, "E15.5.19.19", {"start": v(305.2, 131.76) * mm, "end": v(310.7, 131.76) * mm});
            skLineSegment(sketch, "E15.8.19.19", {"start": v(310.7, 131.76) * mm, "end": v(313.45, 127) * mm});
            skLineSegment(sketch, "E15.11.19.19", {"start": v(313.45, 127) * mm, "end": v(310.7, 122.24) * mm});
            skLineSegment(sketch, "E15.14.19.19", {"start": v(310.7, 122.24) * mm, "end": v(305.2, 122.24) * mm});
            skLineSegment(sketch, "E15.17.19.19", {"start": v(305.2, 122.24) * mm, "end": v(302.45, 127) * mm});
            skSolve(sketch);
        }
        {
            var Q0;
            Q0=qSketchRegion(id+"F2",true);
            extrude(context, id + "F3", {"entities" : qUnion([Q0]), "operationType" : NewBodyOperationType.REMOVE, "oppositeDirection" : true, "depth" : 25.4 * mm, "offsetDistance" : 25.4 * mm});
        }
        {
            var Q0;
            Q0=makeQuery(id+"F1.opExtrude","CAP_FACE",FACE,{"disambiguationData":[OSD([sQuery(id+"F0.wireOp",EDGE,"E0")])],"isStart":false});
            var sketch = newSketch(context, id + "F4", { "sketchPlane" : qUnion([Q0])});
            skCircle(sketch, "E16", {"center": v(0, 0) * mm, "radius": 115.89 * mm});
            skCircle(sketch, "E17", {"center": v(0, 0) * mm, "radius": 123.02 * mm});
            skSolve(sketch);
        }
        {
            var Q0;
            Q0=qSketchRegion(id+"F4",true);
            var Q1;
            Q1=makeQuery(id+"F1.opExtrude","CAP_FACE",FACE,{"disambiguationData":[OSD([sQuery(id+"F0.wireOp",EDGE,"E0")])],"isStart":true});
            extrude(context, id + "F5", {"entities" : qUnion([Q0]), "operationType" : NewBodyOperationType.ADD, "endBound" : BoundingType.UP_TO_SURFACE, "oppositeDirection" : true, "depth" : 25.4 * mm, "endBoundEntityFace" : qUnion([Q1]), "offsetDistance" : 25.4 * mm});
        }
        {
            var Q0;
            Q0=makeQuery(id+"F5.boolean.opBoolean","MERGE",FACE,{"derivedFrom":[makeQuery(id+"F1.opExtrude","CAP_FACE",FACE,{"disambiguationData":[OSD([sQuery(id+"F0.wireOp",EDGE,"E0")])],"isStart":false}),makeQuery(id+"F5.opExtrude","CAP_FACE",FACE,{"disambiguationData":[OSD([sQuery(id+"F4.wireOp",EDGE,"gzat5XN6-aFc3-cK17-7gGf-ptE3Ki8R4cpB"),sQuery(id+"F4.wireOp",EDGE,"E16")])],"isStart":true})]});
            var sketch = newSketch(context, id + "F6", { "sketchPlane" : qUnion([Q0])});
            skLineSegment(sketch, "E18.bottom", {"start": v(62.26, 97.67) * mm, "end": v(65.08, 97.67) * mm});
            skLineSegment(sketch, "E18.top", {"start": v(62.26, 96.12) * mm, "end": v(65.08, 96.12) * mm});
            skLineSegment(sketch, "E18.left", {"start": v(62.26, 97.67) * mm, "end": v(62.26, 96.12) * mm});
            skLineSegment(sketch, "E18.right", {"start": v(65.08, 97.67) * mm, "end": v(65.08, 96.12) * mm});
            skLineSegment(sketch, "E19.bottom", {"start": v(119, -5.1) * mm, "end": v(114.46, -5.1) * mm});
            skLineSegment(sketch, "E19.top", {"start": v(119, -8.9) * mm, "end": v(114.46, -8.9) * mm});
            skLineSegment(sketch, "E19.left", {"start": v(119, -5.1) * mm, "end": v(119, -8.9) * mm});
            skLineSegment(sketch, "E19.right", {"start": v(114.46, -5.1) * mm, "end": v(114.46, -8.9) * mm});
            skLineSegment(sketch, "E20.bottom", {"start": v(61.69, -99.69) * mm, "end": v(65.85, -99.69) * mm});
            skLineSegment(sketch, "E20.top", {"start": v(61.69, -95.43) * mm, "end": v(65.85, -95.43) * mm});
            skLineSegment(sketch, "E20.left", {"start": v(61.69, -99.69) * mm, "end": v(61.69, -95.43) * mm});
            skLineSegment(sketch, "E20.right", {"start": v(65.85, -99.69) * mm, "end": v(65.85, -95.43) * mm});
            skLineSegment(sketch, "E21.bottom", {"start": v(51.35, 104.15) * mm, "end": v(53.35, 104.15) * mm});
            skLineSegment(sketch, "E21.top", {"start": v(51.35, 102.74) * mm, "end": v(53.35, 102.74) * mm});
            skLineSegment(sketch, "E21.left", {"start": v(51.35, 104.15) * mm, "end": v(51.35, 102.74) * mm});
            skLineSegment(sketch, "E21.right", {"start": v(53.35, 104.15) * mm, "end": v(53.35, 102.74) * mm});
            skLineSegment(sketch, "E22.bottom", {"start": v(-53.73, 104.26) * mm, "end": v(-51.28, 104.26) * mm});
            skLineSegment(sketch, "E22.top", {"start": v(-53.73, 102.28) * mm, "end": v(-51.28, 102.28) * mm});
            skLineSegment(sketch, "E22.left", {"start": v(-53.73, 104.26) * mm, "end": v(-53.73, 102.28) * mm});
            skLineSegment(sketch, "E22.right", {"start": v(-51.28, 104.26) * mm, "end": v(-51.28, 102.28) * mm});
            skLineSegment(sketch, "E23.bottom", {"start": v(-64.01, 97.74) * mm, "end": v(-62.4, 97.74) * mm});
            skLineSegment(sketch, "E23.top", {"start": v(-64.01, 96.07) * mm, "end": v(-62.4, 96.07) * mm});
            skLineSegment(sketch, "E23.left", {"start": v(-64.01, 97.74) * mm, "end": v(-64.01, 96.07) * mm});
            skLineSegment(sketch, "E23.right", {"start": v(-62.4, 97.74) * mm, "end": v(-62.4, 96.07) * mm});
            skLineSegment(sketch, "E24.bottom", {"start": v(-117.18, 7.63) * mm, "end": v(-114.53, 7.63) * mm});
            skLineSegment(sketch, "E24.top", {"start": v(-117.18, 5.05) * mm, "end": v(-114.53, 5.05) * mm});
            skLineSegment(sketch, "E24.left", {"start": v(-117.18, 7.63) * mm, "end": v(-117.18, 5.05) * mm});
            skLineSegment(sketch, "E24.right", {"start": v(-114.53, 7.63) * mm, "end": v(-114.53, 5.05) * mm});
            skLineSegment(sketch, "E25.bottom", {"start": v(-117.35, -4.81) * mm, "end": v(-114.28, -4.81) * mm});
            skLineSegment(sketch, "E25.top", {"start": v(-117.35, -7.39) * mm, "end": v(-114.28, -7.39) * mm});
            skLineSegment(sketch, "E25.left", {"start": v(-117.35, -4.81) * mm, "end": v(-117.35, -7.39) * mm});
            skLineSegment(sketch, "E25.right", {"start": v(-114.28, -4.81) * mm, "end": v(-114.28, -7.39) * mm});
            skLineSegment(sketch, "E26.bottom", {"start": v(-64.5, -96.1) * mm, "end": v(-62.4, -96.1) * mm});
            skLineSegment(sketch, "E26.top", {"start": v(-64.5, -98.13) * mm, "end": v(-62.4, -98.13) * mm});
            skLineSegment(sketch, "E26.left", {"start": v(-64.5, -96.1) * mm, "end": v(-64.5, -98.13) * mm});
            skLineSegment(sketch, "E26.right", {"start": v(-62.4, -96.1) * mm, "end": v(-62.4, -98.13) * mm});
            skLineSegment(sketch, "E27.bottom", {"start": v(-53.47, -102.44) * mm, "end": v(-51.12, -102.44) * mm});
            skLineSegment(sketch, "E27.top", {"start": v(-53.47, -104.79) * mm, "end": v(-51.12, -104.79) * mm});
            skLineSegment(sketch, "E27.left", {"start": v(-53.47, -102.44) * mm, "end": v(-53.47, -104.79) * mm});
            skLineSegment(sketch, "E27.right", {"start": v(-51.12, -102.44) * mm, "end": v(-51.12, -104.79) * mm});
            skLineSegment(sketch, "E28.bottom", {"start": v(50.59, -102.33) * mm, "end": v(53.97, -102.33) * mm});
            skLineSegment(sketch, "E28.top", {"start": v(50.59, -104.52) * mm, "end": v(53.97, -104.52) * mm});
            skLineSegment(sketch, "E28.left", {"start": v(50.59, -102.33) * mm, "end": v(50.59, -104.52) * mm});
            skLineSegment(sketch, "E28.right", {"start": v(53.97, -102.33) * mm, "end": v(53.97, -104.52) * mm});
            skLineSegment(sketch, "E29.bottom", {"start": v(114.49, 7.9) * mm, "end": v(117.42, 7.9) * mm});
            skLineSegment(sketch, "E29.top", {"start": v(114.49, 4.9) * mm, "end": v(117.42, 4.9) * mm});
            skLineSegment(sketch, "E29.left", {"start": v(114.49, 7.9) * mm, "end": v(114.49, 4.9) * mm});
            skLineSegment(sketch, "E29.right", {"start": v(117.42, 7.9) * mm, "end": v(117.42, 4.9) * mm});
            skSolve(sketch);
        }
        {
            var Q0;
            Q0=qSketchRegion(id+"F6",true);
            var Q1;
            Q1=makeQuery(id+"F5.boolean.opBoolean","MERGE",FACE,{"derivedFrom":[makeQuery(id+"F1.opExtrude","CAP_FACE",FACE,{"disambiguationData":[OSD([sQuery(id+"F0.wireOp",EDGE,"E0")])],"isStart":true}),makeQuery(id+"F5.opExtrude","CAP_FACE",FACE,{"disambiguationData":[OSD([sQuery(id+"F4.wireOp",EDGE,"gzat5XN6-aFc3-cK17-7gGf-ptE3Ki8R4cpB"),sQuery(id+"F4.wireOp",EDGE,"E16")])],"isStart":false})]});
            extrude(context, id + "F7", {"entities" : qUnion([Q0]), "operationType" : NewBodyOperationType.ADD, "endBound" : BoundingType.UP_TO_SURFACE, "oppositeDirection" : true, "depth" : 25.4 * mm, "endBoundEntityFace" : qUnion([Q1]), "offsetDistance" : 25.4 * mm});
        }
    });
